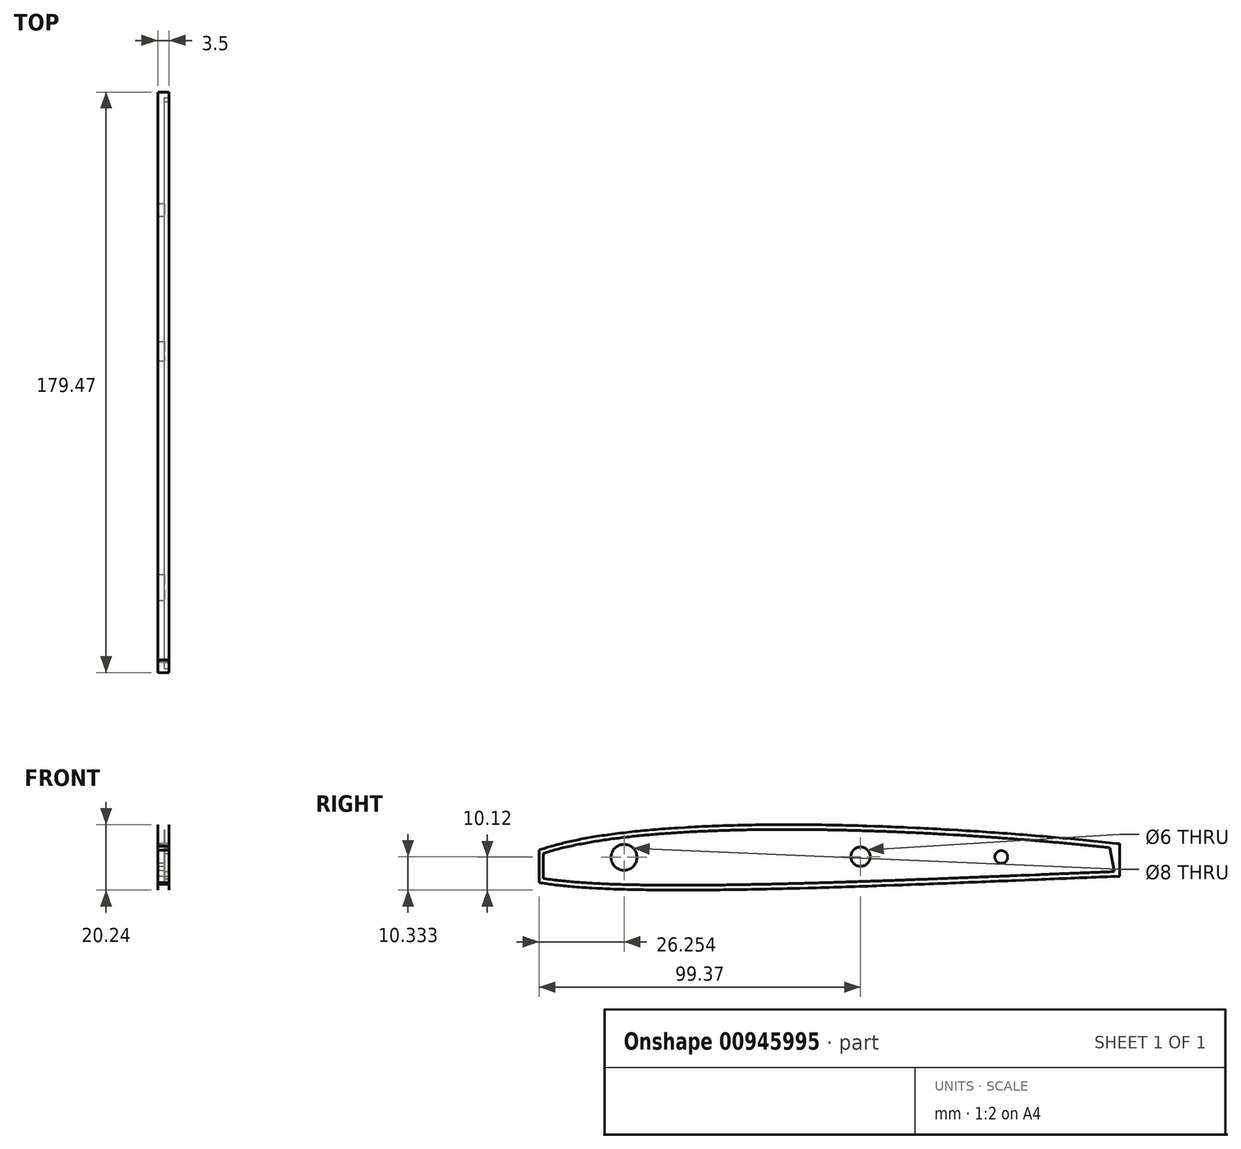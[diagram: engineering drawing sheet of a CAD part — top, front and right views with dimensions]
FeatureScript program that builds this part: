
annotation { "Feature Type Name" : "Feature", "Feature Type Description" : "" }
export const myFeature = defineFeature(function(context is Context, id is Id, definition is map)
    precondition{}
    {
        {
            var Q0;
            Q0=qCreatedBy(makeId("Right.planeOp"),FACE);
            var sketch = newSketch(context, id + "F0", { "sketchPlane" : qUnion([Q0])});
            skLineSegment(sketch, "E0", {"start": v(127, -3.95) * mm, "end": v(126.92, -3.95) * mm});
            skLineSegment(sketch, "E1", {"start": v(126.92, -3.95) * mm, "end": v(126.83, -3.94) * mm});
            skLineSegment(sketch, "E2", {"start": v(126.83, -3.94) * mm, "end": v(126.75, -3.93) * mm});
            skLineSegment(sketch, "E3", {"start": v(126.75, -3.93) * mm, "end": v(126.67, -3.93) * mm});
            skLineSegment(sketch, "E4", {"start": v(126.67, -3.93) * mm, "end": v(126.59, -3.92) * mm});
            skLineSegment(sketch, "E5", {"start": v(126.59, -3.92) * mm, "end": v(126.5, -3.91) * mm});
            skLineSegment(sketch, "E6", {"start": v(126.5, -3.91) * mm, "end": v(126.42, -3.9) * mm});
            skLineSegment(sketch, "E7", {"start": v(126.42, -3.9) * mm, "end": v(126.34, -3.9) * mm});
            skLineSegment(sketch, "E8", {"start": v(126.34, -3.9) * mm, "end": v(126.26, -3.9) * mm});
            skLineSegment(sketch, "E9", {"start": v(126.26, -3.9) * mm, "end": v(125.93, -3.86) * mm});
            skLineSegment(sketch, "E10", {"start": v(125.93, -3.86) * mm, "end": v(125.69, -3.84) * mm});
            skLineSegment(sketch, "E11", {"start": v(125.69, -3.84) * mm, "end": v(125.44, -3.82) * mm});
            skLineSegment(sketch, "E12", {"start": v(125.44, -3.82) * mm, "end": v(125.2, -3.8) * mm});
            skLineSegment(sketch, "E13", {"start": v(125.2, -3.8) * mm, "end": v(124.96, -3.77) * mm});
            skLineSegment(sketch, "E14", {"start": v(124.96, -3.77) * mm, "end": v(124.71, -3.75) * mm});
            skLineSegment(sketch, "E15", {"start": v(124.71, -3.75) * mm, "end": v(124.47, -3.72) * mm});
            skLineSegment(sketch, "E16", {"start": v(124.47, -3.72) * mm, "end": v(124.23, -3.7) * mm});
            skLineSegment(sketch, "E17", {"start": v(124.23, -3.7) * mm, "end": v(123.98, -3.67) * mm});
            skLineSegment(sketch, "E18", {"start": v(123.98, -3.67) * mm, "end": v(123.35, -3.6) * mm});
            skLineSegment(sketch, "E19", {"start": v(123.35, -3.6) * mm, "end": v(122.95, -3.56) * mm});
            skLineSegment(sketch, "E20", {"start": v(122.95, -3.56) * mm, "end": v(122.56, -3.52) * mm});
            skLineSegment(sketch, "E21", {"start": v(122.56, -3.52) * mm, "end": v(122.17, -3.48) * mm});
            skLineSegment(sketch, "E22", {"start": v(122.17, -3.48) * mm, "end": v(121.77, -3.43) * mm});
            skLineSegment(sketch, "E23", {"start": v(121.77, -3.43) * mm, "end": v(121.38, -3.39) * mm});
            skLineSegment(sketch, "E24", {"start": v(121.38, -3.39) * mm, "end": v(120.98, -3.34) * mm});
            skLineSegment(sketch, "E25", {"start": v(120.98, -3.34) * mm, "end": v(120.59, -3.3) * mm});
            skLineSegment(sketch, "E26", {"start": v(120.59, -3.3) * mm, "end": v(120.2, -3.25) * mm});
            skLineSegment(sketch, "E27", {"start": v(120.2, -3.25) * mm, "end": v(119.8, -3.2) * mm});
            skLineSegment(sketch, "E28", {"start": v(119.8, -3.2) * mm, "end": v(119.27, -3.14) * mm});
            skLineSegment(sketch, "E29", {"start": v(119.27, -3.14) * mm, "end": v(118.73, -3.07) * mm});
            skLineSegment(sketch, "E30", {"start": v(118.73, -3.07) * mm, "end": v(118.2, -3) * mm});
            skLineSegment(sketch, "E31", {"start": v(118.2, -3) * mm, "end": v(117.67, -2.94) * mm});
            skLineSegment(sketch, "E32", {"start": v(117.67, -2.94) * mm, "end": v(117.13, -2.87) * mm});
            skLineSegment(sketch, "E33", {"start": v(117.13, -2.87) * mm, "end": v(116.6, -2.8) * mm});
            skLineSegment(sketch, "E34", {"start": v(116.6, -2.8) * mm, "end": v(116.07, -2.74) * mm});
            skLineSegment(sketch, "E35", {"start": v(116.07, -2.74) * mm, "end": v(115.53, -2.67) * mm});
            skLineSegment(sketch, "E36", {"start": v(115.53, -2.67) * mm, "end": v(115, -2.6) * mm});
            skLineSegment(sketch, "E37", {"start": v(115, -2.6) * mm, "end": v(114.47, -2.54) * mm});
            skLineSegment(sketch, "E38", {"start": v(114.47, -2.54) * mm, "end": v(113.8, -2.45) * mm});
            skLineSegment(sketch, "E39", {"start": v(113.8, -2.45) * mm, "end": v(113.14, -2.37) * mm});
            skLineSegment(sketch, "E40", {"start": v(113.14, -2.37) * mm, "end": v(112.48, -2.28) * mm});
            skLineSegment(sketch, "E41", {"start": v(112.48, -2.28) * mm, "end": v(111.82, -2.2) * mm});
            skLineSegment(sketch, "E42", {"start": v(111.82, -2.2) * mm, "end": v(111.16, -2.1) * mm});
            skLineSegment(sketch, "E43", {"start": v(111.16, -2.1) * mm, "end": v(110.5, -2.02) * mm});
            skLineSegment(sketch, "E44", {"start": v(110.5, -2.02) * mm, "end": v(109.84, -1.93) * mm});
            skLineSegment(sketch, "E45", {"start": v(109.84, -1.93) * mm, "end": v(109.17, -1.84) * mm});
            skLineSegment(sketch, "E46", {"start": v(109.17, -1.84) * mm, "end": v(108.51, -1.75) * mm});
            skLineSegment(sketch, "E47", {"start": v(108.51, -1.75) * mm, "end": v(107.07, -1.56) * mm});
            skLineSegment(sketch, "E48", {"start": v(107.07, -1.56) * mm, "end": v(106.3, -1.46) * mm});
            skLineSegment(sketch, "E49", {"start": v(106.3, -1.46) * mm, "end": v(105.52, -1.35) * mm});
            skLineSegment(sketch, "E50", {"start": v(105.52, -1.35) * mm, "end": v(104.74, -1.25) * mm});
            skLineSegment(sketch, "E51", {"start": v(104.74, -1.25) * mm, "end": v(103.96, -1.14) * mm});
            skLineSegment(sketch, "E52", {"start": v(103.96, -1.14) * mm, "end": v(103.19, -1.04) * mm});
            skLineSegment(sketch, "E53", {"start": v(103.19, -1.04) * mm, "end": v(102.4, -0.93) * mm});
            skLineSegment(sketch, "E54", {"start": v(102.4, -0.93) * mm, "end": v(101.63, -0.82) * mm});
            skLineSegment(sketch, "E55", {"start": v(101.63, -0.82) * mm, "end": v(100.85, -0.72) * mm});
            skLineSegment(sketch, "E56", {"start": v(100.85, -0.72) * mm, "end": v(100.08, -0.61) * mm});
            skLineSegment(sketch, "E57", {"start": v(100.08, -0.61) * mm, "end": v(99.2, -0.5) * mm});
            skLineSegment(sketch, "E58", {"start": v(99.2, -0.5) * mm, "end": v(98.32, -0.38) * mm});
            skLineSegment(sketch, "E59", {"start": v(98.32, -0.38) * mm, "end": v(97.43, -0.26) * mm});
            skLineSegment(sketch, "E60", {"start": v(97.43, -0.26) * mm, "end": v(96.55, -0.14) * mm});
            skLineSegment(sketch, "E61", {"start": v(96.55, -0.14) * mm, "end": v(95.67, -0.02) * mm});
            skLineSegment(sketch, "E62", {"start": v(95.67, -0.02) * mm, "end": v(94.8, 0.1) * mm});
            skLineSegment(sketch, "E63", {"start": v(94.8, 0.1) * mm, "end": v(93.91, 0.22) * mm});
            skLineSegment(sketch, "E64", {"start": v(93.91, 0.22) * mm, "end": v(93.03, 0.34) * mm});
            skLineSegment(sketch, "E65", {"start": v(93.03, 0.34) * mm, "end": v(92.15, 0.45) * mm});
            skLineSegment(sketch, "E66", {"start": v(92.15, 0.45) * mm, "end": v(90.3, 0.7) * mm});
            skLineSegment(sketch, "E67", {"start": v(90.3, 0.7) * mm, "end": v(89.33, 0.83) * mm});
            skLineSegment(sketch, "E68", {"start": v(89.33, 0.83) * mm, "end": v(88.36, 0.96) * mm});
            skLineSegment(sketch, "E69", {"start": v(88.36, 0.96) * mm, "end": v(87.39, 1.09) * mm});
            skLineSegment(sketch, "E70", {"start": v(87.39, 1.09) * mm, "end": v(86.42, 1.22) * mm});
            skLineSegment(sketch, "E71", {"start": v(86.42, 1.22) * mm, "end": v(85.44, 1.34) * mm});
            skLineSegment(sketch, "E72", {"start": v(85.44, 1.34) * mm, "end": v(84.47, 1.47) * mm});
            skLineSegment(sketch, "E73", {"start": v(84.47, 1.47) * mm, "end": v(83.5, 1.6) * mm});
            skLineSegment(sketch, "E74", {"start": v(83.5, 1.6) * mm, "end": v(82.53, 1.72) * mm});
            skLineSegment(sketch, "E75", {"start": v(82.53, 1.72) * mm, "end": v(81.56, 1.85) * mm});
            skLineSegment(sketch, "E76", {"start": v(81.56, 1.85) * mm, "end": v(80.51, 1.98) * mm});
            skLineSegment(sketch, "E77", {"start": v(80.51, 1.98) * mm, "end": v(79.46, 2.12) * mm});
            skLineSegment(sketch, "E78", {"start": v(79.46, 2.12) * mm, "end": v(78.41, 2.25) * mm});
            skLineSegment(sketch, "E79", {"start": v(78.41, 2.25) * mm, "end": v(77.36, 2.38) * mm});
            skLineSegment(sketch, "E80", {"start": v(77.36, 2.38) * mm, "end": v(76.31, 2.51) * mm});
            skLineSegment(sketch, "E81", {"start": v(76.31, 2.51) * mm, "end": v(75.26, 2.64) * mm});
            skLineSegment(sketch, "E82", {"start": v(75.26, 2.64) * mm, "end": v(74.21, 2.77) * mm});
            skLineSegment(sketch, "E83", {"start": v(74.21, 2.77) * mm, "end": v(73.17, 2.9) * mm});
            skLineSegment(sketch, "E84", {"start": v(73.17, 2.9) * mm, "end": v(72.12, 3.03) * mm});
            skLineSegment(sketch, "E85", {"start": v(72.12, 3.03) * mm, "end": v(69.95, 3.29) * mm});
            skLineSegment(sketch, "E86", {"start": v(69.95, 3.29) * mm, "end": v(68.83, 3.42) * mm});
            skLineSegment(sketch, "E87", {"start": v(68.83, 3.42) * mm, "end": v(67.72, 3.55) * mm});
            skLineSegment(sketch, "E88", {"start": v(67.72, 3.55) * mm, "end": v(66.6, 3.68) * mm});
            skLineSegment(sketch, "E89", {"start": v(66.6, 3.68) * mm, "end": v(65.48, 3.8) * mm});
            skLineSegment(sketch, "E90", {"start": v(65.48, 3.8) * mm, "end": v(64.37, 3.93) * mm});
            skLineSegment(sketch, "E91", {"start": v(64.37, 3.93) * mm, "end": v(63.25, 4.06) * mm});
            skLineSegment(sketch, "E92", {"start": v(63.25, 4.06) * mm, "end": v(62.14, 4.18) * mm});
            skLineSegment(sketch, "E93", {"start": v(62.14, 4.18) * mm, "end": v(61.02, 4.3) * mm});
            skLineSegment(sketch, "E94", {"start": v(61.02, 4.3) * mm, "end": v(58.73, 4.55) * mm});
            skLineSegment(sketch, "E95", {"start": v(58.73, 4.55) * mm, "end": v(57.56, 4.68) * mm});
            skLineSegment(sketch, "E96", {"start": v(57.56, 4.68) * mm, "end": v(56.38, 4.8) * mm});
            skLineSegment(sketch, "E97", {"start": v(56.38, 4.8) * mm, "end": v(55.21, 4.92) * mm});
            skLineSegment(sketch, "E98", {"start": v(55.21, 4.92) * mm, "end": v(54.04, 5.04) * mm});
            skLineSegment(sketch, "E99", {"start": v(54.04, 5.04) * mm, "end": v(52.86, 5.16) * mm});
            skLineSegment(sketch, "E100", {"start": v(52.86, 5.16) * mm, "end": v(51.7, 5.27) * mm});
            skLineSegment(sketch, "E101", {"start": v(51.7, 5.27) * mm, "end": v(50.52, 5.39) * mm});
            skLineSegment(sketch, "E102", {"start": v(50.52, 5.39) * mm, "end": v(49.34, 5.5) * mm});
            skLineSegment(sketch, "E103", {"start": v(49.34, 5.5) * mm, "end": v(48.17, 5.61) * mm});
            skLineSegment(sketch, "E104", {"start": v(48.17, 5.61) * mm, "end": v(46.95, 5.73) * mm});
            skLineSegment(sketch, "E105", {"start": v(46.95, 5.73) * mm, "end": v(45.73, 5.84) * mm});
            skLineSegment(sketch, "E106", {"start": v(45.73, 5.84) * mm, "end": v(44.51, 5.95) * mm});
            skLineSegment(sketch, "E107", {"start": v(44.51, 5.95) * mm, "end": v(43.3, 6.06) * mm});
            skLineSegment(sketch, "E108", {"start": v(43.3, 6.06) * mm, "end": v(42.07, 6.17) * mm});
            skLineSegment(sketch, "E109", {"start": v(42.07, 6.17) * mm, "end": v(40.85, 6.28) * mm});
            skLineSegment(sketch, "E110", {"start": v(40.85, 6.28) * mm, "end": v(39.63, 6.39) * mm});
            skLineSegment(sketch, "E111", {"start": v(39.63, 6.39) * mm, "end": v(38.41, 6.5) * mm});
            skLineSegment(sketch, "E112", {"start": v(38.41, 6.5) * mm, "end": v(37.2, 6.6) * mm});
            skLineSegment(sketch, "E113", {"start": v(37.2, 6.6) * mm, "end": v(35.97, 6.7) * mm});
            skLineSegment(sketch, "E114", {"start": v(35.97, 6.7) * mm, "end": v(34.72, 6.8) * mm});
            skLineSegment(sketch, "E115", {"start": v(34.72, 6.8) * mm, "end": v(33.46, 6.9) * mm});
            skLineSegment(sketch, "E116", {"start": v(33.46, 6.9) * mm, "end": v(32.2, 7) * mm});
            skLineSegment(sketch, "E117", {"start": v(32.2, 7) * mm, "end": v(30.95, 7.1) * mm});
            skLineSegment(sketch, "E118", {"start": v(30.95, 7.1) * mm, "end": v(29.7, 7.2) * mm});
            skLineSegment(sketch, "E119", {"start": v(29.7, 7.2) * mm, "end": v(28.44, 7.29) * mm});
            skLineSegment(sketch, "E120", {"start": v(28.44, 7.29) * mm, "end": v(27.19, 7.38) * mm});
            skLineSegment(sketch, "E121", {"start": v(27.19, 7.38) * mm, "end": v(25.93, 7.47) * mm});
            skLineSegment(sketch, "E122", {"start": v(25.93, 7.47) * mm, "end": v(24.68, 7.56) * mm});
            skLineSegment(sketch, "E123", {"start": v(24.68, 7.56) * mm, "end": v(23.42, 7.65) * mm});
            skLineSegment(sketch, "E124", {"start": v(23.42, 7.65) * mm, "end": v(22.15, 7.74) * mm});
            skLineSegment(sketch, "E125", {"start": v(22.15, 7.74) * mm, "end": v(20.87, 7.83) * mm});
            skLineSegment(sketch, "E126", {"start": v(20.87, 7.83) * mm, "end": v(19.6, 7.91) * mm});
            skLineSegment(sketch, "E127", {"start": v(19.6, 7.91) * mm, "end": v(18.31, 8) * mm});
            skLineSegment(sketch, "E128", {"start": v(18.31, 8) * mm, "end": v(17.04, 8.08) * mm});
            skLineSegment(sketch, "E129", {"start": v(17.04, 8.08) * mm, "end": v(15.76, 8.16) * mm});
            skLineSegment(sketch, "E130", {"start": v(15.76, 8.16) * mm, "end": v(14.48, 8.24) * mm});
            skLineSegment(sketch, "E131", {"start": v(14.48, 8.24) * mm, "end": v(13.2, 8.32) * mm});
            skLineSegment(sketch, "E132", {"start": v(13.2, 8.32) * mm, "end": v(11.93, 8.4) * mm});
            skLineSegment(sketch, "E133", {"start": v(11.93, 8.4) * mm, "end": v(9.37, 8.55) * mm});
            skLineSegment(sketch, "E134", {"start": v(9.37, 8.55) * mm, "end": v(8.08, 8.63) * mm});
            skLineSegment(sketch, "E135", {"start": v(8.08, 8.63) * mm, "end": v(6.8, 8.7) * mm});
            skLineSegment(sketch, "E136", {"start": v(6.8, 8.7) * mm, "end": v(5.51, 8.77) * mm});
            skLineSegment(sketch, "E137", {"start": v(5.51, 8.77) * mm, "end": v(4.23, 8.84) * mm});
            skLineSegment(sketch, "E138", {"start": v(4.23, 8.84) * mm, "end": v(2.94, 8.9) * mm});
            skLineSegment(sketch, "E139", {"start": v(2.94, 8.9) * mm, "end": v(1.66, 8.97) * mm});
            skLineSegment(sketch, "E140", {"start": v(1.66, 8.97) * mm, "end": v(0.38, 9.04) * mm});
            skLineSegment(sketch, "E141", {"start": v(0.38, 9.04) * mm, "end": v(-0.9, 9.1) * mm});
            skLineSegment(sketch, "E142", {"start": v(-0.9, 9.1) * mm, "end": v(-3.47, 9.22) * mm});
            skLineSegment(sketch, "E143", {"start": v(-3.47, 9.22) * mm, "end": v(-4.75, 9.28) * mm});
            skLineSegment(sketch, "E144", {"start": v(-4.75, 9.28) * mm, "end": v(-6.02, 9.33) * mm});
            skLineSegment(sketch, "E145", {"start": v(-6.02, 9.33) * mm, "end": v(-7.3, 9.39) * mm});
            skLineSegment(sketch, "E146", {"start": v(-7.3, 9.39) * mm, "end": v(-8.58, 9.44) * mm});
            skLineSegment(sketch, "E147", {"start": v(-8.58, 9.44) * mm, "end": v(-9.86, 9.5) * mm});
            skLineSegment(sketch, "E148", {"start": v(-9.86, 9.5) * mm, "end": v(-11.14, 9.54) * mm});
            skLineSegment(sketch, "E149", {"start": v(-11.14, 9.54) * mm, "end": v(-12.41, 9.59) * mm});
            skLineSegment(sketch, "E150", {"start": v(-12.41, 9.59) * mm, "end": v(-13.7, 9.63) * mm});
            skLineSegment(sketch, "E151", {"start": v(-13.7, 9.63) * mm, "end": v(-16.23, 9.71) * mm});
            skLineSegment(sketch, "E152", {"start": v(-16.23, 9.71) * mm, "end": v(-17.49, 9.75) * mm});
            skLineSegment(sketch, "E153", {"start": v(-17.49, 9.75) * mm, "end": v(-18.74, 9.79) * mm});
            skLineSegment(sketch, "E154", {"start": v(-18.74, 9.79) * mm, "end": v(-20, 9.82) * mm});
            skLineSegment(sketch, "E155", {"start": v(-20, 9.82) * mm, "end": v(-21.26, 9.86) * mm});
            skLineSegment(sketch, "E156", {"start": v(-21.26, 9.86) * mm, "end": v(-22.52, 9.89) * mm});
            skLineSegment(sketch, "E157", {"start": v(-22.52, 9.89) * mm, "end": v(-23.78, 9.92) * mm});
            skLineSegment(sketch, "E158", {"start": v(-23.78, 9.92) * mm, "end": v(-25.04, 9.94) * mm});
            skLineSegment(sketch, "E159", {"start": v(-25.04, 9.94) * mm, "end": v(-26.3, 9.97) * mm});
            skLineSegment(sketch, "E160", {"start": v(-26.3, 9.97) * mm, "end": v(-28.78, 10.01) * mm});
            skLineSegment(sketch, "E161", {"start": v(-28.78, 10.01) * mm, "end": v(-30.01, 10.03) * mm});
            skLineSegment(sketch, "E162", {"start": v(-30.01, 10.03) * mm, "end": v(-31.24, 10.05) * mm});
            skLineSegment(sketch, "E163", {"start": v(-31.24, 10.05) * mm, "end": v(-32.47, 10.07) * mm});
            skLineSegment(sketch, "E164", {"start": v(-32.47, 10.07) * mm, "end": v(-33.7, 10.08) * mm});
            skLineSegment(sketch, "E165", {"start": v(-33.7, 10.08) * mm, "end": v(-34.92, 10.1) * mm});
            skLineSegment(sketch, "E166", {"start": v(-34.92, 10.1) * mm, "end": v(-36.15, 10.1) * mm});
            skLineSegment(sketch, "E167", {"start": v(-36.15, 10.1) * mm, "end": v(-37.38, 10.1) * mm});
            skLineSegment(sketch, "E168", {"start": v(-37.38, 10.1) * mm, "end": v(-38.6, 10.11) * mm});
            skLineSegment(sketch, "E169", {"start": v(-38.6, 10.11) * mm, "end": v(-39.83, 10.12) * mm});
            skLineSegment(sketch, "E170", {"start": v(-39.83, 10.12) * mm, "end": v(-41.01, 10.12) * mm});
            skLineSegment(sketch, "E171", {"start": v(-41.01, 10.12) * mm, "end": v(-42.2, 10.12) * mm});
            skLineSegment(sketch, "E172", {"start": v(-42.2, 10.12) * mm, "end": v(-43.38, 10.11) * mm});
            skLineSegment(sketch, "E173", {"start": v(-43.38, 10.11) * mm, "end": v(-44.56, 10.1) * mm});
            skLineSegment(sketch, "E174", {"start": v(-44.56, 10.1) * mm, "end": v(-45.74, 10.1) * mm});
            skLineSegment(sketch, "E175", {"start": v(-45.74, 10.1) * mm, "end": v(-46.93, 10.09) * mm});
            skLineSegment(sketch, "E176", {"start": v(-46.93, 10.09) * mm, "end": v(-48.1, 10.08) * mm});
            skLineSegment(sketch, "E177", {"start": v(-48.1, 10.08) * mm, "end": v(-49.3, 10.06) * mm});
            skLineSegment(sketch, "E178", {"start": v(-49.3, 10.06) * mm, "end": v(-50.47, 10.05) * mm});
            skLineSegment(sketch, "E179", {"start": v(-50.47, 10.05) * mm, "end": v(-51.66, 10.03) * mm});
            skLineSegment(sketch, "E180", {"start": v(-51.66, 10.03) * mm, "end": v(-52.78, 10) * mm});
            skLineSegment(sketch, "E181", {"start": v(-52.78, 10) * mm, "end": v(-53.91, 9.98) * mm});
            skLineSegment(sketch, "E182", {"start": v(-53.91, 9.98) * mm, "end": v(-55.04, 9.96) * mm});
            skLineSegment(sketch, "E183", {"start": v(-55.04, 9.96) * mm, "end": v(-56.17, 9.93) * mm});
            skLineSegment(sketch, "E184", {"start": v(-56.17, 9.93) * mm, "end": v(-57.3, 9.9) * mm});
            skLineSegment(sketch, "E185", {"start": v(-57.3, 9.9) * mm, "end": v(-58.42, 9.87) * mm});
            skLineSegment(sketch, "E186", {"start": v(-58.42, 9.87) * mm, "end": v(-59.55, 9.83) * mm});
            skLineSegment(sketch, "E187", {"start": v(-59.55, 9.83) * mm, "end": v(-60.68, 9.8) * mm});
            skLineSegment(sketch, "E188", {"start": v(-60.68, 9.8) * mm, "end": v(-61.8, 9.76) * mm});
            skLineSegment(sketch, "E189", {"start": v(-61.8, 9.76) * mm, "end": v(-62.93, 9.72) * mm});
            skLineSegment(sketch, "E190", {"start": v(-62.93, 9.72) * mm, "end": v(-64, 9.68) * mm});
            skLineSegment(sketch, "E191", {"start": v(-64, 9.68) * mm, "end": v(-65.05, 9.63) * mm});
            skLineSegment(sketch, "E192", {"start": v(-65.05, 9.63) * mm, "end": v(-66.11, 9.59) * mm});
            skLineSegment(sketch, "E193", {"start": v(-66.11, 9.59) * mm, "end": v(-67.18, 9.54) * mm});
            skLineSegment(sketch, "E194", {"start": v(-67.18, 9.54) * mm, "end": v(-68.24, 9.49) * mm});
            skLineSegment(sketch, "E195", {"start": v(-68.24, 9.49) * mm, "end": v(-69.3, 9.43) * mm});
            skLineSegment(sketch, "E196", {"start": v(-69.3, 9.43) * mm, "end": v(-70.36, 9.38) * mm});
            skLineSegment(sketch, "E197", {"start": v(-70.36, 9.38) * mm, "end": v(-71.42, 9.32) * mm});
            skLineSegment(sketch, "E198", {"start": v(-71.42, 9.32) * mm, "end": v(-72.48, 9.26) * mm});
            skLineSegment(sketch, "E199", {"start": v(-72.48, 9.26) * mm, "end": v(-74.53, 9.13) * mm});
            skLineSegment(sketch, "E200", {"start": v(-74.53, 9.13) * mm, "end": v(-75.51, 9.07) * mm});
            skLineSegment(sketch, "E201", {"start": v(-75.51, 9.07) * mm, "end": v(-76.5, 9) * mm});
            skLineSegment(sketch, "E202", {"start": v(-76.5, 9) * mm, "end": v(-77.48, 8.93) * mm});
            skLineSegment(sketch, "E203", {"start": v(-77.48, 8.93) * mm, "end": v(-78.46, 8.86) * mm});
            skLineSegment(sketch, "E204", {"start": v(-78.46, 8.86) * mm, "end": v(-79.45, 8.79) * mm});
            skLineSegment(sketch, "E205", {"start": v(-79.45, 8.79) * mm, "end": v(-80.43, 8.71) * mm});
            skLineSegment(sketch, "E206", {"start": v(-80.43, 8.71) * mm, "end": v(-81.42, 8.63) * mm});
            skLineSegment(sketch, "E207", {"start": v(-81.42, 8.63) * mm, "end": v(-82.4, 8.55) * mm});
            skLineSegment(sketch, "E208", {"start": v(-82.4, 8.55) * mm, "end": v(-84.28, 8.38) * mm});
            skLineSegment(sketch, "E209", {"start": v(-84.28, 8.38) * mm, "end": v(-85.18, 8.3) * mm});
            skLineSegment(sketch, "E210", {"start": v(-85.18, 8.3) * mm, "end": v(-86.08, 8.2) * mm});
            skLineSegment(sketch, "E211", {"start": v(-86.08, 8.2) * mm, "end": v(-86.98, 8.11) * mm});
            skLineSegment(sketch, "E212", {"start": v(-86.98, 8.11) * mm, "end": v(-87.88, 8.02) * mm});
            skLineSegment(sketch, "E213", {"start": v(-87.88, 8.02) * mm, "end": v(-88.77, 7.92) * mm});
            skLineSegment(sketch, "E214", {"start": v(-88.77, 7.92) * mm, "end": v(-89.67, 7.82) * mm});
            skLineSegment(sketch, "E215", {"start": v(-89.67, 7.82) * mm, "end": v(-90.57, 7.72) * mm});
            skLineSegment(sketch, "E216", {"start": v(-90.57, 7.72) * mm, "end": v(-91.47, 7.61) * mm});
            skLineSegment(sketch, "E217", {"start": v(-91.47, 7.61) * mm, "end": v(-92.37, 7.5) * mm});
            skLineSegment(sketch, "E218", {"start": v(-92.37, 7.5) * mm, "end": v(-93.17, 7.4) * mm});
            skLineSegment(sketch, "E219", {"start": v(-93.17, 7.4) * mm, "end": v(-93.98, 7.3) * mm});
            skLineSegment(sketch, "E220", {"start": v(-93.98, 7.3) * mm, "end": v(-94.78, 7.2) * mm});
            skLineSegment(sketch, "E221", {"start": v(-94.78, 7.2) * mm, "end": v(-95.59, 7.08) * mm});
            skLineSegment(sketch, "E222", {"start": v(-95.59, 7.08) * mm, "end": v(-96.4, 6.97) * mm});
            skLineSegment(sketch, "E223", {"start": v(-96.4, 6.97) * mm, "end": v(-97.2, 6.85) * mm});
            skLineSegment(sketch, "E224", {"start": v(-97.2, 6.85) * mm, "end": v(-98, 6.73) * mm});
            skLineSegment(sketch, "E225", {"start": v(-98, 6.73) * mm, "end": v(-98.81, 6.6) * mm});
            skLineSegment(sketch, "E226", {"start": v(-98.81, 6.6) * mm, "end": v(-99.62, 6.48) * mm});
            skLineSegment(sketch, "E227", {"start": v(-99.62, 6.48) * mm, "end": v(-100.42, 6.35) * mm});
            skLineSegment(sketch, "E228", {"start": v(-100.42, 6.35) * mm, "end": v(-101.13, 6.23) * mm});
            skLineSegment(sketch, "E229", {"start": v(-101.13, 6.23) * mm, "end": v(-101.83, 6.1) * mm});
            skLineSegment(sketch, "E230", {"start": v(-101.83, 6.1) * mm, "end": v(-102.54, 5.98) * mm});
            skLineSegment(sketch, "E231", {"start": v(-102.54, 5.98) * mm, "end": v(-103.25, 5.85) * mm});
            skLineSegment(sketch, "E232", {"start": v(-103.25, 5.85) * mm, "end": v(-103.95, 5.72) * mm});
            skLineSegment(sketch, "E233", {"start": v(-103.95, 5.72) * mm, "end": v(-104.66, 5.59) * mm});
            skLineSegment(sketch, "E234", {"start": v(-104.66, 5.59) * mm, "end": v(-105.37, 5.45) * mm});
            skLineSegment(sketch, "E235", {"start": v(-105.37, 5.45) * mm, "end": v(-106.07, 5.3) * mm});
            skLineSegment(sketch, "E236", {"start": v(-106.07, 5.3) * mm, "end": v(-106.78, 5.16) * mm});
            skLineSegment(sketch, "E237", {"start": v(-106.78, 5.16) * mm, "end": v(-108.09, 4.87) * mm});
            skLineSegment(sketch, "E238", {"start": v(-108.09, 4.87) * mm, "end": v(-108.69, 4.73) * mm});
            skLineSegment(sketch, "E239", {"start": v(-108.69, 4.73) * mm, "end": v(-109.3, 4.6) * mm});
            skLineSegment(sketch, "E240", {"start": v(-109.3, 4.6) * mm, "end": v(-109.9, 4.45) * mm});
            skLineSegment(sketch, "E241", {"start": v(-109.9, 4.45) * mm, "end": v(-110.5, 4.3) * mm});
            skLineSegment(sketch, "E242", {"start": v(-110.5, 4.3) * mm, "end": v(-111.1, 4.15) * mm});
            skLineSegment(sketch, "E243", {"start": v(-111.1, 4.15) * mm, "end": v(-111.7, 4) * mm});
            skLineSegment(sketch, "E244", {"start": v(-111.7, 4) * mm, "end": v(-112.3, 3.84) * mm});
            skLineSegment(sketch, "E245", {"start": v(-112.3, 3.84) * mm, "end": v(-112.9, 3.67) * mm});
            skLineSegment(sketch, "E246", {"start": v(-112.9, 3.67) * mm, "end": v(-113.5, 3.5) * mm});
            skLineSegment(sketch, "E247", {"start": v(-113.5, 3.5) * mm, "end": v(-114, 3.36) * mm});
            skLineSegment(sketch, "E248", {"start": v(-114, 3.36) * mm, "end": v(-114.5, 3.21) * mm});
            skLineSegment(sketch, "E249", {"start": v(-114.5, 3.21) * mm, "end": v(-115, 3.06) * mm});
            skLineSegment(sketch, "E250", {"start": v(-115, 3.06) * mm, "end": v(-115.49, 2.9) * mm});
            skLineSegment(sketch, "E251", {"start": v(-115.49, 2.9) * mm, "end": v(-115.98, 2.74) * mm});
            skLineSegment(sketch, "E252", {"start": v(-115.98, 2.74) * mm, "end": v(-116.48, 2.58) * mm});
            skLineSegment(sketch, "E253", {"start": v(-116.48, 2.58) * mm, "end": v(-116.97, 2.41) * mm});
            skLineSegment(sketch, "E254", {"start": v(-116.97, 2.41) * mm, "end": v(-117.47, 2.24) * mm});
            skLineSegment(sketch, "E255", {"start": v(-117.47, 2.24) * mm, "end": v(-117.96, 2.06) * mm});
            skLineSegment(sketch, "E256", {"start": v(-117.96, 2.06) * mm, "end": v(-118.46, 1.88) * mm});
            skLineSegment(sketch, "E257", {"start": v(-118.46, 1.88) * mm, "end": v(-118.9, 1.71) * mm});
            skLineSegment(sketch, "E258", {"start": v(-118.9, 1.71) * mm, "end": v(-119.32, 1.54) * mm});
            skLineSegment(sketch, "E259", {"start": v(-119.32, 1.54) * mm, "end": v(-119.74, 1.37) * mm});
            skLineSegment(sketch, "E260", {"start": v(-119.74, 1.37) * mm, "end": v(-120.14, 1.2) * mm});
            skLineSegment(sketch, "E261", {"start": v(-120.14, 1.2) * mm, "end": v(-120.53, 1.03) * mm});
            skLineSegment(sketch, "E262", {"start": v(-120.53, 1.03) * mm, "end": v(-120.9, 0.86) * mm});
            skLineSegment(sketch, "E263", {"start": v(-120.9, 0.86) * mm, "end": v(-121.27, 0.7) * mm});
            skLineSegment(sketch, "E264", {"start": v(-121.27, 0.7) * mm, "end": v(-121.63, 0.53) * mm});
            skLineSegment(sketch, "E265", {"start": v(-121.63, 0.53) * mm, "end": v(-121.97, 0.36) * mm});
            skLineSegment(sketch, "E266", {"start": v(-121.97, 0.36) * mm, "end": v(-122.3, 0.19) * mm});
            skLineSegment(sketch, "E267", {"start": v(-122.3, 0.19) * mm, "end": v(-122.62, 0.02) * mm});
            skLineSegment(sketch, "E268", {"start": v(-122.62, 0.02) * mm, "end": v(-122.93, -0.15) * mm});
            skLineSegment(sketch, "E269", {"start": v(-122.93, -0.15) * mm, "end": v(-123.23, -0.32) * mm});
            skLineSegment(sketch, "E270", {"start": v(-123.23, -0.32) * mm, "end": v(-123.52, -0.49) * mm});
            skLineSegment(sketch, "E271", {"start": v(-123.52, -0.49) * mm, "end": v(-123.8, -0.66) * mm});
            skLineSegment(sketch, "E272", {"start": v(-123.8, -0.66) * mm, "end": v(-124.06, -0.83) * mm});
            skLineSegment(sketch, "E273", {"start": v(-124.06, -0.83) * mm, "end": v(-124.32, -1) * mm});
            skLineSegment(sketch, "E274", {"start": v(-124.32, -1) * mm, "end": v(-124.57, -1.16) * mm});
            skLineSegment(sketch, "E275", {"start": v(-124.57, -1.16) * mm, "end": v(-124.81, -1.33) * mm});
            skLineSegment(sketch, "E276", {"start": v(-124.81, -1.33) * mm, "end": v(-125.04, -1.5) * mm});
            skLineSegment(sketch, "E277", {"start": v(-125.04, -1.5) * mm, "end": v(-125.24, -1.66) * mm});
            skLineSegment(sketch, "E278", {"start": v(-125.24, -1.66) * mm, "end": v(-125.43, -1.81) * mm});
            skLineSegment(sketch, "E279", {"start": v(-125.43, -1.81) * mm, "end": v(-125.6, -1.97) * mm});
            skLineSegment(sketch, "E280", {"start": v(-125.6, -1.97) * mm, "end": v(-125.78, -2.13) * mm});
            skLineSegment(sketch, "E281", {"start": v(-125.78, -2.13) * mm, "end": v(-125.95, -2.28) * mm});
            skLineSegment(sketch, "E282", {"start": v(-125.95, -2.28) * mm, "end": v(-126.1, -2.44) * mm});
            skLineSegment(sketch, "E283", {"start": v(-126.1, -2.44) * mm, "end": v(-126.26, -2.6) * mm});
            skLineSegment(sketch, "E284", {"start": v(-126.26, -2.6) * mm, "end": v(-126.4, -2.75) * mm});
            skLineSegment(sketch, "E285", {"start": v(-126.4, -2.75) * mm, "end": v(-126.52, -2.91) * mm});
            skLineSegment(sketch, "E286", {"start": v(-126.52, -2.91) * mm, "end": v(-126.64, -3.07) * mm});
            skLineSegment(sketch, "E287", {"start": v(-126.64, -3.07) * mm, "end": v(-126.7, -3.16) * mm});
            skLineSegment(sketch, "E288", {"start": v(-126.7, -3.16) * mm, "end": v(-126.76, -3.24) * mm});
            skLineSegment(sketch, "E289", {"start": v(-126.76, -3.24) * mm, "end": v(-126.81, -3.33) * mm});
            skLineSegment(sketch, "E290", {"start": v(-126.81, -3.33) * mm, "end": v(-126.86, -3.42) * mm});
            skLineSegment(sketch, "E291", {"start": v(-126.86, -3.42) * mm, "end": v(-126.9, -3.51) * mm});
            skLineSegment(sketch, "E292", {"start": v(-126.9, -3.51) * mm, "end": v(-126.93, -3.6) * mm});
            skLineSegment(sketch, "E293", {"start": v(-126.93, -3.6) * mm, "end": v(-126.96, -3.69) * mm});
            skLineSegment(sketch, "E294", {"start": v(-126.96, -3.69) * mm, "end": v(-126.98, -3.78) * mm});
            skLineSegment(sketch, "E295", {"start": v(-126.98, -3.78) * mm, "end": v(-127, -3.87) * mm});
            skLineSegment(sketch, "E296", {"start": v(-127, -3.87) * mm, "end": v(-127, -3.95) * mm});
            skLineSegment(sketch, "E297", {"start": v(-127, -3.95) * mm, "end": v(-127, -3.99) * mm});
            skLineSegment(sketch, "E298", {"start": v(-127, -3.99) * mm, "end": v(-127, -4.02) * mm});
            skLineSegment(sketch, "E299", {"start": v(-127, -4.02) * mm, "end": v(-127, -4.06) * mm});
            skLineSegment(sketch, "E300", {"start": v(-127, -4.06) * mm, "end": v(-127, -4.1) * mm});
            skLineSegment(sketch, "E301", {"start": v(-127, -4.1) * mm, "end": v(-126.99, -4.13) * mm});
            skLineSegment(sketch, "E302", {"start": v(-126.99, -4.13) * mm, "end": v(-126.98, -4.16) * mm});
            skLineSegment(sketch, "E303", {"start": v(-126.98, -4.16) * mm, "end": v(-126.97, -4.2) * mm});
            skLineSegment(sketch, "E304", {"start": v(-126.97, -4.2) * mm, "end": v(-126.96, -4.23) * mm});
            skLineSegment(sketch, "E305", {"start": v(-126.96, -4.23) * mm, "end": v(-126.95, -4.27) * mm});
            skLineSegment(sketch, "E306", {"start": v(-126.95, -4.27) * mm, "end": v(-126.94, -4.3) * mm});
            skLineSegment(sketch, "E307", {"start": v(-126.94, -4.3) * mm, "end": v(-126.89, -4.4) * mm});
            skLineSegment(sketch, "E308", {"start": v(-126.89, -4.4) * mm, "end": v(-126.82, -4.51) * mm});
            skLineSegment(sketch, "E309", {"start": v(-126.82, -4.51) * mm, "end": v(-126.74, -4.62) * mm});
            skLineSegment(sketch, "E310", {"start": v(-126.74, -4.62) * mm, "end": v(-126.65, -4.72) * mm});
            skLineSegment(sketch, "E311", {"start": v(-126.65, -4.72) * mm, "end": v(-126.54, -4.83) * mm});
            skLineSegment(sketch, "E312", {"start": v(-126.54, -4.83) * mm, "end": v(-126.41, -4.93) * mm});
            skLineSegment(sketch, "E313", {"start": v(-126.41, -4.93) * mm, "end": v(-126.27, -5.04) * mm});
            skLineSegment(sketch, "E314", {"start": v(-126.27, -5.04) * mm, "end": v(-126.12, -5.14) * mm});
            skLineSegment(sketch, "E315", {"start": v(-126.12, -5.14) * mm, "end": v(-125.95, -5.25) * mm});
            skLineSegment(sketch, "E316", {"start": v(-125.95, -5.25) * mm, "end": v(-125.77, -5.35) * mm});
            skLineSegment(sketch, "E317", {"start": v(-125.77, -5.35) * mm, "end": v(-125.58, -5.46) * mm});
            skLineSegment(sketch, "E318", {"start": v(-125.58, -5.46) * mm, "end": v(-125.37, -5.57) * mm});
            skLineSegment(sketch, "E319", {"start": v(-125.37, -5.57) * mm, "end": v(-125.15, -5.67) * mm});
            skLineSegment(sketch, "E320", {"start": v(-125.15, -5.67) * mm, "end": v(-124.92, -5.78) * mm});
            skLineSegment(sketch, "E321", {"start": v(-124.92, -5.78) * mm, "end": v(-124.67, -5.89) * mm});
            skLineSegment(sketch, "E322", {"start": v(-124.67, -5.89) * mm, "end": v(-124.4, -6) * mm});
            skLineSegment(sketch, "E323", {"start": v(-124.4, -6) * mm, "end": v(-124.13, -6.1) * mm});
            skLineSegment(sketch, "E324", {"start": v(-124.13, -6.1) * mm, "end": v(-123.84, -6.2) * mm});
            skLineSegment(sketch, "E325", {"start": v(-123.84, -6.2) * mm, "end": v(-123.53, -6.32) * mm});
            skLineSegment(sketch, "E326", {"start": v(-123.53, -6.32) * mm, "end": v(-123.21, -6.42) * mm});
            skLineSegment(sketch, "E327", {"start": v(-123.21, -6.42) * mm, "end": v(-122.9, -6.52) * mm});
            skLineSegment(sketch, "E328", {"start": v(-122.9, -6.52) * mm, "end": v(-122.57, -6.62) * mm});
            skLineSegment(sketch, "E329", {"start": v(-122.57, -6.62) * mm, "end": v(-122.22, -6.72) * mm});
            skLineSegment(sketch, "E330", {"start": v(-122.22, -6.72) * mm, "end": v(-121.86, -6.82) * mm});
            skLineSegment(sketch, "E331", {"start": v(-121.86, -6.82) * mm, "end": v(-121.49, -6.92) * mm});
            skLineSegment(sketch, "E332", {"start": v(-121.49, -6.92) * mm, "end": v(-121.1, -7.02) * mm});
            skLineSegment(sketch, "E333", {"start": v(-121.1, -7.02) * mm, "end": v(-120.7, -7.12) * mm});
            skLineSegment(sketch, "E334", {"start": v(-120.7, -7.12) * mm, "end": v(-120.27, -7.22) * mm});
            skLineSegment(sketch, "E335", {"start": v(-120.27, -7.22) * mm, "end": v(-119.82, -7.31) * mm});
            skLineSegment(sketch, "E336", {"start": v(-119.82, -7.31) * mm, "end": v(-119.36, -7.41) * mm});
            skLineSegment(sketch, "E337", {"start": v(-119.36, -7.41) * mm, "end": v(-118.85, -7.51) * mm});
            skLineSegment(sketch, "E338", {"start": v(-118.85, -7.51) * mm, "end": v(-118.34, -7.61) * mm});
            skLineSegment(sketch, "E339", {"start": v(-118.34, -7.61) * mm, "end": v(-117.83, -7.7) * mm});
            skLineSegment(sketch, "E340", {"start": v(-117.83, -7.7) * mm, "end": v(-117.33, -7.8) * mm});
            skLineSegment(sketch, "E341", {"start": v(-117.33, -7.8) * mm, "end": v(-116.82, -7.88) * mm});
            skLineSegment(sketch, "E342", {"start": v(-116.82, -7.88) * mm, "end": v(-116.3, -7.97) * mm});
            skLineSegment(sketch, "E343", {"start": v(-116.3, -7.97) * mm, "end": v(-115.8, -8.05) * mm});
            skLineSegment(sketch, "E344", {"start": v(-115.8, -8.05) * mm, "end": v(-115.29, -8.13) * mm});
            skLineSegment(sketch, "E345", {"start": v(-115.29, -8.13) * mm, "end": v(-114.78, -8.2) * mm});
            skLineSegment(sketch, "E346", {"start": v(-114.78, -8.2) * mm, "end": v(-114.27, -8.28) * mm});
            skLineSegment(sketch, "E347", {"start": v(-114.27, -8.28) * mm, "end": v(-113.64, -8.36) * mm});
            skLineSegment(sketch, "E348", {"start": v(-113.64, -8.36) * mm, "end": v(-113, -8.45) * mm});
            skLineSegment(sketch, "E349", {"start": v(-113, -8.45) * mm, "end": v(-112.38, -8.52) * mm});
            skLineSegment(sketch, "E350", {"start": v(-112.38, -8.52) * mm, "end": v(-111.75, -8.6) * mm});
            skLineSegment(sketch, "E351", {"start": v(-111.75, -8.6) * mm, "end": v(-111.12, -8.67) * mm});
            skLineSegment(sketch, "E352", {"start": v(-111.12, -8.67) * mm, "end": v(-110.49, -8.74) * mm});
            skLineSegment(sketch, "E353", {"start": v(-110.49, -8.74) * mm, "end": v(-109.86, -8.8) * mm});
            skLineSegment(sketch, "E354", {"start": v(-109.86, -8.8) * mm, "end": v(-109.23, -8.87) * mm});
            skLineSegment(sketch, "E355", {"start": v(-109.23, -8.87) * mm, "end": v(-108.6, -8.93) * mm});
            skLineSegment(sketch, "E356", {"start": v(-108.6, -8.93) * mm, "end": v(-107.97, -8.99) * mm});
            skLineSegment(sketch, "E357", {"start": v(-107.97, -8.99) * mm, "end": v(-107.22, -9.05) * mm});
            skLineSegment(sketch, "E358", {"start": v(-107.22, -9.05) * mm, "end": v(-106.48, -9.11) * mm});
            skLineSegment(sketch, "E359", {"start": v(-106.48, -9.11) * mm, "end": v(-105.73, -9.17) * mm});
            skLineSegment(sketch, "E360", {"start": v(-105.73, -9.17) * mm, "end": v(-104.98, -9.23) * mm});
            skLineSegment(sketch, "E361", {"start": v(-104.98, -9.23) * mm, "end": v(-104.24, -9.28) * mm});
            skLineSegment(sketch, "E362", {"start": v(-104.24, -9.28) * mm, "end": v(-103.5, -9.34) * mm});
            skLineSegment(sketch, "E363", {"start": v(-103.5, -9.34) * mm, "end": v(-102.74, -9.39) * mm});
            skLineSegment(sketch, "E364", {"start": v(-102.74, -9.39) * mm, "end": v(-102, -9.43) * mm});
            skLineSegment(sketch, "E365", {"start": v(-102, -9.43) * mm, "end": v(-101.25, -9.48) * mm});
            skLineSegment(sketch, "E366", {"start": v(-101.25, -9.48) * mm, "end": v(-99.65, -9.57) * mm});
            skLineSegment(sketch, "E367", {"start": v(-99.65, -9.57) * mm, "end": v(-98.8, -9.61) * mm});
            skLineSegment(sketch, "E368", {"start": v(-98.8, -9.61) * mm, "end": v(-97.93, -9.65) * mm});
            skLineSegment(sketch, "E369", {"start": v(-97.93, -9.65) * mm, "end": v(-97.08, -9.7) * mm});
            skLineSegment(sketch, "E370", {"start": v(-97.08, -9.7) * mm, "end": v(-96.22, -9.73) * mm});
            skLineSegment(sketch, "E371", {"start": v(-96.22, -9.73) * mm, "end": v(-95.36, -9.76) * mm});
            skLineSegment(sketch, "E372", {"start": v(-95.36, -9.76) * mm, "end": v(-94.5, -9.8) * mm});
            skLineSegment(sketch, "E373", {"start": v(-94.5, -9.8) * mm, "end": v(-93.65, -9.82) * mm});
            skLineSegment(sketch, "E374", {"start": v(-93.65, -9.82) * mm, "end": v(-92.8, -9.85) * mm});
            skLineSegment(sketch, "E375", {"start": v(-92.8, -9.85) * mm, "end": v(-91.93, -9.88) * mm});
            skLineSegment(sketch, "E376", {"start": v(-91.93, -9.88) * mm, "end": v(-90.97, -9.9) * mm});
            skLineSegment(sketch, "E377", {"start": v(-90.97, -9.9) * mm, "end": v(-90.01, -9.93) * mm});
            skLineSegment(sketch, "E378", {"start": v(-90.01, -9.93) * mm, "end": v(-89.05, -9.95) * mm});
            skLineSegment(sketch, "E379", {"start": v(-89.05, -9.95) * mm, "end": v(-88.09, -9.98) * mm});
            skLineSegment(sketch, "E380", {"start": v(-88.09, -9.98) * mm, "end": v(-87.13, -10) * mm});
            skLineSegment(sketch, "E381", {"start": v(-87.13, -10) * mm, "end": v(-86.17, -10.01) * mm});
            skLineSegment(sketch, "E382", {"start": v(-86.17, -10.01) * mm, "end": v(-85.2, -10.03) * mm});
            skLineSegment(sketch, "E383", {"start": v(-85.2, -10.03) * mm, "end": v(-84.25, -10.05) * mm});
            skLineSegment(sketch, "E384", {"start": v(-84.25, -10.05) * mm, "end": v(-83.28, -10.06) * mm});
            skLineSegment(sketch, "E385", {"start": v(-83.28, -10.06) * mm, "end": v(-81.27, -10.08) * mm});
            skLineSegment(sketch, "E386", {"start": v(-81.27, -10.08) * mm, "end": v(-80.21, -10.1) * mm});
            skLineSegment(sketch, "E387", {"start": v(-80.21, -10.1) * mm, "end": v(-79.16, -10.1) * mm});
            skLineSegment(sketch, "E388", {"start": v(-79.16, -10.1) * mm, "end": v(-78.1, -10.1) * mm});
            skLineSegment(sketch, "E389", {"start": v(-78.1, -10.1) * mm, "end": v(-77.05, -10.11) * mm});
            skLineSegment(sketch, "E390", {"start": v(-77.05, -10.11) * mm, "end": v(-76, -10.12) * mm});
            skLineSegment(sketch, "E391", {"start": v(-76, -10.12) * mm, "end": v(-74.94, -10.12) * mm});
            skLineSegment(sketch, "E392", {"start": v(-74.94, -10.12) * mm, "end": v(-73.89, -10.12) * mm});
            skLineSegment(sketch, "E393", {"start": v(-73.89, -10.12) * mm, "end": v(-72.83, -10.12) * mm});
            skLineSegment(sketch, "E394", {"start": v(-72.83, -10.12) * mm, "end": v(-71.78, -10.12) * mm});
            skLineSegment(sketch, "E395", {"start": v(-71.78, -10.12) * mm, "end": v(-70.64, -10.11) * mm});
            skLineSegment(sketch, "E396", {"start": v(-70.64, -10.11) * mm, "end": v(-69.5, -10.1) * mm});
            skLineSegment(sketch, "E397", {"start": v(-69.5, -10.1) * mm, "end": v(-68.36, -10.1) * mm});
            skLineSegment(sketch, "E398", {"start": v(-68.36, -10.1) * mm, "end": v(-67.22, -10.1) * mm});
            skLineSegment(sketch, "E399", {"start": v(-67.22, -10.1) * mm, "end": v(-66.08, -10.09) * mm});
            skLineSegment(sketch, "E400", {"start": v(-66.08, -10.09) * mm, "end": v(-64.94, -10.08) * mm});
            skLineSegment(sketch, "E401", {"start": v(-64.94, -10.08) * mm, "end": v(-63.8, -10.07) * mm});
            skLineSegment(sketch, "E402", {"start": v(-63.8, -10.07) * mm, "end": v(-62.67, -10.05) * mm});
            skLineSegment(sketch, "E403", {"start": v(-62.67, -10.05) * mm, "end": v(-61.53, -10.04) * mm});
            skLineSegment(sketch, "E404", {"start": v(-61.53, -10.04) * mm, "end": v(-60.4, -10.03) * mm});
            skLineSegment(sketch, "E405", {"start": v(-60.4, -10.03) * mm, "end": v(-59.18, -10.01) * mm});
            skLineSegment(sketch, "E406", {"start": v(-59.18, -10.01) * mm, "end": v(-57.97, -10) * mm});
            skLineSegment(sketch, "E407", {"start": v(-57.97, -10) * mm, "end": v(-56.76, -9.97) * mm});
            skLineSegment(sketch, "E408", {"start": v(-56.76, -9.97) * mm, "end": v(-55.55, -9.96) * mm});
            skLineSegment(sketch, "E409", {"start": v(-55.55, -9.96) * mm, "end": v(-54.34, -9.93) * mm});
            skLineSegment(sketch, "E410", {"start": v(-54.34, -9.93) * mm, "end": v(-53.14, -9.91) * mm});
            skLineSegment(sketch, "E411", {"start": v(-53.14, -9.91) * mm, "end": v(-51.93, -9.9) * mm});
            skLineSegment(sketch, "E412", {"start": v(-51.93, -9.9) * mm, "end": v(-50.72, -9.87) * mm});
            skLineSegment(sketch, "E413", {"start": v(-50.72, -9.87) * mm, "end": v(-49.5, -9.84) * mm});
            skLineSegment(sketch, "E414", {"start": v(-49.5, -9.84) * mm, "end": v(-47.03, -9.8) * mm});
            skLineSegment(sketch, "E415", {"start": v(-47.03, -9.8) * mm, "end": v(-45.76, -9.76) * mm});
            skLineSegment(sketch, "E416", {"start": v(-45.76, -9.76) * mm, "end": v(-44.5, -9.74) * mm});
            skLineSegment(sketch, "E417", {"start": v(-44.5, -9.74) * mm, "end": v(-43.23, -9.7) * mm});
            skLineSegment(sketch, "E418", {"start": v(-43.23, -9.7) * mm, "end": v(-41.96, -9.68) * mm});
            skLineSegment(sketch, "E419", {"start": v(-41.96, -9.68) * mm, "end": v(-40.7, -9.64) * mm});
            skLineSegment(sketch, "E420", {"start": v(-40.7, -9.64) * mm, "end": v(-39.43, -9.61) * mm});
            skLineSegment(sketch, "E421", {"start": v(-39.43, -9.61) * mm, "end": v(-38.16, -9.58) * mm});
            skLineSegment(sketch, "E422", {"start": v(-38.16, -9.58) * mm, "end": v(-36.9, -9.55) * mm});
            skLineSegment(sketch, "E423", {"start": v(-36.9, -9.55) * mm, "end": v(-34.31, -9.48) * mm});
            skLineSegment(sketch, "E424", {"start": v(-34.31, -9.48) * mm, "end": v(-33, -9.44) * mm});
            skLineSegment(sketch, "E425", {"start": v(-33, -9.44) * mm, "end": v(-31.7, -9.4) * mm});
            skLineSegment(sketch, "E426", {"start": v(-31.7, -9.4) * mm, "end": v(-30.38, -9.37) * mm});
            skLineSegment(sketch, "E427", {"start": v(-30.38, -9.37) * mm, "end": v(-29.07, -9.33) * mm});
            skLineSegment(sketch, "E428", {"start": v(-29.07, -9.33) * mm, "end": v(-27.76, -9.29) * mm});
            skLineSegment(sketch, "E429", {"start": v(-27.76, -9.29) * mm, "end": v(-26.45, -9.25) * mm});
            skLineSegment(sketch, "E430", {"start": v(-26.45, -9.25) * mm, "end": v(-25.13, -9.2) * mm});
            skLineSegment(sketch, "E431", {"start": v(-25.13, -9.2) * mm, "end": v(-23.82, -9.17) * mm});
            skLineSegment(sketch, "E432", {"start": v(-23.82, -9.17) * mm, "end": v(-22.51, -9.13) * mm});
            skLineSegment(sketch, "E433", {"start": v(-22.51, -9.13) * mm, "end": v(-21.17, -9.08) * mm});
            skLineSegment(sketch, "E434", {"start": v(-21.17, -9.08) * mm, "end": v(-19.83, -9.04) * mm});
            skLineSegment(sketch, "E435", {"start": v(-19.83, -9.04) * mm, "end": v(-18.49, -9) * mm});
            skLineSegment(sketch, "E436", {"start": v(-18.49, -9) * mm, "end": v(-17.15, -8.95) * mm});
            skLineSegment(sketch, "E437", {"start": v(-17.15, -8.95) * mm, "end": v(-15.8, -8.9) * mm});
            skLineSegment(sketch, "E438", {"start": v(-15.8, -8.9) * mm, "end": v(-14.47, -8.86) * mm});
            skLineSegment(sketch, "E439", {"start": v(-14.47, -8.86) * mm, "end": v(-13.13, -8.81) * mm});
            skLineSegment(sketch, "E440", {"start": v(-13.13, -8.81) * mm, "end": v(-11.79, -8.77) * mm});
            skLineSegment(sketch, "E441", {"start": v(-11.79, -8.77) * mm, "end": v(-10.44, -8.72) * mm});
            skLineSegment(sketch, "E442", {"start": v(-10.44, -8.72) * mm, "end": v(-7.75, -8.62) * mm});
            skLineSegment(sketch, "E443", {"start": v(-7.75, -8.62) * mm, "end": v(-6.4, -8.57) * mm});
            skLineSegment(sketch, "E444", {"start": v(-6.4, -8.57) * mm, "end": v(-5.04, -8.52) * mm});
            skLineSegment(sketch, "E445", {"start": v(-5.04, -8.52) * mm, "end": v(-3.68, -8.47) * mm});
            skLineSegment(sketch, "E446", {"start": v(-3.68, -8.47) * mm, "end": v(-2.33, -8.42) * mm});
            skLineSegment(sketch, "E447", {"start": v(-2.33, -8.42) * mm, "end": v(-0.97, -8.37) * mm});
            skLineSegment(sketch, "E448", {"start": v(-0.97, -8.37) * mm, "end": v(0.38, -8.32) * mm});
            skLineSegment(sketch, "E449", {"start": v(0.38, -8.32) * mm, "end": v(1.74, -8.27) * mm});
            skLineSegment(sketch, "E450", {"start": v(1.74, -8.27) * mm, "end": v(3.1, -8.22) * mm});
            skLineSegment(sketch, "E451", {"start": v(3.1, -8.22) * mm, "end": v(4.45, -8.17) * mm});
            skLineSegment(sketch, "E452", {"start": v(4.45, -8.17) * mm, "end": v(5.8, -8.12) * mm});
            skLineSegment(sketch, "E453", {"start": v(5.8, -8.12) * mm, "end": v(7.16, -8.06) * mm});
            skLineSegment(sketch, "E454", {"start": v(7.16, -8.06) * mm, "end": v(8.5, -8.01) * mm});
            skLineSegment(sketch, "E455", {"start": v(8.5, -8.01) * mm, "end": v(9.86, -7.96) * mm});
            skLineSegment(sketch, "E456", {"start": v(9.86, -7.96) * mm, "end": v(11.22, -7.9) * mm});
            skLineSegment(sketch, "E457", {"start": v(11.22, -7.9) * mm, "end": v(12.57, -7.85) * mm});
            skLineSegment(sketch, "E458", {"start": v(12.57, -7.85) * mm, "end": v(13.93, -7.8) * mm});
            skLineSegment(sketch, "E459", {"start": v(13.93, -7.8) * mm, "end": v(15.28, -7.75) * mm});
            skLineSegment(sketch, "E460", {"start": v(15.28, -7.75) * mm, "end": v(16.63, -7.7) * mm});
            skLineSegment(sketch, "E461", {"start": v(16.63, -7.7) * mm, "end": v(17.99, -7.64) * mm});
            skLineSegment(sketch, "E462", {"start": v(17.99, -7.64) * mm, "end": v(19.33, -7.58) * mm});
            skLineSegment(sketch, "E463", {"start": v(19.33, -7.58) * mm, "end": v(20.66, -7.53) * mm});
            skLineSegment(sketch, "E464", {"start": v(20.66, -7.53) * mm, "end": v(22, -7.47) * mm});
            skLineSegment(sketch, "E465", {"start": v(22, -7.47) * mm, "end": v(23.34, -7.42) * mm});
            skLineSegment(sketch, "E466", {"start": v(23.34, -7.42) * mm, "end": v(24.68, -7.37) * mm});
            skLineSegment(sketch, "E467", {"start": v(24.68, -7.37) * mm, "end": v(26.01, -7.31) * mm});
            skLineSegment(sketch, "E468", {"start": v(26.01, -7.31) * mm, "end": v(27.35, -7.26) * mm});
            skLineSegment(sketch, "E469", {"start": v(27.35, -7.26) * mm, "end": v(28.69, -7.2) * mm});
            skLineSegment(sketch, "E470", {"start": v(28.69, -7.2) * mm, "end": v(30.03, -7.15) * mm});
            skLineSegment(sketch, "E471", {"start": v(30.03, -7.15) * mm, "end": v(32.67, -7.04) * mm});
            skLineSegment(sketch, "E472", {"start": v(32.67, -7.04) * mm, "end": v(33.98, -6.98) * mm});
            skLineSegment(sketch, "E473", {"start": v(33.98, -6.98) * mm, "end": v(35.28, -6.93) * mm});
            skLineSegment(sketch, "E474", {"start": v(35.28, -6.93) * mm, "end": v(36.59, -6.88) * mm});
            skLineSegment(sketch, "E475", {"start": v(36.59, -6.88) * mm, "end": v(37.9, -6.82) * mm});
            skLineSegment(sketch, "E476", {"start": v(37.9, -6.82) * mm, "end": v(39.2, -6.77) * mm});
            skLineSegment(sketch, "E477", {"start": v(39.2, -6.77) * mm, "end": v(40.5, -6.72) * mm});
            skLineSegment(sketch, "E478", {"start": v(40.5, -6.72) * mm, "end": v(41.81, -6.66) * mm});
            skLineSegment(sketch, "E479", {"start": v(41.81, -6.66) * mm, "end": v(43.12, -6.6) * mm});
            skLineSegment(sketch, "E480", {"start": v(43.12, -6.6) * mm, "end": v(45.68, -6.5) * mm});
            skLineSegment(sketch, "E481", {"start": v(45.68, -6.5) * mm, "end": v(46.94, -6.45) * mm});
            skLineSegment(sketch, "E482", {"start": v(46.94, -6.45) * mm, "end": v(48.2, -6.4) * mm});
            skLineSegment(sketch, "E483", {"start": v(48.2, -6.4) * mm, "end": v(49.46, -6.35) * mm});
            skLineSegment(sketch, "E484", {"start": v(49.46, -6.35) * mm, "end": v(50.71, -6.3) * mm});
            skLineSegment(sketch, "E485", {"start": v(50.71, -6.3) * mm, "end": v(51.97, -6.25) * mm});
            skLineSegment(sketch, "E486", {"start": v(51.97, -6.25) * mm, "end": v(53.23, -6.2) * mm});
            skLineSegment(sketch, "E487", {"start": v(53.23, -6.2) * mm, "end": v(54.49, -6.14) * mm});
            skLineSegment(sketch, "E488", {"start": v(54.49, -6.14) * mm, "end": v(55.75, -6.1) * mm});
            skLineSegment(sketch, "E489", {"start": v(55.75, -6.1) * mm, "end": v(57, -6.04) * mm});
            skLineSegment(sketch, "E490", {"start": v(57, -6.04) * mm, "end": v(58.2, -6) * mm});
            skLineSegment(sketch, "E491", {"start": v(58.2, -6) * mm, "end": v(59.4, -5.95) * mm});
            skLineSegment(sketch, "E492", {"start": v(59.4, -5.95) * mm, "end": v(60.6, -5.9) * mm});
            skLineSegment(sketch, "E493", {"start": v(60.6, -5.9) * mm, "end": v(61.79, -5.85) * mm});
            skLineSegment(sketch, "E494", {"start": v(61.79, -5.85) * mm, "end": v(62.98, -5.8) * mm});
            skLineSegment(sketch, "E495", {"start": v(62.98, -5.8) * mm, "end": v(64.18, -5.75) * mm});
            skLineSegment(sketch, "E496", {"start": v(64.18, -5.75) * mm, "end": v(65.38, -5.7) * mm});
            skLineSegment(sketch, "E497", {"start": v(65.38, -5.7) * mm, "end": v(66.57, -5.66) * mm});
            skLineSegment(sketch, "E498", {"start": v(66.57, -5.66) * mm, "end": v(67.77, -5.61) * mm});
            skLineSegment(sketch, "E499", {"start": v(67.77, -5.61) * mm, "end": v(68.96, -5.57) * mm});
            skLineSegment(sketch, "E500", {"start": v(68.96, -5.57) * mm, "end": v(70.08, -5.52) * mm});
            skLineSegment(sketch, "E501", {"start": v(70.08, -5.52) * mm, "end": v(71.2, -5.48) * mm});
            skLineSegment(sketch, "E502", {"start": v(71.2, -5.48) * mm, "end": v(72.32, -5.44) * mm});
            skLineSegment(sketch, "E503", {"start": v(72.32, -5.44) * mm, "end": v(73.44, -5.4) * mm});
            skLineSegment(sketch, "E504", {"start": v(73.44, -5.4) * mm, "end": v(74.56, -5.35) * mm});
            skLineSegment(sketch, "E505", {"start": v(74.56, -5.35) * mm, "end": v(75.68, -5.31) * mm});
            skLineSegment(sketch, "E506", {"start": v(75.68, -5.31) * mm, "end": v(76.8, -5.27) * mm});
            skLineSegment(sketch, "E507", {"start": v(76.8, -5.27) * mm, "end": v(77.91, -5.23) * mm});
            skLineSegment(sketch, "E508", {"start": v(77.91, -5.23) * mm, "end": v(79.03, -5.19) * mm});
            skLineSegment(sketch, "E509", {"start": v(79.03, -5.19) * mm, "end": v(81.18, -5.1) * mm});
            skLineSegment(sketch, "E510", {"start": v(81.18, -5.1) * mm, "end": v(82.2, -5.07) * mm});
            skLineSegment(sketch, "E511", {"start": v(82.2, -5.07) * mm, "end": v(83.23, -5.03) * mm});
            skLineSegment(sketch, "E512", {"start": v(83.23, -5.03) * mm, "end": v(84.26, -5) * mm});
            skLineSegment(sketch, "E513", {"start": v(84.26, -5) * mm, "end": v(85.29, -4.96) * mm});
            skLineSegment(sketch, "E514", {"start": v(85.29, -4.96) * mm, "end": v(86.31, -4.93) * mm});
            skLineSegment(sketch, "E515", {"start": v(86.31, -4.93) * mm, "end": v(87.34, -4.9) * mm});
            skLineSegment(sketch, "E516", {"start": v(87.34, -4.9) * mm, "end": v(88.37, -4.86) * mm});
            skLineSegment(sketch, "E517", {"start": v(88.37, -4.86) * mm, "end": v(89.4, -4.82) * mm});
            skLineSegment(sketch, "E518", {"start": v(89.4, -4.82) * mm, "end": v(90.42, -4.79) * mm});
            skLineSegment(sketch, "E519", {"start": v(90.42, -4.79) * mm, "end": v(91.34, -4.76) * mm});
            skLineSegment(sketch, "E520", {"start": v(91.34, -4.76) * mm, "end": v(92.27, -4.73) * mm});
            skLineSegment(sketch, "E521", {"start": v(92.27, -4.73) * mm, "end": v(93.19, -4.7) * mm});
            skLineSegment(sketch, "E522", {"start": v(93.19, -4.7) * mm, "end": v(94.11, -4.67) * mm});
            skLineSegment(sketch, "E523", {"start": v(94.11, -4.67) * mm, "end": v(95.03, -4.64) * mm});
            skLineSegment(sketch, "E524", {"start": v(95.03, -4.64) * mm, "end": v(95.96, -4.61) * mm});
            skLineSegment(sketch, "E525", {"start": v(95.96, -4.61) * mm, "end": v(96.88, -4.59) * mm});
            skLineSegment(sketch, "E526", {"start": v(96.88, -4.59) * mm, "end": v(97.8, -4.56) * mm});
            skLineSegment(sketch, "E527", {"start": v(97.8, -4.56) * mm, "end": v(98.72, -4.53) * mm});
            skLineSegment(sketch, "E528", {"start": v(98.72, -4.53) * mm, "end": v(99.64, -4.5) * mm});
            skLineSegment(sketch, "E529", {"start": v(99.64, -4.5) * mm, "end": v(100.45, -4.48) * mm});
            skLineSegment(sketch, "E530", {"start": v(100.45, -4.48) * mm, "end": v(101.25, -4.46) * mm});
            skLineSegment(sketch, "E531", {"start": v(101.25, -4.46) * mm, "end": v(102.06, -4.44) * mm});
            skLineSegment(sketch, "E532", {"start": v(102.06, -4.44) * mm, "end": v(102.86, -4.42) * mm});
            skLineSegment(sketch, "E533", {"start": v(102.86, -4.42) * mm, "end": v(103.67, -4.4) * mm});
            skLineSegment(sketch, "E534", {"start": v(103.67, -4.4) * mm, "end": v(104.47, -4.37) * mm});
            skLineSegment(sketch, "E535", {"start": v(104.47, -4.37) * mm, "end": v(105.28, -4.35) * mm});
            skLineSegment(sketch, "E536", {"start": v(105.28, -4.35) * mm, "end": v(106.08, -4.33) * mm});
            skLineSegment(sketch, "E537", {"start": v(106.08, -4.33) * mm, "end": v(106.89, -4.31) * mm});
            skLineSegment(sketch, "E538", {"start": v(106.89, -4.31) * mm, "end": v(107.7, -4.3) * mm});
            skLineSegment(sketch, "E539", {"start": v(107.7, -4.3) * mm, "end": v(108.37, -4.28) * mm});
            skLineSegment(sketch, "E540", {"start": v(108.37, -4.28) * mm, "end": v(109.05, -4.26) * mm});
            skLineSegment(sketch, "E541", {"start": v(109.05, -4.26) * mm, "end": v(109.72, -4.25) * mm});
            skLineSegment(sketch, "E542", {"start": v(109.72, -4.25) * mm, "end": v(110.4, -4.23) * mm});
            skLineSegment(sketch, "E543", {"start": v(110.4, -4.23) * mm, "end": v(111.08, -4.22) * mm});
            skLineSegment(sketch, "E544", {"start": v(111.08, -4.22) * mm, "end": v(111.75, -4.2) * mm});
            skLineSegment(sketch, "E545", {"start": v(111.75, -4.2) * mm, "end": v(112.43, -4.19) * mm});
            skLineSegment(sketch, "E546", {"start": v(112.43, -4.19) * mm, "end": v(113.1, -4.17) * mm});
            skLineSegment(sketch, "E547", {"start": v(113.1, -4.17) * mm, "end": v(113.78, -4.16) * mm});
            skLineSegment(sketch, "E548", {"start": v(113.78, -4.16) * mm, "end": v(115, -4.14) * mm});
            skLineSegment(sketch, "E549", {"start": v(115, -4.14) * mm, "end": v(115.53, -4.13) * mm});
            skLineSegment(sketch, "E550", {"start": v(115.53, -4.13) * mm, "end": v(116.07, -4.12) * mm});
            skLineSegment(sketch, "E551", {"start": v(116.07, -4.12) * mm, "end": v(116.6, -4.1) * mm});
            skLineSegment(sketch, "E552", {"start": v(116.6, -4.1) * mm, "end": v(117.15, -4.1) * mm});
            skLineSegment(sketch, "E553", {"start": v(117.15, -4.1) * mm, "end": v(117.69, -4.09) * mm});
            skLineSegment(sketch, "E554", {"start": v(117.69, -4.09) * mm, "end": v(118.22, -4.08) * mm});
            skLineSegment(sketch, "E555", {"start": v(118.22, -4.08) * mm, "end": v(118.76, -4.07) * mm});
            skLineSegment(sketch, "E556", {"start": v(118.76, -4.07) * mm, "end": v(119.3, -4.06) * mm});
            skLineSegment(sketch, "E557", {"start": v(119.3, -4.06) * mm, "end": v(119.84, -4.05) * mm});
            skLineSegment(sketch, "E558", {"start": v(119.84, -4.05) * mm, "end": v(124, -3.99) * mm});
            skLineSegment(sketch, "E559", {"start": v(124, -3.99) * mm, "end": v(124.24, -3.99) * mm});
            skLineSegment(sketch, "E560", {"start": v(124.24, -3.99) * mm, "end": v(124.48, -3.98) * mm});
            skLineSegment(sketch, "E561", {"start": v(124.48, -3.98) * mm, "end": v(124.73, -3.98) * mm});
            skLineSegment(sketch, "E562", {"start": v(124.73, -3.98) * mm, "end": v(124.97, -3.98) * mm});
            skLineSegment(sketch, "E563", {"start": v(124.97, -3.98) * mm, "end": v(125.2, -3.97) * mm});
            skLineSegment(sketch, "E564", {"start": v(125.2, -3.97) * mm, "end": v(125.45, -3.97) * mm});
            skLineSegment(sketch, "E565", {"start": v(125.45, -3.97) * mm, "end": v(125.7, -3.97) * mm});
            skLineSegment(sketch, "E566", {"start": v(125.7, -3.97) * mm, "end": v(125.93, -3.96) * mm});
            skLineSegment(sketch, "E567", {"start": v(125.93, -3.96) * mm, "end": v(126.17, -3.96) * mm});
            skLineSegment(sketch, "E568", {"start": v(126.17, -3.96) * mm, "end": v(126.26, -3.96) * mm});
            skLineSegment(sketch, "E569", {"start": v(126.26, -3.96) * mm, "end": v(126.34, -3.96) * mm});
            skLineSegment(sketch, "E570", {"start": v(126.34, -3.96) * mm, "end": v(126.42, -3.96) * mm});
            skLineSegment(sketch, "E571", {"start": v(126.42, -3.96) * mm, "end": v(126.5, -3.96) * mm});
            skLineSegment(sketch, "E572", {"start": v(126.5, -3.96) * mm, "end": v(126.59, -3.96) * mm});
            skLineSegment(sketch, "E573", {"start": v(126.59, -3.96) * mm, "end": v(126.67, -3.96) * mm});
            skLineSegment(sketch, "E574", {"start": v(126.67, -3.96) * mm, "end": v(126.75, -3.96) * mm});
            skLineSegment(sketch, "E575", {"start": v(126.75, -3.96) * mm, "end": v(126.83, -3.96) * mm});
            skLineSegment(sketch, "E576", {"start": v(126.83, -3.96) * mm, "end": v(126.92, -3.95) * mm});
            skLineSegment(sketch, "E577", {"start": v(126.92, -3.95) * mm, "end": v(127, -3.95) * mm});
            skLineSegment(sketch, "E578", {"start": v(61.39, 2.74) * mm, "end": v(60.75, 2.81) * mm});
            skLineSegment(sketch, "E579", {"start": v(60.75, 2.81) * mm, "end": v(60.12, 2.88) * mm});
            skLineSegment(sketch, "E580", {"start": v(60.12, 2.88) * mm, "end": v(59.48, 2.95) * mm});
            skLineSegment(sketch, "E581", {"start": v(59.48, 2.95) * mm, "end": v(58.85, 3.02) * mm});
            skLineSegment(sketch, "E582", {"start": v(58.85, 3.02) * mm, "end": v(58.21, 3.08) * mm});
            skLineSegment(sketch, "E583", {"start": v(58.21, 3.08) * mm, "end": v(57.58, 3.15) * mm});
            skLineSegment(sketch, "E584", {"start": v(57.58, 3.15) * mm, "end": v(56.94, 3.22) * mm});
            skLineSegment(sketch, "E585", {"start": v(56.94, 3.22) * mm, "end": v(56.3, 3.28) * mm});
            skLineSegment(sketch, "E586", {"start": v(56.3, 3.28) * mm, "end": v(55.67, 3.35) * mm});
            skLineSegment(sketch, "E587", {"start": v(55.67, 3.35) * mm, "end": v(55.04, 3.42) * mm});
            skLineSegment(sketch, "E588", {"start": v(55.04, 3.42) * mm, "end": v(54.4, 3.48) * mm});
            skLineSegment(sketch, "E589", {"start": v(54.4, 3.48) * mm, "end": v(53.77, 3.55) * mm});
            skLineSegment(sketch, "E590", {"start": v(53.77, 3.55) * mm, "end": v(53.13, 3.6) * mm});
            skLineSegment(sketch, "E591", {"start": v(53.13, 3.6) * mm, "end": v(52.5, 3.67) * mm});
            skLineSegment(sketch, "E592", {"start": v(52.5, 3.67) * mm, "end": v(51.86, 3.74) * mm});
            skLineSegment(sketch, "E593", {"start": v(51.86, 3.74) * mm, "end": v(51.23, 3.8) * mm});
            skLineSegment(sketch, "E594", {"start": v(51.23, 3.8) * mm, "end": v(50.6, 3.86) * mm});
            skLineSegment(sketch, "E595", {"start": v(50.6, 3.86) * mm, "end": v(49.96, 3.92) * mm});
            skLineSegment(sketch, "E596", {"start": v(49.96, 3.92) * mm, "end": v(49.32, 3.98) * mm});
            skLineSegment(sketch, "E597", {"start": v(49.32, 3.98) * mm, "end": v(48.69, 4.05) * mm});
            skLineSegment(sketch, "E598", {"start": v(48.69, 4.05) * mm, "end": v(48.05, 4.1) * mm});
            skLineSegment(sketch, "E599", {"start": v(48.05, 4.1) * mm, "end": v(47.42, 4.17) * mm});
            skLineSegment(sketch, "E600", {"start": v(47.42, 4.17) * mm, "end": v(46.78, 4.23) * mm});
            skLineSegment(sketch, "E601", {"start": v(46.78, 4.23) * mm, "end": v(46.14, 4.28) * mm});
            skLineSegment(sketch, "E602", {"start": v(46.14, 4.28) * mm, "end": v(45.5, 4.34) * mm});
            skLineSegment(sketch, "E603", {"start": v(45.5, 4.34) * mm, "end": v(44.87, 4.4) * mm});
            skLineSegment(sketch, "E604", {"start": v(44.87, 4.4) * mm, "end": v(44.24, 4.46) * mm});
            skLineSegment(sketch, "E605", {"start": v(44.24, 4.46) * mm, "end": v(43.6, 4.52) * mm});
            skLineSegment(sketch, "E606", {"start": v(43.6, 4.52) * mm, "end": v(42.97, 4.57) * mm});
            skLineSegment(sketch, "E607", {"start": v(42.97, 4.57) * mm, "end": v(42.33, 4.63) * mm});
            skLineSegment(sketch, "E608", {"start": v(42.33, 4.63) * mm, "end": v(41.7, 4.69) * mm});
            skLineSegment(sketch, "E609", {"start": v(41.7, 4.69) * mm, "end": v(41.06, 4.74) * mm});
            skLineSegment(sketch, "E610", {"start": v(41.06, 4.74) * mm, "end": v(40.43, 4.8) * mm});
            skLineSegment(sketch, "E611", {"start": v(40.43, 4.8) * mm, "end": v(39.8, 4.85) * mm});
            skLineSegment(sketch, "E612", {"start": v(39.8, 4.85) * mm, "end": v(39.16, 4.9) * mm});
            skLineSegment(sketch, "E613", {"start": v(39.16, 4.9) * mm, "end": v(38.52, 4.96) * mm});
            skLineSegment(sketch, "E614", {"start": v(38.52, 4.96) * mm, "end": v(37.89, 5.02) * mm});
            skLineSegment(sketch, "E615", {"start": v(37.89, 5.02) * mm, "end": v(37.25, 5.07) * mm});
            skLineSegment(sketch, "E616", {"start": v(37.25, 5.07) * mm, "end": v(36.62, 5.12) * mm});
            skLineSegment(sketch, "E617", {"start": v(36.62, 5.12) * mm, "end": v(35.98, 5.18) * mm});
            skLineSegment(sketch, "E618", {"start": v(35.98, 5.18) * mm, "end": v(35.35, 5.23) * mm});
            skLineSegment(sketch, "E619", {"start": v(35.35, 5.23) * mm, "end": v(34.71, 5.28) * mm});
            skLineSegment(sketch, "E620", {"start": v(34.71, 5.28) * mm, "end": v(34.08, 5.33) * mm});
            skLineSegment(sketch, "E621", {"start": v(34.08, 5.33) * mm, "end": v(33.44, 5.38) * mm});
            skLineSegment(sketch, "E622", {"start": v(33.44, 5.38) * mm, "end": v(32.8, 5.43) * mm});
            skLineSegment(sketch, "E623", {"start": v(32.8, 5.43) * mm, "end": v(32.17, 5.48) * mm});
            skLineSegment(sketch, "E624", {"start": v(32.17, 5.48) * mm, "end": v(31.54, 5.53) * mm});
            skLineSegment(sketch, "E625", {"start": v(31.54, 5.53) * mm, "end": v(30.9, 5.58) * mm});
            skLineSegment(sketch, "E626", {"start": v(30.9, 5.58) * mm, "end": v(30.27, 5.63) * mm});
            skLineSegment(sketch, "E627", {"start": v(30.27, 5.63) * mm, "end": v(29.63, 5.68) * mm});
            skLineSegment(sketch, "E628", {"start": v(29.63, 5.68) * mm, "end": v(29, 5.73) * mm});
            skLineSegment(sketch, "E629", {"start": v(29, 5.73) * mm, "end": v(28.36, 5.78) * mm});
            skLineSegment(sketch, "E630", {"start": v(28.36, 5.78) * mm, "end": v(27.73, 5.82) * mm});
            skLineSegment(sketch, "E631", {"start": v(27.73, 5.82) * mm, "end": v(27.1, 5.87) * mm});
            skLineSegment(sketch, "E632", {"start": v(27.1, 5.87) * mm, "end": v(26.46, 5.92) * mm});
            skLineSegment(sketch, "E633", {"start": v(26.46, 5.92) * mm, "end": v(25.82, 5.96) * mm});
            skLineSegment(sketch, "E634", {"start": v(25.82, 5.96) * mm, "end": v(25.19, 6.01) * mm});
            skLineSegment(sketch, "E635", {"start": v(25.19, 6.01) * mm, "end": v(24.55, 6.06) * mm});
            skLineSegment(sketch, "E636", {"start": v(24.55, 6.06) * mm, "end": v(23.92, 6.1) * mm});
            skLineSegment(sketch, "E637", {"start": v(23.92, 6.1) * mm, "end": v(23.28, 6.15) * mm});
            skLineSegment(sketch, "E638", {"start": v(23.28, 6.15) * mm, "end": v(22.65, 6.2) * mm});
            skLineSegment(sketch, "E639", {"start": v(22.65, 6.2) * mm, "end": v(22, 6.24) * mm});
            skLineSegment(sketch, "E640", {"start": v(22, 6.24) * mm, "end": v(21.37, 6.28) * mm});
            skLineSegment(sketch, "E641", {"start": v(21.37, 6.28) * mm, "end": v(20.74, 6.32) * mm});
            skLineSegment(sketch, "E642", {"start": v(20.74, 6.32) * mm, "end": v(20.1, 6.37) * mm});
            skLineSegment(sketch, "E643", {"start": v(20.1, 6.37) * mm, "end": v(19.47, 6.4) * mm});
            skLineSegment(sketch, "E644", {"start": v(19.47, 6.4) * mm, "end": v(18.83, 6.45) * mm});
            skLineSegment(sketch, "E645", {"start": v(18.83, 6.45) * mm, "end": v(18.2, 6.5) * mm});
            skLineSegment(sketch, "E646", {"start": v(18.2, 6.5) * mm, "end": v(17.56, 6.53) * mm});
            skLineSegment(sketch, "E647", {"start": v(17.56, 6.53) * mm, "end": v(16.93, 6.58) * mm});
            skLineSegment(sketch, "E648", {"start": v(16.93, 6.58) * mm, "end": v(16.3, 6.62) * mm});
            skLineSegment(sketch, "E649", {"start": v(16.3, 6.62) * mm, "end": v(15.66, 6.66) * mm});
            skLineSegment(sketch, "E650", {"start": v(15.66, 6.66) * mm, "end": v(15.02, 6.7) * mm});
            skLineSegment(sketch, "E651", {"start": v(15.02, 6.7) * mm, "end": v(14.39, 6.74) * mm});
            skLineSegment(sketch, "E652", {"start": v(14.39, 6.74) * mm, "end": v(13.75, 6.78) * mm});
            skLineSegment(sketch, "E653", {"start": v(13.75, 6.78) * mm, "end": v(13.12, 6.82) * mm});
            skLineSegment(sketch, "E654", {"start": v(13.12, 6.82) * mm, "end": v(12.48, 6.85) * mm});
            skLineSegment(sketch, "E655", {"start": v(12.48, 6.85) * mm, "end": v(11.85, 6.9) * mm});
            skLineSegment(sketch, "E656", {"start": v(11.85, 6.9) * mm, "end": v(11.21, 6.93) * mm});
            skLineSegment(sketch, "E657", {"start": v(11.21, 6.93) * mm, "end": v(10.58, 6.97) * mm});
            skLineSegment(sketch, "E658", {"start": v(10.58, 6.97) * mm, "end": v(9.94, 7) * mm});
            skLineSegment(sketch, "E659", {"start": v(9.94, 7) * mm, "end": v(9.3, 7.04) * mm});
            skLineSegment(sketch, "E660", {"start": v(9.3, 7.04) * mm, "end": v(8.67, 7.08) * mm});
            skLineSegment(sketch, "E661", {"start": v(8.67, 7.08) * mm, "end": v(8.04, 7.12) * mm});
            skLineSegment(sketch, "E662", {"start": v(8.04, 7.12) * mm, "end": v(7.4, 7.15) * mm});
            skLineSegment(sketch, "E663", {"start": v(7.4, 7.15) * mm, "end": v(6.77, 7.19) * mm});
            skLineSegment(sketch, "E664", {"start": v(6.77, 7.19) * mm, "end": v(6.13, 7.22) * mm});
            skLineSegment(sketch, "E665", {"start": v(6.13, 7.22) * mm, "end": v(5.5, 7.26) * mm});
            skLineSegment(sketch, "E666", {"start": v(5.5, 7.26) * mm, "end": v(4.86, 7.3) * mm});
            skLineSegment(sketch, "E667", {"start": v(4.86, 7.3) * mm, "end": v(4.23, 7.33) * mm});
            skLineSegment(sketch, "E668", {"start": v(4.23, 7.33) * mm, "end": v(3.6, 7.36) * mm});
            skLineSegment(sketch, "E669", {"start": v(3.6, 7.36) * mm, "end": v(2.96, 7.4) * mm});
            skLineSegment(sketch, "E670", {"start": v(2.96, 7.4) * mm, "end": v(2.32, 7.43) * mm});
            skLineSegment(sketch, "E671", {"start": v(2.32, 7.43) * mm, "end": v(1.69, 7.46) * mm});
            skLineSegment(sketch, "E672", {"start": v(1.69, 7.46) * mm, "end": v(1.05, 7.5) * mm});
            skLineSegment(sketch, "E673", {"start": v(1.05, 7.5) * mm, "end": v(0.42, 7.53) * mm});
            skLineSegment(sketch, "E674", {"start": v(0.42, 7.53) * mm, "end": v(-0.22, 7.56) * mm});
            skLineSegment(sketch, "E675", {"start": v(-0.22, 7.56) * mm, "end": v(-0.85, 7.59) * mm});
            skLineSegment(sketch, "E676", {"start": v(-0.85, 7.59) * mm, "end": v(-1.49, 7.62) * mm});
            skLineSegment(sketch, "E677", {"start": v(-1.49, 7.62) * mm, "end": v(-2.12, 7.65) * mm});
            skLineSegment(sketch, "E678", {"start": v(-2.12, 7.65) * mm, "end": v(-2.76, 7.68) * mm});
            skLineSegment(sketch, "E679", {"start": v(-2.76, 7.68) * mm, "end": v(-3.4, 7.7) * mm});
            skLineSegment(sketch, "E680", {"start": v(-3.4, 7.7) * mm, "end": v(-4.03, 7.74) * mm});
            skLineSegment(sketch, "E681", {"start": v(-4.03, 7.74) * mm, "end": v(-4.67, 7.77) * mm});
            skLineSegment(sketch, "E682", {"start": v(-4.67, 7.77) * mm, "end": v(-5.3, 7.8) * mm});
            skLineSegment(sketch, "E683", {"start": v(-5.3, 7.8) * mm, "end": v(-5.94, 7.82) * mm});
            skLineSegment(sketch, "E684", {"start": v(-5.94, 7.82) * mm, "end": v(-6.57, 7.85) * mm});
            skLineSegment(sketch, "E685", {"start": v(-6.57, 7.85) * mm, "end": v(-7.2, 7.88) * mm});
            skLineSegment(sketch, "E686", {"start": v(-7.2, 7.88) * mm, "end": v(-7.84, 7.9) * mm});
            skLineSegment(sketch, "E687", {"start": v(-7.84, 7.9) * mm, "end": v(-8.48, 7.93) * mm});
            skLineSegment(sketch, "E688", {"start": v(-8.48, 7.93) * mm, "end": v(-9.11, 7.95) * mm});
            skLineSegment(sketch, "E689", {"start": v(-9.11, 7.95) * mm, "end": v(-9.75, 7.98) * mm});
            skLineSegment(sketch, "E690", {"start": v(-9.75, 7.98) * mm, "end": v(-10.38, 8) * mm});
            skLineSegment(sketch, "E691", {"start": v(-10.38, 8) * mm, "end": v(-11.02, 8.03) * mm});
            skLineSegment(sketch, "E692", {"start": v(-11.02, 8.03) * mm, "end": v(-11.65, 8.05) * mm});
            skLineSegment(sketch, "E693", {"start": v(-11.65, 8.05) * mm, "end": v(-12.29, 8.07) * mm});
            skLineSegment(sketch, "E694", {"start": v(-12.29, 8.07) * mm, "end": v(-12.92, 8.1) * mm});
            skLineSegment(sketch, "E695", {"start": v(-12.92, 8.1) * mm, "end": v(-13.56, 8.12) * mm});
            skLineSegment(sketch, "E696", {"start": v(-13.56, 8.12) * mm, "end": v(-14.2, 8.14) * mm});
            skLineSegment(sketch, "E697", {"start": v(-14.2, 8.14) * mm, "end": v(-14.83, 8.16) * mm});
            skLineSegment(sketch, "E698", {"start": v(-14.83, 8.16) * mm, "end": v(-15.46, 8.18) * mm});
            skLineSegment(sketch, "E699", {"start": v(-15.46, 8.18) * mm, "end": v(-16.1, 8.2) * mm});
            skLineSegment(sketch, "E700", {"start": v(-16.1, 8.2) * mm, "end": v(-16.73, 8.22) * mm});
            skLineSegment(sketch, "E701", {"start": v(-16.73, 8.22) * mm, "end": v(-17.37, 8.24) * mm});
            skLineSegment(sketch, "E702", {"start": v(-17.37, 8.24) * mm, "end": v(-18, 8.26) * mm});
            skLineSegment(sketch, "E703", {"start": v(-18, 8.26) * mm, "end": v(-18.64, 8.28) * mm});
            skLineSegment(sketch, "E704", {"start": v(-18.64, 8.28) * mm, "end": v(-19.27, 8.3) * mm});
            skLineSegment(sketch, "E705", {"start": v(-19.27, 8.3) * mm, "end": v(-19.9, 8.31) * mm});
            skLineSegment(sketch, "E706", {"start": v(-19.9, 8.31) * mm, "end": v(-20.54, 8.33) * mm});
            skLineSegment(sketch, "E707", {"start": v(-20.54, 8.33) * mm, "end": v(-21.18, 8.35) * mm});
            skLineSegment(sketch, "E708", {"start": v(-21.18, 8.35) * mm, "end": v(-21.81, 8.36) * mm});
            skLineSegment(sketch, "E709", {"start": v(-21.81, 8.36) * mm, "end": v(-22.45, 8.38) * mm});
            skLineSegment(sketch, "E710", {"start": v(-22.45, 8.38) * mm, "end": v(-23.08, 8.4) * mm});
            skLineSegment(sketch, "E711", {"start": v(-23.08, 8.4) * mm, "end": v(-23.72, 8.41) * mm});
            skLineSegment(sketch, "E712", {"start": v(-23.72, 8.41) * mm, "end": v(-24.36, 8.42) * mm});
            skLineSegment(sketch, "E713", {"start": v(-24.36, 8.42) * mm, "end": v(-25, 8.44) * mm});
            skLineSegment(sketch, "E714", {"start": v(-25, 8.44) * mm, "end": v(-25.63, 8.45) * mm});
            skLineSegment(sketch, "E715", {"start": v(-25.63, 8.45) * mm, "end": v(-26.26, 8.46) * mm});
            skLineSegment(sketch, "E716", {"start": v(-26.26, 8.46) * mm, "end": v(-26.9, 8.48) * mm});
            skLineSegment(sketch, "E717", {"start": v(-26.9, 8.48) * mm, "end": v(-27.53, 8.49) * mm});
            skLineSegment(sketch, "E718", {"start": v(-27.53, 8.49) * mm, "end": v(-28.17, 8.5) * mm});
            skLineSegment(sketch, "E719", {"start": v(-28.17, 8.5) * mm, "end": v(-28.8, 8.51) * mm});
            skLineSegment(sketch, "E720", {"start": v(-28.8, 8.51) * mm, "end": v(-29.44, 8.52) * mm});
            skLineSegment(sketch, "E721", {"start": v(-29.44, 8.52) * mm, "end": v(-30.07, 8.53) * mm});
            skLineSegment(sketch, "E722", {"start": v(-30.07, 8.53) * mm, "end": v(-30.7, 8.54) * mm});
            skLineSegment(sketch, "E723", {"start": v(-30.7, 8.54) * mm, "end": v(-31.34, 8.55) * mm});
            skLineSegment(sketch, "E724", {"start": v(-31.34, 8.55) * mm, "end": v(-31.98, 8.56) * mm});
            skLineSegment(sketch, "E725", {"start": v(-31.98, 8.56) * mm, "end": v(-32.61, 8.57) * mm});
            skLineSegment(sketch, "E726", {"start": v(-32.61, 8.57) * mm, "end": v(-33.25, 8.57) * mm});
            skLineSegment(sketch, "E727", {"start": v(-33.25, 8.57) * mm, "end": v(-33.88, 8.58) * mm});
            skLineSegment(sketch, "E728", {"start": v(-33.88, 8.58) * mm, "end": v(-34.52, 8.59) * mm});
            skLineSegment(sketch, "E729", {"start": v(-34.52, 8.59) * mm, "end": v(-35.15, 8.6) * mm});
            skLineSegment(sketch, "E730", {"start": v(-35.15, 8.6) * mm, "end": v(-35.79, 8.6) * mm});
            skLineSegment(sketch, "E731", {"start": v(-35.79, 8.6) * mm, "end": v(-36.42, 8.6) * mm});
            skLineSegment(sketch, "E732", {"start": v(-36.42, 8.6) * mm, "end": v(-37.06, 8.6) * mm});
            skLineSegment(sketch, "E733", {"start": v(-37.06, 8.6) * mm, "end": v(-37.7, 8.6) * mm});
            skLineSegment(sketch, "E734", {"start": v(-37.7, 8.6) * mm, "end": v(-38.33, 8.61) * mm});
            skLineSegment(sketch, "E735", {"start": v(-38.33, 8.61) * mm, "end": v(-38.96, 8.62) * mm});
            skLineSegment(sketch, "E736", {"start": v(-38.96, 8.62) * mm, "end": v(-39.6, 8.62) * mm});
            skLineSegment(sketch, "E737", {"start": v(-39.6, 8.62) * mm, "end": v(-40.23, 8.62) * mm});
            skLineSegment(sketch, "E738", {"start": v(-40.23, 8.62) * mm, "end": v(-40.87, 8.62) * mm});
            skLineSegment(sketch, "E739", {"start": v(-40.87, 8.62) * mm, "end": v(-41.5, 8.62) * mm});
            skLineSegment(sketch, "E740", {"start": v(-41.5, 8.62) * mm, "end": v(-42.14, 8.62) * mm});
            skLineSegment(sketch, "E741", {"start": v(-42.14, 8.62) * mm, "end": v(-42.77, 8.62) * mm});
            skLineSegment(sketch, "E742", {"start": v(-42.77, 8.62) * mm, "end": v(-43.4, 8.61) * mm});
            skLineSegment(sketch, "E743", {"start": v(-43.4, 8.61) * mm, "end": v(-44.04, 8.61) * mm});
            skLineSegment(sketch, "E744", {"start": v(-44.04, 8.61) * mm, "end": v(-44.68, 8.6) * mm});
            skLineSegment(sketch, "E745", {"start": v(-44.68, 8.6) * mm, "end": v(-45.31, 8.6) * mm});
            skLineSegment(sketch, "E746", {"start": v(-45.31, 8.6) * mm, "end": v(-45.95, 8.6) * mm});
            skLineSegment(sketch, "E747", {"start": v(-45.95, 8.6) * mm, "end": v(-46.58, 8.6) * mm});
            skLineSegment(sketch, "E748", {"start": v(-46.58, 8.6) * mm, "end": v(-47.22, 8.59) * mm});
            skLineSegment(sketch, "E749", {"start": v(-47.22, 8.59) * mm, "end": v(-47.85, 8.58) * mm});
            skLineSegment(sketch, "E750", {"start": v(-47.85, 8.58) * mm, "end": v(-48.49, 8.58) * mm});
            skLineSegment(sketch, "E751", {"start": v(-48.49, 8.58) * mm, "end": v(-49.12, 8.57) * mm});
            skLineSegment(sketch, "E752", {"start": v(-49.12, 8.57) * mm, "end": v(-49.76, 8.56) * mm});
            skLineSegment(sketch, "E753", {"start": v(-49.76, 8.56) * mm, "end": v(-50.4, 8.55) * mm});
            skLineSegment(sketch, "E754", {"start": v(-50.4, 8.55) * mm, "end": v(-51.03, 8.54) * mm});
            skLineSegment(sketch, "E755", {"start": v(-51.03, 8.54) * mm, "end": v(-51.66, 8.53) * mm});
            skLineSegment(sketch, "E756", {"start": v(-51.66, 8.53) * mm, "end": v(-52.3, 8.52) * mm});
            skLineSegment(sketch, "E757", {"start": v(-52.3, 8.52) * mm, "end": v(-52.93, 8.5) * mm});
            skLineSegment(sketch, "E758", {"start": v(-52.93, 8.5) * mm, "end": v(-53.57, 8.5) * mm});
            skLineSegment(sketch, "E759", {"start": v(-53.57, 8.5) * mm, "end": v(-54.2, 8.48) * mm});
            skLineSegment(sketch, "E760", {"start": v(-54.2, 8.48) * mm, "end": v(-54.84, 8.47) * mm});
            skLineSegment(sketch, "E761", {"start": v(-54.84, 8.47) * mm, "end": v(-55.47, 8.45) * mm});
            skLineSegment(sketch, "E762", {"start": v(-55.47, 8.45) * mm, "end": v(-56.1, 8.44) * mm});
            skLineSegment(sketch, "E763", {"start": v(-56.1, 8.44) * mm, "end": v(-56.74, 8.42) * mm});
            skLineSegment(sketch, "E764", {"start": v(-56.74, 8.42) * mm, "end": v(-57.37, 8.4) * mm});
            skLineSegment(sketch, "E765", {"start": v(-57.37, 8.4) * mm, "end": v(-58, 8.39) * mm});
            skLineSegment(sketch, "E766", {"start": v(-58, 8.39) * mm, "end": v(-58.64, 8.37) * mm});
            skLineSegment(sketch, "E767", {"start": v(-58.64, 8.37) * mm, "end": v(-59.28, 8.35) * mm});
            skLineSegment(sketch, "E768", {"start": v(-59.28, 8.35) * mm, "end": v(-59.91, 8.33) * mm});
            skLineSegment(sketch, "E769", {"start": v(-59.91, 8.33) * mm, "end": v(-60.55, 8.3) * mm});
            skLineSegment(sketch, "E770", {"start": v(-60.55, 8.3) * mm, "end": v(-61.18, 8.29) * mm});
            skLineSegment(sketch, "E771", {"start": v(-61.18, 8.29) * mm, "end": v(-61.82, 8.27) * mm});
            skLineSegment(sketch, "E772", {"start": v(-61.82, 8.27) * mm, "end": v(-62.45, 8.24) * mm});
            skLineSegment(sketch, "E773", {"start": v(-62.45, 8.24) * mm, "end": v(-63.09, 8.22) * mm});
            skLineSegment(sketch, "E774", {"start": v(-63.09, 8.22) * mm, "end": v(-63.72, 8.2) * mm});
            skLineSegment(sketch, "E775", {"start": v(-63.72, 8.2) * mm, "end": v(-64.36, 8.17) * mm});
            skLineSegment(sketch, "E776", {"start": v(-64.36, 8.17) * mm, "end": v(-65, 8.14) * mm});
            skLineSegment(sketch, "E777", {"start": v(-65, 8.14) * mm, "end": v(-65.63, 8.12) * mm});
            skLineSegment(sketch, "E778", {"start": v(-65.63, 8.12) * mm, "end": v(-66.26, 8.09) * mm});
            skLineSegment(sketch, "E779", {"start": v(-66.26, 8.09) * mm, "end": v(-66.9, 8.06) * mm});
            skLineSegment(sketch, "E780", {"start": v(-66.9, 8.06) * mm, "end": v(-67.53, 8.03) * mm});
            skLineSegment(sketch, "E781", {"start": v(-67.53, 8.03) * mm, "end": v(-68.16, 8) * mm});
            skLineSegment(sketch, "E782", {"start": v(-68.16, 8) * mm, "end": v(-68.8, 7.97) * mm});
            skLineSegment(sketch, "E783", {"start": v(-68.8, 7.97) * mm, "end": v(-69.43, 7.94) * mm});
            skLineSegment(sketch, "E784", {"start": v(-69.43, 7.94) * mm, "end": v(-70.07, 7.9) * mm});
            skLineSegment(sketch, "E785", {"start": v(-70.07, 7.9) * mm, "end": v(-70.7, 7.87) * mm});
            skLineSegment(sketch, "E786", {"start": v(-70.7, 7.87) * mm, "end": v(-71.34, 7.84) * mm});
            skLineSegment(sketch, "E787", {"start": v(-71.34, 7.84) * mm, "end": v(-71.97, 7.8) * mm});
            skLineSegment(sketch, "E788", {"start": v(-71.97, 7.8) * mm, "end": v(-72.6, 7.76) * mm});
            skLineSegment(sketch, "E789", {"start": v(-72.6, 7.76) * mm, "end": v(-73.24, 7.73) * mm});
            skLineSegment(sketch, "E790", {"start": v(-73.24, 7.73) * mm, "end": v(-73.88, 7.69) * mm});
            skLineSegment(sketch, "E791", {"start": v(-73.88, 7.69) * mm, "end": v(-74.51, 7.65) * mm});
            skLineSegment(sketch, "E792", {"start": v(-74.51, 7.65) * mm, "end": v(-75.15, 7.6) * mm});
            skLineSegment(sketch, "E793", {"start": v(-75.15, 7.6) * mm, "end": v(-75.78, 7.57) * mm});
            skLineSegment(sketch, "E794", {"start": v(-75.78, 7.57) * mm, "end": v(-76.42, 7.52) * mm});
            skLineSegment(sketch, "E795", {"start": v(-76.42, 7.52) * mm, "end": v(-77.05, 7.48) * mm});
            skLineSegment(sketch, "E796", {"start": v(-77.05, 7.48) * mm, "end": v(-77.68, 7.44) * mm});
            skLineSegment(sketch, "E797", {"start": v(-77.68, 7.44) * mm, "end": v(-78.32, 7.39) * mm});
            skLineSegment(sketch, "E798", {"start": v(-78.32, 7.39) * mm, "end": v(-78.95, 7.34) * mm});
            skLineSegment(sketch, "E799", {"start": v(-78.95, 7.34) * mm, "end": v(-79.59, 7.3) * mm});
            skLineSegment(sketch, "E800", {"start": v(-79.59, 7.3) * mm, "end": v(-80.22, 7.24) * mm});
            skLineSegment(sketch, "E801", {"start": v(-80.22, 7.24) * mm, "end": v(-80.86, 7.2) * mm});
            skLineSegment(sketch, "E802", {"start": v(-80.86, 7.2) * mm, "end": v(-81.5, 7.14) * mm});
            skLineSegment(sketch, "E803", {"start": v(-81.5, 7.14) * mm, "end": v(-82.13, 7.09) * mm});
            skLineSegment(sketch, "E804", {"start": v(-82.13, 7.09) * mm, "end": v(-82.76, 7.03) * mm});
            skLineSegment(sketch, "E805", {"start": v(-82.76, 7.03) * mm, "end": v(-83.4, 6.98) * mm});
            skLineSegment(sketch, "E806", {"start": v(-83.4, 6.98) * mm, "end": v(-84.03, 6.92) * mm});
            skLineSegment(sketch, "E807", {"start": v(-84.03, 6.92) * mm, "end": v(-84.67, 6.86) * mm});
            skLineSegment(sketch, "E808", {"start": v(-84.67, 6.86) * mm, "end": v(-85.3, 6.8) * mm});
            skLineSegment(sketch, "E809", {"start": v(-85.3, 6.8) * mm, "end": v(-85.93, 6.74) * mm});
            skLineSegment(sketch, "E810", {"start": v(-85.93, 6.74) * mm, "end": v(-86.57, 6.68) * mm});
            skLineSegment(sketch, "E811", {"start": v(-86.57, 6.68) * mm, "end": v(-87.2, 6.61) * mm});
            skLineSegment(sketch, "E812", {"start": v(-87.2, 6.61) * mm, "end": v(-87.84, 6.55) * mm});
            skLineSegment(sketch, "E813", {"start": v(-87.84, 6.55) * mm, "end": v(-88.47, 6.48) * mm});
            skLineSegment(sketch, "E814", {"start": v(-88.47, 6.48) * mm, "end": v(-89.1, 6.4) * mm});
            skLineSegment(sketch, "E815", {"start": v(-89.1, 6.4) * mm, "end": v(-89.74, 6.34) * mm});
            skLineSegment(sketch, "E816", {"start": v(-89.74, 6.34) * mm, "end": v(-90.38, 6.27) * mm});
            skLineSegment(sketch, "E817", {"start": v(-90.38, 6.27) * mm, "end": v(-91.01, 6.2) * mm});
            skLineSegment(sketch, "E818", {"start": v(-91.01, 6.2) * mm, "end": v(-91.64, 6.12) * mm});
            skLineSegment(sketch, "E819", {"start": v(-91.64, 6.12) * mm, "end": v(-92.28, 6.04) * mm});
            skLineSegment(sketch, "E820", {"start": v(-92.28, 6.04) * mm, "end": v(-92.91, 5.96) * mm});
            skLineSegment(sketch, "E821", {"start": v(-92.91, 5.96) * mm, "end": v(-93.55, 5.88) * mm});
            skLineSegment(sketch, "E822", {"start": v(-93.55, 5.88) * mm, "end": v(-94.18, 5.8) * mm});
            skLineSegment(sketch, "E823", {"start": v(-94.18, 5.8) * mm, "end": v(-94.82, 5.71) * mm});
            skLineSegment(sketch, "E824", {"start": v(-94.82, 5.71) * mm, "end": v(-95.45, 5.63) * mm});
            skLineSegment(sketch, "E825", {"start": v(-95.45, 5.63) * mm, "end": v(-96.09, 5.54) * mm});
            skLineSegment(sketch, "E826", {"start": v(-96.09, 5.54) * mm, "end": v(-96.72, 5.45) * mm});
            skLineSegment(sketch, "E827", {"start": v(-96.72, 5.45) * mm, "end": v(-97.35, 5.36) * mm});
            skLineSegment(sketch, "E828", {"start": v(-97.35, 5.36) * mm, "end": v(-97.99, 5.26) * mm});
            skLineSegment(sketch, "E829", {"start": v(-97.99, 5.26) * mm, "end": v(-98.62, 5.17) * mm});
            skLineSegment(sketch, "E830", {"start": v(-98.62, 5.17) * mm, "end": v(-99.26, 5.07) * mm});
            skLineSegment(sketch, "E831", {"start": v(-99.26, 5.07) * mm, "end": v(-99.9, 4.97) * mm});
            skLineSegment(sketch, "E832", {"start": v(-99.9, 4.97) * mm, "end": v(-100.52, 4.86) * mm});
            skLineSegment(sketch, "E833", {"start": v(-100.52, 4.86) * mm, "end": v(-101.16, 4.76) * mm});
            skLineSegment(sketch, "E834", {"start": v(-101.16, 4.76) * mm, "end": v(-101.8, 4.65) * mm});
            skLineSegment(sketch, "E835", {"start": v(-101.8, 4.65) * mm, "end": v(-102.43, 4.54) * mm});
            skLineSegment(sketch, "E836", {"start": v(-102.43, 4.54) * mm, "end": v(-103.06, 4.42) * mm});
            skLineSegment(sketch, "E837", {"start": v(-103.06, 4.42) * mm, "end": v(-103.7, 4.3) * mm});
            skLineSegment(sketch, "E838", {"start": v(-103.7, 4.3) * mm, "end": v(-104.33, 4.19) * mm});
            skLineSegment(sketch, "E839", {"start": v(-104.33, 4.19) * mm, "end": v(-104.96, 4.06) * mm});
            skLineSegment(sketch, "E840", {"start": v(-104.96, 4.06) * mm, "end": v(-105.6, 3.94) * mm});
            skLineSegment(sketch, "E841", {"start": v(-105.6, 3.94) * mm, "end": v(-106.23, 3.8) * mm});
            skLineSegment(sketch, "E842", {"start": v(-106.23, 3.8) * mm, "end": v(-106.87, 3.68) * mm});
            skLineSegment(sketch, "E843", {"start": v(-106.87, 3.68) * mm, "end": v(-107.5, 3.54) * mm});
            skLineSegment(sketch, "E844", {"start": v(-107.5, 3.54) * mm, "end": v(-108.13, 3.4) * mm});
            skLineSegment(sketch, "E845", {"start": v(-108.13, 3.4) * mm, "end": v(-108.77, 3.26) * mm});
            skLineSegment(sketch, "E846", {"start": v(-108.77, 3.26) * mm, "end": v(-109.4, 3.11) * mm});
            skLineSegment(sketch, "E847", {"start": v(-109.4, 3.11) * mm, "end": v(-110.03, 2.96) * mm});
            skLineSegment(sketch, "E848", {"start": v(-110.03, 2.96) * mm, "end": v(-110.67, 2.8) * mm});
            skLineSegment(sketch, "E849", {"start": v(-110.67, 2.8) * mm, "end": v(-111.3, 2.65) * mm});
            skLineSegment(sketch, "E850", {"start": v(-111.3, 2.65) * mm, "end": v(-111.93, 2.48) * mm});
            skLineSegment(sketch, "E851", {"start": v(-111.93, 2.48) * mm, "end": v(-112.57, 2.31) * mm});
            skLineSegment(sketch, "E852", {"start": v(-112.57, 2.31) * mm, "end": v(-113.2, 2.14) * mm});
            skLineSegment(sketch, "E853", {"start": v(-113.2, 2.14) * mm, "end": v(-113.83, 1.96) * mm});
            skLineSegment(sketch, "E854", {"start": v(-113.83, 1.96) * mm, "end": v(-114.47, 1.77) * mm});
            skLineSegment(sketch, "E855", {"start": v(-114.47, 1.77) * mm, "end": v(-115.1, 1.58) * mm});
            skLineSegment(sketch, "E856", {"start": v(-115.1, 1.58) * mm, "end": v(-115.73, 1.38) * mm});
            skLineSegment(sketch, "E857", {"start": v(-115.73, 1.38) * mm, "end": v(-116.37, 1.17) * mm});
            skLineSegment(sketch, "E858", {"start": v(-116.37, 1.17) * mm, "end": v(-117, 0.96) * mm});
            skLineSegment(sketch, "E859", {"start": v(61.37, -4.36) * mm, "end": v(60.74, -4.38) * mm});
            skLineSegment(sketch, "E860", {"start": v(60.74, -4.38) * mm, "end": v(60.1, -4.4) * mm});
            skLineSegment(sketch, "E861", {"start": v(60.1, -4.4) * mm, "end": v(59.47, -4.43) * mm});
            skLineSegment(sketch, "E862", {"start": v(59.47, -4.43) * mm, "end": v(58.83, -4.46) * mm});
            skLineSegment(sketch, "E863", {"start": v(58.83, -4.46) * mm, "end": v(58.2, -4.48) * mm});
            skLineSegment(sketch, "E864", {"start": v(58.2, -4.48) * mm, "end": v(57.56, -4.51) * mm});
            skLineSegment(sketch, "E865", {"start": v(57.56, -4.51) * mm, "end": v(56.93, -4.54) * mm});
            skLineSegment(sketch, "E866", {"start": v(56.93, -4.54) * mm, "end": v(56.3, -4.56) * mm});
            skLineSegment(sketch, "E867", {"start": v(56.3, -4.56) * mm, "end": v(55.66, -4.59) * mm});
            skLineSegment(sketch, "E868", {"start": v(55.66, -4.59) * mm, "end": v(55.02, -4.61) * mm});
            skLineSegment(sketch, "E869", {"start": v(55.02, -4.61) * mm, "end": v(54.39, -4.64) * mm});
            skLineSegment(sketch, "E870", {"start": v(54.39, -4.64) * mm, "end": v(53.75, -4.66) * mm});
            skLineSegment(sketch, "E871", {"start": v(53.75, -4.66) * mm, "end": v(53.12, -4.7) * mm});
            skLineSegment(sketch, "E872", {"start": v(53.12, -4.7) * mm, "end": v(52.48, -4.72) * mm});
            skLineSegment(sketch, "E873", {"start": v(52.48, -4.72) * mm, "end": v(51.85, -4.74) * mm});
            skLineSegment(sketch, "E874", {"start": v(51.85, -4.74) * mm, "end": v(51.21, -4.77) * mm});
            skLineSegment(sketch, "E875", {"start": v(51.21, -4.77) * mm, "end": v(50.58, -4.8) * mm});
            skLineSegment(sketch, "E876", {"start": v(50.58, -4.8) * mm, "end": v(49.94, -4.82) * mm});
            skLineSegment(sketch, "E877", {"start": v(49.94, -4.82) * mm, "end": v(49.3, -4.85) * mm});
            skLineSegment(sketch, "E878", {"start": v(49.3, -4.85) * mm, "end": v(48.67, -4.87) * mm});
            skLineSegment(sketch, "E879", {"start": v(48.67, -4.87) * mm, "end": v(48.04, -4.9) * mm});
            skLineSegment(sketch, "E880", {"start": v(48.04, -4.9) * mm, "end": v(47.4, -4.92) * mm});
            skLineSegment(sketch, "E881", {"start": v(47.4, -4.92) * mm, "end": v(46.77, -4.95) * mm});
            skLineSegment(sketch, "E882", {"start": v(46.77, -4.95) * mm, "end": v(46.13, -4.98) * mm});
            skLineSegment(sketch, "E883", {"start": v(46.13, -4.98) * mm, "end": v(45.5, -5) * mm});
            skLineSegment(sketch, "E884", {"start": v(45.5, -5) * mm, "end": v(44.86, -5.03) * mm});
            skLineSegment(sketch, "E885", {"start": v(44.86, -5.03) * mm, "end": v(44.23, -5.05) * mm});
            skLineSegment(sketch, "E886", {"start": v(44.23, -5.05) * mm, "end": v(43.6, -5.08) * mm});
            skLineSegment(sketch, "E887", {"start": v(43.6, -5.08) * mm, "end": v(42.96, -5.1) * mm});
            skLineSegment(sketch, "E888", {"start": v(42.96, -5.1) * mm, "end": v(42.32, -5.13) * mm});
            skLineSegment(sketch, "E889", {"start": v(42.32, -5.13) * mm, "end": v(41.69, -5.16) * mm});
            skLineSegment(sketch, "E890", {"start": v(41.69, -5.16) * mm, "end": v(41.05, -5.18) * mm});
            skLineSegment(sketch, "E891", {"start": v(41.05, -5.18) * mm, "end": v(40.42, -5.2) * mm});
            skLineSegment(sketch, "E892", {"start": v(40.42, -5.2) * mm, "end": v(39.78, -5.24) * mm});
            skLineSegment(sketch, "E893", {"start": v(39.78, -5.24) * mm, "end": v(39.15, -5.26) * mm});
            skLineSegment(sketch, "E894", {"start": v(39.15, -5.26) * mm, "end": v(38.51, -5.29) * mm});
            skLineSegment(sketch, "E895", {"start": v(38.51, -5.29) * mm, "end": v(37.88, -5.31) * mm});
            skLineSegment(sketch, "E896", {"start": v(37.88, -5.31) * mm, "end": v(37.24, -5.34) * mm});
            skLineSegment(sketch, "E897", {"start": v(37.24, -5.34) * mm, "end": v(36.6, -5.37) * mm});
            skLineSegment(sketch, "E898", {"start": v(36.6, -5.37) * mm, "end": v(35.97, -5.4) * mm});
            skLineSegment(sketch, "E899", {"start": v(35.97, -5.4) * mm, "end": v(35.34, -5.42) * mm});
            skLineSegment(sketch, "E900", {"start": v(35.34, -5.42) * mm, "end": v(34.7, -5.44) * mm});
            skLineSegment(sketch, "E901", {"start": v(34.7, -5.44) * mm, "end": v(34.07, -5.47) * mm});
            skLineSegment(sketch, "E902", {"start": v(34.07, -5.47) * mm, "end": v(33.43, -5.5) * mm});
            skLineSegment(sketch, "E903", {"start": v(33.43, -5.5) * mm, "end": v(32.8, -5.52) * mm});
            skLineSegment(sketch, "E904", {"start": v(32.8, -5.52) * mm, "end": v(32.16, -5.55) * mm});
            skLineSegment(sketch, "E905", {"start": v(32.16, -5.55) * mm, "end": v(31.53, -5.57) * mm});
            skLineSegment(sketch, "E906", {"start": v(31.53, -5.57) * mm, "end": v(30.9, -5.6) * mm});
            skLineSegment(sketch, "E907", {"start": v(30.9, -5.6) * mm, "end": v(30.26, -5.63) * mm});
            skLineSegment(sketch, "E908", {"start": v(30.26, -5.63) * mm, "end": v(29.62, -5.65) * mm});
            skLineSegment(sketch, "E909", {"start": v(29.62, -5.65) * mm, "end": v(28.99, -5.68) * mm});
            skLineSegment(sketch, "E910", {"start": v(28.99, -5.68) * mm, "end": v(28.35, -5.7) * mm});
            skLineSegment(sketch, "E911", {"start": v(28.35, -5.7) * mm, "end": v(27.72, -5.73) * mm});
            skLineSegment(sketch, "E912", {"start": v(27.72, -5.73) * mm, "end": v(27.08, -5.76) * mm});
            skLineSegment(sketch, "E913", {"start": v(27.08, -5.76) * mm, "end": v(26.45, -5.78) * mm});
            skLineSegment(sketch, "E914", {"start": v(26.45, -5.78) * mm, "end": v(25.81, -5.8) * mm});
            skLineSegment(sketch, "E915", {"start": v(25.81, -5.8) * mm, "end": v(25.18, -5.84) * mm});
            skLineSegment(sketch, "E916", {"start": v(25.18, -5.84) * mm, "end": v(24.54, -5.86) * mm});
            skLineSegment(sketch, "E917", {"start": v(24.54, -5.86) * mm, "end": v(23.9, -5.89) * mm});
            skLineSegment(sketch, "E918", {"start": v(23.9, -5.89) * mm, "end": v(23.27, -5.91) * mm});
            skLineSegment(sketch, "E919", {"start": v(23.27, -5.91) * mm, "end": v(22.64, -5.94) * mm});
            skLineSegment(sketch, "E920", {"start": v(22.64, -5.94) * mm, "end": v(22, -5.97) * mm});
            skLineSegment(sketch, "E921", {"start": v(22, -5.97) * mm, "end": v(21.37, -6) * mm});
            skLineSegment(sketch, "E922", {"start": v(21.37, -6) * mm, "end": v(20.73, -6.02) * mm});
            skLineSegment(sketch, "E923", {"start": v(20.73, -6.02) * mm, "end": v(20.1, -6.04) * mm});
            skLineSegment(sketch, "E924", {"start": v(20.1, -6.04) * mm, "end": v(19.46, -6.07) * mm});
            skLineSegment(sketch, "E925", {"start": v(19.46, -6.07) * mm, "end": v(18.83, -6.1) * mm});
            skLineSegment(sketch, "E926", {"start": v(18.83, -6.1) * mm, "end": v(18.2, -6.12) * mm});
            skLineSegment(sketch, "E927", {"start": v(18.2, -6.12) * mm, "end": v(17.56, -6.15) * mm});
            skLineSegment(sketch, "E928", {"start": v(17.56, -6.15) * mm, "end": v(16.92, -6.17) * mm});
            skLineSegment(sketch, "E929", {"start": v(16.92, -6.17) * mm, "end": v(16.29, -6.2) * mm});
            skLineSegment(sketch, "E930", {"start": v(16.29, -6.2) * mm, "end": v(15.65, -6.22) * mm});
            skLineSegment(sketch, "E931", {"start": v(15.65, -6.22) * mm, "end": v(15.02, -6.25) * mm});
            skLineSegment(sketch, "E932", {"start": v(15.02, -6.25) * mm, "end": v(14.38, -6.27) * mm});
            skLineSegment(sketch, "E933", {"start": v(14.38, -6.27) * mm, "end": v(13.75, -6.3) * mm});
            skLineSegment(sketch, "E934", {"start": v(13.75, -6.3) * mm, "end": v(13.11, -6.32) * mm});
            skLineSegment(sketch, "E935", {"start": v(13.11, -6.32) * mm, "end": v(12.48, -6.35) * mm});
            skLineSegment(sketch, "E936", {"start": v(12.48, -6.35) * mm, "end": v(11.84, -6.37) * mm});
            skLineSegment(sketch, "E937", {"start": v(11.84, -6.37) * mm, "end": v(11.2, -6.4) * mm});
            skLineSegment(sketch, "E938", {"start": v(11.2, -6.4) * mm, "end": v(10.57, -6.42) * mm});
            skLineSegment(sketch, "E939", {"start": v(10.57, -6.42) * mm, "end": v(9.94, -6.45) * mm});
            skLineSegment(sketch, "E940", {"start": v(9.94, -6.45) * mm, "end": v(9.3, -6.47) * mm});
            skLineSegment(sketch, "E941", {"start": v(9.3, -6.47) * mm, "end": v(8.67, -6.5) * mm});
            skLineSegment(sketch, "E942", {"start": v(8.67, -6.5) * mm, "end": v(8.03, -6.52) * mm});
            skLineSegment(sketch, "E943", {"start": v(8.03, -6.52) * mm, "end": v(7.4, -6.55) * mm});
            skLineSegment(sketch, "E944", {"start": v(7.4, -6.55) * mm, "end": v(6.76, -6.57) * mm});
            skLineSegment(sketch, "E945", {"start": v(6.76, -6.57) * mm, "end": v(6.13, -6.6) * mm});
            skLineSegment(sketch, "E946", {"start": v(6.13, -6.6) * mm, "end": v(5.5, -6.62) * mm});
            skLineSegment(sketch, "E947", {"start": v(5.5, -6.62) * mm, "end": v(4.86, -6.64) * mm});
            skLineSegment(sketch, "E948", {"start": v(4.86, -6.64) * mm, "end": v(4.22, -6.67) * mm});
            skLineSegment(sketch, "E949", {"start": v(4.22, -6.67) * mm, "end": v(3.59, -6.7) * mm});
            skLineSegment(sketch, "E950", {"start": v(3.59, -6.7) * mm, "end": v(2.95, -6.72) * mm});
            skLineSegment(sketch, "E951", {"start": v(2.95, -6.72) * mm, "end": v(2.32, -6.74) * mm});
            skLineSegment(sketch, "E952", {"start": v(2.32, -6.74) * mm, "end": v(1.68, -6.76) * mm});
            skLineSegment(sketch, "E953", {"start": v(1.68, -6.76) * mm, "end": v(1.05, -6.79) * mm});
            skLineSegment(sketch, "E954", {"start": v(1.05, -6.79) * mm, "end": v(0.41, -6.81) * mm});
            skLineSegment(sketch, "E955", {"start": v(0.41, -6.81) * mm, "end": v(-0.22, -6.84) * mm});
            skLineSegment(sketch, "E956", {"start": v(-0.22, -6.84) * mm, "end": v(-0.86, -6.86) * mm});
            skLineSegment(sketch, "E957", {"start": v(-0.86, -6.86) * mm, "end": v(-1.5, -6.88) * mm});
            skLineSegment(sketch, "E958", {"start": v(-1.5, -6.88) * mm, "end": v(-2.13, -6.9) * mm});
            skLineSegment(sketch, "E959", {"start": v(-2.13, -6.9) * mm, "end": v(-2.76, -6.93) * mm});
            skLineSegment(sketch, "E960", {"start": v(-2.76, -6.93) * mm, "end": v(-3.4, -6.95) * mm});
            skLineSegment(sketch, "E961", {"start": v(-3.4, -6.95) * mm, "end": v(-4.03, -6.98) * mm});
            skLineSegment(sketch, "E962", {"start": v(-4.03, -6.98) * mm, "end": v(-4.67, -7) * mm});
            skLineSegment(sketch, "E963", {"start": v(-4.67, -7) * mm, "end": v(-5.3, -7.03) * mm});
            skLineSegment(sketch, "E964", {"start": v(-5.3, -7.03) * mm, "end": v(-5.94, -7.05) * mm});
            skLineSegment(sketch, "E965", {"start": v(-5.94, -7.05) * mm, "end": v(-6.57, -7.07) * mm});
            skLineSegment(sketch, "E966", {"start": v(-6.57, -7.07) * mm, "end": v(-7.2, -7.1) * mm});
            skLineSegment(sketch, "E967", {"start": v(-7.2, -7.1) * mm, "end": v(-7.84, -7.12) * mm});
            skLineSegment(sketch, "E968", {"start": v(-7.84, -7.12) * mm, "end": v(-8.48, -7.14) * mm});
            skLineSegment(sketch, "E969", {"start": v(-8.48, -7.14) * mm, "end": v(-9.11, -7.16) * mm});
            skLineSegment(sketch, "E970", {"start": v(-9.11, -7.16) * mm, "end": v(-9.75, -7.19) * mm});
            skLineSegment(sketch, "E971", {"start": v(-9.75, -7.19) * mm, "end": v(-10.38, -7.2) * mm});
            skLineSegment(sketch, "E972", {"start": v(-10.38, -7.2) * mm, "end": v(-11.02, -7.23) * mm});
            skLineSegment(sketch, "E973", {"start": v(-11.02, -7.23) * mm, "end": v(-11.65, -7.25) * mm});
            skLineSegment(sketch, "E974", {"start": v(-11.65, -7.25) * mm, "end": v(-12.29, -7.28) * mm});
            skLineSegment(sketch, "E975", {"start": v(-12.29, -7.28) * mm, "end": v(-12.92, -7.3) * mm});
            skLineSegment(sketch, "E976", {"start": v(-12.92, -7.3) * mm, "end": v(-13.56, -7.32) * mm});
            skLineSegment(sketch, "E977", {"start": v(-13.56, -7.32) * mm, "end": v(-14.2, -7.34) * mm});
            skLineSegment(sketch, "E978", {"start": v(-14.2, -7.34) * mm, "end": v(-14.83, -7.36) * mm});
            skLineSegment(sketch, "E979", {"start": v(-14.83, -7.36) * mm, "end": v(-15.46, -7.38) * mm});
            skLineSegment(sketch, "E980", {"start": v(-15.46, -7.38) * mm, "end": v(-16.1, -7.4) * mm});
            skLineSegment(sketch, "E981", {"start": v(-16.1, -7.4) * mm, "end": v(-16.73, -7.43) * mm});
            skLineSegment(sketch, "E982", {"start": v(-16.73, -7.43) * mm, "end": v(-17.37, -7.45) * mm});
            skLineSegment(sketch, "E983", {"start": v(-17.37, -7.45) * mm, "end": v(-18, -7.47) * mm});
            skLineSegment(sketch, "E984", {"start": v(-18, -7.47) * mm, "end": v(-18.64, -7.5) * mm});
            skLineSegment(sketch, "E985", {"start": v(-18.64, -7.5) * mm, "end": v(-19.27, -7.51) * mm});
            skLineSegment(sketch, "E986", {"start": v(-19.27, -7.51) * mm, "end": v(-19.9, -7.53) * mm});
            skLineSegment(sketch, "E987", {"start": v(-19.9, -7.53) * mm, "end": v(-20.54, -7.55) * mm});
            skLineSegment(sketch, "E988", {"start": v(-20.54, -7.55) * mm, "end": v(-21.18, -7.58) * mm});
            skLineSegment(sketch, "E989", {"start": v(-21.18, -7.58) * mm, "end": v(-21.81, -7.6) * mm});
            skLineSegment(sketch, "E990", {"start": v(-21.81, -7.6) * mm, "end": v(-22.45, -7.62) * mm});
            skLineSegment(sketch, "E991", {"start": v(-22.45, -7.62) * mm, "end": v(-23.08, -7.64) * mm});
            skLineSegment(sketch, "E992", {"start": v(-23.08, -7.64) * mm, "end": v(-23.72, -7.66) * mm});
            skLineSegment(sketch, "E993", {"start": v(-23.72, -7.66) * mm, "end": v(-24.35, -7.68) * mm});
            skLineSegment(sketch, "E994", {"start": v(-24.35, -7.68) * mm, "end": v(-24.99, -7.7) * mm});
            skLineSegment(sketch, "E995", {"start": v(-24.99, -7.7) * mm, "end": v(-25.62, -7.72) * mm});
            skLineSegment(sketch, "E996", {"start": v(-25.62, -7.72) * mm, "end": v(-26.26, -7.74) * mm});
            skLineSegment(sketch, "E997", {"start": v(-26.26, -7.74) * mm, "end": v(-26.9, -7.76) * mm});
            skLineSegment(sketch, "E998", {"start": v(-26.9, -7.76) * mm, "end": v(-27.53, -7.77) * mm});
            skLineSegment(sketch, "E999", {"start": v(-27.53, -7.77) * mm, "end": v(-28.16, -7.8) * mm});
            skLineSegment(sketch, "E1000", {"start": v(-28.16, -7.8) * mm, "end": v(-28.8, -7.81) * mm});
            skLineSegment(sketch, "E1001", {"start": v(-28.8, -7.81) * mm, "end": v(-29.43, -7.83) * mm});
            skLineSegment(sketch, "E1002", {"start": v(-29.43, -7.83) * mm, "end": v(-30.07, -7.85) * mm});
            skLineSegment(sketch, "E1003", {"start": v(-30.07, -7.85) * mm, "end": v(-30.7, -7.87) * mm});
            skLineSegment(sketch, "E1004", {"start": v(-30.7, -7.87) * mm, "end": v(-31.34, -7.89) * mm});
            skLineSegment(sketch, "E1005", {"start": v(-31.34, -7.89) * mm, "end": v(-31.97, -7.9) * mm});
            skLineSegment(sketch, "E1006", {"start": v(-31.97, -7.9) * mm, "end": v(-32.6, -7.92) * mm});
            skLineSegment(sketch, "E1007", {"start": v(-32.6, -7.92) * mm, "end": v(-33.24, -7.94) * mm});
            skLineSegment(sketch, "E1008", {"start": v(-33.24, -7.94) * mm, "end": v(-33.88, -7.96) * mm});
            skLineSegment(sketch, "E1009", {"start": v(-33.88, -7.96) * mm, "end": v(-34.51, -7.98) * mm});
            skLineSegment(sketch, "E1010", {"start": v(-34.51, -7.98) * mm, "end": v(-35.15, -8) * mm});
            skLineSegment(sketch, "E1011", {"start": v(-35.15, -8) * mm, "end": v(-35.78, -8.01) * mm});
            skLineSegment(sketch, "E1012", {"start": v(-35.78, -8.01) * mm, "end": v(-36.42, -8.03) * mm});
            skLineSegment(sketch, "E1013", {"start": v(-36.42, -8.03) * mm, "end": v(-37.05, -8.05) * mm});
            skLineSegment(sketch, "E1014", {"start": v(-37.05, -8.05) * mm, "end": v(-37.69, -8.06) * mm});
            skLineSegment(sketch, "E1015", {"start": v(-37.69, -8.06) * mm, "end": v(-38.32, -8.08) * mm});
            skLineSegment(sketch, "E1016", {"start": v(-38.32, -8.08) * mm, "end": v(-38.96, -8.1) * mm});
            skLineSegment(sketch, "E1017", {"start": v(-38.96, -8.1) * mm, "end": v(-39.6, -8.11) * mm});
            skLineSegment(sketch, "E1018", {"start": v(-39.6, -8.11) * mm, "end": v(-40.23, -8.13) * mm});
            skLineSegment(sketch, "E1019", {"start": v(-40.23, -8.13) * mm, "end": v(-40.86, -8.14) * mm});
            skLineSegment(sketch, "E1020", {"start": v(-40.86, -8.14) * mm, "end": v(-41.5, -8.16) * mm});
            skLineSegment(sketch, "E1021", {"start": v(-41.5, -8.16) * mm, "end": v(-42.13, -8.17) * mm});
            skLineSegment(sketch, "E1022", {"start": v(-42.13, -8.17) * mm, "end": v(-42.77, -8.19) * mm});
            skLineSegment(sketch, "E1023", {"start": v(-42.77, -8.19) * mm, "end": v(-43.4, -8.2) * mm});
            skLineSegment(sketch, "E1024", {"start": v(-43.4, -8.2) * mm, "end": v(-44.04, -8.22) * mm});
            skLineSegment(sketch, "E1025", {"start": v(-44.04, -8.22) * mm, "end": v(-44.68, -8.23) * mm});
            skLineSegment(sketch, "E1026", {"start": v(-44.68, -8.23) * mm, "end": v(-45.31, -8.25) * mm});
            skLineSegment(sketch, "E1027", {"start": v(-45.31, -8.25) * mm, "end": v(-45.95, -8.26) * mm});
            skLineSegment(sketch, "E1028", {"start": v(-45.95, -8.26) * mm, "end": v(-46.58, -8.28) * mm});
            skLineSegment(sketch, "E1029", {"start": v(-46.58, -8.28) * mm, "end": v(-47.22, -8.3) * mm});
            skLineSegment(sketch, "E1030", {"start": v(-47.22, -8.3) * mm, "end": v(-47.85, -8.3) * mm});
            skLineSegment(sketch, "E1031", {"start": v(-47.85, -8.3) * mm, "end": v(-48.49, -8.32) * mm});
            skLineSegment(sketch, "E1032", {"start": v(-48.49, -8.32) * mm, "end": v(-49.12, -8.33) * mm});
            skLineSegment(sketch, "E1033", {"start": v(-49.12, -8.33) * mm, "end": v(-49.76, -8.34) * mm});
            skLineSegment(sketch, "E1034", {"start": v(-49.76, -8.34) * mm, "end": v(-50.4, -8.36) * mm});
            skLineSegment(sketch, "E1035", {"start": v(-50.4, -8.36) * mm, "end": v(-51.03, -8.37) * mm});
            skLineSegment(sketch, "E1036", {"start": v(-51.03, -8.37) * mm, "end": v(-51.66, -8.38) * mm});
            skLineSegment(sketch, "E1037", {"start": v(-51.66, -8.38) * mm, "end": v(-52.3, -8.4) * mm});
            skLineSegment(sketch, "E1038", {"start": v(-52.3, -8.4) * mm, "end": v(-52.93, -8.4) * mm});
            skLineSegment(sketch, "E1039", {"start": v(-52.93, -8.4) * mm, "end": v(-53.57, -8.42) * mm});
            skLineSegment(sketch, "E1040", {"start": v(-53.57, -8.42) * mm, "end": v(-54.2, -8.43) * mm});
            skLineSegment(sketch, "E1041", {"start": v(-54.2, -8.43) * mm, "end": v(-54.84, -8.44) * mm});
            skLineSegment(sketch, "E1042", {"start": v(-54.84, -8.44) * mm, "end": v(-55.47, -8.45) * mm});
            skLineSegment(sketch, "E1043", {"start": v(-55.47, -8.45) * mm, "end": v(-56.1, -8.46) * mm});
            skLineSegment(sketch, "E1044", {"start": v(-56.1, -8.46) * mm, "end": v(-56.74, -8.47) * mm});
            skLineSegment(sketch, "E1045", {"start": v(-56.74, -8.47) * mm, "end": v(-57.38, -8.48) * mm});
            skLineSegment(sketch, "E1046", {"start": v(-57.38, -8.48) * mm, "end": v(-58.01, -8.5) * mm});
            skLineSegment(sketch, "E1047", {"start": v(-58.01, -8.5) * mm, "end": v(-58.65, -8.5) * mm});
            skLineSegment(sketch, "E1048", {"start": v(-58.65, -8.5) * mm, "end": v(-59.28, -8.5) * mm});
            skLineSegment(sketch, "E1049", {"start": v(-59.28, -8.5) * mm, "end": v(-59.92, -8.52) * mm});
            skLineSegment(sketch, "E1050", {"start": v(-59.92, -8.52) * mm, "end": v(-60.55, -8.53) * mm});
            skLineSegment(sketch, "E1051", {"start": v(-60.55, -8.53) * mm, "end": v(-61.19, -8.53) * mm});
            skLineSegment(sketch, "E1052", {"start": v(-61.19, -8.53) * mm, "end": v(-61.82, -8.54) * mm});
            skLineSegment(sketch, "E1053", {"start": v(-61.82, -8.54) * mm, "end": v(-62.46, -8.55) * mm});
            skLineSegment(sketch, "E1054", {"start": v(-62.46, -8.55) * mm, "end": v(-63.1, -8.56) * mm});
            skLineSegment(sketch, "E1055", {"start": v(-63.1, -8.56) * mm, "end": v(-63.73, -8.56) * mm});
            skLineSegment(sketch, "E1056", {"start": v(-63.73, -8.56) * mm, "end": v(-64.36, -8.57) * mm});
            skLineSegment(sketch, "E1057", {"start": v(-64.36, -8.57) * mm, "end": v(-65, -8.57) * mm});
            skLineSegment(sketch, "E1058", {"start": v(-65, -8.57) * mm, "end": v(-65.63, -8.58) * mm});
            skLineSegment(sketch, "E1059", {"start": v(-65.63, -8.58) * mm, "end": v(-66.27, -8.59) * mm});
            skLineSegment(sketch, "E1060", {"start": v(-66.27, -8.59) * mm, "end": v(-66.9, -8.6) * mm});
            skLineSegment(sketch, "E1061", {"start": v(-66.9, -8.6) * mm, "end": v(-67.54, -8.6) * mm});
            skLineSegment(sketch, "E1062", {"start": v(-67.54, -8.6) * mm, "end": v(-68.17, -8.6) * mm});
            skLineSegment(sketch, "E1063", {"start": v(-68.17, -8.6) * mm, "end": v(-68.8, -8.6) * mm});
            skLineSegment(sketch, "E1064", {"start": v(-68.8, -8.6) * mm, "end": v(-69.44, -8.6) * mm});
            skLineSegment(sketch, "E1065", {"start": v(-69.44, -8.6) * mm, "end": v(-70.08, -8.6) * mm});
            skLineSegment(sketch, "E1066", {"start": v(-70.08, -8.6) * mm, "end": v(-70.71, -8.61) * mm});
            skLineSegment(sketch, "E1067", {"start": v(-70.71, -8.61) * mm, "end": v(-71.35, -8.61) * mm});
            skLineSegment(sketch, "E1068", {"start": v(-71.35, -8.61) * mm, "end": v(-71.98, -8.62) * mm});
            skLineSegment(sketch, "E1069", {"start": v(-71.98, -8.62) * mm, "end": v(-72.62, -8.62) * mm});
            skLineSegment(sketch, "E1070", {"start": v(-72.62, -8.62) * mm, "end": v(-73.25, -8.62) * mm});
            skLineSegment(sketch, "E1071", {"start": v(-73.25, -8.62) * mm, "end": v(-73.89, -8.62) * mm});
            skLineSegment(sketch, "E1072", {"start": v(-73.89, -8.62) * mm, "end": v(-74.52, -8.62) * mm});
            skLineSegment(sketch, "E1073", {"start": v(-74.52, -8.62) * mm, "end": v(-75.16, -8.62) * mm});
            skLineSegment(sketch, "E1074", {"start": v(-75.16, -8.62) * mm, "end": v(-75.8, -8.62) * mm});
            skLineSegment(sketch, "E1075", {"start": v(-75.8, -8.62) * mm, "end": v(-76.43, -8.62) * mm});
            skLineSegment(sketch, "E1076", {"start": v(-76.43, -8.62) * mm, "end": v(-77.06, -8.61) * mm});
            skLineSegment(sketch, "E1077", {"start": v(-77.06, -8.61) * mm, "end": v(-77.7, -8.61) * mm});
            skLineSegment(sketch, "E1078", {"start": v(-77.7, -8.61) * mm, "end": v(-78.33, -8.6) * mm});
            skLineSegment(sketch, "E1079", {"start": v(-78.33, -8.6) * mm, "end": v(-78.97, -8.6) * mm});
            skLineSegment(sketch, "E1080", {"start": v(-78.97, -8.6) * mm, "end": v(-79.6, -8.6) * mm});
            skLineSegment(sketch, "E1081", {"start": v(-79.6, -8.6) * mm, "end": v(-80.24, -8.6) * mm});
            skLineSegment(sketch, "E1082", {"start": v(-80.24, -8.6) * mm, "end": v(-80.87, -8.59) * mm});
            skLineSegment(sketch, "E1083", {"start": v(-80.87, -8.59) * mm, "end": v(-81.5, -8.58) * mm});
            skLineSegment(sketch, "E1084", {"start": v(-81.5, -8.58) * mm, "end": v(-82.14, -8.58) * mm});
            skLineSegment(sketch, "E1085", {"start": v(-82.14, -8.58) * mm, "end": v(-82.78, -8.57) * mm});
            skLineSegment(sketch, "E1086", {"start": v(-82.78, -8.57) * mm, "end": v(-83.41, -8.56) * mm});
            skLineSegment(sketch, "E1087", {"start": v(-83.41, -8.56) * mm, "end": v(-84.05, -8.55) * mm});
            skLineSegment(sketch, "E1088", {"start": v(-84.05, -8.55) * mm, "end": v(-84.68, -8.54) * mm});
            skLineSegment(sketch, "E1089", {"start": v(-84.68, -8.54) * mm, "end": v(-85.32, -8.53) * mm});
            skLineSegment(sketch, "E1090", {"start": v(-85.32, -8.53) * mm, "end": v(-85.95, -8.52) * mm});
            skLineSegment(sketch, "E1091", {"start": v(-85.95, -8.52) * mm, "end": v(-86.59, -8.51) * mm});
            skLineSegment(sketch, "E1092", {"start": v(-86.59, -8.51) * mm, "end": v(-87.22, -8.5) * mm});
            skLineSegment(sketch, "E1093", {"start": v(-87.22, -8.5) * mm, "end": v(-87.86, -8.49) * mm});
            skLineSegment(sketch, "E1094", {"start": v(-87.86, -8.49) * mm, "end": v(-88.5, -8.47) * mm});
            skLineSegment(sketch, "E1095", {"start": v(-88.5, -8.47) * mm, "end": v(-89.13, -8.46) * mm});
            skLineSegment(sketch, "E1096", {"start": v(-89.13, -8.46) * mm, "end": v(-89.76, -8.44) * mm});
            skLineSegment(sketch, "E1097", {"start": v(-89.76, -8.44) * mm, "end": v(-90.4, -8.43) * mm});
            skLineSegment(sketch, "E1098", {"start": v(-90.4, -8.43) * mm, "end": v(-91.03, -8.4) * mm});
            skLineSegment(sketch, "E1099", {"start": v(-91.03, -8.4) * mm, "end": v(-91.66, -8.4) * mm});
            skLineSegment(sketch, "E1100", {"start": v(-91.66, -8.4) * mm, "end": v(-92.3, -8.37) * mm});
            skLineSegment(sketch, "E1101", {"start": v(-92.3, -8.37) * mm, "end": v(-92.93, -8.35) * mm});
            skLineSegment(sketch, "E1102", {"start": v(-92.93, -8.35) * mm, "end": v(-93.57, -8.33) * mm});
            skLineSegment(sketch, "E1103", {"start": v(-93.57, -8.33) * mm, "end": v(-94.2, -8.31) * mm});
            skLineSegment(sketch, "E1104", {"start": v(-94.2, -8.31) * mm, "end": v(-94.84, -8.29) * mm});
            skLineSegment(sketch, "E1105", {"start": v(-94.84, -8.29) * mm, "end": v(-95.47, -8.26) * mm});
            skLineSegment(sketch, "E1106", {"start": v(-95.47, -8.26) * mm, "end": v(-96.1, -8.24) * mm});
            skLineSegment(sketch, "E1107", {"start": v(-96.1, -8.24) * mm, "end": v(-96.74, -8.21) * mm});
            skLineSegment(sketch, "E1108", {"start": v(-96.74, -8.21) * mm, "end": v(-97.38, -8.19) * mm});
            skLineSegment(sketch, "E1109", {"start": v(-97.38, -8.19) * mm, "end": v(-98.01, -8.16) * mm});
            skLineSegment(sketch, "E1110", {"start": v(-98.01, -8.16) * mm, "end": v(-98.64, -8.13) * mm});
            skLineSegment(sketch, "E1111", {"start": v(-98.64, -8.13) * mm, "end": v(-99.28, -8.1) * mm});
            skLineSegment(sketch, "E1112", {"start": v(-99.28, -8.1) * mm, "end": v(-99.91, -8.06) * mm});
            skLineSegment(sketch, "E1113", {"start": v(-99.91, -8.06) * mm, "end": v(-100.55, -8.03) * mm});
            skLineSegment(sketch, "E1114", {"start": v(-100.55, -8.03) * mm, "end": v(-101.18, -8) * mm});
            skLineSegment(sketch, "E1115", {"start": v(-101.18, -8) * mm, "end": v(-101.82, -7.96) * mm});
            skLineSegment(sketch, "E1116", {"start": v(-101.82, -7.96) * mm, "end": v(-102.45, -7.92) * mm});
            skLineSegment(sketch, "E1117", {"start": v(-102.45, -7.92) * mm, "end": v(-103.09, -7.88) * mm});
            skLineSegment(sketch, "E1118", {"start": v(-103.09, -7.88) * mm, "end": v(-103.72, -7.84) * mm});
            skLineSegment(sketch, "E1119", {"start": v(-103.72, -7.84) * mm, "end": v(-104.36, -7.8) * mm});
            skLineSegment(sketch, "E1120", {"start": v(-104.36, -7.8) * mm, "end": v(-104.99, -7.75) * mm});
            skLineSegment(sketch, "E1121", {"start": v(-104.99, -7.75) * mm, "end": v(-105.62, -7.7) * mm});
            skLineSegment(sketch, "E1122", {"start": v(-105.62, -7.7) * mm, "end": v(-106.26, -7.65) * mm});
            skLineSegment(sketch, "E1123", {"start": v(-106.26, -7.65) * mm, "end": v(-106.9, -7.6) * mm});
            skLineSegment(sketch, "E1124", {"start": v(-106.9, -7.6) * mm, "end": v(-107.53, -7.54) * mm});
            skLineSegment(sketch, "E1125", {"start": v(-107.53, -7.54) * mm, "end": v(-108.16, -7.49) * mm});
            skLineSegment(sketch, "E1126", {"start": v(-108.16, -7.49) * mm, "end": v(-108.8, -7.43) * mm});
            skLineSegment(sketch, "E1127", {"start": v(-108.8, -7.43) * mm, "end": v(-109.43, -7.37) * mm});
            skLineSegment(sketch, "E1128", {"start": v(-109.43, -7.37) * mm, "end": v(-110.06, -7.3) * mm});
            skLineSegment(sketch, "E1129", {"start": v(-110.06, -7.3) * mm, "end": v(-110.7, -7.24) * mm});
            skLineSegment(sketch, "E1130", {"start": v(-110.7, -7.24) * mm, "end": v(-111.33, -7.17) * mm});
            skLineSegment(sketch, "E1131", {"start": v(-111.33, -7.17) * mm, "end": v(-111.97, -7.1) * mm});
            skLineSegment(sketch, "E1132", {"start": v(-111.97, -7.1) * mm, "end": v(-112.6, -7.02) * mm});
            skLineSegment(sketch, "E1133", {"start": v(-112.6, -7.02) * mm, "end": v(-113.23, -6.94) * mm});
            skLineSegment(sketch, "E1134", {"start": v(-113.23, -6.94) * mm, "end": v(-113.87, -6.86) * mm});
            skLineSegment(sketch, "E1135", {"start": v(-113.87, -6.86) * mm, "end": v(-114.5, -6.78) * mm});
            skLineSegment(sketch, "E1136", {"start": v(-114.5, -6.78) * mm, "end": v(-115.13, -6.68) * mm});
            skLineSegment(sketch, "E1137", {"start": v(-115.13, -6.68) * mm, "end": v(-115.77, -6.58) * mm});
            skLineSegment(sketch, "E1138", {"start": v(-115.77, -6.58) * mm, "end": v(-116.4, -6.48) * mm});
            skLineSegment(sketch, "E1139", {"start": v(-116.4, -6.48) * mm, "end": v(-117.03, -6.38) * mm});
            skCircle(sketch, "E1140", {"center": v(-38.1, 0.27) * mm, "radius": 6 * mm});
            skLineSegment(sketch, "E1141", {"start": v(-44.1, 0.27) * mm, "end": v(-32.1, 0.27) * mm});
            skLineSegment(sketch, "E1142", {"start": v(-38.1, -2.73) * mm, "end": v(-38.1, 3.27) * mm});
            skCircle(sketch, "E1143", {"center": v(25.4, 0.1) * mm, "radius": 2 * mm});
            skLineSegment(sketch, "E1144", {"start": v(23.4, 0.1) * mm, "end": v(27.4, 0.1) * mm});
            skLineSegment(sketch, "E1145", {"start": v(25.4, -0.9) * mm, "end": v(25.4, 1.1) * mm});
            skSolve(sketch);
        }
        {
            var Q0;
            Q0 = qSketchRegion(id + "F0", true);
            extrude(context, id + "F1", {"entities" : qUnion([Q0]), "endBound" : BoundingType.SYMMETRIC, "depth" : 2 * mm, "offsetDistance" : 25 * mm});
        }
        {
            var Q0;
            Q0=qCreatedBy(makeId("Right.planeOp"),FACE);
            var sketch = newSketch(context, id + "F2", { "sketchPlane" : qUnion([Q0])});
            skLineSegment(sketch, "E1146", {"start": v(62.14, 4.18) * mm, "end": v(61.02, 4.3) * mm});
            skLineSegment(sketch, "E1147", {"start": v(61.02, 4.3) * mm, "end": v(58.73, 4.55) * mm});
            skLineSegment(sketch, "E1148", {"start": v(58.73, 4.55) * mm, "end": v(57.56, 4.68) * mm});
            skLineSegment(sketch, "E1149", {"start": v(57.56, 4.68) * mm, "end": v(56.38, 4.8) * mm});
            skLineSegment(sketch, "E1150", {"start": v(56.38, 4.8) * mm, "end": v(55.21, 4.92) * mm});
            skLineSegment(sketch, "E1151", {"start": v(55.21, 4.92) * mm, "end": v(54.04, 5.04) * mm});
            skLineSegment(sketch, "E1152", {"start": v(54.04, 5.04) * mm, "end": v(52.86, 5.16) * mm});
            skLineSegment(sketch, "E1153", {"start": v(52.86, 5.16) * mm, "end": v(51.7, 5.27) * mm});
            skLineSegment(sketch, "E1154", {"start": v(51.7, 5.27) * mm, "end": v(50.52, 5.39) * mm});
            skLineSegment(sketch, "E1155", {"start": v(50.52, 5.39) * mm, "end": v(49.34, 5.5) * mm});
            skLineSegment(sketch, "E1156", {"start": v(49.34, 5.5) * mm, "end": v(48.17, 5.61) * mm});
            skLineSegment(sketch, "E1157", {"start": v(48.17, 5.61) * mm, "end": v(46.95, 5.73) * mm});
            skLineSegment(sketch, "E1158", {"start": v(46.95, 5.73) * mm, "end": v(45.73, 5.84) * mm});
            skLineSegment(sketch, "E1159", {"start": v(45.73, 5.84) * mm, "end": v(44.51, 5.95) * mm});
            skLineSegment(sketch, "E1160", {"start": v(44.51, 5.95) * mm, "end": v(43.3, 6.06) * mm});
            skLineSegment(sketch, "E1161", {"start": v(43.3, 6.06) * mm, "end": v(42.07, 6.17) * mm});
            skLineSegment(sketch, "E1162", {"start": v(42.07, 6.17) * mm, "end": v(40.85, 6.28) * mm});
            skLineSegment(sketch, "E1163", {"start": v(40.85, 6.28) * mm, "end": v(39.63, 6.39) * mm});
            skLineSegment(sketch, "E1164", {"start": v(39.63, 6.39) * mm, "end": v(38.41, 6.5) * mm});
            skLineSegment(sketch, "E1165", {"start": v(38.41, 6.5) * mm, "end": v(37.2, 6.6) * mm});
            skLineSegment(sketch, "E1166", {"start": v(37.2, 6.6) * mm, "end": v(35.97, 6.7) * mm});
            skLineSegment(sketch, "E1167", {"start": v(35.97, 6.7) * mm, "end": v(34.72, 6.8) * mm});
            skLineSegment(sketch, "E1168", {"start": v(34.72, 6.8) * mm, "end": v(33.46, 6.9) * mm});
            skLineSegment(sketch, "E1169", {"start": v(33.46, 6.9) * mm, "end": v(32.2, 7) * mm});
            skLineSegment(sketch, "E1170", {"start": v(32.2, 7) * mm, "end": v(30.95, 7.1) * mm});
            skLineSegment(sketch, "E1171", {"start": v(30.95, 7.1) * mm, "end": v(29.7, 7.2) * mm});
            skLineSegment(sketch, "E1172", {"start": v(29.7, 7.2) * mm, "end": v(28.44, 7.29) * mm});
            skLineSegment(sketch, "E1173", {"start": v(28.44, 7.29) * mm, "end": v(27.19, 7.38) * mm});
            skLineSegment(sketch, "E1174", {"start": v(27.19, 7.38) * mm, "end": v(25.93, 7.47) * mm});
            skLineSegment(sketch, "E1175", {"start": v(25.93, 7.47) * mm, "end": v(24.68, 7.56) * mm});
            skLineSegment(sketch, "E1176", {"start": v(24.68, 7.56) * mm, "end": v(23.42, 7.65) * mm});
            skLineSegment(sketch, "E1177", {"start": v(23.42, 7.65) * mm, "end": v(22.15, 7.74) * mm});
            skLineSegment(sketch, "E1178", {"start": v(22.15, 7.74) * mm, "end": v(20.87, 7.83) * mm});
            skLineSegment(sketch, "E1179", {"start": v(20.87, 7.83) * mm, "end": v(19.6, 7.91) * mm});
            skLineSegment(sketch, "E1180", {"start": v(19.6, 7.91) * mm, "end": v(18.31, 8) * mm});
            skLineSegment(sketch, "E1181", {"start": v(18.31, 8) * mm, "end": v(17.04, 8.08) * mm});
            skLineSegment(sketch, "E1182", {"start": v(17.04, 8.08) * mm, "end": v(15.76, 8.16) * mm});
            skLineSegment(sketch, "E1183", {"start": v(15.76, 8.16) * mm, "end": v(14.48, 8.24) * mm});
            skLineSegment(sketch, "E1184", {"start": v(14.48, 8.24) * mm, "end": v(13.2, 8.32) * mm});
            skLineSegment(sketch, "E1185", {"start": v(13.2, 8.32) * mm, "end": v(11.93, 8.4) * mm});
            skLineSegment(sketch, "E1186", {"start": v(11.93, 8.4) * mm, "end": v(9.37, 8.55) * mm});
            skLineSegment(sketch, "E1187", {"start": v(9.37, 8.55) * mm, "end": v(8.08, 8.63) * mm});
            skLineSegment(sketch, "E1188", {"start": v(8.08, 8.63) * mm, "end": v(6.8, 8.7) * mm});
            skLineSegment(sketch, "E1189", {"start": v(6.8, 8.7) * mm, "end": v(5.51, 8.77) * mm});
            skLineSegment(sketch, "E1190", {"start": v(5.51, 8.77) * mm, "end": v(4.23, 8.84) * mm});
            skLineSegment(sketch, "E1191", {"start": v(4.23, 8.84) * mm, "end": v(2.94, 8.9) * mm});
            skLineSegment(sketch, "E1192", {"start": v(2.94, 8.9) * mm, "end": v(1.66, 8.97) * mm});
            skLineSegment(sketch, "E1193", {"start": v(1.66, 8.97) * mm, "end": v(0.38, 9.04) * mm});
            skLineSegment(sketch, "E1194", {"start": v(0.38, 9.04) * mm, "end": v(-0.9, 9.1) * mm});
            skLineSegment(sketch, "E1195", {"start": v(-0.9, 9.1) * mm, "end": v(-3.47, 9.22) * mm});
            skLineSegment(sketch, "E1196", {"start": v(-3.47, 9.22) * mm, "end": v(-4.75, 9.28) * mm});
            skLineSegment(sketch, "E1197", {"start": v(-4.75, 9.28) * mm, "end": v(-6.02, 9.33) * mm});
            skLineSegment(sketch, "E1198", {"start": v(-6.02, 9.33) * mm, "end": v(-7.3, 9.39) * mm});
            skLineSegment(sketch, "E1199", {"start": v(-7.3, 9.39) * mm, "end": v(-8.58, 9.44) * mm});
            skLineSegment(sketch, "E1200", {"start": v(-8.58, 9.44) * mm, "end": v(-9.86, 9.5) * mm});
            skLineSegment(sketch, "E1201", {"start": v(-9.86, 9.5) * mm, "end": v(-11.14, 9.54) * mm});
            skLineSegment(sketch, "E1202", {"start": v(-11.14, 9.54) * mm, "end": v(-12.41, 9.59) * mm});
            skLineSegment(sketch, "E1203", {"start": v(-12.41, 9.59) * mm, "end": v(-13.7, 9.63) * mm});
            skLineSegment(sketch, "E1204", {"start": v(-13.7, 9.63) * mm, "end": v(-16.23, 9.71) * mm});
            skLineSegment(sketch, "E1205", {"start": v(-16.23, 9.71) * mm, "end": v(-17.49, 9.75) * mm});
            skLineSegment(sketch, "E1206", {"start": v(-17.49, 9.75) * mm, "end": v(-18.74, 9.79) * mm});
            skLineSegment(sketch, "E1207", {"start": v(-18.74, 9.79) * mm, "end": v(-20, 9.82) * mm});
            skLineSegment(sketch, "E1208", {"start": v(-20, 9.82) * mm, "end": v(-21.26, 9.86) * mm});
            skLineSegment(sketch, "E1209", {"start": v(-21.26, 9.86) * mm, "end": v(-22.52, 9.89) * mm});
            skLineSegment(sketch, "E1210", {"start": v(-22.52, 9.89) * mm, "end": v(-23.78, 9.92) * mm});
            skLineSegment(sketch, "E1211", {"start": v(-23.78, 9.92) * mm, "end": v(-25.04, 9.94) * mm});
            skLineSegment(sketch, "E1212", {"start": v(-25.04, 9.94) * mm, "end": v(-26.3, 9.97) * mm});
            skLineSegment(sketch, "E1213", {"start": v(-26.3, 9.97) * mm, "end": v(-28.78, 10.01) * mm});
            skLineSegment(sketch, "E1214", {"start": v(-28.78, 10.01) * mm, "end": v(-30.01, 10.03) * mm});
            skLineSegment(sketch, "E1215", {"start": v(-30.01, 10.03) * mm, "end": v(-31.24, 10.05) * mm});
            skLineSegment(sketch, "E1216", {"start": v(-31.24, 10.05) * mm, "end": v(-32.47, 10.07) * mm});
            skLineSegment(sketch, "E1217", {"start": v(-32.47, 10.07) * mm, "end": v(-33.7, 10.08) * mm});
            skLineSegment(sketch, "E1218", {"start": v(-33.7, 10.08) * mm, "end": v(-34.92, 10.1) * mm});
            skLineSegment(sketch, "E1219", {"start": v(-34.92, 10.1) * mm, "end": v(-36.15, 10.1) * mm});
            skLineSegment(sketch, "E1220", {"start": v(-36.15, 10.1) * mm, "end": v(-37.38, 10.1) * mm});
            skLineSegment(sketch, "E1221", {"start": v(-37.38, 10.1) * mm, "end": v(-38.6, 10.11) * mm});
            skLineSegment(sketch, "E1222", {"start": v(-38.6, 10.11) * mm, "end": v(-39.83, 10.12) * mm});
            skLineSegment(sketch, "E1223", {"start": v(-39.83, 10.12) * mm, "end": v(-41.01, 10.12) * mm});
            skLineSegment(sketch, "E1224", {"start": v(-41.01, 10.12) * mm, "end": v(-42.2, 10.12) * mm});
            skLineSegment(sketch, "E1225", {"start": v(-42.2, 10.12) * mm, "end": v(-43.38, 10.11) * mm});
            skLineSegment(sketch, "E1226", {"start": v(-43.38, 10.11) * mm, "end": v(-44.56, 10.1) * mm});
            skLineSegment(sketch, "E1227", {"start": v(-44.56, 10.1) * mm, "end": v(-45.74, 10.1) * mm});
            skLineSegment(sketch, "E1228", {"start": v(-45.74, 10.1) * mm, "end": v(-46.93, 10.09) * mm});
            skLineSegment(sketch, "E1229", {"start": v(-46.93, 10.09) * mm, "end": v(-48.1, 10.08) * mm});
            skLineSegment(sketch, "E1230", {"start": v(-48.1, 10.08) * mm, "end": v(-49.3, 10.06) * mm});
            skLineSegment(sketch, "E1231", {"start": v(-49.3, 10.06) * mm, "end": v(-50.47, 10.05) * mm});
            skLineSegment(sketch, "E1232", {"start": v(-50.47, 10.05) * mm, "end": v(-51.66, 10.03) * mm});
            skLineSegment(sketch, "E1233", {"start": v(-51.66, 10.03) * mm, "end": v(-52.78, 10) * mm});
            skLineSegment(sketch, "E1234", {"start": v(-52.78, 10) * mm, "end": v(-53.91, 9.98) * mm});
            skLineSegment(sketch, "E1235", {"start": v(-53.91, 9.98) * mm, "end": v(-55.04, 9.96) * mm});
            skLineSegment(sketch, "E1236", {"start": v(-55.04, 9.96) * mm, "end": v(-56.17, 9.93) * mm});
            skLineSegment(sketch, "E1237", {"start": v(-56.17, 9.93) * mm, "end": v(-57.3, 9.9) * mm});
            skLineSegment(sketch, "E1238", {"start": v(-57.3, 9.9) * mm, "end": v(-58.42, 9.87) * mm});
            skLineSegment(sketch, "E1239", {"start": v(-58.42, 9.87) * mm, "end": v(-59.55, 9.83) * mm});
            skLineSegment(sketch, "E1240", {"start": v(-59.55, 9.83) * mm, "end": v(-60.68, 9.8) * mm});
            skLineSegment(sketch, "E1241", {"start": v(-60.68, 9.8) * mm, "end": v(-61.8, 9.76) * mm});
            skLineSegment(sketch, "E1242", {"start": v(-61.8, 9.76) * mm, "end": v(-62.93, 9.72) * mm});
            skLineSegment(sketch, "E1243", {"start": v(-62.93, 9.72) * mm, "end": v(-64, 9.68) * mm});
            skLineSegment(sketch, "E1244", {"start": v(-64, 9.68) * mm, "end": v(-65.05, 9.63) * mm});
            skLineSegment(sketch, "E1245", {"start": v(-65.05, 9.63) * mm, "end": v(-66.11, 9.59) * mm});
            skLineSegment(sketch, "E1246", {"start": v(-66.11, 9.59) * mm, "end": v(-67.18, 9.54) * mm});
            skLineSegment(sketch, "E1247", {"start": v(-67.18, 9.54) * mm, "end": v(-68.24, 9.49) * mm});
            skLineSegment(sketch, "E1248", {"start": v(-68.24, 9.49) * mm, "end": v(-69.3, 9.43) * mm});
            skLineSegment(sketch, "E1249", {"start": v(-69.3, 9.43) * mm, "end": v(-70.36, 9.38) * mm});
            skLineSegment(sketch, "E1250", {"start": v(-70.36, 9.38) * mm, "end": v(-71.42, 9.32) * mm});
            skLineSegment(sketch, "E1251", {"start": v(-71.42, 9.32) * mm, "end": v(-72.48, 9.26) * mm});
            skLineSegment(sketch, "E1252", {"start": v(-72.48, 9.26) * mm, "end": v(-74.53, 9.13) * mm});
            skLineSegment(sketch, "E1253", {"start": v(-74.53, 9.13) * mm, "end": v(-75.51, 9.07) * mm});
            skLineSegment(sketch, "E1254", {"start": v(-75.51, 9.07) * mm, "end": v(-76.5, 9) * mm});
            skLineSegment(sketch, "E1255", {"start": v(-76.5, 9) * mm, "end": v(-77.48, 8.93) * mm});
            skLineSegment(sketch, "E1256", {"start": v(-77.48, 8.93) * mm, "end": v(-78.46, 8.86) * mm});
            skLineSegment(sketch, "E1257", {"start": v(-78.46, 8.86) * mm, "end": v(-79.45, 8.79) * mm});
            skLineSegment(sketch, "E1258", {"start": v(-79.45, 8.79) * mm, "end": v(-80.43, 8.71) * mm});
            skLineSegment(sketch, "E1259", {"start": v(-80.43, 8.71) * mm, "end": v(-81.42, 8.63) * mm});
            skLineSegment(sketch, "E1260", {"start": v(-81.42, 8.63) * mm, "end": v(-82.4, 8.55) * mm});
            skLineSegment(sketch, "E1261", {"start": v(-82.4, 8.55) * mm, "end": v(-84.28, 8.38) * mm});
            skLineSegment(sketch, "E1262", {"start": v(-84.28, 8.38) * mm, "end": v(-85.18, 8.3) * mm});
            skLineSegment(sketch, "E1263", {"start": v(-85.18, 8.3) * mm, "end": v(-86.08, 8.2) * mm});
            skLineSegment(sketch, "E1264", {"start": v(-86.08, 8.2) * mm, "end": v(-86.98, 8.11) * mm});
            skLineSegment(sketch, "E1265", {"start": v(-86.98, 8.11) * mm, "end": v(-87.88, 8.02) * mm});
            skLineSegment(sketch, "E1266", {"start": v(-87.88, 8.02) * mm, "end": v(-88.77, 7.92) * mm});
            skLineSegment(sketch, "E1267", {"start": v(-88.77, 7.92) * mm, "end": v(-89.67, 7.82) * mm});
            skLineSegment(sketch, "E1268", {"start": v(-89.67, 7.82) * mm, "end": v(-90.57, 7.72) * mm});
            skLineSegment(sketch, "E1269", {"start": v(-90.57, 7.72) * mm, "end": v(-91.47, 7.61) * mm});
            skLineSegment(sketch, "E1270", {"start": v(-91.47, 7.61) * mm, "end": v(-92.37, 7.5) * mm});
            skLineSegment(sketch, "E1271", {"start": v(-92.37, 7.5) * mm, "end": v(-93.17, 7.4) * mm});
            skLineSegment(sketch, "E1272", {"start": v(-93.17, 7.4) * mm, "end": v(-93.98, 7.3) * mm});
            skLineSegment(sketch, "E1273", {"start": v(-93.98, 7.3) * mm, "end": v(-94.78, 7.2) * mm});
            skLineSegment(sketch, "E1274", {"start": v(-94.78, 7.2) * mm, "end": v(-95.59, 7.08) * mm});
            skLineSegment(sketch, "E1275", {"start": v(-95.59, 7.08) * mm, "end": v(-96.4, 6.97) * mm});
            skLineSegment(sketch, "E1276", {"start": v(-96.4, 6.97) * mm, "end": v(-97.2, 6.85) * mm});
            skLineSegment(sketch, "E1277", {"start": v(-97.2, 6.85) * mm, "end": v(-98, 6.73) * mm});
            skLineSegment(sketch, "E1278", {"start": v(-98, 6.73) * mm, "end": v(-98.81, 6.6) * mm});
            skLineSegment(sketch, "E1279", {"start": v(-98.81, 6.6) * mm, "end": v(-99.62, 6.48) * mm});
            skLineSegment(sketch, "E1280", {"start": v(-99.62, 6.48) * mm, "end": v(-100.42, 6.35) * mm});
            skLineSegment(sketch, "E1281", {"start": v(-100.42, 6.35) * mm, "end": v(-101.13, 6.23) * mm});
            skLineSegment(sketch, "E1282", {"start": v(-101.13, 6.23) * mm, "end": v(-101.83, 6.1) * mm});
            skLineSegment(sketch, "E1283", {"start": v(-101.83, 6.1) * mm, "end": v(-102.54, 5.98) * mm});
            skLineSegment(sketch, "E1284", {"start": v(-102.54, 5.98) * mm, "end": v(-103.25, 5.85) * mm});
            skLineSegment(sketch, "E1285", {"start": v(-103.25, 5.85) * mm, "end": v(-103.95, 5.72) * mm});
            skLineSegment(sketch, "E1286", {"start": v(-103.95, 5.72) * mm, "end": v(-104.66, 5.59) * mm});
            skLineSegment(sketch, "E1287", {"start": v(-104.66, 5.59) * mm, "end": v(-105.37, 5.45) * mm});
            skLineSegment(sketch, "E1288", {"start": v(-105.37, 5.45) * mm, "end": v(-106.07, 5.3) * mm});
            skLineSegment(sketch, "E1289", {"start": v(-106.07, 5.3) * mm, "end": v(-106.78, 5.16) * mm});
            skLineSegment(sketch, "E1290", {"start": v(-106.78, 5.16) * mm, "end": v(-108.09, 4.87) * mm});
            skLineSegment(sketch, "E1291", {"start": v(-108.09, 4.87) * mm, "end": v(-108.69, 4.73) * mm});
            skLineSegment(sketch, "E1292", {"start": v(-108.69, 4.73) * mm, "end": v(-109.3, 4.6) * mm});
            skLineSegment(sketch, "E1293", {"start": v(-109.3, 4.6) * mm, "end": v(-109.9, 4.45) * mm});
            skLineSegment(sketch, "E1294", {"start": v(-109.9, 4.45) * mm, "end": v(-110.5, 4.3) * mm});
            skLineSegment(sketch, "E1295", {"start": v(-110.5, 4.3) * mm, "end": v(-111.1, 4.15) * mm});
            skLineSegment(sketch, "E1296", {"start": v(-111.1, 4.15) * mm, "end": v(-111.7, 4) * mm});
            skLineSegment(sketch, "E1297", {"start": v(-111.7, 4) * mm, "end": v(-112.3, 3.84) * mm});
            skLineSegment(sketch, "E1298", {"start": v(-112.3, 3.84) * mm, "end": v(-112.9, 3.67) * mm});
            skLineSegment(sketch, "E1299", {"start": v(-112.9, 3.67) * mm, "end": v(-113.5, 3.5) * mm});
            skLineSegment(sketch, "E1300", {"start": v(-113.5, 3.5) * mm, "end": v(-114, 3.36) * mm});
            skLineSegment(sketch, "E1301", {"start": v(-114, 3.36) * mm, "end": v(-114.5, 3.21) * mm});
            skLineSegment(sketch, "E1302", {"start": v(-114.5, 3.21) * mm, "end": v(-115, 3.06) * mm});
            skLineSegment(sketch, "E1303", {"start": v(-115, 3.06) * mm, "end": v(-115.49, 2.9) * mm});
            skLineSegment(sketch, "E1304", {"start": v(-115.49, 2.9) * mm, "end": v(-115.98, 2.74) * mm});
            skLineSegment(sketch, "E1305", {"start": v(-115.98, 2.74) * mm, "end": v(-116.48, 2.58) * mm});
            skLineSegment(sketch, "E1306", {"start": v(-116.48, 2.58) * mm, "end": v(-116.97, 2.41) * mm});
            skLineSegment(sketch, "E1307", {"start": v(-117.33, -7.8) * mm, "end": v(-117, -7.85) * mm});
            skLineSegment(sketch, "E1308", {"start": v(-116.82, -7.88) * mm, "end": v(-116.3, -7.97) * mm});
            skLineSegment(sketch, "E1309", {"start": v(-116.3, -7.97) * mm, "end": v(-115.8, -8.05) * mm});
            skLineSegment(sketch, "E1310", {"start": v(-115.8, -8.05) * mm, "end": v(-115.29, -8.13) * mm});
            skLineSegment(sketch, "E1311", {"start": v(-115.29, -8.13) * mm, "end": v(-114.78, -8.2) * mm});
            skLineSegment(sketch, "E1312", {"start": v(-114.78, -8.2) * mm, "end": v(-114.27, -8.28) * mm});
            skLineSegment(sketch, "E1313", {"start": v(-114.27, -8.28) * mm, "end": v(-113.64, -8.36) * mm});
            skLineSegment(sketch, "E1314", {"start": v(-113.64, -8.36) * mm, "end": v(-113, -8.45) * mm});
            skLineSegment(sketch, "E1315", {"start": v(-113, -8.45) * mm, "end": v(-112.38, -8.52) * mm});
            skLineSegment(sketch, "E1316", {"start": v(-112.38, -8.52) * mm, "end": v(-111.75, -8.6) * mm});
            skLineSegment(sketch, "E1317", {"start": v(-111.75, -8.6) * mm, "end": v(-111.12, -8.67) * mm});
            skLineSegment(sketch, "E1318", {"start": v(-111.12, -8.67) * mm, "end": v(-110.49, -8.74) * mm});
            skLineSegment(sketch, "E1319", {"start": v(-110.49, -8.74) * mm, "end": v(-109.86, -8.8) * mm});
            skLineSegment(sketch, "E1320", {"start": v(-109.86, -8.8) * mm, "end": v(-109.23, -8.87) * mm});
            skLineSegment(sketch, "E1321", {"start": v(-109.23, -8.87) * mm, "end": v(-108.6, -8.93) * mm});
            skLineSegment(sketch, "E1322", {"start": v(-108.6, -8.93) * mm, "end": v(-107.97, -8.99) * mm});
            skLineSegment(sketch, "E1323", {"start": v(-107.97, -8.99) * mm, "end": v(-107.22, -9.05) * mm});
            skLineSegment(sketch, "E1324", {"start": v(-107.22, -9.05) * mm, "end": v(-106.48, -9.11) * mm});
            skLineSegment(sketch, "E1325", {"start": v(-106.48, -9.11) * mm, "end": v(-105.73, -9.17) * mm});
            skLineSegment(sketch, "E1326", {"start": v(-105.73, -9.17) * mm, "end": v(-104.98, -9.23) * mm});
            skLineSegment(sketch, "E1327", {"start": v(-104.98, -9.23) * mm, "end": v(-104.24, -9.28) * mm});
            skLineSegment(sketch, "E1328", {"start": v(-104.24, -9.28) * mm, "end": v(-103.5, -9.34) * mm});
            skLineSegment(sketch, "E1329", {"start": v(-103.5, -9.34) * mm, "end": v(-102.74, -9.39) * mm});
            skLineSegment(sketch, "E1330", {"start": v(-102.74, -9.39) * mm, "end": v(-102, -9.43) * mm});
            skLineSegment(sketch, "E1331", {"start": v(-102, -9.43) * mm, "end": v(-101.25, -9.48) * mm});
            skLineSegment(sketch, "E1332", {"start": v(-101.25, -9.48) * mm, "end": v(-99.65, -9.57) * mm});
            skLineSegment(sketch, "E1333", {"start": v(-99.65, -9.57) * mm, "end": v(-98.8, -9.61) * mm});
            skLineSegment(sketch, "E1334", {"start": v(-98.8, -9.61) * mm, "end": v(-97.93, -9.65) * mm});
            skLineSegment(sketch, "E1335", {"start": v(-97.93, -9.65) * mm, "end": v(-97.08, -9.7) * mm});
            skLineSegment(sketch, "E1336", {"start": v(-97.08, -9.7) * mm, "end": v(-96.22, -9.73) * mm});
            skLineSegment(sketch, "E1337", {"start": v(-96.22, -9.73) * mm, "end": v(-95.36, -9.76) * mm});
            skLineSegment(sketch, "E1338", {"start": v(-95.36, -9.76) * mm, "end": v(-94.5, -9.8) * mm});
            skLineSegment(sketch, "E1339", {"start": v(-94.5, -9.8) * mm, "end": v(-93.65, -9.82) * mm});
            skLineSegment(sketch, "E1340", {"start": v(-93.65, -9.82) * mm, "end": v(-92.8, -9.85) * mm});
            skLineSegment(sketch, "E1341", {"start": v(-92.8, -9.85) * mm, "end": v(-91.93, -9.88) * mm});
            skLineSegment(sketch, "E1342", {"start": v(-91.93, -9.88) * mm, "end": v(-90.97, -9.9) * mm});
            skLineSegment(sketch, "E1343", {"start": v(-90.97, -9.9) * mm, "end": v(-90.01, -9.93) * mm});
            skLineSegment(sketch, "E1344", {"start": v(-90.01, -9.93) * mm, "end": v(-89.05, -9.95) * mm});
            skLineSegment(sketch, "E1345", {"start": v(-89.05, -9.95) * mm, "end": v(-88.09, -9.98) * mm});
            skLineSegment(sketch, "E1346", {"start": v(-88.09, -9.98) * mm, "end": v(-87.13, -10) * mm});
            skLineSegment(sketch, "E1347", {"start": v(-87.13, -10) * mm, "end": v(-86.17, -10.01) * mm});
            skLineSegment(sketch, "E1348", {"start": v(-86.17, -10.01) * mm, "end": v(-85.2, -10.03) * mm});
            skLineSegment(sketch, "E1349", {"start": v(-85.2, -10.03) * mm, "end": v(-84.25, -10.05) * mm});
            skLineSegment(sketch, "E1350", {"start": v(-84.25, -10.05) * mm, "end": v(-83.28, -10.06) * mm});
            skLineSegment(sketch, "E1351", {"start": v(-83.28, -10.06) * mm, "end": v(-81.27, -10.08) * mm});
            skLineSegment(sketch, "E1352", {"start": v(-81.27, -10.08) * mm, "end": v(-80.21, -10.1) * mm});
            skLineSegment(sketch, "E1353", {"start": v(-80.21, -10.1) * mm, "end": v(-79.16, -10.1) * mm});
            skLineSegment(sketch, "E1354", {"start": v(-79.16, -10.1) * mm, "end": v(-78.1, -10.1) * mm});
            skLineSegment(sketch, "E1355", {"start": v(-78.1, -10.1) * mm, "end": v(-77.05, -10.11) * mm});
            skLineSegment(sketch, "E1356", {"start": v(-77.05, -10.11) * mm, "end": v(-76, -10.12) * mm});
            skLineSegment(sketch, "E1357", {"start": v(-76, -10.12) * mm, "end": v(-74.94, -10.12) * mm});
            skLineSegment(sketch, "E1358", {"start": v(-74.94, -10.12) * mm, "end": v(-73.89, -10.12) * mm});
            skLineSegment(sketch, "E1359", {"start": v(-73.89, -10.12) * mm, "end": v(-72.83, -10.12) * mm});
            skLineSegment(sketch, "E1360", {"start": v(-72.83, -10.12) * mm, "end": v(-71.78, -10.12) * mm});
            skLineSegment(sketch, "E1361", {"start": v(-71.78, -10.12) * mm, "end": v(-70.64, -10.11) * mm});
            skLineSegment(sketch, "E1362", {"start": v(-70.64, -10.11) * mm, "end": v(-69.5, -10.1) * mm});
            skLineSegment(sketch, "E1363", {"start": v(-69.5, -10.1) * mm, "end": v(-68.36, -10.1) * mm});
            skLineSegment(sketch, "E1364", {"start": v(-68.36, -10.1) * mm, "end": v(-67.22, -10.1) * mm});
            skLineSegment(sketch, "E1365", {"start": v(-67.22, -10.1) * mm, "end": v(-66.08, -10.09) * mm});
            skLineSegment(sketch, "E1366", {"start": v(-66.08, -10.09) * mm, "end": v(-64.94, -10.08) * mm});
            skLineSegment(sketch, "E1367", {"start": v(-64.94, -10.08) * mm, "end": v(-63.8, -10.07) * mm});
            skLineSegment(sketch, "E1368", {"start": v(-63.8, -10.07) * mm, "end": v(-62.67, -10.05) * mm});
            skLineSegment(sketch, "E1369", {"start": v(-62.67, -10.05) * mm, "end": v(-61.53, -10.04) * mm});
            skLineSegment(sketch, "E1370", {"start": v(-61.53, -10.04) * mm, "end": v(-60.4, -10.03) * mm});
            skLineSegment(sketch, "E1371", {"start": v(-60.4, -10.03) * mm, "end": v(-59.18, -10.01) * mm});
            skLineSegment(sketch, "E1372", {"start": v(-59.18, -10.01) * mm, "end": v(-57.97, -10) * mm});
            skLineSegment(sketch, "E1373", {"start": v(-57.97, -10) * mm, "end": v(-56.76, -9.97) * mm});
            skLineSegment(sketch, "E1374", {"start": v(-56.76, -9.97) * mm, "end": v(-55.55, -9.96) * mm});
            skLineSegment(sketch, "E1375", {"start": v(-55.55, -9.96) * mm, "end": v(-54.34, -9.93) * mm});
            skLineSegment(sketch, "E1376", {"start": v(-54.34, -9.93) * mm, "end": v(-53.14, -9.91) * mm});
            skLineSegment(sketch, "E1377", {"start": v(-53.14, -9.91) * mm, "end": v(-51.93, -9.9) * mm});
            skLineSegment(sketch, "E1378", {"start": v(-51.93, -9.9) * mm, "end": v(-50.72, -9.87) * mm});
            skLineSegment(sketch, "E1379", {"start": v(-50.72, -9.87) * mm, "end": v(-49.5, -9.84) * mm});
            skLineSegment(sketch, "E1380", {"start": v(-49.5, -9.84) * mm, "end": v(-47.03, -9.8) * mm});
            skLineSegment(sketch, "E1381", {"start": v(-47.03, -9.8) * mm, "end": v(-45.76, -9.76) * mm});
            skLineSegment(sketch, "E1382", {"start": v(-45.76, -9.76) * mm, "end": v(-44.5, -9.74) * mm});
            skLineSegment(sketch, "E1383", {"start": v(-44.5, -9.74) * mm, "end": v(-43.23, -9.7) * mm});
            skLineSegment(sketch, "E1384", {"start": v(-43.23, -9.7) * mm, "end": v(-41.96, -9.68) * mm});
            skLineSegment(sketch, "E1385", {"start": v(-41.96, -9.68) * mm, "end": v(-40.7, -9.64) * mm});
            skLineSegment(sketch, "E1386", {"start": v(-40.7, -9.64) * mm, "end": v(-39.43, -9.61) * mm});
            skLineSegment(sketch, "E1387", {"start": v(-39.43, -9.61) * mm, "end": v(-38.16, -9.58) * mm});
            skLineSegment(sketch, "E1388", {"start": v(-38.16, -9.58) * mm, "end": v(-36.9, -9.55) * mm});
            skLineSegment(sketch, "E1389", {"start": v(-36.9, -9.55) * mm, "end": v(-34.31, -9.48) * mm});
            skLineSegment(sketch, "E1390", {"start": v(-34.31, -9.48) * mm, "end": v(-33, -9.44) * mm});
            skLineSegment(sketch, "E1391", {"start": v(-33, -9.44) * mm, "end": v(-31.7, -9.4) * mm});
            skLineSegment(sketch, "E1392", {"start": v(-31.7, -9.4) * mm, "end": v(-30.38, -9.37) * mm});
            skLineSegment(sketch, "E1393", {"start": v(-30.38, -9.37) * mm, "end": v(-29.07, -9.33) * mm});
            skLineSegment(sketch, "E1394", {"start": v(-29.07, -9.33) * mm, "end": v(-27.76, -9.29) * mm});
            skLineSegment(sketch, "E1395", {"start": v(-27.76, -9.29) * mm, "end": v(-26.45, -9.25) * mm});
            skLineSegment(sketch, "E1396", {"start": v(-26.45, -9.25) * mm, "end": v(-25.13, -9.2) * mm});
            skLineSegment(sketch, "E1397", {"start": v(-25.13, -9.2) * mm, "end": v(-23.82, -9.17) * mm});
            skLineSegment(sketch, "E1398", {"start": v(-23.82, -9.17) * mm, "end": v(-22.51, -9.13) * mm});
            skLineSegment(sketch, "E1399", {"start": v(-22.51, -9.13) * mm, "end": v(-21.17, -9.08) * mm});
            skLineSegment(sketch, "E1400", {"start": v(-21.17, -9.08) * mm, "end": v(-19.83, -9.04) * mm});
            skLineSegment(sketch, "E1401", {"start": v(-19.83, -9.04) * mm, "end": v(-18.49, -9) * mm});
            skLineSegment(sketch, "E1402", {"start": v(-18.49, -9) * mm, "end": v(-17.15, -8.95) * mm});
            skLineSegment(sketch, "E1403", {"start": v(-17.15, -8.95) * mm, "end": v(-15.8, -8.9) * mm});
            skLineSegment(sketch, "E1404", {"start": v(-15.8, -8.9) * mm, "end": v(-14.47, -8.86) * mm});
            skLineSegment(sketch, "E1405", {"start": v(-14.47, -8.86) * mm, "end": v(-13.13, -8.81) * mm});
            skLineSegment(sketch, "E1406", {"start": v(-13.13, -8.81) * mm, "end": v(-11.79, -8.77) * mm});
            skLineSegment(sketch, "E1407", {"start": v(-11.79, -8.77) * mm, "end": v(-10.44, -8.72) * mm});
            skLineSegment(sketch, "E1408", {"start": v(-10.44, -8.72) * mm, "end": v(-7.75, -8.62) * mm});
            skLineSegment(sketch, "E1409", {"start": v(-7.75, -8.62) * mm, "end": v(-6.4, -8.57) * mm});
            skLineSegment(sketch, "E1410", {"start": v(-6.4, -8.57) * mm, "end": v(-5.04, -8.52) * mm});
            skLineSegment(sketch, "E1411", {"start": v(-5.04, -8.52) * mm, "end": v(-3.68, -8.47) * mm});
            skLineSegment(sketch, "E1412", {"start": v(-3.68, -8.47) * mm, "end": v(-2.33, -8.42) * mm});
            skLineSegment(sketch, "E1413", {"start": v(-2.33, -8.42) * mm, "end": v(-0.97, -8.37) * mm});
            skLineSegment(sketch, "E1414", {"start": v(-0.97, -8.37) * mm, "end": v(0.38, -8.32) * mm});
            skLineSegment(sketch, "E1415", {"start": v(0.38, -8.32) * mm, "end": v(1.74, -8.27) * mm});
            skLineSegment(sketch, "E1416", {"start": v(1.74, -8.27) * mm, "end": v(3.1, -8.22) * mm});
            skLineSegment(sketch, "E1417", {"start": v(3.1, -8.22) * mm, "end": v(4.45, -8.17) * mm});
            skLineSegment(sketch, "E1418", {"start": v(4.45, -8.17) * mm, "end": v(5.8, -8.12) * mm});
            skLineSegment(sketch, "E1419", {"start": v(5.8, -8.12) * mm, "end": v(7.16, -8.06) * mm});
            skLineSegment(sketch, "E1420", {"start": v(7.16, -8.06) * mm, "end": v(8.5, -8.01) * mm});
            skLineSegment(sketch, "E1421", {"start": v(8.5, -8.01) * mm, "end": v(9.86, -7.96) * mm});
            skLineSegment(sketch, "E1422", {"start": v(9.86, -7.96) * mm, "end": v(11.22, -7.9) * mm});
            skLineSegment(sketch, "E1423", {"start": v(11.22, -7.9) * mm, "end": v(12.57, -7.85) * mm});
            skLineSegment(sketch, "E1424", {"start": v(12.57, -7.85) * mm, "end": v(13.93, -7.8) * mm});
            skLineSegment(sketch, "E1425", {"start": v(13.93, -7.8) * mm, "end": v(15.28, -7.75) * mm});
            skLineSegment(sketch, "E1426", {"start": v(15.28, -7.75) * mm, "end": v(16.63, -7.7) * mm});
            skLineSegment(sketch, "E1427", {"start": v(16.63, -7.7) * mm, "end": v(17.99, -7.64) * mm});
            skLineSegment(sketch, "E1428", {"start": v(17.99, -7.64) * mm, "end": v(19.33, -7.58) * mm});
            skLineSegment(sketch, "E1429", {"start": v(19.33, -7.58) * mm, "end": v(20.66, -7.53) * mm});
            skLineSegment(sketch, "E1430", {"start": v(20.66, -7.53) * mm, "end": v(22, -7.47) * mm});
            skLineSegment(sketch, "E1431", {"start": v(22, -7.47) * mm, "end": v(23.34, -7.42) * mm});
            skLineSegment(sketch, "E1432", {"start": v(23.34, -7.42) * mm, "end": v(24.68, -7.37) * mm});
            skLineSegment(sketch, "E1433", {"start": v(24.68, -7.37) * mm, "end": v(26.01, -7.31) * mm});
            skLineSegment(sketch, "E1434", {"start": v(26.01, -7.31) * mm, "end": v(27.35, -7.26) * mm});
            skLineSegment(sketch, "E1435", {"start": v(27.35, -7.26) * mm, "end": v(28.69, -7.2) * mm});
            skLineSegment(sketch, "E1436", {"start": v(28.69, -7.2) * mm, "end": v(30.03, -7.15) * mm});
            skLineSegment(sketch, "E1437", {"start": v(30.03, -7.15) * mm, "end": v(32.67, -7.04) * mm});
            skLineSegment(sketch, "E1438", {"start": v(32.67, -7.04) * mm, "end": v(33.98, -6.98) * mm});
            skLineSegment(sketch, "E1439", {"start": v(33.98, -6.98) * mm, "end": v(35.28, -6.93) * mm});
            skLineSegment(sketch, "E1440", {"start": v(35.28, -6.93) * mm, "end": v(36.59, -6.88) * mm});
            skLineSegment(sketch, "E1441", {"start": v(36.59, -6.88) * mm, "end": v(37.9, -6.82) * mm});
            skLineSegment(sketch, "E1442", {"start": v(37.9, -6.82) * mm, "end": v(39.2, -6.77) * mm});
            skLineSegment(sketch, "E1443", {"start": v(39.2, -6.77) * mm, "end": v(40.5, -6.72) * mm});
            skLineSegment(sketch, "E1444", {"start": v(40.5, -6.72) * mm, "end": v(41.81, -6.66) * mm});
            skLineSegment(sketch, "E1445", {"start": v(41.81, -6.66) * mm, "end": v(43.12, -6.6) * mm});
            skLineSegment(sketch, "E1446", {"start": v(43.12, -6.6) * mm, "end": v(45.68, -6.5) * mm});
            skLineSegment(sketch, "E1447", {"start": v(45.68, -6.5) * mm, "end": v(46.94, -6.45) * mm});
            skLineSegment(sketch, "E1448", {"start": v(46.94, -6.45) * mm, "end": v(48.2, -6.4) * mm});
            skLineSegment(sketch, "E1449", {"start": v(48.2, -6.4) * mm, "end": v(49.46, -6.35) * mm});
            skLineSegment(sketch, "E1450", {"start": v(49.46, -6.35) * mm, "end": v(50.71, -6.3) * mm});
            skLineSegment(sketch, "E1451", {"start": v(50.71, -6.3) * mm, "end": v(51.97, -6.25) * mm});
            skLineSegment(sketch, "E1452", {"start": v(51.97, -6.25) * mm, "end": v(53.23, -6.2) * mm});
            skLineSegment(sketch, "E1453", {"start": v(53.23, -6.2) * mm, "end": v(54.49, -6.14) * mm});
            skLineSegment(sketch, "E1454", {"start": v(54.49, -6.14) * mm, "end": v(55.75, -6.1) * mm});
            skLineSegment(sketch, "E1455", {"start": v(55.75, -6.1) * mm, "end": v(57, -6.04) * mm});
            skLineSegment(sketch, "E1456", {"start": v(57, -6.04) * mm, "end": v(58.2, -6) * mm});
            skLineSegment(sketch, "E1457", {"start": v(58.2, -6) * mm, "end": v(59.4, -5.95) * mm});
            skLineSegment(sketch, "E1458", {"start": v(59.4, -5.95) * mm, "end": v(60.6, -5.9) * mm});
            skLineSegment(sketch, "E1459", {"start": v(60.6, -5.9) * mm, "end": v(61.79, -5.85) * mm});
            skLineSegment(sketch, "E1460", {"start": v(62.14, 4.18) * mm, "end": v(61.39, 2.74) * mm});
            skLineSegment(sketch, "E1461", {"start": v(61.39, 2.74) * mm, "end": v(60.75, 2.81) * mm});
            skLineSegment(sketch, "E1462", {"start": v(60.75, 2.81) * mm, "end": v(60.12, 2.88) * mm});
            skLineSegment(sketch, "E1463", {"start": v(60.12, 2.88) * mm, "end": v(59.48, 2.95) * mm});
            skLineSegment(sketch, "E1464", {"start": v(59.48, 2.95) * mm, "end": v(58.85, 3.02) * mm});
            skLineSegment(sketch, "E1465", {"start": v(58.85, 3.02) * mm, "end": v(58.21, 3.08) * mm});
            skLineSegment(sketch, "E1466", {"start": v(58.21, 3.08) * mm, "end": v(57.58, 3.15) * mm});
            skLineSegment(sketch, "E1467", {"start": v(57.58, 3.15) * mm, "end": v(56.94, 3.22) * mm});
            skLineSegment(sketch, "E1468", {"start": v(56.94, 3.22) * mm, "end": v(56.3, 3.28) * mm});
            skLineSegment(sketch, "E1469", {"start": v(56.3, 3.28) * mm, "end": v(55.67, 3.35) * mm});
            skLineSegment(sketch, "E1470", {"start": v(55.67, 3.35) * mm, "end": v(55.04, 3.42) * mm});
            skLineSegment(sketch, "E1471", {"start": v(55.04, 3.42) * mm, "end": v(54.4, 3.48) * mm});
            skLineSegment(sketch, "E1472", {"start": v(54.4, 3.48) * mm, "end": v(53.77, 3.55) * mm});
            skLineSegment(sketch, "E1473", {"start": v(53.77, 3.55) * mm, "end": v(53.13, 3.6) * mm});
            skLineSegment(sketch, "E1474", {"start": v(53.13, 3.6) * mm, "end": v(52.5, 3.67) * mm});
            skLineSegment(sketch, "E1475", {"start": v(52.5, 3.67) * mm, "end": v(51.86, 3.74) * mm});
            skLineSegment(sketch, "E1476", {"start": v(51.86, 3.74) * mm, "end": v(51.23, 3.8) * mm});
            skLineSegment(sketch, "E1477", {"start": v(51.23, 3.8) * mm, "end": v(50.6, 3.86) * mm});
            skLineSegment(sketch, "E1478", {"start": v(50.6, 3.86) * mm, "end": v(49.96, 3.92) * mm});
            skLineSegment(sketch, "E1479", {"start": v(49.96, 3.92) * mm, "end": v(49.32, 3.98) * mm});
            skLineSegment(sketch, "E1480", {"start": v(49.32, 3.98) * mm, "end": v(48.69, 4.05) * mm});
            skLineSegment(sketch, "E1481", {"start": v(48.69, 4.05) * mm, "end": v(48.05, 4.1) * mm});
            skLineSegment(sketch, "E1482", {"start": v(48.05, 4.1) * mm, "end": v(47.42, 4.17) * mm});
            skLineSegment(sketch, "E1483", {"start": v(47.42, 4.17) * mm, "end": v(46.78, 4.23) * mm});
            skLineSegment(sketch, "E1484", {"start": v(46.78, 4.23) * mm, "end": v(46.14, 4.28) * mm});
            skLineSegment(sketch, "E1485", {"start": v(46.14, 4.28) * mm, "end": v(45.5, 4.34) * mm});
            skLineSegment(sketch, "E1486", {"start": v(45.5, 4.34) * mm, "end": v(44.87, 4.4) * mm});
            skLineSegment(sketch, "E1487", {"start": v(44.87, 4.4) * mm, "end": v(44.24, 4.46) * mm});
            skLineSegment(sketch, "E1488", {"start": v(44.24, 4.46) * mm, "end": v(43.6, 4.52) * mm});
            skLineSegment(sketch, "E1489", {"start": v(43.6, 4.52) * mm, "end": v(42.97, 4.57) * mm});
            skLineSegment(sketch, "E1490", {"start": v(42.97, 4.57) * mm, "end": v(42.33, 4.63) * mm});
            skLineSegment(sketch, "E1491", {"start": v(42.33, 4.63) * mm, "end": v(41.7, 4.69) * mm});
            skLineSegment(sketch, "E1492", {"start": v(41.7, 4.69) * mm, "end": v(41.06, 4.74) * mm});
            skLineSegment(sketch, "E1493", {"start": v(41.06, 4.74) * mm, "end": v(40.43, 4.8) * mm});
            skLineSegment(sketch, "E1494", {"start": v(40.43, 4.8) * mm, "end": v(39.8, 4.85) * mm});
            skLineSegment(sketch, "E1495", {"start": v(39.8, 4.85) * mm, "end": v(39.16, 4.9) * mm});
            skLineSegment(sketch, "E1496", {"start": v(39.16, 4.9) * mm, "end": v(38.52, 4.96) * mm});
            skLineSegment(sketch, "E1497", {"start": v(38.52, 4.96) * mm, "end": v(37.89, 5.02) * mm});
            skLineSegment(sketch, "E1498", {"start": v(37.89, 5.02) * mm, "end": v(37.25, 5.07) * mm});
            skLineSegment(sketch, "E1499", {"start": v(37.25, 5.07) * mm, "end": v(36.62, 5.12) * mm});
            skLineSegment(sketch, "E1500", {"start": v(36.62, 5.12) * mm, "end": v(35.98, 5.18) * mm});
            skLineSegment(sketch, "E1501", {"start": v(35.98, 5.18) * mm, "end": v(35.35, 5.23) * mm});
            skLineSegment(sketch, "E1502", {"start": v(35.35, 5.23) * mm, "end": v(34.71, 5.28) * mm});
            skLineSegment(sketch, "E1503", {"start": v(34.71, 5.28) * mm, "end": v(34.08, 5.33) * mm});
            skLineSegment(sketch, "E1504", {"start": v(34.08, 5.33) * mm, "end": v(33.44, 5.38) * mm});
            skLineSegment(sketch, "E1505", {"start": v(33.44, 5.38) * mm, "end": v(32.8, 5.43) * mm});
            skLineSegment(sketch, "E1506", {"start": v(32.8, 5.43) * mm, "end": v(32.17, 5.48) * mm});
            skLineSegment(sketch, "E1507", {"start": v(32.17, 5.48) * mm, "end": v(31.54, 5.53) * mm});
            skLineSegment(sketch, "E1508", {"start": v(31.54, 5.53) * mm, "end": v(30.9, 5.58) * mm});
            skLineSegment(sketch, "E1509", {"start": v(30.9, 5.58) * mm, "end": v(30.27, 5.63) * mm});
            skLineSegment(sketch, "E1510", {"start": v(30.27, 5.63) * mm, "end": v(29.63, 5.68) * mm});
            skLineSegment(sketch, "E1511", {"start": v(29.63, 5.68) * mm, "end": v(29, 5.73) * mm});
            skLineSegment(sketch, "E1512", {"start": v(29, 5.73) * mm, "end": v(28.36, 5.78) * mm});
            skLineSegment(sketch, "E1513", {"start": v(28.36, 5.78) * mm, "end": v(27.73, 5.82) * mm});
            skLineSegment(sketch, "E1514", {"start": v(27.73, 5.82) * mm, "end": v(27.1, 5.87) * mm});
            skLineSegment(sketch, "E1515", {"start": v(27.1, 5.87) * mm, "end": v(26.46, 5.92) * mm});
            skLineSegment(sketch, "E1516", {"start": v(26.46, 5.92) * mm, "end": v(25.82, 5.96) * mm});
            skLineSegment(sketch, "E1517", {"start": v(25.82, 5.96) * mm, "end": v(25.19, 6.01) * mm});
            skLineSegment(sketch, "E1518", {"start": v(25.19, 6.01) * mm, "end": v(24.55, 6.06) * mm});
            skLineSegment(sketch, "E1519", {"start": v(24.55, 6.06) * mm, "end": v(23.92, 6.1) * mm});
            skLineSegment(sketch, "E1520", {"start": v(23.92, 6.1) * mm, "end": v(23.28, 6.15) * mm});
            skLineSegment(sketch, "E1521", {"start": v(23.28, 6.15) * mm, "end": v(22.65, 6.2) * mm});
            skLineSegment(sketch, "E1522", {"start": v(22.65, 6.2) * mm, "end": v(22, 6.24) * mm});
            skLineSegment(sketch, "E1523", {"start": v(22, 6.24) * mm, "end": v(21.37, 6.28) * mm});
            skLineSegment(sketch, "E1524", {"start": v(21.37, 6.28) * mm, "end": v(20.74, 6.32) * mm});
            skLineSegment(sketch, "E1525", {"start": v(20.74, 6.32) * mm, "end": v(20.1, 6.37) * mm});
            skLineSegment(sketch, "E1526", {"start": v(20.1, 6.37) * mm, "end": v(19.47, 6.4) * mm});
            skLineSegment(sketch, "E1527", {"start": v(19.47, 6.4) * mm, "end": v(18.83, 6.45) * mm});
            skLineSegment(sketch, "E1528", {"start": v(18.83, 6.45) * mm, "end": v(18.2, 6.5) * mm});
            skLineSegment(sketch, "E1529", {"start": v(18.2, 6.5) * mm, "end": v(17.56, 6.53) * mm});
            skLineSegment(sketch, "E1530", {"start": v(17.56, 6.53) * mm, "end": v(16.93, 6.58) * mm});
            skLineSegment(sketch, "E1531", {"start": v(16.93, 6.58) * mm, "end": v(16.3, 6.62) * mm});
            skLineSegment(sketch, "E1532", {"start": v(16.3, 6.62) * mm, "end": v(15.66, 6.66) * mm});
            skLineSegment(sketch, "E1533", {"start": v(15.66, 6.66) * mm, "end": v(15.02, 6.7) * mm});
            skLineSegment(sketch, "E1534", {"start": v(15.02, 6.7) * mm, "end": v(14.39, 6.74) * mm});
            skLineSegment(sketch, "E1535", {"start": v(14.39, 6.74) * mm, "end": v(13.75, 6.78) * mm});
            skLineSegment(sketch, "E1536", {"start": v(13.75, 6.78) * mm, "end": v(13.12, 6.82) * mm});
            skLineSegment(sketch, "E1537", {"start": v(13.12, 6.82) * mm, "end": v(12.48, 6.85) * mm});
            skLineSegment(sketch, "E1538", {"start": v(12.48, 6.85) * mm, "end": v(11.85, 6.9) * mm});
            skLineSegment(sketch, "E1539", {"start": v(11.85, 6.9) * mm, "end": v(11.21, 6.93) * mm});
            skLineSegment(sketch, "E1540", {"start": v(11.21, 6.93) * mm, "end": v(10.58, 6.97) * mm});
            skLineSegment(sketch, "E1541", {"start": v(10.58, 6.97) * mm, "end": v(9.94, 7) * mm});
            skLineSegment(sketch, "E1542", {"start": v(9.94, 7) * mm, "end": v(9.3, 7.04) * mm});
            skLineSegment(sketch, "E1543", {"start": v(9.3, 7.04) * mm, "end": v(8.67, 7.08) * mm});
            skLineSegment(sketch, "E1544", {"start": v(8.67, 7.08) * mm, "end": v(8.04, 7.12) * mm});
            skLineSegment(sketch, "E1545", {"start": v(8.04, 7.12) * mm, "end": v(7.4, 7.15) * mm});
            skLineSegment(sketch, "E1546", {"start": v(7.4, 7.15) * mm, "end": v(6.77, 7.19) * mm});
            skLineSegment(sketch, "E1547", {"start": v(6.77, 7.19) * mm, "end": v(6.13, 7.22) * mm});
            skLineSegment(sketch, "E1548", {"start": v(6.13, 7.22) * mm, "end": v(5.5, 7.26) * mm});
            skLineSegment(sketch, "E1549", {"start": v(5.5, 7.26) * mm, "end": v(4.86, 7.3) * mm});
            skLineSegment(sketch, "E1550", {"start": v(4.86, 7.3) * mm, "end": v(4.23, 7.33) * mm});
            skLineSegment(sketch, "E1551", {"start": v(4.23, 7.33) * mm, "end": v(3.6, 7.36) * mm});
            skLineSegment(sketch, "E1552", {"start": v(3.6, 7.36) * mm, "end": v(2.96, 7.4) * mm});
            skLineSegment(sketch, "E1553", {"start": v(2.96, 7.4) * mm, "end": v(2.32, 7.43) * mm});
            skLineSegment(sketch, "E1554", {"start": v(2.32, 7.43) * mm, "end": v(1.69, 7.46) * mm});
            skLineSegment(sketch, "E1555", {"start": v(1.69, 7.46) * mm, "end": v(1.05, 7.5) * mm});
            skLineSegment(sketch, "E1556", {"start": v(1.05, 7.5) * mm, "end": v(0.42, 7.53) * mm});
            skLineSegment(sketch, "E1557", {"start": v(0.42, 7.53) * mm, "end": v(-0.22, 7.56) * mm});
            skLineSegment(sketch, "E1558", {"start": v(-0.22, 7.56) * mm, "end": v(-0.85, 7.59) * mm});
            skLineSegment(sketch, "E1559", {"start": v(-0.85, 7.59) * mm, "end": v(-1.49, 7.62) * mm});
            skLineSegment(sketch, "E1560", {"start": v(-1.49, 7.62) * mm, "end": v(-2.12, 7.65) * mm});
            skLineSegment(sketch, "E1561", {"start": v(-2.12, 7.65) * mm, "end": v(-2.76, 7.68) * mm});
            skLineSegment(sketch, "E1562", {"start": v(-2.76, 7.68) * mm, "end": v(-3.4, 7.7) * mm});
            skLineSegment(sketch, "E1563", {"start": v(-3.4, 7.7) * mm, "end": v(-4.03, 7.74) * mm});
            skLineSegment(sketch, "E1564", {"start": v(-4.03, 7.74) * mm, "end": v(-4.67, 7.77) * mm});
            skLineSegment(sketch, "E1565", {"start": v(-4.67, 7.77) * mm, "end": v(-5.3, 7.8) * mm});
            skLineSegment(sketch, "E1566", {"start": v(-5.3, 7.8) * mm, "end": v(-5.94, 7.82) * mm});
            skLineSegment(sketch, "E1567", {"start": v(-5.94, 7.82) * mm, "end": v(-6.57, 7.85) * mm});
            skLineSegment(sketch, "E1568", {"start": v(-6.57, 7.85) * mm, "end": v(-7.2, 7.88) * mm});
            skLineSegment(sketch, "E1569", {"start": v(-7.2, 7.88) * mm, "end": v(-7.84, 7.9) * mm});
            skLineSegment(sketch, "E1570", {"start": v(-7.84, 7.9) * mm, "end": v(-8.48, 7.93) * mm});
            skLineSegment(sketch, "E1571", {"start": v(-8.48, 7.93) * mm, "end": v(-9.11, 7.95) * mm});
            skLineSegment(sketch, "E1572", {"start": v(-9.11, 7.95) * mm, "end": v(-9.75, 7.98) * mm});
            skLineSegment(sketch, "E1573", {"start": v(-9.75, 7.98) * mm, "end": v(-10.38, 8) * mm});
            skLineSegment(sketch, "E1574", {"start": v(-10.38, 8) * mm, "end": v(-11.02, 8.03) * mm});
            skLineSegment(sketch, "E1575", {"start": v(-11.02, 8.03) * mm, "end": v(-11.65, 8.05) * mm});
            skLineSegment(sketch, "E1576", {"start": v(-11.65, 8.05) * mm, "end": v(-12.29, 8.07) * mm});
            skLineSegment(sketch, "E1577", {"start": v(-12.29, 8.07) * mm, "end": v(-12.92, 8.1) * mm});
            skLineSegment(sketch, "E1578", {"start": v(-12.92, 8.1) * mm, "end": v(-13.56, 8.12) * mm});
            skLineSegment(sketch, "E1579", {"start": v(-13.56, 8.12) * mm, "end": v(-14.2, 8.14) * mm});
            skLineSegment(sketch, "E1580", {"start": v(-14.2, 8.14) * mm, "end": v(-14.83, 8.16) * mm});
            skLineSegment(sketch, "E1581", {"start": v(-14.83, 8.16) * mm, "end": v(-15.46, 8.18) * mm});
            skLineSegment(sketch, "E1582", {"start": v(-15.46, 8.18) * mm, "end": v(-16.1, 8.2) * mm});
            skLineSegment(sketch, "E1583", {"start": v(-16.1, 8.2) * mm, "end": v(-16.73, 8.22) * mm});
            skLineSegment(sketch, "E1584", {"start": v(-16.73, 8.22) * mm, "end": v(-17.37, 8.24) * mm});
            skLineSegment(sketch, "E1585", {"start": v(-17.37, 8.24) * mm, "end": v(-18, 8.26) * mm});
            skLineSegment(sketch, "E1586", {"start": v(-18, 8.26) * mm, "end": v(-18.64, 8.28) * mm});
            skLineSegment(sketch, "E1587", {"start": v(-18.64, 8.28) * mm, "end": v(-19.27, 8.3) * mm});
            skLineSegment(sketch, "E1588", {"start": v(-19.27, 8.3) * mm, "end": v(-19.9, 8.31) * mm});
            skLineSegment(sketch, "E1589", {"start": v(-19.9, 8.31) * mm, "end": v(-20.54, 8.33) * mm});
            skLineSegment(sketch, "E1590", {"start": v(-20.54, 8.33) * mm, "end": v(-21.18, 8.35) * mm});
            skLineSegment(sketch, "E1591", {"start": v(-21.18, 8.35) * mm, "end": v(-21.81, 8.36) * mm});
            skLineSegment(sketch, "E1592", {"start": v(-21.81, 8.36) * mm, "end": v(-22.45, 8.38) * mm});
            skLineSegment(sketch, "E1593", {"start": v(-22.45, 8.38) * mm, "end": v(-23.08, 8.4) * mm});
            skLineSegment(sketch, "E1594", {"start": v(-23.08, 8.4) * mm, "end": v(-23.72, 8.41) * mm});
            skLineSegment(sketch, "E1595", {"start": v(-23.72, 8.41) * mm, "end": v(-24.36, 8.42) * mm});
            skLineSegment(sketch, "E1596", {"start": v(-24.36, 8.42) * mm, "end": v(-25, 8.44) * mm});
            skLineSegment(sketch, "E1597", {"start": v(-25, 8.44) * mm, "end": v(-25.63, 8.45) * mm});
            skLineSegment(sketch, "E1598", {"start": v(-25.63, 8.45) * mm, "end": v(-26.26, 8.46) * mm});
            skLineSegment(sketch, "E1599", {"start": v(-26.26, 8.46) * mm, "end": v(-26.9, 8.48) * mm});
            skLineSegment(sketch, "E1600", {"start": v(-26.9, 8.48) * mm, "end": v(-27.53, 8.49) * mm});
            skLineSegment(sketch, "E1601", {"start": v(-27.53, 8.49) * mm, "end": v(-28.17, 8.5) * mm});
            skLineSegment(sketch, "E1602", {"start": v(-28.17, 8.5) * mm, "end": v(-28.8, 8.51) * mm});
            skLineSegment(sketch, "E1603", {"start": v(-28.8, 8.51) * mm, "end": v(-29.44, 8.52) * mm});
            skLineSegment(sketch, "E1604", {"start": v(-29.44, 8.52) * mm, "end": v(-30.07, 8.53) * mm});
            skLineSegment(sketch, "E1605", {"start": v(-30.07, 8.53) * mm, "end": v(-30.7, 8.54) * mm});
            skLineSegment(sketch, "E1606", {"start": v(-30.7, 8.54) * mm, "end": v(-31.34, 8.55) * mm});
            skLineSegment(sketch, "E1607", {"start": v(-31.34, 8.55) * mm, "end": v(-31.98, 8.56) * mm});
            skLineSegment(sketch, "E1608", {"start": v(-31.98, 8.56) * mm, "end": v(-32.61, 8.57) * mm});
            skLineSegment(sketch, "E1609", {"start": v(-32.61, 8.57) * mm, "end": v(-33.25, 8.57) * mm});
            skLineSegment(sketch, "E1610", {"start": v(-33.25, 8.57) * mm, "end": v(-33.88, 8.58) * mm});
            skLineSegment(sketch, "E1611", {"start": v(-33.88, 8.58) * mm, "end": v(-34.52, 8.59) * mm});
            skLineSegment(sketch, "E1612", {"start": v(-34.52, 8.59) * mm, "end": v(-35.15, 8.6) * mm});
            skLineSegment(sketch, "E1613", {"start": v(-35.15, 8.6) * mm, "end": v(-35.79, 8.6) * mm});
            skLineSegment(sketch, "E1614", {"start": v(-35.79, 8.6) * mm, "end": v(-36.42, 8.6) * mm});
            skLineSegment(sketch, "E1615", {"start": v(-36.42, 8.6) * mm, "end": v(-37.06, 8.6) * mm});
            skLineSegment(sketch, "E1616", {"start": v(-37.06, 8.6) * mm, "end": v(-37.7, 8.6) * mm});
            skLineSegment(sketch, "E1617", {"start": v(-37.7, 8.6) * mm, "end": v(-38.33, 8.61) * mm});
            skLineSegment(sketch, "E1618", {"start": v(-38.33, 8.61) * mm, "end": v(-38.96, 8.62) * mm});
            skLineSegment(sketch, "E1619", {"start": v(-38.96, 8.62) * mm, "end": v(-39.6, 8.62) * mm});
            skLineSegment(sketch, "E1620", {"start": v(-39.6, 8.62) * mm, "end": v(-40.23, 8.62) * mm});
            skLineSegment(sketch, "E1621", {"start": v(-40.23, 8.62) * mm, "end": v(-40.87, 8.62) * mm});
            skLineSegment(sketch, "E1622", {"start": v(-40.87, 8.62) * mm, "end": v(-41.5, 8.62) * mm});
            skLineSegment(sketch, "E1623", {"start": v(-41.5, 8.62) * mm, "end": v(-42.14, 8.62) * mm});
            skLineSegment(sketch, "E1624", {"start": v(-42.14, 8.62) * mm, "end": v(-42.77, 8.62) * mm});
            skLineSegment(sketch, "E1625", {"start": v(-42.77, 8.62) * mm, "end": v(-43.4, 8.61) * mm});
            skLineSegment(sketch, "E1626", {"start": v(-43.4, 8.61) * mm, "end": v(-44.04, 8.61) * mm});
            skLineSegment(sketch, "E1627", {"start": v(-44.04, 8.61) * mm, "end": v(-44.68, 8.6) * mm});
            skLineSegment(sketch, "E1628", {"start": v(-44.68, 8.6) * mm, "end": v(-45.31, 8.6) * mm});
            skLineSegment(sketch, "E1629", {"start": v(-45.31, 8.6) * mm, "end": v(-45.95, 8.6) * mm});
            skLineSegment(sketch, "E1630", {"start": v(-45.95, 8.6) * mm, "end": v(-46.58, 8.6) * mm});
            skLineSegment(sketch, "E1631", {"start": v(-46.58, 8.6) * mm, "end": v(-47.22, 8.59) * mm});
            skLineSegment(sketch, "E1632", {"start": v(-47.22, 8.59) * mm, "end": v(-47.85, 8.58) * mm});
            skLineSegment(sketch, "E1633", {"start": v(-47.85, 8.58) * mm, "end": v(-48.49, 8.58) * mm});
            skLineSegment(sketch, "E1634", {"start": v(-48.49, 8.58) * mm, "end": v(-49.12, 8.57) * mm});
            skLineSegment(sketch, "E1635", {"start": v(-49.12, 8.57) * mm, "end": v(-49.76, 8.56) * mm});
            skLineSegment(sketch, "E1636", {"start": v(-49.76, 8.56) * mm, "end": v(-50.4, 8.55) * mm});
            skLineSegment(sketch, "E1637", {"start": v(-50.4, 8.55) * mm, "end": v(-51.03, 8.54) * mm});
            skLineSegment(sketch, "E1638", {"start": v(-51.03, 8.54) * mm, "end": v(-51.66, 8.53) * mm});
            skLineSegment(sketch, "E1639", {"start": v(-51.66, 8.53) * mm, "end": v(-52.3, 8.52) * mm});
            skLineSegment(sketch, "E1640", {"start": v(-52.3, 8.52) * mm, "end": v(-52.93, 8.5) * mm});
            skLineSegment(sketch, "E1641", {"start": v(-52.93, 8.5) * mm, "end": v(-53.57, 8.5) * mm});
            skLineSegment(sketch, "E1642", {"start": v(-53.57, 8.5) * mm, "end": v(-54.2, 8.48) * mm});
            skLineSegment(sketch, "E1643", {"start": v(-54.2, 8.48) * mm, "end": v(-54.84, 8.47) * mm});
            skLineSegment(sketch, "E1644", {"start": v(-54.84, 8.47) * mm, "end": v(-55.47, 8.45) * mm});
            skLineSegment(sketch, "E1645", {"start": v(-55.47, 8.45) * mm, "end": v(-56.1, 8.44) * mm});
            skLineSegment(sketch, "E1646", {"start": v(-56.1, 8.44) * mm, "end": v(-56.74, 8.42) * mm});
            skLineSegment(sketch, "E1647", {"start": v(-56.74, 8.42) * mm, "end": v(-57.37, 8.4) * mm});
            skLineSegment(sketch, "E1648", {"start": v(-57.37, 8.4) * mm, "end": v(-58, 8.39) * mm});
            skLineSegment(sketch, "E1649", {"start": v(-58, 8.39) * mm, "end": v(-58.64, 8.37) * mm});
            skLineSegment(sketch, "E1650", {"start": v(-58.64, 8.37) * mm, "end": v(-59.28, 8.35) * mm});
            skLineSegment(sketch, "E1651", {"start": v(-59.28, 8.35) * mm, "end": v(-59.91, 8.33) * mm});
            skLineSegment(sketch, "E1652", {"start": v(-59.91, 8.33) * mm, "end": v(-60.55, 8.3) * mm});
            skLineSegment(sketch, "E1653", {"start": v(-60.55, 8.3) * mm, "end": v(-61.18, 8.29) * mm});
            skLineSegment(sketch, "E1654", {"start": v(-61.18, 8.29) * mm, "end": v(-61.82, 8.27) * mm});
            skLineSegment(sketch, "E1655", {"start": v(-61.82, 8.27) * mm, "end": v(-62.45, 8.24) * mm});
            skLineSegment(sketch, "E1656", {"start": v(-62.45, 8.24) * mm, "end": v(-63.09, 8.22) * mm});
            skLineSegment(sketch, "E1657", {"start": v(-63.09, 8.22) * mm, "end": v(-63.72, 8.2) * mm});
            skLineSegment(sketch, "E1658", {"start": v(-63.72, 8.2) * mm, "end": v(-64.36, 8.17) * mm});
            skLineSegment(sketch, "E1659", {"start": v(-64.36, 8.17) * mm, "end": v(-65, 8.14) * mm});
            skLineSegment(sketch, "E1660", {"start": v(-65, 8.14) * mm, "end": v(-65.63, 8.12) * mm});
            skLineSegment(sketch, "E1661", {"start": v(-65.63, 8.12) * mm, "end": v(-66.26, 8.09) * mm});
            skLineSegment(sketch, "E1662", {"start": v(-66.26, 8.09) * mm, "end": v(-66.9, 8.06) * mm});
            skLineSegment(sketch, "E1663", {"start": v(-66.9, 8.06) * mm, "end": v(-67.53, 8.03) * mm});
            skLineSegment(sketch, "E1664", {"start": v(-67.53, 8.03) * mm, "end": v(-68.16, 8) * mm});
            skLineSegment(sketch, "E1665", {"start": v(-68.16, 8) * mm, "end": v(-68.8, 7.97) * mm});
            skLineSegment(sketch, "E1666", {"start": v(-68.8, 7.97) * mm, "end": v(-69.43, 7.94) * mm});
            skLineSegment(sketch, "E1667", {"start": v(-69.43, 7.94) * mm, "end": v(-70.07, 7.9) * mm});
            skLineSegment(sketch, "E1668", {"start": v(-70.07, 7.9) * mm, "end": v(-70.7, 7.87) * mm});
            skLineSegment(sketch, "E1669", {"start": v(-70.7, 7.87) * mm, "end": v(-71.34, 7.84) * mm});
            skLineSegment(sketch, "E1670", {"start": v(-71.34, 7.84) * mm, "end": v(-71.97, 7.8) * mm});
            skLineSegment(sketch, "E1671", {"start": v(-71.97, 7.8) * mm, "end": v(-72.6, 7.76) * mm});
            skLineSegment(sketch, "E1672", {"start": v(-72.6, 7.76) * mm, "end": v(-73.24, 7.73) * mm});
            skLineSegment(sketch, "E1673", {"start": v(-73.24, 7.73) * mm, "end": v(-73.88, 7.69) * mm});
            skLineSegment(sketch, "E1674", {"start": v(-73.88, 7.69) * mm, "end": v(-74.51, 7.65) * mm});
            skLineSegment(sketch, "E1675", {"start": v(-74.51, 7.65) * mm, "end": v(-75.15, 7.6) * mm});
            skLineSegment(sketch, "E1676", {"start": v(-75.15, 7.6) * mm, "end": v(-75.78, 7.57) * mm});
            skLineSegment(sketch, "E1677", {"start": v(-75.78, 7.57) * mm, "end": v(-76.42, 7.52) * mm});
            skLineSegment(sketch, "E1678", {"start": v(-76.42, 7.52) * mm, "end": v(-77.05, 7.48) * mm});
            skLineSegment(sketch, "E1679", {"start": v(-77.05, 7.48) * mm, "end": v(-77.68, 7.44) * mm});
            skLineSegment(sketch, "E1680", {"start": v(-77.68, 7.44) * mm, "end": v(-78.32, 7.39) * mm});
            skLineSegment(sketch, "E1681", {"start": v(-78.32, 7.39) * mm, "end": v(-78.95, 7.34) * mm});
            skLineSegment(sketch, "E1682", {"start": v(-78.95, 7.34) * mm, "end": v(-79.59, 7.3) * mm});
            skLineSegment(sketch, "E1683", {"start": v(-79.59, 7.3) * mm, "end": v(-80.22, 7.24) * mm});
            skLineSegment(sketch, "E1684", {"start": v(-80.22, 7.24) * mm, "end": v(-80.86, 7.2) * mm});
            skLineSegment(sketch, "E1685", {"start": v(-80.86, 7.2) * mm, "end": v(-81.5, 7.14) * mm});
            skLineSegment(sketch, "E1686", {"start": v(-81.5, 7.14) * mm, "end": v(-82.13, 7.09) * mm});
            skLineSegment(sketch, "E1687", {"start": v(-82.13, 7.09) * mm, "end": v(-82.76, 7.03) * mm});
            skLineSegment(sketch, "E1688", {"start": v(-82.76, 7.03) * mm, "end": v(-83.4, 6.98) * mm});
            skLineSegment(sketch, "E1689", {"start": v(-83.4, 6.98) * mm, "end": v(-84.03, 6.92) * mm});
            skLineSegment(sketch, "E1690", {"start": v(-84.03, 6.92) * mm, "end": v(-84.67, 6.86) * mm});
            skLineSegment(sketch, "E1691", {"start": v(-84.67, 6.86) * mm, "end": v(-85.3, 6.8) * mm});
            skLineSegment(sketch, "E1692", {"start": v(-85.3, 6.8) * mm, "end": v(-85.93, 6.74) * mm});
            skLineSegment(sketch, "E1693", {"start": v(-85.93, 6.74) * mm, "end": v(-86.57, 6.68) * mm});
            skLineSegment(sketch, "E1694", {"start": v(-86.57, 6.68) * mm, "end": v(-87.2, 6.61) * mm});
            skLineSegment(sketch, "E1695", {"start": v(-87.2, 6.61) * mm, "end": v(-87.84, 6.55) * mm});
            skLineSegment(sketch, "E1696", {"start": v(-87.84, 6.55) * mm, "end": v(-88.47, 6.48) * mm});
            skLineSegment(sketch, "E1697", {"start": v(-88.47, 6.48) * mm, "end": v(-89.1, 6.4) * mm});
            skLineSegment(sketch, "E1698", {"start": v(-89.1, 6.4) * mm, "end": v(-89.74, 6.34) * mm});
            skLineSegment(sketch, "E1699", {"start": v(-89.74, 6.34) * mm, "end": v(-90.38, 6.27) * mm});
            skLineSegment(sketch, "E1700", {"start": v(-90.38, 6.27) * mm, "end": v(-91.01, 6.2) * mm});
            skLineSegment(sketch, "E1701", {"start": v(-91.01, 6.2) * mm, "end": v(-91.64, 6.12) * mm});
            skLineSegment(sketch, "E1702", {"start": v(-91.64, 6.12) * mm, "end": v(-92.28, 6.04) * mm});
            skLineSegment(sketch, "E1703", {"start": v(-92.28, 6.04) * mm, "end": v(-92.91, 5.96) * mm});
            skLineSegment(sketch, "E1704", {"start": v(-92.91, 5.96) * mm, "end": v(-93.55, 5.88) * mm});
            skLineSegment(sketch, "E1705", {"start": v(-93.55, 5.88) * mm, "end": v(-94.18, 5.8) * mm});
            skLineSegment(sketch, "E1706", {"start": v(-94.18, 5.8) * mm, "end": v(-94.82, 5.71) * mm});
            skLineSegment(sketch, "E1707", {"start": v(-94.82, 5.71) * mm, "end": v(-95.45, 5.63) * mm});
            skLineSegment(sketch, "E1708", {"start": v(-95.45, 5.63) * mm, "end": v(-96.09, 5.54) * mm});
            skLineSegment(sketch, "E1709", {"start": v(-96.09, 5.54) * mm, "end": v(-96.72, 5.45) * mm});
            skLineSegment(sketch, "E1710", {"start": v(-96.72, 5.45) * mm, "end": v(-97.35, 5.36) * mm});
            skLineSegment(sketch, "E1711", {"start": v(-97.35, 5.36) * mm, "end": v(-97.99, 5.26) * mm});
            skLineSegment(sketch, "E1712", {"start": v(-97.99, 5.26) * mm, "end": v(-98.62, 5.17) * mm});
            skLineSegment(sketch, "E1713", {"start": v(-98.62, 5.17) * mm, "end": v(-99.26, 5.07) * mm});
            skLineSegment(sketch, "E1714", {"start": v(-99.26, 5.07) * mm, "end": v(-99.9, 4.97) * mm});
            skLineSegment(sketch, "E1715", {"start": v(-99.9, 4.97) * mm, "end": v(-100.52, 4.86) * mm});
            skLineSegment(sketch, "E1716", {"start": v(-100.52, 4.86) * mm, "end": v(-101.16, 4.76) * mm});
            skLineSegment(sketch, "E1717", {"start": v(-101.16, 4.76) * mm, "end": v(-101.8, 4.65) * mm});
            skLineSegment(sketch, "E1718", {"start": v(-101.8, 4.65) * mm, "end": v(-102.43, 4.54) * mm});
            skLineSegment(sketch, "E1719", {"start": v(-102.43, 4.54) * mm, "end": v(-103.06, 4.42) * mm});
            skLineSegment(sketch, "E1720", {"start": v(-103.06, 4.42) * mm, "end": v(-103.7, 4.3) * mm});
            skLineSegment(sketch, "E1721", {"start": v(-103.7, 4.3) * mm, "end": v(-104.33, 4.19) * mm});
            skLineSegment(sketch, "E1722", {"start": v(-104.33, 4.19) * mm, "end": v(-104.96, 4.06) * mm});
            skLineSegment(sketch, "E1723", {"start": v(-104.96, 4.06) * mm, "end": v(-105.6, 3.94) * mm});
            skLineSegment(sketch, "E1724", {"start": v(-105.6, 3.94) * mm, "end": v(-106.23, 3.8) * mm});
            skLineSegment(sketch, "E1725", {"start": v(-106.23, 3.8) * mm, "end": v(-106.87, 3.68) * mm});
            skLineSegment(sketch, "E1726", {"start": v(-106.87, 3.68) * mm, "end": v(-107.5, 3.54) * mm});
            skLineSegment(sketch, "E1727", {"start": v(-107.5, 3.54) * mm, "end": v(-108.13, 3.4) * mm});
            skLineSegment(sketch, "E1728", {"start": v(-108.13, 3.4) * mm, "end": v(-108.77, 3.26) * mm});
            skLineSegment(sketch, "E1729", {"start": v(-108.77, 3.26) * mm, "end": v(-109.4, 3.11) * mm});
            skLineSegment(sketch, "E1730", {"start": v(-109.4, 3.11) * mm, "end": v(-110.03, 2.96) * mm});
            skLineSegment(sketch, "E1731", {"start": v(-110.03, 2.96) * mm, "end": v(-110.67, 2.8) * mm});
            skLineSegment(sketch, "E1732", {"start": v(-110.67, 2.8) * mm, "end": v(-111.3, 2.65) * mm});
            skLineSegment(sketch, "E1733", {"start": v(-111.3, 2.65) * mm, "end": v(-111.93, 2.48) * mm});
            skLineSegment(sketch, "E1734", {"start": v(-111.93, 2.48) * mm, "end": v(-112.57, 2.31) * mm});
            skLineSegment(sketch, "E1735", {"start": v(-112.57, 2.31) * mm, "end": v(-113.2, 2.14) * mm});
            skLineSegment(sketch, "E1736", {"start": v(-113.2, 2.14) * mm, "end": v(-113.83, 1.96) * mm});
            skLineSegment(sketch, "E1737", {"start": v(-113.83, 1.96) * mm, "end": v(-114.47, 1.77) * mm});
            skLineSegment(sketch, "E1738", {"start": v(-114.47, 1.77) * mm, "end": v(-115.1, 1.58) * mm});
            skLineSegment(sketch, "E1739", {"start": v(-115.1, 1.58) * mm, "end": v(-115.73, 1.38) * mm});
            skLineSegment(sketch, "E1740", {"start": v(-115.73, 1.38) * mm, "end": v(-116.37, 1.17) * mm});
            skLineSegment(sketch, "E1741", {"start": v(-116.37, 1.17) * mm, "end": v(-117, 0.96) * mm});
            skLineSegment(sketch, "E1742", {"start": v(61.37, -4.36) * mm, "end": v(60.74, -4.38) * mm});
            skLineSegment(sketch, "E1743", {"start": v(60.74, -4.38) * mm, "end": v(60.1, -4.4) * mm});
            skLineSegment(sketch, "E1744", {"start": v(60.1, -4.4) * mm, "end": v(59.47, -4.43) * mm});
            skLineSegment(sketch, "E1745", {"start": v(59.47, -4.43) * mm, "end": v(58.83, -4.46) * mm});
            skLineSegment(sketch, "E1746", {"start": v(58.83, -4.46) * mm, "end": v(58.2, -4.48) * mm});
            skLineSegment(sketch, "E1747", {"start": v(58.2, -4.48) * mm, "end": v(57.56, -4.51) * mm});
            skLineSegment(sketch, "E1748", {"start": v(57.56, -4.51) * mm, "end": v(56.93, -4.54) * mm});
            skLineSegment(sketch, "E1749", {"start": v(56.93, -4.54) * mm, "end": v(56.3, -4.56) * mm});
            skLineSegment(sketch, "E1750", {"start": v(56.3, -4.56) * mm, "end": v(55.66, -4.59) * mm});
            skLineSegment(sketch, "E1751", {"start": v(55.66, -4.59) * mm, "end": v(55.02, -4.61) * mm});
            skLineSegment(sketch, "E1752", {"start": v(55.02, -4.61) * mm, "end": v(54.39, -4.64) * mm});
            skLineSegment(sketch, "E1753", {"start": v(54.39, -4.64) * mm, "end": v(53.75, -4.66) * mm});
            skLineSegment(sketch, "E1754", {"start": v(53.75, -4.66) * mm, "end": v(53.12, -4.7) * mm});
            skLineSegment(sketch, "E1755", {"start": v(53.12, -4.7) * mm, "end": v(52.48, -4.72) * mm});
            skLineSegment(sketch, "E1756", {"start": v(52.48, -4.72) * mm, "end": v(51.85, -4.74) * mm});
            skLineSegment(sketch, "E1757", {"start": v(51.85, -4.74) * mm, "end": v(51.21, -4.77) * mm});
            skLineSegment(sketch, "E1758", {"start": v(51.21, -4.77) * mm, "end": v(50.58, -4.8) * mm});
            skLineSegment(sketch, "E1759", {"start": v(50.58, -4.8) * mm, "end": v(49.94, -4.82) * mm});
            skLineSegment(sketch, "E1760", {"start": v(49.94, -4.82) * mm, "end": v(49.3, -4.85) * mm});
            skLineSegment(sketch, "E1761", {"start": v(49.3, -4.85) * mm, "end": v(48.67, -4.87) * mm});
            skLineSegment(sketch, "E1762", {"start": v(48.67, -4.87) * mm, "end": v(48.04, -4.9) * mm});
            skLineSegment(sketch, "E1763", {"start": v(48.04, -4.9) * mm, "end": v(47.4, -4.92) * mm});
            skLineSegment(sketch, "E1764", {"start": v(47.4, -4.92) * mm, "end": v(46.77, -4.95) * mm});
            skLineSegment(sketch, "E1765", {"start": v(46.77, -4.95) * mm, "end": v(46.13, -4.98) * mm});
            skLineSegment(sketch, "E1766", {"start": v(46.13, -4.98) * mm, "end": v(45.5, -5) * mm});
            skLineSegment(sketch, "E1767", {"start": v(45.5, -5) * mm, "end": v(44.86, -5.03) * mm});
            skLineSegment(sketch, "E1768", {"start": v(44.86, -5.03) * mm, "end": v(44.23, -5.05) * mm});
            skLineSegment(sketch, "E1769", {"start": v(44.23, -5.05) * mm, "end": v(43.6, -5.08) * mm});
            skLineSegment(sketch, "E1770", {"start": v(43.6, -5.08) * mm, "end": v(42.96, -5.1) * mm});
            skLineSegment(sketch, "E1771", {"start": v(42.96, -5.1) * mm, "end": v(42.32, -5.13) * mm});
            skLineSegment(sketch, "E1772", {"start": v(42.32, -5.13) * mm, "end": v(41.69, -5.16) * mm});
            skLineSegment(sketch, "E1773", {"start": v(41.69, -5.16) * mm, "end": v(41.05, -5.18) * mm});
            skLineSegment(sketch, "E1774", {"start": v(41.05, -5.18) * mm, "end": v(40.42, -5.2) * mm});
            skLineSegment(sketch, "E1775", {"start": v(40.42, -5.2) * mm, "end": v(39.78, -5.24) * mm});
            skLineSegment(sketch, "E1776", {"start": v(39.78, -5.24) * mm, "end": v(39.15, -5.26) * mm});
            skLineSegment(sketch, "E1777", {"start": v(39.15, -5.26) * mm, "end": v(38.51, -5.29) * mm});
            skLineSegment(sketch, "E1778", {"start": v(38.51, -5.29) * mm, "end": v(37.88, -5.31) * mm});
            skLineSegment(sketch, "E1779", {"start": v(37.88, -5.31) * mm, "end": v(37.24, -5.34) * mm});
            skLineSegment(sketch, "E1780", {"start": v(37.24, -5.34) * mm, "end": v(36.6, -5.37) * mm});
            skLineSegment(sketch, "E1781", {"start": v(36.6, -5.37) * mm, "end": v(35.97, -5.4) * mm});
            skLineSegment(sketch, "E1782", {"start": v(35.97, -5.4) * mm, "end": v(35.34, -5.42) * mm});
            skLineSegment(sketch, "E1783", {"start": v(35.34, -5.42) * mm, "end": v(34.7, -5.44) * mm});
            skLineSegment(sketch, "E1784", {"start": v(34.7, -5.44) * mm, "end": v(34.07, -5.47) * mm});
            skLineSegment(sketch, "E1785", {"start": v(34.07, -5.47) * mm, "end": v(33.43, -5.5) * mm});
            skLineSegment(sketch, "E1786", {"start": v(33.43, -5.5) * mm, "end": v(32.8, -5.52) * mm});
            skLineSegment(sketch, "E1787", {"start": v(32.8, -5.52) * mm, "end": v(32.16, -5.55) * mm});
            skLineSegment(sketch, "E1788", {"start": v(32.16, -5.55) * mm, "end": v(31.53, -5.57) * mm});
            skLineSegment(sketch, "E1789", {"start": v(31.53, -5.57) * mm, "end": v(30.9, -5.6) * mm});
            skLineSegment(sketch, "E1790", {"start": v(30.9, -5.6) * mm, "end": v(30.26, -5.63) * mm});
            skLineSegment(sketch, "E1791", {"start": v(30.26, -5.63) * mm, "end": v(29.62, -5.65) * mm});
            skLineSegment(sketch, "E1792", {"start": v(29.62, -5.65) * mm, "end": v(28.99, -5.68) * mm});
            skLineSegment(sketch, "E1793", {"start": v(28.99, -5.68) * mm, "end": v(28.35, -5.7) * mm});
            skLineSegment(sketch, "E1794", {"start": v(28.35, -5.7) * mm, "end": v(27.72, -5.73) * mm});
            skLineSegment(sketch, "E1795", {"start": v(27.72, -5.73) * mm, "end": v(27.08, -5.76) * mm});
            skLineSegment(sketch, "E1796", {"start": v(27.08, -5.76) * mm, "end": v(26.45, -5.78) * mm});
            skLineSegment(sketch, "E1797", {"start": v(26.45, -5.78) * mm, "end": v(25.81, -5.8) * mm});
            skLineSegment(sketch, "E1798", {"start": v(25.81, -5.8) * mm, "end": v(25.18, -5.84) * mm});
            skLineSegment(sketch, "E1799", {"start": v(25.18, -5.84) * mm, "end": v(24.54, -5.86) * mm});
            skLineSegment(sketch, "E1800", {"start": v(24.54, -5.86) * mm, "end": v(23.9, -5.89) * mm});
            skLineSegment(sketch, "E1801", {"start": v(23.9, -5.89) * mm, "end": v(23.27, -5.91) * mm});
            skLineSegment(sketch, "E1802", {"start": v(23.27, -5.91) * mm, "end": v(22.64, -5.94) * mm});
            skLineSegment(sketch, "E1803", {"start": v(22.64, -5.94) * mm, "end": v(22, -5.97) * mm});
            skLineSegment(sketch, "E1804", {"start": v(22, -5.97) * mm, "end": v(21.37, -6) * mm});
            skLineSegment(sketch, "E1805", {"start": v(21.37, -6) * mm, "end": v(20.73, -6.02) * mm});
            skLineSegment(sketch, "E1806", {"start": v(20.73, -6.02) * mm, "end": v(20.1, -6.04) * mm});
            skLineSegment(sketch, "E1807", {"start": v(20.1, -6.04) * mm, "end": v(19.46, -6.07) * mm});
            skLineSegment(sketch, "E1808", {"start": v(19.46, -6.07) * mm, "end": v(18.83, -6.1) * mm});
            skLineSegment(sketch, "E1809", {"start": v(18.83, -6.1) * mm, "end": v(18.2, -6.12) * mm});
            skLineSegment(sketch, "E1810", {"start": v(18.2, -6.12) * mm, "end": v(17.56, -6.15) * mm});
            skLineSegment(sketch, "E1811", {"start": v(17.56, -6.15) * mm, "end": v(16.92, -6.17) * mm});
            skLineSegment(sketch, "E1812", {"start": v(16.92, -6.17) * mm, "end": v(16.29, -6.2) * mm});
            skLineSegment(sketch, "E1813", {"start": v(16.29, -6.2) * mm, "end": v(15.65, -6.22) * mm});
            skLineSegment(sketch, "E1814", {"start": v(15.65, -6.22) * mm, "end": v(15.02, -6.25) * mm});
            skLineSegment(sketch, "E1815", {"start": v(15.02, -6.25) * mm, "end": v(14.38, -6.27) * mm});
            skLineSegment(sketch, "E1816", {"start": v(14.38, -6.27) * mm, "end": v(13.75, -6.3) * mm});
            skLineSegment(sketch, "E1817", {"start": v(13.75, -6.3) * mm, "end": v(13.11, -6.32) * mm});
            skLineSegment(sketch, "E1818", {"start": v(13.11, -6.32) * mm, "end": v(12.48, -6.35) * mm});
            skLineSegment(sketch, "E1819", {"start": v(12.48, -6.35) * mm, "end": v(11.84, -6.37) * mm});
            skLineSegment(sketch, "E1820", {"start": v(11.84, -6.37) * mm, "end": v(11.2, -6.4) * mm});
            skLineSegment(sketch, "E1821", {"start": v(11.2, -6.4) * mm, "end": v(10.57, -6.42) * mm});
            skLineSegment(sketch, "E1822", {"start": v(10.57, -6.42) * mm, "end": v(9.94, -6.45) * mm});
            skLineSegment(sketch, "E1823", {"start": v(9.94, -6.45) * mm, "end": v(9.3, -6.47) * mm});
            skLineSegment(sketch, "E1824", {"start": v(9.3, -6.47) * mm, "end": v(8.67, -6.5) * mm});
            skLineSegment(sketch, "E1825", {"start": v(8.67, -6.5) * mm, "end": v(8.03, -6.52) * mm});
            skLineSegment(sketch, "E1826", {"start": v(8.03, -6.52) * mm, "end": v(7.4, -6.55) * mm});
            skLineSegment(sketch, "E1827", {"start": v(7.4, -6.55) * mm, "end": v(6.76, -6.57) * mm});
            skLineSegment(sketch, "E1828", {"start": v(6.76, -6.57) * mm, "end": v(6.13, -6.6) * mm});
            skLineSegment(sketch, "E1829", {"start": v(6.13, -6.6) * mm, "end": v(5.5, -6.62) * mm});
            skLineSegment(sketch, "E1830", {"start": v(5.5, -6.62) * mm, "end": v(4.86, -6.64) * mm});
            skLineSegment(sketch, "E1831", {"start": v(4.86, -6.64) * mm, "end": v(4.22, -6.67) * mm});
            skLineSegment(sketch, "E1832", {"start": v(4.22, -6.67) * mm, "end": v(3.59, -6.7) * mm});
            skLineSegment(sketch, "E1833", {"start": v(3.59, -6.7) * mm, "end": v(2.95, -6.72) * mm});
            skLineSegment(sketch, "E1834", {"start": v(2.95, -6.72) * mm, "end": v(2.32, -6.74) * mm});
            skLineSegment(sketch, "E1835", {"start": v(2.32, -6.74) * mm, "end": v(1.68, -6.76) * mm});
            skLineSegment(sketch, "E1836", {"start": v(1.68, -6.76) * mm, "end": v(1.05, -6.79) * mm});
            skLineSegment(sketch, "E1837", {"start": v(1.05, -6.79) * mm, "end": v(0.41, -6.81) * mm});
            skLineSegment(sketch, "E1838", {"start": v(0.41, -6.81) * mm, "end": v(-0.22, -6.84) * mm});
            skLineSegment(sketch, "E1839", {"start": v(-0.22, -6.84) * mm, "end": v(-0.86, -6.86) * mm});
            skLineSegment(sketch, "E1840", {"start": v(-0.86, -6.86) * mm, "end": v(-1.5, -6.88) * mm});
            skLineSegment(sketch, "E1841", {"start": v(-1.5, -6.88) * mm, "end": v(-2.13, -6.9) * mm});
            skLineSegment(sketch, "E1842", {"start": v(-2.13, -6.9) * mm, "end": v(-2.76, -6.93) * mm});
            skLineSegment(sketch, "E1843", {"start": v(-2.76, -6.93) * mm, "end": v(-3.4, -6.95) * mm});
            skLineSegment(sketch, "E1844", {"start": v(-3.4, -6.95) * mm, "end": v(-4.03, -6.98) * mm});
            skLineSegment(sketch, "E1845", {"start": v(-4.03, -6.98) * mm, "end": v(-4.67, -7) * mm});
            skLineSegment(sketch, "E1846", {"start": v(-4.67, -7) * mm, "end": v(-5.3, -7.03) * mm});
            skLineSegment(sketch, "E1847", {"start": v(-5.3, -7.03) * mm, "end": v(-5.94, -7.05) * mm});
            skLineSegment(sketch, "E1848", {"start": v(-5.94, -7.05) * mm, "end": v(-6.57, -7.07) * mm});
            skLineSegment(sketch, "E1849", {"start": v(-6.57, -7.07) * mm, "end": v(-7.2, -7.1) * mm});
            skLineSegment(sketch, "E1850", {"start": v(-7.2, -7.1) * mm, "end": v(-7.84, -7.12) * mm});
            skLineSegment(sketch, "E1851", {"start": v(-7.84, -7.12) * mm, "end": v(-8.48, -7.14) * mm});
            skLineSegment(sketch, "E1852", {"start": v(-8.48, -7.14) * mm, "end": v(-9.11, -7.16) * mm});
            skLineSegment(sketch, "E1853", {"start": v(-9.11, -7.16) * mm, "end": v(-9.75, -7.19) * mm});
            skLineSegment(sketch, "E1854", {"start": v(-9.75, -7.19) * mm, "end": v(-10.38, -7.2) * mm});
            skLineSegment(sketch, "E1855", {"start": v(-10.38, -7.2) * mm, "end": v(-11.02, -7.23) * mm});
            skLineSegment(sketch, "E1856", {"start": v(-11.02, -7.23) * mm, "end": v(-11.65, -7.25) * mm});
            skLineSegment(sketch, "E1857", {"start": v(-11.65, -7.25) * mm, "end": v(-12.29, -7.28) * mm});
            skLineSegment(sketch, "E1858", {"start": v(-12.29, -7.28) * mm, "end": v(-12.92, -7.3) * mm});
            skLineSegment(sketch, "E1859", {"start": v(-12.92, -7.3) * mm, "end": v(-13.56, -7.32) * mm});
            skLineSegment(sketch, "E1860", {"start": v(-13.56, -7.32) * mm, "end": v(-14.2, -7.34) * mm});
            skLineSegment(sketch, "E1861", {"start": v(-14.2, -7.34) * mm, "end": v(-14.83, -7.36) * mm});
            skLineSegment(sketch, "E1862", {"start": v(-14.83, -7.36) * mm, "end": v(-15.46, -7.38) * mm});
            skLineSegment(sketch, "E1863", {"start": v(-15.46, -7.38) * mm, "end": v(-16.1, -7.4) * mm});
            skLineSegment(sketch, "E1864", {"start": v(-16.1, -7.4) * mm, "end": v(-16.73, -7.43) * mm});
            skLineSegment(sketch, "E1865", {"start": v(-16.73, -7.43) * mm, "end": v(-17.37, -7.45) * mm});
            skLineSegment(sketch, "E1866", {"start": v(-17.37, -7.45) * mm, "end": v(-18, -7.47) * mm});
            skLineSegment(sketch, "E1867", {"start": v(-18, -7.47) * mm, "end": v(-18.64, -7.5) * mm});
            skLineSegment(sketch, "E1868", {"start": v(-18.64, -7.5) * mm, "end": v(-19.27, -7.51) * mm});
            skLineSegment(sketch, "E1869", {"start": v(-19.27, -7.51) * mm, "end": v(-19.9, -7.53) * mm});
            skLineSegment(sketch, "E1870", {"start": v(-19.9, -7.53) * mm, "end": v(-20.54, -7.55) * mm});
            skLineSegment(sketch, "E1871", {"start": v(-20.54, -7.55) * mm, "end": v(-21.18, -7.58) * mm});
            skLineSegment(sketch, "E1872", {"start": v(-21.18, -7.58) * mm, "end": v(-21.81, -7.6) * mm});
            skLineSegment(sketch, "E1873", {"start": v(-21.81, -7.6) * mm, "end": v(-22.45, -7.62) * mm});
            skLineSegment(sketch, "E1874", {"start": v(-22.45, -7.62) * mm, "end": v(-23.08, -7.64) * mm});
            skLineSegment(sketch, "E1875", {"start": v(-23.08, -7.64) * mm, "end": v(-23.72, -7.66) * mm});
            skLineSegment(sketch, "E1876", {"start": v(-23.72, -7.66) * mm, "end": v(-24.35, -7.68) * mm});
            skLineSegment(sketch, "E1877", {"start": v(-24.35, -7.68) * mm, "end": v(-24.99, -7.7) * mm});
            skLineSegment(sketch, "E1878", {"start": v(-24.99, -7.7) * mm, "end": v(-25.62, -7.72) * mm});
            skLineSegment(sketch, "E1879", {"start": v(-25.62, -7.72) * mm, "end": v(-26.26, -7.74) * mm});
            skLineSegment(sketch, "E1880", {"start": v(-26.26, -7.74) * mm, "end": v(-26.9, -7.76) * mm});
            skLineSegment(sketch, "E1881", {"start": v(-26.9, -7.76) * mm, "end": v(-27.53, -7.77) * mm});
            skLineSegment(sketch, "E1882", {"start": v(-27.53, -7.77) * mm, "end": v(-28.16, -7.8) * mm});
            skLineSegment(sketch, "E1883", {"start": v(-28.16, -7.8) * mm, "end": v(-28.8, -7.81) * mm});
            skLineSegment(sketch, "E1884", {"start": v(-28.8, -7.81) * mm, "end": v(-29.43, -7.83) * mm});
            skLineSegment(sketch, "E1885", {"start": v(-29.43, -7.83) * mm, "end": v(-30.07, -7.85) * mm});
            skLineSegment(sketch, "E1886", {"start": v(-30.07, -7.85) * mm, "end": v(-30.7, -7.87) * mm});
            skLineSegment(sketch, "E1887", {"start": v(-30.7, -7.87) * mm, "end": v(-31.34, -7.89) * mm});
            skLineSegment(sketch, "E1888", {"start": v(-31.34, -7.89) * mm, "end": v(-31.97, -7.9) * mm});
            skLineSegment(sketch, "E1889", {"start": v(-31.97, -7.9) * mm, "end": v(-32.6, -7.92) * mm});
            skLineSegment(sketch, "E1890", {"start": v(-32.6, -7.92) * mm, "end": v(-33.24, -7.94) * mm});
            skLineSegment(sketch, "E1891", {"start": v(-33.24, -7.94) * mm, "end": v(-33.88, -7.96) * mm});
            skLineSegment(sketch, "E1892", {"start": v(-33.88, -7.96) * mm, "end": v(-34.51, -7.98) * mm});
            skLineSegment(sketch, "E1893", {"start": v(-34.51, -7.98) * mm, "end": v(-35.15, -8) * mm});
            skLineSegment(sketch, "E1894", {"start": v(-35.15, -8) * mm, "end": v(-35.78, -8.01) * mm});
            skLineSegment(sketch, "E1895", {"start": v(-35.78, -8.01) * mm, "end": v(-36.42, -8.03) * mm});
            skLineSegment(sketch, "E1896", {"start": v(-36.42, -8.03) * mm, "end": v(-37.05, -8.05) * mm});
            skLineSegment(sketch, "E1897", {"start": v(-37.05, -8.05) * mm, "end": v(-37.69, -8.06) * mm});
            skLineSegment(sketch, "E1898", {"start": v(-37.69, -8.06) * mm, "end": v(-38.32, -8.08) * mm});
            skLineSegment(sketch, "E1899", {"start": v(-38.32, -8.08) * mm, "end": v(-38.96, -8.1) * mm});
            skLineSegment(sketch, "E1900", {"start": v(-38.96, -8.1) * mm, "end": v(-39.6, -8.11) * mm});
            skLineSegment(sketch, "E1901", {"start": v(-39.6, -8.11) * mm, "end": v(-40.23, -8.13) * mm});
            skLineSegment(sketch, "E1902", {"start": v(-40.23, -8.13) * mm, "end": v(-40.86, -8.14) * mm});
            skLineSegment(sketch, "E1903", {"start": v(-40.86, -8.14) * mm, "end": v(-41.5, -8.16) * mm});
            skLineSegment(sketch, "E1904", {"start": v(-41.5, -8.16) * mm, "end": v(-42.13, -8.17) * mm});
            skLineSegment(sketch, "E1905", {"start": v(-42.13, -8.17) * mm, "end": v(-42.77, -8.19) * mm});
            skLineSegment(sketch, "E1906", {"start": v(-42.77, -8.19) * mm, "end": v(-43.4, -8.2) * mm});
            skLineSegment(sketch, "E1907", {"start": v(-43.4, -8.2) * mm, "end": v(-44.04, -8.22) * mm});
            skLineSegment(sketch, "E1908", {"start": v(-44.04, -8.22) * mm, "end": v(-44.68, -8.23) * mm});
            skLineSegment(sketch, "E1909", {"start": v(-44.68, -8.23) * mm, "end": v(-45.31, -8.25) * mm});
            skLineSegment(sketch, "E1910", {"start": v(-45.31, -8.25) * mm, "end": v(-45.95, -8.26) * mm});
            skLineSegment(sketch, "E1911", {"start": v(-45.95, -8.26) * mm, "end": v(-46.58, -8.28) * mm});
            skLineSegment(sketch, "E1912", {"start": v(-46.58, -8.28) * mm, "end": v(-47.22, -8.3) * mm});
            skLineSegment(sketch, "E1913", {"start": v(-47.22, -8.3) * mm, "end": v(-47.85, -8.3) * mm});
            skLineSegment(sketch, "E1914", {"start": v(-47.85, -8.3) * mm, "end": v(-48.49, -8.32) * mm});
            skLineSegment(sketch, "E1915", {"start": v(-48.49, -8.32) * mm, "end": v(-49.12, -8.33) * mm});
            skLineSegment(sketch, "E1916", {"start": v(-49.12, -8.33) * mm, "end": v(-49.76, -8.34) * mm});
            skLineSegment(sketch, "E1917", {"start": v(-49.76, -8.34) * mm, "end": v(-50.4, -8.36) * mm});
            skLineSegment(sketch, "E1918", {"start": v(-50.4, -8.36) * mm, "end": v(-51.03, -8.37) * mm});
            skLineSegment(sketch, "E1919", {"start": v(-51.03, -8.37) * mm, "end": v(-51.66, -8.38) * mm});
            skLineSegment(sketch, "E1920", {"start": v(-51.66, -8.38) * mm, "end": v(-52.3, -8.4) * mm});
            skLineSegment(sketch, "E1921", {"start": v(-52.3, -8.4) * mm, "end": v(-52.93, -8.4) * mm});
            skLineSegment(sketch, "E1922", {"start": v(-52.93, -8.4) * mm, "end": v(-53.57, -8.42) * mm});
            skLineSegment(sketch, "E1923", {"start": v(-53.57, -8.42) * mm, "end": v(-54.2, -8.43) * mm});
            skLineSegment(sketch, "E1924", {"start": v(-54.2, -8.43) * mm, "end": v(-54.84, -8.44) * mm});
            skLineSegment(sketch, "E1925", {"start": v(-54.84, -8.44) * mm, "end": v(-55.47, -8.45) * mm});
            skLineSegment(sketch, "E1926", {"start": v(-55.47, -8.45) * mm, "end": v(-56.1, -8.46) * mm});
            skLineSegment(sketch, "E1927", {"start": v(-56.1, -8.46) * mm, "end": v(-56.74, -8.47) * mm});
            skLineSegment(sketch, "E1928", {"start": v(-56.74, -8.47) * mm, "end": v(-57.38, -8.48) * mm});
            skLineSegment(sketch, "E1929", {"start": v(-57.38, -8.48) * mm, "end": v(-58.01, -8.5) * mm});
            skLineSegment(sketch, "E1930", {"start": v(-58.01, -8.5) * mm, "end": v(-58.65, -8.5) * mm});
            skLineSegment(sketch, "E1931", {"start": v(-58.65, -8.5) * mm, "end": v(-59.28, -8.5) * mm});
            skLineSegment(sketch, "E1932", {"start": v(-59.28, -8.5) * mm, "end": v(-59.92, -8.52) * mm});
            skLineSegment(sketch, "E1933", {"start": v(-59.92, -8.52) * mm, "end": v(-60.55, -8.53) * mm});
            skLineSegment(sketch, "E1934", {"start": v(-60.55, -8.53) * mm, "end": v(-61.19, -8.53) * mm});
            skLineSegment(sketch, "E1935", {"start": v(-61.19, -8.53) * mm, "end": v(-61.82, -8.54) * mm});
            skLineSegment(sketch, "E1936", {"start": v(-61.82, -8.54) * mm, "end": v(-62.46, -8.55) * mm});
            skLineSegment(sketch, "E1937", {"start": v(-62.46, -8.55) * mm, "end": v(-63.1, -8.56) * mm});
            skLineSegment(sketch, "E1938", {"start": v(-63.1, -8.56) * mm, "end": v(-63.73, -8.56) * mm});
            skLineSegment(sketch, "E1939", {"start": v(-63.73, -8.56) * mm, "end": v(-64.36, -8.57) * mm});
            skLineSegment(sketch, "E1940", {"start": v(-64.36, -8.57) * mm, "end": v(-65, -8.57) * mm});
            skLineSegment(sketch, "E1941", {"start": v(-65, -8.57) * mm, "end": v(-65.63, -8.58) * mm});
            skLineSegment(sketch, "E1942", {"start": v(-65.63, -8.58) * mm, "end": v(-66.27, -8.59) * mm});
            skLineSegment(sketch, "E1943", {"start": v(-66.27, -8.59) * mm, "end": v(-66.9, -8.6) * mm});
            skLineSegment(sketch, "E1944", {"start": v(-66.9, -8.6) * mm, "end": v(-67.54, -8.6) * mm});
            skLineSegment(sketch, "E1945", {"start": v(-67.54, -8.6) * mm, "end": v(-68.17, -8.6) * mm});
            skLineSegment(sketch, "E1946", {"start": v(-68.17, -8.6) * mm, "end": v(-68.8, -8.6) * mm});
            skLineSegment(sketch, "E1947", {"start": v(-68.8, -8.6) * mm, "end": v(-69.44, -8.6) * mm});
            skLineSegment(sketch, "E1948", {"start": v(-69.44, -8.6) * mm, "end": v(-70.08, -8.6) * mm});
            skLineSegment(sketch, "E1949", {"start": v(-70.08, -8.6) * mm, "end": v(-70.71, -8.61) * mm});
            skLineSegment(sketch, "E1950", {"start": v(-70.71, -8.61) * mm, "end": v(-71.35, -8.61) * mm});
            skLineSegment(sketch, "E1951", {"start": v(-71.35, -8.61) * mm, "end": v(-71.98, -8.62) * mm});
            skLineSegment(sketch, "E1952", {"start": v(-71.98, -8.62) * mm, "end": v(-72.62, -8.62) * mm});
            skLineSegment(sketch, "E1953", {"start": v(-72.62, -8.62) * mm, "end": v(-73.25, -8.62) * mm});
            skLineSegment(sketch, "E1954", {"start": v(-73.25, -8.62) * mm, "end": v(-73.89, -8.62) * mm});
            skLineSegment(sketch, "E1955", {"start": v(-73.89, -8.62) * mm, "end": v(-74.52, -8.62) * mm});
            skLineSegment(sketch, "E1956", {"start": v(-74.52, -8.62) * mm, "end": v(-75.16, -8.62) * mm});
            skLineSegment(sketch, "E1957", {"start": v(-75.16, -8.62) * mm, "end": v(-75.8, -8.62) * mm});
            skLineSegment(sketch, "E1958", {"start": v(-75.8, -8.62) * mm, "end": v(-76.43, -8.62) * mm});
            skLineSegment(sketch, "E1959", {"start": v(-76.43, -8.62) * mm, "end": v(-77.06, -8.61) * mm});
            skLineSegment(sketch, "E1960", {"start": v(-77.06, -8.61) * mm, "end": v(-77.7, -8.61) * mm});
            skLineSegment(sketch, "E1961", {"start": v(-77.7, -8.61) * mm, "end": v(-78.33, -8.6) * mm});
            skLineSegment(sketch, "E1962", {"start": v(-78.33, -8.6) * mm, "end": v(-78.97, -8.6) * mm});
            skLineSegment(sketch, "E1963", {"start": v(-78.97, -8.6) * mm, "end": v(-79.6, -8.6) * mm});
            skLineSegment(sketch, "E1964", {"start": v(-79.6, -8.6) * mm, "end": v(-80.24, -8.6) * mm});
            skLineSegment(sketch, "E1965", {"start": v(-80.24, -8.6) * mm, "end": v(-80.87, -8.59) * mm});
            skLineSegment(sketch, "E1966", {"start": v(-80.87, -8.59) * mm, "end": v(-81.5, -8.58) * mm});
            skLineSegment(sketch, "E1967", {"start": v(-81.5, -8.58) * mm, "end": v(-82.14, -8.58) * mm});
            skLineSegment(sketch, "E1968", {"start": v(-82.14, -8.58) * mm, "end": v(-82.78, -8.57) * mm});
            skLineSegment(sketch, "E1969", {"start": v(-82.78, -8.57) * mm, "end": v(-83.41, -8.56) * mm});
            skLineSegment(sketch, "E1970", {"start": v(-83.41, -8.56) * mm, "end": v(-84.05, -8.55) * mm});
            skLineSegment(sketch, "E1971", {"start": v(-84.05, -8.55) * mm, "end": v(-84.68, -8.54) * mm});
            skLineSegment(sketch, "E1972", {"start": v(-84.68, -8.54) * mm, "end": v(-85.32, -8.53) * mm});
            skLineSegment(sketch, "E1973", {"start": v(-85.32, -8.53) * mm, "end": v(-85.95, -8.52) * mm});
            skLineSegment(sketch, "E1974", {"start": v(-85.95, -8.52) * mm, "end": v(-86.59, -8.51) * mm});
            skLineSegment(sketch, "E1975", {"start": v(-86.59, -8.51) * mm, "end": v(-87.22, -8.5) * mm});
            skLineSegment(sketch, "E1976", {"start": v(-87.22, -8.5) * mm, "end": v(-87.86, -8.49) * mm});
            skLineSegment(sketch, "E1977", {"start": v(-87.86, -8.49) * mm, "end": v(-88.5, -8.47) * mm});
            skLineSegment(sketch, "E1978", {"start": v(-88.5, -8.47) * mm, "end": v(-89.13, -8.46) * mm});
            skLineSegment(sketch, "E1979", {"start": v(-89.13, -8.46) * mm, "end": v(-89.76, -8.44) * mm});
            skLineSegment(sketch, "E1980", {"start": v(-89.76, -8.44) * mm, "end": v(-90.4, -8.43) * mm});
            skLineSegment(sketch, "E1981", {"start": v(-90.4, -8.43) * mm, "end": v(-91.03, -8.4) * mm});
            skLineSegment(sketch, "E1982", {"start": v(-91.03, -8.4) * mm, "end": v(-91.66, -8.4) * mm});
            skLineSegment(sketch, "E1983", {"start": v(-91.66, -8.4) * mm, "end": v(-92.3, -8.37) * mm});
            skLineSegment(sketch, "E1984", {"start": v(-92.3, -8.37) * mm, "end": v(-92.93, -8.35) * mm});
            skLineSegment(sketch, "E1985", {"start": v(-92.93, -8.35) * mm, "end": v(-93.57, -8.33) * mm});
            skLineSegment(sketch, "E1986", {"start": v(-93.57, -8.33) * mm, "end": v(-94.2, -8.31) * mm});
            skLineSegment(sketch, "E1987", {"start": v(-94.2, -8.31) * mm, "end": v(-94.84, -8.29) * mm});
            skLineSegment(sketch, "E1988", {"start": v(-94.84, -8.29) * mm, "end": v(-95.47, -8.26) * mm});
            skLineSegment(sketch, "E1989", {"start": v(-95.47, -8.26) * mm, "end": v(-96.1, -8.24) * mm});
            skLineSegment(sketch, "E1990", {"start": v(-96.1, -8.24) * mm, "end": v(-96.74, -8.21) * mm});
            skLineSegment(sketch, "E1991", {"start": v(-96.74, -8.21) * mm, "end": v(-97.38, -8.19) * mm});
            skLineSegment(sketch, "E1992", {"start": v(-97.38, -8.19) * mm, "end": v(-98.01, -8.16) * mm});
            skLineSegment(sketch, "E1993", {"start": v(-98.01, -8.16) * mm, "end": v(-98.64, -8.13) * mm});
            skLineSegment(sketch, "E1994", {"start": v(-98.64, -8.13) * mm, "end": v(-99.28, -8.1) * mm});
            skLineSegment(sketch, "E1995", {"start": v(-99.28, -8.1) * mm, "end": v(-99.91, -8.06) * mm});
            skLineSegment(sketch, "E1996", {"start": v(-99.91, -8.06) * mm, "end": v(-100.55, -8.03) * mm});
            skLineSegment(sketch, "E1997", {"start": v(-100.55, -8.03) * mm, "end": v(-101.18, -8) * mm});
            skLineSegment(sketch, "E1998", {"start": v(-101.18, -8) * mm, "end": v(-101.82, -7.96) * mm});
            skLineSegment(sketch, "E1999", {"start": v(-101.82, -7.96) * mm, "end": v(-102.45, -7.92) * mm});
            skLineSegment(sketch, "E2000", {"start": v(-102.45, -7.92) * mm, "end": v(-103.09, -7.88) * mm});
            skLineSegment(sketch, "E2001", {"start": v(-103.09, -7.88) * mm, "end": v(-103.72, -7.84) * mm});
            skLineSegment(sketch, "E2002", {"start": v(-103.72, -7.84) * mm, "end": v(-104.36, -7.8) * mm});
            skLineSegment(sketch, "E2003", {"start": v(-104.36, -7.8) * mm, "end": v(-104.99, -7.75) * mm});
            skLineSegment(sketch, "E2004", {"start": v(-104.99, -7.75) * mm, "end": v(-105.62, -7.7) * mm});
            skLineSegment(sketch, "E2005", {"start": v(-105.62, -7.7) * mm, "end": v(-106.26, -7.65) * mm});
            skLineSegment(sketch, "E2006", {"start": v(-106.26, -7.65) * mm, "end": v(-106.9, -7.6) * mm});
            skLineSegment(sketch, "E2007", {"start": v(-106.9, -7.6) * mm, "end": v(-107.53, -7.54) * mm});
            skLineSegment(sketch, "E2008", {"start": v(-107.53, -7.54) * mm, "end": v(-108.16, -7.49) * mm});
            skLineSegment(sketch, "E2009", {"start": v(-108.16, -7.49) * mm, "end": v(-108.8, -7.43) * mm});
            skLineSegment(sketch, "E2010", {"start": v(-108.8, -7.43) * mm, "end": v(-109.43, -7.37) * mm});
            skLineSegment(sketch, "E2011", {"start": v(-109.43, -7.37) * mm, "end": v(-110.06, -7.3) * mm});
            skLineSegment(sketch, "E2012", {"start": v(-110.06, -7.3) * mm, "end": v(-110.7, -7.24) * mm});
            skLineSegment(sketch, "E2013", {"start": v(-110.7, -7.24) * mm, "end": v(-111.33, -7.17) * mm});
            skLineSegment(sketch, "E2014", {"start": v(-111.33, -7.17) * mm, "end": v(-111.97, -7.1) * mm});
            skLineSegment(sketch, "E2015", {"start": v(-111.97, -7.1) * mm, "end": v(-112.6, -7.02) * mm});
            skLineSegment(sketch, "E2016", {"start": v(-112.6, -7.02) * mm, "end": v(-113.23, -6.94) * mm});
            skLineSegment(sketch, "E2017", {"start": v(-113.23, -6.94) * mm, "end": v(-113.87, -6.86) * mm});
            skLineSegment(sketch, "E2018", {"start": v(-113.87, -6.86) * mm, "end": v(-114.5, -6.78) * mm});
            skLineSegment(sketch, "E2019", {"start": v(-114.5, -6.78) * mm, "end": v(-115.13, -6.68) * mm});
            skLineSegment(sketch, "E2020", {"start": v(-115.13, -6.68) * mm, "end": v(-115.77, -6.58) * mm});
            skLineSegment(sketch, "E2021", {"start": v(-115.77, -6.58) * mm, "end": v(-116.4, -6.48) * mm});
            skLineSegment(sketch, "E2022", {"start": v(-116.4, -6.48) * mm, "end": v(-117.03, -6.38) * mm});
            skLineSegment(sketch, "E2023", {"start": v(-116.97, 2.41) * mm, "end": v(-117, 0.96) * mm});
            skLineSegment(sketch, "E2024", {"start": v(-117.03, -6.38) * mm, "end": v(-117.33, -7.8) * mm});
            skLineSegment(sketch, "E2025", {"start": v(61.37, -4.36) * mm, "end": v(61.79, -5.85) * mm});
            skLineSegment(sketch, "E2026", {"start": v(-117, -7.85) * mm, "end": v(-116.82, -7.88) * mm});
            skSolve(sketch);
        }
        {
            var Q0;
            Q0 = qSketchRegion(id + "F2", true);
            extrude(context, id + "F3", {"entities" : qUnion([Q0]), "operationType" : NewBodyOperationType.ADD, "depth" : 2.5 * mm, "offsetDistance" : 25 * mm});
        }
        {
            var Q0;
            Q0=makeQuery(id+"F1.opExtrude","CAP_FACE",FACE,{"disambiguationData":[OSD([sQuery(id+"F0.wireOp",EDGE,"E0"),sQuery(id+"F0.wireOp",EDGE,"E1"),sQuery(id+"F0.wireOp",EDGE,"E2"),sQuery(id+"F0.wireOp",EDGE,"E3"),sQuery(id+"F0.wireOp",EDGE,"E4"),sQuery(id+"F0.wireOp",EDGE,"E5"),sQuery(id+"F0.wireOp",EDGE,"E6"),sQuery(id+"F0.wireOp",EDGE,"E7"),sQuery(id+"F0.wireOp",EDGE,"E8"),sQuery(id+"F0.wireOp",EDGE,"E9"),sQuery(id+"F0.wireOp",EDGE,"E10"),sQuery(id+"F0.wireOp",EDGE,"E11"),sQuery(id+"F0.wireOp",EDGE,"E12"),sQuery(id+"F0.wireOp",EDGE,"E13"),sQuery(id+"F0.wireOp",EDGE,"E14"),sQuery(id+"F0.wireOp",EDGE,"E15"),sQuery(id+"F0.wireOp",EDGE,"E16"),sQuery(id+"F0.wireOp",EDGE,"E17"),sQuery(id+"F0.wireOp",EDGE,"E18"),sQuery(id+"F0.wireOp",EDGE,"E19"),sQuery(id+"F0.wireOp",EDGE,"E20"),sQuery(id+"F0.wireOp",EDGE,"E21"),sQuery(id+"F0.wireOp",EDGE,"E22"),sQuery(id+"F0.wireOp",EDGE,"E23"),sQuery(id+"F0.wireOp",EDGE,"E24"),sQuery(id+"F0.wireOp",EDGE,"E25"),sQuery(id+"F0.wireOp",EDGE,"E26"),sQuery(id+"F0.wireOp",EDGE,"E27"),sQuery(id+"F0.wireOp",EDGE,"E28"),sQuery(id+"F0.wireOp",EDGE,"E29"),sQuery(id+"F0.wireOp",EDGE,"E30"),sQuery(id+"F0.wireOp",EDGE,"E31"),sQuery(id+"F0.wireOp",EDGE,"E32"),sQuery(id+"F0.wireOp",EDGE,"E33"),sQuery(id+"F0.wireOp",EDGE,"E34"),sQuery(id+"F0.wireOp",EDGE,"E35"),sQuery(id+"F0.wireOp",EDGE,"E36"),sQuery(id+"F0.wireOp",EDGE,"E37"),sQuery(id+"F0.wireOp",EDGE,"E38"),sQuery(id+"F0.wireOp",EDGE,"E39"),sQuery(id+"F0.wireOp",EDGE,"E40"),sQuery(id+"F0.wireOp",EDGE,"E41"),sQuery(id+"F0.wireOp",EDGE,"E42"),sQuery(id+"F0.wireOp",EDGE,"E43"),sQuery(id+"F0.wireOp",EDGE,"E44"),sQuery(id+"F0.wireOp",EDGE,"E45"),sQuery(id+"F0.wireOp",EDGE,"E46"),sQuery(id+"F0.wireOp",EDGE,"E47"),sQuery(id+"F0.wireOp",EDGE,"E48"),sQuery(id+"F0.wireOp",EDGE,"E49"),sQuery(id+"F0.wireOp",EDGE,"E50"),sQuery(id+"F0.wireOp",EDGE,"E51"),sQuery(id+"F0.wireOp",EDGE,"E52"),sQuery(id+"F0.wireOp",EDGE,"E53"),sQuery(id+"F0.wireOp",EDGE,"E54"),sQuery(id+"F0.wireOp",EDGE,"E55"),sQuery(id+"F0.wireOp",EDGE,"E56"),sQuery(id+"F0.wireOp",EDGE,"E57"),sQuery(id+"F0.wireOp",EDGE,"E58"),sQuery(id+"F0.wireOp",EDGE,"E59"),sQuery(id+"F0.wireOp",EDGE,"E60"),sQuery(id+"F0.wireOp",EDGE,"E61"),sQuery(id+"F0.wireOp",EDGE,"E62"),sQuery(id+"F0.wireOp",EDGE,"E63"),sQuery(id+"F0.wireOp",EDGE,"E64"),sQuery(id+"F0.wireOp",EDGE,"E65"),sQuery(id+"F0.wireOp",EDGE,"E66"),sQuery(id+"F0.wireOp",EDGE,"E67"),sQuery(id+"F0.wireOp",EDGE,"E68"),sQuery(id+"F0.wireOp",EDGE,"E69"),sQuery(id+"F0.wireOp",EDGE,"E70"),sQuery(id+"F0.wireOp",EDGE,"E71"),sQuery(id+"F0.wireOp",EDGE,"E72"),sQuery(id+"F0.wireOp",EDGE,"E73"),sQuery(id+"F0.wireOp",EDGE,"E74"),sQuery(id+"F0.wireOp",EDGE,"E75"),sQuery(id+"F0.wireOp",EDGE,"E76"),sQuery(id+"F0.wireOp",EDGE,"E77"),sQuery(id+"F0.wireOp",EDGE,"E78"),sQuery(id+"F0.wireOp",EDGE,"E79"),sQuery(id+"F0.wireOp",EDGE,"E80"),sQuery(id+"F0.wireOp",EDGE,"E81"),sQuery(id+"F0.wireOp",EDGE,"E82"),sQuery(id+"F0.wireOp",EDGE,"E83"),sQuery(id+"F0.wireOp",EDGE,"E84"),sQuery(id+"F0.wireOp",EDGE,"E85"),sQuery(id+"F0.wireOp",EDGE,"E86"),sQuery(id+"F0.wireOp",EDGE,"E87"),sQuery(id+"F0.wireOp",EDGE,"E88"),sQuery(id+"F0.wireOp",EDGE,"E89"),sQuery(id+"F0.wireOp",EDGE,"E90"),sQuery(id+"F0.wireOp",EDGE,"E91"),sQuery(id+"F0.wireOp",EDGE,"E92"),sQuery(id+"F0.wireOp",EDGE,"E93"),sQuery(id+"F0.wireOp",EDGE,"E94"),sQuery(id+"F0.wireOp",EDGE,"E95"),sQuery(id+"F0.wireOp",EDGE,"E96"),sQuery(id+"F0.wireOp",EDGE,"E97"),sQuery(id+"F0.wireOp",EDGE,"E98"),sQuery(id+"F0.wireOp",EDGE,"E99"),sQuery(id+"F0.wireOp",EDGE,"E100"),sQuery(id+"F0.wireOp",EDGE,"E101"),sQuery(id+"F0.wireOp",EDGE,"E102"),sQuery(id+"F0.wireOp",EDGE,"E103"),sQuery(id+"F0.wireOp",EDGE,"E104"),sQuery(id+"F0.wireOp",EDGE,"E105"),sQuery(id+"F0.wireOp",EDGE,"E106"),sQuery(id+"F0.wireOp",EDGE,"E107"),sQuery(id+"F0.wireOp",EDGE,"E108"),sQuery(id+"F0.wireOp",EDGE,"E109"),sQuery(id+"F0.wireOp",EDGE,"E110"),sQuery(id+"F0.wireOp",EDGE,"E111"),sQuery(id+"F0.wireOp",EDGE,"E112"),sQuery(id+"F0.wireOp",EDGE,"E113"),sQuery(id+"F0.wireOp",EDGE,"E114"),sQuery(id+"F0.wireOp",EDGE,"E115"),sQuery(id+"F0.wireOp",EDGE,"E116"),sQuery(id+"F0.wireOp",EDGE,"E117"),sQuery(id+"F0.wireOp",EDGE,"E118"),sQuery(id+"F0.wireOp",EDGE,"E119"),sQuery(id+"F0.wireOp",EDGE,"E120"),sQuery(id+"F0.wireOp",EDGE,"E121"),sQuery(id+"F0.wireOp",EDGE,"E122"),sQuery(id+"F0.wireOp",EDGE,"E123"),sQuery(id+"F0.wireOp",EDGE,"E124"),sQuery(id+"F0.wireOp",EDGE,"E125"),sQuery(id+"F0.wireOp",EDGE,"E126"),sQuery(id+"F0.wireOp",EDGE,"E127"),sQuery(id+"F0.wireOp",EDGE,"E128"),sQuery(id+"F0.wireOp",EDGE,"E129"),sQuery(id+"F0.wireOp",EDGE,"E130"),sQuery(id+"F0.wireOp",EDGE,"E131"),sQuery(id+"F0.wireOp",EDGE,"E132"),sQuery(id+"F0.wireOp",EDGE,"E133"),sQuery(id+"F0.wireOp",EDGE,"E134"),sQuery(id+"F0.wireOp",EDGE,"E135"),sQuery(id+"F0.wireOp",EDGE,"E136"),sQuery(id+"F0.wireOp",EDGE,"E137"),sQuery(id+"F0.wireOp",EDGE,"E138"),sQuery(id+"F0.wireOp",EDGE,"E139"),sQuery(id+"F0.wireOp",EDGE,"E140"),sQuery(id+"F0.wireOp",EDGE,"E141"),sQuery(id+"F0.wireOp",EDGE,"E142"),sQuery(id+"F0.wireOp",EDGE,"E143"),sQuery(id+"F0.wireOp",EDGE,"E144"),sQuery(id+"F0.wireOp",EDGE,"E145"),sQuery(id+"F0.wireOp",EDGE,"E146"),sQuery(id+"F0.wireOp",EDGE,"E147"),sQuery(id+"F0.wireOp",EDGE,"E148"),sQuery(id+"F0.wireOp",EDGE,"E149"),sQuery(id+"F0.wireOp",EDGE,"E150"),sQuery(id+"F0.wireOp",EDGE,"E151"),sQuery(id+"F0.wireOp",EDGE,"E152"),sQuery(id+"F0.wireOp",EDGE,"E153"),sQuery(id+"F0.wireOp",EDGE,"E154"),sQuery(id+"F0.wireOp",EDGE,"E155"),sQuery(id+"F0.wireOp",EDGE,"E156"),sQuery(id+"F0.wireOp",EDGE,"E157"),sQuery(id+"F0.wireOp",EDGE,"E158"),sQuery(id+"F0.wireOp",EDGE,"E159"),sQuery(id+"F0.wireOp",EDGE,"E160"),sQuery(id+"F0.wireOp",EDGE,"E161"),sQuery(id+"F0.wireOp",EDGE,"E162"),sQuery(id+"F0.wireOp",EDGE,"E163"),sQuery(id+"F0.wireOp",EDGE,"E164"),sQuery(id+"F0.wireOp",EDGE,"E165"),sQuery(id+"F0.wireOp",EDGE,"E166"),sQuery(id+"F0.wireOp",EDGE,"E167"),sQuery(id+"F0.wireOp",EDGE,"E168"),sQuery(id+"F0.wireOp",EDGE,"E169"),sQuery(id+"F0.wireOp",EDGE,"E170"),sQuery(id+"F0.wireOp",EDGE,"E171"),sQuery(id+"F0.wireOp",EDGE,"E172"),sQuery(id+"F0.wireOp",EDGE,"E173"),sQuery(id+"F0.wireOp",EDGE,"E174"),sQuery(id+"F0.wireOp",EDGE,"E175"),sQuery(id+"F0.wireOp",EDGE,"E176"),sQuery(id+"F0.wireOp",EDGE,"E177"),sQuery(id+"F0.wireOp",EDGE,"E178"),sQuery(id+"F0.wireOp",EDGE,"E179"),sQuery(id+"F0.wireOp",EDGE,"E180"),sQuery(id+"F0.wireOp",EDGE,"E181"),sQuery(id+"F0.wireOp",EDGE,"E182"),sQuery(id+"F0.wireOp",EDGE,"E183"),sQuery(id+"F0.wireOp",EDGE,"E184"),sQuery(id+"F0.wireOp",EDGE,"E185"),sQuery(id+"F0.wireOp",EDGE,"E186"),sQuery(id+"F0.wireOp",EDGE,"E187"),sQuery(id+"F0.wireOp",EDGE,"E188"),sQuery(id+"F0.wireOp",EDGE,"E189"),sQuery(id+"F0.wireOp",EDGE,"E190"),sQuery(id+"F0.wireOp",EDGE,"E191"),sQuery(id+"F0.wireOp",EDGE,"E192"),sQuery(id+"F0.wireOp",EDGE,"E193"),sQuery(id+"F0.wireOp",EDGE,"E194"),sQuery(id+"F0.wireOp",EDGE,"E195"),sQuery(id+"F0.wireOp",EDGE,"E196"),sQuery(id+"F0.wireOp",EDGE,"E197"),sQuery(id+"F0.wireOp",EDGE,"E198"),sQuery(id+"F0.wireOp",EDGE,"E199"),sQuery(id+"F0.wireOp",EDGE,"E200"),sQuery(id+"F0.wireOp",EDGE,"E201"),sQuery(id+"F0.wireOp",EDGE,"E202"),sQuery(id+"F0.wireOp",EDGE,"E203"),sQuery(id+"F0.wireOp",EDGE,"E204"),sQuery(id+"F0.wireOp",EDGE,"E205"),sQuery(id+"F0.wireOp",EDGE,"E206"),sQuery(id+"F0.wireOp",EDGE,"E207"),sQuery(id+"F0.wireOp",EDGE,"E208"),sQuery(id+"F0.wireOp",EDGE,"E209"),sQuery(id+"F0.wireOp",EDGE,"E210"),sQuery(id+"F0.wireOp",EDGE,"E211"),sQuery(id+"F0.wireOp",EDGE,"E212"),sQuery(id+"F0.wireOp",EDGE,"E213"),sQuery(id+"F0.wireOp",EDGE,"E214"),sQuery(id+"F0.wireOp",EDGE,"E215"),sQuery(id+"F0.wireOp",EDGE,"E216"),sQuery(id+"F0.wireOp",EDGE,"E217"),sQuery(id+"F0.wireOp",EDGE,"E218"),sQuery(id+"F0.wireOp",EDGE,"E219"),sQuery(id+"F0.wireOp",EDGE,"E220"),sQuery(id+"F0.wireOp",EDGE,"E221"),sQuery(id+"F0.wireOp",EDGE,"E222"),sQuery(id+"F0.wireOp",EDGE,"E223"),sQuery(id+"F0.wireOp",EDGE,"E224"),sQuery(id+"F0.wireOp",EDGE,"E225"),sQuery(id+"F0.wireOp",EDGE,"E226"),sQuery(id+"F0.wireOp",EDGE,"E227"),sQuery(id+"F0.wireOp",EDGE,"E228"),sQuery(id+"F0.wireOp",EDGE,"E229"),sQuery(id+"F0.wireOp",EDGE,"E230"),sQuery(id+"F0.wireOp",EDGE,"E231"),sQuery(id+"F0.wireOp",EDGE,"E232"),sQuery(id+"F0.wireOp",EDGE,"E233"),sQuery(id+"F0.wireOp",EDGE,"E234"),sQuery(id+"F0.wireOp",EDGE,"E235"),sQuery(id+"F0.wireOp",EDGE,"E236"),sQuery(id+"F0.wireOp",EDGE,"E237"),sQuery(id+"F0.wireOp",EDGE,"E238"),sQuery(id+"F0.wireOp",EDGE,"E239"),sQuery(id+"F0.wireOp",EDGE,"E240"),sQuery(id+"F0.wireOp",EDGE,"E241"),sQuery(id+"F0.wireOp",EDGE,"E242"),sQuery(id+"F0.wireOp",EDGE,"E243"),sQuery(id+"F0.wireOp",EDGE,"E244"),sQuery(id+"F0.wireOp",EDGE,"E245"),sQuery(id+"F0.wireOp",EDGE,"E246"),sQuery(id+"F0.wireOp",EDGE,"E247"),sQuery(id+"F0.wireOp",EDGE,"E248"),sQuery(id+"F0.wireOp",EDGE,"E249"),sQuery(id+"F0.wireOp",EDGE,"E250"),sQuery(id+"F0.wireOp",EDGE,"E251"),sQuery(id+"F0.wireOp",EDGE,"E252"),sQuery(id+"F0.wireOp",EDGE,"E253"),sQuery(id+"F0.wireOp",EDGE,"E254"),sQuery(id+"F0.wireOp",EDGE,"E255"),sQuery(id+"F0.wireOp",EDGE,"E256"),sQuery(id+"F0.wireOp",EDGE,"E257"),sQuery(id+"F0.wireOp",EDGE,"E258"),sQuery(id+"F0.wireOp",EDGE,"E259"),sQuery(id+"F0.wireOp",EDGE,"E260"),sQuery(id+"F0.wireOp",EDGE,"E261"),sQuery(id+"F0.wireOp",EDGE,"E262"),sQuery(id+"F0.wireOp",EDGE,"E263"),sQuery(id+"F0.wireOp",EDGE,"E264"),sQuery(id+"F0.wireOp",EDGE,"E265"),sQuery(id+"F0.wireOp",EDGE,"E266"),sQuery(id+"F0.wireOp",EDGE,"E267"),sQuery(id+"F0.wireOp",EDGE,"E268"),sQuery(id+"F0.wireOp",EDGE,"E269"),sQuery(id+"F0.wireOp",EDGE,"E270"),sQuery(id+"F0.wireOp",EDGE,"E271"),sQuery(id+"F0.wireOp",EDGE,"E272"),sQuery(id+"F0.wireOp",EDGE,"E273"),sQuery(id+"F0.wireOp",EDGE,"E274"),sQuery(id+"F0.wireOp",EDGE,"E275"),sQuery(id+"F0.wireOp",EDGE,"E276"),sQuery(id+"F0.wireOp",EDGE,"E277"),sQuery(id+"F0.wireOp",EDGE,"E278"),sQuery(id+"F0.wireOp",EDGE,"E279"),sQuery(id+"F0.wireOp",EDGE,"E280"),sQuery(id+"F0.wireOp",EDGE,"E281"),sQuery(id+"F0.wireOp",EDGE,"E282"),sQuery(id+"F0.wireOp",EDGE,"E283"),sQuery(id+"F0.wireOp",EDGE,"E284"),sQuery(id+"F0.wireOp",EDGE,"E285"),sQuery(id+"F0.wireOp",EDGE,"E286"),sQuery(id+"F0.wireOp",EDGE,"E287"),sQuery(id+"F0.wireOp",EDGE,"E288"),sQuery(id+"F0.wireOp",EDGE,"E289"),sQuery(id+"F0.wireOp",EDGE,"E290"),sQuery(id+"F0.wireOp",EDGE,"E291"),sQuery(id+"F0.wireOp",EDGE,"E292"),sQuery(id+"F0.wireOp",EDGE,"E293"),sQuery(id+"F0.wireOp",EDGE,"E294"),sQuery(id+"F0.wireOp",EDGE,"E295"),sQuery(id+"F0.wireOp",EDGE,"E296"),sQuery(id+"F0.wireOp",EDGE,"E297"),sQuery(id+"F0.wireOp",EDGE,"E298"),sQuery(id+"F0.wireOp",EDGE,"E299"),sQuery(id+"F0.wireOp",EDGE,"E300"),sQuery(id+"F0.wireOp",EDGE,"E301"),sQuery(id+"F0.wireOp",EDGE,"E302"),sQuery(id+"F0.wireOp",EDGE,"E303"),sQuery(id+"F0.wireOp",EDGE,"E304"),sQuery(id+"F0.wireOp",EDGE,"E305"),sQuery(id+"F0.wireOp",EDGE,"E306"),sQuery(id+"F0.wireOp",EDGE,"E307"),sQuery(id+"F0.wireOp",EDGE,"E308"),sQuery(id+"F0.wireOp",EDGE,"E309"),sQuery(id+"F0.wireOp",EDGE,"E310"),sQuery(id+"F0.wireOp",EDGE,"E311"),sQuery(id+"F0.wireOp",EDGE,"E312"),sQuery(id+"F0.wireOp",EDGE,"E313"),sQuery(id+"F0.wireOp",EDGE,"E314"),sQuery(id+"F0.wireOp",EDGE,"E315"),sQuery(id+"F0.wireOp",EDGE,"E316"),sQuery(id+"F0.wireOp",EDGE,"E317"),sQuery(id+"F0.wireOp",EDGE,"E318"),sQuery(id+"F0.wireOp",EDGE,"E319"),sQuery(id+"F0.wireOp",EDGE,"E320"),sQuery(id+"F0.wireOp",EDGE,"E321"),sQuery(id+"F0.wireOp",EDGE,"E322"),sQuery(id+"F0.wireOp",EDGE,"E323"),sQuery(id+"F0.wireOp",EDGE,"E324"),sQuery(id+"F0.wireOp",EDGE,"E325"),sQuery(id+"F0.wireOp",EDGE,"E326"),sQuery(id+"F0.wireOp",EDGE,"E327"),sQuery(id+"F0.wireOp",EDGE,"E328"),sQuery(id+"F0.wireOp",EDGE,"E329"),sQuery(id+"F0.wireOp",EDGE,"E330"),sQuery(id+"F0.wireOp",EDGE,"E331"),sQuery(id+"F0.wireOp",EDGE,"E332"),sQuery(id+"F0.wireOp",EDGE,"E333"),sQuery(id+"F0.wireOp",EDGE,"E334"),sQuery(id+"F0.wireOp",EDGE,"E335"),sQuery(id+"F0.wireOp",EDGE,"E336"),sQuery(id+"F0.wireOp",EDGE,"E337"),sQuery(id+"F0.wireOp",EDGE,"E338"),sQuery(id+"F0.wireOp",EDGE,"E339"),sQuery(id+"F0.wireOp",EDGE,"E340"),sQuery(id+"F0.wireOp",EDGE,"E341"),sQuery(id+"F0.wireOp",EDGE,"E342"),sQuery(id+"F0.wireOp",EDGE,"E343"),sQuery(id+"F0.wireOp",EDGE,"E344"),sQuery(id+"F0.wireOp",EDGE,"E345"),sQuery(id+"F0.wireOp",EDGE,"E346"),sQuery(id+"F0.wireOp",EDGE,"E347"),sQuery(id+"F0.wireOp",EDGE,"E348"),sQuery(id+"F0.wireOp",EDGE,"E349"),sQuery(id+"F0.wireOp",EDGE,"E350"),sQuery(id+"F0.wireOp",EDGE,"E351"),sQuery(id+"F0.wireOp",EDGE,"E352"),sQuery(id+"F0.wireOp",EDGE,"E353"),sQuery(id+"F0.wireOp",EDGE,"E354"),sQuery(id+"F0.wireOp",EDGE,"E355"),sQuery(id+"F0.wireOp",EDGE,"E356"),sQuery(id+"F0.wireOp",EDGE,"E357"),sQuery(id+"F0.wireOp",EDGE,"E358"),sQuery(id+"F0.wireOp",EDGE,"E359"),sQuery(id+"F0.wireOp",EDGE,"E360"),sQuery(id+"F0.wireOp",EDGE,"E361"),sQuery(id+"F0.wireOp",EDGE,"E362"),sQuery(id+"F0.wireOp",EDGE,"E363"),sQuery(id+"F0.wireOp",EDGE,"E364"),sQuery(id+"F0.wireOp",EDGE,"E365"),sQuery(id+"F0.wireOp",EDGE,"E366"),sQuery(id+"F0.wireOp",EDGE,"E367"),sQuery(id+"F0.wireOp",EDGE,"E368"),sQuery(id+"F0.wireOp",EDGE,"E369"),sQuery(id+"F0.wireOp",EDGE,"E370"),sQuery(id+"F0.wireOp",EDGE,"E371"),sQuery(id+"F0.wireOp",EDGE,"E372"),sQuery(id+"F0.wireOp",EDGE,"E373"),sQuery(id+"F0.wireOp",EDGE,"E374"),sQuery(id+"F0.wireOp",EDGE,"E375"),sQuery(id+"F0.wireOp",EDGE,"E376"),sQuery(id+"F0.wireOp",EDGE,"E377"),sQuery(id+"F0.wireOp",EDGE,"E378"),sQuery(id+"F0.wireOp",EDGE,"E379"),sQuery(id+"F0.wireOp",EDGE,"E380"),sQuery(id+"F0.wireOp",EDGE,"E381"),sQuery(id+"F0.wireOp",EDGE,"E382"),sQuery(id+"F0.wireOp",EDGE,"E383"),sQuery(id+"F0.wireOp",EDGE,"E384"),sQuery(id+"F0.wireOp",EDGE,"E385"),sQuery(id+"F0.wireOp",EDGE,"E386"),sQuery(id+"F0.wireOp",EDGE,"E387"),sQuery(id+"F0.wireOp",EDGE,"E388"),sQuery(id+"F0.wireOp",EDGE,"E389"),sQuery(id+"F0.wireOp",EDGE,"E390"),sQuery(id+"F0.wireOp",EDGE,"E391"),sQuery(id+"F0.wireOp",EDGE,"E392"),sQuery(id+"F0.wireOp",EDGE,"E393"),sQuery(id+"F0.wireOp",EDGE,"E394"),sQuery(id+"F0.wireOp",EDGE,"E395"),sQuery(id+"F0.wireOp",EDGE,"E396"),sQuery(id+"F0.wireOp",EDGE,"E397"),sQuery(id+"F0.wireOp",EDGE,"E398"),sQuery(id+"F0.wireOp",EDGE,"E399"),sQuery(id+"F0.wireOp",EDGE,"E400"),sQuery(id+"F0.wireOp",EDGE,"E401"),sQuery(id+"F0.wireOp",EDGE,"E402"),sQuery(id+"F0.wireOp",EDGE,"E403"),sQuery(id+"F0.wireOp",EDGE,"E404"),sQuery(id+"F0.wireOp",EDGE,"E405"),sQuery(id+"F0.wireOp",EDGE,"E406"),sQuery(id+"F0.wireOp",EDGE,"E407"),sQuery(id+"F0.wireOp",EDGE,"E408"),sQuery(id+"F0.wireOp",EDGE,"E409"),sQuery(id+"F0.wireOp",EDGE,"E410"),sQuery(id+"F0.wireOp",EDGE,"E411"),sQuery(id+"F0.wireOp",EDGE,"E412"),sQuery(id+"F0.wireOp",EDGE,"E413"),sQuery(id+"F0.wireOp",EDGE,"E414"),sQuery(id+"F0.wireOp",EDGE,"E415"),sQuery(id+"F0.wireOp",EDGE,"E416"),sQuery(id+"F0.wireOp",EDGE,"E417"),sQuery(id+"F0.wireOp",EDGE,"E418"),sQuery(id+"F0.wireOp",EDGE,"E419"),sQuery(id+"F0.wireOp",EDGE,"E420"),sQuery(id+"F0.wireOp",EDGE,"E421"),sQuery(id+"F0.wireOp",EDGE,"E422"),sQuery(id+"F0.wireOp",EDGE,"E423"),sQuery(id+"F0.wireOp",EDGE,"E424"),sQuery(id+"F0.wireOp",EDGE,"E425"),sQuery(id+"F0.wireOp",EDGE,"E426"),sQuery(id+"F0.wireOp",EDGE,"E427"),sQuery(id+"F0.wireOp",EDGE,"E428"),sQuery(id+"F0.wireOp",EDGE,"E429"),sQuery(id+"F0.wireOp",EDGE,"E430"),sQuery(id+"F0.wireOp",EDGE,"E431"),sQuery(id+"F0.wireOp",EDGE,"E432"),sQuery(id+"F0.wireOp",EDGE,"E433"),sQuery(id+"F0.wireOp",EDGE,"E434"),sQuery(id+"F0.wireOp",EDGE,"E435"),sQuery(id+"F0.wireOp",EDGE,"E436"),sQuery(id+"F0.wireOp",EDGE,"E437"),sQuery(id+"F0.wireOp",EDGE,"E438"),sQuery(id+"F0.wireOp",EDGE,"E439"),sQuery(id+"F0.wireOp",EDGE,"E440"),sQuery(id+"F0.wireOp",EDGE,"E441"),sQuery(id+"F0.wireOp",EDGE,"E442"),sQuery(id+"F0.wireOp",EDGE,"E443"),sQuery(id+"F0.wireOp",EDGE,"E444"),sQuery(id+"F0.wireOp",EDGE,"E445"),sQuery(id+"F0.wireOp",EDGE,"E446"),sQuery(id+"F0.wireOp",EDGE,"E447"),sQuery(id+"F0.wireOp",EDGE,"E448"),sQuery(id+"F0.wireOp",EDGE,"E449"),sQuery(id+"F0.wireOp",EDGE,"E450"),sQuery(id+"F0.wireOp",EDGE,"E451"),sQuery(id+"F0.wireOp",EDGE,"E452"),sQuery(id+"F0.wireOp",EDGE,"E453"),sQuery(id+"F0.wireOp",EDGE,"E454"),sQuery(id+"F0.wireOp",EDGE,"E455"),sQuery(id+"F0.wireOp",EDGE,"E456"),sQuery(id+"F0.wireOp",EDGE,"E457"),sQuery(id+"F0.wireOp",EDGE,"E458"),sQuery(id+"F0.wireOp",EDGE,"E459"),sQuery(id+"F0.wireOp",EDGE,"E460"),sQuery(id+"F0.wireOp",EDGE,"E461"),sQuery(id+"F0.wireOp",EDGE,"E462"),sQuery(id+"F0.wireOp",EDGE,"E463"),sQuery(id+"F0.wireOp",EDGE,"E464"),sQuery(id+"F0.wireOp",EDGE,"E465"),sQuery(id+"F0.wireOp",EDGE,"E466"),sQuery(id+"F0.wireOp",EDGE,"E467"),sQuery(id+"F0.wireOp",EDGE,"E468"),sQuery(id+"F0.wireOp",EDGE,"E469"),sQuery(id+"F0.wireOp",EDGE,"E470"),sQuery(id+"F0.wireOp",EDGE,"E471"),sQuery(id+"F0.wireOp",EDGE,"E472"),sQuery(id+"F0.wireOp",EDGE,"E473"),sQuery(id+"F0.wireOp",EDGE,"E474"),sQuery(id+"F0.wireOp",EDGE,"E475"),sQuery(id+"F0.wireOp",EDGE,"E476"),sQuery(id+"F0.wireOp",EDGE,"E477"),sQuery(id+"F0.wireOp",EDGE,"E478"),sQuery(id+"F0.wireOp",EDGE,"E479"),sQuery(id+"F0.wireOp",EDGE,"E480"),sQuery(id+"F0.wireOp",EDGE,"E481"),sQuery(id+"F0.wireOp",EDGE,"E482"),sQuery(id+"F0.wireOp",EDGE,"E483"),sQuery(id+"F0.wireOp",EDGE,"E484"),sQuery(id+"F0.wireOp",EDGE,"E485"),sQuery(id+"F0.wireOp",EDGE,"E486"),sQuery(id+"F0.wireOp",EDGE,"E487"),sQuery(id+"F0.wireOp",EDGE,"E488"),sQuery(id+"F0.wireOp",EDGE,"E489"),sQuery(id+"F0.wireOp",EDGE,"E490"),sQuery(id+"F0.wireOp",EDGE,"E491"),sQuery(id+"F0.wireOp",EDGE,"E492"),sQuery(id+"F0.wireOp",EDGE,"E493"),sQuery(id+"F0.wireOp",EDGE,"E494"),sQuery(id+"F0.wireOp",EDGE,"E495"),sQuery(id+"F0.wireOp",EDGE,"E496"),sQuery(id+"F0.wireOp",EDGE,"E497"),sQuery(id+"F0.wireOp",EDGE,"E498"),sQuery(id+"F0.wireOp",EDGE,"E499"),sQuery(id+"F0.wireOp",EDGE,"E500"),sQuery(id+"F0.wireOp",EDGE,"E501"),sQuery(id+"F0.wireOp",EDGE,"E502"),sQuery(id+"F0.wireOp",EDGE,"E503"),sQuery(id+"F0.wireOp",EDGE,"E504"),sQuery(id+"F0.wireOp",EDGE,"E505"),sQuery(id+"F0.wireOp",EDGE,"E506"),sQuery(id+"F0.wireOp",EDGE,"E507"),sQuery(id+"F0.wireOp",EDGE,"E508"),sQuery(id+"F0.wireOp",EDGE,"E509"),sQuery(id+"F0.wireOp",EDGE,"E510"),sQuery(id+"F0.wireOp",EDGE,"E511"),sQuery(id+"F0.wireOp",EDGE,"E512"),sQuery(id+"F0.wireOp",EDGE,"E513"),sQuery(id+"F0.wireOp",EDGE,"E514"),sQuery(id+"F0.wireOp",EDGE,"E515"),sQuery(id+"F0.wireOp",EDGE,"E516"),sQuery(id+"F0.wireOp",EDGE,"E517"),sQuery(id+"F0.wireOp",EDGE,"E518"),sQuery(id+"F0.wireOp",EDGE,"E519"),sQuery(id+"F0.wireOp",EDGE,"E520"),sQuery(id+"F0.wireOp",EDGE,"E521"),sQuery(id+"F0.wireOp",EDGE,"E522"),sQuery(id+"F0.wireOp",EDGE,"E523"),sQuery(id+"F0.wireOp",EDGE,"E524"),sQuery(id+"F0.wireOp",EDGE,"E525"),sQuery(id+"F0.wireOp",EDGE,"E526"),sQuery(id+"F0.wireOp",EDGE,"E527"),sQuery(id+"F0.wireOp",EDGE,"E528"),sQuery(id+"F0.wireOp",EDGE,"E529"),sQuery(id+"F0.wireOp",EDGE,"E530"),sQuery(id+"F0.wireOp",EDGE,"E531"),sQuery(id+"F0.wireOp",EDGE,"E532"),sQuery(id+"F0.wireOp",EDGE,"E533"),sQuery(id+"F0.wireOp",EDGE,"E534"),sQuery(id+"F0.wireOp",EDGE,"E535"),sQuery(id+"F0.wireOp",EDGE,"E536"),sQuery(id+"F0.wireOp",EDGE,"E537"),sQuery(id+"F0.wireOp",EDGE,"E538"),sQuery(id+"F0.wireOp",EDGE,"E539"),sQuery(id+"F0.wireOp",EDGE,"E540"),sQuery(id+"F0.wireOp",EDGE,"E541"),sQuery(id+"F0.wireOp",EDGE,"E542"),sQuery(id+"F0.wireOp",EDGE,"E543"),sQuery(id+"F0.wireOp",EDGE,"E544"),sQuery(id+"F0.wireOp",EDGE,"E545"),sQuery(id+"F0.wireOp",EDGE,"E546"),sQuery(id+"F0.wireOp",EDGE,"E547"),sQuery(id+"F0.wireOp",EDGE,"E548"),sQuery(id+"F0.wireOp",EDGE,"E549"),sQuery(id+"F0.wireOp",EDGE,"E550"),sQuery(id+"F0.wireOp",EDGE,"E551"),sQuery(id+"F0.wireOp",EDGE,"E552"),sQuery(id+"F0.wireOp",EDGE,"E553"),sQuery(id+"F0.wireOp",EDGE,"E554"),sQuery(id+"F0.wireOp",EDGE,"E555"),sQuery(id+"F0.wireOp",EDGE,"E556"),sQuery(id+"F0.wireOp",EDGE,"E557"),sQuery(id+"F0.wireOp",EDGE,"E558"),sQuery(id+"F0.wireOp",EDGE,"E559"),sQuery(id+"F0.wireOp",EDGE,"E560"),sQuery(id+"F0.wireOp",EDGE,"E561"),sQuery(id+"F0.wireOp",EDGE,"E562"),sQuery(id+"F0.wireOp",EDGE,"E563"),sQuery(id+"F0.wireOp",EDGE,"E564"),sQuery(id+"F0.wireOp",EDGE,"E565"),sQuery(id+"F0.wireOp",EDGE,"E566"),sQuery(id+"F0.wireOp",EDGE,"E567"),sQuery(id+"F0.wireOp",EDGE,"E568"),sQuery(id+"F0.wireOp",EDGE,"E569"),sQuery(id+"F0.wireOp",EDGE,"E570"),sQuery(id+"F0.wireOp",EDGE,"E571"),sQuery(id+"F0.wireOp",EDGE,"E572"),sQuery(id+"F0.wireOp",EDGE,"E573"),sQuery(id+"F0.wireOp",EDGE,"E574"),sQuery(id+"F0.wireOp",EDGE,"E575"),sQuery(id+"F0.wireOp",EDGE,"E576"),sQuery(id+"F0.wireOp",EDGE,"E577"),sQuery(id+"F0.wireOp",EDGE,"E1140"),sQuery(id+"F0.wireOp",EDGE,"E1143")])],"isStart":false});
            var sketch = newSketch(context, id + "F4", { "sketchPlane" : qUnion([Q0])});
            skLineSegment(sketch, "E2027", {"start": v(-38.1, 0.27) * mm, "end": v(25.4, 0.1) * mm, "construction": true});
            skCircle(sketch, "E2028", {"center": v(-18.1, 0.21) * mm, "radius": 3 * mm});
            skLineSegment(sketch, "E2029.bottom", {"start": v(62, 23.22) * mm, "end": v(147, 23.22) * mm});
            skLineSegment(sketch, "E2029.top", {"start": v(62, -26.78) * mm, "end": v(147, -26.78) * mm});
            skLineSegment(sketch, "E2029.left", {"start": v(62, 23.22) * mm, "end": v(62, -26.78) * mm});
            skLineSegment(sketch, "E2029.right", {"start": v(147, 23.22) * mm, "end": v(147, -26.78) * mm});
            skSolve(sketch);
        }
        {
            var Q0;
            Q0 = qSketchRegion(id + "F4", true);
            extrude(context, id + "F5", {"entities" : qUnion([Q0]), "operationType" : NewBodyOperationType.REMOVE, "endBound" : BoundingType.SYMMETRIC, "oppositeDirection" : true, "depth" : 25 * mm, "offsetDistance" : 25 * mm});
        }
        {
            var Q0;
            Q0=makeQuery(id+"F1.opExtrude","CAP_FACE",FACE,{"disambiguationData":[OSD([sQuery(id+"F0.wireOp",EDGE,"E0"),sQuery(id+"F0.wireOp",EDGE,"E1"),sQuery(id+"F0.wireOp",EDGE,"E2"),sQuery(id+"F0.wireOp",EDGE,"E3"),sQuery(id+"F0.wireOp",EDGE,"E4"),sQuery(id+"F0.wireOp",EDGE,"E5"),sQuery(id+"F0.wireOp",EDGE,"E6"),sQuery(id+"F0.wireOp",EDGE,"E7"),sQuery(id+"F0.wireOp",EDGE,"E8"),sQuery(id+"F0.wireOp",EDGE,"E9"),sQuery(id+"F0.wireOp",EDGE,"E10"),sQuery(id+"F0.wireOp",EDGE,"E11"),sQuery(id+"F0.wireOp",EDGE,"E12"),sQuery(id+"F0.wireOp",EDGE,"E13"),sQuery(id+"F0.wireOp",EDGE,"E14"),sQuery(id+"F0.wireOp",EDGE,"E15"),sQuery(id+"F0.wireOp",EDGE,"E16"),sQuery(id+"F0.wireOp",EDGE,"E17"),sQuery(id+"F0.wireOp",EDGE,"E18"),sQuery(id+"F0.wireOp",EDGE,"E19"),sQuery(id+"F0.wireOp",EDGE,"E20"),sQuery(id+"F0.wireOp",EDGE,"E21"),sQuery(id+"F0.wireOp",EDGE,"E22"),sQuery(id+"F0.wireOp",EDGE,"E23"),sQuery(id+"F0.wireOp",EDGE,"E24"),sQuery(id+"F0.wireOp",EDGE,"E25"),sQuery(id+"F0.wireOp",EDGE,"E26"),sQuery(id+"F0.wireOp",EDGE,"E27"),sQuery(id+"F0.wireOp",EDGE,"E28"),sQuery(id+"F0.wireOp",EDGE,"E29"),sQuery(id+"F0.wireOp",EDGE,"E30"),sQuery(id+"F0.wireOp",EDGE,"E31"),sQuery(id+"F0.wireOp",EDGE,"E32"),sQuery(id+"F0.wireOp",EDGE,"E33"),sQuery(id+"F0.wireOp",EDGE,"E34"),sQuery(id+"F0.wireOp",EDGE,"E35"),sQuery(id+"F0.wireOp",EDGE,"E36"),sQuery(id+"F0.wireOp",EDGE,"E37"),sQuery(id+"F0.wireOp",EDGE,"E38"),sQuery(id+"F0.wireOp",EDGE,"E39"),sQuery(id+"F0.wireOp",EDGE,"E40"),sQuery(id+"F0.wireOp",EDGE,"E41"),sQuery(id+"F0.wireOp",EDGE,"E42"),sQuery(id+"F0.wireOp",EDGE,"E43"),sQuery(id+"F0.wireOp",EDGE,"E44"),sQuery(id+"F0.wireOp",EDGE,"E45"),sQuery(id+"F0.wireOp",EDGE,"E46"),sQuery(id+"F0.wireOp",EDGE,"E47"),sQuery(id+"F0.wireOp",EDGE,"E48"),sQuery(id+"F0.wireOp",EDGE,"E49"),sQuery(id+"F0.wireOp",EDGE,"E50"),sQuery(id+"F0.wireOp",EDGE,"E51"),sQuery(id+"F0.wireOp",EDGE,"E52"),sQuery(id+"F0.wireOp",EDGE,"E53"),sQuery(id+"F0.wireOp",EDGE,"E54"),sQuery(id+"F0.wireOp",EDGE,"E55"),sQuery(id+"F0.wireOp",EDGE,"E56"),sQuery(id+"F0.wireOp",EDGE,"E57"),sQuery(id+"F0.wireOp",EDGE,"E58"),sQuery(id+"F0.wireOp",EDGE,"E59"),sQuery(id+"F0.wireOp",EDGE,"E60"),sQuery(id+"F0.wireOp",EDGE,"E61"),sQuery(id+"F0.wireOp",EDGE,"E62"),sQuery(id+"F0.wireOp",EDGE,"E63"),sQuery(id+"F0.wireOp",EDGE,"E64"),sQuery(id+"F0.wireOp",EDGE,"E65"),sQuery(id+"F0.wireOp",EDGE,"E66"),sQuery(id+"F0.wireOp",EDGE,"E67"),sQuery(id+"F0.wireOp",EDGE,"E68"),sQuery(id+"F0.wireOp",EDGE,"E69"),sQuery(id+"F0.wireOp",EDGE,"E70"),sQuery(id+"F0.wireOp",EDGE,"E71"),sQuery(id+"F0.wireOp",EDGE,"E72"),sQuery(id+"F0.wireOp",EDGE,"E73"),sQuery(id+"F0.wireOp",EDGE,"E74"),sQuery(id+"F0.wireOp",EDGE,"E75"),sQuery(id+"F0.wireOp",EDGE,"E76"),sQuery(id+"F0.wireOp",EDGE,"E77"),sQuery(id+"F0.wireOp",EDGE,"E78"),sQuery(id+"F0.wireOp",EDGE,"E79"),sQuery(id+"F0.wireOp",EDGE,"E80"),sQuery(id+"F0.wireOp",EDGE,"E81"),sQuery(id+"F0.wireOp",EDGE,"E82"),sQuery(id+"F0.wireOp",EDGE,"E83"),sQuery(id+"F0.wireOp",EDGE,"E84"),sQuery(id+"F0.wireOp",EDGE,"E85"),sQuery(id+"F0.wireOp",EDGE,"E86"),sQuery(id+"F0.wireOp",EDGE,"E87"),sQuery(id+"F0.wireOp",EDGE,"E88"),sQuery(id+"F0.wireOp",EDGE,"E89"),sQuery(id+"F0.wireOp",EDGE,"E90"),sQuery(id+"F0.wireOp",EDGE,"E91"),sQuery(id+"F0.wireOp",EDGE,"E92"),sQuery(id+"F0.wireOp",EDGE,"E93"),sQuery(id+"F0.wireOp",EDGE,"E94"),sQuery(id+"F0.wireOp",EDGE,"E95"),sQuery(id+"F0.wireOp",EDGE,"E96"),sQuery(id+"F0.wireOp",EDGE,"E97"),sQuery(id+"F0.wireOp",EDGE,"E98"),sQuery(id+"F0.wireOp",EDGE,"E99"),sQuery(id+"F0.wireOp",EDGE,"E100"),sQuery(id+"F0.wireOp",EDGE,"E101"),sQuery(id+"F0.wireOp",EDGE,"E102"),sQuery(id+"F0.wireOp",EDGE,"E103"),sQuery(id+"F0.wireOp",EDGE,"E104"),sQuery(id+"F0.wireOp",EDGE,"E105"),sQuery(id+"F0.wireOp",EDGE,"E106"),sQuery(id+"F0.wireOp",EDGE,"E107"),sQuery(id+"F0.wireOp",EDGE,"E108"),sQuery(id+"F0.wireOp",EDGE,"E109"),sQuery(id+"F0.wireOp",EDGE,"E110"),sQuery(id+"F0.wireOp",EDGE,"E111"),sQuery(id+"F0.wireOp",EDGE,"E112"),sQuery(id+"F0.wireOp",EDGE,"E113"),sQuery(id+"F0.wireOp",EDGE,"E114"),sQuery(id+"F0.wireOp",EDGE,"E115"),sQuery(id+"F0.wireOp",EDGE,"E116"),sQuery(id+"F0.wireOp",EDGE,"E117"),sQuery(id+"F0.wireOp",EDGE,"E118"),sQuery(id+"F0.wireOp",EDGE,"E119"),sQuery(id+"F0.wireOp",EDGE,"E120"),sQuery(id+"F0.wireOp",EDGE,"E121"),sQuery(id+"F0.wireOp",EDGE,"E122"),sQuery(id+"F0.wireOp",EDGE,"E123"),sQuery(id+"F0.wireOp",EDGE,"E124"),sQuery(id+"F0.wireOp",EDGE,"E125"),sQuery(id+"F0.wireOp",EDGE,"E126"),sQuery(id+"F0.wireOp",EDGE,"E127"),sQuery(id+"F0.wireOp",EDGE,"E128"),sQuery(id+"F0.wireOp",EDGE,"E129"),sQuery(id+"F0.wireOp",EDGE,"E130"),sQuery(id+"F0.wireOp",EDGE,"E131"),sQuery(id+"F0.wireOp",EDGE,"E132"),sQuery(id+"F0.wireOp",EDGE,"E133"),sQuery(id+"F0.wireOp",EDGE,"E134"),sQuery(id+"F0.wireOp",EDGE,"E135"),sQuery(id+"F0.wireOp",EDGE,"E136"),sQuery(id+"F0.wireOp",EDGE,"E137"),sQuery(id+"F0.wireOp",EDGE,"E138"),sQuery(id+"F0.wireOp",EDGE,"E139"),sQuery(id+"F0.wireOp",EDGE,"E140"),sQuery(id+"F0.wireOp",EDGE,"E141"),sQuery(id+"F0.wireOp",EDGE,"E142"),sQuery(id+"F0.wireOp",EDGE,"E143"),sQuery(id+"F0.wireOp",EDGE,"E144"),sQuery(id+"F0.wireOp",EDGE,"E145"),sQuery(id+"F0.wireOp",EDGE,"E146"),sQuery(id+"F0.wireOp",EDGE,"E147"),sQuery(id+"F0.wireOp",EDGE,"E148"),sQuery(id+"F0.wireOp",EDGE,"E149"),sQuery(id+"F0.wireOp",EDGE,"E150"),sQuery(id+"F0.wireOp",EDGE,"E151"),sQuery(id+"F0.wireOp",EDGE,"E152"),sQuery(id+"F0.wireOp",EDGE,"E153"),sQuery(id+"F0.wireOp",EDGE,"E154"),sQuery(id+"F0.wireOp",EDGE,"E155"),sQuery(id+"F0.wireOp",EDGE,"E156"),sQuery(id+"F0.wireOp",EDGE,"E157"),sQuery(id+"F0.wireOp",EDGE,"E158"),sQuery(id+"F0.wireOp",EDGE,"E159"),sQuery(id+"F0.wireOp",EDGE,"E160"),sQuery(id+"F0.wireOp",EDGE,"E161"),sQuery(id+"F0.wireOp",EDGE,"E162"),sQuery(id+"F0.wireOp",EDGE,"E163"),sQuery(id+"F0.wireOp",EDGE,"E164"),sQuery(id+"F0.wireOp",EDGE,"E165"),sQuery(id+"F0.wireOp",EDGE,"E166"),sQuery(id+"F0.wireOp",EDGE,"E167"),sQuery(id+"F0.wireOp",EDGE,"E168"),sQuery(id+"F0.wireOp",EDGE,"E169"),sQuery(id+"F0.wireOp",EDGE,"E170"),sQuery(id+"F0.wireOp",EDGE,"E171"),sQuery(id+"F0.wireOp",EDGE,"E172"),sQuery(id+"F0.wireOp",EDGE,"E173"),sQuery(id+"F0.wireOp",EDGE,"E174"),sQuery(id+"F0.wireOp",EDGE,"E175"),sQuery(id+"F0.wireOp",EDGE,"E176"),sQuery(id+"F0.wireOp",EDGE,"E177"),sQuery(id+"F0.wireOp",EDGE,"E178"),sQuery(id+"F0.wireOp",EDGE,"E179"),sQuery(id+"F0.wireOp",EDGE,"E180"),sQuery(id+"F0.wireOp",EDGE,"E181"),sQuery(id+"F0.wireOp",EDGE,"E182"),sQuery(id+"F0.wireOp",EDGE,"E183"),sQuery(id+"F0.wireOp",EDGE,"E184"),sQuery(id+"F0.wireOp",EDGE,"E185"),sQuery(id+"F0.wireOp",EDGE,"E186"),sQuery(id+"F0.wireOp",EDGE,"E187"),sQuery(id+"F0.wireOp",EDGE,"E188"),sQuery(id+"F0.wireOp",EDGE,"E189"),sQuery(id+"F0.wireOp",EDGE,"E190"),sQuery(id+"F0.wireOp",EDGE,"E191"),sQuery(id+"F0.wireOp",EDGE,"E192"),sQuery(id+"F0.wireOp",EDGE,"E193"),sQuery(id+"F0.wireOp",EDGE,"E194"),sQuery(id+"F0.wireOp",EDGE,"E195"),sQuery(id+"F0.wireOp",EDGE,"E196"),sQuery(id+"F0.wireOp",EDGE,"E197"),sQuery(id+"F0.wireOp",EDGE,"E198"),sQuery(id+"F0.wireOp",EDGE,"E199"),sQuery(id+"F0.wireOp",EDGE,"E200"),sQuery(id+"F0.wireOp",EDGE,"E201"),sQuery(id+"F0.wireOp",EDGE,"E202"),sQuery(id+"F0.wireOp",EDGE,"E203"),sQuery(id+"F0.wireOp",EDGE,"E204"),sQuery(id+"F0.wireOp",EDGE,"E205"),sQuery(id+"F0.wireOp",EDGE,"E206"),sQuery(id+"F0.wireOp",EDGE,"E207"),sQuery(id+"F0.wireOp",EDGE,"E208"),sQuery(id+"F0.wireOp",EDGE,"E209"),sQuery(id+"F0.wireOp",EDGE,"E210"),sQuery(id+"F0.wireOp",EDGE,"E211"),sQuery(id+"F0.wireOp",EDGE,"E212"),sQuery(id+"F0.wireOp",EDGE,"E213"),sQuery(id+"F0.wireOp",EDGE,"E214"),sQuery(id+"F0.wireOp",EDGE,"E215"),sQuery(id+"F0.wireOp",EDGE,"E216"),sQuery(id+"F0.wireOp",EDGE,"E217"),sQuery(id+"F0.wireOp",EDGE,"E218"),sQuery(id+"F0.wireOp",EDGE,"E219"),sQuery(id+"F0.wireOp",EDGE,"E220"),sQuery(id+"F0.wireOp",EDGE,"E221"),sQuery(id+"F0.wireOp",EDGE,"E222"),sQuery(id+"F0.wireOp",EDGE,"E223"),sQuery(id+"F0.wireOp",EDGE,"E224"),sQuery(id+"F0.wireOp",EDGE,"E225"),sQuery(id+"F0.wireOp",EDGE,"E226"),sQuery(id+"F0.wireOp",EDGE,"E227"),sQuery(id+"F0.wireOp",EDGE,"E228"),sQuery(id+"F0.wireOp",EDGE,"E229"),sQuery(id+"F0.wireOp",EDGE,"E230"),sQuery(id+"F0.wireOp",EDGE,"E231"),sQuery(id+"F0.wireOp",EDGE,"E232"),sQuery(id+"F0.wireOp",EDGE,"E233"),sQuery(id+"F0.wireOp",EDGE,"E234"),sQuery(id+"F0.wireOp",EDGE,"E235"),sQuery(id+"F0.wireOp",EDGE,"E236"),sQuery(id+"F0.wireOp",EDGE,"E237"),sQuery(id+"F0.wireOp",EDGE,"E238"),sQuery(id+"F0.wireOp",EDGE,"E239"),sQuery(id+"F0.wireOp",EDGE,"E240"),sQuery(id+"F0.wireOp",EDGE,"E241"),sQuery(id+"F0.wireOp",EDGE,"E242"),sQuery(id+"F0.wireOp",EDGE,"E243"),sQuery(id+"F0.wireOp",EDGE,"E244"),sQuery(id+"F0.wireOp",EDGE,"E245"),sQuery(id+"F0.wireOp",EDGE,"E246"),sQuery(id+"F0.wireOp",EDGE,"E247"),sQuery(id+"F0.wireOp",EDGE,"E248"),sQuery(id+"F0.wireOp",EDGE,"E249"),sQuery(id+"F0.wireOp",EDGE,"E250"),sQuery(id+"F0.wireOp",EDGE,"E251"),sQuery(id+"F0.wireOp",EDGE,"E252"),sQuery(id+"F0.wireOp",EDGE,"E253"),sQuery(id+"F0.wireOp",EDGE,"E254"),sQuery(id+"F0.wireOp",EDGE,"E255"),sQuery(id+"F0.wireOp",EDGE,"E256"),sQuery(id+"F0.wireOp",EDGE,"E257"),sQuery(id+"F0.wireOp",EDGE,"E258"),sQuery(id+"F0.wireOp",EDGE,"E259"),sQuery(id+"F0.wireOp",EDGE,"E260"),sQuery(id+"F0.wireOp",EDGE,"E261"),sQuery(id+"F0.wireOp",EDGE,"E262"),sQuery(id+"F0.wireOp",EDGE,"E263"),sQuery(id+"F0.wireOp",EDGE,"E264"),sQuery(id+"F0.wireOp",EDGE,"E265"),sQuery(id+"F0.wireOp",EDGE,"E266"),sQuery(id+"F0.wireOp",EDGE,"E267"),sQuery(id+"F0.wireOp",EDGE,"E268"),sQuery(id+"F0.wireOp",EDGE,"E269"),sQuery(id+"F0.wireOp",EDGE,"E270"),sQuery(id+"F0.wireOp",EDGE,"E271"),sQuery(id+"F0.wireOp",EDGE,"E272"),sQuery(id+"F0.wireOp",EDGE,"E273"),sQuery(id+"F0.wireOp",EDGE,"E274"),sQuery(id+"F0.wireOp",EDGE,"E275"),sQuery(id+"F0.wireOp",EDGE,"E276"),sQuery(id+"F0.wireOp",EDGE,"E277"),sQuery(id+"F0.wireOp",EDGE,"E278"),sQuery(id+"F0.wireOp",EDGE,"E279"),sQuery(id+"F0.wireOp",EDGE,"E280"),sQuery(id+"F0.wireOp",EDGE,"E281"),sQuery(id+"F0.wireOp",EDGE,"E282"),sQuery(id+"F0.wireOp",EDGE,"E283"),sQuery(id+"F0.wireOp",EDGE,"E284"),sQuery(id+"F0.wireOp",EDGE,"E285"),sQuery(id+"F0.wireOp",EDGE,"E286"),sQuery(id+"F0.wireOp",EDGE,"E287"),sQuery(id+"F0.wireOp",EDGE,"E288"),sQuery(id+"F0.wireOp",EDGE,"E289"),sQuery(id+"F0.wireOp",EDGE,"E290"),sQuery(id+"F0.wireOp",EDGE,"E291"),sQuery(id+"F0.wireOp",EDGE,"E292"),sQuery(id+"F0.wireOp",EDGE,"E293"),sQuery(id+"F0.wireOp",EDGE,"E294"),sQuery(id+"F0.wireOp",EDGE,"E295"),sQuery(id+"F0.wireOp",EDGE,"E296"),sQuery(id+"F0.wireOp",EDGE,"E297"),sQuery(id+"F0.wireOp",EDGE,"E298"),sQuery(id+"F0.wireOp",EDGE,"E299"),sQuery(id+"F0.wireOp",EDGE,"E300"),sQuery(id+"F0.wireOp",EDGE,"E301"),sQuery(id+"F0.wireOp",EDGE,"E302"),sQuery(id+"F0.wireOp",EDGE,"E303"),sQuery(id+"F0.wireOp",EDGE,"E304"),sQuery(id+"F0.wireOp",EDGE,"E305"),sQuery(id+"F0.wireOp",EDGE,"E306"),sQuery(id+"F0.wireOp",EDGE,"E307"),sQuery(id+"F0.wireOp",EDGE,"E308"),sQuery(id+"F0.wireOp",EDGE,"E309"),sQuery(id+"F0.wireOp",EDGE,"E310"),sQuery(id+"F0.wireOp",EDGE,"E311"),sQuery(id+"F0.wireOp",EDGE,"E312"),sQuery(id+"F0.wireOp",EDGE,"E313"),sQuery(id+"F0.wireOp",EDGE,"E314"),sQuery(id+"F0.wireOp",EDGE,"E315"),sQuery(id+"F0.wireOp",EDGE,"E316"),sQuery(id+"F0.wireOp",EDGE,"E317"),sQuery(id+"F0.wireOp",EDGE,"E318"),sQuery(id+"F0.wireOp",EDGE,"E319"),sQuery(id+"F0.wireOp",EDGE,"E320"),sQuery(id+"F0.wireOp",EDGE,"E321"),sQuery(id+"F0.wireOp",EDGE,"E322"),sQuery(id+"F0.wireOp",EDGE,"E323"),sQuery(id+"F0.wireOp",EDGE,"E324"),sQuery(id+"F0.wireOp",EDGE,"E325"),sQuery(id+"F0.wireOp",EDGE,"E326"),sQuery(id+"F0.wireOp",EDGE,"E327"),sQuery(id+"F0.wireOp",EDGE,"E328"),sQuery(id+"F0.wireOp",EDGE,"E329"),sQuery(id+"F0.wireOp",EDGE,"E330"),sQuery(id+"F0.wireOp",EDGE,"E331"),sQuery(id+"F0.wireOp",EDGE,"E332"),sQuery(id+"F0.wireOp",EDGE,"E333"),sQuery(id+"F0.wireOp",EDGE,"E334"),sQuery(id+"F0.wireOp",EDGE,"E335"),sQuery(id+"F0.wireOp",EDGE,"E336"),sQuery(id+"F0.wireOp",EDGE,"E337"),sQuery(id+"F0.wireOp",EDGE,"E338"),sQuery(id+"F0.wireOp",EDGE,"E339"),sQuery(id+"F0.wireOp",EDGE,"E340"),sQuery(id+"F0.wireOp",EDGE,"E341"),sQuery(id+"F0.wireOp",EDGE,"E342"),sQuery(id+"F0.wireOp",EDGE,"E343"),sQuery(id+"F0.wireOp",EDGE,"E344"),sQuery(id+"F0.wireOp",EDGE,"E345"),sQuery(id+"F0.wireOp",EDGE,"E346"),sQuery(id+"F0.wireOp",EDGE,"E347"),sQuery(id+"F0.wireOp",EDGE,"E348"),sQuery(id+"F0.wireOp",EDGE,"E349"),sQuery(id+"F0.wireOp",EDGE,"E350"),sQuery(id+"F0.wireOp",EDGE,"E351"),sQuery(id+"F0.wireOp",EDGE,"E352"),sQuery(id+"F0.wireOp",EDGE,"E353"),sQuery(id+"F0.wireOp",EDGE,"E354"),sQuery(id+"F0.wireOp",EDGE,"E355"),sQuery(id+"F0.wireOp",EDGE,"E356"),sQuery(id+"F0.wireOp",EDGE,"E357"),sQuery(id+"F0.wireOp",EDGE,"E358"),sQuery(id+"F0.wireOp",EDGE,"E359"),sQuery(id+"F0.wireOp",EDGE,"E360"),sQuery(id+"F0.wireOp",EDGE,"E361"),sQuery(id+"F0.wireOp",EDGE,"E362"),sQuery(id+"F0.wireOp",EDGE,"E363"),sQuery(id+"F0.wireOp",EDGE,"E364"),sQuery(id+"F0.wireOp",EDGE,"E365"),sQuery(id+"F0.wireOp",EDGE,"E366"),sQuery(id+"F0.wireOp",EDGE,"E367"),sQuery(id+"F0.wireOp",EDGE,"E368"),sQuery(id+"F0.wireOp",EDGE,"E369"),sQuery(id+"F0.wireOp",EDGE,"E370"),sQuery(id+"F0.wireOp",EDGE,"E371"),sQuery(id+"F0.wireOp",EDGE,"E372"),sQuery(id+"F0.wireOp",EDGE,"E373"),sQuery(id+"F0.wireOp",EDGE,"E374"),sQuery(id+"F0.wireOp",EDGE,"E375"),sQuery(id+"F0.wireOp",EDGE,"E376"),sQuery(id+"F0.wireOp",EDGE,"E377"),sQuery(id+"F0.wireOp",EDGE,"E378"),sQuery(id+"F0.wireOp",EDGE,"E379"),sQuery(id+"F0.wireOp",EDGE,"E380"),sQuery(id+"F0.wireOp",EDGE,"E381"),sQuery(id+"F0.wireOp",EDGE,"E382"),sQuery(id+"F0.wireOp",EDGE,"E383"),sQuery(id+"F0.wireOp",EDGE,"E384"),sQuery(id+"F0.wireOp",EDGE,"E385"),sQuery(id+"F0.wireOp",EDGE,"E386"),sQuery(id+"F0.wireOp",EDGE,"E387"),sQuery(id+"F0.wireOp",EDGE,"E388"),sQuery(id+"F0.wireOp",EDGE,"E389"),sQuery(id+"F0.wireOp",EDGE,"E390"),sQuery(id+"F0.wireOp",EDGE,"E391"),sQuery(id+"F0.wireOp",EDGE,"E392"),sQuery(id+"F0.wireOp",EDGE,"E393"),sQuery(id+"F0.wireOp",EDGE,"E394"),sQuery(id+"F0.wireOp",EDGE,"E395"),sQuery(id+"F0.wireOp",EDGE,"E396"),sQuery(id+"F0.wireOp",EDGE,"E397"),sQuery(id+"F0.wireOp",EDGE,"E398"),sQuery(id+"F0.wireOp",EDGE,"E399"),sQuery(id+"F0.wireOp",EDGE,"E400"),sQuery(id+"F0.wireOp",EDGE,"E401"),sQuery(id+"F0.wireOp",EDGE,"E402"),sQuery(id+"F0.wireOp",EDGE,"E403"),sQuery(id+"F0.wireOp",EDGE,"E404"),sQuery(id+"F0.wireOp",EDGE,"E405"),sQuery(id+"F0.wireOp",EDGE,"E406"),sQuery(id+"F0.wireOp",EDGE,"E407"),sQuery(id+"F0.wireOp",EDGE,"E408"),sQuery(id+"F0.wireOp",EDGE,"E409"),sQuery(id+"F0.wireOp",EDGE,"E410"),sQuery(id+"F0.wireOp",EDGE,"E411"),sQuery(id+"F0.wireOp",EDGE,"E412"),sQuery(id+"F0.wireOp",EDGE,"E413"),sQuery(id+"F0.wireOp",EDGE,"E414"),sQuery(id+"F0.wireOp",EDGE,"E415"),sQuery(id+"F0.wireOp",EDGE,"E416"),sQuery(id+"F0.wireOp",EDGE,"E417"),sQuery(id+"F0.wireOp",EDGE,"E418"),sQuery(id+"F0.wireOp",EDGE,"E419"),sQuery(id+"F0.wireOp",EDGE,"E420"),sQuery(id+"F0.wireOp",EDGE,"E421"),sQuery(id+"F0.wireOp",EDGE,"E422"),sQuery(id+"F0.wireOp",EDGE,"E423"),sQuery(id+"F0.wireOp",EDGE,"E424"),sQuery(id+"F0.wireOp",EDGE,"E425"),sQuery(id+"F0.wireOp",EDGE,"E426"),sQuery(id+"F0.wireOp",EDGE,"E427"),sQuery(id+"F0.wireOp",EDGE,"E428"),sQuery(id+"F0.wireOp",EDGE,"E429"),sQuery(id+"F0.wireOp",EDGE,"E430"),sQuery(id+"F0.wireOp",EDGE,"E431"),sQuery(id+"F0.wireOp",EDGE,"E432"),sQuery(id+"F0.wireOp",EDGE,"E433"),sQuery(id+"F0.wireOp",EDGE,"E434"),sQuery(id+"F0.wireOp",EDGE,"E435"),sQuery(id+"F0.wireOp",EDGE,"E436"),sQuery(id+"F0.wireOp",EDGE,"E437"),sQuery(id+"F0.wireOp",EDGE,"E438"),sQuery(id+"F0.wireOp",EDGE,"E439"),sQuery(id+"F0.wireOp",EDGE,"E440"),sQuery(id+"F0.wireOp",EDGE,"E441"),sQuery(id+"F0.wireOp",EDGE,"E442"),sQuery(id+"F0.wireOp",EDGE,"E443"),sQuery(id+"F0.wireOp",EDGE,"E444"),sQuery(id+"F0.wireOp",EDGE,"E445"),sQuery(id+"F0.wireOp",EDGE,"E446"),sQuery(id+"F0.wireOp",EDGE,"E447"),sQuery(id+"F0.wireOp",EDGE,"E448"),sQuery(id+"F0.wireOp",EDGE,"E449"),sQuery(id+"F0.wireOp",EDGE,"E450"),sQuery(id+"F0.wireOp",EDGE,"E451"),sQuery(id+"F0.wireOp",EDGE,"E452"),sQuery(id+"F0.wireOp",EDGE,"E453"),sQuery(id+"F0.wireOp",EDGE,"E454"),sQuery(id+"F0.wireOp",EDGE,"E455"),sQuery(id+"F0.wireOp",EDGE,"E456"),sQuery(id+"F0.wireOp",EDGE,"E457"),sQuery(id+"F0.wireOp",EDGE,"E458"),sQuery(id+"F0.wireOp",EDGE,"E459"),sQuery(id+"F0.wireOp",EDGE,"E460"),sQuery(id+"F0.wireOp",EDGE,"E461"),sQuery(id+"F0.wireOp",EDGE,"E462"),sQuery(id+"F0.wireOp",EDGE,"E463"),sQuery(id+"F0.wireOp",EDGE,"E464"),sQuery(id+"F0.wireOp",EDGE,"E465"),sQuery(id+"F0.wireOp",EDGE,"E466"),sQuery(id+"F0.wireOp",EDGE,"E467"),sQuery(id+"F0.wireOp",EDGE,"E468"),sQuery(id+"F0.wireOp",EDGE,"E469"),sQuery(id+"F0.wireOp",EDGE,"E470"),sQuery(id+"F0.wireOp",EDGE,"E471"),sQuery(id+"F0.wireOp",EDGE,"E472"),sQuery(id+"F0.wireOp",EDGE,"E473"),sQuery(id+"F0.wireOp",EDGE,"E474"),sQuery(id+"F0.wireOp",EDGE,"E475"),sQuery(id+"F0.wireOp",EDGE,"E476"),sQuery(id+"F0.wireOp",EDGE,"E477"),sQuery(id+"F0.wireOp",EDGE,"E478"),sQuery(id+"F0.wireOp",EDGE,"E479"),sQuery(id+"F0.wireOp",EDGE,"E480"),sQuery(id+"F0.wireOp",EDGE,"E481"),sQuery(id+"F0.wireOp",EDGE,"E482"),sQuery(id+"F0.wireOp",EDGE,"E483"),sQuery(id+"F0.wireOp",EDGE,"E484"),sQuery(id+"F0.wireOp",EDGE,"E485"),sQuery(id+"F0.wireOp",EDGE,"E486"),sQuery(id+"F0.wireOp",EDGE,"E487"),sQuery(id+"F0.wireOp",EDGE,"E488"),sQuery(id+"F0.wireOp",EDGE,"E489"),sQuery(id+"F0.wireOp",EDGE,"E490"),sQuery(id+"F0.wireOp",EDGE,"E491"),sQuery(id+"F0.wireOp",EDGE,"E492"),sQuery(id+"F0.wireOp",EDGE,"E493"),sQuery(id+"F0.wireOp",EDGE,"E494"),sQuery(id+"F0.wireOp",EDGE,"E495"),sQuery(id+"F0.wireOp",EDGE,"E496"),sQuery(id+"F0.wireOp",EDGE,"E497"),sQuery(id+"F0.wireOp",EDGE,"E498"),sQuery(id+"F0.wireOp",EDGE,"E499"),sQuery(id+"F0.wireOp",EDGE,"E500"),sQuery(id+"F0.wireOp",EDGE,"E501"),sQuery(id+"F0.wireOp",EDGE,"E502"),sQuery(id+"F0.wireOp",EDGE,"E503"),sQuery(id+"F0.wireOp",EDGE,"E504"),sQuery(id+"F0.wireOp",EDGE,"E505"),sQuery(id+"F0.wireOp",EDGE,"E506"),sQuery(id+"F0.wireOp",EDGE,"E507"),sQuery(id+"F0.wireOp",EDGE,"E508"),sQuery(id+"F0.wireOp",EDGE,"E509"),sQuery(id+"F0.wireOp",EDGE,"E510"),sQuery(id+"F0.wireOp",EDGE,"E511"),sQuery(id+"F0.wireOp",EDGE,"E512"),sQuery(id+"F0.wireOp",EDGE,"E513"),sQuery(id+"F0.wireOp",EDGE,"E514"),sQuery(id+"F0.wireOp",EDGE,"E515"),sQuery(id+"F0.wireOp",EDGE,"E516"),sQuery(id+"F0.wireOp",EDGE,"E517"),sQuery(id+"F0.wireOp",EDGE,"E518"),sQuery(id+"F0.wireOp",EDGE,"E519"),sQuery(id+"F0.wireOp",EDGE,"E520"),sQuery(id+"F0.wireOp",EDGE,"E521"),sQuery(id+"F0.wireOp",EDGE,"E522"),sQuery(id+"F0.wireOp",EDGE,"E523"),sQuery(id+"F0.wireOp",EDGE,"E524"),sQuery(id+"F0.wireOp",EDGE,"E525"),sQuery(id+"F0.wireOp",EDGE,"E526"),sQuery(id+"F0.wireOp",EDGE,"E527"),sQuery(id+"F0.wireOp",EDGE,"E528"),sQuery(id+"F0.wireOp",EDGE,"E529"),sQuery(id+"F0.wireOp",EDGE,"E530"),sQuery(id+"F0.wireOp",EDGE,"E531"),sQuery(id+"F0.wireOp",EDGE,"E532"),sQuery(id+"F0.wireOp",EDGE,"E533"),sQuery(id+"F0.wireOp",EDGE,"E534"),sQuery(id+"F0.wireOp",EDGE,"E535"),sQuery(id+"F0.wireOp",EDGE,"E536"),sQuery(id+"F0.wireOp",EDGE,"E537"),sQuery(id+"F0.wireOp",EDGE,"E538"),sQuery(id+"F0.wireOp",EDGE,"E539"),sQuery(id+"F0.wireOp",EDGE,"E540"),sQuery(id+"F0.wireOp",EDGE,"E541"),sQuery(id+"F0.wireOp",EDGE,"E542"),sQuery(id+"F0.wireOp",EDGE,"E543"),sQuery(id+"F0.wireOp",EDGE,"E544"),sQuery(id+"F0.wireOp",EDGE,"E545"),sQuery(id+"F0.wireOp",EDGE,"E546"),sQuery(id+"F0.wireOp",EDGE,"E547"),sQuery(id+"F0.wireOp",EDGE,"E548"),sQuery(id+"F0.wireOp",EDGE,"E549"),sQuery(id+"F0.wireOp",EDGE,"E550"),sQuery(id+"F0.wireOp",EDGE,"E551"),sQuery(id+"F0.wireOp",EDGE,"E552"),sQuery(id+"F0.wireOp",EDGE,"E553"),sQuery(id+"F0.wireOp",EDGE,"E554"),sQuery(id+"F0.wireOp",EDGE,"E555"),sQuery(id+"F0.wireOp",EDGE,"E556"),sQuery(id+"F0.wireOp",EDGE,"E557"),sQuery(id+"F0.wireOp",EDGE,"E558"),sQuery(id+"F0.wireOp",EDGE,"E559"),sQuery(id+"F0.wireOp",EDGE,"E560"),sQuery(id+"F0.wireOp",EDGE,"E561"),sQuery(id+"F0.wireOp",EDGE,"E562"),sQuery(id+"F0.wireOp",EDGE,"E563"),sQuery(id+"F0.wireOp",EDGE,"E564"),sQuery(id+"F0.wireOp",EDGE,"E565"),sQuery(id+"F0.wireOp",EDGE,"E566"),sQuery(id+"F0.wireOp",EDGE,"E567"),sQuery(id+"F0.wireOp",EDGE,"E568"),sQuery(id+"F0.wireOp",EDGE,"E569"),sQuery(id+"F0.wireOp",EDGE,"E570"),sQuery(id+"F0.wireOp",EDGE,"E571"),sQuery(id+"F0.wireOp",EDGE,"E572"),sQuery(id+"F0.wireOp",EDGE,"E573"),sQuery(id+"F0.wireOp",EDGE,"E574"),sQuery(id+"F0.wireOp",EDGE,"E575"),sQuery(id+"F0.wireOp",EDGE,"E576"),sQuery(id+"F0.wireOp",EDGE,"E577"),sQuery(id+"F0.wireOp",EDGE,"E1140"),sQuery(id+"F0.wireOp",EDGE,"E1143")])],"isStart":false});
            var sketch = newSketch(context, id + "F6", { "sketchPlane" : qUnion([Q0])});
            skLineSegment(sketch, "E2030.bottom", {"start": v(-137.89, 9.87) * mm, "end": v(-117.47, 9.87) * mm});
            skLineSegment(sketch, "E2030.top", {"start": v(-137.89, -15.95) * mm, "end": v(-117.47, -15.95) * mm});
            skLineSegment(sketch, "E2030.left", {"start": v(-137.89, 9.87) * mm, "end": v(-137.89, -15.95) * mm});
            skLineSegment(sketch, "E2030.right", {"start": v(-117.47, 9.87) * mm, "end": v(-117.47, -15.95) * mm});
            skSolve(sketch);
        }
        {
            var Q0;
            Q0 = qSketchRegion(id + "F6", true);
            extrude(context, id + "F7", {"entities" : qUnion([Q0]), "operationType" : NewBodyOperationType.REMOVE, "endBound" : BoundingType.SYMMETRIC, "oppositeDirection" : true, "depth" : 25 * mm, "offsetDistance" : 25 * mm});
        }
        {
            var Q0;
            Q0=makeQuery(id+"F1.opExtrude","CAP_FACE",FACE,{"disambiguationData":[OSD([sQuery(id+"F0.wireOp",EDGE,"E0"),sQuery(id+"F0.wireOp",EDGE,"E1"),sQuery(id+"F0.wireOp",EDGE,"E2"),sQuery(id+"F0.wireOp",EDGE,"E3"),sQuery(id+"F0.wireOp",EDGE,"E4"),sQuery(id+"F0.wireOp",EDGE,"E5"),sQuery(id+"F0.wireOp",EDGE,"E6"),sQuery(id+"F0.wireOp",EDGE,"E7"),sQuery(id+"F0.wireOp",EDGE,"E8"),sQuery(id+"F0.wireOp",EDGE,"E9"),sQuery(id+"F0.wireOp",EDGE,"E10"),sQuery(id+"F0.wireOp",EDGE,"E11"),sQuery(id+"F0.wireOp",EDGE,"E12"),sQuery(id+"F0.wireOp",EDGE,"E13"),sQuery(id+"F0.wireOp",EDGE,"E14"),sQuery(id+"F0.wireOp",EDGE,"E15"),sQuery(id+"F0.wireOp",EDGE,"E16"),sQuery(id+"F0.wireOp",EDGE,"E17"),sQuery(id+"F0.wireOp",EDGE,"E18"),sQuery(id+"F0.wireOp",EDGE,"E19"),sQuery(id+"F0.wireOp",EDGE,"E20"),sQuery(id+"F0.wireOp",EDGE,"E21"),sQuery(id+"F0.wireOp",EDGE,"E22"),sQuery(id+"F0.wireOp",EDGE,"E23"),sQuery(id+"F0.wireOp",EDGE,"E24"),sQuery(id+"F0.wireOp",EDGE,"E25"),sQuery(id+"F0.wireOp",EDGE,"E26"),sQuery(id+"F0.wireOp",EDGE,"E27"),sQuery(id+"F0.wireOp",EDGE,"E28"),sQuery(id+"F0.wireOp",EDGE,"E29"),sQuery(id+"F0.wireOp",EDGE,"E30"),sQuery(id+"F0.wireOp",EDGE,"E31"),sQuery(id+"F0.wireOp",EDGE,"E32"),sQuery(id+"F0.wireOp",EDGE,"E33"),sQuery(id+"F0.wireOp",EDGE,"E34"),sQuery(id+"F0.wireOp",EDGE,"E35"),sQuery(id+"F0.wireOp",EDGE,"E36"),sQuery(id+"F0.wireOp",EDGE,"E37"),sQuery(id+"F0.wireOp",EDGE,"E38"),sQuery(id+"F0.wireOp",EDGE,"E39"),sQuery(id+"F0.wireOp",EDGE,"E40"),sQuery(id+"F0.wireOp",EDGE,"E41"),sQuery(id+"F0.wireOp",EDGE,"E42"),sQuery(id+"F0.wireOp",EDGE,"E43"),sQuery(id+"F0.wireOp",EDGE,"E44"),sQuery(id+"F0.wireOp",EDGE,"E45"),sQuery(id+"F0.wireOp",EDGE,"E46"),sQuery(id+"F0.wireOp",EDGE,"E47"),sQuery(id+"F0.wireOp",EDGE,"E48"),sQuery(id+"F0.wireOp",EDGE,"E49"),sQuery(id+"F0.wireOp",EDGE,"E50"),sQuery(id+"F0.wireOp",EDGE,"E51"),sQuery(id+"F0.wireOp",EDGE,"E52"),sQuery(id+"F0.wireOp",EDGE,"E53"),sQuery(id+"F0.wireOp",EDGE,"E54"),sQuery(id+"F0.wireOp",EDGE,"E55"),sQuery(id+"F0.wireOp",EDGE,"E56"),sQuery(id+"F0.wireOp",EDGE,"E57"),sQuery(id+"F0.wireOp",EDGE,"E58"),sQuery(id+"F0.wireOp",EDGE,"E59"),sQuery(id+"F0.wireOp",EDGE,"E60"),sQuery(id+"F0.wireOp",EDGE,"E61"),sQuery(id+"F0.wireOp",EDGE,"E62"),sQuery(id+"F0.wireOp",EDGE,"E63"),sQuery(id+"F0.wireOp",EDGE,"E64"),sQuery(id+"F0.wireOp",EDGE,"E65"),sQuery(id+"F0.wireOp",EDGE,"E66"),sQuery(id+"F0.wireOp",EDGE,"E67"),sQuery(id+"F0.wireOp",EDGE,"E68"),sQuery(id+"F0.wireOp",EDGE,"E69"),sQuery(id+"F0.wireOp",EDGE,"E70"),sQuery(id+"F0.wireOp",EDGE,"E71"),sQuery(id+"F0.wireOp",EDGE,"E72"),sQuery(id+"F0.wireOp",EDGE,"E73"),sQuery(id+"F0.wireOp",EDGE,"E74"),sQuery(id+"F0.wireOp",EDGE,"E75"),sQuery(id+"F0.wireOp",EDGE,"E76"),sQuery(id+"F0.wireOp",EDGE,"E77"),sQuery(id+"F0.wireOp",EDGE,"E78"),sQuery(id+"F0.wireOp",EDGE,"E79"),sQuery(id+"F0.wireOp",EDGE,"E80"),sQuery(id+"F0.wireOp",EDGE,"E81"),sQuery(id+"F0.wireOp",EDGE,"E82"),sQuery(id+"F0.wireOp",EDGE,"E83"),sQuery(id+"F0.wireOp",EDGE,"E84"),sQuery(id+"F0.wireOp",EDGE,"E85"),sQuery(id+"F0.wireOp",EDGE,"E86"),sQuery(id+"F0.wireOp",EDGE,"E87"),sQuery(id+"F0.wireOp",EDGE,"E88"),sQuery(id+"F0.wireOp",EDGE,"E89"),sQuery(id+"F0.wireOp",EDGE,"E90"),sQuery(id+"F0.wireOp",EDGE,"E91"),sQuery(id+"F0.wireOp",EDGE,"E92"),sQuery(id+"F0.wireOp",EDGE,"E93"),sQuery(id+"F0.wireOp",EDGE,"E94"),sQuery(id+"F0.wireOp",EDGE,"E95"),sQuery(id+"F0.wireOp",EDGE,"E96"),sQuery(id+"F0.wireOp",EDGE,"E97"),sQuery(id+"F0.wireOp",EDGE,"E98"),sQuery(id+"F0.wireOp",EDGE,"E99"),sQuery(id+"F0.wireOp",EDGE,"E100"),sQuery(id+"F0.wireOp",EDGE,"E101"),sQuery(id+"F0.wireOp",EDGE,"E102"),sQuery(id+"F0.wireOp",EDGE,"E103"),sQuery(id+"F0.wireOp",EDGE,"E104"),sQuery(id+"F0.wireOp",EDGE,"E105"),sQuery(id+"F0.wireOp",EDGE,"E106"),sQuery(id+"F0.wireOp",EDGE,"E107"),sQuery(id+"F0.wireOp",EDGE,"E108"),sQuery(id+"F0.wireOp",EDGE,"E109"),sQuery(id+"F0.wireOp",EDGE,"E110"),sQuery(id+"F0.wireOp",EDGE,"E111"),sQuery(id+"F0.wireOp",EDGE,"E112"),sQuery(id+"F0.wireOp",EDGE,"E113"),sQuery(id+"F0.wireOp",EDGE,"E114"),sQuery(id+"F0.wireOp",EDGE,"E115"),sQuery(id+"F0.wireOp",EDGE,"E116"),sQuery(id+"F0.wireOp",EDGE,"E117"),sQuery(id+"F0.wireOp",EDGE,"E118"),sQuery(id+"F0.wireOp",EDGE,"E119"),sQuery(id+"F0.wireOp",EDGE,"E120"),sQuery(id+"F0.wireOp",EDGE,"E121"),sQuery(id+"F0.wireOp",EDGE,"E122"),sQuery(id+"F0.wireOp",EDGE,"E123"),sQuery(id+"F0.wireOp",EDGE,"E124"),sQuery(id+"F0.wireOp",EDGE,"E125"),sQuery(id+"F0.wireOp",EDGE,"E126"),sQuery(id+"F0.wireOp",EDGE,"E127"),sQuery(id+"F0.wireOp",EDGE,"E128"),sQuery(id+"F0.wireOp",EDGE,"E129"),sQuery(id+"F0.wireOp",EDGE,"E130"),sQuery(id+"F0.wireOp",EDGE,"E131"),sQuery(id+"F0.wireOp",EDGE,"E132"),sQuery(id+"F0.wireOp",EDGE,"E133"),sQuery(id+"F0.wireOp",EDGE,"E134"),sQuery(id+"F0.wireOp",EDGE,"E135"),sQuery(id+"F0.wireOp",EDGE,"E136"),sQuery(id+"F0.wireOp",EDGE,"E137"),sQuery(id+"F0.wireOp",EDGE,"E138"),sQuery(id+"F0.wireOp",EDGE,"E139"),sQuery(id+"F0.wireOp",EDGE,"E140"),sQuery(id+"F0.wireOp",EDGE,"E141"),sQuery(id+"F0.wireOp",EDGE,"E142"),sQuery(id+"F0.wireOp",EDGE,"E143"),sQuery(id+"F0.wireOp",EDGE,"E144"),sQuery(id+"F0.wireOp",EDGE,"E145"),sQuery(id+"F0.wireOp",EDGE,"E146"),sQuery(id+"F0.wireOp",EDGE,"E147"),sQuery(id+"F0.wireOp",EDGE,"E148"),sQuery(id+"F0.wireOp",EDGE,"E149"),sQuery(id+"F0.wireOp",EDGE,"E150"),sQuery(id+"F0.wireOp",EDGE,"E151"),sQuery(id+"F0.wireOp",EDGE,"E152"),sQuery(id+"F0.wireOp",EDGE,"E153"),sQuery(id+"F0.wireOp",EDGE,"E154"),sQuery(id+"F0.wireOp",EDGE,"E155"),sQuery(id+"F0.wireOp",EDGE,"E156"),sQuery(id+"F0.wireOp",EDGE,"E157"),sQuery(id+"F0.wireOp",EDGE,"E158"),sQuery(id+"F0.wireOp",EDGE,"E159"),sQuery(id+"F0.wireOp",EDGE,"E160"),sQuery(id+"F0.wireOp",EDGE,"E161"),sQuery(id+"F0.wireOp",EDGE,"E162"),sQuery(id+"F0.wireOp",EDGE,"E163"),sQuery(id+"F0.wireOp",EDGE,"E164"),sQuery(id+"F0.wireOp",EDGE,"E165"),sQuery(id+"F0.wireOp",EDGE,"E166"),sQuery(id+"F0.wireOp",EDGE,"E167"),sQuery(id+"F0.wireOp",EDGE,"E168"),sQuery(id+"F0.wireOp",EDGE,"E169"),sQuery(id+"F0.wireOp",EDGE,"E170"),sQuery(id+"F0.wireOp",EDGE,"E171"),sQuery(id+"F0.wireOp",EDGE,"E172"),sQuery(id+"F0.wireOp",EDGE,"E173"),sQuery(id+"F0.wireOp",EDGE,"E174"),sQuery(id+"F0.wireOp",EDGE,"E175"),sQuery(id+"F0.wireOp",EDGE,"E176"),sQuery(id+"F0.wireOp",EDGE,"E177"),sQuery(id+"F0.wireOp",EDGE,"E178"),sQuery(id+"F0.wireOp",EDGE,"E179"),sQuery(id+"F0.wireOp",EDGE,"E180"),sQuery(id+"F0.wireOp",EDGE,"E181"),sQuery(id+"F0.wireOp",EDGE,"E182"),sQuery(id+"F0.wireOp",EDGE,"E183"),sQuery(id+"F0.wireOp",EDGE,"E184"),sQuery(id+"F0.wireOp",EDGE,"E185"),sQuery(id+"F0.wireOp",EDGE,"E186"),sQuery(id+"F0.wireOp",EDGE,"E187"),sQuery(id+"F0.wireOp",EDGE,"E188"),sQuery(id+"F0.wireOp",EDGE,"E189"),sQuery(id+"F0.wireOp",EDGE,"E190"),sQuery(id+"F0.wireOp",EDGE,"E191"),sQuery(id+"F0.wireOp",EDGE,"E192"),sQuery(id+"F0.wireOp",EDGE,"E193"),sQuery(id+"F0.wireOp",EDGE,"E194"),sQuery(id+"F0.wireOp",EDGE,"E195"),sQuery(id+"F0.wireOp",EDGE,"E196"),sQuery(id+"F0.wireOp",EDGE,"E197"),sQuery(id+"F0.wireOp",EDGE,"E198"),sQuery(id+"F0.wireOp",EDGE,"E199"),sQuery(id+"F0.wireOp",EDGE,"E200"),sQuery(id+"F0.wireOp",EDGE,"E201"),sQuery(id+"F0.wireOp",EDGE,"E202"),sQuery(id+"F0.wireOp",EDGE,"E203"),sQuery(id+"F0.wireOp",EDGE,"E204"),sQuery(id+"F0.wireOp",EDGE,"E205"),sQuery(id+"F0.wireOp",EDGE,"E206"),sQuery(id+"F0.wireOp",EDGE,"E207"),sQuery(id+"F0.wireOp",EDGE,"E208"),sQuery(id+"F0.wireOp",EDGE,"E209"),sQuery(id+"F0.wireOp",EDGE,"E210"),sQuery(id+"F0.wireOp",EDGE,"E211"),sQuery(id+"F0.wireOp",EDGE,"E212"),sQuery(id+"F0.wireOp",EDGE,"E213"),sQuery(id+"F0.wireOp",EDGE,"E214"),sQuery(id+"F0.wireOp",EDGE,"E215"),sQuery(id+"F0.wireOp",EDGE,"E216"),sQuery(id+"F0.wireOp",EDGE,"E217"),sQuery(id+"F0.wireOp",EDGE,"E218"),sQuery(id+"F0.wireOp",EDGE,"E219"),sQuery(id+"F0.wireOp",EDGE,"E220"),sQuery(id+"F0.wireOp",EDGE,"E221"),sQuery(id+"F0.wireOp",EDGE,"E222"),sQuery(id+"F0.wireOp",EDGE,"E223"),sQuery(id+"F0.wireOp",EDGE,"E224"),sQuery(id+"F0.wireOp",EDGE,"E225"),sQuery(id+"F0.wireOp",EDGE,"E226"),sQuery(id+"F0.wireOp",EDGE,"E227"),sQuery(id+"F0.wireOp",EDGE,"E228"),sQuery(id+"F0.wireOp",EDGE,"E229"),sQuery(id+"F0.wireOp",EDGE,"E230"),sQuery(id+"F0.wireOp",EDGE,"E231"),sQuery(id+"F0.wireOp",EDGE,"E232"),sQuery(id+"F0.wireOp",EDGE,"E233"),sQuery(id+"F0.wireOp",EDGE,"E234"),sQuery(id+"F0.wireOp",EDGE,"E235"),sQuery(id+"F0.wireOp",EDGE,"E236"),sQuery(id+"F0.wireOp",EDGE,"E237"),sQuery(id+"F0.wireOp",EDGE,"E238"),sQuery(id+"F0.wireOp",EDGE,"E239"),sQuery(id+"F0.wireOp",EDGE,"E240"),sQuery(id+"F0.wireOp",EDGE,"E241"),sQuery(id+"F0.wireOp",EDGE,"E242"),sQuery(id+"F0.wireOp",EDGE,"E243"),sQuery(id+"F0.wireOp",EDGE,"E244"),sQuery(id+"F0.wireOp",EDGE,"E245"),sQuery(id+"F0.wireOp",EDGE,"E246"),sQuery(id+"F0.wireOp",EDGE,"E247"),sQuery(id+"F0.wireOp",EDGE,"E248"),sQuery(id+"F0.wireOp",EDGE,"E249"),sQuery(id+"F0.wireOp",EDGE,"E250"),sQuery(id+"F0.wireOp",EDGE,"E251"),sQuery(id+"F0.wireOp",EDGE,"E252"),sQuery(id+"F0.wireOp",EDGE,"E253"),sQuery(id+"F0.wireOp",EDGE,"E254"),sQuery(id+"F0.wireOp",EDGE,"E255"),sQuery(id+"F0.wireOp",EDGE,"E256"),sQuery(id+"F0.wireOp",EDGE,"E257"),sQuery(id+"F0.wireOp",EDGE,"E258"),sQuery(id+"F0.wireOp",EDGE,"E259"),sQuery(id+"F0.wireOp",EDGE,"E260"),sQuery(id+"F0.wireOp",EDGE,"E261"),sQuery(id+"F0.wireOp",EDGE,"E262"),sQuery(id+"F0.wireOp",EDGE,"E263"),sQuery(id+"F0.wireOp",EDGE,"E264"),sQuery(id+"F0.wireOp",EDGE,"E265"),sQuery(id+"F0.wireOp",EDGE,"E266"),sQuery(id+"F0.wireOp",EDGE,"E267"),sQuery(id+"F0.wireOp",EDGE,"E268"),sQuery(id+"F0.wireOp",EDGE,"E269"),sQuery(id+"F0.wireOp",EDGE,"E270"),sQuery(id+"F0.wireOp",EDGE,"E271"),sQuery(id+"F0.wireOp",EDGE,"E272"),sQuery(id+"F0.wireOp",EDGE,"E273"),sQuery(id+"F0.wireOp",EDGE,"E274"),sQuery(id+"F0.wireOp",EDGE,"E275"),sQuery(id+"F0.wireOp",EDGE,"E276"),sQuery(id+"F0.wireOp",EDGE,"E277"),sQuery(id+"F0.wireOp",EDGE,"E278"),sQuery(id+"F0.wireOp",EDGE,"E279"),sQuery(id+"F0.wireOp",EDGE,"E280"),sQuery(id+"F0.wireOp",EDGE,"E281"),sQuery(id+"F0.wireOp",EDGE,"E282"),sQuery(id+"F0.wireOp",EDGE,"E283"),sQuery(id+"F0.wireOp",EDGE,"E284"),sQuery(id+"F0.wireOp",EDGE,"E285"),sQuery(id+"F0.wireOp",EDGE,"E286"),sQuery(id+"F0.wireOp",EDGE,"E287"),sQuery(id+"F0.wireOp",EDGE,"E288"),sQuery(id+"F0.wireOp",EDGE,"E289"),sQuery(id+"F0.wireOp",EDGE,"E290"),sQuery(id+"F0.wireOp",EDGE,"E291"),sQuery(id+"F0.wireOp",EDGE,"E292"),sQuery(id+"F0.wireOp",EDGE,"E293"),sQuery(id+"F0.wireOp",EDGE,"E294"),sQuery(id+"F0.wireOp",EDGE,"E295"),sQuery(id+"F0.wireOp",EDGE,"E296"),sQuery(id+"F0.wireOp",EDGE,"E297"),sQuery(id+"F0.wireOp",EDGE,"E298"),sQuery(id+"F0.wireOp",EDGE,"E299"),sQuery(id+"F0.wireOp",EDGE,"E300"),sQuery(id+"F0.wireOp",EDGE,"E301"),sQuery(id+"F0.wireOp",EDGE,"E302"),sQuery(id+"F0.wireOp",EDGE,"E303"),sQuery(id+"F0.wireOp",EDGE,"E304"),sQuery(id+"F0.wireOp",EDGE,"E305"),sQuery(id+"F0.wireOp",EDGE,"E306"),sQuery(id+"F0.wireOp",EDGE,"E307"),sQuery(id+"F0.wireOp",EDGE,"E308"),sQuery(id+"F0.wireOp",EDGE,"E309"),sQuery(id+"F0.wireOp",EDGE,"E310"),sQuery(id+"F0.wireOp",EDGE,"E311"),sQuery(id+"F0.wireOp",EDGE,"E312"),sQuery(id+"F0.wireOp",EDGE,"E313"),sQuery(id+"F0.wireOp",EDGE,"E314"),sQuery(id+"F0.wireOp",EDGE,"E315"),sQuery(id+"F0.wireOp",EDGE,"E316"),sQuery(id+"F0.wireOp",EDGE,"E317"),sQuery(id+"F0.wireOp",EDGE,"E318"),sQuery(id+"F0.wireOp",EDGE,"E319"),sQuery(id+"F0.wireOp",EDGE,"E320"),sQuery(id+"F0.wireOp",EDGE,"E321"),sQuery(id+"F0.wireOp",EDGE,"E322"),sQuery(id+"F0.wireOp",EDGE,"E323"),sQuery(id+"F0.wireOp",EDGE,"E324"),sQuery(id+"F0.wireOp",EDGE,"E325"),sQuery(id+"F0.wireOp",EDGE,"E326"),sQuery(id+"F0.wireOp",EDGE,"E327"),sQuery(id+"F0.wireOp",EDGE,"E328"),sQuery(id+"F0.wireOp",EDGE,"E329"),sQuery(id+"F0.wireOp",EDGE,"E330"),sQuery(id+"F0.wireOp",EDGE,"E331"),sQuery(id+"F0.wireOp",EDGE,"E332"),sQuery(id+"F0.wireOp",EDGE,"E333"),sQuery(id+"F0.wireOp",EDGE,"E334"),sQuery(id+"F0.wireOp",EDGE,"E335"),sQuery(id+"F0.wireOp",EDGE,"E336"),sQuery(id+"F0.wireOp",EDGE,"E337"),sQuery(id+"F0.wireOp",EDGE,"E338"),sQuery(id+"F0.wireOp",EDGE,"E339"),sQuery(id+"F0.wireOp",EDGE,"E340"),sQuery(id+"F0.wireOp",EDGE,"E341"),sQuery(id+"F0.wireOp",EDGE,"E342"),sQuery(id+"F0.wireOp",EDGE,"E343"),sQuery(id+"F0.wireOp",EDGE,"E344"),sQuery(id+"F0.wireOp",EDGE,"E345"),sQuery(id+"F0.wireOp",EDGE,"E346"),sQuery(id+"F0.wireOp",EDGE,"E347"),sQuery(id+"F0.wireOp",EDGE,"E348"),sQuery(id+"F0.wireOp",EDGE,"E349"),sQuery(id+"F0.wireOp",EDGE,"E350"),sQuery(id+"F0.wireOp",EDGE,"E351"),sQuery(id+"F0.wireOp",EDGE,"E352"),sQuery(id+"F0.wireOp",EDGE,"E353"),sQuery(id+"F0.wireOp",EDGE,"E354"),sQuery(id+"F0.wireOp",EDGE,"E355"),sQuery(id+"F0.wireOp",EDGE,"E356"),sQuery(id+"F0.wireOp",EDGE,"E357"),sQuery(id+"F0.wireOp",EDGE,"E358"),sQuery(id+"F0.wireOp",EDGE,"E359"),sQuery(id+"F0.wireOp",EDGE,"E360"),sQuery(id+"F0.wireOp",EDGE,"E361"),sQuery(id+"F0.wireOp",EDGE,"E362"),sQuery(id+"F0.wireOp",EDGE,"E363"),sQuery(id+"F0.wireOp",EDGE,"E364"),sQuery(id+"F0.wireOp",EDGE,"E365"),sQuery(id+"F0.wireOp",EDGE,"E366"),sQuery(id+"F0.wireOp",EDGE,"E367"),sQuery(id+"F0.wireOp",EDGE,"E368"),sQuery(id+"F0.wireOp",EDGE,"E369"),sQuery(id+"F0.wireOp",EDGE,"E370"),sQuery(id+"F0.wireOp",EDGE,"E371"),sQuery(id+"F0.wireOp",EDGE,"E372"),sQuery(id+"F0.wireOp",EDGE,"E373"),sQuery(id+"F0.wireOp",EDGE,"E374"),sQuery(id+"F0.wireOp",EDGE,"E375"),sQuery(id+"F0.wireOp",EDGE,"E376"),sQuery(id+"F0.wireOp",EDGE,"E377"),sQuery(id+"F0.wireOp",EDGE,"E378"),sQuery(id+"F0.wireOp",EDGE,"E379"),sQuery(id+"F0.wireOp",EDGE,"E380"),sQuery(id+"F0.wireOp",EDGE,"E381"),sQuery(id+"F0.wireOp",EDGE,"E382"),sQuery(id+"F0.wireOp",EDGE,"E383"),sQuery(id+"F0.wireOp",EDGE,"E384"),sQuery(id+"F0.wireOp",EDGE,"E385"),sQuery(id+"F0.wireOp",EDGE,"E386"),sQuery(id+"F0.wireOp",EDGE,"E387"),sQuery(id+"F0.wireOp",EDGE,"E388"),sQuery(id+"F0.wireOp",EDGE,"E389"),sQuery(id+"F0.wireOp",EDGE,"E390"),sQuery(id+"F0.wireOp",EDGE,"E391"),sQuery(id+"F0.wireOp",EDGE,"E392"),sQuery(id+"F0.wireOp",EDGE,"E393"),sQuery(id+"F0.wireOp",EDGE,"E394"),sQuery(id+"F0.wireOp",EDGE,"E395"),sQuery(id+"F0.wireOp",EDGE,"E396"),sQuery(id+"F0.wireOp",EDGE,"E397"),sQuery(id+"F0.wireOp",EDGE,"E398"),sQuery(id+"F0.wireOp",EDGE,"E399"),sQuery(id+"F0.wireOp",EDGE,"E400"),sQuery(id+"F0.wireOp",EDGE,"E401"),sQuery(id+"F0.wireOp",EDGE,"E402"),sQuery(id+"F0.wireOp",EDGE,"E403"),sQuery(id+"F0.wireOp",EDGE,"E404"),sQuery(id+"F0.wireOp",EDGE,"E405"),sQuery(id+"F0.wireOp",EDGE,"E406"),sQuery(id+"F0.wireOp",EDGE,"E407"),sQuery(id+"F0.wireOp",EDGE,"E408"),sQuery(id+"F0.wireOp",EDGE,"E409"),sQuery(id+"F0.wireOp",EDGE,"E410"),sQuery(id+"F0.wireOp",EDGE,"E411"),sQuery(id+"F0.wireOp",EDGE,"E412"),sQuery(id+"F0.wireOp",EDGE,"E413"),sQuery(id+"F0.wireOp",EDGE,"E414"),sQuery(id+"F0.wireOp",EDGE,"E415"),sQuery(id+"F0.wireOp",EDGE,"E416"),sQuery(id+"F0.wireOp",EDGE,"E417"),sQuery(id+"F0.wireOp",EDGE,"E418"),sQuery(id+"F0.wireOp",EDGE,"E419"),sQuery(id+"F0.wireOp",EDGE,"E420"),sQuery(id+"F0.wireOp",EDGE,"E421"),sQuery(id+"F0.wireOp",EDGE,"E422"),sQuery(id+"F0.wireOp",EDGE,"E423"),sQuery(id+"F0.wireOp",EDGE,"E424"),sQuery(id+"F0.wireOp",EDGE,"E425"),sQuery(id+"F0.wireOp",EDGE,"E426"),sQuery(id+"F0.wireOp",EDGE,"E427"),sQuery(id+"F0.wireOp",EDGE,"E428"),sQuery(id+"F0.wireOp",EDGE,"E429"),sQuery(id+"F0.wireOp",EDGE,"E430"),sQuery(id+"F0.wireOp",EDGE,"E431"),sQuery(id+"F0.wireOp",EDGE,"E432"),sQuery(id+"F0.wireOp",EDGE,"E433"),sQuery(id+"F0.wireOp",EDGE,"E434"),sQuery(id+"F0.wireOp",EDGE,"E435"),sQuery(id+"F0.wireOp",EDGE,"E436"),sQuery(id+"F0.wireOp",EDGE,"E437"),sQuery(id+"F0.wireOp",EDGE,"E438"),sQuery(id+"F0.wireOp",EDGE,"E439"),sQuery(id+"F0.wireOp",EDGE,"E440"),sQuery(id+"F0.wireOp",EDGE,"E441"),sQuery(id+"F0.wireOp",EDGE,"E442"),sQuery(id+"F0.wireOp",EDGE,"E443"),sQuery(id+"F0.wireOp",EDGE,"E444"),sQuery(id+"F0.wireOp",EDGE,"E445"),sQuery(id+"F0.wireOp",EDGE,"E446"),sQuery(id+"F0.wireOp",EDGE,"E447"),sQuery(id+"F0.wireOp",EDGE,"E448"),sQuery(id+"F0.wireOp",EDGE,"E449"),sQuery(id+"F0.wireOp",EDGE,"E450"),sQuery(id+"F0.wireOp",EDGE,"E451"),sQuery(id+"F0.wireOp",EDGE,"E452"),sQuery(id+"F0.wireOp",EDGE,"E453"),sQuery(id+"F0.wireOp",EDGE,"E454"),sQuery(id+"F0.wireOp",EDGE,"E455"),sQuery(id+"F0.wireOp",EDGE,"E456"),sQuery(id+"F0.wireOp",EDGE,"E457"),sQuery(id+"F0.wireOp",EDGE,"E458"),sQuery(id+"F0.wireOp",EDGE,"E459"),sQuery(id+"F0.wireOp",EDGE,"E460"),sQuery(id+"F0.wireOp",EDGE,"E461"),sQuery(id+"F0.wireOp",EDGE,"E462"),sQuery(id+"F0.wireOp",EDGE,"E463"),sQuery(id+"F0.wireOp",EDGE,"E464"),sQuery(id+"F0.wireOp",EDGE,"E465"),sQuery(id+"F0.wireOp",EDGE,"E466"),sQuery(id+"F0.wireOp",EDGE,"E467"),sQuery(id+"F0.wireOp",EDGE,"E468"),sQuery(id+"F0.wireOp",EDGE,"E469"),sQuery(id+"F0.wireOp",EDGE,"E470"),sQuery(id+"F0.wireOp",EDGE,"E471"),sQuery(id+"F0.wireOp",EDGE,"E472"),sQuery(id+"F0.wireOp",EDGE,"E473"),sQuery(id+"F0.wireOp",EDGE,"E474"),sQuery(id+"F0.wireOp",EDGE,"E475"),sQuery(id+"F0.wireOp",EDGE,"E476"),sQuery(id+"F0.wireOp",EDGE,"E477"),sQuery(id+"F0.wireOp",EDGE,"E478"),sQuery(id+"F0.wireOp",EDGE,"E479"),sQuery(id+"F0.wireOp",EDGE,"E480"),sQuery(id+"F0.wireOp",EDGE,"E481"),sQuery(id+"F0.wireOp",EDGE,"E482"),sQuery(id+"F0.wireOp",EDGE,"E483"),sQuery(id+"F0.wireOp",EDGE,"E484"),sQuery(id+"F0.wireOp",EDGE,"E485"),sQuery(id+"F0.wireOp",EDGE,"E486"),sQuery(id+"F0.wireOp",EDGE,"E487"),sQuery(id+"F0.wireOp",EDGE,"E488"),sQuery(id+"F0.wireOp",EDGE,"E489"),sQuery(id+"F0.wireOp",EDGE,"E490"),sQuery(id+"F0.wireOp",EDGE,"E491"),sQuery(id+"F0.wireOp",EDGE,"E492"),sQuery(id+"F0.wireOp",EDGE,"E493"),sQuery(id+"F0.wireOp",EDGE,"E494"),sQuery(id+"F0.wireOp",EDGE,"E495"),sQuery(id+"F0.wireOp",EDGE,"E496"),sQuery(id+"F0.wireOp",EDGE,"E497"),sQuery(id+"F0.wireOp",EDGE,"E498"),sQuery(id+"F0.wireOp",EDGE,"E499"),sQuery(id+"F0.wireOp",EDGE,"E500"),sQuery(id+"F0.wireOp",EDGE,"E501"),sQuery(id+"F0.wireOp",EDGE,"E502"),sQuery(id+"F0.wireOp",EDGE,"E503"),sQuery(id+"F0.wireOp",EDGE,"E504"),sQuery(id+"F0.wireOp",EDGE,"E505"),sQuery(id+"F0.wireOp",EDGE,"E506"),sQuery(id+"F0.wireOp",EDGE,"E507"),sQuery(id+"F0.wireOp",EDGE,"E508"),sQuery(id+"F0.wireOp",EDGE,"E509"),sQuery(id+"F0.wireOp",EDGE,"E510"),sQuery(id+"F0.wireOp",EDGE,"E511"),sQuery(id+"F0.wireOp",EDGE,"E512"),sQuery(id+"F0.wireOp",EDGE,"E513"),sQuery(id+"F0.wireOp",EDGE,"E514"),sQuery(id+"F0.wireOp",EDGE,"E515"),sQuery(id+"F0.wireOp",EDGE,"E516"),sQuery(id+"F0.wireOp",EDGE,"E517"),sQuery(id+"F0.wireOp",EDGE,"E518"),sQuery(id+"F0.wireOp",EDGE,"E519"),sQuery(id+"F0.wireOp",EDGE,"E520"),sQuery(id+"F0.wireOp",EDGE,"E521"),sQuery(id+"F0.wireOp",EDGE,"E522"),sQuery(id+"F0.wireOp",EDGE,"E523"),sQuery(id+"F0.wireOp",EDGE,"E524"),sQuery(id+"F0.wireOp",EDGE,"E525"),sQuery(id+"F0.wireOp",EDGE,"E526"),sQuery(id+"F0.wireOp",EDGE,"E527"),sQuery(id+"F0.wireOp",EDGE,"E528"),sQuery(id+"F0.wireOp",EDGE,"E529"),sQuery(id+"F0.wireOp",EDGE,"E530"),sQuery(id+"F0.wireOp",EDGE,"E531"),sQuery(id+"F0.wireOp",EDGE,"E532"),sQuery(id+"F0.wireOp",EDGE,"E533"),sQuery(id+"F0.wireOp",EDGE,"E534"),sQuery(id+"F0.wireOp",EDGE,"E535"),sQuery(id+"F0.wireOp",EDGE,"E536"),sQuery(id+"F0.wireOp",EDGE,"E537"),sQuery(id+"F0.wireOp",EDGE,"E538"),sQuery(id+"F0.wireOp",EDGE,"E539"),sQuery(id+"F0.wireOp",EDGE,"E540"),sQuery(id+"F0.wireOp",EDGE,"E541"),sQuery(id+"F0.wireOp",EDGE,"E542"),sQuery(id+"F0.wireOp",EDGE,"E543"),sQuery(id+"F0.wireOp",EDGE,"E544"),sQuery(id+"F0.wireOp",EDGE,"E545"),sQuery(id+"F0.wireOp",EDGE,"E546"),sQuery(id+"F0.wireOp",EDGE,"E547"),sQuery(id+"F0.wireOp",EDGE,"E548"),sQuery(id+"F0.wireOp",EDGE,"E549"),sQuery(id+"F0.wireOp",EDGE,"E550"),sQuery(id+"F0.wireOp",EDGE,"E551"),sQuery(id+"F0.wireOp",EDGE,"E552"),sQuery(id+"F0.wireOp",EDGE,"E553"),sQuery(id+"F0.wireOp",EDGE,"E554"),sQuery(id+"F0.wireOp",EDGE,"E555"),sQuery(id+"F0.wireOp",EDGE,"E556"),sQuery(id+"F0.wireOp",EDGE,"E557"),sQuery(id+"F0.wireOp",EDGE,"E558"),sQuery(id+"F0.wireOp",EDGE,"E559"),sQuery(id+"F0.wireOp",EDGE,"E560"),sQuery(id+"F0.wireOp",EDGE,"E561"),sQuery(id+"F0.wireOp",EDGE,"E562"),sQuery(id+"F0.wireOp",EDGE,"E563"),sQuery(id+"F0.wireOp",EDGE,"E564"),sQuery(id+"F0.wireOp",EDGE,"E565"),sQuery(id+"F0.wireOp",EDGE,"E566"),sQuery(id+"F0.wireOp",EDGE,"E567"),sQuery(id+"F0.wireOp",EDGE,"E568"),sQuery(id+"F0.wireOp",EDGE,"E569"),sQuery(id+"F0.wireOp",EDGE,"E570"),sQuery(id+"F0.wireOp",EDGE,"E571"),sQuery(id+"F0.wireOp",EDGE,"E572"),sQuery(id+"F0.wireOp",EDGE,"E573"),sQuery(id+"F0.wireOp",EDGE,"E574"),sQuery(id+"F0.wireOp",EDGE,"E575"),sQuery(id+"F0.wireOp",EDGE,"E576"),sQuery(id+"F0.wireOp",EDGE,"E577"),sQuery(id+"F0.wireOp",EDGE,"E1140"),sQuery(id+"F0.wireOp",EDGE,"E1143")])],"isStart":false});
            var sketch = newSketch(context, id + "F8", { "sketchPlane" : qUnion([Q0])});
            skLineSegment(sketch, "E2031.0", {"start": v(62, 4.2) * mm, "end": v(62, -5.84) * mm});
            skLineSegment(sketch, "E2032.0", {"start": v(62, 4.2) * mm, "end": v(61.02, 4.3) * mm});
            skLineSegment(sketch, "E2033.0", {"start": v(61.02, 4.3) * mm, "end": v(58.73, 4.55) * mm});
            skLineSegment(sketch, "E2034.0", {"start": v(61.79, -5.85) * mm, "end": v(62, -5.84) * mm});
            skLineSegment(sketch, "E2035.0", {"start": v(60.6, -5.9) * mm, "end": v(61.79, -5.85) * mm});
            skLineSegment(sketch, "E2036", {"start": v(58.73, 4.55) * mm, "end": v(60.6, -5.9) * mm});
            skSolve(sketch);
        }
        {
            var Q0;
            Q0 = qSketchRegion(id + "F8", true);
            var Q1;
            Q1=makeQuery(id+"F3.opExtrude","CAP_FACE",FACE,{"disambiguationData":[OSD([sQuery(id+"F2.wireOp",EDGE,"E1146"),sQuery(id+"F2.wireOp",EDGE,"E1147"),sQuery(id+"F2.wireOp",EDGE,"E1148"),sQuery(id+"F2.wireOp",EDGE,"E1149"),sQuery(id+"F2.wireOp",EDGE,"E1150"),sQuery(id+"F2.wireOp",EDGE,"E1151"),sQuery(id+"F2.wireOp",EDGE,"E1152"),sQuery(id+"F2.wireOp",EDGE,"E1153"),sQuery(id+"F2.wireOp",EDGE,"E1154"),sQuery(id+"F2.wireOp",EDGE,"E1155"),sQuery(id+"F2.wireOp",EDGE,"E1156"),sQuery(id+"F2.wireOp",EDGE,"E1157"),sQuery(id+"F2.wireOp",EDGE,"E1158"),sQuery(id+"F2.wireOp",EDGE,"E1159"),sQuery(id+"F2.wireOp",EDGE,"E1160"),sQuery(id+"F2.wireOp",EDGE,"E1161"),sQuery(id+"F2.wireOp",EDGE,"E1162"),sQuery(id+"F2.wireOp",EDGE,"E1163"),sQuery(id+"F2.wireOp",EDGE,"E1164"),sQuery(id+"F2.wireOp",EDGE,"E1165"),sQuery(id+"F2.wireOp",EDGE,"E1166"),sQuery(id+"F2.wireOp",EDGE,"E1167"),sQuery(id+"F2.wireOp",EDGE,"E1168"),sQuery(id+"F2.wireOp",EDGE,"E1169"),sQuery(id+"F2.wireOp",EDGE,"E1170"),sQuery(id+"F2.wireOp",EDGE,"E1171"),sQuery(id+"F2.wireOp",EDGE,"E1172"),sQuery(id+"F2.wireOp",EDGE,"E1173"),sQuery(id+"F2.wireOp",EDGE,"E1174"),sQuery(id+"F2.wireOp",EDGE,"E1175"),sQuery(id+"F2.wireOp",EDGE,"E1176"),sQuery(id+"F2.wireOp",EDGE,"E1177"),sQuery(id+"F2.wireOp",EDGE,"E1178"),sQuery(id+"F2.wireOp",EDGE,"E1179"),sQuery(id+"F2.wireOp",EDGE,"E1180"),sQuery(id+"F2.wireOp",EDGE,"E1181"),sQuery(id+"F2.wireOp",EDGE,"E1182"),sQuery(id+"F2.wireOp",EDGE,"E1183"),sQuery(id+"F2.wireOp",EDGE,"E1184"),sQuery(id+"F2.wireOp",EDGE,"E1185"),sQuery(id+"F2.wireOp",EDGE,"E1186"),sQuery(id+"F2.wireOp",EDGE,"E1187"),sQuery(id+"F2.wireOp",EDGE,"E1188"),sQuery(id+"F2.wireOp",EDGE,"E1189"),sQuery(id+"F2.wireOp",EDGE,"E1190"),sQuery(id+"F2.wireOp",EDGE,"E1191"),sQuery(id+"F2.wireOp",EDGE,"E1192"),sQuery(id+"F2.wireOp",EDGE,"E1193"),sQuery(id+"F2.wireOp",EDGE,"E1194"),sQuery(id+"F2.wireOp",EDGE,"E1195"),sQuery(id+"F2.wireOp",EDGE,"E1196"),sQuery(id+"F2.wireOp",EDGE,"E1197"),sQuery(id+"F2.wireOp",EDGE,"E1198"),sQuery(id+"F2.wireOp",EDGE,"E1199"),sQuery(id+"F2.wireOp",EDGE,"E1200"),sQuery(id+"F2.wireOp",EDGE,"E1201"),sQuery(id+"F2.wireOp",EDGE,"E1202"),sQuery(id+"F2.wireOp",EDGE,"E1203"),sQuery(id+"F2.wireOp",EDGE,"E1204"),sQuery(id+"F2.wireOp",EDGE,"E1205"),sQuery(id+"F2.wireOp",EDGE,"E1206"),sQuery(id+"F2.wireOp",EDGE,"E1207"),sQuery(id+"F2.wireOp",EDGE,"E1208"),sQuery(id+"F2.wireOp",EDGE,"E1209"),sQuery(id+"F2.wireOp",EDGE,"E1210"),sQuery(id+"F2.wireOp",EDGE,"E1211"),sQuery(id+"F2.wireOp",EDGE,"E1212"),sQuery(id+"F2.wireOp",EDGE,"E1213"),sQuery(id+"F2.wireOp",EDGE,"E1214"),sQuery(id+"F2.wireOp",EDGE,"E1215"),sQuery(id+"F2.wireOp",EDGE,"E1216"),sQuery(id+"F2.wireOp",EDGE,"E1217"),sQuery(id+"F2.wireOp",EDGE,"E1218"),sQuery(id+"F2.wireOp",EDGE,"E1219"),sQuery(id+"F2.wireOp",EDGE,"E1220"),sQuery(id+"F2.wireOp",EDGE,"E1221"),sQuery(id+"F2.wireOp",EDGE,"E1222"),sQuery(id+"F2.wireOp",EDGE,"E1223"),sQuery(id+"F2.wireOp",EDGE,"E1224"),sQuery(id+"F2.wireOp",EDGE,"E1225"),sQuery(id+"F2.wireOp",EDGE,"E1226"),sQuery(id+"F2.wireOp",EDGE,"E1227"),sQuery(id+"F2.wireOp",EDGE,"E1228"),sQuery(id+"F2.wireOp",EDGE,"E1229"),sQuery(id+"F2.wireOp",EDGE,"E1230"),sQuery(id+"F2.wireOp",EDGE,"E1231"),sQuery(id+"F2.wireOp",EDGE,"E1232"),sQuery(id+"F2.wireOp",EDGE,"E1233"),sQuery(id+"F2.wireOp",EDGE,"E1234"),sQuery(id+"F2.wireOp",EDGE,"E1235"),sQuery(id+"F2.wireOp",EDGE,"E1236"),sQuery(id+"F2.wireOp",EDGE,"E1237"),sQuery(id+"F2.wireOp",EDGE,"E1238"),sQuery(id+"F2.wireOp",EDGE,"E1239"),sQuery(id+"F2.wireOp",EDGE,"E1240"),sQuery(id+"F2.wireOp",EDGE,"E1241"),sQuery(id+"F2.wireOp",EDGE,"E1242"),sQuery(id+"F2.wireOp",EDGE,"E1243"),sQuery(id+"F2.wireOp",EDGE,"E1244"),sQuery(id+"F2.wireOp",EDGE,"E1245"),sQuery(id+"F2.wireOp",EDGE,"E1246"),sQuery(id+"F2.wireOp",EDGE,"E1247"),sQuery(id+"F2.wireOp",EDGE,"E1248"),sQuery(id+"F2.wireOp",EDGE,"E1249"),sQuery(id+"F2.wireOp",EDGE,"E1250"),sQuery(id+"F2.wireOp",EDGE,"E1251"),sQuery(id+"F2.wireOp",EDGE,"E1252"),sQuery(id+"F2.wireOp",EDGE,"E1253"),sQuery(id+"F2.wireOp",EDGE,"E1254"),sQuery(id+"F2.wireOp",EDGE,"E1255"),sQuery(id+"F2.wireOp",EDGE,"E1256"),sQuery(id+"F2.wireOp",EDGE,"E1257"),sQuery(id+"F2.wireOp",EDGE,"E1258"),sQuery(id+"F2.wireOp",EDGE,"E1259"),sQuery(id+"F2.wireOp",EDGE,"E1260"),sQuery(id+"F2.wireOp",EDGE,"E1261"),sQuery(id+"F2.wireOp",EDGE,"E1262"),sQuery(id+"F2.wireOp",EDGE,"E1263"),sQuery(id+"F2.wireOp",EDGE,"E1264"),sQuery(id+"F2.wireOp",EDGE,"E1265"),sQuery(id+"F2.wireOp",EDGE,"E1266"),sQuery(id+"F2.wireOp",EDGE,"E1267"),sQuery(id+"F2.wireOp",EDGE,"E1268"),sQuery(id+"F2.wireOp",EDGE,"E1269"),sQuery(id+"F2.wireOp",EDGE,"E1270"),sQuery(id+"F2.wireOp",EDGE,"E1271"),sQuery(id+"F2.wireOp",EDGE,"E1272"),sQuery(id+"F2.wireOp",EDGE,"E1273"),sQuery(id+"F2.wireOp",EDGE,"E1274"),sQuery(id+"F2.wireOp",EDGE,"E1275"),sQuery(id+"F2.wireOp",EDGE,"E1276"),sQuery(id+"F2.wireOp",EDGE,"E1277"),sQuery(id+"F2.wireOp",EDGE,"E1278"),sQuery(id+"F2.wireOp",EDGE,"E1279"),sQuery(id+"F2.wireOp",EDGE,"E1280"),sQuery(id+"F2.wireOp",EDGE,"E1281"),sQuery(id+"F2.wireOp",EDGE,"E1282"),sQuery(id+"F2.wireOp",EDGE,"E1283"),sQuery(id+"F2.wireOp",EDGE,"E1284"),sQuery(id+"F2.wireOp",EDGE,"E1285"),sQuery(id+"F2.wireOp",EDGE,"E1286"),sQuery(id+"F2.wireOp",EDGE,"E1287"),sQuery(id+"F2.wireOp",EDGE,"E1288"),sQuery(id+"F2.wireOp",EDGE,"E1289"),sQuery(id+"F2.wireOp",EDGE,"E1290"),sQuery(id+"F2.wireOp",EDGE,"E1291"),sQuery(id+"F2.wireOp",EDGE,"E1292"),sQuery(id+"F2.wireOp",EDGE,"E1293"),sQuery(id+"F2.wireOp",EDGE,"E1294"),sQuery(id+"F2.wireOp",EDGE,"E1295"),sQuery(id+"F2.wireOp",EDGE,"E1296"),sQuery(id+"F2.wireOp",EDGE,"E1297"),sQuery(id+"F2.wireOp",EDGE,"E1298"),sQuery(id+"F2.wireOp",EDGE,"E1299"),sQuery(id+"F2.wireOp",EDGE,"E1300"),sQuery(id+"F2.wireOp",EDGE,"E1301"),sQuery(id+"F2.wireOp",EDGE,"E1302"),sQuery(id+"F2.wireOp",EDGE,"E1303"),sQuery(id+"F2.wireOp",EDGE,"E1304"),sQuery(id+"F2.wireOp",EDGE,"E1305"),sQuery(id+"F2.wireOp",EDGE,"E1306"),sQuery(id+"F2.wireOp",EDGE,"E1460"),sQuery(id+"F2.wireOp",EDGE,"E1461"),sQuery(id+"F2.wireOp",EDGE,"E1462"),sQuery(id+"F2.wireOp",EDGE,"E1463"),sQuery(id+"F2.wireOp",EDGE,"E1464"),sQuery(id+"F2.wireOp",EDGE,"E1465"),sQuery(id+"F2.wireOp",EDGE,"E1466"),sQuery(id+"F2.wireOp",EDGE,"E1467"),sQuery(id+"F2.wireOp",EDGE,"E1468"),sQuery(id+"F2.wireOp",EDGE,"E1469"),sQuery(id+"F2.wireOp",EDGE,"E1470"),sQuery(id+"F2.wireOp",EDGE,"E1471"),sQuery(id+"F2.wireOp",EDGE,"E1472"),sQuery(id+"F2.wireOp",EDGE,"E1473"),sQuery(id+"F2.wireOp",EDGE,"E1474"),sQuery(id+"F2.wireOp",EDGE,"E1475"),sQuery(id+"F2.wireOp",EDGE,"E1476"),sQuery(id+"F2.wireOp",EDGE,"E1477"),sQuery(id+"F2.wireOp",EDGE,"E1478"),sQuery(id+"F2.wireOp",EDGE,"E1479"),sQuery(id+"F2.wireOp",EDGE,"E1480"),sQuery(id+"F2.wireOp",EDGE,"E1481"),sQuery(id+"F2.wireOp",EDGE,"E1482"),sQuery(id+"F2.wireOp",EDGE,"E1483"),sQuery(id+"F2.wireOp",EDGE,"E1484"),sQuery(id+"F2.wireOp",EDGE,"E1485"),sQuery(id+"F2.wireOp",EDGE,"E1486"),sQuery(id+"F2.wireOp",EDGE,"E1487"),sQuery(id+"F2.wireOp",EDGE,"E1488"),sQuery(id+"F2.wireOp",EDGE,"E1489"),sQuery(id+"F2.wireOp",EDGE,"E1490"),sQuery(id+"F2.wireOp",EDGE,"E1491"),sQuery(id+"F2.wireOp",EDGE,"E1492"),sQuery(id+"F2.wireOp",EDGE,"E1493"),sQuery(id+"F2.wireOp",EDGE,"E1494"),sQuery(id+"F2.wireOp",EDGE,"E1495"),sQuery(id+"F2.wireOp",EDGE,"E1496"),sQuery(id+"F2.wireOp",EDGE,"E1497"),sQuery(id+"F2.wireOp",EDGE,"E1498"),sQuery(id+"F2.wireOp",EDGE,"E1499"),sQuery(id+"F2.wireOp",EDGE,"E1500"),sQuery(id+"F2.wireOp",EDGE,"E1501"),sQuery(id+"F2.wireOp",EDGE,"E1502"),sQuery(id+"F2.wireOp",EDGE,"E1503"),sQuery(id+"F2.wireOp",EDGE,"E1504"),sQuery(id+"F2.wireOp",EDGE,"E1505"),sQuery(id+"F2.wireOp",EDGE,"E1506"),sQuery(id+"F2.wireOp",EDGE,"E1507"),sQuery(id+"F2.wireOp",EDGE,"E1508"),sQuery(id+"F2.wireOp",EDGE,"E1509"),sQuery(id+"F2.wireOp",EDGE,"E1510"),sQuery(id+"F2.wireOp",EDGE,"E1511"),sQuery(id+"F2.wireOp",EDGE,"E1512"),sQuery(id+"F2.wireOp",EDGE,"E1513"),sQuery(id+"F2.wireOp",EDGE,"E1514"),sQuery(id+"F2.wireOp",EDGE,"E1515"),sQuery(id+"F2.wireOp",EDGE,"E1516"),sQuery(id+"F2.wireOp",EDGE,"E1517"),sQuery(id+"F2.wireOp",EDGE,"E1518"),sQuery(id+"F2.wireOp",EDGE,"E1519"),sQuery(id+"F2.wireOp",EDGE,"E1520"),sQuery(id+"F2.wireOp",EDGE,"E1521"),sQuery(id+"F2.wireOp",EDGE,"E1522"),sQuery(id+"F2.wireOp",EDGE,"E1523"),sQuery(id+"F2.wireOp",EDGE,"E1524"),sQuery(id+"F2.wireOp",EDGE,"E1525"),sQuery(id+"F2.wireOp",EDGE,"E1526"),sQuery(id+"F2.wireOp",EDGE,"E1527"),sQuery(id+"F2.wireOp",EDGE,"E1528"),sQuery(id+"F2.wireOp",EDGE,"E1529"),sQuery(id+"F2.wireOp",EDGE,"E1530"),sQuery(id+"F2.wireOp",EDGE,"E1531"),sQuery(id+"F2.wireOp",EDGE,"E1532"),sQuery(id+"F2.wireOp",EDGE,"E1533"),sQuery(id+"F2.wireOp",EDGE,"E1534"),sQuery(id+"F2.wireOp",EDGE,"E1535"),sQuery(id+"F2.wireOp",EDGE,"E1536"),sQuery(id+"F2.wireOp",EDGE,"E1537"),sQuery(id+"F2.wireOp",EDGE,"E1538"),sQuery(id+"F2.wireOp",EDGE,"E1539"),sQuery(id+"F2.wireOp",EDGE,"E1540"),sQuery(id+"F2.wireOp",EDGE,"E1541"),sQuery(id+"F2.wireOp",EDGE,"E1542"),sQuery(id+"F2.wireOp",EDGE,"E1543"),sQuery(id+"F2.wireOp",EDGE,"E1544"),sQuery(id+"F2.wireOp",EDGE,"E1545"),sQuery(id+"F2.wireOp",EDGE,"E1546"),sQuery(id+"F2.wireOp",EDGE,"E1547"),sQuery(id+"F2.wireOp",EDGE,"E1548"),sQuery(id+"F2.wireOp",EDGE,"E1549"),sQuery(id+"F2.wireOp",EDGE,"E1550"),sQuery(id+"F2.wireOp",EDGE,"E1551"),sQuery(id+"F2.wireOp",EDGE,"E1552"),sQuery(id+"F2.wireOp",EDGE,"E1553"),sQuery(id+"F2.wireOp",EDGE,"E1554"),sQuery(id+"F2.wireOp",EDGE,"E1555"),sQuery(id+"F2.wireOp",EDGE,"E1556"),sQuery(id+"F2.wireOp",EDGE,"E1557"),sQuery(id+"F2.wireOp",EDGE,"E1558"),sQuery(id+"F2.wireOp",EDGE,"E1559"),sQuery(id+"F2.wireOp",EDGE,"E1560"),sQuery(id+"F2.wireOp",EDGE,"E1561"),sQuery(id+"F2.wireOp",EDGE,"E1562"),sQuery(id+"F2.wireOp",EDGE,"E1563"),sQuery(id+"F2.wireOp",EDGE,"E1564"),sQuery(id+"F2.wireOp",EDGE,"E1565"),sQuery(id+"F2.wireOp",EDGE,"E1566"),sQuery(id+"F2.wireOp",EDGE,"E1567"),sQuery(id+"F2.wireOp",EDGE,"E1568"),sQuery(id+"F2.wireOp",EDGE,"E1569"),sQuery(id+"F2.wireOp",EDGE,"E1570"),sQuery(id+"F2.wireOp",EDGE,"E1571"),sQuery(id+"F2.wireOp",EDGE,"E1572"),sQuery(id+"F2.wireOp",EDGE,"E1573"),sQuery(id+"F2.wireOp",EDGE,"E1574"),sQuery(id+"F2.wireOp",EDGE,"E1575"),sQuery(id+"F2.wireOp",EDGE,"E1576"),sQuery(id+"F2.wireOp",EDGE,"E1577"),sQuery(id+"F2.wireOp",EDGE,"E1578"),sQuery(id+"F2.wireOp",EDGE,"E1579"),sQuery(id+"F2.wireOp",EDGE,"E1580"),sQuery(id+"F2.wireOp",EDGE,"E1581"),sQuery(id+"F2.wireOp",EDGE,"E1582"),sQuery(id+"F2.wireOp",EDGE,"E1583"),sQuery(id+"F2.wireOp",EDGE,"E1584"),sQuery(id+"F2.wireOp",EDGE,"E1585"),sQuery(id+"F2.wireOp",EDGE,"E1586"),sQuery(id+"F2.wireOp",EDGE,"E1587"),sQuery(id+"F2.wireOp",EDGE,"E1588"),sQuery(id+"F2.wireOp",EDGE,"E1589"),sQuery(id+"F2.wireOp",EDGE,"E1590"),sQuery(id+"F2.wireOp",EDGE,"E1591"),sQuery(id+"F2.wireOp",EDGE,"E1592"),sQuery(id+"F2.wireOp",EDGE,"E1593"),sQuery(id+"F2.wireOp",EDGE,"E1594"),sQuery(id+"F2.wireOp",EDGE,"E1595"),sQuery(id+"F2.wireOp",EDGE,"E1596"),sQuery(id+"F2.wireOp",EDGE,"E1597"),sQuery(id+"F2.wireOp",EDGE,"E1598"),sQuery(id+"F2.wireOp",EDGE,"E1599"),sQuery(id+"F2.wireOp",EDGE,"E1600"),sQuery(id+"F2.wireOp",EDGE,"E1601"),sQuery(id+"F2.wireOp",EDGE,"E1602"),sQuery(id+"F2.wireOp",EDGE,"E1603"),sQuery(id+"F2.wireOp",EDGE,"E1604"),sQuery(id+"F2.wireOp",EDGE,"E1605"),sQuery(id+"F2.wireOp",EDGE,"E1606"),sQuery(id+"F2.wireOp",EDGE,"E1607"),sQuery(id+"F2.wireOp",EDGE,"E1608"),sQuery(id+"F2.wireOp",EDGE,"E1609"),sQuery(id+"F2.wireOp",EDGE,"E1610"),sQuery(id+"F2.wireOp",EDGE,"E1611"),sQuery(id+"F2.wireOp",EDGE,"E1612"),sQuery(id+"F2.wireOp",EDGE,"E1613"),sQuery(id+"F2.wireOp",EDGE,"E1614"),sQuery(id+"F2.wireOp",EDGE,"E1615"),sQuery(id+"F2.wireOp",EDGE,"E1616"),sQuery(id+"F2.wireOp",EDGE,"E1617"),sQuery(id+"F2.wireOp",EDGE,"E1618"),sQuery(id+"F2.wireOp",EDGE,"E1619"),sQuery(id+"F2.wireOp",EDGE,"E1620"),sQuery(id+"F2.wireOp",EDGE,"E1621"),sQuery(id+"F2.wireOp",EDGE,"E1622"),sQuery(id+"F2.wireOp",EDGE,"E1623"),sQuery(id+"F2.wireOp",EDGE,"E1624"),sQuery(id+"F2.wireOp",EDGE,"E1625"),sQuery(id+"F2.wireOp",EDGE,"E1626"),sQuery(id+"F2.wireOp",EDGE,"E1627"),sQuery(id+"F2.wireOp",EDGE,"E1628"),sQuery(id+"F2.wireOp",EDGE,"E1629"),sQuery(id+"F2.wireOp",EDGE,"E1630"),sQuery(id+"F2.wireOp",EDGE,"E1631"),sQuery(id+"F2.wireOp",EDGE,"E1632"),sQuery(id+"F2.wireOp",EDGE,"E1633"),sQuery(id+"F2.wireOp",EDGE,"E1634"),sQuery(id+"F2.wireOp",EDGE,"E1635"),sQuery(id+"F2.wireOp",EDGE,"E1636"),sQuery(id+"F2.wireOp",EDGE,"E1637"),sQuery(id+"F2.wireOp",EDGE,"E1638"),sQuery(id+"F2.wireOp",EDGE,"E1639"),sQuery(id+"F2.wireOp",EDGE,"E1640"),sQuery(id+"F2.wireOp",EDGE,"E1641"),sQuery(id+"F2.wireOp",EDGE,"E1642"),sQuery(id+"F2.wireOp",EDGE,"E1643"),sQuery(id+"F2.wireOp",EDGE,"E1644"),sQuery(id+"F2.wireOp",EDGE,"E1645"),sQuery(id+"F2.wireOp",EDGE,"E1646"),sQuery(id+"F2.wireOp",EDGE,"E1647"),sQuery(id+"F2.wireOp",EDGE,"E1648"),sQuery(id+"F2.wireOp",EDGE,"E1649"),sQuery(id+"F2.wireOp",EDGE,"E1650"),sQuery(id+"F2.wireOp",EDGE,"E1651"),sQuery(id+"F2.wireOp",EDGE,"E1652"),sQuery(id+"F2.wireOp",EDGE,"E1653"),sQuery(id+"F2.wireOp",EDGE,"E1654"),sQuery(id+"F2.wireOp",EDGE,"E1655"),sQuery(id+"F2.wireOp",EDGE,"E1656"),sQuery(id+"F2.wireOp",EDGE,"E1657"),sQuery(id+"F2.wireOp",EDGE,"E1658"),sQuery(id+"F2.wireOp",EDGE,"E1659"),sQuery(id+"F2.wireOp",EDGE,"E1660"),sQuery(id+"F2.wireOp",EDGE,"E1661"),sQuery(id+"F2.wireOp",EDGE,"E1662"),sQuery(id+"F2.wireOp",EDGE,"E1663"),sQuery(id+"F2.wireOp",EDGE,"E1664"),sQuery(id+"F2.wireOp",EDGE,"E1665"),sQuery(id+"F2.wireOp",EDGE,"E1666"),sQuery(id+"F2.wireOp",EDGE,"E1667"),sQuery(id+"F2.wireOp",EDGE,"E1668"),sQuery(id+"F2.wireOp",EDGE,"E1669"),sQuery(id+"F2.wireOp",EDGE,"E1670"),sQuery(id+"F2.wireOp",EDGE,"E1671"),sQuery(id+"F2.wireOp",EDGE,"E1672"),sQuery(id+"F2.wireOp",EDGE,"E1673"),sQuery(id+"F2.wireOp",EDGE,"E1674"),sQuery(id+"F2.wireOp",EDGE,"E1675"),sQuery(id+"F2.wireOp",EDGE,"E1676"),sQuery(id+"F2.wireOp",EDGE,"E1677"),sQuery(id+"F2.wireOp",EDGE,"E1678"),sQuery(id+"F2.wireOp",EDGE,"E1679"),sQuery(id+"F2.wireOp",EDGE,"E1680"),sQuery(id+"F2.wireOp",EDGE,"E1681"),sQuery(id+"F2.wireOp",EDGE,"E1682"),sQuery(id+"F2.wireOp",EDGE,"E1683"),sQuery(id+"F2.wireOp",EDGE,"E1684"),sQuery(id+"F2.wireOp",EDGE,"E1685"),sQuery(id+"F2.wireOp",EDGE,"E1686"),sQuery(id+"F2.wireOp",EDGE,"E1687"),sQuery(id+"F2.wireOp",EDGE,"E1688"),sQuery(id+"F2.wireOp",EDGE,"E1689"),sQuery(id+"F2.wireOp",EDGE,"E1690"),sQuery(id+"F2.wireOp",EDGE,"E1691"),sQuery(id+"F2.wireOp",EDGE,"E1692"),sQuery(id+"F2.wireOp",EDGE,"E1693"),sQuery(id+"F2.wireOp",EDGE,"E1694"),sQuery(id+"F2.wireOp",EDGE,"E1695"),sQuery(id+"F2.wireOp",EDGE,"E1696"),sQuery(id+"F2.wireOp",EDGE,"E1697"),sQuery(id+"F2.wireOp",EDGE,"E1698"),sQuery(id+"F2.wireOp",EDGE,"E1699"),sQuery(id+"F2.wireOp",EDGE,"E1700"),sQuery(id+"F2.wireOp",EDGE,"E1701"),sQuery(id+"F2.wireOp",EDGE,"E1702"),sQuery(id+"F2.wireOp",EDGE,"E1703"),sQuery(id+"F2.wireOp",EDGE,"E1704"),sQuery(id+"F2.wireOp",EDGE,"E1705"),sQuery(id+"F2.wireOp",EDGE,"E1706"),sQuery(id+"F2.wireOp",EDGE,"E1707"),sQuery(id+"F2.wireOp",EDGE,"E1708"),sQuery(id+"F2.wireOp",EDGE,"E1709"),sQuery(id+"F2.wireOp",EDGE,"E1710"),sQuery(id+"F2.wireOp",EDGE,"E1711"),sQuery(id+"F2.wireOp",EDGE,"E1712"),sQuery(id+"F2.wireOp",EDGE,"E1713"),sQuery(id+"F2.wireOp",EDGE,"E1714"),sQuery(id+"F2.wireOp",EDGE,"E1715"),sQuery(id+"F2.wireOp",EDGE,"E1716"),sQuery(id+"F2.wireOp",EDGE,"E1717"),sQuery(id+"F2.wireOp",EDGE,"E1718"),sQuery(id+"F2.wireOp",EDGE,"E1719"),sQuery(id+"F2.wireOp",EDGE,"E1720"),sQuery(id+"F2.wireOp",EDGE,"E1721"),sQuery(id+"F2.wireOp",EDGE,"E1722"),sQuery(id+"F2.wireOp",EDGE,"E1723"),sQuery(id+"F2.wireOp",EDGE,"E1724"),sQuery(id+"F2.wireOp",EDGE,"E1725"),sQuery(id+"F2.wireOp",EDGE,"E1726"),sQuery(id+"F2.wireOp",EDGE,"E1727"),sQuery(id+"F2.wireOp",EDGE,"E1728"),sQuery(id+"F2.wireOp",EDGE,"E1729"),sQuery(id+"F2.wireOp",EDGE,"E1730"),sQuery(id+"F2.wireOp",EDGE,"E1731"),sQuery(id+"F2.wireOp",EDGE,"E1732"),sQuery(id+"F2.wireOp",EDGE,"E1733"),sQuery(id+"F2.wireOp",EDGE,"E1734"),sQuery(id+"F2.wireOp",EDGE,"E1735"),sQuery(id+"F2.wireOp",EDGE,"E1736"),sQuery(id+"F2.wireOp",EDGE,"E1737"),sQuery(id+"F2.wireOp",EDGE,"E1738"),sQuery(id+"F2.wireOp",EDGE,"E1739"),sQuery(id+"F2.wireOp",EDGE,"E1740"),sQuery(id+"F2.wireOp",EDGE,"E1741"),sQuery(id+"F2.wireOp",EDGE,"E2023")])],"isStart":false});
            extrude(context, id + "F9", {"entities" : qUnion([Q0]), "operationType" : NewBodyOperationType.ADD, "endBound" : BoundingType.UP_TO_SURFACE, "depth" : 25 * mm, "endBoundEntityFace" : qUnion([Q1]), "offsetDistance" : 25 * mm});
        }
        {
            var Q0;
            Q0=makeQuery(id+"F3.opExtrude","SWEPT_FACE",FACE,{"disambiguationData":[OSD([sQuery(id+"F2.wireOp",EDGE,"E2023")])]});
            var Q1;
            Q1=makeQuery(id+"F1.opExtrude","CAP_EDGE",EDGE,{"disambiguationData":[OSD([sQuery(id+"F0.wireOp",EDGE,"E254")])],"isStart":false});
            sweep(context, id + "F10", {"operationType" : NewBodyOperationType.ADD, "profiles" : qUnion([Q0]), "path" : qUnion([Q1])});
        }
        {
            var Q0;
            {var subQ0=sQuery(id+"F0.wireOp",EDGE,"E341");var subQ1=sQuery(id+"F0.wireOp",EDGE,"E340");var subQ4=sQuery(id+"F0.wireOp",EDGE,"E1143");var subQ5=sQuery(id+"F0.wireOp",EDGE,"E1140");var subQ6=sQuery(id+"F0.wireOp",EDGE,"E577");var subQ7=sQuery(id+"F0.wireOp",EDGE,"E576");var subQ8=sQuery(id+"F0.wireOp",EDGE,"E575");var subQ9=sQuery(id+"F0.wireOp",EDGE,"E574");var subQ10=sQuery(id+"F0.wireOp",EDGE,"E573");var subQ11=sQuery(id+"F0.wireOp",EDGE,"E572");var subQ12=sQuery(id+"F0.wireOp",EDGE,"E571");var subQ13=sQuery(id+"F0.wireOp",EDGE,"E570");var subQ14=sQuery(id+"F0.wireOp",EDGE,"E569");var subQ15=sQuery(id+"F0.wireOp",EDGE,"E568");var subQ16=sQuery(id+"F0.wireOp",EDGE,"E567");var subQ17=sQuery(id+"F0.wireOp",EDGE,"E566");var subQ18=sQuery(id+"F0.wireOp",EDGE,"E565");var subQ19=sQuery(id+"F0.wireOp",EDGE,"E564");var subQ20=sQuery(id+"F0.wireOp",EDGE,"E563");var subQ21=sQuery(id+"F0.wireOp",EDGE,"E562");var subQ22=sQuery(id+"F0.wireOp",EDGE,"E561");var subQ23=sQuery(id+"F0.wireOp",EDGE,"E560");var subQ24=sQuery(id+"F0.wireOp",EDGE,"E559");var subQ25=sQuery(id+"F0.wireOp",EDGE,"E558");var subQ26=sQuery(id+"F0.wireOp",EDGE,"E557");var subQ27=sQuery(id+"F0.wireOp",EDGE,"E556");var subQ28=sQuery(id+"F0.wireOp",EDGE,"E555");var subQ29=sQuery(id+"F0.wireOp",EDGE,"E554");var subQ30=sQuery(id+"F0.wireOp",EDGE,"E553");var subQ31=sQuery(id+"F0.wireOp",EDGE,"E552");var subQ32=sQuery(id+"F0.wireOp",EDGE,"E551");var subQ33=sQuery(id+"F0.wireOp",EDGE,"E550");var subQ34=sQuery(id+"F0.wireOp",EDGE,"E549");var subQ35=sQuery(id+"F0.wireOp",EDGE,"E548");var subQ36=sQuery(id+"F0.wireOp",EDGE,"E547");var subQ37=sQuery(id+"F0.wireOp",EDGE,"E546");var subQ38=sQuery(id+"F0.wireOp",EDGE,"E545");var subQ39=sQuery(id+"F0.wireOp",EDGE,"E544");var subQ40=sQuery(id+"F0.wireOp",EDGE,"E543");var subQ41=sQuery(id+"F0.wireOp",EDGE,"E542");var subQ42=sQuery(id+"F0.wireOp",EDGE,"E541");var subQ43=sQuery(id+"F0.wireOp",EDGE,"E540");var subQ44=sQuery(id+"F0.wireOp",EDGE,"E539");var subQ45=sQuery(id+"F0.wireOp",EDGE,"E538");var subQ46=sQuery(id+"F0.wireOp",EDGE,"E537");var subQ47=sQuery(id+"F0.wireOp",EDGE,"E536");var subQ48=sQuery(id+"F0.wireOp",EDGE,"E535");var subQ49=sQuery(id+"F0.wireOp",EDGE,"E534");var subQ50=sQuery(id+"F0.wireOp",EDGE,"E533");var subQ51=sQuery(id+"F0.wireOp",EDGE,"E532");var subQ52=sQuery(id+"F0.wireOp",EDGE,"E531");var subQ53=sQuery(id+"F0.wireOp",EDGE,"E530");var subQ54=sQuery(id+"F0.wireOp",EDGE,"E529");var subQ55=sQuery(id+"F0.wireOp",EDGE,"E528");var subQ56=sQuery(id+"F0.wireOp",EDGE,"E527");var subQ57=sQuery(id+"F0.wireOp",EDGE,"E526");var subQ58=sQuery(id+"F0.wireOp",EDGE,"E525");var subQ59=sQuery(id+"F0.wireOp",EDGE,"E524");var subQ60=sQuery(id+"F0.wireOp",EDGE,"E523");var subQ61=sQuery(id+"F0.wireOp",EDGE,"E522");var subQ62=sQuery(id+"F0.wireOp",EDGE,"E521");var subQ63=sQuery(id+"F0.wireOp",EDGE,"E520");var subQ64=sQuery(id+"F0.wireOp",EDGE,"E519");var subQ65=sQuery(id+"F0.wireOp",EDGE,"E518");var subQ66=sQuery(id+"F0.wireOp",EDGE,"E517");var subQ67=sQuery(id+"F0.wireOp",EDGE,"E516");var subQ68=sQuery(id+"F0.wireOp",EDGE,"E515");var subQ69=sQuery(id+"F0.wireOp",EDGE,"E514");var subQ70=sQuery(id+"F0.wireOp",EDGE,"E513");var subQ71=sQuery(id+"F0.wireOp",EDGE,"E512");var subQ72=sQuery(id+"F0.wireOp",EDGE,"E511");var subQ73=sQuery(id+"F0.wireOp",EDGE,"E510");var subQ74=sQuery(id+"F0.wireOp",EDGE,"E509");var subQ75=sQuery(id+"F0.wireOp",EDGE,"E508");var subQ76=sQuery(id+"F0.wireOp",EDGE,"E507");var subQ77=sQuery(id+"F0.wireOp",EDGE,"E506");var subQ78=sQuery(id+"F0.wireOp",EDGE,"E505");var subQ79=sQuery(id+"F0.wireOp",EDGE,"E504");var subQ80=sQuery(id+"F0.wireOp",EDGE,"E503");var subQ81=sQuery(id+"F0.wireOp",EDGE,"E502");var subQ82=sQuery(id+"F0.wireOp",EDGE,"E501");var subQ83=sQuery(id+"F0.wireOp",EDGE,"E500");var subQ84=sQuery(id+"F0.wireOp",EDGE,"E499");var subQ85=sQuery(id+"F0.wireOp",EDGE,"E498");var subQ86=sQuery(id+"F0.wireOp",EDGE,"E497");var subQ87=sQuery(id+"F0.wireOp",EDGE,"E496");var subQ88=sQuery(id+"F0.wireOp",EDGE,"E495");var subQ89=sQuery(id+"F0.wireOp",EDGE,"E494");var subQ90=sQuery(id+"F0.wireOp",EDGE,"E493");var subQ91=sQuery(id+"F0.wireOp",EDGE,"E492");var subQ92=sQuery(id+"F0.wireOp",EDGE,"E491");var subQ93=sQuery(id+"F0.wireOp",EDGE,"E490");var subQ94=sQuery(id+"F0.wireOp",EDGE,"E489");var subQ95=sQuery(id+"F0.wireOp",EDGE,"E488");var subQ96=sQuery(id+"F0.wireOp",EDGE,"E487");var subQ97=sQuery(id+"F0.wireOp",EDGE,"E486");var subQ98=sQuery(id+"F0.wireOp",EDGE,"E485");var subQ99=sQuery(id+"F0.wireOp",EDGE,"E484");var subQ100=sQuery(id+"F0.wireOp",EDGE,"E483");var subQ101=sQuery(id+"F0.wireOp",EDGE,"E482");var subQ102=sQuery(id+"F0.wireOp",EDGE,"E481");var subQ103=sQuery(id+"F0.wireOp",EDGE,"E480");var subQ104=sQuery(id+"F0.wireOp",EDGE,"E479");var subQ105=sQuery(id+"F0.wireOp",EDGE,"E478");var subQ106=sQuery(id+"F0.wireOp",EDGE,"E477");var subQ107=sQuery(id+"F0.wireOp",EDGE,"E476");var subQ108=sQuery(id+"F0.wireOp",EDGE,"E475");var subQ109=sQuery(id+"F0.wireOp",EDGE,"E474");var subQ110=sQuery(id+"F0.wireOp",EDGE,"E473");var subQ111=sQuery(id+"F0.wireOp",EDGE,"E472");var subQ112=sQuery(id+"F0.wireOp",EDGE,"E471");var subQ113=sQuery(id+"F0.wireOp",EDGE,"E470");var subQ114=sQuery(id+"F0.wireOp",EDGE,"E469");var subQ115=sQuery(id+"F0.wireOp",EDGE,"E468");var subQ116=sQuery(id+"F0.wireOp",EDGE,"E467");var subQ117=sQuery(id+"F0.wireOp",EDGE,"E466");var subQ118=sQuery(id+"F0.wireOp",EDGE,"E465");var subQ119=sQuery(id+"F0.wireOp",EDGE,"E464");var subQ120=sQuery(id+"F0.wireOp",EDGE,"E463");var subQ121=sQuery(id+"F0.wireOp",EDGE,"E462");var subQ122=sQuery(id+"F0.wireOp",EDGE,"E461");var subQ123=sQuery(id+"F0.wireOp",EDGE,"E460");var subQ124=sQuery(id+"F0.wireOp",EDGE,"E459");var subQ125=sQuery(id+"F0.wireOp",EDGE,"E458");var subQ126=sQuery(id+"F0.wireOp",EDGE,"E457");var subQ127=sQuery(id+"F0.wireOp",EDGE,"E456");var subQ128=sQuery(id+"F0.wireOp",EDGE,"E455");var subQ129=sQuery(id+"F0.wireOp",EDGE,"E454");var subQ130=sQuery(id+"F0.wireOp",EDGE,"E453");var subQ131=sQuery(id+"F0.wireOp",EDGE,"E452");var subQ132=sQuery(id+"F0.wireOp",EDGE,"E451");var subQ133=sQuery(id+"F0.wireOp",EDGE,"E450");var subQ134=sQuery(id+"F0.wireOp",EDGE,"E449");var subQ135=sQuery(id+"F0.wireOp",EDGE,"E448");var subQ136=sQuery(id+"F0.wireOp",EDGE,"E447");var subQ137=sQuery(id+"F0.wireOp",EDGE,"E446");var subQ138=sQuery(id+"F0.wireOp",EDGE,"E445");var subQ139=sQuery(id+"F0.wireOp",EDGE,"E444");var subQ140=sQuery(id+"F0.wireOp",EDGE,"E443");var subQ141=sQuery(id+"F0.wireOp",EDGE,"E442");var subQ142=sQuery(id+"F0.wireOp",EDGE,"E441");var subQ143=sQuery(id+"F0.wireOp",EDGE,"E440");var subQ144=sQuery(id+"F0.wireOp",EDGE,"E439");var subQ145=sQuery(id+"F0.wireOp",EDGE,"E438");var subQ146=sQuery(id+"F0.wireOp",EDGE,"E437");var subQ147=sQuery(id+"F0.wireOp",EDGE,"E436");var subQ148=sQuery(id+"F0.wireOp",EDGE,"E435");var subQ149=sQuery(id+"F0.wireOp",EDGE,"E434");var subQ150=sQuery(id+"F0.wireOp",EDGE,"E433");var subQ151=sQuery(id+"F0.wireOp",EDGE,"E432");var subQ152=sQuery(id+"F0.wireOp",EDGE,"E431");var subQ153=sQuery(id+"F0.wireOp",EDGE,"E430");var subQ154=sQuery(id+"F0.wireOp",EDGE,"E429");var subQ155=sQuery(id+"F0.wireOp",EDGE,"E428");var subQ156=sQuery(id+"F0.wireOp",EDGE,"E427");var subQ157=sQuery(id+"F0.wireOp",EDGE,"E426");var subQ158=sQuery(id+"F0.wireOp",EDGE,"E425");var subQ159=sQuery(id+"F0.wireOp",EDGE,"E424");var subQ160=sQuery(id+"F0.wireOp",EDGE,"E423");var subQ161=sQuery(id+"F0.wireOp",EDGE,"E422");var subQ162=sQuery(id+"F0.wireOp",EDGE,"E421");var subQ163=sQuery(id+"F0.wireOp",EDGE,"E420");var subQ164=sQuery(id+"F0.wireOp",EDGE,"E419");var subQ165=sQuery(id+"F0.wireOp",EDGE,"E418");var subQ166=sQuery(id+"F0.wireOp",EDGE,"E417");var subQ167=sQuery(id+"F0.wireOp",EDGE,"E416");var subQ168=sQuery(id+"F0.wireOp",EDGE,"E415");var subQ169=sQuery(id+"F0.wireOp",EDGE,"E414");var subQ170=sQuery(id+"F0.wireOp",EDGE,"E413");var subQ171=sQuery(id+"F0.wireOp",EDGE,"E412");var subQ172=sQuery(id+"F0.wireOp",EDGE,"E411");var subQ173=sQuery(id+"F0.wireOp",EDGE,"E410");var subQ174=sQuery(id+"F0.wireOp",EDGE,"E409");var subQ175=sQuery(id+"F0.wireOp",EDGE,"E408");var subQ176=sQuery(id+"F0.wireOp",EDGE,"E407");var subQ177=sQuery(id+"F0.wireOp",EDGE,"E406");var subQ178=sQuery(id+"F0.wireOp",EDGE,"E405");var subQ179=sQuery(id+"F0.wireOp",EDGE,"E404");var subQ180=sQuery(id+"F0.wireOp",EDGE,"E403");var subQ181=sQuery(id+"F0.wireOp",EDGE,"E402");var subQ182=sQuery(id+"F0.wireOp",EDGE,"E401");var subQ183=sQuery(id+"F0.wireOp",EDGE,"E400");var subQ184=sQuery(id+"F0.wireOp",EDGE,"E399");var subQ185=sQuery(id+"F0.wireOp",EDGE,"E398");var subQ186=sQuery(id+"F0.wireOp",EDGE,"E397");var subQ187=sQuery(id+"F0.wireOp",EDGE,"E396");var subQ188=sQuery(id+"F0.wireOp",EDGE,"E395");var subQ189=sQuery(id+"F0.wireOp",EDGE,"E394");var subQ190=sQuery(id+"F0.wireOp",EDGE,"E393");var subQ191=sQuery(id+"F0.wireOp",EDGE,"E392");var subQ192=sQuery(id+"F0.wireOp",EDGE,"E391");var subQ193=sQuery(id+"F0.wireOp",EDGE,"E390");var subQ194=sQuery(id+"F0.wireOp",EDGE,"E389");var subQ195=sQuery(id+"F0.wireOp",EDGE,"E388");var subQ196=sQuery(id+"F0.wireOp",EDGE,"E387");var subQ197=sQuery(id+"F0.wireOp",EDGE,"E386");var subQ198=sQuery(id+"F0.wireOp",EDGE,"E385");var subQ199=sQuery(id+"F0.wireOp",EDGE,"E384");var subQ200=sQuery(id+"F0.wireOp",EDGE,"E383");var subQ201=sQuery(id+"F0.wireOp",EDGE,"E382");var subQ202=sQuery(id+"F0.wireOp",EDGE,"E381");var subQ203=sQuery(id+"F0.wireOp",EDGE,"E380");var subQ204=sQuery(id+"F0.wireOp",EDGE,"E379");var subQ205=sQuery(id+"F0.wireOp",EDGE,"E378");var subQ206=sQuery(id+"F0.wireOp",EDGE,"E377");var subQ207=sQuery(id+"F0.wireOp",EDGE,"E376");var subQ208=sQuery(id+"F0.wireOp",EDGE,"E375");var subQ209=sQuery(id+"F0.wireOp",EDGE,"E374");var subQ210=sQuery(id+"F0.wireOp",EDGE,"E373");var subQ211=sQuery(id+"F0.wireOp",EDGE,"E372");var subQ212=sQuery(id+"F0.wireOp",EDGE,"E371");var subQ213=sQuery(id+"F0.wireOp",EDGE,"E370");var subQ214=sQuery(id+"F0.wireOp",EDGE,"E369");var subQ215=sQuery(id+"F0.wireOp",EDGE,"E368");var subQ216=sQuery(id+"F0.wireOp",EDGE,"E367");var subQ217=sQuery(id+"F0.wireOp",EDGE,"E366");var subQ218=sQuery(id+"F0.wireOp",EDGE,"E365");var subQ219=sQuery(id+"F0.wireOp",EDGE,"E364");var subQ220=sQuery(id+"F0.wireOp",EDGE,"E363");var subQ221=sQuery(id+"F0.wireOp",EDGE,"E362");var subQ222=sQuery(id+"F0.wireOp",EDGE,"E361");var subQ223=sQuery(id+"F0.wireOp",EDGE,"E360");var subQ224=sQuery(id+"F0.wireOp",EDGE,"E359");var subQ225=sQuery(id+"F0.wireOp",EDGE,"E358");var subQ226=sQuery(id+"F0.wireOp",EDGE,"E357");var subQ227=sQuery(id+"F0.wireOp",EDGE,"E356");var subQ228=sQuery(id+"F0.wireOp",EDGE,"E355");var subQ229=sQuery(id+"F0.wireOp",EDGE,"E354");var subQ230=sQuery(id+"F0.wireOp",EDGE,"E353");var subQ231=sQuery(id+"F0.wireOp",EDGE,"E352");var subQ232=sQuery(id+"F0.wireOp",EDGE,"E351");var subQ233=sQuery(id+"F0.wireOp",EDGE,"E350");var subQ234=sQuery(id+"F0.wireOp",EDGE,"E349");var subQ235=sQuery(id+"F0.wireOp",EDGE,"E348");var subQ236=sQuery(id+"F0.wireOp",EDGE,"E347");var subQ237=sQuery(id+"F0.wireOp",EDGE,"E346");var subQ238=sQuery(id+"F0.wireOp",EDGE,"E345");var subQ239=sQuery(id+"F0.wireOp",EDGE,"E344");var subQ240=sQuery(id+"F0.wireOp",EDGE,"E343");var subQ241=sQuery(id+"F0.wireOp",EDGE,"E342");var subQ242=sQuery(id+"F0.wireOp",EDGE,"E339");var subQ243=sQuery(id+"F0.wireOp",EDGE,"E338");var subQ244=sQuery(id+"F0.wireOp",EDGE,"E337");var subQ245=sQuery(id+"F0.wireOp",EDGE,"E336");var subQ246=sQuery(id+"F0.wireOp",EDGE,"E335");var subQ247=sQuery(id+"F0.wireOp",EDGE,"E334");var subQ248=sQuery(id+"F0.wireOp",EDGE,"E333");var subQ249=sQuery(id+"F0.wireOp",EDGE,"E332");var subQ250=sQuery(id+"F0.wireOp",EDGE,"E331");var subQ251=sQuery(id+"F0.wireOp",EDGE,"E330");var subQ252=sQuery(id+"F0.wireOp",EDGE,"E329");var subQ253=sQuery(id+"F0.wireOp",EDGE,"E328");var subQ254=sQuery(id+"F0.wireOp",EDGE,"E327");var subQ255=sQuery(id+"F0.wireOp",EDGE,"E326");var subQ256=sQuery(id+"F0.wireOp",EDGE,"E325");var subQ257=sQuery(id+"F0.wireOp",EDGE,"E324");var subQ258=sQuery(id+"F0.wireOp",EDGE,"E323");var subQ259=sQuery(id+"F0.wireOp",EDGE,"E322");var subQ260=sQuery(id+"F0.wireOp",EDGE,"E321");var subQ261=sQuery(id+"F0.wireOp",EDGE,"E320");var subQ262=sQuery(id+"F0.wireOp",EDGE,"E319");var subQ263=sQuery(id+"F0.wireOp",EDGE,"E318");var subQ264=sQuery(id+"F0.wireOp",EDGE,"E317");var subQ265=sQuery(id+"F0.wireOp",EDGE,"E316");var subQ266=sQuery(id+"F0.wireOp",EDGE,"E315");var subQ267=sQuery(id+"F0.wireOp",EDGE,"E314");var subQ268=sQuery(id+"F0.wireOp",EDGE,"E313");var subQ269=sQuery(id+"F0.wireOp",EDGE,"E312");var subQ270=sQuery(id+"F0.wireOp",EDGE,"E311");var subQ271=sQuery(id+"F0.wireOp",EDGE,"E310");var subQ272=sQuery(id+"F0.wireOp",EDGE,"E309");var subQ273=sQuery(id+"F0.wireOp",EDGE,"E308");var subQ274=sQuery(id+"F0.wireOp",EDGE,"E307");var subQ275=sQuery(id+"F0.wireOp",EDGE,"E306");var subQ276=sQuery(id+"F0.wireOp",EDGE,"E305");var subQ277=sQuery(id+"F0.wireOp",EDGE,"E304");var subQ278=sQuery(id+"F0.wireOp",EDGE,"E303");var subQ279=sQuery(id+"F0.wireOp",EDGE,"E302");var subQ280=sQuery(id+"F0.wireOp",EDGE,"E301");var subQ281=sQuery(id+"F0.wireOp",EDGE,"E300");var subQ282=sQuery(id+"F0.wireOp",EDGE,"E299");var subQ283=sQuery(id+"F0.wireOp",EDGE,"E298");var subQ284=sQuery(id+"F0.wireOp",EDGE,"E297");var subQ285=sQuery(id+"F0.wireOp",EDGE,"E296");var subQ286=sQuery(id+"F0.wireOp",EDGE,"E295");var subQ287=sQuery(id+"F0.wireOp",EDGE,"E294");var subQ288=sQuery(id+"F0.wireOp",EDGE,"E293");var subQ289=sQuery(id+"F0.wireOp",EDGE,"E292");var subQ290=sQuery(id+"F0.wireOp",EDGE,"E291");var subQ291=sQuery(id+"F0.wireOp",EDGE,"E290");var subQ292=sQuery(id+"F0.wireOp",EDGE,"E289");var subQ293=sQuery(id+"F0.wireOp",EDGE,"E288");var subQ294=sQuery(id+"F0.wireOp",EDGE,"E287");var subQ295=sQuery(id+"F0.wireOp",EDGE,"E286");var subQ296=sQuery(id+"F0.wireOp",EDGE,"E285");var subQ297=sQuery(id+"F0.wireOp",EDGE,"E284");var subQ298=sQuery(id+"F0.wireOp",EDGE,"E283");var subQ299=sQuery(id+"F0.wireOp",EDGE,"E282");var subQ300=sQuery(id+"F0.wireOp",EDGE,"E281");var subQ301=sQuery(id+"F0.wireOp",EDGE,"E280");var subQ302=sQuery(id+"F0.wireOp",EDGE,"E279");var subQ303=sQuery(id+"F0.wireOp",EDGE,"E278");var subQ304=sQuery(id+"F0.wireOp",EDGE,"E277");var subQ305=sQuery(id+"F0.wireOp",EDGE,"E276");var subQ306=sQuery(id+"F0.wireOp",EDGE,"E275");var subQ307=sQuery(id+"F0.wireOp",EDGE,"E274");var subQ308=sQuery(id+"F0.wireOp",EDGE,"E273");var subQ309=sQuery(id+"F0.wireOp",EDGE,"E272");var subQ310=sQuery(id+"F0.wireOp",EDGE,"E271");var subQ311=sQuery(id+"F0.wireOp",EDGE,"E270");var subQ312=sQuery(id+"F0.wireOp",EDGE,"E269");var subQ313=sQuery(id+"F0.wireOp",EDGE,"E268");var subQ314=sQuery(id+"F0.wireOp",EDGE,"E267");var subQ315=sQuery(id+"F0.wireOp",EDGE,"E266");var subQ316=sQuery(id+"F0.wireOp",EDGE,"E265");var subQ317=sQuery(id+"F0.wireOp",EDGE,"E264");var subQ318=sQuery(id+"F0.wireOp",EDGE,"E263");var subQ319=sQuery(id+"F0.wireOp",EDGE,"E262");var subQ320=sQuery(id+"F0.wireOp",EDGE,"E261");var subQ321=sQuery(id+"F0.wireOp",EDGE,"E260");var subQ322=sQuery(id+"F0.wireOp",EDGE,"E259");var subQ323=sQuery(id+"F0.wireOp",EDGE,"E258");var subQ324=sQuery(id+"F0.wireOp",EDGE,"E257");var subQ325=sQuery(id+"F0.wireOp",EDGE,"E256");var subQ326=sQuery(id+"F0.wireOp",EDGE,"E255");var subQ327=sQuery(id+"F0.wireOp",EDGE,"E254");var subQ328=sQuery(id+"F0.wireOp",EDGE,"E253");var subQ329=sQuery(id+"F0.wireOp",EDGE,"E252");var subQ330=sQuery(id+"F0.wireOp",EDGE,"E251");var subQ331=sQuery(id+"F0.wireOp",EDGE,"E250");var subQ332=sQuery(id+"F0.wireOp",EDGE,"E249");var subQ333=sQuery(id+"F0.wireOp",EDGE,"E248");var subQ334=sQuery(id+"F0.wireOp",EDGE,"E247");var subQ335=sQuery(id+"F0.wireOp",EDGE,"E246");var subQ336=sQuery(id+"F0.wireOp",EDGE,"E245");var subQ337=sQuery(id+"F0.wireOp",EDGE,"E244");var subQ338=sQuery(id+"F0.wireOp",EDGE,"E243");var subQ339=sQuery(id+"F0.wireOp",EDGE,"E242");var subQ340=sQuery(id+"F0.wireOp",EDGE,"E241");var subQ341=sQuery(id+"F0.wireOp",EDGE,"E240");var subQ342=sQuery(id+"F0.wireOp",EDGE,"E239");var subQ343=sQuery(id+"F0.wireOp",EDGE,"E238");var subQ344=sQuery(id+"F0.wireOp",EDGE,"E237");var subQ345=sQuery(id+"F0.wireOp",EDGE,"E236");var subQ346=sQuery(id+"F0.wireOp",EDGE,"E235");var subQ347=sQuery(id+"F0.wireOp",EDGE,"E234");var subQ348=sQuery(id+"F0.wireOp",EDGE,"E233");var subQ349=sQuery(id+"F0.wireOp",EDGE,"E232");var subQ350=sQuery(id+"F0.wireOp",EDGE,"E231");var subQ351=sQuery(id+"F0.wireOp",EDGE,"E230");var subQ352=sQuery(id+"F0.wireOp",EDGE,"E229");var subQ353=sQuery(id+"F0.wireOp",EDGE,"E228");var subQ354=sQuery(id+"F0.wireOp",EDGE,"E227");var subQ355=sQuery(id+"F0.wireOp",EDGE,"E226");var subQ356=sQuery(id+"F0.wireOp",EDGE,"E225");var subQ357=sQuery(id+"F0.wireOp",EDGE,"E224");var subQ358=sQuery(id+"F0.wireOp",EDGE,"E223");var subQ359=sQuery(id+"F0.wireOp",EDGE,"E222");var subQ360=sQuery(id+"F0.wireOp",EDGE,"E221");var subQ361=sQuery(id+"F0.wireOp",EDGE,"E220");var subQ362=sQuery(id+"F0.wireOp",EDGE,"E219");var subQ363=sQuery(id+"F0.wireOp",EDGE,"E218");var subQ364=sQuery(id+"F0.wireOp",EDGE,"E217");var subQ365=sQuery(id+"F0.wireOp",EDGE,"E216");var subQ366=sQuery(id+"F0.wireOp",EDGE,"E215");var subQ367=sQuery(id+"F0.wireOp",EDGE,"E214");var subQ368=sQuery(id+"F0.wireOp",EDGE,"E213");var subQ369=sQuery(id+"F0.wireOp",EDGE,"E212");var subQ370=sQuery(id+"F0.wireOp",EDGE,"E211");var subQ371=sQuery(id+"F0.wireOp",EDGE,"E210");var subQ372=sQuery(id+"F0.wireOp",EDGE,"E209");var subQ373=sQuery(id+"F0.wireOp",EDGE,"E208");var subQ374=sQuery(id+"F0.wireOp",EDGE,"E207");var subQ375=sQuery(id+"F0.wireOp",EDGE,"E206");var subQ376=sQuery(id+"F0.wireOp",EDGE,"E205");var subQ377=sQuery(id+"F0.wireOp",EDGE,"E204");var subQ378=sQuery(id+"F0.wireOp",EDGE,"E203");var subQ379=sQuery(id+"F0.wireOp",EDGE,"E202");var subQ380=sQuery(id+"F0.wireOp",EDGE,"E201");var subQ381=sQuery(id+"F0.wireOp",EDGE,"E200");var subQ382=sQuery(id+"F0.wireOp",EDGE,"E199");var subQ383=sQuery(id+"F0.wireOp",EDGE,"E198");var subQ384=sQuery(id+"F0.wireOp",EDGE,"E197");var subQ385=sQuery(id+"F0.wireOp",EDGE,"E196");var subQ386=sQuery(id+"F0.wireOp",EDGE,"E195");var subQ387=sQuery(id+"F0.wireOp",EDGE,"E194");var subQ388=sQuery(id+"F0.wireOp",EDGE,"E193");var subQ389=sQuery(id+"F0.wireOp",EDGE,"E192");var subQ390=sQuery(id+"F0.wireOp",EDGE,"E191");var subQ391=sQuery(id+"F0.wireOp",EDGE,"E190");var subQ392=sQuery(id+"F0.wireOp",EDGE,"E189");var subQ393=sQuery(id+"F0.wireOp",EDGE,"E188");var subQ394=sQuery(id+"F0.wireOp",EDGE,"E187");var subQ395=sQuery(id+"F0.wireOp",EDGE,"E186");var subQ396=sQuery(id+"F0.wireOp",EDGE,"E185");var subQ397=sQuery(id+"F0.wireOp",EDGE,"E184");var subQ398=sQuery(id+"F0.wireOp",EDGE,"E183");var subQ399=sQuery(id+"F0.wireOp",EDGE,"E182");var subQ400=sQuery(id+"F0.wireOp",EDGE,"E181");var subQ401=sQuery(id+"F0.wireOp",EDGE,"E180");var subQ402=sQuery(id+"F0.wireOp",EDGE,"E179");var subQ403=sQuery(id+"F0.wireOp",EDGE,"E178");var subQ404=sQuery(id+"F0.wireOp",EDGE,"E177");var subQ405=sQuery(id+"F0.wireOp",EDGE,"E176");var subQ406=sQuery(id+"F0.wireOp",EDGE,"E175");var subQ407=sQuery(id+"F0.wireOp",EDGE,"E174");var subQ408=sQuery(id+"F0.wireOp",EDGE,"E173");var subQ409=sQuery(id+"F0.wireOp",EDGE,"E172");var subQ410=sQuery(id+"F0.wireOp",EDGE,"E171");var subQ411=sQuery(id+"F0.wireOp",EDGE,"E170");var subQ412=sQuery(id+"F0.wireOp",EDGE,"E169");var subQ413=sQuery(id+"F0.wireOp",EDGE,"E168");var subQ414=sQuery(id+"F0.wireOp",EDGE,"E167");var subQ415=sQuery(id+"F0.wireOp",EDGE,"E166");var subQ416=sQuery(id+"F0.wireOp",EDGE,"E165");var subQ417=sQuery(id+"F0.wireOp",EDGE,"E164");var subQ418=sQuery(id+"F0.wireOp",EDGE,"E163");var subQ419=sQuery(id+"F0.wireOp",EDGE,"E162");var subQ420=sQuery(id+"F0.wireOp",EDGE,"E161");var subQ421=sQuery(id+"F0.wireOp",EDGE,"E160");var subQ422=sQuery(id+"F0.wireOp",EDGE,"E159");var subQ423=sQuery(id+"F0.wireOp",EDGE,"E158");var subQ424=sQuery(id+"F0.wireOp",EDGE,"E157");var subQ425=sQuery(id+"F0.wireOp",EDGE,"E156");var subQ426=sQuery(id+"F0.wireOp",EDGE,"E155");var subQ427=sQuery(id+"F0.wireOp",EDGE,"E154");var subQ428=sQuery(id+"F0.wireOp",EDGE,"E153");var subQ429=sQuery(id+"F0.wireOp",EDGE,"E152");var subQ430=sQuery(id+"F0.wireOp",EDGE,"E151");var subQ431=sQuery(id+"F0.wireOp",EDGE,"E150");var subQ432=sQuery(id+"F0.wireOp",EDGE,"E149");var subQ433=sQuery(id+"F0.wireOp",EDGE,"E148");var subQ434=sQuery(id+"F0.wireOp",EDGE,"E147");var subQ435=sQuery(id+"F0.wireOp",EDGE,"E146");var subQ436=sQuery(id+"F0.wireOp",EDGE,"E145");var subQ437=sQuery(id+"F0.wireOp",EDGE,"E144");var subQ438=sQuery(id+"F0.wireOp",EDGE,"E143");var subQ439=sQuery(id+"F0.wireOp",EDGE,"E142");var subQ440=sQuery(id+"F0.wireOp",EDGE,"E141");var subQ441=sQuery(id+"F0.wireOp",EDGE,"E140");var subQ442=sQuery(id+"F0.wireOp",EDGE,"E139");var subQ443=sQuery(id+"F0.wireOp",EDGE,"E138");var subQ444=sQuery(id+"F0.wireOp",EDGE,"E137");var subQ445=sQuery(id+"F0.wireOp",EDGE,"E136");var subQ446=sQuery(id+"F0.wireOp",EDGE,"E135");var subQ447=sQuery(id+"F0.wireOp",EDGE,"E134");var subQ448=sQuery(id+"F0.wireOp",EDGE,"E133");var subQ449=sQuery(id+"F0.wireOp",EDGE,"E132");var subQ450=sQuery(id+"F0.wireOp",EDGE,"E131");var subQ451=sQuery(id+"F0.wireOp",EDGE,"E130");var subQ452=sQuery(id+"F0.wireOp",EDGE,"E129");var subQ453=sQuery(id+"F0.wireOp",EDGE,"E128");var subQ454=sQuery(id+"F0.wireOp",EDGE,"E127");var subQ455=sQuery(id+"F0.wireOp",EDGE,"E126");var subQ456=sQuery(id+"F0.wireOp",EDGE,"E125");var subQ457=sQuery(id+"F0.wireOp",EDGE,"E124");var subQ458=sQuery(id+"F0.wireOp",EDGE,"E123");var subQ459=sQuery(id+"F0.wireOp",EDGE,"E122");var subQ460=sQuery(id+"F0.wireOp",EDGE,"E121");var subQ461=sQuery(id+"F0.wireOp",EDGE,"E120");var subQ462=sQuery(id+"F0.wireOp",EDGE,"E119");var subQ463=sQuery(id+"F0.wireOp",EDGE,"E118");var subQ464=sQuery(id+"F0.wireOp",EDGE,"E117");var subQ465=sQuery(id+"F0.wireOp",EDGE,"E116");var subQ466=sQuery(id+"F0.wireOp",EDGE,"E115");var subQ467=sQuery(id+"F0.wireOp",EDGE,"E114");var subQ468=sQuery(id+"F0.wireOp",EDGE,"E113");var subQ469=sQuery(id+"F0.wireOp",EDGE,"E112");var subQ470=sQuery(id+"F0.wireOp",EDGE,"E111");var subQ471=sQuery(id+"F0.wireOp",EDGE,"E110");var subQ472=sQuery(id+"F0.wireOp",EDGE,"E109");var subQ473=sQuery(id+"F0.wireOp",EDGE,"E108");var subQ474=sQuery(id+"F0.wireOp",EDGE,"E107");var subQ475=sQuery(id+"F0.wireOp",EDGE,"E106");var subQ476=sQuery(id+"F0.wireOp",EDGE,"E105");var subQ477=sQuery(id+"F0.wireOp",EDGE,"E104");var subQ478=sQuery(id+"F0.wireOp",EDGE,"E103");var subQ479=sQuery(id+"F0.wireOp",EDGE,"E102");var subQ480=sQuery(id+"F0.wireOp",EDGE,"E101");var subQ481=sQuery(id+"F0.wireOp",EDGE,"E100");var subQ482=sQuery(id+"F0.wireOp",EDGE,"E99");var subQ483=sQuery(id+"F0.wireOp",EDGE,"E98");var subQ484=sQuery(id+"F0.wireOp",EDGE,"E97");var subQ485=sQuery(id+"F0.wireOp",EDGE,"E96");var subQ486=sQuery(id+"F0.wireOp",EDGE,"E95");var subQ487=sQuery(id+"F0.wireOp",EDGE,"E94");var subQ488=sQuery(id+"F0.wireOp",EDGE,"E93");var subQ489=sQuery(id+"F0.wireOp",EDGE,"E92");var subQ490=sQuery(id+"F0.wireOp",EDGE,"E91");var subQ491=sQuery(id+"F0.wireOp",EDGE,"E90");var subQ492=sQuery(id+"F0.wireOp",EDGE,"E89");var subQ493=sQuery(id+"F0.wireOp",EDGE,"E88");var subQ494=sQuery(id+"F0.wireOp",EDGE,"E87");var subQ495=sQuery(id+"F0.wireOp",EDGE,"E86");var subQ496=sQuery(id+"F0.wireOp",EDGE,"E85");var subQ497=sQuery(id+"F0.wireOp",EDGE,"E84");var subQ498=sQuery(id+"F0.wireOp",EDGE,"E83");var subQ499=sQuery(id+"F0.wireOp",EDGE,"E82");var subQ500=sQuery(id+"F0.wireOp",EDGE,"E81");var subQ501=sQuery(id+"F0.wireOp",EDGE,"E80");var subQ502=sQuery(id+"F0.wireOp",EDGE,"E79");var subQ503=sQuery(id+"F0.wireOp",EDGE,"E78");var subQ504=sQuery(id+"F0.wireOp",EDGE,"E77");var subQ505=sQuery(id+"F0.wireOp",EDGE,"E76");var subQ506=sQuery(id+"F0.wireOp",EDGE,"E75");var subQ507=sQuery(id+"F0.wireOp",EDGE,"E74");var subQ508=sQuery(id+"F0.wireOp",EDGE,"E73");var subQ509=sQuery(id+"F0.wireOp",EDGE,"E72");var subQ510=sQuery(id+"F0.wireOp",EDGE,"E71");var subQ511=sQuery(id+"F0.wireOp",EDGE,"E70");var subQ512=sQuery(id+"F0.wireOp",EDGE,"E69");var subQ513=sQuery(id+"F0.wireOp",EDGE,"E68");var subQ514=sQuery(id+"F0.wireOp",EDGE,"E67");var subQ515=sQuery(id+"F0.wireOp",EDGE,"E66");var subQ516=sQuery(id+"F0.wireOp",EDGE,"E65");var subQ517=sQuery(id+"F0.wireOp",EDGE,"E64");var subQ518=sQuery(id+"F0.wireOp",EDGE,"E63");var subQ519=sQuery(id+"F0.wireOp",EDGE,"E62");var subQ520=sQuery(id+"F0.wireOp",EDGE,"E61");var subQ521=sQuery(id+"F0.wireOp",EDGE,"E60");var subQ522=sQuery(id+"F0.wireOp",EDGE,"E59");var subQ523=sQuery(id+"F0.wireOp",EDGE,"E58");var subQ524=sQuery(id+"F0.wireOp",EDGE,"E57");var subQ525=sQuery(id+"F0.wireOp",EDGE,"E56");var subQ526=sQuery(id+"F0.wireOp",EDGE,"E55");var subQ527=sQuery(id+"F0.wireOp",EDGE,"E54");var subQ528=sQuery(id+"F0.wireOp",EDGE,"E53");var subQ529=sQuery(id+"F0.wireOp",EDGE,"E52");var subQ530=sQuery(id+"F0.wireOp",EDGE,"E51");var subQ531=sQuery(id+"F0.wireOp",EDGE,"E50");var subQ532=sQuery(id+"F0.wireOp",EDGE,"E49");var subQ533=sQuery(id+"F0.wireOp",EDGE,"E48");var subQ534=sQuery(id+"F0.wireOp",EDGE,"E47");var subQ535=sQuery(id+"F0.wireOp",EDGE,"E46");var subQ536=sQuery(id+"F0.wireOp",EDGE,"E45");var subQ537=sQuery(id+"F0.wireOp",EDGE,"E44");var subQ538=sQuery(id+"F0.wireOp",EDGE,"E43");var subQ539=sQuery(id+"F0.wireOp",EDGE,"E42");var subQ540=sQuery(id+"F0.wireOp",EDGE,"E41");var subQ541=sQuery(id+"F0.wireOp",EDGE,"E40");var subQ542=sQuery(id+"F0.wireOp",EDGE,"E39");var subQ543=sQuery(id+"F0.wireOp",EDGE,"E38");var subQ544=sQuery(id+"F0.wireOp",EDGE,"E37");var subQ545=sQuery(id+"F0.wireOp",EDGE,"E36");var subQ546=sQuery(id+"F0.wireOp",EDGE,"E35");var subQ547=sQuery(id+"F0.wireOp",EDGE,"E34");var subQ548=sQuery(id+"F0.wireOp",EDGE,"E33");var subQ549=sQuery(id+"F0.wireOp",EDGE,"E32");var subQ550=sQuery(id+"F0.wireOp",EDGE,"E31");var subQ551=sQuery(id+"F0.wireOp",EDGE,"E30");var subQ552=sQuery(id+"F0.wireOp",EDGE,"E29");var subQ553=sQuery(id+"F0.wireOp",EDGE,"E28");var subQ554=sQuery(id+"F0.wireOp",EDGE,"E27");var subQ555=sQuery(id+"F0.wireOp",EDGE,"E26");var subQ556=sQuery(id+"F0.wireOp",EDGE,"E25");var subQ557=sQuery(id+"F0.wireOp",EDGE,"E24");var subQ558=sQuery(id+"F0.wireOp",EDGE,"E23");var subQ559=sQuery(id+"F0.wireOp",EDGE,"E22");var subQ560=sQuery(id+"F0.wireOp",EDGE,"E21");var subQ561=sQuery(id+"F0.wireOp",EDGE,"E20");var subQ562=sQuery(id+"F0.wireOp",EDGE,"E19");var subQ563=sQuery(id+"F0.wireOp",EDGE,"E18");var subQ564=sQuery(id+"F0.wireOp",EDGE,"E17");var subQ565=sQuery(id+"F0.wireOp",EDGE,"E16");var subQ566=sQuery(id+"F0.wireOp",EDGE,"E15");var subQ567=sQuery(id+"F0.wireOp",EDGE,"E14");var subQ568=sQuery(id+"F0.wireOp",EDGE,"E13");var subQ569=sQuery(id+"F0.wireOp",EDGE,"E12");var subQ570=sQuery(id+"F0.wireOp",EDGE,"E11");var subQ571=sQuery(id+"F0.wireOp",EDGE,"E10");var subQ572=sQuery(id+"F0.wireOp",EDGE,"E9");var subQ573=sQuery(id+"F0.wireOp",EDGE,"E8");var subQ574=sQuery(id+"F0.wireOp",EDGE,"E7");var subQ575=sQuery(id+"F0.wireOp",EDGE,"E6");var subQ576=sQuery(id+"F0.wireOp",EDGE,"E5");var subQ577=sQuery(id+"F0.wireOp",EDGE,"E4");var subQ578=sQuery(id+"F0.wireOp",EDGE,"E3");var subQ579=sQuery(id+"F0.wireOp",EDGE,"E2");var subQ580=sQuery(id+"F0.wireOp",EDGE,"E1");var subQ581=sQuery(id+"F0.wireOp",EDGE,"E0");Q0=makeQuery(id+"F10.boolean.opBoolean","SPLIT",FACE,{"disambiguationData":[TD([makeQuery(id+"F1.opExtrude","SWEPT_FACE",FACE,{"disambiguationData":[OSD([subQ1])]})])],"derivedFrom":makeQuery(id+"F1.opExtrude","CAP_FACE",FACE,{"disambiguationData":[OSD([subQ581,subQ580,subQ579,subQ578,subQ577,subQ576,subQ575,subQ574,subQ573,subQ572,subQ571,subQ570,subQ569,subQ568,subQ567,subQ566,subQ565,subQ564,subQ563,subQ562,subQ561,subQ560,subQ559,subQ558,subQ557,subQ556,subQ555,subQ554,subQ553,subQ552,subQ551,subQ550,subQ549,subQ548,subQ547,subQ546,subQ545,subQ544,subQ543,subQ542,subQ541,subQ540,subQ539,subQ538,subQ537,subQ536,subQ535,subQ534,subQ533,subQ532,subQ531,subQ530,subQ529,subQ528,subQ527,subQ526,subQ525,subQ524,subQ523,subQ522,subQ521,subQ520,subQ519,subQ518,subQ517,subQ516,subQ515,subQ514,subQ513,subQ512,subQ511,subQ510,subQ509,subQ508,subQ507,subQ506,subQ505,subQ504,subQ503,subQ502,subQ501,subQ500,subQ499,subQ498,subQ497,subQ496,subQ495,subQ494,subQ493,subQ492,subQ491,subQ490,subQ489,subQ488,subQ487,subQ486,subQ485,subQ484,subQ483,subQ482,subQ481,subQ480,subQ479,subQ478,subQ477,subQ476,subQ475,subQ474,subQ473,subQ472,subQ471,subQ470,subQ469,subQ468,subQ467,subQ466,subQ465,subQ464,subQ463,subQ462,subQ461,subQ460,subQ459,subQ458,subQ457,subQ456,subQ455,subQ454,subQ453,subQ452,subQ451,subQ450,subQ449,subQ448,subQ447,subQ446,subQ445,subQ444,subQ443,subQ442,subQ441,subQ440,subQ439,subQ438,subQ437,subQ436,subQ435,subQ434,subQ433,subQ432,subQ431,subQ430,subQ429,subQ428,subQ427,subQ426,subQ425,subQ424,subQ423,subQ422,subQ421,subQ420,subQ419,subQ418,subQ417,subQ416,subQ415,subQ414,subQ413,subQ412,subQ411,subQ410,subQ409,subQ408,subQ407,subQ406,subQ405,subQ404,subQ403,subQ402,subQ401,subQ400,subQ399,subQ398,subQ397,subQ396,subQ395,subQ394,subQ393,subQ392,subQ391,subQ390,subQ389,subQ388,subQ387,subQ386,subQ385,subQ384,subQ383,subQ382,subQ381,subQ380,subQ379,subQ378,subQ377,subQ376,subQ375,subQ374,subQ373,subQ372,subQ371,subQ370,subQ369,subQ368,subQ367,subQ366,subQ365,subQ364,subQ363,subQ362,subQ361,subQ360,subQ359,subQ358,subQ357,subQ356,subQ355,subQ354,subQ353,subQ352,subQ351,subQ350,subQ349,subQ348,subQ347,subQ346,subQ345,subQ344,subQ343,subQ342,subQ341,subQ340,subQ339,subQ338,subQ337,subQ336,subQ335,subQ334,subQ333,subQ332,subQ331,subQ330,subQ329,subQ328,subQ327,subQ326,subQ325,subQ324,subQ323,subQ322,subQ321,subQ320,subQ319,subQ318,subQ317,subQ316,subQ315,subQ314,subQ313,subQ312,subQ311,subQ310,subQ309,subQ308,subQ307,subQ306,subQ305,subQ304,subQ303,subQ302,subQ301,subQ300,subQ299,subQ298,subQ297,subQ296,subQ295,subQ294,subQ293,subQ292,subQ291,subQ290,subQ289,subQ288,subQ287,subQ286,subQ285,subQ284,subQ283,subQ282,subQ281,subQ280,subQ279,subQ278,subQ277,subQ276,subQ275,subQ274,subQ273,subQ272,subQ271,subQ270,subQ269,subQ268,subQ267,subQ266,subQ265,subQ264,subQ263,subQ262,subQ261,subQ260,subQ259,subQ258,subQ257,subQ256,subQ255,subQ254,subQ253,subQ252,subQ251,subQ250,subQ249,subQ248,subQ247,subQ246,subQ245,subQ244,subQ243,subQ242,subQ1,subQ0,subQ241,subQ240,subQ239,subQ238,subQ237,subQ236,subQ235,subQ234,subQ233,subQ232,subQ231,subQ230,subQ229,subQ228,subQ227,subQ226,subQ225,subQ224,subQ223,subQ222,subQ221,subQ220,subQ219,subQ218,subQ217,subQ216,subQ215,subQ214,subQ213,subQ212,subQ211,subQ210,subQ209,subQ208,subQ207,subQ206,subQ205,subQ204,subQ203,subQ202,subQ201,subQ200,subQ199,subQ198,subQ197,subQ196,subQ195,subQ194,subQ193,subQ192,subQ191,subQ190,subQ189,subQ188,subQ187,subQ186,subQ185,subQ184,subQ183,subQ182,subQ181,subQ180,subQ179,subQ178,subQ177,subQ176,subQ175,subQ174,subQ173,subQ172,subQ171,subQ170,subQ169,subQ168,subQ167,subQ166,subQ165,subQ164,subQ163,subQ162,subQ161,subQ160,subQ159,subQ158,subQ157,subQ156,subQ155,subQ154,subQ153,subQ152,subQ151,subQ150,subQ149,subQ148,subQ147,subQ146,subQ145,subQ144,subQ143,subQ142,subQ141,subQ140,subQ139,subQ138,subQ137,subQ136,subQ135,subQ134,subQ133,subQ132,subQ131,subQ130,subQ129,subQ128,subQ127,subQ126,subQ125,subQ124,subQ123,subQ122,subQ121,subQ120,subQ119,subQ118,subQ117,subQ116,subQ115,subQ114,subQ113,subQ112,subQ111,subQ110,subQ109,subQ108,subQ107,subQ106,subQ105,subQ104,subQ103,subQ102,subQ101,subQ100,subQ99,subQ98,subQ97,subQ96,subQ95,subQ94,subQ93,subQ92,subQ91,subQ90,subQ89,subQ88,subQ87,subQ86,subQ85,subQ84,subQ83,subQ82,subQ81,subQ80,subQ79,subQ78,subQ77,subQ76,subQ75,subQ74,subQ73,subQ72,subQ71,subQ70,subQ69,subQ68,subQ67,subQ66,subQ65,subQ64,subQ63,subQ62,subQ61,subQ60,subQ59,subQ58,subQ57,subQ56,subQ55,subQ54,subQ53,subQ52,subQ51,subQ50,subQ49,subQ48,subQ47,subQ46,subQ45,subQ44,subQ43,subQ42,subQ41,subQ40,subQ39,subQ38,subQ37,subQ36,subQ35,subQ34,subQ33,subQ32,subQ31,subQ30,subQ29,subQ28,subQ27,subQ26,subQ25,subQ24,subQ23,subQ22,subQ21,subQ20,subQ19,subQ18,subQ17,subQ16,subQ15,subQ14,subQ13,subQ12,subQ11,subQ10,subQ9,subQ8,subQ7,subQ6,subQ5,subQ4])],"isStart":false})});}
            var sketch = newSketch(context, id + "F11", { "sketchPlane" : qUnion([Q0])});
            skLineSegment(sketch, "E2037.0", {"start": v(-118.3, -7.62) * mm, "end": v(-117.47, -7.77) * mm});
            skLineSegment(sketch, "E2038", {"start": v(-118.21, -7.06) * mm, "end": v(-118.36, -7.89) * mm, "construction": true});
            skPoint(sketch, "E2039.orphan", {"position": v(-117.33, -7.8) * mm});
            skSolve(sketch);
        }
        {
            var Q0;
            Q0=makeQuery(id+"F3.opExtrude","SWEPT_FACE",FACE,{"disambiguationData":[OSD([sQuery(id+"F2.wireOp",EDGE,"E2024")])]});
            var Q1;
            Q1=sQuery(id+"F11.wireOp",EDGE,"E2037.0");
            sweep(context, id + "F12", {"operationType" : NewBodyOperationType.ADD, "profiles" : qUnion([Q0]), "path" : qUnion([Q1])});
        }
        {
            var Q0;
            {var subQ0=sQuery(id+"F0.wireOp",EDGE,"E341");var subQ1=sQuery(id+"F0.wireOp",EDGE,"E340");var subQ4=sQuery(id+"F0.wireOp",EDGE,"E1143");var subQ5=sQuery(id+"F0.wireOp",EDGE,"E1140");var subQ6=sQuery(id+"F0.wireOp",EDGE,"E577");var subQ7=sQuery(id+"F0.wireOp",EDGE,"E576");var subQ8=sQuery(id+"F0.wireOp",EDGE,"E575");var subQ9=sQuery(id+"F0.wireOp",EDGE,"E574");var subQ10=sQuery(id+"F0.wireOp",EDGE,"E573");var subQ11=sQuery(id+"F0.wireOp",EDGE,"E572");var subQ12=sQuery(id+"F0.wireOp",EDGE,"E571");var subQ13=sQuery(id+"F0.wireOp",EDGE,"E570");var subQ14=sQuery(id+"F0.wireOp",EDGE,"E569");var subQ15=sQuery(id+"F0.wireOp",EDGE,"E568");var subQ16=sQuery(id+"F0.wireOp",EDGE,"E567");var subQ17=sQuery(id+"F0.wireOp",EDGE,"E566");var subQ18=sQuery(id+"F0.wireOp",EDGE,"E565");var subQ19=sQuery(id+"F0.wireOp",EDGE,"E564");var subQ20=sQuery(id+"F0.wireOp",EDGE,"E563");var subQ21=sQuery(id+"F0.wireOp",EDGE,"E562");var subQ22=sQuery(id+"F0.wireOp",EDGE,"E561");var subQ23=sQuery(id+"F0.wireOp",EDGE,"E560");var subQ24=sQuery(id+"F0.wireOp",EDGE,"E559");var subQ25=sQuery(id+"F0.wireOp",EDGE,"E558");var subQ26=sQuery(id+"F0.wireOp",EDGE,"E557");var subQ27=sQuery(id+"F0.wireOp",EDGE,"E556");var subQ28=sQuery(id+"F0.wireOp",EDGE,"E555");var subQ29=sQuery(id+"F0.wireOp",EDGE,"E554");var subQ30=sQuery(id+"F0.wireOp",EDGE,"E553");var subQ31=sQuery(id+"F0.wireOp",EDGE,"E552");var subQ32=sQuery(id+"F0.wireOp",EDGE,"E551");var subQ33=sQuery(id+"F0.wireOp",EDGE,"E550");var subQ34=sQuery(id+"F0.wireOp",EDGE,"E549");var subQ35=sQuery(id+"F0.wireOp",EDGE,"E548");var subQ36=sQuery(id+"F0.wireOp",EDGE,"E547");var subQ37=sQuery(id+"F0.wireOp",EDGE,"E546");var subQ38=sQuery(id+"F0.wireOp",EDGE,"E545");var subQ39=sQuery(id+"F0.wireOp",EDGE,"E544");var subQ40=sQuery(id+"F0.wireOp",EDGE,"E543");var subQ41=sQuery(id+"F0.wireOp",EDGE,"E542");var subQ42=sQuery(id+"F0.wireOp",EDGE,"E541");var subQ43=sQuery(id+"F0.wireOp",EDGE,"E540");var subQ44=sQuery(id+"F0.wireOp",EDGE,"E539");var subQ45=sQuery(id+"F0.wireOp",EDGE,"E538");var subQ46=sQuery(id+"F0.wireOp",EDGE,"E537");var subQ47=sQuery(id+"F0.wireOp",EDGE,"E536");var subQ48=sQuery(id+"F0.wireOp",EDGE,"E535");var subQ49=sQuery(id+"F0.wireOp",EDGE,"E534");var subQ50=sQuery(id+"F0.wireOp",EDGE,"E533");var subQ51=sQuery(id+"F0.wireOp",EDGE,"E532");var subQ52=sQuery(id+"F0.wireOp",EDGE,"E531");var subQ53=sQuery(id+"F0.wireOp",EDGE,"E530");var subQ54=sQuery(id+"F0.wireOp",EDGE,"E529");var subQ55=sQuery(id+"F0.wireOp",EDGE,"E528");var subQ56=sQuery(id+"F0.wireOp",EDGE,"E527");var subQ57=sQuery(id+"F0.wireOp",EDGE,"E526");var subQ58=sQuery(id+"F0.wireOp",EDGE,"E525");var subQ59=sQuery(id+"F0.wireOp",EDGE,"E524");var subQ60=sQuery(id+"F0.wireOp",EDGE,"E523");var subQ61=sQuery(id+"F0.wireOp",EDGE,"E522");var subQ62=sQuery(id+"F0.wireOp",EDGE,"E521");var subQ63=sQuery(id+"F0.wireOp",EDGE,"E520");var subQ64=sQuery(id+"F0.wireOp",EDGE,"E519");var subQ65=sQuery(id+"F0.wireOp",EDGE,"E518");var subQ66=sQuery(id+"F0.wireOp",EDGE,"E517");var subQ67=sQuery(id+"F0.wireOp",EDGE,"E516");var subQ68=sQuery(id+"F0.wireOp",EDGE,"E515");var subQ69=sQuery(id+"F0.wireOp",EDGE,"E514");var subQ70=sQuery(id+"F0.wireOp",EDGE,"E513");var subQ71=sQuery(id+"F0.wireOp",EDGE,"E512");var subQ72=sQuery(id+"F0.wireOp",EDGE,"E511");var subQ73=sQuery(id+"F0.wireOp",EDGE,"E510");var subQ74=sQuery(id+"F0.wireOp",EDGE,"E509");var subQ75=sQuery(id+"F0.wireOp",EDGE,"E508");var subQ76=sQuery(id+"F0.wireOp",EDGE,"E507");var subQ77=sQuery(id+"F0.wireOp",EDGE,"E506");var subQ78=sQuery(id+"F0.wireOp",EDGE,"E505");var subQ79=sQuery(id+"F0.wireOp",EDGE,"E504");var subQ80=sQuery(id+"F0.wireOp",EDGE,"E503");var subQ81=sQuery(id+"F0.wireOp",EDGE,"E502");var subQ82=sQuery(id+"F0.wireOp",EDGE,"E501");var subQ83=sQuery(id+"F0.wireOp",EDGE,"E500");var subQ84=sQuery(id+"F0.wireOp",EDGE,"E499");var subQ85=sQuery(id+"F0.wireOp",EDGE,"E498");var subQ86=sQuery(id+"F0.wireOp",EDGE,"E497");var subQ87=sQuery(id+"F0.wireOp",EDGE,"E496");var subQ88=sQuery(id+"F0.wireOp",EDGE,"E495");var subQ89=sQuery(id+"F0.wireOp",EDGE,"E494");var subQ90=sQuery(id+"F0.wireOp",EDGE,"E493");var subQ91=sQuery(id+"F0.wireOp",EDGE,"E492");var subQ92=sQuery(id+"F0.wireOp",EDGE,"E491");var subQ93=sQuery(id+"F0.wireOp",EDGE,"E490");var subQ94=sQuery(id+"F0.wireOp",EDGE,"E489");var subQ95=sQuery(id+"F0.wireOp",EDGE,"E488");var subQ96=sQuery(id+"F0.wireOp",EDGE,"E487");var subQ97=sQuery(id+"F0.wireOp",EDGE,"E486");var subQ98=sQuery(id+"F0.wireOp",EDGE,"E485");var subQ99=sQuery(id+"F0.wireOp",EDGE,"E484");var subQ100=sQuery(id+"F0.wireOp",EDGE,"E483");var subQ101=sQuery(id+"F0.wireOp",EDGE,"E482");var subQ102=sQuery(id+"F0.wireOp",EDGE,"E481");var subQ103=sQuery(id+"F0.wireOp",EDGE,"E480");var subQ104=sQuery(id+"F0.wireOp",EDGE,"E479");var subQ105=sQuery(id+"F0.wireOp",EDGE,"E478");var subQ106=sQuery(id+"F0.wireOp",EDGE,"E477");var subQ107=sQuery(id+"F0.wireOp",EDGE,"E476");var subQ108=sQuery(id+"F0.wireOp",EDGE,"E475");var subQ109=sQuery(id+"F0.wireOp",EDGE,"E474");var subQ110=sQuery(id+"F0.wireOp",EDGE,"E473");var subQ111=sQuery(id+"F0.wireOp",EDGE,"E472");var subQ112=sQuery(id+"F0.wireOp",EDGE,"E471");var subQ113=sQuery(id+"F0.wireOp",EDGE,"E470");var subQ114=sQuery(id+"F0.wireOp",EDGE,"E469");var subQ115=sQuery(id+"F0.wireOp",EDGE,"E468");var subQ116=sQuery(id+"F0.wireOp",EDGE,"E467");var subQ117=sQuery(id+"F0.wireOp",EDGE,"E466");var subQ118=sQuery(id+"F0.wireOp",EDGE,"E465");var subQ119=sQuery(id+"F0.wireOp",EDGE,"E464");var subQ120=sQuery(id+"F0.wireOp",EDGE,"E463");var subQ121=sQuery(id+"F0.wireOp",EDGE,"E462");var subQ122=sQuery(id+"F0.wireOp",EDGE,"E461");var subQ123=sQuery(id+"F0.wireOp",EDGE,"E460");var subQ124=sQuery(id+"F0.wireOp",EDGE,"E459");var subQ125=sQuery(id+"F0.wireOp",EDGE,"E458");var subQ126=sQuery(id+"F0.wireOp",EDGE,"E457");var subQ127=sQuery(id+"F0.wireOp",EDGE,"E456");var subQ128=sQuery(id+"F0.wireOp",EDGE,"E455");var subQ129=sQuery(id+"F0.wireOp",EDGE,"E454");var subQ130=sQuery(id+"F0.wireOp",EDGE,"E453");var subQ131=sQuery(id+"F0.wireOp",EDGE,"E452");var subQ132=sQuery(id+"F0.wireOp",EDGE,"E451");var subQ133=sQuery(id+"F0.wireOp",EDGE,"E450");var subQ134=sQuery(id+"F0.wireOp",EDGE,"E449");var subQ135=sQuery(id+"F0.wireOp",EDGE,"E448");var subQ136=sQuery(id+"F0.wireOp",EDGE,"E447");var subQ137=sQuery(id+"F0.wireOp",EDGE,"E446");var subQ138=sQuery(id+"F0.wireOp",EDGE,"E445");var subQ139=sQuery(id+"F0.wireOp",EDGE,"E444");var subQ140=sQuery(id+"F0.wireOp",EDGE,"E443");var subQ141=sQuery(id+"F0.wireOp",EDGE,"E442");var subQ142=sQuery(id+"F0.wireOp",EDGE,"E441");var subQ143=sQuery(id+"F0.wireOp",EDGE,"E440");var subQ144=sQuery(id+"F0.wireOp",EDGE,"E439");var subQ145=sQuery(id+"F0.wireOp",EDGE,"E438");var subQ146=sQuery(id+"F0.wireOp",EDGE,"E437");var subQ147=sQuery(id+"F0.wireOp",EDGE,"E436");var subQ148=sQuery(id+"F0.wireOp",EDGE,"E435");var subQ149=sQuery(id+"F0.wireOp",EDGE,"E434");var subQ150=sQuery(id+"F0.wireOp",EDGE,"E433");var subQ151=sQuery(id+"F0.wireOp",EDGE,"E432");var subQ152=sQuery(id+"F0.wireOp",EDGE,"E431");var subQ153=sQuery(id+"F0.wireOp",EDGE,"E430");var subQ154=sQuery(id+"F0.wireOp",EDGE,"E429");var subQ155=sQuery(id+"F0.wireOp",EDGE,"E428");var subQ156=sQuery(id+"F0.wireOp",EDGE,"E427");var subQ157=sQuery(id+"F0.wireOp",EDGE,"E426");var subQ158=sQuery(id+"F0.wireOp",EDGE,"E425");var subQ159=sQuery(id+"F0.wireOp",EDGE,"E424");var subQ160=sQuery(id+"F0.wireOp",EDGE,"E423");var subQ161=sQuery(id+"F0.wireOp",EDGE,"E422");var subQ162=sQuery(id+"F0.wireOp",EDGE,"E421");var subQ163=sQuery(id+"F0.wireOp",EDGE,"E420");var subQ164=sQuery(id+"F0.wireOp",EDGE,"E419");var subQ165=sQuery(id+"F0.wireOp",EDGE,"E418");var subQ166=sQuery(id+"F0.wireOp",EDGE,"E417");var subQ167=sQuery(id+"F0.wireOp",EDGE,"E416");var subQ168=sQuery(id+"F0.wireOp",EDGE,"E415");var subQ169=sQuery(id+"F0.wireOp",EDGE,"E414");var subQ170=sQuery(id+"F0.wireOp",EDGE,"E413");var subQ171=sQuery(id+"F0.wireOp",EDGE,"E412");var subQ172=sQuery(id+"F0.wireOp",EDGE,"E411");var subQ173=sQuery(id+"F0.wireOp",EDGE,"E410");var subQ174=sQuery(id+"F0.wireOp",EDGE,"E409");var subQ175=sQuery(id+"F0.wireOp",EDGE,"E408");var subQ176=sQuery(id+"F0.wireOp",EDGE,"E407");var subQ177=sQuery(id+"F0.wireOp",EDGE,"E406");var subQ178=sQuery(id+"F0.wireOp",EDGE,"E405");var subQ179=sQuery(id+"F0.wireOp",EDGE,"E404");var subQ180=sQuery(id+"F0.wireOp",EDGE,"E403");var subQ181=sQuery(id+"F0.wireOp",EDGE,"E402");var subQ182=sQuery(id+"F0.wireOp",EDGE,"E401");var subQ183=sQuery(id+"F0.wireOp",EDGE,"E400");var subQ184=sQuery(id+"F0.wireOp",EDGE,"E399");var subQ185=sQuery(id+"F0.wireOp",EDGE,"E398");var subQ186=sQuery(id+"F0.wireOp",EDGE,"E397");var subQ187=sQuery(id+"F0.wireOp",EDGE,"E396");var subQ188=sQuery(id+"F0.wireOp",EDGE,"E395");var subQ189=sQuery(id+"F0.wireOp",EDGE,"E394");var subQ190=sQuery(id+"F0.wireOp",EDGE,"E393");var subQ191=sQuery(id+"F0.wireOp",EDGE,"E392");var subQ192=sQuery(id+"F0.wireOp",EDGE,"E391");var subQ193=sQuery(id+"F0.wireOp",EDGE,"E390");var subQ194=sQuery(id+"F0.wireOp",EDGE,"E389");var subQ195=sQuery(id+"F0.wireOp",EDGE,"E388");var subQ196=sQuery(id+"F0.wireOp",EDGE,"E387");var subQ197=sQuery(id+"F0.wireOp",EDGE,"E386");var subQ198=sQuery(id+"F0.wireOp",EDGE,"E385");var subQ199=sQuery(id+"F0.wireOp",EDGE,"E384");var subQ200=sQuery(id+"F0.wireOp",EDGE,"E383");var subQ201=sQuery(id+"F0.wireOp",EDGE,"E382");var subQ202=sQuery(id+"F0.wireOp",EDGE,"E381");var subQ203=sQuery(id+"F0.wireOp",EDGE,"E380");var subQ204=sQuery(id+"F0.wireOp",EDGE,"E379");var subQ205=sQuery(id+"F0.wireOp",EDGE,"E378");var subQ206=sQuery(id+"F0.wireOp",EDGE,"E377");var subQ207=sQuery(id+"F0.wireOp",EDGE,"E376");var subQ208=sQuery(id+"F0.wireOp",EDGE,"E375");var subQ209=sQuery(id+"F0.wireOp",EDGE,"E374");var subQ210=sQuery(id+"F0.wireOp",EDGE,"E373");var subQ211=sQuery(id+"F0.wireOp",EDGE,"E372");var subQ212=sQuery(id+"F0.wireOp",EDGE,"E371");var subQ213=sQuery(id+"F0.wireOp",EDGE,"E370");var subQ214=sQuery(id+"F0.wireOp",EDGE,"E369");var subQ215=sQuery(id+"F0.wireOp",EDGE,"E368");var subQ216=sQuery(id+"F0.wireOp",EDGE,"E367");var subQ217=sQuery(id+"F0.wireOp",EDGE,"E366");var subQ218=sQuery(id+"F0.wireOp",EDGE,"E365");var subQ219=sQuery(id+"F0.wireOp",EDGE,"E364");var subQ220=sQuery(id+"F0.wireOp",EDGE,"E363");var subQ221=sQuery(id+"F0.wireOp",EDGE,"E362");var subQ222=sQuery(id+"F0.wireOp",EDGE,"E361");var subQ223=sQuery(id+"F0.wireOp",EDGE,"E360");var subQ224=sQuery(id+"F0.wireOp",EDGE,"E359");var subQ225=sQuery(id+"F0.wireOp",EDGE,"E358");var subQ226=sQuery(id+"F0.wireOp",EDGE,"E357");var subQ227=sQuery(id+"F0.wireOp",EDGE,"E356");var subQ228=sQuery(id+"F0.wireOp",EDGE,"E355");var subQ229=sQuery(id+"F0.wireOp",EDGE,"E354");var subQ230=sQuery(id+"F0.wireOp",EDGE,"E353");var subQ231=sQuery(id+"F0.wireOp",EDGE,"E352");var subQ232=sQuery(id+"F0.wireOp",EDGE,"E351");var subQ233=sQuery(id+"F0.wireOp",EDGE,"E350");var subQ234=sQuery(id+"F0.wireOp",EDGE,"E349");var subQ235=sQuery(id+"F0.wireOp",EDGE,"E348");var subQ236=sQuery(id+"F0.wireOp",EDGE,"E347");var subQ237=sQuery(id+"F0.wireOp",EDGE,"E346");var subQ238=sQuery(id+"F0.wireOp",EDGE,"E345");var subQ239=sQuery(id+"F0.wireOp",EDGE,"E344");var subQ240=sQuery(id+"F0.wireOp",EDGE,"E343");var subQ241=sQuery(id+"F0.wireOp",EDGE,"E342");var subQ242=sQuery(id+"F0.wireOp",EDGE,"E339");var subQ243=sQuery(id+"F0.wireOp",EDGE,"E338");var subQ244=sQuery(id+"F0.wireOp",EDGE,"E337");var subQ245=sQuery(id+"F0.wireOp",EDGE,"E336");var subQ246=sQuery(id+"F0.wireOp",EDGE,"E335");var subQ247=sQuery(id+"F0.wireOp",EDGE,"E334");var subQ248=sQuery(id+"F0.wireOp",EDGE,"E333");var subQ249=sQuery(id+"F0.wireOp",EDGE,"E332");var subQ250=sQuery(id+"F0.wireOp",EDGE,"E331");var subQ251=sQuery(id+"F0.wireOp",EDGE,"E330");var subQ252=sQuery(id+"F0.wireOp",EDGE,"E329");var subQ253=sQuery(id+"F0.wireOp",EDGE,"E328");var subQ254=sQuery(id+"F0.wireOp",EDGE,"E327");var subQ255=sQuery(id+"F0.wireOp",EDGE,"E326");var subQ256=sQuery(id+"F0.wireOp",EDGE,"E325");var subQ257=sQuery(id+"F0.wireOp",EDGE,"E324");var subQ258=sQuery(id+"F0.wireOp",EDGE,"E323");var subQ259=sQuery(id+"F0.wireOp",EDGE,"E322");var subQ260=sQuery(id+"F0.wireOp",EDGE,"E321");var subQ261=sQuery(id+"F0.wireOp",EDGE,"E320");var subQ262=sQuery(id+"F0.wireOp",EDGE,"E319");var subQ263=sQuery(id+"F0.wireOp",EDGE,"E318");var subQ264=sQuery(id+"F0.wireOp",EDGE,"E317");var subQ265=sQuery(id+"F0.wireOp",EDGE,"E316");var subQ266=sQuery(id+"F0.wireOp",EDGE,"E315");var subQ267=sQuery(id+"F0.wireOp",EDGE,"E314");var subQ268=sQuery(id+"F0.wireOp",EDGE,"E313");var subQ269=sQuery(id+"F0.wireOp",EDGE,"E312");var subQ270=sQuery(id+"F0.wireOp",EDGE,"E311");var subQ271=sQuery(id+"F0.wireOp",EDGE,"E310");var subQ272=sQuery(id+"F0.wireOp",EDGE,"E309");var subQ273=sQuery(id+"F0.wireOp",EDGE,"E308");var subQ274=sQuery(id+"F0.wireOp",EDGE,"E307");var subQ275=sQuery(id+"F0.wireOp",EDGE,"E306");var subQ276=sQuery(id+"F0.wireOp",EDGE,"E305");var subQ277=sQuery(id+"F0.wireOp",EDGE,"E304");var subQ278=sQuery(id+"F0.wireOp",EDGE,"E303");var subQ279=sQuery(id+"F0.wireOp",EDGE,"E302");var subQ280=sQuery(id+"F0.wireOp",EDGE,"E301");var subQ281=sQuery(id+"F0.wireOp",EDGE,"E300");var subQ282=sQuery(id+"F0.wireOp",EDGE,"E299");var subQ283=sQuery(id+"F0.wireOp",EDGE,"E298");var subQ284=sQuery(id+"F0.wireOp",EDGE,"E297");var subQ285=sQuery(id+"F0.wireOp",EDGE,"E296");var subQ286=sQuery(id+"F0.wireOp",EDGE,"E295");var subQ287=sQuery(id+"F0.wireOp",EDGE,"E294");var subQ288=sQuery(id+"F0.wireOp",EDGE,"E293");var subQ289=sQuery(id+"F0.wireOp",EDGE,"E292");var subQ290=sQuery(id+"F0.wireOp",EDGE,"E291");var subQ291=sQuery(id+"F0.wireOp",EDGE,"E290");var subQ292=sQuery(id+"F0.wireOp",EDGE,"E289");var subQ293=sQuery(id+"F0.wireOp",EDGE,"E288");var subQ294=sQuery(id+"F0.wireOp",EDGE,"E287");var subQ295=sQuery(id+"F0.wireOp",EDGE,"E286");var subQ296=sQuery(id+"F0.wireOp",EDGE,"E285");var subQ297=sQuery(id+"F0.wireOp",EDGE,"E284");var subQ298=sQuery(id+"F0.wireOp",EDGE,"E283");var subQ299=sQuery(id+"F0.wireOp",EDGE,"E282");var subQ300=sQuery(id+"F0.wireOp",EDGE,"E281");var subQ301=sQuery(id+"F0.wireOp",EDGE,"E280");var subQ302=sQuery(id+"F0.wireOp",EDGE,"E279");var subQ303=sQuery(id+"F0.wireOp",EDGE,"E278");var subQ304=sQuery(id+"F0.wireOp",EDGE,"E277");var subQ305=sQuery(id+"F0.wireOp",EDGE,"E276");var subQ306=sQuery(id+"F0.wireOp",EDGE,"E275");var subQ307=sQuery(id+"F0.wireOp",EDGE,"E274");var subQ308=sQuery(id+"F0.wireOp",EDGE,"E273");var subQ309=sQuery(id+"F0.wireOp",EDGE,"E272");var subQ310=sQuery(id+"F0.wireOp",EDGE,"E271");var subQ311=sQuery(id+"F0.wireOp",EDGE,"E270");var subQ312=sQuery(id+"F0.wireOp",EDGE,"E269");var subQ313=sQuery(id+"F0.wireOp",EDGE,"E268");var subQ314=sQuery(id+"F0.wireOp",EDGE,"E267");var subQ315=sQuery(id+"F0.wireOp",EDGE,"E266");var subQ316=sQuery(id+"F0.wireOp",EDGE,"E265");var subQ317=sQuery(id+"F0.wireOp",EDGE,"E264");var subQ318=sQuery(id+"F0.wireOp",EDGE,"E263");var subQ319=sQuery(id+"F0.wireOp",EDGE,"E262");var subQ320=sQuery(id+"F0.wireOp",EDGE,"E261");var subQ321=sQuery(id+"F0.wireOp",EDGE,"E260");var subQ322=sQuery(id+"F0.wireOp",EDGE,"E259");var subQ323=sQuery(id+"F0.wireOp",EDGE,"E258");var subQ324=sQuery(id+"F0.wireOp",EDGE,"E257");var subQ325=sQuery(id+"F0.wireOp",EDGE,"E256");var subQ326=sQuery(id+"F0.wireOp",EDGE,"E255");var subQ327=sQuery(id+"F0.wireOp",EDGE,"E254");var subQ328=sQuery(id+"F0.wireOp",EDGE,"E253");var subQ329=sQuery(id+"F0.wireOp",EDGE,"E252");var subQ330=sQuery(id+"F0.wireOp",EDGE,"E251");var subQ331=sQuery(id+"F0.wireOp",EDGE,"E250");var subQ332=sQuery(id+"F0.wireOp",EDGE,"E249");var subQ333=sQuery(id+"F0.wireOp",EDGE,"E248");var subQ334=sQuery(id+"F0.wireOp",EDGE,"E247");var subQ335=sQuery(id+"F0.wireOp",EDGE,"E246");var subQ336=sQuery(id+"F0.wireOp",EDGE,"E245");var subQ337=sQuery(id+"F0.wireOp",EDGE,"E244");var subQ338=sQuery(id+"F0.wireOp",EDGE,"E243");var subQ339=sQuery(id+"F0.wireOp",EDGE,"E242");var subQ340=sQuery(id+"F0.wireOp",EDGE,"E241");var subQ341=sQuery(id+"F0.wireOp",EDGE,"E240");var subQ342=sQuery(id+"F0.wireOp",EDGE,"E239");var subQ343=sQuery(id+"F0.wireOp",EDGE,"E238");var subQ344=sQuery(id+"F0.wireOp",EDGE,"E237");var subQ345=sQuery(id+"F0.wireOp",EDGE,"E236");var subQ346=sQuery(id+"F0.wireOp",EDGE,"E235");var subQ347=sQuery(id+"F0.wireOp",EDGE,"E234");var subQ348=sQuery(id+"F0.wireOp",EDGE,"E233");var subQ349=sQuery(id+"F0.wireOp",EDGE,"E232");var subQ350=sQuery(id+"F0.wireOp",EDGE,"E231");var subQ351=sQuery(id+"F0.wireOp",EDGE,"E230");var subQ352=sQuery(id+"F0.wireOp",EDGE,"E229");var subQ353=sQuery(id+"F0.wireOp",EDGE,"E228");var subQ354=sQuery(id+"F0.wireOp",EDGE,"E227");var subQ355=sQuery(id+"F0.wireOp",EDGE,"E226");var subQ356=sQuery(id+"F0.wireOp",EDGE,"E225");var subQ357=sQuery(id+"F0.wireOp",EDGE,"E224");var subQ358=sQuery(id+"F0.wireOp",EDGE,"E223");var subQ359=sQuery(id+"F0.wireOp",EDGE,"E222");var subQ360=sQuery(id+"F0.wireOp",EDGE,"E221");var subQ361=sQuery(id+"F0.wireOp",EDGE,"E220");var subQ362=sQuery(id+"F0.wireOp",EDGE,"E219");var subQ363=sQuery(id+"F0.wireOp",EDGE,"E218");var subQ364=sQuery(id+"F0.wireOp",EDGE,"E217");var subQ365=sQuery(id+"F0.wireOp",EDGE,"E216");var subQ366=sQuery(id+"F0.wireOp",EDGE,"E215");var subQ367=sQuery(id+"F0.wireOp",EDGE,"E214");var subQ368=sQuery(id+"F0.wireOp",EDGE,"E213");var subQ369=sQuery(id+"F0.wireOp",EDGE,"E212");var subQ370=sQuery(id+"F0.wireOp",EDGE,"E211");var subQ371=sQuery(id+"F0.wireOp",EDGE,"E210");var subQ372=sQuery(id+"F0.wireOp",EDGE,"E209");var subQ373=sQuery(id+"F0.wireOp",EDGE,"E208");var subQ374=sQuery(id+"F0.wireOp",EDGE,"E207");var subQ375=sQuery(id+"F0.wireOp",EDGE,"E206");var subQ376=sQuery(id+"F0.wireOp",EDGE,"E205");var subQ377=sQuery(id+"F0.wireOp",EDGE,"E204");var subQ378=sQuery(id+"F0.wireOp",EDGE,"E203");var subQ379=sQuery(id+"F0.wireOp",EDGE,"E202");var subQ380=sQuery(id+"F0.wireOp",EDGE,"E201");var subQ381=sQuery(id+"F0.wireOp",EDGE,"E200");var subQ382=sQuery(id+"F0.wireOp",EDGE,"E199");var subQ383=sQuery(id+"F0.wireOp",EDGE,"E198");var subQ384=sQuery(id+"F0.wireOp",EDGE,"E197");var subQ385=sQuery(id+"F0.wireOp",EDGE,"E196");var subQ386=sQuery(id+"F0.wireOp",EDGE,"E195");var subQ387=sQuery(id+"F0.wireOp",EDGE,"E194");var subQ388=sQuery(id+"F0.wireOp",EDGE,"E193");var subQ389=sQuery(id+"F0.wireOp",EDGE,"E192");var subQ390=sQuery(id+"F0.wireOp",EDGE,"E191");var subQ391=sQuery(id+"F0.wireOp",EDGE,"E190");var subQ392=sQuery(id+"F0.wireOp",EDGE,"E189");var subQ393=sQuery(id+"F0.wireOp",EDGE,"E188");var subQ394=sQuery(id+"F0.wireOp",EDGE,"E187");var subQ395=sQuery(id+"F0.wireOp",EDGE,"E186");var subQ396=sQuery(id+"F0.wireOp",EDGE,"E185");var subQ397=sQuery(id+"F0.wireOp",EDGE,"E184");var subQ398=sQuery(id+"F0.wireOp",EDGE,"E183");var subQ399=sQuery(id+"F0.wireOp",EDGE,"E182");var subQ400=sQuery(id+"F0.wireOp",EDGE,"E181");var subQ401=sQuery(id+"F0.wireOp",EDGE,"E180");var subQ402=sQuery(id+"F0.wireOp",EDGE,"E179");var subQ403=sQuery(id+"F0.wireOp",EDGE,"E178");var subQ404=sQuery(id+"F0.wireOp",EDGE,"E177");var subQ405=sQuery(id+"F0.wireOp",EDGE,"E176");var subQ406=sQuery(id+"F0.wireOp",EDGE,"E175");var subQ407=sQuery(id+"F0.wireOp",EDGE,"E174");var subQ408=sQuery(id+"F0.wireOp",EDGE,"E173");var subQ409=sQuery(id+"F0.wireOp",EDGE,"E172");var subQ410=sQuery(id+"F0.wireOp",EDGE,"E171");var subQ411=sQuery(id+"F0.wireOp",EDGE,"E170");var subQ412=sQuery(id+"F0.wireOp",EDGE,"E169");var subQ413=sQuery(id+"F0.wireOp",EDGE,"E168");var subQ414=sQuery(id+"F0.wireOp",EDGE,"E167");var subQ415=sQuery(id+"F0.wireOp",EDGE,"E166");var subQ416=sQuery(id+"F0.wireOp",EDGE,"E165");var subQ417=sQuery(id+"F0.wireOp",EDGE,"E164");var subQ418=sQuery(id+"F0.wireOp",EDGE,"E163");var subQ419=sQuery(id+"F0.wireOp",EDGE,"E162");var subQ420=sQuery(id+"F0.wireOp",EDGE,"E161");var subQ421=sQuery(id+"F0.wireOp",EDGE,"E160");var subQ422=sQuery(id+"F0.wireOp",EDGE,"E159");var subQ423=sQuery(id+"F0.wireOp",EDGE,"E158");var subQ424=sQuery(id+"F0.wireOp",EDGE,"E157");var subQ425=sQuery(id+"F0.wireOp",EDGE,"E156");var subQ426=sQuery(id+"F0.wireOp",EDGE,"E155");var subQ427=sQuery(id+"F0.wireOp",EDGE,"E154");var subQ428=sQuery(id+"F0.wireOp",EDGE,"E153");var subQ429=sQuery(id+"F0.wireOp",EDGE,"E152");var subQ430=sQuery(id+"F0.wireOp",EDGE,"E151");var subQ431=sQuery(id+"F0.wireOp",EDGE,"E150");var subQ432=sQuery(id+"F0.wireOp",EDGE,"E149");var subQ433=sQuery(id+"F0.wireOp",EDGE,"E148");var subQ434=sQuery(id+"F0.wireOp",EDGE,"E147");var subQ435=sQuery(id+"F0.wireOp",EDGE,"E146");var subQ436=sQuery(id+"F0.wireOp",EDGE,"E145");var subQ437=sQuery(id+"F0.wireOp",EDGE,"E144");var subQ438=sQuery(id+"F0.wireOp",EDGE,"E143");var subQ439=sQuery(id+"F0.wireOp",EDGE,"E142");var subQ440=sQuery(id+"F0.wireOp",EDGE,"E141");var subQ441=sQuery(id+"F0.wireOp",EDGE,"E140");var subQ442=sQuery(id+"F0.wireOp",EDGE,"E139");var subQ443=sQuery(id+"F0.wireOp",EDGE,"E138");var subQ444=sQuery(id+"F0.wireOp",EDGE,"E137");var subQ445=sQuery(id+"F0.wireOp",EDGE,"E136");var subQ446=sQuery(id+"F0.wireOp",EDGE,"E135");var subQ447=sQuery(id+"F0.wireOp",EDGE,"E134");var subQ448=sQuery(id+"F0.wireOp",EDGE,"E133");var subQ449=sQuery(id+"F0.wireOp",EDGE,"E132");var subQ450=sQuery(id+"F0.wireOp",EDGE,"E131");var subQ451=sQuery(id+"F0.wireOp",EDGE,"E130");var subQ452=sQuery(id+"F0.wireOp",EDGE,"E129");var subQ453=sQuery(id+"F0.wireOp",EDGE,"E128");var subQ454=sQuery(id+"F0.wireOp",EDGE,"E127");var subQ455=sQuery(id+"F0.wireOp",EDGE,"E126");var subQ456=sQuery(id+"F0.wireOp",EDGE,"E125");var subQ457=sQuery(id+"F0.wireOp",EDGE,"E124");var subQ458=sQuery(id+"F0.wireOp",EDGE,"E123");var subQ459=sQuery(id+"F0.wireOp",EDGE,"E122");var subQ460=sQuery(id+"F0.wireOp",EDGE,"E121");var subQ461=sQuery(id+"F0.wireOp",EDGE,"E120");var subQ462=sQuery(id+"F0.wireOp",EDGE,"E119");var subQ463=sQuery(id+"F0.wireOp",EDGE,"E118");var subQ464=sQuery(id+"F0.wireOp",EDGE,"E117");var subQ465=sQuery(id+"F0.wireOp",EDGE,"E116");var subQ466=sQuery(id+"F0.wireOp",EDGE,"E115");var subQ467=sQuery(id+"F0.wireOp",EDGE,"E114");var subQ468=sQuery(id+"F0.wireOp",EDGE,"E113");var subQ469=sQuery(id+"F0.wireOp",EDGE,"E112");var subQ470=sQuery(id+"F0.wireOp",EDGE,"E111");var subQ471=sQuery(id+"F0.wireOp",EDGE,"E110");var subQ472=sQuery(id+"F0.wireOp",EDGE,"E109");var subQ473=sQuery(id+"F0.wireOp",EDGE,"E108");var subQ474=sQuery(id+"F0.wireOp",EDGE,"E107");var subQ475=sQuery(id+"F0.wireOp",EDGE,"E106");var subQ476=sQuery(id+"F0.wireOp",EDGE,"E105");var subQ477=sQuery(id+"F0.wireOp",EDGE,"E104");var subQ478=sQuery(id+"F0.wireOp",EDGE,"E103");var subQ479=sQuery(id+"F0.wireOp",EDGE,"E102");var subQ480=sQuery(id+"F0.wireOp",EDGE,"E101");var subQ481=sQuery(id+"F0.wireOp",EDGE,"E100");var subQ482=sQuery(id+"F0.wireOp",EDGE,"E99");var subQ483=sQuery(id+"F0.wireOp",EDGE,"E98");var subQ484=sQuery(id+"F0.wireOp",EDGE,"E97");var subQ485=sQuery(id+"F0.wireOp",EDGE,"E96");var subQ486=sQuery(id+"F0.wireOp",EDGE,"E95");var subQ487=sQuery(id+"F0.wireOp",EDGE,"E94");var subQ488=sQuery(id+"F0.wireOp",EDGE,"E93");var subQ489=sQuery(id+"F0.wireOp",EDGE,"E92");var subQ490=sQuery(id+"F0.wireOp",EDGE,"E91");var subQ491=sQuery(id+"F0.wireOp",EDGE,"E90");var subQ492=sQuery(id+"F0.wireOp",EDGE,"E89");var subQ493=sQuery(id+"F0.wireOp",EDGE,"E88");var subQ494=sQuery(id+"F0.wireOp",EDGE,"E87");var subQ495=sQuery(id+"F0.wireOp",EDGE,"E86");var subQ496=sQuery(id+"F0.wireOp",EDGE,"E85");var subQ497=sQuery(id+"F0.wireOp",EDGE,"E84");var subQ498=sQuery(id+"F0.wireOp",EDGE,"E83");var subQ499=sQuery(id+"F0.wireOp",EDGE,"E82");var subQ500=sQuery(id+"F0.wireOp",EDGE,"E81");var subQ501=sQuery(id+"F0.wireOp",EDGE,"E80");var subQ502=sQuery(id+"F0.wireOp",EDGE,"E79");var subQ503=sQuery(id+"F0.wireOp",EDGE,"E78");var subQ504=sQuery(id+"F0.wireOp",EDGE,"E77");var subQ505=sQuery(id+"F0.wireOp",EDGE,"E76");var subQ506=sQuery(id+"F0.wireOp",EDGE,"E75");var subQ507=sQuery(id+"F0.wireOp",EDGE,"E74");var subQ508=sQuery(id+"F0.wireOp",EDGE,"E73");var subQ509=sQuery(id+"F0.wireOp",EDGE,"E72");var subQ510=sQuery(id+"F0.wireOp",EDGE,"E71");var subQ511=sQuery(id+"F0.wireOp",EDGE,"E70");var subQ512=sQuery(id+"F0.wireOp",EDGE,"E69");var subQ513=sQuery(id+"F0.wireOp",EDGE,"E68");var subQ514=sQuery(id+"F0.wireOp",EDGE,"E67");var subQ515=sQuery(id+"F0.wireOp",EDGE,"E66");var subQ516=sQuery(id+"F0.wireOp",EDGE,"E65");var subQ517=sQuery(id+"F0.wireOp",EDGE,"E64");var subQ518=sQuery(id+"F0.wireOp",EDGE,"E63");var subQ519=sQuery(id+"F0.wireOp",EDGE,"E62");var subQ520=sQuery(id+"F0.wireOp",EDGE,"E61");var subQ521=sQuery(id+"F0.wireOp",EDGE,"E60");var subQ522=sQuery(id+"F0.wireOp",EDGE,"E59");var subQ523=sQuery(id+"F0.wireOp",EDGE,"E58");var subQ524=sQuery(id+"F0.wireOp",EDGE,"E57");var subQ525=sQuery(id+"F0.wireOp",EDGE,"E56");var subQ526=sQuery(id+"F0.wireOp",EDGE,"E55");var subQ527=sQuery(id+"F0.wireOp",EDGE,"E54");var subQ528=sQuery(id+"F0.wireOp",EDGE,"E53");var subQ529=sQuery(id+"F0.wireOp",EDGE,"E52");var subQ530=sQuery(id+"F0.wireOp",EDGE,"E51");var subQ531=sQuery(id+"F0.wireOp",EDGE,"E50");var subQ532=sQuery(id+"F0.wireOp",EDGE,"E49");var subQ533=sQuery(id+"F0.wireOp",EDGE,"E48");var subQ534=sQuery(id+"F0.wireOp",EDGE,"E47");var subQ535=sQuery(id+"F0.wireOp",EDGE,"E46");var subQ536=sQuery(id+"F0.wireOp",EDGE,"E45");var subQ537=sQuery(id+"F0.wireOp",EDGE,"E44");var subQ538=sQuery(id+"F0.wireOp",EDGE,"E43");var subQ539=sQuery(id+"F0.wireOp",EDGE,"E42");var subQ540=sQuery(id+"F0.wireOp",EDGE,"E41");var subQ541=sQuery(id+"F0.wireOp",EDGE,"E40");var subQ542=sQuery(id+"F0.wireOp",EDGE,"E39");var subQ543=sQuery(id+"F0.wireOp",EDGE,"E38");var subQ544=sQuery(id+"F0.wireOp",EDGE,"E37");var subQ545=sQuery(id+"F0.wireOp",EDGE,"E36");var subQ546=sQuery(id+"F0.wireOp",EDGE,"E35");var subQ547=sQuery(id+"F0.wireOp",EDGE,"E34");var subQ548=sQuery(id+"F0.wireOp",EDGE,"E33");var subQ549=sQuery(id+"F0.wireOp",EDGE,"E32");var subQ550=sQuery(id+"F0.wireOp",EDGE,"E31");var subQ551=sQuery(id+"F0.wireOp",EDGE,"E30");var subQ552=sQuery(id+"F0.wireOp",EDGE,"E29");var subQ553=sQuery(id+"F0.wireOp",EDGE,"E28");var subQ554=sQuery(id+"F0.wireOp",EDGE,"E27");var subQ555=sQuery(id+"F0.wireOp",EDGE,"E26");var subQ556=sQuery(id+"F0.wireOp",EDGE,"E25");var subQ557=sQuery(id+"F0.wireOp",EDGE,"E24");var subQ558=sQuery(id+"F0.wireOp",EDGE,"E23");var subQ559=sQuery(id+"F0.wireOp",EDGE,"E22");var subQ560=sQuery(id+"F0.wireOp",EDGE,"E21");var subQ561=sQuery(id+"F0.wireOp",EDGE,"E20");var subQ562=sQuery(id+"F0.wireOp",EDGE,"E19");var subQ563=sQuery(id+"F0.wireOp",EDGE,"E18");var subQ564=sQuery(id+"F0.wireOp",EDGE,"E17");var subQ565=sQuery(id+"F0.wireOp",EDGE,"E16");var subQ566=sQuery(id+"F0.wireOp",EDGE,"E15");var subQ567=sQuery(id+"F0.wireOp",EDGE,"E14");var subQ568=sQuery(id+"F0.wireOp",EDGE,"E13");var subQ569=sQuery(id+"F0.wireOp",EDGE,"E12");var subQ570=sQuery(id+"F0.wireOp",EDGE,"E11");var subQ571=sQuery(id+"F0.wireOp",EDGE,"E10");var subQ572=sQuery(id+"F0.wireOp",EDGE,"E9");var subQ573=sQuery(id+"F0.wireOp",EDGE,"E8");var subQ574=sQuery(id+"F0.wireOp",EDGE,"E7");var subQ575=sQuery(id+"F0.wireOp",EDGE,"E6");var subQ576=sQuery(id+"F0.wireOp",EDGE,"E5");var subQ577=sQuery(id+"F0.wireOp",EDGE,"E4");var subQ578=sQuery(id+"F0.wireOp",EDGE,"E3");var subQ579=sQuery(id+"F0.wireOp",EDGE,"E2");var subQ580=sQuery(id+"F0.wireOp",EDGE,"E1");var subQ581=sQuery(id+"F0.wireOp",EDGE,"E0");Q0=makeQuery(id+"F10.boolean.opBoolean","SPLIT",FACE,{"disambiguationData":[TD([makeQuery(id+"F1.opExtrude","SWEPT_FACE",FACE,{"disambiguationData":[OSD([subQ1])]})])],"derivedFrom":makeQuery(id+"F1.opExtrude","CAP_FACE",FACE,{"disambiguationData":[OSD([subQ581,subQ580,subQ579,subQ578,subQ577,subQ576,subQ575,subQ574,subQ573,subQ572,subQ571,subQ570,subQ569,subQ568,subQ567,subQ566,subQ565,subQ564,subQ563,subQ562,subQ561,subQ560,subQ559,subQ558,subQ557,subQ556,subQ555,subQ554,subQ553,subQ552,subQ551,subQ550,subQ549,subQ548,subQ547,subQ546,subQ545,subQ544,subQ543,subQ542,subQ541,subQ540,subQ539,subQ538,subQ537,subQ536,subQ535,subQ534,subQ533,subQ532,subQ531,subQ530,subQ529,subQ528,subQ527,subQ526,subQ525,subQ524,subQ523,subQ522,subQ521,subQ520,subQ519,subQ518,subQ517,subQ516,subQ515,subQ514,subQ513,subQ512,subQ511,subQ510,subQ509,subQ508,subQ507,subQ506,subQ505,subQ504,subQ503,subQ502,subQ501,subQ500,subQ499,subQ498,subQ497,subQ496,subQ495,subQ494,subQ493,subQ492,subQ491,subQ490,subQ489,subQ488,subQ487,subQ486,subQ485,subQ484,subQ483,subQ482,subQ481,subQ480,subQ479,subQ478,subQ477,subQ476,subQ475,subQ474,subQ473,subQ472,subQ471,subQ470,subQ469,subQ468,subQ467,subQ466,subQ465,subQ464,subQ463,subQ462,subQ461,subQ460,subQ459,subQ458,subQ457,subQ456,subQ455,subQ454,subQ453,subQ452,subQ451,subQ450,subQ449,subQ448,subQ447,subQ446,subQ445,subQ444,subQ443,subQ442,subQ441,subQ440,subQ439,subQ438,subQ437,subQ436,subQ435,subQ434,subQ433,subQ432,subQ431,subQ430,subQ429,subQ428,subQ427,subQ426,subQ425,subQ424,subQ423,subQ422,subQ421,subQ420,subQ419,subQ418,subQ417,subQ416,subQ415,subQ414,subQ413,subQ412,subQ411,subQ410,subQ409,subQ408,subQ407,subQ406,subQ405,subQ404,subQ403,subQ402,subQ401,subQ400,subQ399,subQ398,subQ397,subQ396,subQ395,subQ394,subQ393,subQ392,subQ391,subQ390,subQ389,subQ388,subQ387,subQ386,subQ385,subQ384,subQ383,subQ382,subQ381,subQ380,subQ379,subQ378,subQ377,subQ376,subQ375,subQ374,subQ373,subQ372,subQ371,subQ370,subQ369,subQ368,subQ367,subQ366,subQ365,subQ364,subQ363,subQ362,subQ361,subQ360,subQ359,subQ358,subQ357,subQ356,subQ355,subQ354,subQ353,subQ352,subQ351,subQ350,subQ349,subQ348,subQ347,subQ346,subQ345,subQ344,subQ343,subQ342,subQ341,subQ340,subQ339,subQ338,subQ337,subQ336,subQ335,subQ334,subQ333,subQ332,subQ331,subQ330,subQ329,subQ328,subQ327,subQ326,subQ325,subQ324,subQ323,subQ322,subQ321,subQ320,subQ319,subQ318,subQ317,subQ316,subQ315,subQ314,subQ313,subQ312,subQ311,subQ310,subQ309,subQ308,subQ307,subQ306,subQ305,subQ304,subQ303,subQ302,subQ301,subQ300,subQ299,subQ298,subQ297,subQ296,subQ295,subQ294,subQ293,subQ292,subQ291,subQ290,subQ289,subQ288,subQ287,subQ286,subQ285,subQ284,subQ283,subQ282,subQ281,subQ280,subQ279,subQ278,subQ277,subQ276,subQ275,subQ274,subQ273,subQ272,subQ271,subQ270,subQ269,subQ268,subQ267,subQ266,subQ265,subQ264,subQ263,subQ262,subQ261,subQ260,subQ259,subQ258,subQ257,subQ256,subQ255,subQ254,subQ253,subQ252,subQ251,subQ250,subQ249,subQ248,subQ247,subQ246,subQ245,subQ244,subQ243,subQ242,subQ1,subQ0,subQ241,subQ240,subQ239,subQ238,subQ237,subQ236,subQ235,subQ234,subQ233,subQ232,subQ231,subQ230,subQ229,subQ228,subQ227,subQ226,subQ225,subQ224,subQ223,subQ222,subQ221,subQ220,subQ219,subQ218,subQ217,subQ216,subQ215,subQ214,subQ213,subQ212,subQ211,subQ210,subQ209,subQ208,subQ207,subQ206,subQ205,subQ204,subQ203,subQ202,subQ201,subQ200,subQ199,subQ198,subQ197,subQ196,subQ195,subQ194,subQ193,subQ192,subQ191,subQ190,subQ189,subQ188,subQ187,subQ186,subQ185,subQ184,subQ183,subQ182,subQ181,subQ180,subQ179,subQ178,subQ177,subQ176,subQ175,subQ174,subQ173,subQ172,subQ171,subQ170,subQ169,subQ168,subQ167,subQ166,subQ165,subQ164,subQ163,subQ162,subQ161,subQ160,subQ159,subQ158,subQ157,subQ156,subQ155,subQ154,subQ153,subQ152,subQ151,subQ150,subQ149,subQ148,subQ147,subQ146,subQ145,subQ144,subQ143,subQ142,subQ141,subQ140,subQ139,subQ138,subQ137,subQ136,subQ135,subQ134,subQ133,subQ132,subQ131,subQ130,subQ129,subQ128,subQ127,subQ126,subQ125,subQ124,subQ123,subQ122,subQ121,subQ120,subQ119,subQ118,subQ117,subQ116,subQ115,subQ114,subQ113,subQ112,subQ111,subQ110,subQ109,subQ108,subQ107,subQ106,subQ105,subQ104,subQ103,subQ102,subQ101,subQ100,subQ99,subQ98,subQ97,subQ96,subQ95,subQ94,subQ93,subQ92,subQ91,subQ90,subQ89,subQ88,subQ87,subQ86,subQ85,subQ84,subQ83,subQ82,subQ81,subQ80,subQ79,subQ78,subQ77,subQ76,subQ75,subQ74,subQ73,subQ72,subQ71,subQ70,subQ69,subQ68,subQ67,subQ66,subQ65,subQ64,subQ63,subQ62,subQ61,subQ60,subQ59,subQ58,subQ57,subQ56,subQ55,subQ54,subQ53,subQ52,subQ51,subQ50,subQ49,subQ48,subQ47,subQ46,subQ45,subQ44,subQ43,subQ42,subQ41,subQ40,subQ39,subQ38,subQ37,subQ36,subQ35,subQ34,subQ33,subQ32,subQ31,subQ30,subQ29,subQ28,subQ27,subQ26,subQ25,subQ24,subQ23,subQ22,subQ21,subQ20,subQ19,subQ18,subQ17,subQ16,subQ15,subQ14,subQ13,subQ12,subQ11,subQ10,subQ9,subQ8,subQ7,subQ6,subQ5,subQ4])],"isStart":false})});}
            var sketch = newSketch(context, id + "F13", { "sketchPlane" : qUnion([Q0])});
            skLineSegment(sketch, "E2040.0", {"start": v(-117.47, 2.24) * mm, "end": v(-117.47, -7.77) * mm});
            skLineSegment(sketch, "E2041", {"start": v(-117.47, 2.24) * mm, "end": v(-118.47, 2.24) * mm});
            skLineSegment(sketch, "E2042", {"start": v(-118.47, 2.24) * mm, "end": v(-118.47, -7.77) * mm});
            skLineSegment(sketch, "E2043", {"start": v(-118.47, -7.77) * mm, "end": v(-117.47, -7.77) * mm});
            skSolve(sketch);
        }
        {
            var Q0;
            Q0 = qSketchRegion(id + "F13", true);
            var Q1;
            {var subQ0=sQuery(id+"F2.wireOp",EDGE,"E2024");var subQ1=sQuery(id+"F2.wireOp",EDGE,"E2023");Q1=makeQuery(id+"F12.boolean.opBoolean","MERGE",FACE,{"derivedFrom":[makeQuery(id+"F10.boolean.opBoolean","MERGE",FACE,{"derivedFrom":[makeQuery(id+"F9.boolean.opBoolean","MERGE",FACE,{"derivedFrom":[makeQuery(id+"F3.opExtrude","CAP_FACE",FACE,{"disambiguationData":[OSD([sQuery(id+"F2.wireOp",EDGE,"E1307"),sQuery(id+"F2.wireOp",EDGE,"E1308"),sQuery(id+"F2.wireOp",EDGE,"E1309"),sQuery(id+"F2.wireOp",EDGE,"E1310"),sQuery(id+"F2.wireOp",EDGE,"E1311"),sQuery(id+"F2.wireOp",EDGE,"E1312"),sQuery(id+"F2.wireOp",EDGE,"E1313"),sQuery(id+"F2.wireOp",EDGE,"E1314"),sQuery(id+"F2.wireOp",EDGE,"E1315"),sQuery(id+"F2.wireOp",EDGE,"E1316"),sQuery(id+"F2.wireOp",EDGE,"E1317"),sQuery(id+"F2.wireOp",EDGE,"E1318"),sQuery(id+"F2.wireOp",EDGE,"E1319"),sQuery(id+"F2.wireOp",EDGE,"E1320"),sQuery(id+"F2.wireOp",EDGE,"E1321"),sQuery(id+"F2.wireOp",EDGE,"E1322"),sQuery(id+"F2.wireOp",EDGE,"E1323"),sQuery(id+"F2.wireOp",EDGE,"E1324"),sQuery(id+"F2.wireOp",EDGE,"E1325"),sQuery(id+"F2.wireOp",EDGE,"E1326"),sQuery(id+"F2.wireOp",EDGE,"E1327"),sQuery(id+"F2.wireOp",EDGE,"E1328"),sQuery(id+"F2.wireOp",EDGE,"E1329"),sQuery(id+"F2.wireOp",EDGE,"E1330"),sQuery(id+"F2.wireOp",EDGE,"E1331"),sQuery(id+"F2.wireOp",EDGE,"E1332"),sQuery(id+"F2.wireOp",EDGE,"E1333"),sQuery(id+"F2.wireOp",EDGE,"E1334"),sQuery(id+"F2.wireOp",EDGE,"E1335"),sQuery(id+"F2.wireOp",EDGE,"E1336"),sQuery(id+"F2.wireOp",EDGE,"E1337"),sQuery(id+"F2.wireOp",EDGE,"E1338"),sQuery(id+"F2.wireOp",EDGE,"E1339"),sQuery(id+"F2.wireOp",EDGE,"E1340"),sQuery(id+"F2.wireOp",EDGE,"E1341"),sQuery(id+"F2.wireOp",EDGE,"E1342"),sQuery(id+"F2.wireOp",EDGE,"E1343"),sQuery(id+"F2.wireOp",EDGE,"E1344"),sQuery(id+"F2.wireOp",EDGE,"E1345"),sQuery(id+"F2.wireOp",EDGE,"E1346"),sQuery(id+"F2.wireOp",EDGE,"E1347"),sQuery(id+"F2.wireOp",EDGE,"E1348"),sQuery(id+"F2.wireOp",EDGE,"E1349"),sQuery(id+"F2.wireOp",EDGE,"E1350"),sQuery(id+"F2.wireOp",EDGE,"E1351"),sQuery(id+"F2.wireOp",EDGE,"E1352"),sQuery(id+"F2.wireOp",EDGE,"E1353"),sQuery(id+"F2.wireOp",EDGE,"E1354"),sQuery(id+"F2.wireOp",EDGE,"E1355"),sQuery(id+"F2.wireOp",EDGE,"E1356"),sQuery(id+"F2.wireOp",EDGE,"E1357"),sQuery(id+"F2.wireOp",EDGE,"E1358"),sQuery(id+"F2.wireOp",EDGE,"E1359"),sQuery(id+"F2.wireOp",EDGE,"E1360"),sQuery(id+"F2.wireOp",EDGE,"E1361"),sQuery(id+"F2.wireOp",EDGE,"E1362"),sQuery(id+"F2.wireOp",EDGE,"E1363"),sQuery(id+"F2.wireOp",EDGE,"E1364"),sQuery(id+"F2.wireOp",EDGE,"E1365"),sQuery(id+"F2.wireOp",EDGE,"E1366"),sQuery(id+"F2.wireOp",EDGE,"E1367"),sQuery(id+"F2.wireOp",EDGE,"E1368"),sQuery(id+"F2.wireOp",EDGE,"E1369"),sQuery(id+"F2.wireOp",EDGE,"E1370"),sQuery(id+"F2.wireOp",EDGE,"E1371"),sQuery(id+"F2.wireOp",EDGE,"E1372"),sQuery(id+"F2.wireOp",EDGE,"E1373"),sQuery(id+"F2.wireOp",EDGE,"E1374"),sQuery(id+"F2.wireOp",EDGE,"E1375"),sQuery(id+"F2.wireOp",EDGE,"E1376"),sQuery(id+"F2.wireOp",EDGE,"E1377"),sQuery(id+"F2.wireOp",EDGE,"E1378"),sQuery(id+"F2.wireOp",EDGE,"E1379"),sQuery(id+"F2.wireOp",EDGE,"E1380"),sQuery(id+"F2.wireOp",EDGE,"E1381"),sQuery(id+"F2.wireOp",EDGE,"E1382"),sQuery(id+"F2.wireOp",EDGE,"E1383"),sQuery(id+"F2.wireOp",EDGE,"E1384"),sQuery(id+"F2.wireOp",EDGE,"E1385"),sQuery(id+"F2.wireOp",EDGE,"E1386"),sQuery(id+"F2.wireOp",EDGE,"E1387"),sQuery(id+"F2.wireOp",EDGE,"E1388"),sQuery(id+"F2.wireOp",EDGE,"E1389"),sQuery(id+"F2.wireOp",EDGE,"E1390"),sQuery(id+"F2.wireOp",EDGE,"E1391"),sQuery(id+"F2.wireOp",EDGE,"E1392"),sQuery(id+"F2.wireOp",EDGE,"E1393"),sQuery(id+"F2.wireOp",EDGE,"E1394"),sQuery(id+"F2.wireOp",EDGE,"E1395"),sQuery(id+"F2.wireOp",EDGE,"E1396"),sQuery(id+"F2.wireOp",EDGE,"E1397"),sQuery(id+"F2.wireOp",EDGE,"E1398"),sQuery(id+"F2.wireOp",EDGE,"E1399"),sQuery(id+"F2.wireOp",EDGE,"E1400"),sQuery(id+"F2.wireOp",EDGE,"E1401"),sQuery(id+"F2.wireOp",EDGE,"E1402"),sQuery(id+"F2.wireOp",EDGE,"E1403"),sQuery(id+"F2.wireOp",EDGE,"E1404"),sQuery(id+"F2.wireOp",EDGE,"E1405"),sQuery(id+"F2.wireOp",EDGE,"E1406"),sQuery(id+"F2.wireOp",EDGE,"E1407"),sQuery(id+"F2.wireOp",EDGE,"E1408"),sQuery(id+"F2.wireOp",EDGE,"E1409"),sQuery(id+"F2.wireOp",EDGE,"E1410"),sQuery(id+"F2.wireOp",EDGE,"E1411"),sQuery(id+"F2.wireOp",EDGE,"E1412"),sQuery(id+"F2.wireOp",EDGE,"E1413"),sQuery(id+"F2.wireOp",EDGE,"E1414"),sQuery(id+"F2.wireOp",EDGE,"E1415"),sQuery(id+"F2.wireOp",EDGE,"E1416"),sQuery(id+"F2.wireOp",EDGE,"E1417"),sQuery(id+"F2.wireOp",EDGE,"E1418"),sQuery(id+"F2.wireOp",EDGE,"E1419"),sQuery(id+"F2.wireOp",EDGE,"E1420"),sQuery(id+"F2.wireOp",EDGE,"E1421"),sQuery(id+"F2.wireOp",EDGE,"E1422"),sQuery(id+"F2.wireOp",EDGE,"E1423"),sQuery(id+"F2.wireOp",EDGE,"E1424"),sQuery(id+"F2.wireOp",EDGE,"E1425"),sQuery(id+"F2.wireOp",EDGE,"E1426"),sQuery(id+"F2.wireOp",EDGE,"E1427"),sQuery(id+"F2.wireOp",EDGE,"E1428"),sQuery(id+"F2.wireOp",EDGE,"E1429"),sQuery(id+"F2.wireOp",EDGE,"E1430"),sQuery(id+"F2.wireOp",EDGE,"E1431"),sQuery(id+"F2.wireOp",EDGE,"E1432"),sQuery(id+"F2.wireOp",EDGE,"E1433"),sQuery(id+"F2.wireOp",EDGE,"E1434"),sQuery(id+"F2.wireOp",EDGE,"E1435"),sQuery(id+"F2.wireOp",EDGE,"E1436"),sQuery(id+"F2.wireOp",EDGE,"E1437"),sQuery(id+"F2.wireOp",EDGE,"E1438"),sQuery(id+"F2.wireOp",EDGE,"E1439"),sQuery(id+"F2.wireOp",EDGE,"E1440"),sQuery(id+"F2.wireOp",EDGE,"E1441"),sQuery(id+"F2.wireOp",EDGE,"E1442"),sQuery(id+"F2.wireOp",EDGE,"E1443"),sQuery(id+"F2.wireOp",EDGE,"E1444"),sQuery(id+"F2.wireOp",EDGE,"E1445"),sQuery(id+"F2.wireOp",EDGE,"E1446"),sQuery(id+"F2.wireOp",EDGE,"E1447"),sQuery(id+"F2.wireOp",EDGE,"E1448"),sQuery(id+"F2.wireOp",EDGE,"E1449"),sQuery(id+"F2.wireOp",EDGE,"E1450"),sQuery(id+"F2.wireOp",EDGE,"E1451"),sQuery(id+"F2.wireOp",EDGE,"E1452"),sQuery(id+"F2.wireOp",EDGE,"E1453"),sQuery(id+"F2.wireOp",EDGE,"E1454"),sQuery(id+"F2.wireOp",EDGE,"E1455"),sQuery(id+"F2.wireOp",EDGE,"E1456"),sQuery(id+"F2.wireOp",EDGE,"E1457"),sQuery(id+"F2.wireOp",EDGE,"E1458"),sQuery(id+"F2.wireOp",EDGE,"E1459"),sQuery(id+"F2.wireOp",EDGE,"E1742"),sQuery(id+"F2.wireOp",EDGE,"E1743"),sQuery(id+"F2.wireOp",EDGE,"E1744"),sQuery(id+"F2.wireOp",EDGE,"E1745"),sQuery(id+"F2.wireOp",EDGE,"E1746"),sQuery(id+"F2.wireOp",EDGE,"E1747"),sQuery(id+"F2.wireOp",EDGE,"E1748"),sQuery(id+"F2.wireOp",EDGE,"E1749"),sQuery(id+"F2.wireOp",EDGE,"E1750"),sQuery(id+"F2.wireOp",EDGE,"E1751"),sQuery(id+"F2.wireOp",EDGE,"E1752"),sQuery(id+"F2.wireOp",EDGE,"E1753"),sQuery(id+"F2.wireOp",EDGE,"E1754"),sQuery(id+"F2.wireOp",EDGE,"E1755"),sQuery(id+"F2.wireOp",EDGE,"E1756"),sQuery(id+"F2.wireOp",EDGE,"E1757"),sQuery(id+"F2.wireOp",EDGE,"E1758"),sQuery(id+"F2.wireOp",EDGE,"E1759"),sQuery(id+"F2.wireOp",EDGE,"E1760"),sQuery(id+"F2.wireOp",EDGE,"E1761"),sQuery(id+"F2.wireOp",EDGE,"E1762"),sQuery(id+"F2.wireOp",EDGE,"E1763"),sQuery(id+"F2.wireOp",EDGE,"E1764"),sQuery(id+"F2.wireOp",EDGE,"E1765"),sQuery(id+"F2.wireOp",EDGE,"E1766"),sQuery(id+"F2.wireOp",EDGE,"E1767"),sQuery(id+"F2.wireOp",EDGE,"E1768"),sQuery(id+"F2.wireOp",EDGE,"E1769"),sQuery(id+"F2.wireOp",EDGE,"E1770"),sQuery(id+"F2.wireOp",EDGE,"E1771"),sQuery(id+"F2.wireOp",EDGE,"E1772"),sQuery(id+"F2.wireOp",EDGE,"E1773"),sQuery(id+"F2.wireOp",EDGE,"E1774"),sQuery(id+"F2.wireOp",EDGE,"E1775"),sQuery(id+"F2.wireOp",EDGE,"E1776"),sQuery(id+"F2.wireOp",EDGE,"E1777"),sQuery(id+"F2.wireOp",EDGE,"E1778"),sQuery(id+"F2.wireOp",EDGE,"E1779"),sQuery(id+"F2.wireOp",EDGE,"E1780"),sQuery(id+"F2.wireOp",EDGE,"E1781"),sQuery(id+"F2.wireOp",EDGE,"E1782"),sQuery(id+"F2.wireOp",EDGE,"E1783"),sQuery(id+"F2.wireOp",EDGE,"E1784"),sQuery(id+"F2.wireOp",EDGE,"E1785"),sQuery(id+"F2.wireOp",EDGE,"E1786"),sQuery(id+"F2.wireOp",EDGE,"E1787"),sQuery(id+"F2.wireOp",EDGE,"E1788"),sQuery(id+"F2.wireOp",EDGE,"E1789"),sQuery(id+"F2.wireOp",EDGE,"E1790"),sQuery(id+"F2.wireOp",EDGE,"E1791"),sQuery(id+"F2.wireOp",EDGE,"E1792"),sQuery(id+"F2.wireOp",EDGE,"E1793"),sQuery(id+"F2.wireOp",EDGE,"E1794"),sQuery(id+"F2.wireOp",EDGE,"E1795"),sQuery(id+"F2.wireOp",EDGE,"E1796"),sQuery(id+"F2.wireOp",EDGE,"E1797"),sQuery(id+"F2.wireOp",EDGE,"E1798"),sQuery(id+"F2.wireOp",EDGE,"E1799"),sQuery(id+"F2.wireOp",EDGE,"E1800"),sQuery(id+"F2.wireOp",EDGE,"E1801"),sQuery(id+"F2.wireOp",EDGE,"E1802"),sQuery(id+"F2.wireOp",EDGE,"E1803"),sQuery(id+"F2.wireOp",EDGE,"E1804"),sQuery(id+"F2.wireOp",EDGE,"E1805"),sQuery(id+"F2.wireOp",EDGE,"E1806"),sQuery(id+"F2.wireOp",EDGE,"E1807"),sQuery(id+"F2.wireOp",EDGE,"E1808"),sQuery(id+"F2.wireOp",EDGE,"E1809"),sQuery(id+"F2.wireOp",EDGE,"E1810"),sQuery(id+"F2.wireOp",EDGE,"E1811"),sQuery(id+"F2.wireOp",EDGE,"E1812"),sQuery(id+"F2.wireOp",EDGE,"E1813"),sQuery(id+"F2.wireOp",EDGE,"E1814"),sQuery(id+"F2.wireOp",EDGE,"E1815"),sQuery(id+"F2.wireOp",EDGE,"E1816"),sQuery(id+"F2.wireOp",EDGE,"E1817"),sQuery(id+"F2.wireOp",EDGE,"E1818"),sQuery(id+"F2.wireOp",EDGE,"E1819"),sQuery(id+"F2.wireOp",EDGE,"E1820"),sQuery(id+"F2.wireOp",EDGE,"E1821"),sQuery(id+"F2.wireOp",EDGE,"E1822"),sQuery(id+"F2.wireOp",EDGE,"E1823"),sQuery(id+"F2.wireOp",EDGE,"E1824"),sQuery(id+"F2.wireOp",EDGE,"E1825"),sQuery(id+"F2.wireOp",EDGE,"E1826"),sQuery(id+"F2.wireOp",EDGE,"E1827"),sQuery(id+"F2.wireOp",EDGE,"E1828"),sQuery(id+"F2.wireOp",EDGE,"E1829"),sQuery(id+"F2.wireOp",EDGE,"E1830"),sQuery(id+"F2.wireOp",EDGE,"E1831"),sQuery(id+"F2.wireOp",EDGE,"E1832"),sQuery(id+"F2.wireOp",EDGE,"E1833"),sQuery(id+"F2.wireOp",EDGE,"E1834"),sQuery(id+"F2.wireOp",EDGE,"E1835"),sQuery(id+"F2.wireOp",EDGE,"E1836"),sQuery(id+"F2.wireOp",EDGE,"E1837"),sQuery(id+"F2.wireOp",EDGE,"E1838"),sQuery(id+"F2.wireOp",EDGE,"E1839"),sQuery(id+"F2.wireOp",EDGE,"E1840"),sQuery(id+"F2.wireOp",EDGE,"E1841"),sQuery(id+"F2.wireOp",EDGE,"E1842"),sQuery(id+"F2.wireOp",EDGE,"E1843"),sQuery(id+"F2.wireOp",EDGE,"E1844"),sQuery(id+"F2.wireOp",EDGE,"E1845"),sQuery(id+"F2.wireOp",EDGE,"E1846"),sQuery(id+"F2.wireOp",EDGE,"E1847"),sQuery(id+"F2.wireOp",EDGE,"E1848"),sQuery(id+"F2.wireOp",EDGE,"E1849"),sQuery(id+"F2.wireOp",EDGE,"E1850"),sQuery(id+"F2.wireOp",EDGE,"E1851"),sQuery(id+"F2.wireOp",EDGE,"E1852"),sQuery(id+"F2.wireOp",EDGE,"E1853"),sQuery(id+"F2.wireOp",EDGE,"E1854"),sQuery(id+"F2.wireOp",EDGE,"E1855"),sQuery(id+"F2.wireOp",EDGE,"E1856"),sQuery(id+"F2.wireOp",EDGE,"E1857"),sQuery(id+"F2.wireOp",EDGE,"E1858"),sQuery(id+"F2.wireOp",EDGE,"E1859"),sQuery(id+"F2.wireOp",EDGE,"E1860"),sQuery(id+"F2.wireOp",EDGE,"E1861"),sQuery(id+"F2.wireOp",EDGE,"E1862"),sQuery(id+"F2.wireOp",EDGE,"E1863"),sQuery(id+"F2.wireOp",EDGE,"E1864"),sQuery(id+"F2.wireOp",EDGE,"E1865"),sQuery(id+"F2.wireOp",EDGE,"E1866"),sQuery(id+"F2.wireOp",EDGE,"E1867"),sQuery(id+"F2.wireOp",EDGE,"E1868"),sQuery(id+"F2.wireOp",EDGE,"E1869"),sQuery(id+"F2.wireOp",EDGE,"E1870"),sQuery(id+"F2.wireOp",EDGE,"E1871"),sQuery(id+"F2.wireOp",EDGE,"E1872"),sQuery(id+"F2.wireOp",EDGE,"E1873"),sQuery(id+"F2.wireOp",EDGE,"E1874"),sQuery(id+"F2.wireOp",EDGE,"E1875"),sQuery(id+"F2.wireOp",EDGE,"E1876"),sQuery(id+"F2.wireOp",EDGE,"E1877"),sQuery(id+"F2.wireOp",EDGE,"E1878"),sQuery(id+"F2.wireOp",EDGE,"E1879"),sQuery(id+"F2.wireOp",EDGE,"E1880"),sQuery(id+"F2.wireOp",EDGE,"E1881"),sQuery(id+"F2.wireOp",EDGE,"E1882"),sQuery(id+"F2.wireOp",EDGE,"E1883"),sQuery(id+"F2.wireOp",EDGE,"E1884"),sQuery(id+"F2.wireOp",EDGE,"E1885"),sQuery(id+"F2.wireOp",EDGE,"E1886"),sQuery(id+"F2.wireOp",EDGE,"E1887"),sQuery(id+"F2.wireOp",EDGE,"E1888"),sQuery(id+"F2.wireOp",EDGE,"E1889"),sQuery(id+"F2.wireOp",EDGE,"E1890"),sQuery(id+"F2.wireOp",EDGE,"E1891"),sQuery(id+"F2.wireOp",EDGE,"E1892"),sQuery(id+"F2.wireOp",EDGE,"E1893"),sQuery(id+"F2.wireOp",EDGE,"E1894"),sQuery(id+"F2.wireOp",EDGE,"E1895"),sQuery(id+"F2.wireOp",EDGE,"E1896"),sQuery(id+"F2.wireOp",EDGE,"E1897"),sQuery(id+"F2.wireOp",EDGE,"E1898"),sQuery(id+"F2.wireOp",EDGE,"E1899"),sQuery(id+"F2.wireOp",EDGE,"E1900"),sQuery(id+"F2.wireOp",EDGE,"E1901"),sQuery(id+"F2.wireOp",EDGE,"E1902"),sQuery(id+"F2.wireOp",EDGE,"E1903"),sQuery(id+"F2.wireOp",EDGE,"E1904"),sQuery(id+"F2.wireOp",EDGE,"E1905"),sQuery(id+"F2.wireOp",EDGE,"E1906"),sQuery(id+"F2.wireOp",EDGE,"E1907"),sQuery(id+"F2.wireOp",EDGE,"E1908"),sQuery(id+"F2.wireOp",EDGE,"E1909"),sQuery(id+"F2.wireOp",EDGE,"E1910"),sQuery(id+"F2.wireOp",EDGE,"E1911"),sQuery(id+"F2.wireOp",EDGE,"E1912"),sQuery(id+"F2.wireOp",EDGE,"E1913"),sQuery(id+"F2.wireOp",EDGE,"E1914"),sQuery(id+"F2.wireOp",EDGE,"E1915"),sQuery(id+"F2.wireOp",EDGE,"E1916"),sQuery(id+"F2.wireOp",EDGE,"E1917"),sQuery(id+"F2.wireOp",EDGE,"E1918"),sQuery(id+"F2.wireOp",EDGE,"E1919"),sQuery(id+"F2.wireOp",EDGE,"E1920"),sQuery(id+"F2.wireOp",EDGE,"E1921"),sQuery(id+"F2.wireOp",EDGE,"E1922"),sQuery(id+"F2.wireOp",EDGE,"E1923"),sQuery(id+"F2.wireOp",EDGE,"E1924"),sQuery(id+"F2.wireOp",EDGE,"E1925"),sQuery(id+"F2.wireOp",EDGE,"E1926"),sQuery(id+"F2.wireOp",EDGE,"E1927"),sQuery(id+"F2.wireOp",EDGE,"E1928"),sQuery(id+"F2.wireOp",EDGE,"E1929"),sQuery(id+"F2.wireOp",EDGE,"E1930"),sQuery(id+"F2.wireOp",EDGE,"E1931"),sQuery(id+"F2.wireOp",EDGE,"E1932"),sQuery(id+"F2.wireOp",EDGE,"E1933"),sQuery(id+"F2.wireOp",EDGE,"E1934"),sQuery(id+"F2.wireOp",EDGE,"E1935"),sQuery(id+"F2.wireOp",EDGE,"E1936"),sQuery(id+"F2.wireOp",EDGE,"E1937"),sQuery(id+"F2.wireOp",EDGE,"E1938"),sQuery(id+"F2.wireOp",EDGE,"E1939"),sQuery(id+"F2.wireOp",EDGE,"E1940"),sQuery(id+"F2.wireOp",EDGE,"E1941"),sQuery(id+"F2.wireOp",EDGE,"E1942"),sQuery(id+"F2.wireOp",EDGE,"E1943"),sQuery(id+"F2.wireOp",EDGE,"E1944"),sQuery(id+"F2.wireOp",EDGE,"E1945"),sQuery(id+"F2.wireOp",EDGE,"E1946"),sQuery(id+"F2.wireOp",EDGE,"E1947"),sQuery(id+"F2.wireOp",EDGE,"E1948"),sQuery(id+"F2.wireOp",EDGE,"E1949"),sQuery(id+"F2.wireOp",EDGE,"E1950"),sQuery(id+"F2.wireOp",EDGE,"E1951"),sQuery(id+"F2.wireOp",EDGE,"E1952"),sQuery(id+"F2.wireOp",EDGE,"E1953"),sQuery(id+"F2.wireOp",EDGE,"E1954"),sQuery(id+"F2.wireOp",EDGE,"E1955"),sQuery(id+"F2.wireOp",EDGE,"E1956"),sQuery(id+"F2.wireOp",EDGE,"E1957"),sQuery(id+"F2.wireOp",EDGE,"E1958"),sQuery(id+"F2.wireOp",EDGE,"E1959"),sQuery(id+"F2.wireOp",EDGE,"E1960"),sQuery(id+"F2.wireOp",EDGE,"E1961"),sQuery(id+"F2.wireOp",EDGE,"E1962"),sQuery(id+"F2.wireOp",EDGE,"E1963"),sQuery(id+"F2.wireOp",EDGE,"E1964"),sQuery(id+"F2.wireOp",EDGE,"E1965"),sQuery(id+"F2.wireOp",EDGE,"E1966"),sQuery(id+"F2.wireOp",EDGE,"E1967"),sQuery(id+"F2.wireOp",EDGE,"E1968"),sQuery(id+"F2.wireOp",EDGE,"E1969"),sQuery(id+"F2.wireOp",EDGE,"E1970"),sQuery(id+"F2.wireOp",EDGE,"E1971"),sQuery(id+"F2.wireOp",EDGE,"E1972"),sQuery(id+"F2.wireOp",EDGE,"E1973"),sQuery(id+"F2.wireOp",EDGE,"E1974"),sQuery(id+"F2.wireOp",EDGE,"E1975"),sQuery(id+"F2.wireOp",EDGE,"E1976"),sQuery(id+"F2.wireOp",EDGE,"E1977"),sQuery(id+"F2.wireOp",EDGE,"E1978"),sQuery(id+"F2.wireOp",EDGE,"E1979"),sQuery(id+"F2.wireOp",EDGE,"E1980"),sQuery(id+"F2.wireOp",EDGE,"E1981"),sQuery(id+"F2.wireOp",EDGE,"E1982"),sQuery(id+"F2.wireOp",EDGE,"E1983"),sQuery(id+"F2.wireOp",EDGE,"E1984"),sQuery(id+"F2.wireOp",EDGE,"E1985"),sQuery(id+"F2.wireOp",EDGE,"E1986"),sQuery(id+"F2.wireOp",EDGE,"E1987"),sQuery(id+"F2.wireOp",EDGE,"E1988"),sQuery(id+"F2.wireOp",EDGE,"E1989"),sQuery(id+"F2.wireOp",EDGE,"E1990"),sQuery(id+"F2.wireOp",EDGE,"E1991"),sQuery(id+"F2.wireOp",EDGE,"E1992"),sQuery(id+"F2.wireOp",EDGE,"E1993"),sQuery(id+"F2.wireOp",EDGE,"E1994"),sQuery(id+"F2.wireOp",EDGE,"E1995"),sQuery(id+"F2.wireOp",EDGE,"E1996"),sQuery(id+"F2.wireOp",EDGE,"E1997"),sQuery(id+"F2.wireOp",EDGE,"E1998"),sQuery(id+"F2.wireOp",EDGE,"E1999"),sQuery(id+"F2.wireOp",EDGE,"E2000"),sQuery(id+"F2.wireOp",EDGE,"E2001"),sQuery(id+"F2.wireOp",EDGE,"E2002"),sQuery(id+"F2.wireOp",EDGE,"E2003"),sQuery(id+"F2.wireOp",EDGE,"E2004"),sQuery(id+"F2.wireOp",EDGE,"E2005"),sQuery(id+"F2.wireOp",EDGE,"E2006"),sQuery(id+"F2.wireOp",EDGE,"E2007"),sQuery(id+"F2.wireOp",EDGE,"E2008"),sQuery(id+"F2.wireOp",EDGE,"E2009"),sQuery(id+"F2.wireOp",EDGE,"E2010"),sQuery(id+"F2.wireOp",EDGE,"E2011"),sQuery(id+"F2.wireOp",EDGE,"E2012"),sQuery(id+"F2.wireOp",EDGE,"E2013"),sQuery(id+"F2.wireOp",EDGE,"E2014"),sQuery(id+"F2.wireOp",EDGE,"E2015"),sQuery(id+"F2.wireOp",EDGE,"E2016"),sQuery(id+"F2.wireOp",EDGE,"E2017"),sQuery(id+"F2.wireOp",EDGE,"E2018"),sQuery(id+"F2.wireOp",EDGE,"E2019"),sQuery(id+"F2.wireOp",EDGE,"E2020"),sQuery(id+"F2.wireOp",EDGE,"E2021"),sQuery(id+"F2.wireOp",EDGE,"E2022"),subQ0,sQuery(id+"F2.wireOp",EDGE,"E2025"),sQuery(id+"F2.wireOp",EDGE,"E2026")])],"isStart":false}),makeQuery(id+"F3.opExtrude","CAP_FACE",FACE,{"disambiguationData":[OSD([sQuery(id+"F2.wireOp",EDGE,"E1146"),sQuery(id+"F2.wireOp",EDGE,"E1147"),sQuery(id+"F2.wireOp",EDGE,"E1148"),sQuery(id+"F2.wireOp",EDGE,"E1149"),sQuery(id+"F2.wireOp",EDGE,"E1150"),sQuery(id+"F2.wireOp",EDGE,"E1151"),sQuery(id+"F2.wireOp",EDGE,"E1152"),sQuery(id+"F2.wireOp",EDGE,"E1153"),sQuery(id+"F2.wireOp",EDGE,"E1154"),sQuery(id+"F2.wireOp",EDGE,"E1155"),sQuery(id+"F2.wireOp",EDGE,"E1156"),sQuery(id+"F2.wireOp",EDGE,"E1157"),sQuery(id+"F2.wireOp",EDGE,"E1158"),sQuery(id+"F2.wireOp",EDGE,"E1159"),sQuery(id+"F2.wireOp",EDGE,"E1160"),sQuery(id+"F2.wireOp",EDGE,"E1161"),sQuery(id+"F2.wireOp",EDGE,"E1162"),sQuery(id+"F2.wireOp",EDGE,"E1163"),sQuery(id+"F2.wireOp",EDGE,"E1164"),sQuery(id+"F2.wireOp",EDGE,"E1165"),sQuery(id+"F2.wireOp",EDGE,"E1166"),sQuery(id+"F2.wireOp",EDGE,"E1167"),sQuery(id+"F2.wireOp",EDGE,"E1168"),sQuery(id+"F2.wireOp",EDGE,"E1169"),sQuery(id+"F2.wireOp",EDGE,"E1170"),sQuery(id+"F2.wireOp",EDGE,"E1171"),sQuery(id+"F2.wireOp",EDGE,"E1172"),sQuery(id+"F2.wireOp",EDGE,"E1173"),sQuery(id+"F2.wireOp",EDGE,"E1174"),sQuery(id+"F2.wireOp",EDGE,"E1175"),sQuery(id+"F2.wireOp",EDGE,"E1176"),sQuery(id+"F2.wireOp",EDGE,"E1177"),sQuery(id+"F2.wireOp",EDGE,"E1178"),sQuery(id+"F2.wireOp",EDGE,"E1179"),sQuery(id+"F2.wireOp",EDGE,"E1180"),sQuery(id+"F2.wireOp",EDGE,"E1181"),sQuery(id+"F2.wireOp",EDGE,"E1182"),sQuery(id+"F2.wireOp",EDGE,"E1183"),sQuery(id+"F2.wireOp",EDGE,"E1184"),sQuery(id+"F2.wireOp",EDGE,"E1185"),sQuery(id+"F2.wireOp",EDGE,"E1186"),sQuery(id+"F2.wireOp",EDGE,"E1187"),sQuery(id+"F2.wireOp",EDGE,"E1188"),sQuery(id+"F2.wireOp",EDGE,"E1189"),sQuery(id+"F2.wireOp",EDGE,"E1190"),sQuery(id+"F2.wireOp",EDGE,"E1191"),sQuery(id+"F2.wireOp",EDGE,"E1192"),sQuery(id+"F2.wireOp",EDGE,"E1193"),sQuery(id+"F2.wireOp",EDGE,"E1194"),sQuery(id+"F2.wireOp",EDGE,"E1195"),sQuery(id+"F2.wireOp",EDGE,"E1196"),sQuery(id+"F2.wireOp",EDGE,"E1197"),sQuery(id+"F2.wireOp",EDGE,"E1198"),sQuery(id+"F2.wireOp",EDGE,"E1199"),sQuery(id+"F2.wireOp",EDGE,"E1200"),sQuery(id+"F2.wireOp",EDGE,"E1201"),sQuery(id+"F2.wireOp",EDGE,"E1202"),sQuery(id+"F2.wireOp",EDGE,"E1203"),sQuery(id+"F2.wireOp",EDGE,"E1204"),sQuery(id+"F2.wireOp",EDGE,"E1205"),sQuery(id+"F2.wireOp",EDGE,"E1206"),sQuery(id+"F2.wireOp",EDGE,"E1207"),sQuery(id+"F2.wireOp",EDGE,"E1208"),sQuery(id+"F2.wireOp",EDGE,"E1209"),sQuery(id+"F2.wireOp",EDGE,"E1210"),sQuery(id+"F2.wireOp",EDGE,"E1211"),sQuery(id+"F2.wireOp",EDGE,"E1212"),sQuery(id+"F2.wireOp",EDGE,"E1213"),sQuery(id+"F2.wireOp",EDGE,"E1214"),sQuery(id+"F2.wireOp",EDGE,"E1215"),sQuery(id+"F2.wireOp",EDGE,"E1216"),sQuery(id+"F2.wireOp",EDGE,"E1217"),sQuery(id+"F2.wireOp",EDGE,"E1218"),sQuery(id+"F2.wireOp",EDGE,"E1219"),sQuery(id+"F2.wireOp",EDGE,"E1220"),sQuery(id+"F2.wireOp",EDGE,"E1221"),sQuery(id+"F2.wireOp",EDGE,"E1222"),sQuery(id+"F2.wireOp",EDGE,"E1223"),sQuery(id+"F2.wireOp",EDGE,"E1224"),sQuery(id+"F2.wireOp",EDGE,"E1225"),sQuery(id+"F2.wireOp",EDGE,"E1226"),sQuery(id+"F2.wireOp",EDGE,"E1227"),sQuery(id+"F2.wireOp",EDGE,"E1228"),sQuery(id+"F2.wireOp",EDGE,"E1229"),sQuery(id+"F2.wireOp",EDGE,"E1230"),sQuery(id+"F2.wireOp",EDGE,"E1231"),sQuery(id+"F2.wireOp",EDGE,"E1232"),sQuery(id+"F2.wireOp",EDGE,"E1233"),sQuery(id+"F2.wireOp",EDGE,"E1234"),sQuery(id+"F2.wireOp",EDGE,"E1235"),sQuery(id+"F2.wireOp",EDGE,"E1236"),sQuery(id+"F2.wireOp",EDGE,"E1237"),sQuery(id+"F2.wireOp",EDGE,"E1238"),sQuery(id+"F2.wireOp",EDGE,"E1239"),sQuery(id+"F2.wireOp",EDGE,"E1240"),sQuery(id+"F2.wireOp",EDGE,"E1241"),sQuery(id+"F2.wireOp",EDGE,"E1242"),sQuery(id+"F2.wireOp",EDGE,"E1243"),sQuery(id+"F2.wireOp",EDGE,"E1244"),sQuery(id+"F2.wireOp",EDGE,"E1245"),sQuery(id+"F2.wireOp",EDGE,"E1246"),sQuery(id+"F2.wireOp",EDGE,"E1247"),sQuery(id+"F2.wireOp",EDGE,"E1248"),sQuery(id+"F2.wireOp",EDGE,"E1249"),sQuery(id+"F2.wireOp",EDGE,"E1250"),sQuery(id+"F2.wireOp",EDGE,"E1251"),sQuery(id+"F2.wireOp",EDGE,"E1252"),sQuery(id+"F2.wireOp",EDGE,"E1253"),sQuery(id+"F2.wireOp",EDGE,"E1254"),sQuery(id+"F2.wireOp",EDGE,"E1255"),sQuery(id+"F2.wireOp",EDGE,"E1256"),sQuery(id+"F2.wireOp",EDGE,"E1257"),sQuery(id+"F2.wireOp",EDGE,"E1258"),sQuery(id+"F2.wireOp",EDGE,"E1259"),sQuery(id+"F2.wireOp",EDGE,"E1260"),sQuery(id+"F2.wireOp",EDGE,"E1261"),sQuery(id+"F2.wireOp",EDGE,"E1262"),sQuery(id+"F2.wireOp",EDGE,"E1263"),sQuery(id+"F2.wireOp",EDGE,"E1264"),sQuery(id+"F2.wireOp",EDGE,"E1265"),sQuery(id+"F2.wireOp",EDGE,"E1266"),sQuery(id+"F2.wireOp",EDGE,"E1267"),sQuery(id+"F2.wireOp",EDGE,"E1268"),sQuery(id+"F2.wireOp",EDGE,"E1269"),sQuery(id+"F2.wireOp",EDGE,"E1270"),sQuery(id+"F2.wireOp",EDGE,"E1271"),sQuery(id+"F2.wireOp",EDGE,"E1272"),sQuery(id+"F2.wireOp",EDGE,"E1273"),sQuery(id+"F2.wireOp",EDGE,"E1274"),sQuery(id+"F2.wireOp",EDGE,"E1275"),sQuery(id+"F2.wireOp",EDGE,"E1276"),sQuery(id+"F2.wireOp",EDGE,"E1277"),sQuery(id+"F2.wireOp",EDGE,"E1278"),sQuery(id+"F2.wireOp",EDGE,"E1279"),sQuery(id+"F2.wireOp",EDGE,"E1280"),sQuery(id+"F2.wireOp",EDGE,"E1281"),sQuery(id+"F2.wireOp",EDGE,"E1282"),sQuery(id+"F2.wireOp",EDGE,"E1283"),sQuery(id+"F2.wireOp",EDGE,"E1284"),sQuery(id+"F2.wireOp",EDGE,"E1285"),sQuery(id+"F2.wireOp",EDGE,"E1286"),sQuery(id+"F2.wireOp",EDGE,"E1287"),sQuery(id+"F2.wireOp",EDGE,"E1288"),sQuery(id+"F2.wireOp",EDGE,"E1289"),sQuery(id+"F2.wireOp",EDGE,"E1290"),sQuery(id+"F2.wireOp",EDGE,"E1291"),sQuery(id+"F2.wireOp",EDGE,"E1292"),sQuery(id+"F2.wireOp",EDGE,"E1293"),sQuery(id+"F2.wireOp",EDGE,"E1294"),sQuery(id+"F2.wireOp",EDGE,"E1295"),sQuery(id+"F2.wireOp",EDGE,"E1296"),sQuery(id+"F2.wireOp",EDGE,"E1297"),sQuery(id+"F2.wireOp",EDGE,"E1298"),sQuery(id+"F2.wireOp",EDGE,"E1299"),sQuery(id+"F2.wireOp",EDGE,"E1300"),sQuery(id+"F2.wireOp",EDGE,"E1301"),sQuery(id+"F2.wireOp",EDGE,"E1302"),sQuery(id+"F2.wireOp",EDGE,"E1303"),sQuery(id+"F2.wireOp",EDGE,"E1304"),sQuery(id+"F2.wireOp",EDGE,"E1305"),sQuery(id+"F2.wireOp",EDGE,"E1306"),sQuery(id+"F2.wireOp",EDGE,"E1460"),sQuery(id+"F2.wireOp",EDGE,"E1461"),sQuery(id+"F2.wireOp",EDGE,"E1462"),sQuery(id+"F2.wireOp",EDGE,"E1463"),sQuery(id+"F2.wireOp",EDGE,"E1464"),sQuery(id+"F2.wireOp",EDGE,"E1465"),sQuery(id+"F2.wireOp",EDGE,"E1466"),sQuery(id+"F2.wireOp",EDGE,"E1467"),sQuery(id+"F2.wireOp",EDGE,"E1468"),sQuery(id+"F2.wireOp",EDGE,"E1469"),sQuery(id+"F2.wireOp",EDGE,"E1470"),sQuery(id+"F2.wireOp",EDGE,"E1471"),sQuery(id+"F2.wireOp",EDGE,"E1472"),sQuery(id+"F2.wireOp",EDGE,"E1473"),sQuery(id+"F2.wireOp",EDGE,"E1474"),sQuery(id+"F2.wireOp",EDGE,"E1475"),sQuery(id+"F2.wireOp",EDGE,"E1476"),sQuery(id+"F2.wireOp",EDGE,"E1477"),sQuery(id+"F2.wireOp",EDGE,"E1478"),sQuery(id+"F2.wireOp",EDGE,"E1479"),sQuery(id+"F2.wireOp",EDGE,"E1480"),sQuery(id+"F2.wireOp",EDGE,"E1481"),sQuery(id+"F2.wireOp",EDGE,"E1482"),sQuery(id+"F2.wireOp",EDGE,"E1483"),sQuery(id+"F2.wireOp",EDGE,"E1484"),sQuery(id+"F2.wireOp",EDGE,"E1485"),sQuery(id+"F2.wireOp",EDGE,"E1486"),sQuery(id+"F2.wireOp",EDGE,"E1487"),sQuery(id+"F2.wireOp",EDGE,"E1488"),sQuery(id+"F2.wireOp",EDGE,"E1489"),sQuery(id+"F2.wireOp",EDGE,"E1490"),sQuery(id+"F2.wireOp",EDGE,"E1491"),sQuery(id+"F2.wireOp",EDGE,"E1492"),sQuery(id+"F2.wireOp",EDGE,"E1493"),sQuery(id+"F2.wireOp",EDGE,"E1494"),sQuery(id+"F2.wireOp",EDGE,"E1495"),sQuery(id+"F2.wireOp",EDGE,"E1496"),sQuery(id+"F2.wireOp",EDGE,"E1497"),sQuery(id+"F2.wireOp",EDGE,"E1498"),sQuery(id+"F2.wireOp",EDGE,"E1499"),sQuery(id+"F2.wireOp",EDGE,"E1500"),sQuery(id+"F2.wireOp",EDGE,"E1501"),sQuery(id+"F2.wireOp",EDGE,"E1502"),sQuery(id+"F2.wireOp",EDGE,"E1503"),sQuery(id+"F2.wireOp",EDGE,"E1504"),sQuery(id+"F2.wireOp",EDGE,"E1505"),sQuery(id+"F2.wireOp",EDGE,"E1506"),sQuery(id+"F2.wireOp",EDGE,"E1507"),sQuery(id+"F2.wireOp",EDGE,"E1508"),sQuery(id+"F2.wireOp",EDGE,"E1509"),sQuery(id+"F2.wireOp",EDGE,"E1510"),sQuery(id+"F2.wireOp",EDGE,"E1511"),sQuery(id+"F2.wireOp",EDGE,"E1512"),sQuery(id+"F2.wireOp",EDGE,"E1513"),sQuery(id+"F2.wireOp",EDGE,"E1514"),sQuery(id+"F2.wireOp",EDGE,"E1515"),sQuery(id+"F2.wireOp",EDGE,"E1516"),sQuery(id+"F2.wireOp",EDGE,"E1517"),sQuery(id+"F2.wireOp",EDGE,"E1518"),sQuery(id+"F2.wireOp",EDGE,"E1519"),sQuery(id+"F2.wireOp",EDGE,"E1520"),sQuery(id+"F2.wireOp",EDGE,"E1521"),sQuery(id+"F2.wireOp",EDGE,"E1522"),sQuery(id+"F2.wireOp",EDGE,"E1523"),sQuery(id+"F2.wireOp",EDGE,"E1524"),sQuery(id+"F2.wireOp",EDGE,"E1525"),sQuery(id+"F2.wireOp",EDGE,"E1526"),sQuery(id+"F2.wireOp",EDGE,"E1527"),sQuery(id+"F2.wireOp",EDGE,"E1528"),sQuery(id+"F2.wireOp",EDGE,"E1529"),sQuery(id+"F2.wireOp",EDGE,"E1530"),sQuery(id+"F2.wireOp",EDGE,"E1531"),sQuery(id+"F2.wireOp",EDGE,"E1532"),sQuery(id+"F2.wireOp",EDGE,"E1533"),sQuery(id+"F2.wireOp",EDGE,"E1534"),sQuery(id+"F2.wireOp",EDGE,"E1535"),sQuery(id+"F2.wireOp",EDGE,"E1536"),sQuery(id+"F2.wireOp",EDGE,"E1537"),sQuery(id+"F2.wireOp",EDGE,"E1538"),sQuery(id+"F2.wireOp",EDGE,"E1539"),sQuery(id+"F2.wireOp",EDGE,"E1540"),sQuery(id+"F2.wireOp",EDGE,"E1541"),sQuery(id+"F2.wireOp",EDGE,"E1542"),sQuery(id+"F2.wireOp",EDGE,"E1543"),sQuery(id+"F2.wireOp",EDGE,"E1544"),sQuery(id+"F2.wireOp",EDGE,"E1545"),sQuery(id+"F2.wireOp",EDGE,"E1546"),sQuery(id+"F2.wireOp",EDGE,"E1547"),sQuery(id+"F2.wireOp",EDGE,"E1548"),sQuery(id+"F2.wireOp",EDGE,"E1549"),sQuery(id+"F2.wireOp",EDGE,"E1550"),sQuery(id+"F2.wireOp",EDGE,"E1551"),sQuery(id+"F2.wireOp",EDGE,"E1552"),sQuery(id+"F2.wireOp",EDGE,"E1553"),sQuery(id+"F2.wireOp",EDGE,"E1554"),sQuery(id+"F2.wireOp",EDGE,"E1555"),sQuery(id+"F2.wireOp",EDGE,"E1556"),sQuery(id+"F2.wireOp",EDGE,"E1557"),sQuery(id+"F2.wireOp",EDGE,"E1558"),sQuery(id+"F2.wireOp",EDGE,"E1559"),sQuery(id+"F2.wireOp",EDGE,"E1560"),sQuery(id+"F2.wireOp",EDGE,"E1561"),sQuery(id+"F2.wireOp",EDGE,"E1562"),sQuery(id+"F2.wireOp",EDGE,"E1563"),sQuery(id+"F2.wireOp",EDGE,"E1564"),sQuery(id+"F2.wireOp",EDGE,"E1565"),sQuery(id+"F2.wireOp",EDGE,"E1566"),sQuery(id+"F2.wireOp",EDGE,"E1567"),sQuery(id+"F2.wireOp",EDGE,"E1568"),sQuery(id+"F2.wireOp",EDGE,"E1569"),sQuery(id+"F2.wireOp",EDGE,"E1570"),sQuery(id+"F2.wireOp",EDGE,"E1571"),sQuery(id+"F2.wireOp",EDGE,"E1572"),sQuery(id+"F2.wireOp",EDGE,"E1573"),sQuery(id+"F2.wireOp",EDGE,"E1574"),sQuery(id+"F2.wireOp",EDGE,"E1575"),sQuery(id+"F2.wireOp",EDGE,"E1576"),sQuery(id+"F2.wireOp",EDGE,"E1577"),sQuery(id+"F2.wireOp",EDGE,"E1578"),sQuery(id+"F2.wireOp",EDGE,"E1579"),sQuery(id+"F2.wireOp",EDGE,"E1580"),sQuery(id+"F2.wireOp",EDGE,"E1581"),sQuery(id+"F2.wireOp",EDGE,"E1582"),sQuery(id+"F2.wireOp",EDGE,"E1583"),sQuery(id+"F2.wireOp",EDGE,"E1584"),sQuery(id+"F2.wireOp",EDGE,"E1585"),sQuery(id+"F2.wireOp",EDGE,"E1586"),sQuery(id+"F2.wireOp",EDGE,"E1587"),sQuery(id+"F2.wireOp",EDGE,"E1588"),sQuery(id+"F2.wireOp",EDGE,"E1589"),sQuery(id+"F2.wireOp",EDGE,"E1590"),sQuery(id+"F2.wireOp",EDGE,"E1591"),sQuery(id+"F2.wireOp",EDGE,"E1592"),sQuery(id+"F2.wireOp",EDGE,"E1593"),sQuery(id+"F2.wireOp",EDGE,"E1594"),sQuery(id+"F2.wireOp",EDGE,"E1595"),sQuery(id+"F2.wireOp",EDGE,"E1596"),sQuery(id+"F2.wireOp",EDGE,"E1597"),sQuery(id+"F2.wireOp",EDGE,"E1598"),sQuery(id+"F2.wireOp",EDGE,"E1599"),sQuery(id+"F2.wireOp",EDGE,"E1600"),sQuery(id+"F2.wireOp",EDGE,"E1601"),sQuery(id+"F2.wireOp",EDGE,"E1602"),sQuery(id+"F2.wireOp",EDGE,"E1603"),sQuery(id+"F2.wireOp",EDGE,"E1604"),sQuery(id+"F2.wireOp",EDGE,"E1605"),sQuery(id+"F2.wireOp",EDGE,"E1606"),sQuery(id+"F2.wireOp",EDGE,"E1607"),sQuery(id+"F2.wireOp",EDGE,"E1608"),sQuery(id+"F2.wireOp",EDGE,"E1609"),sQuery(id+"F2.wireOp",EDGE,"E1610"),sQuery(id+"F2.wireOp",EDGE,"E1611"),sQuery(id+"F2.wireOp",EDGE,"E1612"),sQuery(id+"F2.wireOp",EDGE,"E1613"),sQuery(id+"F2.wireOp",EDGE,"E1614"),sQuery(id+"F2.wireOp",EDGE,"E1615"),sQuery(id+"F2.wireOp",EDGE,"E1616"),sQuery(id+"F2.wireOp",EDGE,"E1617"),sQuery(id+"F2.wireOp",EDGE,"E1618"),sQuery(id+"F2.wireOp",EDGE,"E1619"),sQuery(id+"F2.wireOp",EDGE,"E1620"),sQuery(id+"F2.wireOp",EDGE,"E1621"),sQuery(id+"F2.wireOp",EDGE,"E1622"),sQuery(id+"F2.wireOp",EDGE,"E1623"),sQuery(id+"F2.wireOp",EDGE,"E1624"),sQuery(id+"F2.wireOp",EDGE,"E1625"),sQuery(id+"F2.wireOp",EDGE,"E1626"),sQuery(id+"F2.wireOp",EDGE,"E1627"),sQuery(id+"F2.wireOp",EDGE,"E1628"),sQuery(id+"F2.wireOp",EDGE,"E1629"),sQuery(id+"F2.wireOp",EDGE,"E1630"),sQuery(id+"F2.wireOp",EDGE,"E1631"),sQuery(id+"F2.wireOp",EDGE,"E1632"),sQuery(id+"F2.wireOp",EDGE,"E1633"),sQuery(id+"F2.wireOp",EDGE,"E1634"),sQuery(id+"F2.wireOp",EDGE,"E1635"),sQuery(id+"F2.wireOp",EDGE,"E1636"),sQuery(id+"F2.wireOp",EDGE,"E1637"),sQuery(id+"F2.wireOp",EDGE,"E1638"),sQuery(id+"F2.wireOp",EDGE,"E1639"),sQuery(id+"F2.wireOp",EDGE,"E1640"),sQuery(id+"F2.wireOp",EDGE,"E1641"),sQuery(id+"F2.wireOp",EDGE,"E1642"),sQuery(id+"F2.wireOp",EDGE,"E1643"),sQuery(id+"F2.wireOp",EDGE,"E1644"),sQuery(id+"F2.wireOp",EDGE,"E1645"),sQuery(id+"F2.wireOp",EDGE,"E1646"),sQuery(id+"F2.wireOp",EDGE,"E1647"),sQuery(id+"F2.wireOp",EDGE,"E1648"),sQuery(id+"F2.wireOp",EDGE,"E1649"),sQuery(id+"F2.wireOp",EDGE,"E1650"),sQuery(id+"F2.wireOp",EDGE,"E1651"),sQuery(id+"F2.wireOp",EDGE,"E1652"),sQuery(id+"F2.wireOp",EDGE,"E1653"),sQuery(id+"F2.wireOp",EDGE,"E1654"),sQuery(id+"F2.wireOp",EDGE,"E1655"),sQuery(id+"F2.wireOp",EDGE,"E1656"),sQuery(id+"F2.wireOp",EDGE,"E1657"),sQuery(id+"F2.wireOp",EDGE,"E1658"),sQuery(id+"F2.wireOp",EDGE,"E1659"),sQuery(id+"F2.wireOp",EDGE,"E1660"),sQuery(id+"F2.wireOp",EDGE,"E1661"),sQuery(id+"F2.wireOp",EDGE,"E1662"),sQuery(id+"F2.wireOp",EDGE,"E1663"),sQuery(id+"F2.wireOp",EDGE,"E1664"),sQuery(id+"F2.wireOp",EDGE,"E1665"),sQuery(id+"F2.wireOp",EDGE,"E1666"),sQuery(id+"F2.wireOp",EDGE,"E1667"),sQuery(id+"F2.wireOp",EDGE,"E1668"),sQuery(id+"F2.wireOp",EDGE,"E1669"),sQuery(id+"F2.wireOp",EDGE,"E1670"),sQuery(id+"F2.wireOp",EDGE,"E1671"),sQuery(id+"F2.wireOp",EDGE,"E1672"),sQuery(id+"F2.wireOp",EDGE,"E1673"),sQuery(id+"F2.wireOp",EDGE,"E1674"),sQuery(id+"F2.wireOp",EDGE,"E1675"),sQuery(id+"F2.wireOp",EDGE,"E1676"),sQuery(id+"F2.wireOp",EDGE,"E1677"),sQuery(id+"F2.wireOp",EDGE,"E1678"),sQuery(id+"F2.wireOp",EDGE,"E1679"),sQuery(id+"F2.wireOp",EDGE,"E1680"),sQuery(id+"F2.wireOp",EDGE,"E1681"),sQuery(id+"F2.wireOp",EDGE,"E1682"),sQuery(id+"F2.wireOp",EDGE,"E1683"),sQuery(id+"F2.wireOp",EDGE,"E1684"),sQuery(id+"F2.wireOp",EDGE,"E1685"),sQuery(id+"F2.wireOp",EDGE,"E1686"),sQuery(id+"F2.wireOp",EDGE,"E1687"),sQuery(id+"F2.wireOp",EDGE,"E1688"),sQuery(id+"F2.wireOp",EDGE,"E1689"),sQuery(id+"F2.wireOp",EDGE,"E1690"),sQuery(id+"F2.wireOp",EDGE,"E1691"),sQuery(id+"F2.wireOp",EDGE,"E1692"),sQuery(id+"F2.wireOp",EDGE,"E1693"),sQuery(id+"F2.wireOp",EDGE,"E1694"),sQuery(id+"F2.wireOp",EDGE,"E1695"),sQuery(id+"F2.wireOp",EDGE,"E1696"),sQuery(id+"F2.wireOp",EDGE,"E1697"),sQuery(id+"F2.wireOp",EDGE,"E1698"),sQuery(id+"F2.wireOp",EDGE,"E1699"),sQuery(id+"F2.wireOp",EDGE,"E1700"),sQuery(id+"F2.wireOp",EDGE,"E1701"),sQuery(id+"F2.wireOp",EDGE,"E1702"),sQuery(id+"F2.wireOp",EDGE,"E1703"),sQuery(id+"F2.wireOp",EDGE,"E1704"),sQuery(id+"F2.wireOp",EDGE,"E1705"),sQuery(id+"F2.wireOp",EDGE,"E1706"),sQuery(id+"F2.wireOp",EDGE,"E1707"),sQuery(id+"F2.wireOp",EDGE,"E1708"),sQuery(id+"F2.wireOp",EDGE,"E1709"),sQuery(id+"F2.wireOp",EDGE,"E1710"),sQuery(id+"F2.wireOp",EDGE,"E1711"),sQuery(id+"F2.wireOp",EDGE,"E1712"),sQuery(id+"F2.wireOp",EDGE,"E1713"),sQuery(id+"F2.wireOp",EDGE,"E1714"),sQuery(id+"F2.wireOp",EDGE,"E1715"),sQuery(id+"F2.wireOp",EDGE,"E1716"),sQuery(id+"F2.wireOp",EDGE,"E1717"),sQuery(id+"F2.wireOp",EDGE,"E1718"),sQuery(id+"F2.wireOp",EDGE,"E1719"),sQuery(id+"F2.wireOp",EDGE,"E1720"),sQuery(id+"F2.wireOp",EDGE,"E1721"),sQuery(id+"F2.wireOp",EDGE,"E1722"),sQuery(id+"F2.wireOp",EDGE,"E1723"),sQuery(id+"F2.wireOp",EDGE,"E1724"),sQuery(id+"F2.wireOp",EDGE,"E1725"),sQuery(id+"F2.wireOp",EDGE,"E1726"),sQuery(id+"F2.wireOp",EDGE,"E1727"),sQuery(id+"F2.wireOp",EDGE,"E1728"),sQuery(id+"F2.wireOp",EDGE,"E1729"),sQuery(id+"F2.wireOp",EDGE,"E1730"),sQuery(id+"F2.wireOp",EDGE,"E1731"),sQuery(id+"F2.wireOp",EDGE,"E1732"),sQuery(id+"F2.wireOp",EDGE,"E1733"),sQuery(id+"F2.wireOp",EDGE,"E1734"),sQuery(id+"F2.wireOp",EDGE,"E1735"),sQuery(id+"F2.wireOp",EDGE,"E1736"),sQuery(id+"F2.wireOp",EDGE,"E1737"),sQuery(id+"F2.wireOp",EDGE,"E1738"),sQuery(id+"F2.wireOp",EDGE,"E1739"),sQuery(id+"F2.wireOp",EDGE,"E1740"),sQuery(id+"F2.wireOp",EDGE,"E1741"),subQ1])],"isStart":false}),makeQuery(id+"F9.opExtrude","CAP_FACE",FACE,{"disambiguationData":[OSD([sQuery(id+"F8.wireOp",EDGE,"E2031.0"),sQuery(id+"F8.wireOp",EDGE,"E2032.0"),sQuery(id+"F8.wireOp",EDGE,"E2033.0"),sQuery(id+"F8.wireOp",EDGE,"E2034.0"),sQuery(id+"F8.wireOp",EDGE,"E2035.0"),sQuery(id+"F8.wireOp",EDGE,"E2036")])],"isStart":false})]}),makeQuery(id+"F10.opSweep","SWEPT_FACE",FACE,{"disambiguationData":[OSD([sQuery(id+"F0.wireOp",EDGE,"E254"),subQ1])]})]}),makeQuery(id+"F12.opSweep","SWEPT_FACE",FACE,{"disambiguationData":[OSD([subQ0,sQuery(id+"F11.wireOp",EDGE,"E2037.0")])]})]});}
            extrude(context, id + "F14", {"entities" : qUnion([Q0]), "operationType" : NewBodyOperationType.REMOVE, "endBound" : BoundingType.UP_TO_SURFACE, "depth" : 25 * mm, "endBoundEntityFace" : qUnion([Q1]), "offsetDistance" : 25 * mm});
        }
        {
            var Q0;
            {var subQ0=sQuery(id+"F0.wireOp",EDGE,"E341");var subQ1=sQuery(id+"F0.wireOp",EDGE,"E340");var subQ4=sQuery(id+"F0.wireOp",EDGE,"E1143");var subQ5=sQuery(id+"F0.wireOp",EDGE,"E1140");var subQ6=sQuery(id+"F0.wireOp",EDGE,"E577");var subQ7=sQuery(id+"F0.wireOp",EDGE,"E576");var subQ8=sQuery(id+"F0.wireOp",EDGE,"E575");var subQ9=sQuery(id+"F0.wireOp",EDGE,"E574");var subQ10=sQuery(id+"F0.wireOp",EDGE,"E573");var subQ11=sQuery(id+"F0.wireOp",EDGE,"E572");var subQ12=sQuery(id+"F0.wireOp",EDGE,"E571");var subQ13=sQuery(id+"F0.wireOp",EDGE,"E570");var subQ14=sQuery(id+"F0.wireOp",EDGE,"E569");var subQ15=sQuery(id+"F0.wireOp",EDGE,"E568");var subQ16=sQuery(id+"F0.wireOp",EDGE,"E567");var subQ17=sQuery(id+"F0.wireOp",EDGE,"E566");var subQ18=sQuery(id+"F0.wireOp",EDGE,"E565");var subQ19=sQuery(id+"F0.wireOp",EDGE,"E564");var subQ20=sQuery(id+"F0.wireOp",EDGE,"E563");var subQ21=sQuery(id+"F0.wireOp",EDGE,"E562");var subQ22=sQuery(id+"F0.wireOp",EDGE,"E561");var subQ23=sQuery(id+"F0.wireOp",EDGE,"E560");var subQ24=sQuery(id+"F0.wireOp",EDGE,"E559");var subQ25=sQuery(id+"F0.wireOp",EDGE,"E558");var subQ26=sQuery(id+"F0.wireOp",EDGE,"E557");var subQ27=sQuery(id+"F0.wireOp",EDGE,"E556");var subQ28=sQuery(id+"F0.wireOp",EDGE,"E555");var subQ29=sQuery(id+"F0.wireOp",EDGE,"E554");var subQ30=sQuery(id+"F0.wireOp",EDGE,"E553");var subQ31=sQuery(id+"F0.wireOp",EDGE,"E552");var subQ32=sQuery(id+"F0.wireOp",EDGE,"E551");var subQ33=sQuery(id+"F0.wireOp",EDGE,"E550");var subQ34=sQuery(id+"F0.wireOp",EDGE,"E549");var subQ35=sQuery(id+"F0.wireOp",EDGE,"E548");var subQ36=sQuery(id+"F0.wireOp",EDGE,"E547");var subQ37=sQuery(id+"F0.wireOp",EDGE,"E546");var subQ38=sQuery(id+"F0.wireOp",EDGE,"E545");var subQ39=sQuery(id+"F0.wireOp",EDGE,"E544");var subQ40=sQuery(id+"F0.wireOp",EDGE,"E543");var subQ41=sQuery(id+"F0.wireOp",EDGE,"E542");var subQ42=sQuery(id+"F0.wireOp",EDGE,"E541");var subQ43=sQuery(id+"F0.wireOp",EDGE,"E540");var subQ44=sQuery(id+"F0.wireOp",EDGE,"E539");var subQ45=sQuery(id+"F0.wireOp",EDGE,"E538");var subQ46=sQuery(id+"F0.wireOp",EDGE,"E537");var subQ47=sQuery(id+"F0.wireOp",EDGE,"E536");var subQ48=sQuery(id+"F0.wireOp",EDGE,"E535");var subQ49=sQuery(id+"F0.wireOp",EDGE,"E534");var subQ50=sQuery(id+"F0.wireOp",EDGE,"E533");var subQ51=sQuery(id+"F0.wireOp",EDGE,"E532");var subQ52=sQuery(id+"F0.wireOp",EDGE,"E531");var subQ53=sQuery(id+"F0.wireOp",EDGE,"E530");var subQ54=sQuery(id+"F0.wireOp",EDGE,"E529");var subQ55=sQuery(id+"F0.wireOp",EDGE,"E528");var subQ56=sQuery(id+"F0.wireOp",EDGE,"E527");var subQ57=sQuery(id+"F0.wireOp",EDGE,"E526");var subQ58=sQuery(id+"F0.wireOp",EDGE,"E525");var subQ59=sQuery(id+"F0.wireOp",EDGE,"E524");var subQ60=sQuery(id+"F0.wireOp",EDGE,"E523");var subQ61=sQuery(id+"F0.wireOp",EDGE,"E522");var subQ62=sQuery(id+"F0.wireOp",EDGE,"E521");var subQ63=sQuery(id+"F0.wireOp",EDGE,"E520");var subQ64=sQuery(id+"F0.wireOp",EDGE,"E519");var subQ65=sQuery(id+"F0.wireOp",EDGE,"E518");var subQ66=sQuery(id+"F0.wireOp",EDGE,"E517");var subQ67=sQuery(id+"F0.wireOp",EDGE,"E516");var subQ68=sQuery(id+"F0.wireOp",EDGE,"E515");var subQ69=sQuery(id+"F0.wireOp",EDGE,"E514");var subQ70=sQuery(id+"F0.wireOp",EDGE,"E513");var subQ71=sQuery(id+"F0.wireOp",EDGE,"E512");var subQ72=sQuery(id+"F0.wireOp",EDGE,"E511");var subQ73=sQuery(id+"F0.wireOp",EDGE,"E510");var subQ74=sQuery(id+"F0.wireOp",EDGE,"E509");var subQ75=sQuery(id+"F0.wireOp",EDGE,"E508");var subQ76=sQuery(id+"F0.wireOp",EDGE,"E507");var subQ77=sQuery(id+"F0.wireOp",EDGE,"E506");var subQ78=sQuery(id+"F0.wireOp",EDGE,"E505");var subQ79=sQuery(id+"F0.wireOp",EDGE,"E504");var subQ80=sQuery(id+"F0.wireOp",EDGE,"E503");var subQ81=sQuery(id+"F0.wireOp",EDGE,"E502");var subQ82=sQuery(id+"F0.wireOp",EDGE,"E501");var subQ83=sQuery(id+"F0.wireOp",EDGE,"E500");var subQ84=sQuery(id+"F0.wireOp",EDGE,"E499");var subQ85=sQuery(id+"F0.wireOp",EDGE,"E498");var subQ86=sQuery(id+"F0.wireOp",EDGE,"E497");var subQ87=sQuery(id+"F0.wireOp",EDGE,"E496");var subQ88=sQuery(id+"F0.wireOp",EDGE,"E495");var subQ89=sQuery(id+"F0.wireOp",EDGE,"E494");var subQ90=sQuery(id+"F0.wireOp",EDGE,"E493");var subQ91=sQuery(id+"F0.wireOp",EDGE,"E492");var subQ92=sQuery(id+"F0.wireOp",EDGE,"E491");var subQ93=sQuery(id+"F0.wireOp",EDGE,"E490");var subQ94=sQuery(id+"F0.wireOp",EDGE,"E489");var subQ95=sQuery(id+"F0.wireOp",EDGE,"E488");var subQ96=sQuery(id+"F0.wireOp",EDGE,"E487");var subQ97=sQuery(id+"F0.wireOp",EDGE,"E486");var subQ98=sQuery(id+"F0.wireOp",EDGE,"E485");var subQ99=sQuery(id+"F0.wireOp",EDGE,"E484");var subQ100=sQuery(id+"F0.wireOp",EDGE,"E483");var subQ101=sQuery(id+"F0.wireOp",EDGE,"E482");var subQ102=sQuery(id+"F0.wireOp",EDGE,"E481");var subQ103=sQuery(id+"F0.wireOp",EDGE,"E480");var subQ104=sQuery(id+"F0.wireOp",EDGE,"E479");var subQ105=sQuery(id+"F0.wireOp",EDGE,"E478");var subQ106=sQuery(id+"F0.wireOp",EDGE,"E477");var subQ107=sQuery(id+"F0.wireOp",EDGE,"E476");var subQ108=sQuery(id+"F0.wireOp",EDGE,"E475");var subQ109=sQuery(id+"F0.wireOp",EDGE,"E474");var subQ110=sQuery(id+"F0.wireOp",EDGE,"E473");var subQ111=sQuery(id+"F0.wireOp",EDGE,"E472");var subQ112=sQuery(id+"F0.wireOp",EDGE,"E471");var subQ113=sQuery(id+"F0.wireOp",EDGE,"E470");var subQ114=sQuery(id+"F0.wireOp",EDGE,"E469");var subQ115=sQuery(id+"F0.wireOp",EDGE,"E468");var subQ116=sQuery(id+"F0.wireOp",EDGE,"E467");var subQ117=sQuery(id+"F0.wireOp",EDGE,"E466");var subQ118=sQuery(id+"F0.wireOp",EDGE,"E465");var subQ119=sQuery(id+"F0.wireOp",EDGE,"E464");var subQ120=sQuery(id+"F0.wireOp",EDGE,"E463");var subQ121=sQuery(id+"F0.wireOp",EDGE,"E462");var subQ122=sQuery(id+"F0.wireOp",EDGE,"E461");var subQ123=sQuery(id+"F0.wireOp",EDGE,"E460");var subQ124=sQuery(id+"F0.wireOp",EDGE,"E459");var subQ125=sQuery(id+"F0.wireOp",EDGE,"E458");var subQ126=sQuery(id+"F0.wireOp",EDGE,"E457");var subQ127=sQuery(id+"F0.wireOp",EDGE,"E456");var subQ128=sQuery(id+"F0.wireOp",EDGE,"E455");var subQ129=sQuery(id+"F0.wireOp",EDGE,"E454");var subQ130=sQuery(id+"F0.wireOp",EDGE,"E453");var subQ131=sQuery(id+"F0.wireOp",EDGE,"E452");var subQ132=sQuery(id+"F0.wireOp",EDGE,"E451");var subQ133=sQuery(id+"F0.wireOp",EDGE,"E450");var subQ134=sQuery(id+"F0.wireOp",EDGE,"E449");var subQ135=sQuery(id+"F0.wireOp",EDGE,"E448");var subQ136=sQuery(id+"F0.wireOp",EDGE,"E447");var subQ137=sQuery(id+"F0.wireOp",EDGE,"E446");var subQ138=sQuery(id+"F0.wireOp",EDGE,"E445");var subQ139=sQuery(id+"F0.wireOp",EDGE,"E444");var subQ140=sQuery(id+"F0.wireOp",EDGE,"E443");var subQ141=sQuery(id+"F0.wireOp",EDGE,"E442");var subQ142=sQuery(id+"F0.wireOp",EDGE,"E441");var subQ143=sQuery(id+"F0.wireOp",EDGE,"E440");var subQ144=sQuery(id+"F0.wireOp",EDGE,"E439");var subQ145=sQuery(id+"F0.wireOp",EDGE,"E438");var subQ146=sQuery(id+"F0.wireOp",EDGE,"E437");var subQ147=sQuery(id+"F0.wireOp",EDGE,"E436");var subQ148=sQuery(id+"F0.wireOp",EDGE,"E435");var subQ149=sQuery(id+"F0.wireOp",EDGE,"E434");var subQ150=sQuery(id+"F0.wireOp",EDGE,"E433");var subQ151=sQuery(id+"F0.wireOp",EDGE,"E432");var subQ152=sQuery(id+"F0.wireOp",EDGE,"E431");var subQ153=sQuery(id+"F0.wireOp",EDGE,"E430");var subQ154=sQuery(id+"F0.wireOp",EDGE,"E429");var subQ155=sQuery(id+"F0.wireOp",EDGE,"E428");var subQ156=sQuery(id+"F0.wireOp",EDGE,"E427");var subQ157=sQuery(id+"F0.wireOp",EDGE,"E426");var subQ158=sQuery(id+"F0.wireOp",EDGE,"E425");var subQ159=sQuery(id+"F0.wireOp",EDGE,"E424");var subQ160=sQuery(id+"F0.wireOp",EDGE,"E423");var subQ161=sQuery(id+"F0.wireOp",EDGE,"E422");var subQ162=sQuery(id+"F0.wireOp",EDGE,"E421");var subQ163=sQuery(id+"F0.wireOp",EDGE,"E420");var subQ164=sQuery(id+"F0.wireOp",EDGE,"E419");var subQ165=sQuery(id+"F0.wireOp",EDGE,"E418");var subQ166=sQuery(id+"F0.wireOp",EDGE,"E417");var subQ167=sQuery(id+"F0.wireOp",EDGE,"E416");var subQ168=sQuery(id+"F0.wireOp",EDGE,"E415");var subQ169=sQuery(id+"F0.wireOp",EDGE,"E414");var subQ170=sQuery(id+"F0.wireOp",EDGE,"E413");var subQ171=sQuery(id+"F0.wireOp",EDGE,"E412");var subQ172=sQuery(id+"F0.wireOp",EDGE,"E411");var subQ173=sQuery(id+"F0.wireOp",EDGE,"E410");var subQ174=sQuery(id+"F0.wireOp",EDGE,"E409");var subQ175=sQuery(id+"F0.wireOp",EDGE,"E408");var subQ176=sQuery(id+"F0.wireOp",EDGE,"E407");var subQ177=sQuery(id+"F0.wireOp",EDGE,"E406");var subQ178=sQuery(id+"F0.wireOp",EDGE,"E405");var subQ179=sQuery(id+"F0.wireOp",EDGE,"E404");var subQ180=sQuery(id+"F0.wireOp",EDGE,"E403");var subQ181=sQuery(id+"F0.wireOp",EDGE,"E402");var subQ182=sQuery(id+"F0.wireOp",EDGE,"E401");var subQ183=sQuery(id+"F0.wireOp",EDGE,"E400");var subQ184=sQuery(id+"F0.wireOp",EDGE,"E399");var subQ185=sQuery(id+"F0.wireOp",EDGE,"E398");var subQ186=sQuery(id+"F0.wireOp",EDGE,"E397");var subQ187=sQuery(id+"F0.wireOp",EDGE,"E396");var subQ188=sQuery(id+"F0.wireOp",EDGE,"E395");var subQ189=sQuery(id+"F0.wireOp",EDGE,"E394");var subQ190=sQuery(id+"F0.wireOp",EDGE,"E393");var subQ191=sQuery(id+"F0.wireOp",EDGE,"E392");var subQ192=sQuery(id+"F0.wireOp",EDGE,"E391");var subQ193=sQuery(id+"F0.wireOp",EDGE,"E390");var subQ194=sQuery(id+"F0.wireOp",EDGE,"E389");var subQ195=sQuery(id+"F0.wireOp",EDGE,"E388");var subQ196=sQuery(id+"F0.wireOp",EDGE,"E387");var subQ197=sQuery(id+"F0.wireOp",EDGE,"E386");var subQ198=sQuery(id+"F0.wireOp",EDGE,"E385");var subQ199=sQuery(id+"F0.wireOp",EDGE,"E384");var subQ200=sQuery(id+"F0.wireOp",EDGE,"E383");var subQ201=sQuery(id+"F0.wireOp",EDGE,"E382");var subQ202=sQuery(id+"F0.wireOp",EDGE,"E381");var subQ203=sQuery(id+"F0.wireOp",EDGE,"E380");var subQ204=sQuery(id+"F0.wireOp",EDGE,"E379");var subQ205=sQuery(id+"F0.wireOp",EDGE,"E378");var subQ206=sQuery(id+"F0.wireOp",EDGE,"E377");var subQ207=sQuery(id+"F0.wireOp",EDGE,"E376");var subQ208=sQuery(id+"F0.wireOp",EDGE,"E375");var subQ209=sQuery(id+"F0.wireOp",EDGE,"E374");var subQ210=sQuery(id+"F0.wireOp",EDGE,"E373");var subQ211=sQuery(id+"F0.wireOp",EDGE,"E372");var subQ212=sQuery(id+"F0.wireOp",EDGE,"E371");var subQ213=sQuery(id+"F0.wireOp",EDGE,"E370");var subQ214=sQuery(id+"F0.wireOp",EDGE,"E369");var subQ215=sQuery(id+"F0.wireOp",EDGE,"E368");var subQ216=sQuery(id+"F0.wireOp",EDGE,"E367");var subQ217=sQuery(id+"F0.wireOp",EDGE,"E366");var subQ218=sQuery(id+"F0.wireOp",EDGE,"E365");var subQ219=sQuery(id+"F0.wireOp",EDGE,"E364");var subQ220=sQuery(id+"F0.wireOp",EDGE,"E363");var subQ221=sQuery(id+"F0.wireOp",EDGE,"E362");var subQ222=sQuery(id+"F0.wireOp",EDGE,"E361");var subQ223=sQuery(id+"F0.wireOp",EDGE,"E360");var subQ224=sQuery(id+"F0.wireOp",EDGE,"E359");var subQ225=sQuery(id+"F0.wireOp",EDGE,"E358");var subQ226=sQuery(id+"F0.wireOp",EDGE,"E357");var subQ227=sQuery(id+"F0.wireOp",EDGE,"E356");var subQ228=sQuery(id+"F0.wireOp",EDGE,"E355");var subQ229=sQuery(id+"F0.wireOp",EDGE,"E354");var subQ230=sQuery(id+"F0.wireOp",EDGE,"E353");var subQ231=sQuery(id+"F0.wireOp",EDGE,"E352");var subQ232=sQuery(id+"F0.wireOp",EDGE,"E351");var subQ233=sQuery(id+"F0.wireOp",EDGE,"E350");var subQ234=sQuery(id+"F0.wireOp",EDGE,"E349");var subQ235=sQuery(id+"F0.wireOp",EDGE,"E348");var subQ236=sQuery(id+"F0.wireOp",EDGE,"E347");var subQ237=sQuery(id+"F0.wireOp",EDGE,"E346");var subQ238=sQuery(id+"F0.wireOp",EDGE,"E345");var subQ239=sQuery(id+"F0.wireOp",EDGE,"E344");var subQ240=sQuery(id+"F0.wireOp",EDGE,"E343");var subQ241=sQuery(id+"F0.wireOp",EDGE,"E342");var subQ242=sQuery(id+"F0.wireOp",EDGE,"E339");var subQ243=sQuery(id+"F0.wireOp",EDGE,"E338");var subQ244=sQuery(id+"F0.wireOp",EDGE,"E337");var subQ245=sQuery(id+"F0.wireOp",EDGE,"E336");var subQ246=sQuery(id+"F0.wireOp",EDGE,"E335");var subQ247=sQuery(id+"F0.wireOp",EDGE,"E334");var subQ248=sQuery(id+"F0.wireOp",EDGE,"E333");var subQ249=sQuery(id+"F0.wireOp",EDGE,"E332");var subQ250=sQuery(id+"F0.wireOp",EDGE,"E331");var subQ251=sQuery(id+"F0.wireOp",EDGE,"E330");var subQ252=sQuery(id+"F0.wireOp",EDGE,"E329");var subQ253=sQuery(id+"F0.wireOp",EDGE,"E328");var subQ254=sQuery(id+"F0.wireOp",EDGE,"E327");var subQ255=sQuery(id+"F0.wireOp",EDGE,"E326");var subQ256=sQuery(id+"F0.wireOp",EDGE,"E325");var subQ257=sQuery(id+"F0.wireOp",EDGE,"E324");var subQ258=sQuery(id+"F0.wireOp",EDGE,"E323");var subQ259=sQuery(id+"F0.wireOp",EDGE,"E322");var subQ260=sQuery(id+"F0.wireOp",EDGE,"E321");var subQ261=sQuery(id+"F0.wireOp",EDGE,"E320");var subQ262=sQuery(id+"F0.wireOp",EDGE,"E319");var subQ263=sQuery(id+"F0.wireOp",EDGE,"E318");var subQ264=sQuery(id+"F0.wireOp",EDGE,"E317");var subQ265=sQuery(id+"F0.wireOp",EDGE,"E316");var subQ266=sQuery(id+"F0.wireOp",EDGE,"E315");var subQ267=sQuery(id+"F0.wireOp",EDGE,"E314");var subQ268=sQuery(id+"F0.wireOp",EDGE,"E313");var subQ269=sQuery(id+"F0.wireOp",EDGE,"E312");var subQ270=sQuery(id+"F0.wireOp",EDGE,"E311");var subQ271=sQuery(id+"F0.wireOp",EDGE,"E310");var subQ272=sQuery(id+"F0.wireOp",EDGE,"E309");var subQ273=sQuery(id+"F0.wireOp",EDGE,"E308");var subQ274=sQuery(id+"F0.wireOp",EDGE,"E307");var subQ275=sQuery(id+"F0.wireOp",EDGE,"E306");var subQ276=sQuery(id+"F0.wireOp",EDGE,"E305");var subQ277=sQuery(id+"F0.wireOp",EDGE,"E304");var subQ278=sQuery(id+"F0.wireOp",EDGE,"E303");var subQ279=sQuery(id+"F0.wireOp",EDGE,"E302");var subQ280=sQuery(id+"F0.wireOp",EDGE,"E301");var subQ281=sQuery(id+"F0.wireOp",EDGE,"E300");var subQ282=sQuery(id+"F0.wireOp",EDGE,"E299");var subQ283=sQuery(id+"F0.wireOp",EDGE,"E298");var subQ284=sQuery(id+"F0.wireOp",EDGE,"E297");var subQ285=sQuery(id+"F0.wireOp",EDGE,"E296");var subQ286=sQuery(id+"F0.wireOp",EDGE,"E295");var subQ287=sQuery(id+"F0.wireOp",EDGE,"E294");var subQ288=sQuery(id+"F0.wireOp",EDGE,"E293");var subQ289=sQuery(id+"F0.wireOp",EDGE,"E292");var subQ290=sQuery(id+"F0.wireOp",EDGE,"E291");var subQ291=sQuery(id+"F0.wireOp",EDGE,"E290");var subQ292=sQuery(id+"F0.wireOp",EDGE,"E289");var subQ293=sQuery(id+"F0.wireOp",EDGE,"E288");var subQ294=sQuery(id+"F0.wireOp",EDGE,"E287");var subQ295=sQuery(id+"F0.wireOp",EDGE,"E286");var subQ296=sQuery(id+"F0.wireOp",EDGE,"E285");var subQ297=sQuery(id+"F0.wireOp",EDGE,"E284");var subQ298=sQuery(id+"F0.wireOp",EDGE,"E283");var subQ299=sQuery(id+"F0.wireOp",EDGE,"E282");var subQ300=sQuery(id+"F0.wireOp",EDGE,"E281");var subQ301=sQuery(id+"F0.wireOp",EDGE,"E280");var subQ302=sQuery(id+"F0.wireOp",EDGE,"E279");var subQ303=sQuery(id+"F0.wireOp",EDGE,"E278");var subQ304=sQuery(id+"F0.wireOp",EDGE,"E277");var subQ305=sQuery(id+"F0.wireOp",EDGE,"E276");var subQ306=sQuery(id+"F0.wireOp",EDGE,"E275");var subQ307=sQuery(id+"F0.wireOp",EDGE,"E274");var subQ308=sQuery(id+"F0.wireOp",EDGE,"E273");var subQ309=sQuery(id+"F0.wireOp",EDGE,"E272");var subQ310=sQuery(id+"F0.wireOp",EDGE,"E271");var subQ311=sQuery(id+"F0.wireOp",EDGE,"E270");var subQ312=sQuery(id+"F0.wireOp",EDGE,"E269");var subQ313=sQuery(id+"F0.wireOp",EDGE,"E268");var subQ314=sQuery(id+"F0.wireOp",EDGE,"E267");var subQ315=sQuery(id+"F0.wireOp",EDGE,"E266");var subQ316=sQuery(id+"F0.wireOp",EDGE,"E265");var subQ317=sQuery(id+"F0.wireOp",EDGE,"E264");var subQ318=sQuery(id+"F0.wireOp",EDGE,"E263");var subQ319=sQuery(id+"F0.wireOp",EDGE,"E262");var subQ320=sQuery(id+"F0.wireOp",EDGE,"E261");var subQ321=sQuery(id+"F0.wireOp",EDGE,"E260");var subQ322=sQuery(id+"F0.wireOp",EDGE,"E259");var subQ323=sQuery(id+"F0.wireOp",EDGE,"E258");var subQ324=sQuery(id+"F0.wireOp",EDGE,"E257");var subQ325=sQuery(id+"F0.wireOp",EDGE,"E256");var subQ326=sQuery(id+"F0.wireOp",EDGE,"E255");var subQ327=sQuery(id+"F0.wireOp",EDGE,"E254");var subQ328=sQuery(id+"F0.wireOp",EDGE,"E253");var subQ329=sQuery(id+"F0.wireOp",EDGE,"E252");var subQ330=sQuery(id+"F0.wireOp",EDGE,"E251");var subQ331=sQuery(id+"F0.wireOp",EDGE,"E250");var subQ332=sQuery(id+"F0.wireOp",EDGE,"E249");var subQ333=sQuery(id+"F0.wireOp",EDGE,"E248");var subQ334=sQuery(id+"F0.wireOp",EDGE,"E247");var subQ335=sQuery(id+"F0.wireOp",EDGE,"E246");var subQ336=sQuery(id+"F0.wireOp",EDGE,"E245");var subQ337=sQuery(id+"F0.wireOp",EDGE,"E244");var subQ338=sQuery(id+"F0.wireOp",EDGE,"E243");var subQ339=sQuery(id+"F0.wireOp",EDGE,"E242");var subQ340=sQuery(id+"F0.wireOp",EDGE,"E241");var subQ341=sQuery(id+"F0.wireOp",EDGE,"E240");var subQ342=sQuery(id+"F0.wireOp",EDGE,"E239");var subQ343=sQuery(id+"F0.wireOp",EDGE,"E238");var subQ344=sQuery(id+"F0.wireOp",EDGE,"E237");var subQ345=sQuery(id+"F0.wireOp",EDGE,"E236");var subQ346=sQuery(id+"F0.wireOp",EDGE,"E235");var subQ347=sQuery(id+"F0.wireOp",EDGE,"E234");var subQ348=sQuery(id+"F0.wireOp",EDGE,"E233");var subQ349=sQuery(id+"F0.wireOp",EDGE,"E232");var subQ350=sQuery(id+"F0.wireOp",EDGE,"E231");var subQ351=sQuery(id+"F0.wireOp",EDGE,"E230");var subQ352=sQuery(id+"F0.wireOp",EDGE,"E229");var subQ353=sQuery(id+"F0.wireOp",EDGE,"E228");var subQ354=sQuery(id+"F0.wireOp",EDGE,"E227");var subQ355=sQuery(id+"F0.wireOp",EDGE,"E226");var subQ356=sQuery(id+"F0.wireOp",EDGE,"E225");var subQ357=sQuery(id+"F0.wireOp",EDGE,"E224");var subQ358=sQuery(id+"F0.wireOp",EDGE,"E223");var subQ359=sQuery(id+"F0.wireOp",EDGE,"E222");var subQ360=sQuery(id+"F0.wireOp",EDGE,"E221");var subQ361=sQuery(id+"F0.wireOp",EDGE,"E220");var subQ362=sQuery(id+"F0.wireOp",EDGE,"E219");var subQ363=sQuery(id+"F0.wireOp",EDGE,"E218");var subQ364=sQuery(id+"F0.wireOp",EDGE,"E217");var subQ365=sQuery(id+"F0.wireOp",EDGE,"E216");var subQ366=sQuery(id+"F0.wireOp",EDGE,"E215");var subQ367=sQuery(id+"F0.wireOp",EDGE,"E214");var subQ368=sQuery(id+"F0.wireOp",EDGE,"E213");var subQ369=sQuery(id+"F0.wireOp",EDGE,"E212");var subQ370=sQuery(id+"F0.wireOp",EDGE,"E211");var subQ371=sQuery(id+"F0.wireOp",EDGE,"E210");var subQ372=sQuery(id+"F0.wireOp",EDGE,"E209");var subQ373=sQuery(id+"F0.wireOp",EDGE,"E208");var subQ374=sQuery(id+"F0.wireOp",EDGE,"E207");var subQ375=sQuery(id+"F0.wireOp",EDGE,"E206");var subQ376=sQuery(id+"F0.wireOp",EDGE,"E205");var subQ377=sQuery(id+"F0.wireOp",EDGE,"E204");var subQ378=sQuery(id+"F0.wireOp",EDGE,"E203");var subQ379=sQuery(id+"F0.wireOp",EDGE,"E202");var subQ380=sQuery(id+"F0.wireOp",EDGE,"E201");var subQ381=sQuery(id+"F0.wireOp",EDGE,"E200");var subQ382=sQuery(id+"F0.wireOp",EDGE,"E199");var subQ383=sQuery(id+"F0.wireOp",EDGE,"E198");var subQ384=sQuery(id+"F0.wireOp",EDGE,"E197");var subQ385=sQuery(id+"F0.wireOp",EDGE,"E196");var subQ386=sQuery(id+"F0.wireOp",EDGE,"E195");var subQ387=sQuery(id+"F0.wireOp",EDGE,"E194");var subQ388=sQuery(id+"F0.wireOp",EDGE,"E193");var subQ389=sQuery(id+"F0.wireOp",EDGE,"E192");var subQ390=sQuery(id+"F0.wireOp",EDGE,"E191");var subQ391=sQuery(id+"F0.wireOp",EDGE,"E190");var subQ392=sQuery(id+"F0.wireOp",EDGE,"E189");var subQ393=sQuery(id+"F0.wireOp",EDGE,"E188");var subQ394=sQuery(id+"F0.wireOp",EDGE,"E187");var subQ395=sQuery(id+"F0.wireOp",EDGE,"E186");var subQ396=sQuery(id+"F0.wireOp",EDGE,"E185");var subQ397=sQuery(id+"F0.wireOp",EDGE,"E184");var subQ398=sQuery(id+"F0.wireOp",EDGE,"E183");var subQ399=sQuery(id+"F0.wireOp",EDGE,"E182");var subQ400=sQuery(id+"F0.wireOp",EDGE,"E181");var subQ401=sQuery(id+"F0.wireOp",EDGE,"E180");var subQ402=sQuery(id+"F0.wireOp",EDGE,"E179");var subQ403=sQuery(id+"F0.wireOp",EDGE,"E178");var subQ404=sQuery(id+"F0.wireOp",EDGE,"E177");var subQ405=sQuery(id+"F0.wireOp",EDGE,"E176");var subQ406=sQuery(id+"F0.wireOp",EDGE,"E175");var subQ407=sQuery(id+"F0.wireOp",EDGE,"E174");var subQ408=sQuery(id+"F0.wireOp",EDGE,"E173");var subQ409=sQuery(id+"F0.wireOp",EDGE,"E172");var subQ410=sQuery(id+"F0.wireOp",EDGE,"E171");var subQ411=sQuery(id+"F0.wireOp",EDGE,"E170");var subQ412=sQuery(id+"F0.wireOp",EDGE,"E169");var subQ413=sQuery(id+"F0.wireOp",EDGE,"E168");var subQ414=sQuery(id+"F0.wireOp",EDGE,"E167");var subQ415=sQuery(id+"F0.wireOp",EDGE,"E166");var subQ416=sQuery(id+"F0.wireOp",EDGE,"E165");var subQ417=sQuery(id+"F0.wireOp",EDGE,"E164");var subQ418=sQuery(id+"F0.wireOp",EDGE,"E163");var subQ419=sQuery(id+"F0.wireOp",EDGE,"E162");var subQ420=sQuery(id+"F0.wireOp",EDGE,"E161");var subQ421=sQuery(id+"F0.wireOp",EDGE,"E160");var subQ422=sQuery(id+"F0.wireOp",EDGE,"E159");var subQ423=sQuery(id+"F0.wireOp",EDGE,"E158");var subQ424=sQuery(id+"F0.wireOp",EDGE,"E157");var subQ425=sQuery(id+"F0.wireOp",EDGE,"E156");var subQ426=sQuery(id+"F0.wireOp",EDGE,"E155");var subQ427=sQuery(id+"F0.wireOp",EDGE,"E154");var subQ428=sQuery(id+"F0.wireOp",EDGE,"E153");var subQ429=sQuery(id+"F0.wireOp",EDGE,"E152");var subQ430=sQuery(id+"F0.wireOp",EDGE,"E151");var subQ431=sQuery(id+"F0.wireOp",EDGE,"E150");var subQ432=sQuery(id+"F0.wireOp",EDGE,"E149");var subQ433=sQuery(id+"F0.wireOp",EDGE,"E148");var subQ434=sQuery(id+"F0.wireOp",EDGE,"E147");var subQ435=sQuery(id+"F0.wireOp",EDGE,"E146");var subQ436=sQuery(id+"F0.wireOp",EDGE,"E145");var subQ437=sQuery(id+"F0.wireOp",EDGE,"E144");var subQ438=sQuery(id+"F0.wireOp",EDGE,"E143");var subQ439=sQuery(id+"F0.wireOp",EDGE,"E142");var subQ440=sQuery(id+"F0.wireOp",EDGE,"E141");var subQ441=sQuery(id+"F0.wireOp",EDGE,"E140");var subQ442=sQuery(id+"F0.wireOp",EDGE,"E139");var subQ443=sQuery(id+"F0.wireOp",EDGE,"E138");var subQ444=sQuery(id+"F0.wireOp",EDGE,"E137");var subQ445=sQuery(id+"F0.wireOp",EDGE,"E136");var subQ446=sQuery(id+"F0.wireOp",EDGE,"E135");var subQ447=sQuery(id+"F0.wireOp",EDGE,"E134");var subQ448=sQuery(id+"F0.wireOp",EDGE,"E133");var subQ449=sQuery(id+"F0.wireOp",EDGE,"E132");var subQ450=sQuery(id+"F0.wireOp",EDGE,"E131");var subQ451=sQuery(id+"F0.wireOp",EDGE,"E130");var subQ452=sQuery(id+"F0.wireOp",EDGE,"E129");var subQ453=sQuery(id+"F0.wireOp",EDGE,"E128");var subQ454=sQuery(id+"F0.wireOp",EDGE,"E127");var subQ455=sQuery(id+"F0.wireOp",EDGE,"E126");var subQ456=sQuery(id+"F0.wireOp",EDGE,"E125");var subQ457=sQuery(id+"F0.wireOp",EDGE,"E124");var subQ458=sQuery(id+"F0.wireOp",EDGE,"E123");var subQ459=sQuery(id+"F0.wireOp",EDGE,"E122");var subQ460=sQuery(id+"F0.wireOp",EDGE,"E121");var subQ461=sQuery(id+"F0.wireOp",EDGE,"E120");var subQ462=sQuery(id+"F0.wireOp",EDGE,"E119");var subQ463=sQuery(id+"F0.wireOp",EDGE,"E118");var subQ464=sQuery(id+"F0.wireOp",EDGE,"E117");var subQ465=sQuery(id+"F0.wireOp",EDGE,"E116");var subQ466=sQuery(id+"F0.wireOp",EDGE,"E115");var subQ467=sQuery(id+"F0.wireOp",EDGE,"E114");var subQ468=sQuery(id+"F0.wireOp",EDGE,"E113");var subQ469=sQuery(id+"F0.wireOp",EDGE,"E112");var subQ470=sQuery(id+"F0.wireOp",EDGE,"E111");var subQ471=sQuery(id+"F0.wireOp",EDGE,"E110");var subQ472=sQuery(id+"F0.wireOp",EDGE,"E109");var subQ473=sQuery(id+"F0.wireOp",EDGE,"E108");var subQ474=sQuery(id+"F0.wireOp",EDGE,"E107");var subQ475=sQuery(id+"F0.wireOp",EDGE,"E106");var subQ476=sQuery(id+"F0.wireOp",EDGE,"E105");var subQ477=sQuery(id+"F0.wireOp",EDGE,"E104");var subQ478=sQuery(id+"F0.wireOp",EDGE,"E103");var subQ479=sQuery(id+"F0.wireOp",EDGE,"E102");var subQ480=sQuery(id+"F0.wireOp",EDGE,"E101");var subQ481=sQuery(id+"F0.wireOp",EDGE,"E100");var subQ482=sQuery(id+"F0.wireOp",EDGE,"E99");var subQ483=sQuery(id+"F0.wireOp",EDGE,"E98");var subQ484=sQuery(id+"F0.wireOp",EDGE,"E97");var subQ485=sQuery(id+"F0.wireOp",EDGE,"E96");var subQ486=sQuery(id+"F0.wireOp",EDGE,"E95");var subQ487=sQuery(id+"F0.wireOp",EDGE,"E94");var subQ488=sQuery(id+"F0.wireOp",EDGE,"E93");var subQ489=sQuery(id+"F0.wireOp",EDGE,"E92");var subQ490=sQuery(id+"F0.wireOp",EDGE,"E91");var subQ491=sQuery(id+"F0.wireOp",EDGE,"E90");var subQ492=sQuery(id+"F0.wireOp",EDGE,"E89");var subQ493=sQuery(id+"F0.wireOp",EDGE,"E88");var subQ494=sQuery(id+"F0.wireOp",EDGE,"E87");var subQ495=sQuery(id+"F0.wireOp",EDGE,"E86");var subQ496=sQuery(id+"F0.wireOp",EDGE,"E85");var subQ497=sQuery(id+"F0.wireOp",EDGE,"E84");var subQ498=sQuery(id+"F0.wireOp",EDGE,"E83");var subQ499=sQuery(id+"F0.wireOp",EDGE,"E82");var subQ500=sQuery(id+"F0.wireOp",EDGE,"E81");var subQ501=sQuery(id+"F0.wireOp",EDGE,"E80");var subQ502=sQuery(id+"F0.wireOp",EDGE,"E79");var subQ503=sQuery(id+"F0.wireOp",EDGE,"E78");var subQ504=sQuery(id+"F0.wireOp",EDGE,"E77");var subQ505=sQuery(id+"F0.wireOp",EDGE,"E76");var subQ506=sQuery(id+"F0.wireOp",EDGE,"E75");var subQ507=sQuery(id+"F0.wireOp",EDGE,"E74");var subQ508=sQuery(id+"F0.wireOp",EDGE,"E73");var subQ509=sQuery(id+"F0.wireOp",EDGE,"E72");var subQ510=sQuery(id+"F0.wireOp",EDGE,"E71");var subQ511=sQuery(id+"F0.wireOp",EDGE,"E70");var subQ512=sQuery(id+"F0.wireOp",EDGE,"E69");var subQ513=sQuery(id+"F0.wireOp",EDGE,"E68");var subQ514=sQuery(id+"F0.wireOp",EDGE,"E67");var subQ515=sQuery(id+"F0.wireOp",EDGE,"E66");var subQ516=sQuery(id+"F0.wireOp",EDGE,"E65");var subQ517=sQuery(id+"F0.wireOp",EDGE,"E64");var subQ518=sQuery(id+"F0.wireOp",EDGE,"E63");var subQ519=sQuery(id+"F0.wireOp",EDGE,"E62");var subQ520=sQuery(id+"F0.wireOp",EDGE,"E61");var subQ521=sQuery(id+"F0.wireOp",EDGE,"E60");var subQ522=sQuery(id+"F0.wireOp",EDGE,"E59");var subQ523=sQuery(id+"F0.wireOp",EDGE,"E58");var subQ524=sQuery(id+"F0.wireOp",EDGE,"E57");var subQ525=sQuery(id+"F0.wireOp",EDGE,"E56");var subQ526=sQuery(id+"F0.wireOp",EDGE,"E55");var subQ527=sQuery(id+"F0.wireOp",EDGE,"E54");var subQ528=sQuery(id+"F0.wireOp",EDGE,"E53");var subQ529=sQuery(id+"F0.wireOp",EDGE,"E52");var subQ530=sQuery(id+"F0.wireOp",EDGE,"E51");var subQ531=sQuery(id+"F0.wireOp",EDGE,"E50");var subQ532=sQuery(id+"F0.wireOp",EDGE,"E49");var subQ533=sQuery(id+"F0.wireOp",EDGE,"E48");var subQ534=sQuery(id+"F0.wireOp",EDGE,"E47");var subQ535=sQuery(id+"F0.wireOp",EDGE,"E46");var subQ536=sQuery(id+"F0.wireOp",EDGE,"E45");var subQ537=sQuery(id+"F0.wireOp",EDGE,"E44");var subQ538=sQuery(id+"F0.wireOp",EDGE,"E43");var subQ539=sQuery(id+"F0.wireOp",EDGE,"E42");var subQ540=sQuery(id+"F0.wireOp",EDGE,"E41");var subQ541=sQuery(id+"F0.wireOp",EDGE,"E40");var subQ542=sQuery(id+"F0.wireOp",EDGE,"E39");var subQ543=sQuery(id+"F0.wireOp",EDGE,"E38");var subQ544=sQuery(id+"F0.wireOp",EDGE,"E37");var subQ545=sQuery(id+"F0.wireOp",EDGE,"E36");var subQ546=sQuery(id+"F0.wireOp",EDGE,"E35");var subQ547=sQuery(id+"F0.wireOp",EDGE,"E34");var subQ548=sQuery(id+"F0.wireOp",EDGE,"E33");var subQ549=sQuery(id+"F0.wireOp",EDGE,"E32");var subQ550=sQuery(id+"F0.wireOp",EDGE,"E31");var subQ551=sQuery(id+"F0.wireOp",EDGE,"E30");var subQ552=sQuery(id+"F0.wireOp",EDGE,"E29");var subQ553=sQuery(id+"F0.wireOp",EDGE,"E28");var subQ554=sQuery(id+"F0.wireOp",EDGE,"E27");var subQ555=sQuery(id+"F0.wireOp",EDGE,"E26");var subQ556=sQuery(id+"F0.wireOp",EDGE,"E25");var subQ557=sQuery(id+"F0.wireOp",EDGE,"E24");var subQ558=sQuery(id+"F0.wireOp",EDGE,"E23");var subQ559=sQuery(id+"F0.wireOp",EDGE,"E22");var subQ560=sQuery(id+"F0.wireOp",EDGE,"E21");var subQ561=sQuery(id+"F0.wireOp",EDGE,"E20");var subQ562=sQuery(id+"F0.wireOp",EDGE,"E19");var subQ563=sQuery(id+"F0.wireOp",EDGE,"E18");var subQ564=sQuery(id+"F0.wireOp",EDGE,"E17");var subQ565=sQuery(id+"F0.wireOp",EDGE,"E16");var subQ566=sQuery(id+"F0.wireOp",EDGE,"E15");var subQ567=sQuery(id+"F0.wireOp",EDGE,"E14");var subQ568=sQuery(id+"F0.wireOp",EDGE,"E13");var subQ569=sQuery(id+"F0.wireOp",EDGE,"E12");var subQ570=sQuery(id+"F0.wireOp",EDGE,"E11");var subQ571=sQuery(id+"F0.wireOp",EDGE,"E10");var subQ572=sQuery(id+"F0.wireOp",EDGE,"E9");var subQ573=sQuery(id+"F0.wireOp",EDGE,"E8");var subQ574=sQuery(id+"F0.wireOp",EDGE,"E7");var subQ575=sQuery(id+"F0.wireOp",EDGE,"E6");var subQ576=sQuery(id+"F0.wireOp",EDGE,"E5");var subQ577=sQuery(id+"F0.wireOp",EDGE,"E4");var subQ578=sQuery(id+"F0.wireOp",EDGE,"E3");var subQ579=sQuery(id+"F0.wireOp",EDGE,"E2");var subQ580=sQuery(id+"F0.wireOp",EDGE,"E1");var subQ581=sQuery(id+"F0.wireOp",EDGE,"E0");Q0=makeQuery(id+"F10.boolean.opBoolean","SPLIT",FACE,{"disambiguationData":[TD([makeQuery(id+"F1.opExtrude","SWEPT_FACE",FACE,{"disambiguationData":[OSD([subQ1])]})])],"derivedFrom":makeQuery(id+"F1.opExtrude","CAP_FACE",FACE,{"disambiguationData":[OSD([subQ581,subQ580,subQ579,subQ578,subQ577,subQ576,subQ575,subQ574,subQ573,subQ572,subQ571,subQ570,subQ569,subQ568,subQ567,subQ566,subQ565,subQ564,subQ563,subQ562,subQ561,subQ560,subQ559,subQ558,subQ557,subQ556,subQ555,subQ554,subQ553,subQ552,subQ551,subQ550,subQ549,subQ548,subQ547,subQ546,subQ545,subQ544,subQ543,subQ542,subQ541,subQ540,subQ539,subQ538,subQ537,subQ536,subQ535,subQ534,subQ533,subQ532,subQ531,subQ530,subQ529,subQ528,subQ527,subQ526,subQ525,subQ524,subQ523,subQ522,subQ521,subQ520,subQ519,subQ518,subQ517,subQ516,subQ515,subQ514,subQ513,subQ512,subQ511,subQ510,subQ509,subQ508,subQ507,subQ506,subQ505,subQ504,subQ503,subQ502,subQ501,subQ500,subQ499,subQ498,subQ497,subQ496,subQ495,subQ494,subQ493,subQ492,subQ491,subQ490,subQ489,subQ488,subQ487,subQ486,subQ485,subQ484,subQ483,subQ482,subQ481,subQ480,subQ479,subQ478,subQ477,subQ476,subQ475,subQ474,subQ473,subQ472,subQ471,subQ470,subQ469,subQ468,subQ467,subQ466,subQ465,subQ464,subQ463,subQ462,subQ461,subQ460,subQ459,subQ458,subQ457,subQ456,subQ455,subQ454,subQ453,subQ452,subQ451,subQ450,subQ449,subQ448,subQ447,subQ446,subQ445,subQ444,subQ443,subQ442,subQ441,subQ440,subQ439,subQ438,subQ437,subQ436,subQ435,subQ434,subQ433,subQ432,subQ431,subQ430,subQ429,subQ428,subQ427,subQ426,subQ425,subQ424,subQ423,subQ422,subQ421,subQ420,subQ419,subQ418,subQ417,subQ416,subQ415,subQ414,subQ413,subQ412,subQ411,subQ410,subQ409,subQ408,subQ407,subQ406,subQ405,subQ404,subQ403,subQ402,subQ401,subQ400,subQ399,subQ398,subQ397,subQ396,subQ395,subQ394,subQ393,subQ392,subQ391,subQ390,subQ389,subQ388,subQ387,subQ386,subQ385,subQ384,subQ383,subQ382,subQ381,subQ380,subQ379,subQ378,subQ377,subQ376,subQ375,subQ374,subQ373,subQ372,subQ371,subQ370,subQ369,subQ368,subQ367,subQ366,subQ365,subQ364,subQ363,subQ362,subQ361,subQ360,subQ359,subQ358,subQ357,subQ356,subQ355,subQ354,subQ353,subQ352,subQ351,subQ350,subQ349,subQ348,subQ347,subQ346,subQ345,subQ344,subQ343,subQ342,subQ341,subQ340,subQ339,subQ338,subQ337,subQ336,subQ335,subQ334,subQ333,subQ332,subQ331,subQ330,subQ329,subQ328,subQ327,subQ326,subQ325,subQ324,subQ323,subQ322,subQ321,subQ320,subQ319,subQ318,subQ317,subQ316,subQ315,subQ314,subQ313,subQ312,subQ311,subQ310,subQ309,subQ308,subQ307,subQ306,subQ305,subQ304,subQ303,subQ302,subQ301,subQ300,subQ299,subQ298,subQ297,subQ296,subQ295,subQ294,subQ293,subQ292,subQ291,subQ290,subQ289,subQ288,subQ287,subQ286,subQ285,subQ284,subQ283,subQ282,subQ281,subQ280,subQ279,subQ278,subQ277,subQ276,subQ275,subQ274,subQ273,subQ272,subQ271,subQ270,subQ269,subQ268,subQ267,subQ266,subQ265,subQ264,subQ263,subQ262,subQ261,subQ260,subQ259,subQ258,subQ257,subQ256,subQ255,subQ254,subQ253,subQ252,subQ251,subQ250,subQ249,subQ248,subQ247,subQ246,subQ245,subQ244,subQ243,subQ242,subQ1,subQ0,subQ241,subQ240,subQ239,subQ238,subQ237,subQ236,subQ235,subQ234,subQ233,subQ232,subQ231,subQ230,subQ229,subQ228,subQ227,subQ226,subQ225,subQ224,subQ223,subQ222,subQ221,subQ220,subQ219,subQ218,subQ217,subQ216,subQ215,subQ214,subQ213,subQ212,subQ211,subQ210,subQ209,subQ208,subQ207,subQ206,subQ205,subQ204,subQ203,subQ202,subQ201,subQ200,subQ199,subQ198,subQ197,subQ196,subQ195,subQ194,subQ193,subQ192,subQ191,subQ190,subQ189,subQ188,subQ187,subQ186,subQ185,subQ184,subQ183,subQ182,subQ181,subQ180,subQ179,subQ178,subQ177,subQ176,subQ175,subQ174,subQ173,subQ172,subQ171,subQ170,subQ169,subQ168,subQ167,subQ166,subQ165,subQ164,subQ163,subQ162,subQ161,subQ160,subQ159,subQ158,subQ157,subQ156,subQ155,subQ154,subQ153,subQ152,subQ151,subQ150,subQ149,subQ148,subQ147,subQ146,subQ145,subQ144,subQ143,subQ142,subQ141,subQ140,subQ139,subQ138,subQ137,subQ136,subQ135,subQ134,subQ133,subQ132,subQ131,subQ130,subQ129,subQ128,subQ127,subQ126,subQ125,subQ124,subQ123,subQ122,subQ121,subQ120,subQ119,subQ118,subQ117,subQ116,subQ115,subQ114,subQ113,subQ112,subQ111,subQ110,subQ109,subQ108,subQ107,subQ106,subQ105,subQ104,subQ103,subQ102,subQ101,subQ100,subQ99,subQ98,subQ97,subQ96,subQ95,subQ94,subQ93,subQ92,subQ91,subQ90,subQ89,subQ88,subQ87,subQ86,subQ85,subQ84,subQ83,subQ82,subQ81,subQ80,subQ79,subQ78,subQ77,subQ76,subQ75,subQ74,subQ73,subQ72,subQ71,subQ70,subQ69,subQ68,subQ67,subQ66,subQ65,subQ64,subQ63,subQ62,subQ61,subQ60,subQ59,subQ58,subQ57,subQ56,subQ55,subQ54,subQ53,subQ52,subQ51,subQ50,subQ49,subQ48,subQ47,subQ46,subQ45,subQ44,subQ43,subQ42,subQ41,subQ40,subQ39,subQ38,subQ37,subQ36,subQ35,subQ34,subQ33,subQ32,subQ31,subQ30,subQ29,subQ28,subQ27,subQ26,subQ25,subQ24,subQ23,subQ22,subQ21,subQ20,subQ19,subQ18,subQ17,subQ16,subQ15,subQ14,subQ13,subQ12,subQ11,subQ10,subQ9,subQ8,subQ7,subQ6,subQ5,subQ4])],"isStart":false})});}
            var sketch = newSketch(context, id + "F15", { "sketchPlane" : qUnion([Q0])});
            skLineSegment(sketch, "E2044.0", {"start": v(-117.47, 2.24) * mm, "end": v(-117.47, -7.77) * mm});
            skLineSegment(sketch, "E2045", {"start": v(-117.47, 2.24) * mm, "end": v(-116.22, 2.24) * mm});
            skLineSegment(sketch, "E2046", {"start": v(-116.22, 2.24) * mm, "end": v(-116.22, -7.77) * mm});
            skLineSegment(sketch, "E2047", {"start": v(-116.22, -7.77) * mm, "end": v(-117.47, -7.77) * mm});
            skSolve(sketch);
        }
        {
            var Q0;
            Q0 = qSketchRegion(id + "F15", true);
            var Q1;
            {var subQ0=sQuery(id+"F2.wireOp",EDGE,"E2024");var subQ1=sQuery(id+"F2.wireOp",EDGE,"E2023");Q1=makeQuery(id+"F12.boolean.opBoolean","MERGE",FACE,{"derivedFrom":[makeQuery(id+"F10.boolean.opBoolean","MERGE",FACE,{"derivedFrom":[makeQuery(id+"F9.boolean.opBoolean","MERGE",FACE,{"derivedFrom":[makeQuery(id+"F3.opExtrude","CAP_FACE",FACE,{"disambiguationData":[OSD([sQuery(id+"F2.wireOp",EDGE,"E1307"),sQuery(id+"F2.wireOp",EDGE,"E1308"),sQuery(id+"F2.wireOp",EDGE,"E1309"),sQuery(id+"F2.wireOp",EDGE,"E1310"),sQuery(id+"F2.wireOp",EDGE,"E1311"),sQuery(id+"F2.wireOp",EDGE,"E1312"),sQuery(id+"F2.wireOp",EDGE,"E1313"),sQuery(id+"F2.wireOp",EDGE,"E1314"),sQuery(id+"F2.wireOp",EDGE,"E1315"),sQuery(id+"F2.wireOp",EDGE,"E1316"),sQuery(id+"F2.wireOp",EDGE,"E1317"),sQuery(id+"F2.wireOp",EDGE,"E1318"),sQuery(id+"F2.wireOp",EDGE,"E1319"),sQuery(id+"F2.wireOp",EDGE,"E1320"),sQuery(id+"F2.wireOp",EDGE,"E1321"),sQuery(id+"F2.wireOp",EDGE,"E1322"),sQuery(id+"F2.wireOp",EDGE,"E1323"),sQuery(id+"F2.wireOp",EDGE,"E1324"),sQuery(id+"F2.wireOp",EDGE,"E1325"),sQuery(id+"F2.wireOp",EDGE,"E1326"),sQuery(id+"F2.wireOp",EDGE,"E1327"),sQuery(id+"F2.wireOp",EDGE,"E1328"),sQuery(id+"F2.wireOp",EDGE,"E1329"),sQuery(id+"F2.wireOp",EDGE,"E1330"),sQuery(id+"F2.wireOp",EDGE,"E1331"),sQuery(id+"F2.wireOp",EDGE,"E1332"),sQuery(id+"F2.wireOp",EDGE,"E1333"),sQuery(id+"F2.wireOp",EDGE,"E1334"),sQuery(id+"F2.wireOp",EDGE,"E1335"),sQuery(id+"F2.wireOp",EDGE,"E1336"),sQuery(id+"F2.wireOp",EDGE,"E1337"),sQuery(id+"F2.wireOp",EDGE,"E1338"),sQuery(id+"F2.wireOp",EDGE,"E1339"),sQuery(id+"F2.wireOp",EDGE,"E1340"),sQuery(id+"F2.wireOp",EDGE,"E1341"),sQuery(id+"F2.wireOp",EDGE,"E1342"),sQuery(id+"F2.wireOp",EDGE,"E1343"),sQuery(id+"F2.wireOp",EDGE,"E1344"),sQuery(id+"F2.wireOp",EDGE,"E1345"),sQuery(id+"F2.wireOp",EDGE,"E1346"),sQuery(id+"F2.wireOp",EDGE,"E1347"),sQuery(id+"F2.wireOp",EDGE,"E1348"),sQuery(id+"F2.wireOp",EDGE,"E1349"),sQuery(id+"F2.wireOp",EDGE,"E1350"),sQuery(id+"F2.wireOp",EDGE,"E1351"),sQuery(id+"F2.wireOp",EDGE,"E1352"),sQuery(id+"F2.wireOp",EDGE,"E1353"),sQuery(id+"F2.wireOp",EDGE,"E1354"),sQuery(id+"F2.wireOp",EDGE,"E1355"),sQuery(id+"F2.wireOp",EDGE,"E1356"),sQuery(id+"F2.wireOp",EDGE,"E1357"),sQuery(id+"F2.wireOp",EDGE,"E1358"),sQuery(id+"F2.wireOp",EDGE,"E1359"),sQuery(id+"F2.wireOp",EDGE,"E1360"),sQuery(id+"F2.wireOp",EDGE,"E1361"),sQuery(id+"F2.wireOp",EDGE,"E1362"),sQuery(id+"F2.wireOp",EDGE,"E1363"),sQuery(id+"F2.wireOp",EDGE,"E1364"),sQuery(id+"F2.wireOp",EDGE,"E1365"),sQuery(id+"F2.wireOp",EDGE,"E1366"),sQuery(id+"F2.wireOp",EDGE,"E1367"),sQuery(id+"F2.wireOp",EDGE,"E1368"),sQuery(id+"F2.wireOp",EDGE,"E1369"),sQuery(id+"F2.wireOp",EDGE,"E1370"),sQuery(id+"F2.wireOp",EDGE,"E1371"),sQuery(id+"F2.wireOp",EDGE,"E1372"),sQuery(id+"F2.wireOp",EDGE,"E1373"),sQuery(id+"F2.wireOp",EDGE,"E1374"),sQuery(id+"F2.wireOp",EDGE,"E1375"),sQuery(id+"F2.wireOp",EDGE,"E1376"),sQuery(id+"F2.wireOp",EDGE,"E1377"),sQuery(id+"F2.wireOp",EDGE,"E1378"),sQuery(id+"F2.wireOp",EDGE,"E1379"),sQuery(id+"F2.wireOp",EDGE,"E1380"),sQuery(id+"F2.wireOp",EDGE,"E1381"),sQuery(id+"F2.wireOp",EDGE,"E1382"),sQuery(id+"F2.wireOp",EDGE,"E1383"),sQuery(id+"F2.wireOp",EDGE,"E1384"),sQuery(id+"F2.wireOp",EDGE,"E1385"),sQuery(id+"F2.wireOp",EDGE,"E1386"),sQuery(id+"F2.wireOp",EDGE,"E1387"),sQuery(id+"F2.wireOp",EDGE,"E1388"),sQuery(id+"F2.wireOp",EDGE,"E1389"),sQuery(id+"F2.wireOp",EDGE,"E1390"),sQuery(id+"F2.wireOp",EDGE,"E1391"),sQuery(id+"F2.wireOp",EDGE,"E1392"),sQuery(id+"F2.wireOp",EDGE,"E1393"),sQuery(id+"F2.wireOp",EDGE,"E1394"),sQuery(id+"F2.wireOp",EDGE,"E1395"),sQuery(id+"F2.wireOp",EDGE,"E1396"),sQuery(id+"F2.wireOp",EDGE,"E1397"),sQuery(id+"F2.wireOp",EDGE,"E1398"),sQuery(id+"F2.wireOp",EDGE,"E1399"),sQuery(id+"F2.wireOp",EDGE,"E1400"),sQuery(id+"F2.wireOp",EDGE,"E1401"),sQuery(id+"F2.wireOp",EDGE,"E1402"),sQuery(id+"F2.wireOp",EDGE,"E1403"),sQuery(id+"F2.wireOp",EDGE,"E1404"),sQuery(id+"F2.wireOp",EDGE,"E1405"),sQuery(id+"F2.wireOp",EDGE,"E1406"),sQuery(id+"F2.wireOp",EDGE,"E1407"),sQuery(id+"F2.wireOp",EDGE,"E1408"),sQuery(id+"F2.wireOp",EDGE,"E1409"),sQuery(id+"F2.wireOp",EDGE,"E1410"),sQuery(id+"F2.wireOp",EDGE,"E1411"),sQuery(id+"F2.wireOp",EDGE,"E1412"),sQuery(id+"F2.wireOp",EDGE,"E1413"),sQuery(id+"F2.wireOp",EDGE,"E1414"),sQuery(id+"F2.wireOp",EDGE,"E1415"),sQuery(id+"F2.wireOp",EDGE,"E1416"),sQuery(id+"F2.wireOp",EDGE,"E1417"),sQuery(id+"F2.wireOp",EDGE,"E1418"),sQuery(id+"F2.wireOp",EDGE,"E1419"),sQuery(id+"F2.wireOp",EDGE,"E1420"),sQuery(id+"F2.wireOp",EDGE,"E1421"),sQuery(id+"F2.wireOp",EDGE,"E1422"),sQuery(id+"F2.wireOp",EDGE,"E1423"),sQuery(id+"F2.wireOp",EDGE,"E1424"),sQuery(id+"F2.wireOp",EDGE,"E1425"),sQuery(id+"F2.wireOp",EDGE,"E1426"),sQuery(id+"F2.wireOp",EDGE,"E1427"),sQuery(id+"F2.wireOp",EDGE,"E1428"),sQuery(id+"F2.wireOp",EDGE,"E1429"),sQuery(id+"F2.wireOp",EDGE,"E1430"),sQuery(id+"F2.wireOp",EDGE,"E1431"),sQuery(id+"F2.wireOp",EDGE,"E1432"),sQuery(id+"F2.wireOp",EDGE,"E1433"),sQuery(id+"F2.wireOp",EDGE,"E1434"),sQuery(id+"F2.wireOp",EDGE,"E1435"),sQuery(id+"F2.wireOp",EDGE,"E1436"),sQuery(id+"F2.wireOp",EDGE,"E1437"),sQuery(id+"F2.wireOp",EDGE,"E1438"),sQuery(id+"F2.wireOp",EDGE,"E1439"),sQuery(id+"F2.wireOp",EDGE,"E1440"),sQuery(id+"F2.wireOp",EDGE,"E1441"),sQuery(id+"F2.wireOp",EDGE,"E1442"),sQuery(id+"F2.wireOp",EDGE,"E1443"),sQuery(id+"F2.wireOp",EDGE,"E1444"),sQuery(id+"F2.wireOp",EDGE,"E1445"),sQuery(id+"F2.wireOp",EDGE,"E1446"),sQuery(id+"F2.wireOp",EDGE,"E1447"),sQuery(id+"F2.wireOp",EDGE,"E1448"),sQuery(id+"F2.wireOp",EDGE,"E1449"),sQuery(id+"F2.wireOp",EDGE,"E1450"),sQuery(id+"F2.wireOp",EDGE,"E1451"),sQuery(id+"F2.wireOp",EDGE,"E1452"),sQuery(id+"F2.wireOp",EDGE,"E1453"),sQuery(id+"F2.wireOp",EDGE,"E1454"),sQuery(id+"F2.wireOp",EDGE,"E1455"),sQuery(id+"F2.wireOp",EDGE,"E1456"),sQuery(id+"F2.wireOp",EDGE,"E1457"),sQuery(id+"F2.wireOp",EDGE,"E1458"),sQuery(id+"F2.wireOp",EDGE,"E1459"),sQuery(id+"F2.wireOp",EDGE,"E1742"),sQuery(id+"F2.wireOp",EDGE,"E1743"),sQuery(id+"F2.wireOp",EDGE,"E1744"),sQuery(id+"F2.wireOp",EDGE,"E1745"),sQuery(id+"F2.wireOp",EDGE,"E1746"),sQuery(id+"F2.wireOp",EDGE,"E1747"),sQuery(id+"F2.wireOp",EDGE,"E1748"),sQuery(id+"F2.wireOp",EDGE,"E1749"),sQuery(id+"F2.wireOp",EDGE,"E1750"),sQuery(id+"F2.wireOp",EDGE,"E1751"),sQuery(id+"F2.wireOp",EDGE,"E1752"),sQuery(id+"F2.wireOp",EDGE,"E1753"),sQuery(id+"F2.wireOp",EDGE,"E1754"),sQuery(id+"F2.wireOp",EDGE,"E1755"),sQuery(id+"F2.wireOp",EDGE,"E1756"),sQuery(id+"F2.wireOp",EDGE,"E1757"),sQuery(id+"F2.wireOp",EDGE,"E1758"),sQuery(id+"F2.wireOp",EDGE,"E1759"),sQuery(id+"F2.wireOp",EDGE,"E1760"),sQuery(id+"F2.wireOp",EDGE,"E1761"),sQuery(id+"F2.wireOp",EDGE,"E1762"),sQuery(id+"F2.wireOp",EDGE,"E1763"),sQuery(id+"F2.wireOp",EDGE,"E1764"),sQuery(id+"F2.wireOp",EDGE,"E1765"),sQuery(id+"F2.wireOp",EDGE,"E1766"),sQuery(id+"F2.wireOp",EDGE,"E1767"),sQuery(id+"F2.wireOp",EDGE,"E1768"),sQuery(id+"F2.wireOp",EDGE,"E1769"),sQuery(id+"F2.wireOp",EDGE,"E1770"),sQuery(id+"F2.wireOp",EDGE,"E1771"),sQuery(id+"F2.wireOp",EDGE,"E1772"),sQuery(id+"F2.wireOp",EDGE,"E1773"),sQuery(id+"F2.wireOp",EDGE,"E1774"),sQuery(id+"F2.wireOp",EDGE,"E1775"),sQuery(id+"F2.wireOp",EDGE,"E1776"),sQuery(id+"F2.wireOp",EDGE,"E1777"),sQuery(id+"F2.wireOp",EDGE,"E1778"),sQuery(id+"F2.wireOp",EDGE,"E1779"),sQuery(id+"F2.wireOp",EDGE,"E1780"),sQuery(id+"F2.wireOp",EDGE,"E1781"),sQuery(id+"F2.wireOp",EDGE,"E1782"),sQuery(id+"F2.wireOp",EDGE,"E1783"),sQuery(id+"F2.wireOp",EDGE,"E1784"),sQuery(id+"F2.wireOp",EDGE,"E1785"),sQuery(id+"F2.wireOp",EDGE,"E1786"),sQuery(id+"F2.wireOp",EDGE,"E1787"),sQuery(id+"F2.wireOp",EDGE,"E1788"),sQuery(id+"F2.wireOp",EDGE,"E1789"),sQuery(id+"F2.wireOp",EDGE,"E1790"),sQuery(id+"F2.wireOp",EDGE,"E1791"),sQuery(id+"F2.wireOp",EDGE,"E1792"),sQuery(id+"F2.wireOp",EDGE,"E1793"),sQuery(id+"F2.wireOp",EDGE,"E1794"),sQuery(id+"F2.wireOp",EDGE,"E1795"),sQuery(id+"F2.wireOp",EDGE,"E1796"),sQuery(id+"F2.wireOp",EDGE,"E1797"),sQuery(id+"F2.wireOp",EDGE,"E1798"),sQuery(id+"F2.wireOp",EDGE,"E1799"),sQuery(id+"F2.wireOp",EDGE,"E1800"),sQuery(id+"F2.wireOp",EDGE,"E1801"),sQuery(id+"F2.wireOp",EDGE,"E1802"),sQuery(id+"F2.wireOp",EDGE,"E1803"),sQuery(id+"F2.wireOp",EDGE,"E1804"),sQuery(id+"F2.wireOp",EDGE,"E1805"),sQuery(id+"F2.wireOp",EDGE,"E1806"),sQuery(id+"F2.wireOp",EDGE,"E1807"),sQuery(id+"F2.wireOp",EDGE,"E1808"),sQuery(id+"F2.wireOp",EDGE,"E1809"),sQuery(id+"F2.wireOp",EDGE,"E1810"),sQuery(id+"F2.wireOp",EDGE,"E1811"),sQuery(id+"F2.wireOp",EDGE,"E1812"),sQuery(id+"F2.wireOp",EDGE,"E1813"),sQuery(id+"F2.wireOp",EDGE,"E1814"),sQuery(id+"F2.wireOp",EDGE,"E1815"),sQuery(id+"F2.wireOp",EDGE,"E1816"),sQuery(id+"F2.wireOp",EDGE,"E1817"),sQuery(id+"F2.wireOp",EDGE,"E1818"),sQuery(id+"F2.wireOp",EDGE,"E1819"),sQuery(id+"F2.wireOp",EDGE,"E1820"),sQuery(id+"F2.wireOp",EDGE,"E1821"),sQuery(id+"F2.wireOp",EDGE,"E1822"),sQuery(id+"F2.wireOp",EDGE,"E1823"),sQuery(id+"F2.wireOp",EDGE,"E1824"),sQuery(id+"F2.wireOp",EDGE,"E1825"),sQuery(id+"F2.wireOp",EDGE,"E1826"),sQuery(id+"F2.wireOp",EDGE,"E1827"),sQuery(id+"F2.wireOp",EDGE,"E1828"),sQuery(id+"F2.wireOp",EDGE,"E1829"),sQuery(id+"F2.wireOp",EDGE,"E1830"),sQuery(id+"F2.wireOp",EDGE,"E1831"),sQuery(id+"F2.wireOp",EDGE,"E1832"),sQuery(id+"F2.wireOp",EDGE,"E1833"),sQuery(id+"F2.wireOp",EDGE,"E1834"),sQuery(id+"F2.wireOp",EDGE,"E1835"),sQuery(id+"F2.wireOp",EDGE,"E1836"),sQuery(id+"F2.wireOp",EDGE,"E1837"),sQuery(id+"F2.wireOp",EDGE,"E1838"),sQuery(id+"F2.wireOp",EDGE,"E1839"),sQuery(id+"F2.wireOp",EDGE,"E1840"),sQuery(id+"F2.wireOp",EDGE,"E1841"),sQuery(id+"F2.wireOp",EDGE,"E1842"),sQuery(id+"F2.wireOp",EDGE,"E1843"),sQuery(id+"F2.wireOp",EDGE,"E1844"),sQuery(id+"F2.wireOp",EDGE,"E1845"),sQuery(id+"F2.wireOp",EDGE,"E1846"),sQuery(id+"F2.wireOp",EDGE,"E1847"),sQuery(id+"F2.wireOp",EDGE,"E1848"),sQuery(id+"F2.wireOp",EDGE,"E1849"),sQuery(id+"F2.wireOp",EDGE,"E1850"),sQuery(id+"F2.wireOp",EDGE,"E1851"),sQuery(id+"F2.wireOp",EDGE,"E1852"),sQuery(id+"F2.wireOp",EDGE,"E1853"),sQuery(id+"F2.wireOp",EDGE,"E1854"),sQuery(id+"F2.wireOp",EDGE,"E1855"),sQuery(id+"F2.wireOp",EDGE,"E1856"),sQuery(id+"F2.wireOp",EDGE,"E1857"),sQuery(id+"F2.wireOp",EDGE,"E1858"),sQuery(id+"F2.wireOp",EDGE,"E1859"),sQuery(id+"F2.wireOp",EDGE,"E1860"),sQuery(id+"F2.wireOp",EDGE,"E1861"),sQuery(id+"F2.wireOp",EDGE,"E1862"),sQuery(id+"F2.wireOp",EDGE,"E1863"),sQuery(id+"F2.wireOp",EDGE,"E1864"),sQuery(id+"F2.wireOp",EDGE,"E1865"),sQuery(id+"F2.wireOp",EDGE,"E1866"),sQuery(id+"F2.wireOp",EDGE,"E1867"),sQuery(id+"F2.wireOp",EDGE,"E1868"),sQuery(id+"F2.wireOp",EDGE,"E1869"),sQuery(id+"F2.wireOp",EDGE,"E1870"),sQuery(id+"F2.wireOp",EDGE,"E1871"),sQuery(id+"F2.wireOp",EDGE,"E1872"),sQuery(id+"F2.wireOp",EDGE,"E1873"),sQuery(id+"F2.wireOp",EDGE,"E1874"),sQuery(id+"F2.wireOp",EDGE,"E1875"),sQuery(id+"F2.wireOp",EDGE,"E1876"),sQuery(id+"F2.wireOp",EDGE,"E1877"),sQuery(id+"F2.wireOp",EDGE,"E1878"),sQuery(id+"F2.wireOp",EDGE,"E1879"),sQuery(id+"F2.wireOp",EDGE,"E1880"),sQuery(id+"F2.wireOp",EDGE,"E1881"),sQuery(id+"F2.wireOp",EDGE,"E1882"),sQuery(id+"F2.wireOp",EDGE,"E1883"),sQuery(id+"F2.wireOp",EDGE,"E1884"),sQuery(id+"F2.wireOp",EDGE,"E1885"),sQuery(id+"F2.wireOp",EDGE,"E1886"),sQuery(id+"F2.wireOp",EDGE,"E1887"),sQuery(id+"F2.wireOp",EDGE,"E1888"),sQuery(id+"F2.wireOp",EDGE,"E1889"),sQuery(id+"F2.wireOp",EDGE,"E1890"),sQuery(id+"F2.wireOp",EDGE,"E1891"),sQuery(id+"F2.wireOp",EDGE,"E1892"),sQuery(id+"F2.wireOp",EDGE,"E1893"),sQuery(id+"F2.wireOp",EDGE,"E1894"),sQuery(id+"F2.wireOp",EDGE,"E1895"),sQuery(id+"F2.wireOp",EDGE,"E1896"),sQuery(id+"F2.wireOp",EDGE,"E1897"),sQuery(id+"F2.wireOp",EDGE,"E1898"),sQuery(id+"F2.wireOp",EDGE,"E1899"),sQuery(id+"F2.wireOp",EDGE,"E1900"),sQuery(id+"F2.wireOp",EDGE,"E1901"),sQuery(id+"F2.wireOp",EDGE,"E1902"),sQuery(id+"F2.wireOp",EDGE,"E1903"),sQuery(id+"F2.wireOp",EDGE,"E1904"),sQuery(id+"F2.wireOp",EDGE,"E1905"),sQuery(id+"F2.wireOp",EDGE,"E1906"),sQuery(id+"F2.wireOp",EDGE,"E1907"),sQuery(id+"F2.wireOp",EDGE,"E1908"),sQuery(id+"F2.wireOp",EDGE,"E1909"),sQuery(id+"F2.wireOp",EDGE,"E1910"),sQuery(id+"F2.wireOp",EDGE,"E1911"),sQuery(id+"F2.wireOp",EDGE,"E1912"),sQuery(id+"F2.wireOp",EDGE,"E1913"),sQuery(id+"F2.wireOp",EDGE,"E1914"),sQuery(id+"F2.wireOp",EDGE,"E1915"),sQuery(id+"F2.wireOp",EDGE,"E1916"),sQuery(id+"F2.wireOp",EDGE,"E1917"),sQuery(id+"F2.wireOp",EDGE,"E1918"),sQuery(id+"F2.wireOp",EDGE,"E1919"),sQuery(id+"F2.wireOp",EDGE,"E1920"),sQuery(id+"F2.wireOp",EDGE,"E1921"),sQuery(id+"F2.wireOp",EDGE,"E1922"),sQuery(id+"F2.wireOp",EDGE,"E1923"),sQuery(id+"F2.wireOp",EDGE,"E1924"),sQuery(id+"F2.wireOp",EDGE,"E1925"),sQuery(id+"F2.wireOp",EDGE,"E1926"),sQuery(id+"F2.wireOp",EDGE,"E1927"),sQuery(id+"F2.wireOp",EDGE,"E1928"),sQuery(id+"F2.wireOp",EDGE,"E1929"),sQuery(id+"F2.wireOp",EDGE,"E1930"),sQuery(id+"F2.wireOp",EDGE,"E1931"),sQuery(id+"F2.wireOp",EDGE,"E1932"),sQuery(id+"F2.wireOp",EDGE,"E1933"),sQuery(id+"F2.wireOp",EDGE,"E1934"),sQuery(id+"F2.wireOp",EDGE,"E1935"),sQuery(id+"F2.wireOp",EDGE,"E1936"),sQuery(id+"F2.wireOp",EDGE,"E1937"),sQuery(id+"F2.wireOp",EDGE,"E1938"),sQuery(id+"F2.wireOp",EDGE,"E1939"),sQuery(id+"F2.wireOp",EDGE,"E1940"),sQuery(id+"F2.wireOp",EDGE,"E1941"),sQuery(id+"F2.wireOp",EDGE,"E1942"),sQuery(id+"F2.wireOp",EDGE,"E1943"),sQuery(id+"F2.wireOp",EDGE,"E1944"),sQuery(id+"F2.wireOp",EDGE,"E1945"),sQuery(id+"F2.wireOp",EDGE,"E1946"),sQuery(id+"F2.wireOp",EDGE,"E1947"),sQuery(id+"F2.wireOp",EDGE,"E1948"),sQuery(id+"F2.wireOp",EDGE,"E1949"),sQuery(id+"F2.wireOp",EDGE,"E1950"),sQuery(id+"F2.wireOp",EDGE,"E1951"),sQuery(id+"F2.wireOp",EDGE,"E1952"),sQuery(id+"F2.wireOp",EDGE,"E1953"),sQuery(id+"F2.wireOp",EDGE,"E1954"),sQuery(id+"F2.wireOp",EDGE,"E1955"),sQuery(id+"F2.wireOp",EDGE,"E1956"),sQuery(id+"F2.wireOp",EDGE,"E1957"),sQuery(id+"F2.wireOp",EDGE,"E1958"),sQuery(id+"F2.wireOp",EDGE,"E1959"),sQuery(id+"F2.wireOp",EDGE,"E1960"),sQuery(id+"F2.wireOp",EDGE,"E1961"),sQuery(id+"F2.wireOp",EDGE,"E1962"),sQuery(id+"F2.wireOp",EDGE,"E1963"),sQuery(id+"F2.wireOp",EDGE,"E1964"),sQuery(id+"F2.wireOp",EDGE,"E1965"),sQuery(id+"F2.wireOp",EDGE,"E1966"),sQuery(id+"F2.wireOp",EDGE,"E1967"),sQuery(id+"F2.wireOp",EDGE,"E1968"),sQuery(id+"F2.wireOp",EDGE,"E1969"),sQuery(id+"F2.wireOp",EDGE,"E1970"),sQuery(id+"F2.wireOp",EDGE,"E1971"),sQuery(id+"F2.wireOp",EDGE,"E1972"),sQuery(id+"F2.wireOp",EDGE,"E1973"),sQuery(id+"F2.wireOp",EDGE,"E1974"),sQuery(id+"F2.wireOp",EDGE,"E1975"),sQuery(id+"F2.wireOp",EDGE,"E1976"),sQuery(id+"F2.wireOp",EDGE,"E1977"),sQuery(id+"F2.wireOp",EDGE,"E1978"),sQuery(id+"F2.wireOp",EDGE,"E1979"),sQuery(id+"F2.wireOp",EDGE,"E1980"),sQuery(id+"F2.wireOp",EDGE,"E1981"),sQuery(id+"F2.wireOp",EDGE,"E1982"),sQuery(id+"F2.wireOp",EDGE,"E1983"),sQuery(id+"F2.wireOp",EDGE,"E1984"),sQuery(id+"F2.wireOp",EDGE,"E1985"),sQuery(id+"F2.wireOp",EDGE,"E1986"),sQuery(id+"F2.wireOp",EDGE,"E1987"),sQuery(id+"F2.wireOp",EDGE,"E1988"),sQuery(id+"F2.wireOp",EDGE,"E1989"),sQuery(id+"F2.wireOp",EDGE,"E1990"),sQuery(id+"F2.wireOp",EDGE,"E1991"),sQuery(id+"F2.wireOp",EDGE,"E1992"),sQuery(id+"F2.wireOp",EDGE,"E1993"),sQuery(id+"F2.wireOp",EDGE,"E1994"),sQuery(id+"F2.wireOp",EDGE,"E1995"),sQuery(id+"F2.wireOp",EDGE,"E1996"),sQuery(id+"F2.wireOp",EDGE,"E1997"),sQuery(id+"F2.wireOp",EDGE,"E1998"),sQuery(id+"F2.wireOp",EDGE,"E1999"),sQuery(id+"F2.wireOp",EDGE,"E2000"),sQuery(id+"F2.wireOp",EDGE,"E2001"),sQuery(id+"F2.wireOp",EDGE,"E2002"),sQuery(id+"F2.wireOp",EDGE,"E2003"),sQuery(id+"F2.wireOp",EDGE,"E2004"),sQuery(id+"F2.wireOp",EDGE,"E2005"),sQuery(id+"F2.wireOp",EDGE,"E2006"),sQuery(id+"F2.wireOp",EDGE,"E2007"),sQuery(id+"F2.wireOp",EDGE,"E2008"),sQuery(id+"F2.wireOp",EDGE,"E2009"),sQuery(id+"F2.wireOp",EDGE,"E2010"),sQuery(id+"F2.wireOp",EDGE,"E2011"),sQuery(id+"F2.wireOp",EDGE,"E2012"),sQuery(id+"F2.wireOp",EDGE,"E2013"),sQuery(id+"F2.wireOp",EDGE,"E2014"),sQuery(id+"F2.wireOp",EDGE,"E2015"),sQuery(id+"F2.wireOp",EDGE,"E2016"),sQuery(id+"F2.wireOp",EDGE,"E2017"),sQuery(id+"F2.wireOp",EDGE,"E2018"),sQuery(id+"F2.wireOp",EDGE,"E2019"),sQuery(id+"F2.wireOp",EDGE,"E2020"),sQuery(id+"F2.wireOp",EDGE,"E2021"),sQuery(id+"F2.wireOp",EDGE,"E2022"),subQ0,sQuery(id+"F2.wireOp",EDGE,"E2025"),sQuery(id+"F2.wireOp",EDGE,"E2026")])],"isStart":false}),makeQuery(id+"F3.opExtrude","CAP_FACE",FACE,{"disambiguationData":[OSD([sQuery(id+"F2.wireOp",EDGE,"E1146"),sQuery(id+"F2.wireOp",EDGE,"E1147"),sQuery(id+"F2.wireOp",EDGE,"E1148"),sQuery(id+"F2.wireOp",EDGE,"E1149"),sQuery(id+"F2.wireOp",EDGE,"E1150"),sQuery(id+"F2.wireOp",EDGE,"E1151"),sQuery(id+"F2.wireOp",EDGE,"E1152"),sQuery(id+"F2.wireOp",EDGE,"E1153"),sQuery(id+"F2.wireOp",EDGE,"E1154"),sQuery(id+"F2.wireOp",EDGE,"E1155"),sQuery(id+"F2.wireOp",EDGE,"E1156"),sQuery(id+"F2.wireOp",EDGE,"E1157"),sQuery(id+"F2.wireOp",EDGE,"E1158"),sQuery(id+"F2.wireOp",EDGE,"E1159"),sQuery(id+"F2.wireOp",EDGE,"E1160"),sQuery(id+"F2.wireOp",EDGE,"E1161"),sQuery(id+"F2.wireOp",EDGE,"E1162"),sQuery(id+"F2.wireOp",EDGE,"E1163"),sQuery(id+"F2.wireOp",EDGE,"E1164"),sQuery(id+"F2.wireOp",EDGE,"E1165"),sQuery(id+"F2.wireOp",EDGE,"E1166"),sQuery(id+"F2.wireOp",EDGE,"E1167"),sQuery(id+"F2.wireOp",EDGE,"E1168"),sQuery(id+"F2.wireOp",EDGE,"E1169"),sQuery(id+"F2.wireOp",EDGE,"E1170"),sQuery(id+"F2.wireOp",EDGE,"E1171"),sQuery(id+"F2.wireOp",EDGE,"E1172"),sQuery(id+"F2.wireOp",EDGE,"E1173"),sQuery(id+"F2.wireOp",EDGE,"E1174"),sQuery(id+"F2.wireOp",EDGE,"E1175"),sQuery(id+"F2.wireOp",EDGE,"E1176"),sQuery(id+"F2.wireOp",EDGE,"E1177"),sQuery(id+"F2.wireOp",EDGE,"E1178"),sQuery(id+"F2.wireOp",EDGE,"E1179"),sQuery(id+"F2.wireOp",EDGE,"E1180"),sQuery(id+"F2.wireOp",EDGE,"E1181"),sQuery(id+"F2.wireOp",EDGE,"E1182"),sQuery(id+"F2.wireOp",EDGE,"E1183"),sQuery(id+"F2.wireOp",EDGE,"E1184"),sQuery(id+"F2.wireOp",EDGE,"E1185"),sQuery(id+"F2.wireOp",EDGE,"E1186"),sQuery(id+"F2.wireOp",EDGE,"E1187"),sQuery(id+"F2.wireOp",EDGE,"E1188"),sQuery(id+"F2.wireOp",EDGE,"E1189"),sQuery(id+"F2.wireOp",EDGE,"E1190"),sQuery(id+"F2.wireOp",EDGE,"E1191"),sQuery(id+"F2.wireOp",EDGE,"E1192"),sQuery(id+"F2.wireOp",EDGE,"E1193"),sQuery(id+"F2.wireOp",EDGE,"E1194"),sQuery(id+"F2.wireOp",EDGE,"E1195"),sQuery(id+"F2.wireOp",EDGE,"E1196"),sQuery(id+"F2.wireOp",EDGE,"E1197"),sQuery(id+"F2.wireOp",EDGE,"E1198"),sQuery(id+"F2.wireOp",EDGE,"E1199"),sQuery(id+"F2.wireOp",EDGE,"E1200"),sQuery(id+"F2.wireOp",EDGE,"E1201"),sQuery(id+"F2.wireOp",EDGE,"E1202"),sQuery(id+"F2.wireOp",EDGE,"E1203"),sQuery(id+"F2.wireOp",EDGE,"E1204"),sQuery(id+"F2.wireOp",EDGE,"E1205"),sQuery(id+"F2.wireOp",EDGE,"E1206"),sQuery(id+"F2.wireOp",EDGE,"E1207"),sQuery(id+"F2.wireOp",EDGE,"E1208"),sQuery(id+"F2.wireOp",EDGE,"E1209"),sQuery(id+"F2.wireOp",EDGE,"E1210"),sQuery(id+"F2.wireOp",EDGE,"E1211"),sQuery(id+"F2.wireOp",EDGE,"E1212"),sQuery(id+"F2.wireOp",EDGE,"E1213"),sQuery(id+"F2.wireOp",EDGE,"E1214"),sQuery(id+"F2.wireOp",EDGE,"E1215"),sQuery(id+"F2.wireOp",EDGE,"E1216"),sQuery(id+"F2.wireOp",EDGE,"E1217"),sQuery(id+"F2.wireOp",EDGE,"E1218"),sQuery(id+"F2.wireOp",EDGE,"E1219"),sQuery(id+"F2.wireOp",EDGE,"E1220"),sQuery(id+"F2.wireOp",EDGE,"E1221"),sQuery(id+"F2.wireOp",EDGE,"E1222"),sQuery(id+"F2.wireOp",EDGE,"E1223"),sQuery(id+"F2.wireOp",EDGE,"E1224"),sQuery(id+"F2.wireOp",EDGE,"E1225"),sQuery(id+"F2.wireOp",EDGE,"E1226"),sQuery(id+"F2.wireOp",EDGE,"E1227"),sQuery(id+"F2.wireOp",EDGE,"E1228"),sQuery(id+"F2.wireOp",EDGE,"E1229"),sQuery(id+"F2.wireOp",EDGE,"E1230"),sQuery(id+"F2.wireOp",EDGE,"E1231"),sQuery(id+"F2.wireOp",EDGE,"E1232"),sQuery(id+"F2.wireOp",EDGE,"E1233"),sQuery(id+"F2.wireOp",EDGE,"E1234"),sQuery(id+"F2.wireOp",EDGE,"E1235"),sQuery(id+"F2.wireOp",EDGE,"E1236"),sQuery(id+"F2.wireOp",EDGE,"E1237"),sQuery(id+"F2.wireOp",EDGE,"E1238"),sQuery(id+"F2.wireOp",EDGE,"E1239"),sQuery(id+"F2.wireOp",EDGE,"E1240"),sQuery(id+"F2.wireOp",EDGE,"E1241"),sQuery(id+"F2.wireOp",EDGE,"E1242"),sQuery(id+"F2.wireOp",EDGE,"E1243"),sQuery(id+"F2.wireOp",EDGE,"E1244"),sQuery(id+"F2.wireOp",EDGE,"E1245"),sQuery(id+"F2.wireOp",EDGE,"E1246"),sQuery(id+"F2.wireOp",EDGE,"E1247"),sQuery(id+"F2.wireOp",EDGE,"E1248"),sQuery(id+"F2.wireOp",EDGE,"E1249"),sQuery(id+"F2.wireOp",EDGE,"E1250"),sQuery(id+"F2.wireOp",EDGE,"E1251"),sQuery(id+"F2.wireOp",EDGE,"E1252"),sQuery(id+"F2.wireOp",EDGE,"E1253"),sQuery(id+"F2.wireOp",EDGE,"E1254"),sQuery(id+"F2.wireOp",EDGE,"E1255"),sQuery(id+"F2.wireOp",EDGE,"E1256"),sQuery(id+"F2.wireOp",EDGE,"E1257"),sQuery(id+"F2.wireOp",EDGE,"E1258"),sQuery(id+"F2.wireOp",EDGE,"E1259"),sQuery(id+"F2.wireOp",EDGE,"E1260"),sQuery(id+"F2.wireOp",EDGE,"E1261"),sQuery(id+"F2.wireOp",EDGE,"E1262"),sQuery(id+"F2.wireOp",EDGE,"E1263"),sQuery(id+"F2.wireOp",EDGE,"E1264"),sQuery(id+"F2.wireOp",EDGE,"E1265"),sQuery(id+"F2.wireOp",EDGE,"E1266"),sQuery(id+"F2.wireOp",EDGE,"E1267"),sQuery(id+"F2.wireOp",EDGE,"E1268"),sQuery(id+"F2.wireOp",EDGE,"E1269"),sQuery(id+"F2.wireOp",EDGE,"E1270"),sQuery(id+"F2.wireOp",EDGE,"E1271"),sQuery(id+"F2.wireOp",EDGE,"E1272"),sQuery(id+"F2.wireOp",EDGE,"E1273"),sQuery(id+"F2.wireOp",EDGE,"E1274"),sQuery(id+"F2.wireOp",EDGE,"E1275"),sQuery(id+"F2.wireOp",EDGE,"E1276"),sQuery(id+"F2.wireOp",EDGE,"E1277"),sQuery(id+"F2.wireOp",EDGE,"E1278"),sQuery(id+"F2.wireOp",EDGE,"E1279"),sQuery(id+"F2.wireOp",EDGE,"E1280"),sQuery(id+"F2.wireOp",EDGE,"E1281"),sQuery(id+"F2.wireOp",EDGE,"E1282"),sQuery(id+"F2.wireOp",EDGE,"E1283"),sQuery(id+"F2.wireOp",EDGE,"E1284"),sQuery(id+"F2.wireOp",EDGE,"E1285"),sQuery(id+"F2.wireOp",EDGE,"E1286"),sQuery(id+"F2.wireOp",EDGE,"E1287"),sQuery(id+"F2.wireOp",EDGE,"E1288"),sQuery(id+"F2.wireOp",EDGE,"E1289"),sQuery(id+"F2.wireOp",EDGE,"E1290"),sQuery(id+"F2.wireOp",EDGE,"E1291"),sQuery(id+"F2.wireOp",EDGE,"E1292"),sQuery(id+"F2.wireOp",EDGE,"E1293"),sQuery(id+"F2.wireOp",EDGE,"E1294"),sQuery(id+"F2.wireOp",EDGE,"E1295"),sQuery(id+"F2.wireOp",EDGE,"E1296"),sQuery(id+"F2.wireOp",EDGE,"E1297"),sQuery(id+"F2.wireOp",EDGE,"E1298"),sQuery(id+"F2.wireOp",EDGE,"E1299"),sQuery(id+"F2.wireOp",EDGE,"E1300"),sQuery(id+"F2.wireOp",EDGE,"E1301"),sQuery(id+"F2.wireOp",EDGE,"E1302"),sQuery(id+"F2.wireOp",EDGE,"E1303"),sQuery(id+"F2.wireOp",EDGE,"E1304"),sQuery(id+"F2.wireOp",EDGE,"E1305"),sQuery(id+"F2.wireOp",EDGE,"E1306"),sQuery(id+"F2.wireOp",EDGE,"E1460"),sQuery(id+"F2.wireOp",EDGE,"E1461"),sQuery(id+"F2.wireOp",EDGE,"E1462"),sQuery(id+"F2.wireOp",EDGE,"E1463"),sQuery(id+"F2.wireOp",EDGE,"E1464"),sQuery(id+"F2.wireOp",EDGE,"E1465"),sQuery(id+"F2.wireOp",EDGE,"E1466"),sQuery(id+"F2.wireOp",EDGE,"E1467"),sQuery(id+"F2.wireOp",EDGE,"E1468"),sQuery(id+"F2.wireOp",EDGE,"E1469"),sQuery(id+"F2.wireOp",EDGE,"E1470"),sQuery(id+"F2.wireOp",EDGE,"E1471"),sQuery(id+"F2.wireOp",EDGE,"E1472"),sQuery(id+"F2.wireOp",EDGE,"E1473"),sQuery(id+"F2.wireOp",EDGE,"E1474"),sQuery(id+"F2.wireOp",EDGE,"E1475"),sQuery(id+"F2.wireOp",EDGE,"E1476"),sQuery(id+"F2.wireOp",EDGE,"E1477"),sQuery(id+"F2.wireOp",EDGE,"E1478"),sQuery(id+"F2.wireOp",EDGE,"E1479"),sQuery(id+"F2.wireOp",EDGE,"E1480"),sQuery(id+"F2.wireOp",EDGE,"E1481"),sQuery(id+"F2.wireOp",EDGE,"E1482"),sQuery(id+"F2.wireOp",EDGE,"E1483"),sQuery(id+"F2.wireOp",EDGE,"E1484"),sQuery(id+"F2.wireOp",EDGE,"E1485"),sQuery(id+"F2.wireOp",EDGE,"E1486"),sQuery(id+"F2.wireOp",EDGE,"E1487"),sQuery(id+"F2.wireOp",EDGE,"E1488"),sQuery(id+"F2.wireOp",EDGE,"E1489"),sQuery(id+"F2.wireOp",EDGE,"E1490"),sQuery(id+"F2.wireOp",EDGE,"E1491"),sQuery(id+"F2.wireOp",EDGE,"E1492"),sQuery(id+"F2.wireOp",EDGE,"E1493"),sQuery(id+"F2.wireOp",EDGE,"E1494"),sQuery(id+"F2.wireOp",EDGE,"E1495"),sQuery(id+"F2.wireOp",EDGE,"E1496"),sQuery(id+"F2.wireOp",EDGE,"E1497"),sQuery(id+"F2.wireOp",EDGE,"E1498"),sQuery(id+"F2.wireOp",EDGE,"E1499"),sQuery(id+"F2.wireOp",EDGE,"E1500"),sQuery(id+"F2.wireOp",EDGE,"E1501"),sQuery(id+"F2.wireOp",EDGE,"E1502"),sQuery(id+"F2.wireOp",EDGE,"E1503"),sQuery(id+"F2.wireOp",EDGE,"E1504"),sQuery(id+"F2.wireOp",EDGE,"E1505"),sQuery(id+"F2.wireOp",EDGE,"E1506"),sQuery(id+"F2.wireOp",EDGE,"E1507"),sQuery(id+"F2.wireOp",EDGE,"E1508"),sQuery(id+"F2.wireOp",EDGE,"E1509"),sQuery(id+"F2.wireOp",EDGE,"E1510"),sQuery(id+"F2.wireOp",EDGE,"E1511"),sQuery(id+"F2.wireOp",EDGE,"E1512"),sQuery(id+"F2.wireOp",EDGE,"E1513"),sQuery(id+"F2.wireOp",EDGE,"E1514"),sQuery(id+"F2.wireOp",EDGE,"E1515"),sQuery(id+"F2.wireOp",EDGE,"E1516"),sQuery(id+"F2.wireOp",EDGE,"E1517"),sQuery(id+"F2.wireOp",EDGE,"E1518"),sQuery(id+"F2.wireOp",EDGE,"E1519"),sQuery(id+"F2.wireOp",EDGE,"E1520"),sQuery(id+"F2.wireOp",EDGE,"E1521"),sQuery(id+"F2.wireOp",EDGE,"E1522"),sQuery(id+"F2.wireOp",EDGE,"E1523"),sQuery(id+"F2.wireOp",EDGE,"E1524"),sQuery(id+"F2.wireOp",EDGE,"E1525"),sQuery(id+"F2.wireOp",EDGE,"E1526"),sQuery(id+"F2.wireOp",EDGE,"E1527"),sQuery(id+"F2.wireOp",EDGE,"E1528"),sQuery(id+"F2.wireOp",EDGE,"E1529"),sQuery(id+"F2.wireOp",EDGE,"E1530"),sQuery(id+"F2.wireOp",EDGE,"E1531"),sQuery(id+"F2.wireOp",EDGE,"E1532"),sQuery(id+"F2.wireOp",EDGE,"E1533"),sQuery(id+"F2.wireOp",EDGE,"E1534"),sQuery(id+"F2.wireOp",EDGE,"E1535"),sQuery(id+"F2.wireOp",EDGE,"E1536"),sQuery(id+"F2.wireOp",EDGE,"E1537"),sQuery(id+"F2.wireOp",EDGE,"E1538"),sQuery(id+"F2.wireOp",EDGE,"E1539"),sQuery(id+"F2.wireOp",EDGE,"E1540"),sQuery(id+"F2.wireOp",EDGE,"E1541"),sQuery(id+"F2.wireOp",EDGE,"E1542"),sQuery(id+"F2.wireOp",EDGE,"E1543"),sQuery(id+"F2.wireOp",EDGE,"E1544"),sQuery(id+"F2.wireOp",EDGE,"E1545"),sQuery(id+"F2.wireOp",EDGE,"E1546"),sQuery(id+"F2.wireOp",EDGE,"E1547"),sQuery(id+"F2.wireOp",EDGE,"E1548"),sQuery(id+"F2.wireOp",EDGE,"E1549"),sQuery(id+"F2.wireOp",EDGE,"E1550"),sQuery(id+"F2.wireOp",EDGE,"E1551"),sQuery(id+"F2.wireOp",EDGE,"E1552"),sQuery(id+"F2.wireOp",EDGE,"E1553"),sQuery(id+"F2.wireOp",EDGE,"E1554"),sQuery(id+"F2.wireOp",EDGE,"E1555"),sQuery(id+"F2.wireOp",EDGE,"E1556"),sQuery(id+"F2.wireOp",EDGE,"E1557"),sQuery(id+"F2.wireOp",EDGE,"E1558"),sQuery(id+"F2.wireOp",EDGE,"E1559"),sQuery(id+"F2.wireOp",EDGE,"E1560"),sQuery(id+"F2.wireOp",EDGE,"E1561"),sQuery(id+"F2.wireOp",EDGE,"E1562"),sQuery(id+"F2.wireOp",EDGE,"E1563"),sQuery(id+"F2.wireOp",EDGE,"E1564"),sQuery(id+"F2.wireOp",EDGE,"E1565"),sQuery(id+"F2.wireOp",EDGE,"E1566"),sQuery(id+"F2.wireOp",EDGE,"E1567"),sQuery(id+"F2.wireOp",EDGE,"E1568"),sQuery(id+"F2.wireOp",EDGE,"E1569"),sQuery(id+"F2.wireOp",EDGE,"E1570"),sQuery(id+"F2.wireOp",EDGE,"E1571"),sQuery(id+"F2.wireOp",EDGE,"E1572"),sQuery(id+"F2.wireOp",EDGE,"E1573"),sQuery(id+"F2.wireOp",EDGE,"E1574"),sQuery(id+"F2.wireOp",EDGE,"E1575"),sQuery(id+"F2.wireOp",EDGE,"E1576"),sQuery(id+"F2.wireOp",EDGE,"E1577"),sQuery(id+"F2.wireOp",EDGE,"E1578"),sQuery(id+"F2.wireOp",EDGE,"E1579"),sQuery(id+"F2.wireOp",EDGE,"E1580"),sQuery(id+"F2.wireOp",EDGE,"E1581"),sQuery(id+"F2.wireOp",EDGE,"E1582"),sQuery(id+"F2.wireOp",EDGE,"E1583"),sQuery(id+"F2.wireOp",EDGE,"E1584"),sQuery(id+"F2.wireOp",EDGE,"E1585"),sQuery(id+"F2.wireOp",EDGE,"E1586"),sQuery(id+"F2.wireOp",EDGE,"E1587"),sQuery(id+"F2.wireOp",EDGE,"E1588"),sQuery(id+"F2.wireOp",EDGE,"E1589"),sQuery(id+"F2.wireOp",EDGE,"E1590"),sQuery(id+"F2.wireOp",EDGE,"E1591"),sQuery(id+"F2.wireOp",EDGE,"E1592"),sQuery(id+"F2.wireOp",EDGE,"E1593"),sQuery(id+"F2.wireOp",EDGE,"E1594"),sQuery(id+"F2.wireOp",EDGE,"E1595"),sQuery(id+"F2.wireOp",EDGE,"E1596"),sQuery(id+"F2.wireOp",EDGE,"E1597"),sQuery(id+"F2.wireOp",EDGE,"E1598"),sQuery(id+"F2.wireOp",EDGE,"E1599"),sQuery(id+"F2.wireOp",EDGE,"E1600"),sQuery(id+"F2.wireOp",EDGE,"E1601"),sQuery(id+"F2.wireOp",EDGE,"E1602"),sQuery(id+"F2.wireOp",EDGE,"E1603"),sQuery(id+"F2.wireOp",EDGE,"E1604"),sQuery(id+"F2.wireOp",EDGE,"E1605"),sQuery(id+"F2.wireOp",EDGE,"E1606"),sQuery(id+"F2.wireOp",EDGE,"E1607"),sQuery(id+"F2.wireOp",EDGE,"E1608"),sQuery(id+"F2.wireOp",EDGE,"E1609"),sQuery(id+"F2.wireOp",EDGE,"E1610"),sQuery(id+"F2.wireOp",EDGE,"E1611"),sQuery(id+"F2.wireOp",EDGE,"E1612"),sQuery(id+"F2.wireOp",EDGE,"E1613"),sQuery(id+"F2.wireOp",EDGE,"E1614"),sQuery(id+"F2.wireOp",EDGE,"E1615"),sQuery(id+"F2.wireOp",EDGE,"E1616"),sQuery(id+"F2.wireOp",EDGE,"E1617"),sQuery(id+"F2.wireOp",EDGE,"E1618"),sQuery(id+"F2.wireOp",EDGE,"E1619"),sQuery(id+"F2.wireOp",EDGE,"E1620"),sQuery(id+"F2.wireOp",EDGE,"E1621"),sQuery(id+"F2.wireOp",EDGE,"E1622"),sQuery(id+"F2.wireOp",EDGE,"E1623"),sQuery(id+"F2.wireOp",EDGE,"E1624"),sQuery(id+"F2.wireOp",EDGE,"E1625"),sQuery(id+"F2.wireOp",EDGE,"E1626"),sQuery(id+"F2.wireOp",EDGE,"E1627"),sQuery(id+"F2.wireOp",EDGE,"E1628"),sQuery(id+"F2.wireOp",EDGE,"E1629"),sQuery(id+"F2.wireOp",EDGE,"E1630"),sQuery(id+"F2.wireOp",EDGE,"E1631"),sQuery(id+"F2.wireOp",EDGE,"E1632"),sQuery(id+"F2.wireOp",EDGE,"E1633"),sQuery(id+"F2.wireOp",EDGE,"E1634"),sQuery(id+"F2.wireOp",EDGE,"E1635"),sQuery(id+"F2.wireOp",EDGE,"E1636"),sQuery(id+"F2.wireOp",EDGE,"E1637"),sQuery(id+"F2.wireOp",EDGE,"E1638"),sQuery(id+"F2.wireOp",EDGE,"E1639"),sQuery(id+"F2.wireOp",EDGE,"E1640"),sQuery(id+"F2.wireOp",EDGE,"E1641"),sQuery(id+"F2.wireOp",EDGE,"E1642"),sQuery(id+"F2.wireOp",EDGE,"E1643"),sQuery(id+"F2.wireOp",EDGE,"E1644"),sQuery(id+"F2.wireOp",EDGE,"E1645"),sQuery(id+"F2.wireOp",EDGE,"E1646"),sQuery(id+"F2.wireOp",EDGE,"E1647"),sQuery(id+"F2.wireOp",EDGE,"E1648"),sQuery(id+"F2.wireOp",EDGE,"E1649"),sQuery(id+"F2.wireOp",EDGE,"E1650"),sQuery(id+"F2.wireOp",EDGE,"E1651"),sQuery(id+"F2.wireOp",EDGE,"E1652"),sQuery(id+"F2.wireOp",EDGE,"E1653"),sQuery(id+"F2.wireOp",EDGE,"E1654"),sQuery(id+"F2.wireOp",EDGE,"E1655"),sQuery(id+"F2.wireOp",EDGE,"E1656"),sQuery(id+"F2.wireOp",EDGE,"E1657"),sQuery(id+"F2.wireOp",EDGE,"E1658"),sQuery(id+"F2.wireOp",EDGE,"E1659"),sQuery(id+"F2.wireOp",EDGE,"E1660"),sQuery(id+"F2.wireOp",EDGE,"E1661"),sQuery(id+"F2.wireOp",EDGE,"E1662"),sQuery(id+"F2.wireOp",EDGE,"E1663"),sQuery(id+"F2.wireOp",EDGE,"E1664"),sQuery(id+"F2.wireOp",EDGE,"E1665"),sQuery(id+"F2.wireOp",EDGE,"E1666"),sQuery(id+"F2.wireOp",EDGE,"E1667"),sQuery(id+"F2.wireOp",EDGE,"E1668"),sQuery(id+"F2.wireOp",EDGE,"E1669"),sQuery(id+"F2.wireOp",EDGE,"E1670"),sQuery(id+"F2.wireOp",EDGE,"E1671"),sQuery(id+"F2.wireOp",EDGE,"E1672"),sQuery(id+"F2.wireOp",EDGE,"E1673"),sQuery(id+"F2.wireOp",EDGE,"E1674"),sQuery(id+"F2.wireOp",EDGE,"E1675"),sQuery(id+"F2.wireOp",EDGE,"E1676"),sQuery(id+"F2.wireOp",EDGE,"E1677"),sQuery(id+"F2.wireOp",EDGE,"E1678"),sQuery(id+"F2.wireOp",EDGE,"E1679"),sQuery(id+"F2.wireOp",EDGE,"E1680"),sQuery(id+"F2.wireOp",EDGE,"E1681"),sQuery(id+"F2.wireOp",EDGE,"E1682"),sQuery(id+"F2.wireOp",EDGE,"E1683"),sQuery(id+"F2.wireOp",EDGE,"E1684"),sQuery(id+"F2.wireOp",EDGE,"E1685"),sQuery(id+"F2.wireOp",EDGE,"E1686"),sQuery(id+"F2.wireOp",EDGE,"E1687"),sQuery(id+"F2.wireOp",EDGE,"E1688"),sQuery(id+"F2.wireOp",EDGE,"E1689"),sQuery(id+"F2.wireOp",EDGE,"E1690"),sQuery(id+"F2.wireOp",EDGE,"E1691"),sQuery(id+"F2.wireOp",EDGE,"E1692"),sQuery(id+"F2.wireOp",EDGE,"E1693"),sQuery(id+"F2.wireOp",EDGE,"E1694"),sQuery(id+"F2.wireOp",EDGE,"E1695"),sQuery(id+"F2.wireOp",EDGE,"E1696"),sQuery(id+"F2.wireOp",EDGE,"E1697"),sQuery(id+"F2.wireOp",EDGE,"E1698"),sQuery(id+"F2.wireOp",EDGE,"E1699"),sQuery(id+"F2.wireOp",EDGE,"E1700"),sQuery(id+"F2.wireOp",EDGE,"E1701"),sQuery(id+"F2.wireOp",EDGE,"E1702"),sQuery(id+"F2.wireOp",EDGE,"E1703"),sQuery(id+"F2.wireOp",EDGE,"E1704"),sQuery(id+"F2.wireOp",EDGE,"E1705"),sQuery(id+"F2.wireOp",EDGE,"E1706"),sQuery(id+"F2.wireOp",EDGE,"E1707"),sQuery(id+"F2.wireOp",EDGE,"E1708"),sQuery(id+"F2.wireOp",EDGE,"E1709"),sQuery(id+"F2.wireOp",EDGE,"E1710"),sQuery(id+"F2.wireOp",EDGE,"E1711"),sQuery(id+"F2.wireOp",EDGE,"E1712"),sQuery(id+"F2.wireOp",EDGE,"E1713"),sQuery(id+"F2.wireOp",EDGE,"E1714"),sQuery(id+"F2.wireOp",EDGE,"E1715"),sQuery(id+"F2.wireOp",EDGE,"E1716"),sQuery(id+"F2.wireOp",EDGE,"E1717"),sQuery(id+"F2.wireOp",EDGE,"E1718"),sQuery(id+"F2.wireOp",EDGE,"E1719"),sQuery(id+"F2.wireOp",EDGE,"E1720"),sQuery(id+"F2.wireOp",EDGE,"E1721"),sQuery(id+"F2.wireOp",EDGE,"E1722"),sQuery(id+"F2.wireOp",EDGE,"E1723"),sQuery(id+"F2.wireOp",EDGE,"E1724"),sQuery(id+"F2.wireOp",EDGE,"E1725"),sQuery(id+"F2.wireOp",EDGE,"E1726"),sQuery(id+"F2.wireOp",EDGE,"E1727"),sQuery(id+"F2.wireOp",EDGE,"E1728"),sQuery(id+"F2.wireOp",EDGE,"E1729"),sQuery(id+"F2.wireOp",EDGE,"E1730"),sQuery(id+"F2.wireOp",EDGE,"E1731"),sQuery(id+"F2.wireOp",EDGE,"E1732"),sQuery(id+"F2.wireOp",EDGE,"E1733"),sQuery(id+"F2.wireOp",EDGE,"E1734"),sQuery(id+"F2.wireOp",EDGE,"E1735"),sQuery(id+"F2.wireOp",EDGE,"E1736"),sQuery(id+"F2.wireOp",EDGE,"E1737"),sQuery(id+"F2.wireOp",EDGE,"E1738"),sQuery(id+"F2.wireOp",EDGE,"E1739"),sQuery(id+"F2.wireOp",EDGE,"E1740"),sQuery(id+"F2.wireOp",EDGE,"E1741"),subQ1])],"isStart":false}),makeQuery(id+"F9.opExtrude","CAP_FACE",FACE,{"disambiguationData":[OSD([sQuery(id+"F8.wireOp",EDGE,"E2031.0"),sQuery(id+"F8.wireOp",EDGE,"E2032.0"),sQuery(id+"F8.wireOp",EDGE,"E2033.0"),sQuery(id+"F8.wireOp",EDGE,"E2034.0"),sQuery(id+"F8.wireOp",EDGE,"E2035.0"),sQuery(id+"F8.wireOp",EDGE,"E2036")])],"isStart":false})]}),makeQuery(id+"F10.opSweep","SWEPT_FACE",FACE,{"disambiguationData":[OSD([sQuery(id+"F0.wireOp",EDGE,"E254"),subQ1])]})]}),makeQuery(id+"F12.opSweep","SWEPT_FACE",FACE,{"disambiguationData":[OSD([subQ0,sQuery(id+"F11.wireOp",EDGE,"E2037.0")])]})]});}
            extrude(context, id + "F16", {"entities" : qUnion([Q0]), "operationType" : NewBodyOperationType.ADD, "endBound" : BoundingType.UP_TO_SURFACE, "depth" : 25 * mm, "endBoundEntityFace" : qUnion([Q1]), "offsetDistance" : 25 * mm});
        }
        {
            var Q0;
            Q0=makeQuery(id+"F1.opExtrude","SWEPT_BODY",BODY,{"disambiguationData":[OSD([sQuery(id+"F0.wireOp",EDGE,"E0"),sQuery(id+"F0.wireOp",EDGE,"E1"),sQuery(id+"F0.wireOp",EDGE,"E2"),sQuery(id+"F0.wireOp",EDGE,"E3"),sQuery(id+"F0.wireOp",EDGE,"E4"),sQuery(id+"F0.wireOp",EDGE,"E5"),sQuery(id+"F0.wireOp",EDGE,"E6"),sQuery(id+"F0.wireOp",EDGE,"E7"),sQuery(id+"F0.wireOp",EDGE,"E8"),sQuery(id+"F0.wireOp",EDGE,"E9"),sQuery(id+"F0.wireOp",EDGE,"E10"),sQuery(id+"F0.wireOp",EDGE,"E11"),sQuery(id+"F0.wireOp",EDGE,"E12"),sQuery(id+"F0.wireOp",EDGE,"E13"),sQuery(id+"F0.wireOp",EDGE,"E14"),sQuery(id+"F0.wireOp",EDGE,"E15"),sQuery(id+"F0.wireOp",EDGE,"E16"),sQuery(id+"F0.wireOp",EDGE,"E17"),sQuery(id+"F0.wireOp",EDGE,"E18"),sQuery(id+"F0.wireOp",EDGE,"E19"),sQuery(id+"F0.wireOp",EDGE,"E20"),sQuery(id+"F0.wireOp",EDGE,"E21"),sQuery(id+"F0.wireOp",EDGE,"E22"),sQuery(id+"F0.wireOp",EDGE,"E23"),sQuery(id+"F0.wireOp",EDGE,"E24"),sQuery(id+"F0.wireOp",EDGE,"E25"),sQuery(id+"F0.wireOp",EDGE,"E26"),sQuery(id+"F0.wireOp",EDGE,"E27"),sQuery(id+"F0.wireOp",EDGE,"E28"),sQuery(id+"F0.wireOp",EDGE,"E29"),sQuery(id+"F0.wireOp",EDGE,"E30"),sQuery(id+"F0.wireOp",EDGE,"E31"),sQuery(id+"F0.wireOp",EDGE,"E32"),sQuery(id+"F0.wireOp",EDGE,"E33"),sQuery(id+"F0.wireOp",EDGE,"E34"),sQuery(id+"F0.wireOp",EDGE,"E35"),sQuery(id+"F0.wireOp",EDGE,"E36"),sQuery(id+"F0.wireOp",EDGE,"E37"),sQuery(id+"F0.wireOp",EDGE,"E38"),sQuery(id+"F0.wireOp",EDGE,"E39"),sQuery(id+"F0.wireOp",EDGE,"E40"),sQuery(id+"F0.wireOp",EDGE,"E41"),sQuery(id+"F0.wireOp",EDGE,"E42"),sQuery(id+"F0.wireOp",EDGE,"E43"),sQuery(id+"F0.wireOp",EDGE,"E44"),sQuery(id+"F0.wireOp",EDGE,"E45"),sQuery(id+"F0.wireOp",EDGE,"E46"),sQuery(id+"F0.wireOp",EDGE,"E47"),sQuery(id+"F0.wireOp",EDGE,"E48"),sQuery(id+"F0.wireOp",EDGE,"E49"),sQuery(id+"F0.wireOp",EDGE,"E50"),sQuery(id+"F0.wireOp",EDGE,"E51"),sQuery(id+"F0.wireOp",EDGE,"E52"),sQuery(id+"F0.wireOp",EDGE,"E53"),sQuery(id+"F0.wireOp",EDGE,"E54"),sQuery(id+"F0.wireOp",EDGE,"E55"),sQuery(id+"F0.wireOp",EDGE,"E56"),sQuery(id+"F0.wireOp",EDGE,"E57"),sQuery(id+"F0.wireOp",EDGE,"E58"),sQuery(id+"F0.wireOp",EDGE,"E59"),sQuery(id+"F0.wireOp",EDGE,"E60"),sQuery(id+"F0.wireOp",EDGE,"E61"),sQuery(id+"F0.wireOp",EDGE,"E62"),sQuery(id+"F0.wireOp",EDGE,"E63"),sQuery(id+"F0.wireOp",EDGE,"E64"),sQuery(id+"F0.wireOp",EDGE,"E65"),sQuery(id+"F0.wireOp",EDGE,"E66"),sQuery(id+"F0.wireOp",EDGE,"E67"),sQuery(id+"F0.wireOp",EDGE,"E68"),sQuery(id+"F0.wireOp",EDGE,"E69"),sQuery(id+"F0.wireOp",EDGE,"E70"),sQuery(id+"F0.wireOp",EDGE,"E71"),sQuery(id+"F0.wireOp",EDGE,"E72"),sQuery(id+"F0.wireOp",EDGE,"E73"),sQuery(id+"F0.wireOp",EDGE,"E74"),sQuery(id+"F0.wireOp",EDGE,"E75"),sQuery(id+"F0.wireOp",EDGE,"E76"),sQuery(id+"F0.wireOp",EDGE,"E77"),sQuery(id+"F0.wireOp",EDGE,"E78"),sQuery(id+"F0.wireOp",EDGE,"E79"),sQuery(id+"F0.wireOp",EDGE,"E80"),sQuery(id+"F0.wireOp",EDGE,"E81"),sQuery(id+"F0.wireOp",EDGE,"E82"),sQuery(id+"F0.wireOp",EDGE,"E83"),sQuery(id+"F0.wireOp",EDGE,"E84"),sQuery(id+"F0.wireOp",EDGE,"E85"),sQuery(id+"F0.wireOp",EDGE,"E86"),sQuery(id+"F0.wireOp",EDGE,"E87"),sQuery(id+"F0.wireOp",EDGE,"E88"),sQuery(id+"F0.wireOp",EDGE,"E89"),sQuery(id+"F0.wireOp",EDGE,"E90"),sQuery(id+"F0.wireOp",EDGE,"E91"),sQuery(id+"F0.wireOp",EDGE,"E92"),sQuery(id+"F0.wireOp",EDGE,"E93"),sQuery(id+"F0.wireOp",EDGE,"E94"),sQuery(id+"F0.wireOp",EDGE,"E95"),sQuery(id+"F0.wireOp",EDGE,"E96"),sQuery(id+"F0.wireOp",EDGE,"E97"),sQuery(id+"F0.wireOp",EDGE,"E98"),sQuery(id+"F0.wireOp",EDGE,"E99"),sQuery(id+"F0.wireOp",EDGE,"E100"),sQuery(id+"F0.wireOp",EDGE,"E101"),sQuery(id+"F0.wireOp",EDGE,"E102"),sQuery(id+"F0.wireOp",EDGE,"E103"),sQuery(id+"F0.wireOp",EDGE,"E104"),sQuery(id+"F0.wireOp",EDGE,"E105"),sQuery(id+"F0.wireOp",EDGE,"E106"),sQuery(id+"F0.wireOp",EDGE,"E107"),sQuery(id+"F0.wireOp",EDGE,"E108"),sQuery(id+"F0.wireOp",EDGE,"E109"),sQuery(id+"F0.wireOp",EDGE,"E110"),sQuery(id+"F0.wireOp",EDGE,"E111"),sQuery(id+"F0.wireOp",EDGE,"E112"),sQuery(id+"F0.wireOp",EDGE,"E113"),sQuery(id+"F0.wireOp",EDGE,"E114"),sQuery(id+"F0.wireOp",EDGE,"E115"),sQuery(id+"F0.wireOp",EDGE,"E116"),sQuery(id+"F0.wireOp",EDGE,"E117"),sQuery(id+"F0.wireOp",EDGE,"E118"),sQuery(id+"F0.wireOp",EDGE,"E119"),sQuery(id+"F0.wireOp",EDGE,"E120"),sQuery(id+"F0.wireOp",EDGE,"E121"),sQuery(id+"F0.wireOp",EDGE,"E122"),sQuery(id+"F0.wireOp",EDGE,"E123"),sQuery(id+"F0.wireOp",EDGE,"E124"),sQuery(id+"F0.wireOp",EDGE,"E125"),sQuery(id+"F0.wireOp",EDGE,"E126"),sQuery(id+"F0.wireOp",EDGE,"E127"),sQuery(id+"F0.wireOp",EDGE,"E128"),sQuery(id+"F0.wireOp",EDGE,"E129"),sQuery(id+"F0.wireOp",EDGE,"E130"),sQuery(id+"F0.wireOp",EDGE,"E131"),sQuery(id+"F0.wireOp",EDGE,"E132"),sQuery(id+"F0.wireOp",EDGE,"E133"),sQuery(id+"F0.wireOp",EDGE,"E134"),sQuery(id+"F0.wireOp",EDGE,"E135"),sQuery(id+"F0.wireOp",EDGE,"E136"),sQuery(id+"F0.wireOp",EDGE,"E137"),sQuery(id+"F0.wireOp",EDGE,"E138"),sQuery(id+"F0.wireOp",EDGE,"E139"),sQuery(id+"F0.wireOp",EDGE,"E140"),sQuery(id+"F0.wireOp",EDGE,"E141"),sQuery(id+"F0.wireOp",EDGE,"E142"),sQuery(id+"F0.wireOp",EDGE,"E143"),sQuery(id+"F0.wireOp",EDGE,"E144"),sQuery(id+"F0.wireOp",EDGE,"E145"),sQuery(id+"F0.wireOp",EDGE,"E146"),sQuery(id+"F0.wireOp",EDGE,"E147"),sQuery(id+"F0.wireOp",EDGE,"E148"),sQuery(id+"F0.wireOp",EDGE,"E149"),sQuery(id+"F0.wireOp",EDGE,"E150"),sQuery(id+"F0.wireOp",EDGE,"E151"),sQuery(id+"F0.wireOp",EDGE,"E152"),sQuery(id+"F0.wireOp",EDGE,"E153"),sQuery(id+"F0.wireOp",EDGE,"E154"),sQuery(id+"F0.wireOp",EDGE,"E155"),sQuery(id+"F0.wireOp",EDGE,"E156"),sQuery(id+"F0.wireOp",EDGE,"E157"),sQuery(id+"F0.wireOp",EDGE,"E158"),sQuery(id+"F0.wireOp",EDGE,"E159"),sQuery(id+"F0.wireOp",EDGE,"E160"),sQuery(id+"F0.wireOp",EDGE,"E161"),sQuery(id+"F0.wireOp",EDGE,"E162"),sQuery(id+"F0.wireOp",EDGE,"E163"),sQuery(id+"F0.wireOp",EDGE,"E164"),sQuery(id+"F0.wireOp",EDGE,"E165"),sQuery(id+"F0.wireOp",EDGE,"E166"),sQuery(id+"F0.wireOp",EDGE,"E167"),sQuery(id+"F0.wireOp",EDGE,"E168"),sQuery(id+"F0.wireOp",EDGE,"E169"),sQuery(id+"F0.wireOp",EDGE,"E170"),sQuery(id+"F0.wireOp",EDGE,"E171"),sQuery(id+"F0.wireOp",EDGE,"E172"),sQuery(id+"F0.wireOp",EDGE,"E173"),sQuery(id+"F0.wireOp",EDGE,"E174"),sQuery(id+"F0.wireOp",EDGE,"E175"),sQuery(id+"F0.wireOp",EDGE,"E176"),sQuery(id+"F0.wireOp",EDGE,"E177"),sQuery(id+"F0.wireOp",EDGE,"E178"),sQuery(id+"F0.wireOp",EDGE,"E179"),sQuery(id+"F0.wireOp",EDGE,"E180"),sQuery(id+"F0.wireOp",EDGE,"E181"),sQuery(id+"F0.wireOp",EDGE,"E182"),sQuery(id+"F0.wireOp",EDGE,"E183"),sQuery(id+"F0.wireOp",EDGE,"E184"),sQuery(id+"F0.wireOp",EDGE,"E185"),sQuery(id+"F0.wireOp",EDGE,"E186"),sQuery(id+"F0.wireOp",EDGE,"E187"),sQuery(id+"F0.wireOp",EDGE,"E188"),sQuery(id+"F0.wireOp",EDGE,"E189"),sQuery(id+"F0.wireOp",EDGE,"E190"),sQuery(id+"F0.wireOp",EDGE,"E191"),sQuery(id+"F0.wireOp",EDGE,"E192"),sQuery(id+"F0.wireOp",EDGE,"E193"),sQuery(id+"F0.wireOp",EDGE,"E194"),sQuery(id+"F0.wireOp",EDGE,"E195"),sQuery(id+"F0.wireOp",EDGE,"E196"),sQuery(id+"F0.wireOp",EDGE,"E197"),sQuery(id+"F0.wireOp",EDGE,"E198"),sQuery(id+"F0.wireOp",EDGE,"E199"),sQuery(id+"F0.wireOp",EDGE,"E200"),sQuery(id+"F0.wireOp",EDGE,"E201"),sQuery(id+"F0.wireOp",EDGE,"E202"),sQuery(id+"F0.wireOp",EDGE,"E203"),sQuery(id+"F0.wireOp",EDGE,"E204"),sQuery(id+"F0.wireOp",EDGE,"E205"),sQuery(id+"F0.wireOp",EDGE,"E206"),sQuery(id+"F0.wireOp",EDGE,"E207"),sQuery(id+"F0.wireOp",EDGE,"E208"),sQuery(id+"F0.wireOp",EDGE,"E209"),sQuery(id+"F0.wireOp",EDGE,"E210"),sQuery(id+"F0.wireOp",EDGE,"E211"),sQuery(id+"F0.wireOp",EDGE,"E212"),sQuery(id+"F0.wireOp",EDGE,"E213"),sQuery(id+"F0.wireOp",EDGE,"E214"),sQuery(id+"F0.wireOp",EDGE,"E215"),sQuery(id+"F0.wireOp",EDGE,"E216"),sQuery(id+"F0.wireOp",EDGE,"E217"),sQuery(id+"F0.wireOp",EDGE,"E218"),sQuery(id+"F0.wireOp",EDGE,"E219"),sQuery(id+"F0.wireOp",EDGE,"E220"),sQuery(id+"F0.wireOp",EDGE,"E221"),sQuery(id+"F0.wireOp",EDGE,"E222"),sQuery(id+"F0.wireOp",EDGE,"E223"),sQuery(id+"F0.wireOp",EDGE,"E224"),sQuery(id+"F0.wireOp",EDGE,"E225"),sQuery(id+"F0.wireOp",EDGE,"E226"),sQuery(id+"F0.wireOp",EDGE,"E227"),sQuery(id+"F0.wireOp",EDGE,"E228"),sQuery(id+"F0.wireOp",EDGE,"E229"),sQuery(id+"F0.wireOp",EDGE,"E230"),sQuery(id+"F0.wireOp",EDGE,"E231"),sQuery(id+"F0.wireOp",EDGE,"E232"),sQuery(id+"F0.wireOp",EDGE,"E233"),sQuery(id+"F0.wireOp",EDGE,"E234"),sQuery(id+"F0.wireOp",EDGE,"E235"),sQuery(id+"F0.wireOp",EDGE,"E236"),sQuery(id+"F0.wireOp",EDGE,"E237"),sQuery(id+"F0.wireOp",EDGE,"E238"),sQuery(id+"F0.wireOp",EDGE,"E239"),sQuery(id+"F0.wireOp",EDGE,"E240"),sQuery(id+"F0.wireOp",EDGE,"E241"),sQuery(id+"F0.wireOp",EDGE,"E242"),sQuery(id+"F0.wireOp",EDGE,"E243"),sQuery(id+"F0.wireOp",EDGE,"E244"),sQuery(id+"F0.wireOp",EDGE,"E245"),sQuery(id+"F0.wireOp",EDGE,"E246"),sQuery(id+"F0.wireOp",EDGE,"E247"),sQuery(id+"F0.wireOp",EDGE,"E248"),sQuery(id+"F0.wireOp",EDGE,"E249"),sQuery(id+"F0.wireOp",EDGE,"E250"),sQuery(id+"F0.wireOp",EDGE,"E251"),sQuery(id+"F0.wireOp",EDGE,"E252"),sQuery(id+"F0.wireOp",EDGE,"E253"),sQuery(id+"F0.wireOp",EDGE,"E254"),sQuery(id+"F0.wireOp",EDGE,"E255"),sQuery(id+"F0.wireOp",EDGE,"E256"),sQuery(id+"F0.wireOp",EDGE,"E257"),sQuery(id+"F0.wireOp",EDGE,"E258"),sQuery(id+"F0.wireOp",EDGE,"E259"),sQuery(id+"F0.wireOp",EDGE,"E260"),sQuery(id+"F0.wireOp",EDGE,"E261"),sQuery(id+"F0.wireOp",EDGE,"E262"),sQuery(id+"F0.wireOp",EDGE,"E263"),sQuery(id+"F0.wireOp",EDGE,"E264"),sQuery(id+"F0.wireOp",EDGE,"E265"),sQuery(id+"F0.wireOp",EDGE,"E266"),sQuery(id+"F0.wireOp",EDGE,"E267"),sQuery(id+"F0.wireOp",EDGE,"E268"),sQuery(id+"F0.wireOp",EDGE,"E269"),sQuery(id+"F0.wireOp",EDGE,"E270"),sQuery(id+"F0.wireOp",EDGE,"E271"),sQuery(id+"F0.wireOp",EDGE,"E272"),sQuery(id+"F0.wireOp",EDGE,"E273"),sQuery(id+"F0.wireOp",EDGE,"E274"),sQuery(id+"F0.wireOp",EDGE,"E275"),sQuery(id+"F0.wireOp",EDGE,"E276"),sQuery(id+"F0.wireOp",EDGE,"E277"),sQuery(id+"F0.wireOp",EDGE,"E278"),sQuery(id+"F0.wireOp",EDGE,"E279"),sQuery(id+"F0.wireOp",EDGE,"E280"),sQuery(id+"F0.wireOp",EDGE,"E281"),sQuery(id+"F0.wireOp",EDGE,"E282"),sQuery(id+"F0.wireOp",EDGE,"E283"),sQuery(id+"F0.wireOp",EDGE,"E284"),sQuery(id+"F0.wireOp",EDGE,"E285"),sQuery(id+"F0.wireOp",EDGE,"E286"),sQuery(id+"F0.wireOp",EDGE,"E287"),sQuery(id+"F0.wireOp",EDGE,"E288"),sQuery(id+"F0.wireOp",EDGE,"E289"),sQuery(id+"F0.wireOp",EDGE,"E290"),sQuery(id+"F0.wireOp",EDGE,"E291"),sQuery(id+"F0.wireOp",EDGE,"E292"),sQuery(id+"F0.wireOp",EDGE,"E293"),sQuery(id+"F0.wireOp",EDGE,"E294"),sQuery(id+"F0.wireOp",EDGE,"E295"),sQuery(id+"F0.wireOp",EDGE,"E296"),sQuery(id+"F0.wireOp",EDGE,"E297"),sQuery(id+"F0.wireOp",EDGE,"E298"),sQuery(id+"F0.wireOp",EDGE,"E299"),sQuery(id+"F0.wireOp",EDGE,"E300"),sQuery(id+"F0.wireOp",EDGE,"E301"),sQuery(id+"F0.wireOp",EDGE,"E302"),sQuery(id+"F0.wireOp",EDGE,"E303"),sQuery(id+"F0.wireOp",EDGE,"E304"),sQuery(id+"F0.wireOp",EDGE,"E305"),sQuery(id+"F0.wireOp",EDGE,"E306"),sQuery(id+"F0.wireOp",EDGE,"E307"),sQuery(id+"F0.wireOp",EDGE,"E308"),sQuery(id+"F0.wireOp",EDGE,"E309"),sQuery(id+"F0.wireOp",EDGE,"E310"),sQuery(id+"F0.wireOp",EDGE,"E311"),sQuery(id+"F0.wireOp",EDGE,"E312"),sQuery(id+"F0.wireOp",EDGE,"E313"),sQuery(id+"F0.wireOp",EDGE,"E314"),sQuery(id+"F0.wireOp",EDGE,"E315"),sQuery(id+"F0.wireOp",EDGE,"E316"),sQuery(id+"F0.wireOp",EDGE,"E317"),sQuery(id+"F0.wireOp",EDGE,"E318"),sQuery(id+"F0.wireOp",EDGE,"E319"),sQuery(id+"F0.wireOp",EDGE,"E320"),sQuery(id+"F0.wireOp",EDGE,"E321"),sQuery(id+"F0.wireOp",EDGE,"E322"),sQuery(id+"F0.wireOp",EDGE,"E323"),sQuery(id+"F0.wireOp",EDGE,"E324"),sQuery(id+"F0.wireOp",EDGE,"E325"),sQuery(id+"F0.wireOp",EDGE,"E326"),sQuery(id+"F0.wireOp",EDGE,"E327"),sQuery(id+"F0.wireOp",EDGE,"E328"),sQuery(id+"F0.wireOp",EDGE,"E329"),sQuery(id+"F0.wireOp",EDGE,"E330"),sQuery(id+"F0.wireOp",EDGE,"E331"),sQuery(id+"F0.wireOp",EDGE,"E332"),sQuery(id+"F0.wireOp",EDGE,"E333"),sQuery(id+"F0.wireOp",EDGE,"E334"),sQuery(id+"F0.wireOp",EDGE,"E335"),sQuery(id+"F0.wireOp",EDGE,"E336"),sQuery(id+"F0.wireOp",EDGE,"E337"),sQuery(id+"F0.wireOp",EDGE,"E338"),sQuery(id+"F0.wireOp",EDGE,"E339"),sQuery(id+"F0.wireOp",EDGE,"E340"),sQuery(id+"F0.wireOp",EDGE,"E341"),sQuery(id+"F0.wireOp",EDGE,"E342"),sQuery(id+"F0.wireOp",EDGE,"E343"),sQuery(id+"F0.wireOp",EDGE,"E344"),sQuery(id+"F0.wireOp",EDGE,"E345"),sQuery(id+"F0.wireOp",EDGE,"E346"),sQuery(id+"F0.wireOp",EDGE,"E347"),sQuery(id+"F0.wireOp",EDGE,"E348"),sQuery(id+"F0.wireOp",EDGE,"E349"),sQuery(id+"F0.wireOp",EDGE,"E350"),sQuery(id+"F0.wireOp",EDGE,"E351"),sQuery(id+"F0.wireOp",EDGE,"E352"),sQuery(id+"F0.wireOp",EDGE,"E353"),sQuery(id+"F0.wireOp",EDGE,"E354"),sQuery(id+"F0.wireOp",EDGE,"E355"),sQuery(id+"F0.wireOp",EDGE,"E356"),sQuery(id+"F0.wireOp",EDGE,"E357"),sQuery(id+"F0.wireOp",EDGE,"E358"),sQuery(id+"F0.wireOp",EDGE,"E359"),sQuery(id+"F0.wireOp",EDGE,"E360"),sQuery(id+"F0.wireOp",EDGE,"E361"),sQuery(id+"F0.wireOp",EDGE,"E362"),sQuery(id+"F0.wireOp",EDGE,"E363"),sQuery(id+"F0.wireOp",EDGE,"E364"),sQuery(id+"F0.wireOp",EDGE,"E365"),sQuery(id+"F0.wireOp",EDGE,"E366"),sQuery(id+"F0.wireOp",EDGE,"E367"),sQuery(id+"F0.wireOp",EDGE,"E368"),sQuery(id+"F0.wireOp",EDGE,"E369"),sQuery(id+"F0.wireOp",EDGE,"E370"),sQuery(id+"F0.wireOp",EDGE,"E371"),sQuery(id+"F0.wireOp",EDGE,"E372"),sQuery(id+"F0.wireOp",EDGE,"E373"),sQuery(id+"F0.wireOp",EDGE,"E374"),sQuery(id+"F0.wireOp",EDGE,"E375"),sQuery(id+"F0.wireOp",EDGE,"E376"),sQuery(id+"F0.wireOp",EDGE,"E377"),sQuery(id+"F0.wireOp",EDGE,"E378"),sQuery(id+"F0.wireOp",EDGE,"E379"),sQuery(id+"F0.wireOp",EDGE,"E380"),sQuery(id+"F0.wireOp",EDGE,"E381"),sQuery(id+"F0.wireOp",EDGE,"E382"),sQuery(id+"F0.wireOp",EDGE,"E383"),sQuery(id+"F0.wireOp",EDGE,"E384"),sQuery(id+"F0.wireOp",EDGE,"E385"),sQuery(id+"F0.wireOp",EDGE,"E386"),sQuery(id+"F0.wireOp",EDGE,"E387"),sQuery(id+"F0.wireOp",EDGE,"E388"),sQuery(id+"F0.wireOp",EDGE,"E389"),sQuery(id+"F0.wireOp",EDGE,"E390"),sQuery(id+"F0.wireOp",EDGE,"E391"),sQuery(id+"F0.wireOp",EDGE,"E392"),sQuery(id+"F0.wireOp",EDGE,"E393"),sQuery(id+"F0.wireOp",EDGE,"E394"),sQuery(id+"F0.wireOp",EDGE,"E395"),sQuery(id+"F0.wireOp",EDGE,"E396"),sQuery(id+"F0.wireOp",EDGE,"E397"),sQuery(id+"F0.wireOp",EDGE,"E398"),sQuery(id+"F0.wireOp",EDGE,"E399"),sQuery(id+"F0.wireOp",EDGE,"E400"),sQuery(id+"F0.wireOp",EDGE,"E401"),sQuery(id+"F0.wireOp",EDGE,"E402"),sQuery(id+"F0.wireOp",EDGE,"E403"),sQuery(id+"F0.wireOp",EDGE,"E404"),sQuery(id+"F0.wireOp",EDGE,"E405"),sQuery(id+"F0.wireOp",EDGE,"E406"),sQuery(id+"F0.wireOp",EDGE,"E407"),sQuery(id+"F0.wireOp",EDGE,"E408"),sQuery(id+"F0.wireOp",EDGE,"E409"),sQuery(id+"F0.wireOp",EDGE,"E410"),sQuery(id+"F0.wireOp",EDGE,"E411"),sQuery(id+"F0.wireOp",EDGE,"E412"),sQuery(id+"F0.wireOp",EDGE,"E413"),sQuery(id+"F0.wireOp",EDGE,"E414"),sQuery(id+"F0.wireOp",EDGE,"E415"),sQuery(id+"F0.wireOp",EDGE,"E416"),sQuery(id+"F0.wireOp",EDGE,"E417"),sQuery(id+"F0.wireOp",EDGE,"E418"),sQuery(id+"F0.wireOp",EDGE,"E419"),sQuery(id+"F0.wireOp",EDGE,"E420"),sQuery(id+"F0.wireOp",EDGE,"E421"),sQuery(id+"F0.wireOp",EDGE,"E422"),sQuery(id+"F0.wireOp",EDGE,"E423"),sQuery(id+"F0.wireOp",EDGE,"E424"),sQuery(id+"F0.wireOp",EDGE,"E425"),sQuery(id+"F0.wireOp",EDGE,"E426"),sQuery(id+"F0.wireOp",EDGE,"E427"),sQuery(id+"F0.wireOp",EDGE,"E428"),sQuery(id+"F0.wireOp",EDGE,"E429"),sQuery(id+"F0.wireOp",EDGE,"E430"),sQuery(id+"F0.wireOp",EDGE,"E431"),sQuery(id+"F0.wireOp",EDGE,"E432"),sQuery(id+"F0.wireOp",EDGE,"E433"),sQuery(id+"F0.wireOp",EDGE,"E434"),sQuery(id+"F0.wireOp",EDGE,"E435"),sQuery(id+"F0.wireOp",EDGE,"E436"),sQuery(id+"F0.wireOp",EDGE,"E437"),sQuery(id+"F0.wireOp",EDGE,"E438"),sQuery(id+"F0.wireOp",EDGE,"E439"),sQuery(id+"F0.wireOp",EDGE,"E440"),sQuery(id+"F0.wireOp",EDGE,"E441"),sQuery(id+"F0.wireOp",EDGE,"E442"),sQuery(id+"F0.wireOp",EDGE,"E443"),sQuery(id+"F0.wireOp",EDGE,"E444"),sQuery(id+"F0.wireOp",EDGE,"E445"),sQuery(id+"F0.wireOp",EDGE,"E446"),sQuery(id+"F0.wireOp",EDGE,"E447"),sQuery(id+"F0.wireOp",EDGE,"E448"),sQuery(id+"F0.wireOp",EDGE,"E449"),sQuery(id+"F0.wireOp",EDGE,"E450"),sQuery(id+"F0.wireOp",EDGE,"E451"),sQuery(id+"F0.wireOp",EDGE,"E452"),sQuery(id+"F0.wireOp",EDGE,"E453"),sQuery(id+"F0.wireOp",EDGE,"E454"),sQuery(id+"F0.wireOp",EDGE,"E455"),sQuery(id+"F0.wireOp",EDGE,"E456"),sQuery(id+"F0.wireOp",EDGE,"E457"),sQuery(id+"F0.wireOp",EDGE,"E458"),sQuery(id+"F0.wireOp",EDGE,"E459"),sQuery(id+"F0.wireOp",EDGE,"E460"),sQuery(id+"F0.wireOp",EDGE,"E461"),sQuery(id+"F0.wireOp",EDGE,"E462"),sQuery(id+"F0.wireOp",EDGE,"E463"),sQuery(id+"F0.wireOp",EDGE,"E464"),sQuery(id+"F0.wireOp",EDGE,"E465"),sQuery(id+"F0.wireOp",EDGE,"E466"),sQuery(id+"F0.wireOp",EDGE,"E467"),sQuery(id+"F0.wireOp",EDGE,"E468"),sQuery(id+"F0.wireOp",EDGE,"E469"),sQuery(id+"F0.wireOp",EDGE,"E470"),sQuery(id+"F0.wireOp",EDGE,"E471"),sQuery(id+"F0.wireOp",EDGE,"E472"),sQuery(id+"F0.wireOp",EDGE,"E473"),sQuery(id+"F0.wireOp",EDGE,"E474"),sQuery(id+"F0.wireOp",EDGE,"E475"),sQuery(id+"F0.wireOp",EDGE,"E476"),sQuery(id+"F0.wireOp",EDGE,"E477"),sQuery(id+"F0.wireOp",EDGE,"E478"),sQuery(id+"F0.wireOp",EDGE,"E479"),sQuery(id+"F0.wireOp",EDGE,"E480"),sQuery(id+"F0.wireOp",EDGE,"E481"),sQuery(id+"F0.wireOp",EDGE,"E482"),sQuery(id+"F0.wireOp",EDGE,"E483"),sQuery(id+"F0.wireOp",EDGE,"E484"),sQuery(id+"F0.wireOp",EDGE,"E485"),sQuery(id+"F0.wireOp",EDGE,"E486"),sQuery(id+"F0.wireOp",EDGE,"E487"),sQuery(id+"F0.wireOp",EDGE,"E488"),sQuery(id+"F0.wireOp",EDGE,"E489"),sQuery(id+"F0.wireOp",EDGE,"E490"),sQuery(id+"F0.wireOp",EDGE,"E491"),sQuery(id+"F0.wireOp",EDGE,"E492"),sQuery(id+"F0.wireOp",EDGE,"E493"),sQuery(id+"F0.wireOp",EDGE,"E494"),sQuery(id+"F0.wireOp",EDGE,"E495"),sQuery(id+"F0.wireOp",EDGE,"E496"),sQuery(id+"F0.wireOp",EDGE,"E497"),sQuery(id+"F0.wireOp",EDGE,"E498"),sQuery(id+"F0.wireOp",EDGE,"E499"),sQuery(id+"F0.wireOp",EDGE,"E500"),sQuery(id+"F0.wireOp",EDGE,"E501"),sQuery(id+"F0.wireOp",EDGE,"E502"),sQuery(id+"F0.wireOp",EDGE,"E503"),sQuery(id+"F0.wireOp",EDGE,"E504"),sQuery(id+"F0.wireOp",EDGE,"E505"),sQuery(id+"F0.wireOp",EDGE,"E506"),sQuery(id+"F0.wireOp",EDGE,"E507"),sQuery(id+"F0.wireOp",EDGE,"E508"),sQuery(id+"F0.wireOp",EDGE,"E509"),sQuery(id+"F0.wireOp",EDGE,"E510"),sQuery(id+"F0.wireOp",EDGE,"E511"),sQuery(id+"F0.wireOp",EDGE,"E512"),sQuery(id+"F0.wireOp",EDGE,"E513"),sQuery(id+"F0.wireOp",EDGE,"E514"),sQuery(id+"F0.wireOp",EDGE,"E515"),sQuery(id+"F0.wireOp",EDGE,"E516"),sQuery(id+"F0.wireOp",EDGE,"E517"),sQuery(id+"F0.wireOp",EDGE,"E518"),sQuery(id+"F0.wireOp",EDGE,"E519"),sQuery(id+"F0.wireOp",EDGE,"E520"),sQuery(id+"F0.wireOp",EDGE,"E521"),sQuery(id+"F0.wireOp",EDGE,"E522"),sQuery(id+"F0.wireOp",EDGE,"E523"),sQuery(id+"F0.wireOp",EDGE,"E524"),sQuery(id+"F0.wireOp",EDGE,"E525"),sQuery(id+"F0.wireOp",EDGE,"E526"),sQuery(id+"F0.wireOp",EDGE,"E527"),sQuery(id+"F0.wireOp",EDGE,"E528"),sQuery(id+"F0.wireOp",EDGE,"E529"),sQuery(id+"F0.wireOp",EDGE,"E530"),sQuery(id+"F0.wireOp",EDGE,"E531"),sQuery(id+"F0.wireOp",EDGE,"E532"),sQuery(id+"F0.wireOp",EDGE,"E533"),sQuery(id+"F0.wireOp",EDGE,"E534"),sQuery(id+"F0.wireOp",EDGE,"E535"),sQuery(id+"F0.wireOp",EDGE,"E536"),sQuery(id+"F0.wireOp",EDGE,"E537"),sQuery(id+"F0.wireOp",EDGE,"E538"),sQuery(id+"F0.wireOp",EDGE,"E539"),sQuery(id+"F0.wireOp",EDGE,"E540"),sQuery(id+"F0.wireOp",EDGE,"E541"),sQuery(id+"F0.wireOp",EDGE,"E542"),sQuery(id+"F0.wireOp",EDGE,"E543"),sQuery(id+"F0.wireOp",EDGE,"E544"),sQuery(id+"F0.wireOp",EDGE,"E545"),sQuery(id+"F0.wireOp",EDGE,"E546"),sQuery(id+"F0.wireOp",EDGE,"E547"),sQuery(id+"F0.wireOp",EDGE,"E548"),sQuery(id+"F0.wireOp",EDGE,"E549"),sQuery(id+"F0.wireOp",EDGE,"E550"),sQuery(id+"F0.wireOp",EDGE,"E551"),sQuery(id+"F0.wireOp",EDGE,"E552"),sQuery(id+"F0.wireOp",EDGE,"E553"),sQuery(id+"F0.wireOp",EDGE,"E554"),sQuery(id+"F0.wireOp",EDGE,"E555"),sQuery(id+"F0.wireOp",EDGE,"E556"),sQuery(id+"F0.wireOp",EDGE,"E557"),sQuery(id+"F0.wireOp",EDGE,"E558"),sQuery(id+"F0.wireOp",EDGE,"E559"),sQuery(id+"F0.wireOp",EDGE,"E560"),sQuery(id+"F0.wireOp",EDGE,"E561"),sQuery(id+"F0.wireOp",EDGE,"E562"),sQuery(id+"F0.wireOp",EDGE,"E563"),sQuery(id+"F0.wireOp",EDGE,"E564"),sQuery(id+"F0.wireOp",EDGE,"E565"),sQuery(id+"F0.wireOp",EDGE,"E566"),sQuery(id+"F0.wireOp",EDGE,"E567"),sQuery(id+"F0.wireOp",EDGE,"E568"),sQuery(id+"F0.wireOp",EDGE,"E569"),sQuery(id+"F0.wireOp",EDGE,"E570"),sQuery(id+"F0.wireOp",EDGE,"E571"),sQuery(id+"F0.wireOp",EDGE,"E572"),sQuery(id+"F0.wireOp",EDGE,"E573"),sQuery(id+"F0.wireOp",EDGE,"E574"),sQuery(id+"F0.wireOp",EDGE,"E575"),sQuery(id+"F0.wireOp",EDGE,"E576"),sQuery(id+"F0.wireOp",EDGE,"E577"),sQuery(id+"F0.wireOp",EDGE,"E1140"),sQuery(id+"F0.wireOp",EDGE,"E1143")])]});
            var Q1;
            Q1=qCreatedBy(makeId("Origin.pointOp"),VERTEX);
            transform(context, id + "F17", {"entities" : qUnion([Q0]), "transformType" : TransformType.SCALE_UNIFORMLY, "scale" : 1, "scalePoint" : qUnion([Q1]), "makeCopy" : false});
        }
        {
            var Q0;
            {var subQ0=sQuery(id+"F0.wireOp",EDGE,"E341");var subQ1=sQuery(id+"F0.wireOp",EDGE,"E340");var subQ4=sQuery(id+"F0.wireOp",EDGE,"E1143");var subQ5=sQuery(id+"F0.wireOp",EDGE,"E1140");var subQ6=sQuery(id+"F0.wireOp",EDGE,"E577");var subQ7=sQuery(id+"F0.wireOp",EDGE,"E576");var subQ8=sQuery(id+"F0.wireOp",EDGE,"E575");var subQ9=sQuery(id+"F0.wireOp",EDGE,"E574");var subQ10=sQuery(id+"F0.wireOp",EDGE,"E573");var subQ11=sQuery(id+"F0.wireOp",EDGE,"E572");var subQ12=sQuery(id+"F0.wireOp",EDGE,"E571");var subQ13=sQuery(id+"F0.wireOp",EDGE,"E570");var subQ14=sQuery(id+"F0.wireOp",EDGE,"E569");var subQ15=sQuery(id+"F0.wireOp",EDGE,"E568");var subQ16=sQuery(id+"F0.wireOp",EDGE,"E567");var subQ17=sQuery(id+"F0.wireOp",EDGE,"E566");var subQ18=sQuery(id+"F0.wireOp",EDGE,"E565");var subQ19=sQuery(id+"F0.wireOp",EDGE,"E564");var subQ20=sQuery(id+"F0.wireOp",EDGE,"E563");var subQ21=sQuery(id+"F0.wireOp",EDGE,"E562");var subQ22=sQuery(id+"F0.wireOp",EDGE,"E561");var subQ23=sQuery(id+"F0.wireOp",EDGE,"E560");var subQ24=sQuery(id+"F0.wireOp",EDGE,"E559");var subQ25=sQuery(id+"F0.wireOp",EDGE,"E558");var subQ26=sQuery(id+"F0.wireOp",EDGE,"E557");var subQ27=sQuery(id+"F0.wireOp",EDGE,"E556");var subQ28=sQuery(id+"F0.wireOp",EDGE,"E555");var subQ29=sQuery(id+"F0.wireOp",EDGE,"E554");var subQ30=sQuery(id+"F0.wireOp",EDGE,"E553");var subQ31=sQuery(id+"F0.wireOp",EDGE,"E552");var subQ32=sQuery(id+"F0.wireOp",EDGE,"E551");var subQ33=sQuery(id+"F0.wireOp",EDGE,"E550");var subQ34=sQuery(id+"F0.wireOp",EDGE,"E549");var subQ35=sQuery(id+"F0.wireOp",EDGE,"E548");var subQ36=sQuery(id+"F0.wireOp",EDGE,"E547");var subQ37=sQuery(id+"F0.wireOp",EDGE,"E546");var subQ38=sQuery(id+"F0.wireOp",EDGE,"E545");var subQ39=sQuery(id+"F0.wireOp",EDGE,"E544");var subQ40=sQuery(id+"F0.wireOp",EDGE,"E543");var subQ41=sQuery(id+"F0.wireOp",EDGE,"E542");var subQ42=sQuery(id+"F0.wireOp",EDGE,"E541");var subQ43=sQuery(id+"F0.wireOp",EDGE,"E540");var subQ44=sQuery(id+"F0.wireOp",EDGE,"E539");var subQ45=sQuery(id+"F0.wireOp",EDGE,"E538");var subQ46=sQuery(id+"F0.wireOp",EDGE,"E537");var subQ47=sQuery(id+"F0.wireOp",EDGE,"E536");var subQ48=sQuery(id+"F0.wireOp",EDGE,"E535");var subQ49=sQuery(id+"F0.wireOp",EDGE,"E534");var subQ50=sQuery(id+"F0.wireOp",EDGE,"E533");var subQ51=sQuery(id+"F0.wireOp",EDGE,"E532");var subQ52=sQuery(id+"F0.wireOp",EDGE,"E531");var subQ53=sQuery(id+"F0.wireOp",EDGE,"E530");var subQ54=sQuery(id+"F0.wireOp",EDGE,"E529");var subQ55=sQuery(id+"F0.wireOp",EDGE,"E528");var subQ56=sQuery(id+"F0.wireOp",EDGE,"E527");var subQ57=sQuery(id+"F0.wireOp",EDGE,"E526");var subQ58=sQuery(id+"F0.wireOp",EDGE,"E525");var subQ59=sQuery(id+"F0.wireOp",EDGE,"E524");var subQ60=sQuery(id+"F0.wireOp",EDGE,"E523");var subQ61=sQuery(id+"F0.wireOp",EDGE,"E522");var subQ62=sQuery(id+"F0.wireOp",EDGE,"E521");var subQ63=sQuery(id+"F0.wireOp",EDGE,"E520");var subQ64=sQuery(id+"F0.wireOp",EDGE,"E519");var subQ65=sQuery(id+"F0.wireOp",EDGE,"E518");var subQ66=sQuery(id+"F0.wireOp",EDGE,"E517");var subQ67=sQuery(id+"F0.wireOp",EDGE,"E516");var subQ68=sQuery(id+"F0.wireOp",EDGE,"E515");var subQ69=sQuery(id+"F0.wireOp",EDGE,"E514");var subQ70=sQuery(id+"F0.wireOp",EDGE,"E513");var subQ71=sQuery(id+"F0.wireOp",EDGE,"E512");var subQ72=sQuery(id+"F0.wireOp",EDGE,"E511");var subQ73=sQuery(id+"F0.wireOp",EDGE,"E510");var subQ74=sQuery(id+"F0.wireOp",EDGE,"E509");var subQ75=sQuery(id+"F0.wireOp",EDGE,"E508");var subQ76=sQuery(id+"F0.wireOp",EDGE,"E507");var subQ77=sQuery(id+"F0.wireOp",EDGE,"E506");var subQ78=sQuery(id+"F0.wireOp",EDGE,"E505");var subQ79=sQuery(id+"F0.wireOp",EDGE,"E504");var subQ80=sQuery(id+"F0.wireOp",EDGE,"E503");var subQ81=sQuery(id+"F0.wireOp",EDGE,"E502");var subQ82=sQuery(id+"F0.wireOp",EDGE,"E501");var subQ83=sQuery(id+"F0.wireOp",EDGE,"E500");var subQ84=sQuery(id+"F0.wireOp",EDGE,"E499");var subQ85=sQuery(id+"F0.wireOp",EDGE,"E498");var subQ86=sQuery(id+"F0.wireOp",EDGE,"E497");var subQ87=sQuery(id+"F0.wireOp",EDGE,"E496");var subQ88=sQuery(id+"F0.wireOp",EDGE,"E495");var subQ89=sQuery(id+"F0.wireOp",EDGE,"E494");var subQ90=sQuery(id+"F0.wireOp",EDGE,"E493");var subQ91=sQuery(id+"F0.wireOp",EDGE,"E492");var subQ92=sQuery(id+"F0.wireOp",EDGE,"E491");var subQ93=sQuery(id+"F0.wireOp",EDGE,"E490");var subQ94=sQuery(id+"F0.wireOp",EDGE,"E489");var subQ95=sQuery(id+"F0.wireOp",EDGE,"E488");var subQ96=sQuery(id+"F0.wireOp",EDGE,"E487");var subQ97=sQuery(id+"F0.wireOp",EDGE,"E486");var subQ98=sQuery(id+"F0.wireOp",EDGE,"E485");var subQ99=sQuery(id+"F0.wireOp",EDGE,"E484");var subQ100=sQuery(id+"F0.wireOp",EDGE,"E483");var subQ101=sQuery(id+"F0.wireOp",EDGE,"E482");var subQ102=sQuery(id+"F0.wireOp",EDGE,"E481");var subQ103=sQuery(id+"F0.wireOp",EDGE,"E480");var subQ104=sQuery(id+"F0.wireOp",EDGE,"E479");var subQ105=sQuery(id+"F0.wireOp",EDGE,"E478");var subQ106=sQuery(id+"F0.wireOp",EDGE,"E477");var subQ107=sQuery(id+"F0.wireOp",EDGE,"E476");var subQ108=sQuery(id+"F0.wireOp",EDGE,"E475");var subQ109=sQuery(id+"F0.wireOp",EDGE,"E474");var subQ110=sQuery(id+"F0.wireOp",EDGE,"E473");var subQ111=sQuery(id+"F0.wireOp",EDGE,"E472");var subQ112=sQuery(id+"F0.wireOp",EDGE,"E471");var subQ113=sQuery(id+"F0.wireOp",EDGE,"E470");var subQ114=sQuery(id+"F0.wireOp",EDGE,"E469");var subQ115=sQuery(id+"F0.wireOp",EDGE,"E468");var subQ116=sQuery(id+"F0.wireOp",EDGE,"E467");var subQ117=sQuery(id+"F0.wireOp",EDGE,"E466");var subQ118=sQuery(id+"F0.wireOp",EDGE,"E465");var subQ119=sQuery(id+"F0.wireOp",EDGE,"E464");var subQ120=sQuery(id+"F0.wireOp",EDGE,"E463");var subQ121=sQuery(id+"F0.wireOp",EDGE,"E462");var subQ122=sQuery(id+"F0.wireOp",EDGE,"E461");var subQ123=sQuery(id+"F0.wireOp",EDGE,"E460");var subQ124=sQuery(id+"F0.wireOp",EDGE,"E459");var subQ125=sQuery(id+"F0.wireOp",EDGE,"E458");var subQ126=sQuery(id+"F0.wireOp",EDGE,"E457");var subQ127=sQuery(id+"F0.wireOp",EDGE,"E456");var subQ128=sQuery(id+"F0.wireOp",EDGE,"E455");var subQ129=sQuery(id+"F0.wireOp",EDGE,"E454");var subQ130=sQuery(id+"F0.wireOp",EDGE,"E453");var subQ131=sQuery(id+"F0.wireOp",EDGE,"E452");var subQ132=sQuery(id+"F0.wireOp",EDGE,"E451");var subQ133=sQuery(id+"F0.wireOp",EDGE,"E450");var subQ134=sQuery(id+"F0.wireOp",EDGE,"E449");var subQ135=sQuery(id+"F0.wireOp",EDGE,"E448");var subQ136=sQuery(id+"F0.wireOp",EDGE,"E447");var subQ137=sQuery(id+"F0.wireOp",EDGE,"E446");var subQ138=sQuery(id+"F0.wireOp",EDGE,"E445");var subQ139=sQuery(id+"F0.wireOp",EDGE,"E444");var subQ140=sQuery(id+"F0.wireOp",EDGE,"E443");var subQ141=sQuery(id+"F0.wireOp",EDGE,"E442");var subQ142=sQuery(id+"F0.wireOp",EDGE,"E441");var subQ143=sQuery(id+"F0.wireOp",EDGE,"E440");var subQ144=sQuery(id+"F0.wireOp",EDGE,"E439");var subQ145=sQuery(id+"F0.wireOp",EDGE,"E438");var subQ146=sQuery(id+"F0.wireOp",EDGE,"E437");var subQ147=sQuery(id+"F0.wireOp",EDGE,"E436");var subQ148=sQuery(id+"F0.wireOp",EDGE,"E435");var subQ149=sQuery(id+"F0.wireOp",EDGE,"E434");var subQ150=sQuery(id+"F0.wireOp",EDGE,"E433");var subQ151=sQuery(id+"F0.wireOp",EDGE,"E432");var subQ152=sQuery(id+"F0.wireOp",EDGE,"E431");var subQ153=sQuery(id+"F0.wireOp",EDGE,"E430");var subQ154=sQuery(id+"F0.wireOp",EDGE,"E429");var subQ155=sQuery(id+"F0.wireOp",EDGE,"E428");var subQ156=sQuery(id+"F0.wireOp",EDGE,"E427");var subQ157=sQuery(id+"F0.wireOp",EDGE,"E426");var subQ158=sQuery(id+"F0.wireOp",EDGE,"E425");var subQ159=sQuery(id+"F0.wireOp",EDGE,"E424");var subQ160=sQuery(id+"F0.wireOp",EDGE,"E423");var subQ161=sQuery(id+"F0.wireOp",EDGE,"E422");var subQ162=sQuery(id+"F0.wireOp",EDGE,"E421");var subQ163=sQuery(id+"F0.wireOp",EDGE,"E420");var subQ164=sQuery(id+"F0.wireOp",EDGE,"E419");var subQ165=sQuery(id+"F0.wireOp",EDGE,"E418");var subQ166=sQuery(id+"F0.wireOp",EDGE,"E417");var subQ167=sQuery(id+"F0.wireOp",EDGE,"E416");var subQ168=sQuery(id+"F0.wireOp",EDGE,"E415");var subQ169=sQuery(id+"F0.wireOp",EDGE,"E414");var subQ170=sQuery(id+"F0.wireOp",EDGE,"E413");var subQ171=sQuery(id+"F0.wireOp",EDGE,"E412");var subQ172=sQuery(id+"F0.wireOp",EDGE,"E411");var subQ173=sQuery(id+"F0.wireOp",EDGE,"E410");var subQ174=sQuery(id+"F0.wireOp",EDGE,"E409");var subQ175=sQuery(id+"F0.wireOp",EDGE,"E408");var subQ176=sQuery(id+"F0.wireOp",EDGE,"E407");var subQ177=sQuery(id+"F0.wireOp",EDGE,"E406");var subQ178=sQuery(id+"F0.wireOp",EDGE,"E405");var subQ179=sQuery(id+"F0.wireOp",EDGE,"E404");var subQ180=sQuery(id+"F0.wireOp",EDGE,"E403");var subQ181=sQuery(id+"F0.wireOp",EDGE,"E402");var subQ182=sQuery(id+"F0.wireOp",EDGE,"E401");var subQ183=sQuery(id+"F0.wireOp",EDGE,"E400");var subQ184=sQuery(id+"F0.wireOp",EDGE,"E399");var subQ185=sQuery(id+"F0.wireOp",EDGE,"E398");var subQ186=sQuery(id+"F0.wireOp",EDGE,"E397");var subQ187=sQuery(id+"F0.wireOp",EDGE,"E396");var subQ188=sQuery(id+"F0.wireOp",EDGE,"E395");var subQ189=sQuery(id+"F0.wireOp",EDGE,"E394");var subQ190=sQuery(id+"F0.wireOp",EDGE,"E393");var subQ191=sQuery(id+"F0.wireOp",EDGE,"E392");var subQ192=sQuery(id+"F0.wireOp",EDGE,"E391");var subQ193=sQuery(id+"F0.wireOp",EDGE,"E390");var subQ194=sQuery(id+"F0.wireOp",EDGE,"E389");var subQ195=sQuery(id+"F0.wireOp",EDGE,"E388");var subQ196=sQuery(id+"F0.wireOp",EDGE,"E387");var subQ197=sQuery(id+"F0.wireOp",EDGE,"E386");var subQ198=sQuery(id+"F0.wireOp",EDGE,"E385");var subQ199=sQuery(id+"F0.wireOp",EDGE,"E384");var subQ200=sQuery(id+"F0.wireOp",EDGE,"E383");var subQ201=sQuery(id+"F0.wireOp",EDGE,"E382");var subQ202=sQuery(id+"F0.wireOp",EDGE,"E381");var subQ203=sQuery(id+"F0.wireOp",EDGE,"E380");var subQ204=sQuery(id+"F0.wireOp",EDGE,"E379");var subQ205=sQuery(id+"F0.wireOp",EDGE,"E378");var subQ206=sQuery(id+"F0.wireOp",EDGE,"E377");var subQ207=sQuery(id+"F0.wireOp",EDGE,"E376");var subQ208=sQuery(id+"F0.wireOp",EDGE,"E375");var subQ209=sQuery(id+"F0.wireOp",EDGE,"E374");var subQ210=sQuery(id+"F0.wireOp",EDGE,"E373");var subQ211=sQuery(id+"F0.wireOp",EDGE,"E372");var subQ212=sQuery(id+"F0.wireOp",EDGE,"E371");var subQ213=sQuery(id+"F0.wireOp",EDGE,"E370");var subQ214=sQuery(id+"F0.wireOp",EDGE,"E369");var subQ215=sQuery(id+"F0.wireOp",EDGE,"E368");var subQ216=sQuery(id+"F0.wireOp",EDGE,"E367");var subQ217=sQuery(id+"F0.wireOp",EDGE,"E366");var subQ218=sQuery(id+"F0.wireOp",EDGE,"E365");var subQ219=sQuery(id+"F0.wireOp",EDGE,"E364");var subQ220=sQuery(id+"F0.wireOp",EDGE,"E363");var subQ221=sQuery(id+"F0.wireOp",EDGE,"E362");var subQ222=sQuery(id+"F0.wireOp",EDGE,"E361");var subQ223=sQuery(id+"F0.wireOp",EDGE,"E360");var subQ224=sQuery(id+"F0.wireOp",EDGE,"E359");var subQ225=sQuery(id+"F0.wireOp",EDGE,"E358");var subQ226=sQuery(id+"F0.wireOp",EDGE,"E357");var subQ227=sQuery(id+"F0.wireOp",EDGE,"E356");var subQ228=sQuery(id+"F0.wireOp",EDGE,"E355");var subQ229=sQuery(id+"F0.wireOp",EDGE,"E354");var subQ230=sQuery(id+"F0.wireOp",EDGE,"E353");var subQ231=sQuery(id+"F0.wireOp",EDGE,"E352");var subQ232=sQuery(id+"F0.wireOp",EDGE,"E351");var subQ233=sQuery(id+"F0.wireOp",EDGE,"E350");var subQ234=sQuery(id+"F0.wireOp",EDGE,"E349");var subQ235=sQuery(id+"F0.wireOp",EDGE,"E348");var subQ236=sQuery(id+"F0.wireOp",EDGE,"E347");var subQ237=sQuery(id+"F0.wireOp",EDGE,"E346");var subQ238=sQuery(id+"F0.wireOp",EDGE,"E345");var subQ239=sQuery(id+"F0.wireOp",EDGE,"E344");var subQ240=sQuery(id+"F0.wireOp",EDGE,"E343");var subQ241=sQuery(id+"F0.wireOp",EDGE,"E342");var subQ242=sQuery(id+"F0.wireOp",EDGE,"E339");var subQ243=sQuery(id+"F0.wireOp",EDGE,"E338");var subQ244=sQuery(id+"F0.wireOp",EDGE,"E337");var subQ245=sQuery(id+"F0.wireOp",EDGE,"E336");var subQ246=sQuery(id+"F0.wireOp",EDGE,"E335");var subQ247=sQuery(id+"F0.wireOp",EDGE,"E334");var subQ248=sQuery(id+"F0.wireOp",EDGE,"E333");var subQ249=sQuery(id+"F0.wireOp",EDGE,"E332");var subQ250=sQuery(id+"F0.wireOp",EDGE,"E331");var subQ251=sQuery(id+"F0.wireOp",EDGE,"E330");var subQ252=sQuery(id+"F0.wireOp",EDGE,"E329");var subQ253=sQuery(id+"F0.wireOp",EDGE,"E328");var subQ254=sQuery(id+"F0.wireOp",EDGE,"E327");var subQ255=sQuery(id+"F0.wireOp",EDGE,"E326");var subQ256=sQuery(id+"F0.wireOp",EDGE,"E325");var subQ257=sQuery(id+"F0.wireOp",EDGE,"E324");var subQ258=sQuery(id+"F0.wireOp",EDGE,"E323");var subQ259=sQuery(id+"F0.wireOp",EDGE,"E322");var subQ260=sQuery(id+"F0.wireOp",EDGE,"E321");var subQ261=sQuery(id+"F0.wireOp",EDGE,"E320");var subQ262=sQuery(id+"F0.wireOp",EDGE,"E319");var subQ263=sQuery(id+"F0.wireOp",EDGE,"E318");var subQ264=sQuery(id+"F0.wireOp",EDGE,"E317");var subQ265=sQuery(id+"F0.wireOp",EDGE,"E316");var subQ266=sQuery(id+"F0.wireOp",EDGE,"E315");var subQ267=sQuery(id+"F0.wireOp",EDGE,"E314");var subQ268=sQuery(id+"F0.wireOp",EDGE,"E313");var subQ269=sQuery(id+"F0.wireOp",EDGE,"E312");var subQ270=sQuery(id+"F0.wireOp",EDGE,"E311");var subQ271=sQuery(id+"F0.wireOp",EDGE,"E310");var subQ272=sQuery(id+"F0.wireOp",EDGE,"E309");var subQ273=sQuery(id+"F0.wireOp",EDGE,"E308");var subQ274=sQuery(id+"F0.wireOp",EDGE,"E307");var subQ275=sQuery(id+"F0.wireOp",EDGE,"E306");var subQ276=sQuery(id+"F0.wireOp",EDGE,"E305");var subQ277=sQuery(id+"F0.wireOp",EDGE,"E304");var subQ278=sQuery(id+"F0.wireOp",EDGE,"E303");var subQ279=sQuery(id+"F0.wireOp",EDGE,"E302");var subQ280=sQuery(id+"F0.wireOp",EDGE,"E301");var subQ281=sQuery(id+"F0.wireOp",EDGE,"E300");var subQ282=sQuery(id+"F0.wireOp",EDGE,"E299");var subQ283=sQuery(id+"F0.wireOp",EDGE,"E298");var subQ284=sQuery(id+"F0.wireOp",EDGE,"E297");var subQ285=sQuery(id+"F0.wireOp",EDGE,"E296");var subQ286=sQuery(id+"F0.wireOp",EDGE,"E295");var subQ287=sQuery(id+"F0.wireOp",EDGE,"E294");var subQ288=sQuery(id+"F0.wireOp",EDGE,"E293");var subQ289=sQuery(id+"F0.wireOp",EDGE,"E292");var subQ290=sQuery(id+"F0.wireOp",EDGE,"E291");var subQ291=sQuery(id+"F0.wireOp",EDGE,"E290");var subQ292=sQuery(id+"F0.wireOp",EDGE,"E289");var subQ293=sQuery(id+"F0.wireOp",EDGE,"E288");var subQ294=sQuery(id+"F0.wireOp",EDGE,"E287");var subQ295=sQuery(id+"F0.wireOp",EDGE,"E286");var subQ296=sQuery(id+"F0.wireOp",EDGE,"E285");var subQ297=sQuery(id+"F0.wireOp",EDGE,"E284");var subQ298=sQuery(id+"F0.wireOp",EDGE,"E283");var subQ299=sQuery(id+"F0.wireOp",EDGE,"E282");var subQ300=sQuery(id+"F0.wireOp",EDGE,"E281");var subQ301=sQuery(id+"F0.wireOp",EDGE,"E280");var subQ302=sQuery(id+"F0.wireOp",EDGE,"E279");var subQ303=sQuery(id+"F0.wireOp",EDGE,"E278");var subQ304=sQuery(id+"F0.wireOp",EDGE,"E277");var subQ305=sQuery(id+"F0.wireOp",EDGE,"E276");var subQ306=sQuery(id+"F0.wireOp",EDGE,"E275");var subQ307=sQuery(id+"F0.wireOp",EDGE,"E274");var subQ308=sQuery(id+"F0.wireOp",EDGE,"E273");var subQ309=sQuery(id+"F0.wireOp",EDGE,"E272");var subQ310=sQuery(id+"F0.wireOp",EDGE,"E271");var subQ311=sQuery(id+"F0.wireOp",EDGE,"E270");var subQ312=sQuery(id+"F0.wireOp",EDGE,"E269");var subQ313=sQuery(id+"F0.wireOp",EDGE,"E268");var subQ314=sQuery(id+"F0.wireOp",EDGE,"E267");var subQ315=sQuery(id+"F0.wireOp",EDGE,"E266");var subQ316=sQuery(id+"F0.wireOp",EDGE,"E265");var subQ317=sQuery(id+"F0.wireOp",EDGE,"E264");var subQ318=sQuery(id+"F0.wireOp",EDGE,"E263");var subQ319=sQuery(id+"F0.wireOp",EDGE,"E262");var subQ320=sQuery(id+"F0.wireOp",EDGE,"E261");var subQ321=sQuery(id+"F0.wireOp",EDGE,"E260");var subQ322=sQuery(id+"F0.wireOp",EDGE,"E259");var subQ323=sQuery(id+"F0.wireOp",EDGE,"E258");var subQ324=sQuery(id+"F0.wireOp",EDGE,"E257");var subQ325=sQuery(id+"F0.wireOp",EDGE,"E256");var subQ326=sQuery(id+"F0.wireOp",EDGE,"E255");var subQ327=sQuery(id+"F0.wireOp",EDGE,"E254");var subQ328=sQuery(id+"F0.wireOp",EDGE,"E253");var subQ329=sQuery(id+"F0.wireOp",EDGE,"E252");var subQ330=sQuery(id+"F0.wireOp",EDGE,"E251");var subQ331=sQuery(id+"F0.wireOp",EDGE,"E250");var subQ332=sQuery(id+"F0.wireOp",EDGE,"E249");var subQ333=sQuery(id+"F0.wireOp",EDGE,"E248");var subQ334=sQuery(id+"F0.wireOp",EDGE,"E247");var subQ335=sQuery(id+"F0.wireOp",EDGE,"E246");var subQ336=sQuery(id+"F0.wireOp",EDGE,"E245");var subQ337=sQuery(id+"F0.wireOp",EDGE,"E244");var subQ338=sQuery(id+"F0.wireOp",EDGE,"E243");var subQ339=sQuery(id+"F0.wireOp",EDGE,"E242");var subQ340=sQuery(id+"F0.wireOp",EDGE,"E241");var subQ341=sQuery(id+"F0.wireOp",EDGE,"E240");var subQ342=sQuery(id+"F0.wireOp",EDGE,"E239");var subQ343=sQuery(id+"F0.wireOp",EDGE,"E238");var subQ344=sQuery(id+"F0.wireOp",EDGE,"E237");var subQ345=sQuery(id+"F0.wireOp",EDGE,"E236");var subQ346=sQuery(id+"F0.wireOp",EDGE,"E235");var subQ347=sQuery(id+"F0.wireOp",EDGE,"E234");var subQ348=sQuery(id+"F0.wireOp",EDGE,"E233");var subQ349=sQuery(id+"F0.wireOp",EDGE,"E232");var subQ350=sQuery(id+"F0.wireOp",EDGE,"E231");var subQ351=sQuery(id+"F0.wireOp",EDGE,"E230");var subQ352=sQuery(id+"F0.wireOp",EDGE,"E229");var subQ353=sQuery(id+"F0.wireOp",EDGE,"E228");var subQ354=sQuery(id+"F0.wireOp",EDGE,"E227");var subQ355=sQuery(id+"F0.wireOp",EDGE,"E226");var subQ356=sQuery(id+"F0.wireOp",EDGE,"E225");var subQ357=sQuery(id+"F0.wireOp",EDGE,"E224");var subQ358=sQuery(id+"F0.wireOp",EDGE,"E223");var subQ359=sQuery(id+"F0.wireOp",EDGE,"E222");var subQ360=sQuery(id+"F0.wireOp",EDGE,"E221");var subQ361=sQuery(id+"F0.wireOp",EDGE,"E220");var subQ362=sQuery(id+"F0.wireOp",EDGE,"E219");var subQ363=sQuery(id+"F0.wireOp",EDGE,"E218");var subQ364=sQuery(id+"F0.wireOp",EDGE,"E217");var subQ365=sQuery(id+"F0.wireOp",EDGE,"E216");var subQ366=sQuery(id+"F0.wireOp",EDGE,"E215");var subQ367=sQuery(id+"F0.wireOp",EDGE,"E214");var subQ368=sQuery(id+"F0.wireOp",EDGE,"E213");var subQ369=sQuery(id+"F0.wireOp",EDGE,"E212");var subQ370=sQuery(id+"F0.wireOp",EDGE,"E211");var subQ371=sQuery(id+"F0.wireOp",EDGE,"E210");var subQ372=sQuery(id+"F0.wireOp",EDGE,"E209");var subQ373=sQuery(id+"F0.wireOp",EDGE,"E208");var subQ374=sQuery(id+"F0.wireOp",EDGE,"E207");var subQ375=sQuery(id+"F0.wireOp",EDGE,"E206");var subQ376=sQuery(id+"F0.wireOp",EDGE,"E205");var subQ377=sQuery(id+"F0.wireOp",EDGE,"E204");var subQ378=sQuery(id+"F0.wireOp",EDGE,"E203");var subQ379=sQuery(id+"F0.wireOp",EDGE,"E202");var subQ380=sQuery(id+"F0.wireOp",EDGE,"E201");var subQ381=sQuery(id+"F0.wireOp",EDGE,"E200");var subQ382=sQuery(id+"F0.wireOp",EDGE,"E199");var subQ383=sQuery(id+"F0.wireOp",EDGE,"E198");var subQ384=sQuery(id+"F0.wireOp",EDGE,"E197");var subQ385=sQuery(id+"F0.wireOp",EDGE,"E196");var subQ386=sQuery(id+"F0.wireOp",EDGE,"E195");var subQ387=sQuery(id+"F0.wireOp",EDGE,"E194");var subQ388=sQuery(id+"F0.wireOp",EDGE,"E193");var subQ389=sQuery(id+"F0.wireOp",EDGE,"E192");var subQ390=sQuery(id+"F0.wireOp",EDGE,"E191");var subQ391=sQuery(id+"F0.wireOp",EDGE,"E190");var subQ392=sQuery(id+"F0.wireOp",EDGE,"E189");var subQ393=sQuery(id+"F0.wireOp",EDGE,"E188");var subQ394=sQuery(id+"F0.wireOp",EDGE,"E187");var subQ395=sQuery(id+"F0.wireOp",EDGE,"E186");var subQ396=sQuery(id+"F0.wireOp",EDGE,"E185");var subQ397=sQuery(id+"F0.wireOp",EDGE,"E184");var subQ398=sQuery(id+"F0.wireOp",EDGE,"E183");var subQ399=sQuery(id+"F0.wireOp",EDGE,"E182");var subQ400=sQuery(id+"F0.wireOp",EDGE,"E181");var subQ401=sQuery(id+"F0.wireOp",EDGE,"E180");var subQ402=sQuery(id+"F0.wireOp",EDGE,"E179");var subQ403=sQuery(id+"F0.wireOp",EDGE,"E178");var subQ404=sQuery(id+"F0.wireOp",EDGE,"E177");var subQ405=sQuery(id+"F0.wireOp",EDGE,"E176");var subQ406=sQuery(id+"F0.wireOp",EDGE,"E175");var subQ407=sQuery(id+"F0.wireOp",EDGE,"E174");var subQ408=sQuery(id+"F0.wireOp",EDGE,"E173");var subQ409=sQuery(id+"F0.wireOp",EDGE,"E172");var subQ410=sQuery(id+"F0.wireOp",EDGE,"E171");var subQ411=sQuery(id+"F0.wireOp",EDGE,"E170");var subQ412=sQuery(id+"F0.wireOp",EDGE,"E169");var subQ413=sQuery(id+"F0.wireOp",EDGE,"E168");var subQ414=sQuery(id+"F0.wireOp",EDGE,"E167");var subQ415=sQuery(id+"F0.wireOp",EDGE,"E166");var subQ416=sQuery(id+"F0.wireOp",EDGE,"E165");var subQ417=sQuery(id+"F0.wireOp",EDGE,"E164");var subQ418=sQuery(id+"F0.wireOp",EDGE,"E163");var subQ419=sQuery(id+"F0.wireOp",EDGE,"E162");var subQ420=sQuery(id+"F0.wireOp",EDGE,"E161");var subQ421=sQuery(id+"F0.wireOp",EDGE,"E160");var subQ422=sQuery(id+"F0.wireOp",EDGE,"E159");var subQ423=sQuery(id+"F0.wireOp",EDGE,"E158");var subQ424=sQuery(id+"F0.wireOp",EDGE,"E157");var subQ425=sQuery(id+"F0.wireOp",EDGE,"E156");var subQ426=sQuery(id+"F0.wireOp",EDGE,"E155");var subQ427=sQuery(id+"F0.wireOp",EDGE,"E154");var subQ428=sQuery(id+"F0.wireOp",EDGE,"E153");var subQ429=sQuery(id+"F0.wireOp",EDGE,"E152");var subQ430=sQuery(id+"F0.wireOp",EDGE,"E151");var subQ431=sQuery(id+"F0.wireOp",EDGE,"E150");var subQ432=sQuery(id+"F0.wireOp",EDGE,"E149");var subQ433=sQuery(id+"F0.wireOp",EDGE,"E148");var subQ434=sQuery(id+"F0.wireOp",EDGE,"E147");var subQ435=sQuery(id+"F0.wireOp",EDGE,"E146");var subQ436=sQuery(id+"F0.wireOp",EDGE,"E145");var subQ437=sQuery(id+"F0.wireOp",EDGE,"E144");var subQ438=sQuery(id+"F0.wireOp",EDGE,"E143");var subQ439=sQuery(id+"F0.wireOp",EDGE,"E142");var subQ440=sQuery(id+"F0.wireOp",EDGE,"E141");var subQ441=sQuery(id+"F0.wireOp",EDGE,"E140");var subQ442=sQuery(id+"F0.wireOp",EDGE,"E139");var subQ443=sQuery(id+"F0.wireOp",EDGE,"E138");var subQ444=sQuery(id+"F0.wireOp",EDGE,"E137");var subQ445=sQuery(id+"F0.wireOp",EDGE,"E136");var subQ446=sQuery(id+"F0.wireOp",EDGE,"E135");var subQ447=sQuery(id+"F0.wireOp",EDGE,"E134");var subQ448=sQuery(id+"F0.wireOp",EDGE,"E133");var subQ449=sQuery(id+"F0.wireOp",EDGE,"E132");var subQ450=sQuery(id+"F0.wireOp",EDGE,"E131");var subQ451=sQuery(id+"F0.wireOp",EDGE,"E130");var subQ452=sQuery(id+"F0.wireOp",EDGE,"E129");var subQ453=sQuery(id+"F0.wireOp",EDGE,"E128");var subQ454=sQuery(id+"F0.wireOp",EDGE,"E127");var subQ455=sQuery(id+"F0.wireOp",EDGE,"E126");var subQ456=sQuery(id+"F0.wireOp",EDGE,"E125");var subQ457=sQuery(id+"F0.wireOp",EDGE,"E124");var subQ458=sQuery(id+"F0.wireOp",EDGE,"E123");var subQ459=sQuery(id+"F0.wireOp",EDGE,"E122");var subQ460=sQuery(id+"F0.wireOp",EDGE,"E121");var subQ461=sQuery(id+"F0.wireOp",EDGE,"E120");var subQ462=sQuery(id+"F0.wireOp",EDGE,"E119");var subQ463=sQuery(id+"F0.wireOp",EDGE,"E118");var subQ464=sQuery(id+"F0.wireOp",EDGE,"E117");var subQ465=sQuery(id+"F0.wireOp",EDGE,"E116");var subQ466=sQuery(id+"F0.wireOp",EDGE,"E115");var subQ467=sQuery(id+"F0.wireOp",EDGE,"E114");var subQ468=sQuery(id+"F0.wireOp",EDGE,"E113");var subQ469=sQuery(id+"F0.wireOp",EDGE,"E112");var subQ470=sQuery(id+"F0.wireOp",EDGE,"E111");var subQ471=sQuery(id+"F0.wireOp",EDGE,"E110");var subQ472=sQuery(id+"F0.wireOp",EDGE,"E109");var subQ473=sQuery(id+"F0.wireOp",EDGE,"E108");var subQ474=sQuery(id+"F0.wireOp",EDGE,"E107");var subQ475=sQuery(id+"F0.wireOp",EDGE,"E106");var subQ476=sQuery(id+"F0.wireOp",EDGE,"E105");var subQ477=sQuery(id+"F0.wireOp",EDGE,"E104");var subQ478=sQuery(id+"F0.wireOp",EDGE,"E103");var subQ479=sQuery(id+"F0.wireOp",EDGE,"E102");var subQ480=sQuery(id+"F0.wireOp",EDGE,"E101");var subQ481=sQuery(id+"F0.wireOp",EDGE,"E100");var subQ482=sQuery(id+"F0.wireOp",EDGE,"E99");var subQ483=sQuery(id+"F0.wireOp",EDGE,"E98");var subQ484=sQuery(id+"F0.wireOp",EDGE,"E97");var subQ485=sQuery(id+"F0.wireOp",EDGE,"E96");var subQ486=sQuery(id+"F0.wireOp",EDGE,"E95");var subQ487=sQuery(id+"F0.wireOp",EDGE,"E94");var subQ488=sQuery(id+"F0.wireOp",EDGE,"E93");var subQ489=sQuery(id+"F0.wireOp",EDGE,"E92");var subQ490=sQuery(id+"F0.wireOp",EDGE,"E91");var subQ491=sQuery(id+"F0.wireOp",EDGE,"E90");var subQ492=sQuery(id+"F0.wireOp",EDGE,"E89");var subQ493=sQuery(id+"F0.wireOp",EDGE,"E88");var subQ494=sQuery(id+"F0.wireOp",EDGE,"E87");var subQ495=sQuery(id+"F0.wireOp",EDGE,"E86");var subQ496=sQuery(id+"F0.wireOp",EDGE,"E85");var subQ497=sQuery(id+"F0.wireOp",EDGE,"E84");var subQ498=sQuery(id+"F0.wireOp",EDGE,"E83");var subQ499=sQuery(id+"F0.wireOp",EDGE,"E82");var subQ500=sQuery(id+"F0.wireOp",EDGE,"E81");var subQ501=sQuery(id+"F0.wireOp",EDGE,"E80");var subQ502=sQuery(id+"F0.wireOp",EDGE,"E79");var subQ503=sQuery(id+"F0.wireOp",EDGE,"E78");var subQ504=sQuery(id+"F0.wireOp",EDGE,"E77");var subQ505=sQuery(id+"F0.wireOp",EDGE,"E76");var subQ506=sQuery(id+"F0.wireOp",EDGE,"E75");var subQ507=sQuery(id+"F0.wireOp",EDGE,"E74");var subQ508=sQuery(id+"F0.wireOp",EDGE,"E73");var subQ509=sQuery(id+"F0.wireOp",EDGE,"E72");var subQ510=sQuery(id+"F0.wireOp",EDGE,"E71");var subQ511=sQuery(id+"F0.wireOp",EDGE,"E70");var subQ512=sQuery(id+"F0.wireOp",EDGE,"E69");var subQ513=sQuery(id+"F0.wireOp",EDGE,"E68");var subQ514=sQuery(id+"F0.wireOp",EDGE,"E67");var subQ515=sQuery(id+"F0.wireOp",EDGE,"E66");var subQ516=sQuery(id+"F0.wireOp",EDGE,"E65");var subQ517=sQuery(id+"F0.wireOp",EDGE,"E64");var subQ518=sQuery(id+"F0.wireOp",EDGE,"E63");var subQ519=sQuery(id+"F0.wireOp",EDGE,"E62");var subQ520=sQuery(id+"F0.wireOp",EDGE,"E61");var subQ521=sQuery(id+"F0.wireOp",EDGE,"E60");var subQ522=sQuery(id+"F0.wireOp",EDGE,"E59");var subQ523=sQuery(id+"F0.wireOp",EDGE,"E58");var subQ524=sQuery(id+"F0.wireOp",EDGE,"E57");var subQ525=sQuery(id+"F0.wireOp",EDGE,"E56");var subQ526=sQuery(id+"F0.wireOp",EDGE,"E55");var subQ527=sQuery(id+"F0.wireOp",EDGE,"E54");var subQ528=sQuery(id+"F0.wireOp",EDGE,"E53");var subQ529=sQuery(id+"F0.wireOp",EDGE,"E52");var subQ530=sQuery(id+"F0.wireOp",EDGE,"E51");var subQ531=sQuery(id+"F0.wireOp",EDGE,"E50");var subQ532=sQuery(id+"F0.wireOp",EDGE,"E49");var subQ533=sQuery(id+"F0.wireOp",EDGE,"E48");var subQ534=sQuery(id+"F0.wireOp",EDGE,"E47");var subQ535=sQuery(id+"F0.wireOp",EDGE,"E46");var subQ536=sQuery(id+"F0.wireOp",EDGE,"E45");var subQ537=sQuery(id+"F0.wireOp",EDGE,"E44");var subQ538=sQuery(id+"F0.wireOp",EDGE,"E43");var subQ539=sQuery(id+"F0.wireOp",EDGE,"E42");var subQ540=sQuery(id+"F0.wireOp",EDGE,"E41");var subQ541=sQuery(id+"F0.wireOp",EDGE,"E40");var subQ542=sQuery(id+"F0.wireOp",EDGE,"E39");var subQ543=sQuery(id+"F0.wireOp",EDGE,"E38");var subQ544=sQuery(id+"F0.wireOp",EDGE,"E37");var subQ545=sQuery(id+"F0.wireOp",EDGE,"E36");var subQ546=sQuery(id+"F0.wireOp",EDGE,"E35");var subQ547=sQuery(id+"F0.wireOp",EDGE,"E34");var subQ548=sQuery(id+"F0.wireOp",EDGE,"E33");var subQ549=sQuery(id+"F0.wireOp",EDGE,"E32");var subQ550=sQuery(id+"F0.wireOp",EDGE,"E31");var subQ551=sQuery(id+"F0.wireOp",EDGE,"E30");var subQ552=sQuery(id+"F0.wireOp",EDGE,"E29");var subQ553=sQuery(id+"F0.wireOp",EDGE,"E28");var subQ554=sQuery(id+"F0.wireOp",EDGE,"E27");var subQ555=sQuery(id+"F0.wireOp",EDGE,"E26");var subQ556=sQuery(id+"F0.wireOp",EDGE,"E25");var subQ557=sQuery(id+"F0.wireOp",EDGE,"E24");var subQ558=sQuery(id+"F0.wireOp",EDGE,"E23");var subQ559=sQuery(id+"F0.wireOp",EDGE,"E22");var subQ560=sQuery(id+"F0.wireOp",EDGE,"E21");var subQ561=sQuery(id+"F0.wireOp",EDGE,"E20");var subQ562=sQuery(id+"F0.wireOp",EDGE,"E19");var subQ563=sQuery(id+"F0.wireOp",EDGE,"E18");var subQ564=sQuery(id+"F0.wireOp",EDGE,"E17");var subQ565=sQuery(id+"F0.wireOp",EDGE,"E16");var subQ566=sQuery(id+"F0.wireOp",EDGE,"E15");var subQ567=sQuery(id+"F0.wireOp",EDGE,"E14");var subQ568=sQuery(id+"F0.wireOp",EDGE,"E13");var subQ569=sQuery(id+"F0.wireOp",EDGE,"E12");var subQ570=sQuery(id+"F0.wireOp",EDGE,"E11");var subQ571=sQuery(id+"F0.wireOp",EDGE,"E10");var subQ572=sQuery(id+"F0.wireOp",EDGE,"E9");var subQ573=sQuery(id+"F0.wireOp",EDGE,"E8");var subQ574=sQuery(id+"F0.wireOp",EDGE,"E7");var subQ575=sQuery(id+"F0.wireOp",EDGE,"E6");var subQ576=sQuery(id+"F0.wireOp",EDGE,"E5");var subQ577=sQuery(id+"F0.wireOp",EDGE,"E4");var subQ578=sQuery(id+"F0.wireOp",EDGE,"E3");var subQ579=sQuery(id+"F0.wireOp",EDGE,"E2");var subQ580=sQuery(id+"F0.wireOp",EDGE,"E1");var subQ581=sQuery(id+"F0.wireOp",EDGE,"E0");Q0=makeQuery(id+"F10.boolean.opBoolean","SPLIT",FACE,{"disambiguationData":[TD([makeQuery(id+"F1.opExtrude","SWEPT_FACE",FACE,{"disambiguationData":[OSD([subQ1])]})])],"derivedFrom":makeQuery(id+"F1.opExtrude","CAP_FACE",FACE,{"disambiguationData":[OSD([subQ581,subQ580,subQ579,subQ578,subQ577,subQ576,subQ575,subQ574,subQ573,subQ572,subQ571,subQ570,subQ569,subQ568,subQ567,subQ566,subQ565,subQ564,subQ563,subQ562,subQ561,subQ560,subQ559,subQ558,subQ557,subQ556,subQ555,subQ554,subQ553,subQ552,subQ551,subQ550,subQ549,subQ548,subQ547,subQ546,subQ545,subQ544,subQ543,subQ542,subQ541,subQ540,subQ539,subQ538,subQ537,subQ536,subQ535,subQ534,subQ533,subQ532,subQ531,subQ530,subQ529,subQ528,subQ527,subQ526,subQ525,subQ524,subQ523,subQ522,subQ521,subQ520,subQ519,subQ518,subQ517,subQ516,subQ515,subQ514,subQ513,subQ512,subQ511,subQ510,subQ509,subQ508,subQ507,subQ506,subQ505,subQ504,subQ503,subQ502,subQ501,subQ500,subQ499,subQ498,subQ497,subQ496,subQ495,subQ494,subQ493,subQ492,subQ491,subQ490,subQ489,subQ488,subQ487,subQ486,subQ485,subQ484,subQ483,subQ482,subQ481,subQ480,subQ479,subQ478,subQ477,subQ476,subQ475,subQ474,subQ473,subQ472,subQ471,subQ470,subQ469,subQ468,subQ467,subQ466,subQ465,subQ464,subQ463,subQ462,subQ461,subQ460,subQ459,subQ458,subQ457,subQ456,subQ455,subQ454,subQ453,subQ452,subQ451,subQ450,subQ449,subQ448,subQ447,subQ446,subQ445,subQ444,subQ443,subQ442,subQ441,subQ440,subQ439,subQ438,subQ437,subQ436,subQ435,subQ434,subQ433,subQ432,subQ431,subQ430,subQ429,subQ428,subQ427,subQ426,subQ425,subQ424,subQ423,subQ422,subQ421,subQ420,subQ419,subQ418,subQ417,subQ416,subQ415,subQ414,subQ413,subQ412,subQ411,subQ410,subQ409,subQ408,subQ407,subQ406,subQ405,subQ404,subQ403,subQ402,subQ401,subQ400,subQ399,subQ398,subQ397,subQ396,subQ395,subQ394,subQ393,subQ392,subQ391,subQ390,subQ389,subQ388,subQ387,subQ386,subQ385,subQ384,subQ383,subQ382,subQ381,subQ380,subQ379,subQ378,subQ377,subQ376,subQ375,subQ374,subQ373,subQ372,subQ371,subQ370,subQ369,subQ368,subQ367,subQ366,subQ365,subQ364,subQ363,subQ362,subQ361,subQ360,subQ359,subQ358,subQ357,subQ356,subQ355,subQ354,subQ353,subQ352,subQ351,subQ350,subQ349,subQ348,subQ347,subQ346,subQ345,subQ344,subQ343,subQ342,subQ341,subQ340,subQ339,subQ338,subQ337,subQ336,subQ335,subQ334,subQ333,subQ332,subQ331,subQ330,subQ329,subQ328,subQ327,subQ326,subQ325,subQ324,subQ323,subQ322,subQ321,subQ320,subQ319,subQ318,subQ317,subQ316,subQ315,subQ314,subQ313,subQ312,subQ311,subQ310,subQ309,subQ308,subQ307,subQ306,subQ305,subQ304,subQ303,subQ302,subQ301,subQ300,subQ299,subQ298,subQ297,subQ296,subQ295,subQ294,subQ293,subQ292,subQ291,subQ290,subQ289,subQ288,subQ287,subQ286,subQ285,subQ284,subQ283,subQ282,subQ281,subQ280,subQ279,subQ278,subQ277,subQ276,subQ275,subQ274,subQ273,subQ272,subQ271,subQ270,subQ269,subQ268,subQ267,subQ266,subQ265,subQ264,subQ263,subQ262,subQ261,subQ260,subQ259,subQ258,subQ257,subQ256,subQ255,subQ254,subQ253,subQ252,subQ251,subQ250,subQ249,subQ248,subQ247,subQ246,subQ245,subQ244,subQ243,subQ242,subQ1,subQ0,subQ241,subQ240,subQ239,subQ238,subQ237,subQ236,subQ235,subQ234,subQ233,subQ232,subQ231,subQ230,subQ229,subQ228,subQ227,subQ226,subQ225,subQ224,subQ223,subQ222,subQ221,subQ220,subQ219,subQ218,subQ217,subQ216,subQ215,subQ214,subQ213,subQ212,subQ211,subQ210,subQ209,subQ208,subQ207,subQ206,subQ205,subQ204,subQ203,subQ202,subQ201,subQ200,subQ199,subQ198,subQ197,subQ196,subQ195,subQ194,subQ193,subQ192,subQ191,subQ190,subQ189,subQ188,subQ187,subQ186,subQ185,subQ184,subQ183,subQ182,subQ181,subQ180,subQ179,subQ178,subQ177,subQ176,subQ175,subQ174,subQ173,subQ172,subQ171,subQ170,subQ169,subQ168,subQ167,subQ166,subQ165,subQ164,subQ163,subQ162,subQ161,subQ160,subQ159,subQ158,subQ157,subQ156,subQ155,subQ154,subQ153,subQ152,subQ151,subQ150,subQ149,subQ148,subQ147,subQ146,subQ145,subQ144,subQ143,subQ142,subQ141,subQ140,subQ139,subQ138,subQ137,subQ136,subQ135,subQ134,subQ133,subQ132,subQ131,subQ130,subQ129,subQ128,subQ127,subQ126,subQ125,subQ124,subQ123,subQ122,subQ121,subQ120,subQ119,subQ118,subQ117,subQ116,subQ115,subQ114,subQ113,subQ112,subQ111,subQ110,subQ109,subQ108,subQ107,subQ106,subQ105,subQ104,subQ103,subQ102,subQ101,subQ100,subQ99,subQ98,subQ97,subQ96,subQ95,subQ94,subQ93,subQ92,subQ91,subQ90,subQ89,subQ88,subQ87,subQ86,subQ85,subQ84,subQ83,subQ82,subQ81,subQ80,subQ79,subQ78,subQ77,subQ76,subQ75,subQ74,subQ73,subQ72,subQ71,subQ70,subQ69,subQ68,subQ67,subQ66,subQ65,subQ64,subQ63,subQ62,subQ61,subQ60,subQ59,subQ58,subQ57,subQ56,subQ55,subQ54,subQ53,subQ52,subQ51,subQ50,subQ49,subQ48,subQ47,subQ46,subQ45,subQ44,subQ43,subQ42,subQ41,subQ40,subQ39,subQ38,subQ37,subQ36,subQ35,subQ34,subQ33,subQ32,subQ31,subQ30,subQ29,subQ28,subQ27,subQ26,subQ25,subQ24,subQ23,subQ22,subQ21,subQ20,subQ19,subQ18,subQ17,subQ16,subQ15,subQ14,subQ13,subQ12,subQ11,subQ10,subQ9,subQ8,subQ7,subQ6,subQ5,subQ4])],"isStart":false})});}
            var sketch = newSketch(context, id + "F18", { "sketchPlane" : qUnion([Q0])});
            skCircle(sketch, "E2048.0", {"center": v(-38.1, 0.27) * mm, "radius": 6 * mm});
            skSolve(sketch);
        }
        {
            var Q0;
            Q0 = qSketchRegion(id + "F18", true);
            var Q1;
            Q1=makeQuery(id+"F1.opExtrude","CAP_FACE",FACE,{"disambiguationData":[OSD([sQuery(id+"F0.wireOp",EDGE,"E0"),sQuery(id+"F0.wireOp",EDGE,"E1"),sQuery(id+"F0.wireOp",EDGE,"E2"),sQuery(id+"F0.wireOp",EDGE,"E3"),sQuery(id+"F0.wireOp",EDGE,"E4"),sQuery(id+"F0.wireOp",EDGE,"E5"),sQuery(id+"F0.wireOp",EDGE,"E6"),sQuery(id+"F0.wireOp",EDGE,"E7"),sQuery(id+"F0.wireOp",EDGE,"E8"),sQuery(id+"F0.wireOp",EDGE,"E9"),sQuery(id+"F0.wireOp",EDGE,"E10"),sQuery(id+"F0.wireOp",EDGE,"E11"),sQuery(id+"F0.wireOp",EDGE,"E12"),sQuery(id+"F0.wireOp",EDGE,"E13"),sQuery(id+"F0.wireOp",EDGE,"E14"),sQuery(id+"F0.wireOp",EDGE,"E15"),sQuery(id+"F0.wireOp",EDGE,"E16"),sQuery(id+"F0.wireOp",EDGE,"E17"),sQuery(id+"F0.wireOp",EDGE,"E18"),sQuery(id+"F0.wireOp",EDGE,"E19"),sQuery(id+"F0.wireOp",EDGE,"E20"),sQuery(id+"F0.wireOp",EDGE,"E21"),sQuery(id+"F0.wireOp",EDGE,"E22"),sQuery(id+"F0.wireOp",EDGE,"E23"),sQuery(id+"F0.wireOp",EDGE,"E24"),sQuery(id+"F0.wireOp",EDGE,"E25"),sQuery(id+"F0.wireOp",EDGE,"E26"),sQuery(id+"F0.wireOp",EDGE,"E27"),sQuery(id+"F0.wireOp",EDGE,"E28"),sQuery(id+"F0.wireOp",EDGE,"E29"),sQuery(id+"F0.wireOp",EDGE,"E30"),sQuery(id+"F0.wireOp",EDGE,"E31"),sQuery(id+"F0.wireOp",EDGE,"E32"),sQuery(id+"F0.wireOp",EDGE,"E33"),sQuery(id+"F0.wireOp",EDGE,"E34"),sQuery(id+"F0.wireOp",EDGE,"E35"),sQuery(id+"F0.wireOp",EDGE,"E36"),sQuery(id+"F0.wireOp",EDGE,"E37"),sQuery(id+"F0.wireOp",EDGE,"E38"),sQuery(id+"F0.wireOp",EDGE,"E39"),sQuery(id+"F0.wireOp",EDGE,"E40"),sQuery(id+"F0.wireOp",EDGE,"E41"),sQuery(id+"F0.wireOp",EDGE,"E42"),sQuery(id+"F0.wireOp",EDGE,"E43"),sQuery(id+"F0.wireOp",EDGE,"E44"),sQuery(id+"F0.wireOp",EDGE,"E45"),sQuery(id+"F0.wireOp",EDGE,"E46"),sQuery(id+"F0.wireOp",EDGE,"E47"),sQuery(id+"F0.wireOp",EDGE,"E48"),sQuery(id+"F0.wireOp",EDGE,"E49"),sQuery(id+"F0.wireOp",EDGE,"E50"),sQuery(id+"F0.wireOp",EDGE,"E51"),sQuery(id+"F0.wireOp",EDGE,"E52"),sQuery(id+"F0.wireOp",EDGE,"E53"),sQuery(id+"F0.wireOp",EDGE,"E54"),sQuery(id+"F0.wireOp",EDGE,"E55"),sQuery(id+"F0.wireOp",EDGE,"E56"),sQuery(id+"F0.wireOp",EDGE,"E57"),sQuery(id+"F0.wireOp",EDGE,"E58"),sQuery(id+"F0.wireOp",EDGE,"E59"),sQuery(id+"F0.wireOp",EDGE,"E60"),sQuery(id+"F0.wireOp",EDGE,"E61"),sQuery(id+"F0.wireOp",EDGE,"E62"),sQuery(id+"F0.wireOp",EDGE,"E63"),sQuery(id+"F0.wireOp",EDGE,"E64"),sQuery(id+"F0.wireOp",EDGE,"E65"),sQuery(id+"F0.wireOp",EDGE,"E66"),sQuery(id+"F0.wireOp",EDGE,"E67"),sQuery(id+"F0.wireOp",EDGE,"E68"),sQuery(id+"F0.wireOp",EDGE,"E69"),sQuery(id+"F0.wireOp",EDGE,"E70"),sQuery(id+"F0.wireOp",EDGE,"E71"),sQuery(id+"F0.wireOp",EDGE,"E72"),sQuery(id+"F0.wireOp",EDGE,"E73"),sQuery(id+"F0.wireOp",EDGE,"E74"),sQuery(id+"F0.wireOp",EDGE,"E75"),sQuery(id+"F0.wireOp",EDGE,"E76"),sQuery(id+"F0.wireOp",EDGE,"E77"),sQuery(id+"F0.wireOp",EDGE,"E78"),sQuery(id+"F0.wireOp",EDGE,"E79"),sQuery(id+"F0.wireOp",EDGE,"E80"),sQuery(id+"F0.wireOp",EDGE,"E81"),sQuery(id+"F0.wireOp",EDGE,"E82"),sQuery(id+"F0.wireOp",EDGE,"E83"),sQuery(id+"F0.wireOp",EDGE,"E84"),sQuery(id+"F0.wireOp",EDGE,"E85"),sQuery(id+"F0.wireOp",EDGE,"E86"),sQuery(id+"F0.wireOp",EDGE,"E87"),sQuery(id+"F0.wireOp",EDGE,"E88"),sQuery(id+"F0.wireOp",EDGE,"E89"),sQuery(id+"F0.wireOp",EDGE,"E90"),sQuery(id+"F0.wireOp",EDGE,"E91"),sQuery(id+"F0.wireOp",EDGE,"E92"),sQuery(id+"F0.wireOp",EDGE,"E93"),sQuery(id+"F0.wireOp",EDGE,"E94"),sQuery(id+"F0.wireOp",EDGE,"E95"),sQuery(id+"F0.wireOp",EDGE,"E96"),sQuery(id+"F0.wireOp",EDGE,"E97"),sQuery(id+"F0.wireOp",EDGE,"E98"),sQuery(id+"F0.wireOp",EDGE,"E99"),sQuery(id+"F0.wireOp",EDGE,"E100"),sQuery(id+"F0.wireOp",EDGE,"E101"),sQuery(id+"F0.wireOp",EDGE,"E102"),sQuery(id+"F0.wireOp",EDGE,"E103"),sQuery(id+"F0.wireOp",EDGE,"E104"),sQuery(id+"F0.wireOp",EDGE,"E105"),sQuery(id+"F0.wireOp",EDGE,"E106"),sQuery(id+"F0.wireOp",EDGE,"E107"),sQuery(id+"F0.wireOp",EDGE,"E108"),sQuery(id+"F0.wireOp",EDGE,"E109"),sQuery(id+"F0.wireOp",EDGE,"E110"),sQuery(id+"F0.wireOp",EDGE,"E111"),sQuery(id+"F0.wireOp",EDGE,"E112"),sQuery(id+"F0.wireOp",EDGE,"E113"),sQuery(id+"F0.wireOp",EDGE,"E114"),sQuery(id+"F0.wireOp",EDGE,"E115"),sQuery(id+"F0.wireOp",EDGE,"E116"),sQuery(id+"F0.wireOp",EDGE,"E117"),sQuery(id+"F0.wireOp",EDGE,"E118"),sQuery(id+"F0.wireOp",EDGE,"E119"),sQuery(id+"F0.wireOp",EDGE,"E120"),sQuery(id+"F0.wireOp",EDGE,"E121"),sQuery(id+"F0.wireOp",EDGE,"E122"),sQuery(id+"F0.wireOp",EDGE,"E123"),sQuery(id+"F0.wireOp",EDGE,"E124"),sQuery(id+"F0.wireOp",EDGE,"E125"),sQuery(id+"F0.wireOp",EDGE,"E126"),sQuery(id+"F0.wireOp",EDGE,"E127"),sQuery(id+"F0.wireOp",EDGE,"E128"),sQuery(id+"F0.wireOp",EDGE,"E129"),sQuery(id+"F0.wireOp",EDGE,"E130"),sQuery(id+"F0.wireOp",EDGE,"E131"),sQuery(id+"F0.wireOp",EDGE,"E132"),sQuery(id+"F0.wireOp",EDGE,"E133"),sQuery(id+"F0.wireOp",EDGE,"E134"),sQuery(id+"F0.wireOp",EDGE,"E135"),sQuery(id+"F0.wireOp",EDGE,"E136"),sQuery(id+"F0.wireOp",EDGE,"E137"),sQuery(id+"F0.wireOp",EDGE,"E138"),sQuery(id+"F0.wireOp",EDGE,"E139"),sQuery(id+"F0.wireOp",EDGE,"E140"),sQuery(id+"F0.wireOp",EDGE,"E141"),sQuery(id+"F0.wireOp",EDGE,"E142"),sQuery(id+"F0.wireOp",EDGE,"E143"),sQuery(id+"F0.wireOp",EDGE,"E144"),sQuery(id+"F0.wireOp",EDGE,"E145"),sQuery(id+"F0.wireOp",EDGE,"E146"),sQuery(id+"F0.wireOp",EDGE,"E147"),sQuery(id+"F0.wireOp",EDGE,"E148"),sQuery(id+"F0.wireOp",EDGE,"E149"),sQuery(id+"F0.wireOp",EDGE,"E150"),sQuery(id+"F0.wireOp",EDGE,"E151"),sQuery(id+"F0.wireOp",EDGE,"E152"),sQuery(id+"F0.wireOp",EDGE,"E153"),sQuery(id+"F0.wireOp",EDGE,"E154"),sQuery(id+"F0.wireOp",EDGE,"E155"),sQuery(id+"F0.wireOp",EDGE,"E156"),sQuery(id+"F0.wireOp",EDGE,"E157"),sQuery(id+"F0.wireOp",EDGE,"E158"),sQuery(id+"F0.wireOp",EDGE,"E159"),sQuery(id+"F0.wireOp",EDGE,"E160"),sQuery(id+"F0.wireOp",EDGE,"E161"),sQuery(id+"F0.wireOp",EDGE,"E162"),sQuery(id+"F0.wireOp",EDGE,"E163"),sQuery(id+"F0.wireOp",EDGE,"E164"),sQuery(id+"F0.wireOp",EDGE,"E165"),sQuery(id+"F0.wireOp",EDGE,"E166"),sQuery(id+"F0.wireOp",EDGE,"E167"),sQuery(id+"F0.wireOp",EDGE,"E168"),sQuery(id+"F0.wireOp",EDGE,"E169"),sQuery(id+"F0.wireOp",EDGE,"E170"),sQuery(id+"F0.wireOp",EDGE,"E171"),sQuery(id+"F0.wireOp",EDGE,"E172"),sQuery(id+"F0.wireOp",EDGE,"E173"),sQuery(id+"F0.wireOp",EDGE,"E174"),sQuery(id+"F0.wireOp",EDGE,"E175"),sQuery(id+"F0.wireOp",EDGE,"E176"),sQuery(id+"F0.wireOp",EDGE,"E177"),sQuery(id+"F0.wireOp",EDGE,"E178"),sQuery(id+"F0.wireOp",EDGE,"E179"),sQuery(id+"F0.wireOp",EDGE,"E180"),sQuery(id+"F0.wireOp",EDGE,"E181"),sQuery(id+"F0.wireOp",EDGE,"E182"),sQuery(id+"F0.wireOp",EDGE,"E183"),sQuery(id+"F0.wireOp",EDGE,"E184"),sQuery(id+"F0.wireOp",EDGE,"E185"),sQuery(id+"F0.wireOp",EDGE,"E186"),sQuery(id+"F0.wireOp",EDGE,"E187"),sQuery(id+"F0.wireOp",EDGE,"E188"),sQuery(id+"F0.wireOp",EDGE,"E189"),sQuery(id+"F0.wireOp",EDGE,"E190"),sQuery(id+"F0.wireOp",EDGE,"E191"),sQuery(id+"F0.wireOp",EDGE,"E192"),sQuery(id+"F0.wireOp",EDGE,"E193"),sQuery(id+"F0.wireOp",EDGE,"E194"),sQuery(id+"F0.wireOp",EDGE,"E195"),sQuery(id+"F0.wireOp",EDGE,"E196"),sQuery(id+"F0.wireOp",EDGE,"E197"),sQuery(id+"F0.wireOp",EDGE,"E198"),sQuery(id+"F0.wireOp",EDGE,"E199"),sQuery(id+"F0.wireOp",EDGE,"E200"),sQuery(id+"F0.wireOp",EDGE,"E201"),sQuery(id+"F0.wireOp",EDGE,"E202"),sQuery(id+"F0.wireOp",EDGE,"E203"),sQuery(id+"F0.wireOp",EDGE,"E204"),sQuery(id+"F0.wireOp",EDGE,"E205"),sQuery(id+"F0.wireOp",EDGE,"E206"),sQuery(id+"F0.wireOp",EDGE,"E207"),sQuery(id+"F0.wireOp",EDGE,"E208"),sQuery(id+"F0.wireOp",EDGE,"E209"),sQuery(id+"F0.wireOp",EDGE,"E210"),sQuery(id+"F0.wireOp",EDGE,"E211"),sQuery(id+"F0.wireOp",EDGE,"E212"),sQuery(id+"F0.wireOp",EDGE,"E213"),sQuery(id+"F0.wireOp",EDGE,"E214"),sQuery(id+"F0.wireOp",EDGE,"E215"),sQuery(id+"F0.wireOp",EDGE,"E216"),sQuery(id+"F0.wireOp",EDGE,"E217"),sQuery(id+"F0.wireOp",EDGE,"E218"),sQuery(id+"F0.wireOp",EDGE,"E219"),sQuery(id+"F0.wireOp",EDGE,"E220"),sQuery(id+"F0.wireOp",EDGE,"E221"),sQuery(id+"F0.wireOp",EDGE,"E222"),sQuery(id+"F0.wireOp",EDGE,"E223"),sQuery(id+"F0.wireOp",EDGE,"E224"),sQuery(id+"F0.wireOp",EDGE,"E225"),sQuery(id+"F0.wireOp",EDGE,"E226"),sQuery(id+"F0.wireOp",EDGE,"E227"),sQuery(id+"F0.wireOp",EDGE,"E228"),sQuery(id+"F0.wireOp",EDGE,"E229"),sQuery(id+"F0.wireOp",EDGE,"E230"),sQuery(id+"F0.wireOp",EDGE,"E231"),sQuery(id+"F0.wireOp",EDGE,"E232"),sQuery(id+"F0.wireOp",EDGE,"E233"),sQuery(id+"F0.wireOp",EDGE,"E234"),sQuery(id+"F0.wireOp",EDGE,"E235"),sQuery(id+"F0.wireOp",EDGE,"E236"),sQuery(id+"F0.wireOp",EDGE,"E237"),sQuery(id+"F0.wireOp",EDGE,"E238"),sQuery(id+"F0.wireOp",EDGE,"E239"),sQuery(id+"F0.wireOp",EDGE,"E240"),sQuery(id+"F0.wireOp",EDGE,"E241"),sQuery(id+"F0.wireOp",EDGE,"E242"),sQuery(id+"F0.wireOp",EDGE,"E243"),sQuery(id+"F0.wireOp",EDGE,"E244"),sQuery(id+"F0.wireOp",EDGE,"E245"),sQuery(id+"F0.wireOp",EDGE,"E246"),sQuery(id+"F0.wireOp",EDGE,"E247"),sQuery(id+"F0.wireOp",EDGE,"E248"),sQuery(id+"F0.wireOp",EDGE,"E249"),sQuery(id+"F0.wireOp",EDGE,"E250"),sQuery(id+"F0.wireOp",EDGE,"E251"),sQuery(id+"F0.wireOp",EDGE,"E252"),sQuery(id+"F0.wireOp",EDGE,"E253"),sQuery(id+"F0.wireOp",EDGE,"E254"),sQuery(id+"F0.wireOp",EDGE,"E255"),sQuery(id+"F0.wireOp",EDGE,"E256"),sQuery(id+"F0.wireOp",EDGE,"E257"),sQuery(id+"F0.wireOp",EDGE,"E258"),sQuery(id+"F0.wireOp",EDGE,"E259"),sQuery(id+"F0.wireOp",EDGE,"E260"),sQuery(id+"F0.wireOp",EDGE,"E261"),sQuery(id+"F0.wireOp",EDGE,"E262"),sQuery(id+"F0.wireOp",EDGE,"E263"),sQuery(id+"F0.wireOp",EDGE,"E264"),sQuery(id+"F0.wireOp",EDGE,"E265"),sQuery(id+"F0.wireOp",EDGE,"E266"),sQuery(id+"F0.wireOp",EDGE,"E267"),sQuery(id+"F0.wireOp",EDGE,"E268"),sQuery(id+"F0.wireOp",EDGE,"E269"),sQuery(id+"F0.wireOp",EDGE,"E270"),sQuery(id+"F0.wireOp",EDGE,"E271"),sQuery(id+"F0.wireOp",EDGE,"E272"),sQuery(id+"F0.wireOp",EDGE,"E273"),sQuery(id+"F0.wireOp",EDGE,"E274"),sQuery(id+"F0.wireOp",EDGE,"E275"),sQuery(id+"F0.wireOp",EDGE,"E276"),sQuery(id+"F0.wireOp",EDGE,"E277"),sQuery(id+"F0.wireOp",EDGE,"E278"),sQuery(id+"F0.wireOp",EDGE,"E279"),sQuery(id+"F0.wireOp",EDGE,"E280"),sQuery(id+"F0.wireOp",EDGE,"E281"),sQuery(id+"F0.wireOp",EDGE,"E282"),sQuery(id+"F0.wireOp",EDGE,"E283"),sQuery(id+"F0.wireOp",EDGE,"E284"),sQuery(id+"F0.wireOp",EDGE,"E285"),sQuery(id+"F0.wireOp",EDGE,"E286"),sQuery(id+"F0.wireOp",EDGE,"E287"),sQuery(id+"F0.wireOp",EDGE,"E288"),sQuery(id+"F0.wireOp",EDGE,"E289"),sQuery(id+"F0.wireOp",EDGE,"E290"),sQuery(id+"F0.wireOp",EDGE,"E291"),sQuery(id+"F0.wireOp",EDGE,"E292"),sQuery(id+"F0.wireOp",EDGE,"E293"),sQuery(id+"F0.wireOp",EDGE,"E294"),sQuery(id+"F0.wireOp",EDGE,"E295"),sQuery(id+"F0.wireOp",EDGE,"E296"),sQuery(id+"F0.wireOp",EDGE,"E297"),sQuery(id+"F0.wireOp",EDGE,"E298"),sQuery(id+"F0.wireOp",EDGE,"E299"),sQuery(id+"F0.wireOp",EDGE,"E300"),sQuery(id+"F0.wireOp",EDGE,"E301"),sQuery(id+"F0.wireOp",EDGE,"E302"),sQuery(id+"F0.wireOp",EDGE,"E303"),sQuery(id+"F0.wireOp",EDGE,"E304"),sQuery(id+"F0.wireOp",EDGE,"E305"),sQuery(id+"F0.wireOp",EDGE,"E306"),sQuery(id+"F0.wireOp",EDGE,"E307"),sQuery(id+"F0.wireOp",EDGE,"E308"),sQuery(id+"F0.wireOp",EDGE,"E309"),sQuery(id+"F0.wireOp",EDGE,"E310"),sQuery(id+"F0.wireOp",EDGE,"E311"),sQuery(id+"F0.wireOp",EDGE,"E312"),sQuery(id+"F0.wireOp",EDGE,"E313"),sQuery(id+"F0.wireOp",EDGE,"E314"),sQuery(id+"F0.wireOp",EDGE,"E315"),sQuery(id+"F0.wireOp",EDGE,"E316"),sQuery(id+"F0.wireOp",EDGE,"E317"),sQuery(id+"F0.wireOp",EDGE,"E318"),sQuery(id+"F0.wireOp",EDGE,"E319"),sQuery(id+"F0.wireOp",EDGE,"E320"),sQuery(id+"F0.wireOp",EDGE,"E321"),sQuery(id+"F0.wireOp",EDGE,"E322"),sQuery(id+"F0.wireOp",EDGE,"E323"),sQuery(id+"F0.wireOp",EDGE,"E324"),sQuery(id+"F0.wireOp",EDGE,"E325"),sQuery(id+"F0.wireOp",EDGE,"E326"),sQuery(id+"F0.wireOp",EDGE,"E327"),sQuery(id+"F0.wireOp",EDGE,"E328"),sQuery(id+"F0.wireOp",EDGE,"E329"),sQuery(id+"F0.wireOp",EDGE,"E330"),sQuery(id+"F0.wireOp",EDGE,"E331"),sQuery(id+"F0.wireOp",EDGE,"E332"),sQuery(id+"F0.wireOp",EDGE,"E333"),sQuery(id+"F0.wireOp",EDGE,"E334"),sQuery(id+"F0.wireOp",EDGE,"E335"),sQuery(id+"F0.wireOp",EDGE,"E336"),sQuery(id+"F0.wireOp",EDGE,"E337"),sQuery(id+"F0.wireOp",EDGE,"E338"),sQuery(id+"F0.wireOp",EDGE,"E339"),sQuery(id+"F0.wireOp",EDGE,"E340"),sQuery(id+"F0.wireOp",EDGE,"E341"),sQuery(id+"F0.wireOp",EDGE,"E342"),sQuery(id+"F0.wireOp",EDGE,"E343"),sQuery(id+"F0.wireOp",EDGE,"E344"),sQuery(id+"F0.wireOp",EDGE,"E345"),sQuery(id+"F0.wireOp",EDGE,"E346"),sQuery(id+"F0.wireOp",EDGE,"E347"),sQuery(id+"F0.wireOp",EDGE,"E348"),sQuery(id+"F0.wireOp",EDGE,"E349"),sQuery(id+"F0.wireOp",EDGE,"E350"),sQuery(id+"F0.wireOp",EDGE,"E351"),sQuery(id+"F0.wireOp",EDGE,"E352"),sQuery(id+"F0.wireOp",EDGE,"E353"),sQuery(id+"F0.wireOp",EDGE,"E354"),sQuery(id+"F0.wireOp",EDGE,"E355"),sQuery(id+"F0.wireOp",EDGE,"E356"),sQuery(id+"F0.wireOp",EDGE,"E357"),sQuery(id+"F0.wireOp",EDGE,"E358"),sQuery(id+"F0.wireOp",EDGE,"E359"),sQuery(id+"F0.wireOp",EDGE,"E360"),sQuery(id+"F0.wireOp",EDGE,"E361"),sQuery(id+"F0.wireOp",EDGE,"E362"),sQuery(id+"F0.wireOp",EDGE,"E363"),sQuery(id+"F0.wireOp",EDGE,"E364"),sQuery(id+"F0.wireOp",EDGE,"E365"),sQuery(id+"F0.wireOp",EDGE,"E366"),sQuery(id+"F0.wireOp",EDGE,"E367"),sQuery(id+"F0.wireOp",EDGE,"E368"),sQuery(id+"F0.wireOp",EDGE,"E369"),sQuery(id+"F0.wireOp",EDGE,"E370"),sQuery(id+"F0.wireOp",EDGE,"E371"),sQuery(id+"F0.wireOp",EDGE,"E372"),sQuery(id+"F0.wireOp",EDGE,"E373"),sQuery(id+"F0.wireOp",EDGE,"E374"),sQuery(id+"F0.wireOp",EDGE,"E375"),sQuery(id+"F0.wireOp",EDGE,"E376"),sQuery(id+"F0.wireOp",EDGE,"E377"),sQuery(id+"F0.wireOp",EDGE,"E378"),sQuery(id+"F0.wireOp",EDGE,"E379"),sQuery(id+"F0.wireOp",EDGE,"E380"),sQuery(id+"F0.wireOp",EDGE,"E381"),sQuery(id+"F0.wireOp",EDGE,"E382"),sQuery(id+"F0.wireOp",EDGE,"E383"),sQuery(id+"F0.wireOp",EDGE,"E384"),sQuery(id+"F0.wireOp",EDGE,"E385"),sQuery(id+"F0.wireOp",EDGE,"E386"),sQuery(id+"F0.wireOp",EDGE,"E387"),sQuery(id+"F0.wireOp",EDGE,"E388"),sQuery(id+"F0.wireOp",EDGE,"E389"),sQuery(id+"F0.wireOp",EDGE,"E390"),sQuery(id+"F0.wireOp",EDGE,"E391"),sQuery(id+"F0.wireOp",EDGE,"E392"),sQuery(id+"F0.wireOp",EDGE,"E393"),sQuery(id+"F0.wireOp",EDGE,"E394"),sQuery(id+"F0.wireOp",EDGE,"E395"),sQuery(id+"F0.wireOp",EDGE,"E396"),sQuery(id+"F0.wireOp",EDGE,"E397"),sQuery(id+"F0.wireOp",EDGE,"E398"),sQuery(id+"F0.wireOp",EDGE,"E399"),sQuery(id+"F0.wireOp",EDGE,"E400"),sQuery(id+"F0.wireOp",EDGE,"E401"),sQuery(id+"F0.wireOp",EDGE,"E402"),sQuery(id+"F0.wireOp",EDGE,"E403"),sQuery(id+"F0.wireOp",EDGE,"E404"),sQuery(id+"F0.wireOp",EDGE,"E405"),sQuery(id+"F0.wireOp",EDGE,"E406"),sQuery(id+"F0.wireOp",EDGE,"E407"),sQuery(id+"F0.wireOp",EDGE,"E408"),sQuery(id+"F0.wireOp",EDGE,"E409"),sQuery(id+"F0.wireOp",EDGE,"E410"),sQuery(id+"F0.wireOp",EDGE,"E411"),sQuery(id+"F0.wireOp",EDGE,"E412"),sQuery(id+"F0.wireOp",EDGE,"E413"),sQuery(id+"F0.wireOp",EDGE,"E414"),sQuery(id+"F0.wireOp",EDGE,"E415"),sQuery(id+"F0.wireOp",EDGE,"E416"),sQuery(id+"F0.wireOp",EDGE,"E417"),sQuery(id+"F0.wireOp",EDGE,"E418"),sQuery(id+"F0.wireOp",EDGE,"E419"),sQuery(id+"F0.wireOp",EDGE,"E420"),sQuery(id+"F0.wireOp",EDGE,"E421"),sQuery(id+"F0.wireOp",EDGE,"E422"),sQuery(id+"F0.wireOp",EDGE,"E423"),sQuery(id+"F0.wireOp",EDGE,"E424"),sQuery(id+"F0.wireOp",EDGE,"E425"),sQuery(id+"F0.wireOp",EDGE,"E426"),sQuery(id+"F0.wireOp",EDGE,"E427"),sQuery(id+"F0.wireOp",EDGE,"E428"),sQuery(id+"F0.wireOp",EDGE,"E429"),sQuery(id+"F0.wireOp",EDGE,"E430"),sQuery(id+"F0.wireOp",EDGE,"E431"),sQuery(id+"F0.wireOp",EDGE,"E432"),sQuery(id+"F0.wireOp",EDGE,"E433"),sQuery(id+"F0.wireOp",EDGE,"E434"),sQuery(id+"F0.wireOp",EDGE,"E435"),sQuery(id+"F0.wireOp",EDGE,"E436"),sQuery(id+"F0.wireOp",EDGE,"E437"),sQuery(id+"F0.wireOp",EDGE,"E438"),sQuery(id+"F0.wireOp",EDGE,"E439"),sQuery(id+"F0.wireOp",EDGE,"E440"),sQuery(id+"F0.wireOp",EDGE,"E441"),sQuery(id+"F0.wireOp",EDGE,"E442"),sQuery(id+"F0.wireOp",EDGE,"E443"),sQuery(id+"F0.wireOp",EDGE,"E444"),sQuery(id+"F0.wireOp",EDGE,"E445"),sQuery(id+"F0.wireOp",EDGE,"E446"),sQuery(id+"F0.wireOp",EDGE,"E447"),sQuery(id+"F0.wireOp",EDGE,"E448"),sQuery(id+"F0.wireOp",EDGE,"E449"),sQuery(id+"F0.wireOp",EDGE,"E450"),sQuery(id+"F0.wireOp",EDGE,"E451"),sQuery(id+"F0.wireOp",EDGE,"E452"),sQuery(id+"F0.wireOp",EDGE,"E453"),sQuery(id+"F0.wireOp",EDGE,"E454"),sQuery(id+"F0.wireOp",EDGE,"E455"),sQuery(id+"F0.wireOp",EDGE,"E456"),sQuery(id+"F0.wireOp",EDGE,"E457"),sQuery(id+"F0.wireOp",EDGE,"E458"),sQuery(id+"F0.wireOp",EDGE,"E459"),sQuery(id+"F0.wireOp",EDGE,"E460"),sQuery(id+"F0.wireOp",EDGE,"E461"),sQuery(id+"F0.wireOp",EDGE,"E462"),sQuery(id+"F0.wireOp",EDGE,"E463"),sQuery(id+"F0.wireOp",EDGE,"E464"),sQuery(id+"F0.wireOp",EDGE,"E465"),sQuery(id+"F0.wireOp",EDGE,"E466"),sQuery(id+"F0.wireOp",EDGE,"E467"),sQuery(id+"F0.wireOp",EDGE,"E468"),sQuery(id+"F0.wireOp",EDGE,"E469"),sQuery(id+"F0.wireOp",EDGE,"E470"),sQuery(id+"F0.wireOp",EDGE,"E471"),sQuery(id+"F0.wireOp",EDGE,"E472"),sQuery(id+"F0.wireOp",EDGE,"E473"),sQuery(id+"F0.wireOp",EDGE,"E474"),sQuery(id+"F0.wireOp",EDGE,"E475"),sQuery(id+"F0.wireOp",EDGE,"E476"),sQuery(id+"F0.wireOp",EDGE,"E477"),sQuery(id+"F0.wireOp",EDGE,"E478"),sQuery(id+"F0.wireOp",EDGE,"E479"),sQuery(id+"F0.wireOp",EDGE,"E480"),sQuery(id+"F0.wireOp",EDGE,"E481"),sQuery(id+"F0.wireOp",EDGE,"E482"),sQuery(id+"F0.wireOp",EDGE,"E483"),sQuery(id+"F0.wireOp",EDGE,"E484"),sQuery(id+"F0.wireOp",EDGE,"E485"),sQuery(id+"F0.wireOp",EDGE,"E486"),sQuery(id+"F0.wireOp",EDGE,"E487"),sQuery(id+"F0.wireOp",EDGE,"E488"),sQuery(id+"F0.wireOp",EDGE,"E489"),sQuery(id+"F0.wireOp",EDGE,"E490"),sQuery(id+"F0.wireOp",EDGE,"E491"),sQuery(id+"F0.wireOp",EDGE,"E492"),sQuery(id+"F0.wireOp",EDGE,"E493"),sQuery(id+"F0.wireOp",EDGE,"E494"),sQuery(id+"F0.wireOp",EDGE,"E495"),sQuery(id+"F0.wireOp",EDGE,"E496"),sQuery(id+"F0.wireOp",EDGE,"E497"),sQuery(id+"F0.wireOp",EDGE,"E498"),sQuery(id+"F0.wireOp",EDGE,"E499"),sQuery(id+"F0.wireOp",EDGE,"E500"),sQuery(id+"F0.wireOp",EDGE,"E501"),sQuery(id+"F0.wireOp",EDGE,"E502"),sQuery(id+"F0.wireOp",EDGE,"E503"),sQuery(id+"F0.wireOp",EDGE,"E504"),sQuery(id+"F0.wireOp",EDGE,"E505"),sQuery(id+"F0.wireOp",EDGE,"E506"),sQuery(id+"F0.wireOp",EDGE,"E507"),sQuery(id+"F0.wireOp",EDGE,"E508"),sQuery(id+"F0.wireOp",EDGE,"E509"),sQuery(id+"F0.wireOp",EDGE,"E510"),sQuery(id+"F0.wireOp",EDGE,"E511"),sQuery(id+"F0.wireOp",EDGE,"E512"),sQuery(id+"F0.wireOp",EDGE,"E513"),sQuery(id+"F0.wireOp",EDGE,"E514"),sQuery(id+"F0.wireOp",EDGE,"E515"),sQuery(id+"F0.wireOp",EDGE,"E516"),sQuery(id+"F0.wireOp",EDGE,"E517"),sQuery(id+"F0.wireOp",EDGE,"E518"),sQuery(id+"F0.wireOp",EDGE,"E519"),sQuery(id+"F0.wireOp",EDGE,"E520"),sQuery(id+"F0.wireOp",EDGE,"E521"),sQuery(id+"F0.wireOp",EDGE,"E522"),sQuery(id+"F0.wireOp",EDGE,"E523"),sQuery(id+"F0.wireOp",EDGE,"E524"),sQuery(id+"F0.wireOp",EDGE,"E525"),sQuery(id+"F0.wireOp",EDGE,"E526"),sQuery(id+"F0.wireOp",EDGE,"E527"),sQuery(id+"F0.wireOp",EDGE,"E528"),sQuery(id+"F0.wireOp",EDGE,"E529"),sQuery(id+"F0.wireOp",EDGE,"E530"),sQuery(id+"F0.wireOp",EDGE,"E531"),sQuery(id+"F0.wireOp",EDGE,"E532"),sQuery(id+"F0.wireOp",EDGE,"E533"),sQuery(id+"F0.wireOp",EDGE,"E534"),sQuery(id+"F0.wireOp",EDGE,"E535"),sQuery(id+"F0.wireOp",EDGE,"E536"),sQuery(id+"F0.wireOp",EDGE,"E537"),sQuery(id+"F0.wireOp",EDGE,"E538"),sQuery(id+"F0.wireOp",EDGE,"E539"),sQuery(id+"F0.wireOp",EDGE,"E540"),sQuery(id+"F0.wireOp",EDGE,"E541"),sQuery(id+"F0.wireOp",EDGE,"E542"),sQuery(id+"F0.wireOp",EDGE,"E543"),sQuery(id+"F0.wireOp",EDGE,"E544"),sQuery(id+"F0.wireOp",EDGE,"E545"),sQuery(id+"F0.wireOp",EDGE,"E546"),sQuery(id+"F0.wireOp",EDGE,"E547"),sQuery(id+"F0.wireOp",EDGE,"E548"),sQuery(id+"F0.wireOp",EDGE,"E549"),sQuery(id+"F0.wireOp",EDGE,"E550"),sQuery(id+"F0.wireOp",EDGE,"E551"),sQuery(id+"F0.wireOp",EDGE,"E552"),sQuery(id+"F0.wireOp",EDGE,"E553"),sQuery(id+"F0.wireOp",EDGE,"E554"),sQuery(id+"F0.wireOp",EDGE,"E555"),sQuery(id+"F0.wireOp",EDGE,"E556"),sQuery(id+"F0.wireOp",EDGE,"E557"),sQuery(id+"F0.wireOp",EDGE,"E558"),sQuery(id+"F0.wireOp",EDGE,"E559"),sQuery(id+"F0.wireOp",EDGE,"E560"),sQuery(id+"F0.wireOp",EDGE,"E561"),sQuery(id+"F0.wireOp",EDGE,"E562"),sQuery(id+"F0.wireOp",EDGE,"E563"),sQuery(id+"F0.wireOp",EDGE,"E564"),sQuery(id+"F0.wireOp",EDGE,"E565"),sQuery(id+"F0.wireOp",EDGE,"E566"),sQuery(id+"F0.wireOp",EDGE,"E567"),sQuery(id+"F0.wireOp",EDGE,"E568"),sQuery(id+"F0.wireOp",EDGE,"E569"),sQuery(id+"F0.wireOp",EDGE,"E570"),sQuery(id+"F0.wireOp",EDGE,"E571"),sQuery(id+"F0.wireOp",EDGE,"E572"),sQuery(id+"F0.wireOp",EDGE,"E573"),sQuery(id+"F0.wireOp",EDGE,"E574"),sQuery(id+"F0.wireOp",EDGE,"E575"),sQuery(id+"F0.wireOp",EDGE,"E576"),sQuery(id+"F0.wireOp",EDGE,"E577"),sQuery(id+"F0.wireOp",EDGE,"E1140"),sQuery(id+"F0.wireOp",EDGE,"E1143")])],"isStart":true});
            extrude(context, id + "F19", {"entities" : qUnion([Q0]), "operationType" : NewBodyOperationType.ADD, "endBound" : BoundingType.UP_TO_SURFACE, "oppositeDirection" : true, "depth" : 25 * mm, "endBoundEntityFace" : qUnion([Q1]), "offsetDistance" : 25 * mm});
        }
        {
            var Q0;
            {var subQ0=sQuery(id+"F0.wireOp",EDGE,"E341");var subQ1=sQuery(id+"F0.wireOp",EDGE,"E340");var subQ4=sQuery(id+"F0.wireOp",EDGE,"E1143");var subQ5=sQuery(id+"F0.wireOp",EDGE,"E1140");var subQ6=sQuery(id+"F0.wireOp",EDGE,"E577");var subQ7=sQuery(id+"F0.wireOp",EDGE,"E576");var subQ8=sQuery(id+"F0.wireOp",EDGE,"E575");var subQ9=sQuery(id+"F0.wireOp",EDGE,"E574");var subQ10=sQuery(id+"F0.wireOp",EDGE,"E573");var subQ11=sQuery(id+"F0.wireOp",EDGE,"E572");var subQ12=sQuery(id+"F0.wireOp",EDGE,"E571");var subQ13=sQuery(id+"F0.wireOp",EDGE,"E570");var subQ14=sQuery(id+"F0.wireOp",EDGE,"E569");var subQ15=sQuery(id+"F0.wireOp",EDGE,"E568");var subQ16=sQuery(id+"F0.wireOp",EDGE,"E567");var subQ17=sQuery(id+"F0.wireOp",EDGE,"E566");var subQ18=sQuery(id+"F0.wireOp",EDGE,"E565");var subQ19=sQuery(id+"F0.wireOp",EDGE,"E564");var subQ20=sQuery(id+"F0.wireOp",EDGE,"E563");var subQ21=sQuery(id+"F0.wireOp",EDGE,"E562");var subQ22=sQuery(id+"F0.wireOp",EDGE,"E561");var subQ23=sQuery(id+"F0.wireOp",EDGE,"E560");var subQ24=sQuery(id+"F0.wireOp",EDGE,"E559");var subQ25=sQuery(id+"F0.wireOp",EDGE,"E558");var subQ26=sQuery(id+"F0.wireOp",EDGE,"E557");var subQ27=sQuery(id+"F0.wireOp",EDGE,"E556");var subQ28=sQuery(id+"F0.wireOp",EDGE,"E555");var subQ29=sQuery(id+"F0.wireOp",EDGE,"E554");var subQ30=sQuery(id+"F0.wireOp",EDGE,"E553");var subQ31=sQuery(id+"F0.wireOp",EDGE,"E552");var subQ32=sQuery(id+"F0.wireOp",EDGE,"E551");var subQ33=sQuery(id+"F0.wireOp",EDGE,"E550");var subQ34=sQuery(id+"F0.wireOp",EDGE,"E549");var subQ35=sQuery(id+"F0.wireOp",EDGE,"E548");var subQ36=sQuery(id+"F0.wireOp",EDGE,"E547");var subQ37=sQuery(id+"F0.wireOp",EDGE,"E546");var subQ38=sQuery(id+"F0.wireOp",EDGE,"E545");var subQ39=sQuery(id+"F0.wireOp",EDGE,"E544");var subQ40=sQuery(id+"F0.wireOp",EDGE,"E543");var subQ41=sQuery(id+"F0.wireOp",EDGE,"E542");var subQ42=sQuery(id+"F0.wireOp",EDGE,"E541");var subQ43=sQuery(id+"F0.wireOp",EDGE,"E540");var subQ44=sQuery(id+"F0.wireOp",EDGE,"E539");var subQ45=sQuery(id+"F0.wireOp",EDGE,"E538");var subQ46=sQuery(id+"F0.wireOp",EDGE,"E537");var subQ47=sQuery(id+"F0.wireOp",EDGE,"E536");var subQ48=sQuery(id+"F0.wireOp",EDGE,"E535");var subQ49=sQuery(id+"F0.wireOp",EDGE,"E534");var subQ50=sQuery(id+"F0.wireOp",EDGE,"E533");var subQ51=sQuery(id+"F0.wireOp",EDGE,"E532");var subQ52=sQuery(id+"F0.wireOp",EDGE,"E531");var subQ53=sQuery(id+"F0.wireOp",EDGE,"E530");var subQ54=sQuery(id+"F0.wireOp",EDGE,"E529");var subQ55=sQuery(id+"F0.wireOp",EDGE,"E528");var subQ56=sQuery(id+"F0.wireOp",EDGE,"E527");var subQ57=sQuery(id+"F0.wireOp",EDGE,"E526");var subQ58=sQuery(id+"F0.wireOp",EDGE,"E525");var subQ59=sQuery(id+"F0.wireOp",EDGE,"E524");var subQ60=sQuery(id+"F0.wireOp",EDGE,"E523");var subQ61=sQuery(id+"F0.wireOp",EDGE,"E522");var subQ62=sQuery(id+"F0.wireOp",EDGE,"E521");var subQ63=sQuery(id+"F0.wireOp",EDGE,"E520");var subQ64=sQuery(id+"F0.wireOp",EDGE,"E519");var subQ65=sQuery(id+"F0.wireOp",EDGE,"E518");var subQ66=sQuery(id+"F0.wireOp",EDGE,"E517");var subQ67=sQuery(id+"F0.wireOp",EDGE,"E516");var subQ68=sQuery(id+"F0.wireOp",EDGE,"E515");var subQ69=sQuery(id+"F0.wireOp",EDGE,"E514");var subQ70=sQuery(id+"F0.wireOp",EDGE,"E513");var subQ71=sQuery(id+"F0.wireOp",EDGE,"E512");var subQ72=sQuery(id+"F0.wireOp",EDGE,"E511");var subQ73=sQuery(id+"F0.wireOp",EDGE,"E510");var subQ74=sQuery(id+"F0.wireOp",EDGE,"E509");var subQ75=sQuery(id+"F0.wireOp",EDGE,"E508");var subQ76=sQuery(id+"F0.wireOp",EDGE,"E507");var subQ77=sQuery(id+"F0.wireOp",EDGE,"E506");var subQ78=sQuery(id+"F0.wireOp",EDGE,"E505");var subQ79=sQuery(id+"F0.wireOp",EDGE,"E504");var subQ80=sQuery(id+"F0.wireOp",EDGE,"E503");var subQ81=sQuery(id+"F0.wireOp",EDGE,"E502");var subQ82=sQuery(id+"F0.wireOp",EDGE,"E501");var subQ83=sQuery(id+"F0.wireOp",EDGE,"E500");var subQ84=sQuery(id+"F0.wireOp",EDGE,"E499");var subQ85=sQuery(id+"F0.wireOp",EDGE,"E498");var subQ86=sQuery(id+"F0.wireOp",EDGE,"E497");var subQ87=sQuery(id+"F0.wireOp",EDGE,"E496");var subQ88=sQuery(id+"F0.wireOp",EDGE,"E495");var subQ89=sQuery(id+"F0.wireOp",EDGE,"E494");var subQ90=sQuery(id+"F0.wireOp",EDGE,"E493");var subQ91=sQuery(id+"F0.wireOp",EDGE,"E492");var subQ92=sQuery(id+"F0.wireOp",EDGE,"E491");var subQ93=sQuery(id+"F0.wireOp",EDGE,"E490");var subQ94=sQuery(id+"F0.wireOp",EDGE,"E489");var subQ95=sQuery(id+"F0.wireOp",EDGE,"E488");var subQ96=sQuery(id+"F0.wireOp",EDGE,"E487");var subQ97=sQuery(id+"F0.wireOp",EDGE,"E486");var subQ98=sQuery(id+"F0.wireOp",EDGE,"E485");var subQ99=sQuery(id+"F0.wireOp",EDGE,"E484");var subQ100=sQuery(id+"F0.wireOp",EDGE,"E483");var subQ101=sQuery(id+"F0.wireOp",EDGE,"E482");var subQ102=sQuery(id+"F0.wireOp",EDGE,"E481");var subQ103=sQuery(id+"F0.wireOp",EDGE,"E480");var subQ104=sQuery(id+"F0.wireOp",EDGE,"E479");var subQ105=sQuery(id+"F0.wireOp",EDGE,"E478");var subQ106=sQuery(id+"F0.wireOp",EDGE,"E477");var subQ107=sQuery(id+"F0.wireOp",EDGE,"E476");var subQ108=sQuery(id+"F0.wireOp",EDGE,"E475");var subQ109=sQuery(id+"F0.wireOp",EDGE,"E474");var subQ110=sQuery(id+"F0.wireOp",EDGE,"E473");var subQ111=sQuery(id+"F0.wireOp",EDGE,"E472");var subQ112=sQuery(id+"F0.wireOp",EDGE,"E471");var subQ113=sQuery(id+"F0.wireOp",EDGE,"E470");var subQ114=sQuery(id+"F0.wireOp",EDGE,"E469");var subQ115=sQuery(id+"F0.wireOp",EDGE,"E468");var subQ116=sQuery(id+"F0.wireOp",EDGE,"E467");var subQ117=sQuery(id+"F0.wireOp",EDGE,"E466");var subQ118=sQuery(id+"F0.wireOp",EDGE,"E465");var subQ119=sQuery(id+"F0.wireOp",EDGE,"E464");var subQ120=sQuery(id+"F0.wireOp",EDGE,"E463");var subQ121=sQuery(id+"F0.wireOp",EDGE,"E462");var subQ122=sQuery(id+"F0.wireOp",EDGE,"E461");var subQ123=sQuery(id+"F0.wireOp",EDGE,"E460");var subQ124=sQuery(id+"F0.wireOp",EDGE,"E459");var subQ125=sQuery(id+"F0.wireOp",EDGE,"E458");var subQ126=sQuery(id+"F0.wireOp",EDGE,"E457");var subQ127=sQuery(id+"F0.wireOp",EDGE,"E456");var subQ128=sQuery(id+"F0.wireOp",EDGE,"E455");var subQ129=sQuery(id+"F0.wireOp",EDGE,"E454");var subQ130=sQuery(id+"F0.wireOp",EDGE,"E453");var subQ131=sQuery(id+"F0.wireOp",EDGE,"E452");var subQ132=sQuery(id+"F0.wireOp",EDGE,"E451");var subQ133=sQuery(id+"F0.wireOp",EDGE,"E450");var subQ134=sQuery(id+"F0.wireOp",EDGE,"E449");var subQ135=sQuery(id+"F0.wireOp",EDGE,"E448");var subQ136=sQuery(id+"F0.wireOp",EDGE,"E447");var subQ137=sQuery(id+"F0.wireOp",EDGE,"E446");var subQ138=sQuery(id+"F0.wireOp",EDGE,"E445");var subQ139=sQuery(id+"F0.wireOp",EDGE,"E444");var subQ140=sQuery(id+"F0.wireOp",EDGE,"E443");var subQ141=sQuery(id+"F0.wireOp",EDGE,"E442");var subQ142=sQuery(id+"F0.wireOp",EDGE,"E441");var subQ143=sQuery(id+"F0.wireOp",EDGE,"E440");var subQ144=sQuery(id+"F0.wireOp",EDGE,"E439");var subQ145=sQuery(id+"F0.wireOp",EDGE,"E438");var subQ146=sQuery(id+"F0.wireOp",EDGE,"E437");var subQ147=sQuery(id+"F0.wireOp",EDGE,"E436");var subQ148=sQuery(id+"F0.wireOp",EDGE,"E435");var subQ149=sQuery(id+"F0.wireOp",EDGE,"E434");var subQ150=sQuery(id+"F0.wireOp",EDGE,"E433");var subQ151=sQuery(id+"F0.wireOp",EDGE,"E432");var subQ152=sQuery(id+"F0.wireOp",EDGE,"E431");var subQ153=sQuery(id+"F0.wireOp",EDGE,"E430");var subQ154=sQuery(id+"F0.wireOp",EDGE,"E429");var subQ155=sQuery(id+"F0.wireOp",EDGE,"E428");var subQ156=sQuery(id+"F0.wireOp",EDGE,"E427");var subQ157=sQuery(id+"F0.wireOp",EDGE,"E426");var subQ158=sQuery(id+"F0.wireOp",EDGE,"E425");var subQ159=sQuery(id+"F0.wireOp",EDGE,"E424");var subQ160=sQuery(id+"F0.wireOp",EDGE,"E423");var subQ161=sQuery(id+"F0.wireOp",EDGE,"E422");var subQ162=sQuery(id+"F0.wireOp",EDGE,"E421");var subQ163=sQuery(id+"F0.wireOp",EDGE,"E420");var subQ164=sQuery(id+"F0.wireOp",EDGE,"E419");var subQ165=sQuery(id+"F0.wireOp",EDGE,"E418");var subQ166=sQuery(id+"F0.wireOp",EDGE,"E417");var subQ167=sQuery(id+"F0.wireOp",EDGE,"E416");var subQ168=sQuery(id+"F0.wireOp",EDGE,"E415");var subQ169=sQuery(id+"F0.wireOp",EDGE,"E414");var subQ170=sQuery(id+"F0.wireOp",EDGE,"E413");var subQ171=sQuery(id+"F0.wireOp",EDGE,"E412");var subQ172=sQuery(id+"F0.wireOp",EDGE,"E411");var subQ173=sQuery(id+"F0.wireOp",EDGE,"E410");var subQ174=sQuery(id+"F0.wireOp",EDGE,"E409");var subQ175=sQuery(id+"F0.wireOp",EDGE,"E408");var subQ176=sQuery(id+"F0.wireOp",EDGE,"E407");var subQ177=sQuery(id+"F0.wireOp",EDGE,"E406");var subQ178=sQuery(id+"F0.wireOp",EDGE,"E405");var subQ179=sQuery(id+"F0.wireOp",EDGE,"E404");var subQ180=sQuery(id+"F0.wireOp",EDGE,"E403");var subQ181=sQuery(id+"F0.wireOp",EDGE,"E402");var subQ182=sQuery(id+"F0.wireOp",EDGE,"E401");var subQ183=sQuery(id+"F0.wireOp",EDGE,"E400");var subQ184=sQuery(id+"F0.wireOp",EDGE,"E399");var subQ185=sQuery(id+"F0.wireOp",EDGE,"E398");var subQ186=sQuery(id+"F0.wireOp",EDGE,"E397");var subQ187=sQuery(id+"F0.wireOp",EDGE,"E396");var subQ188=sQuery(id+"F0.wireOp",EDGE,"E395");var subQ189=sQuery(id+"F0.wireOp",EDGE,"E394");var subQ190=sQuery(id+"F0.wireOp",EDGE,"E393");var subQ191=sQuery(id+"F0.wireOp",EDGE,"E392");var subQ192=sQuery(id+"F0.wireOp",EDGE,"E391");var subQ193=sQuery(id+"F0.wireOp",EDGE,"E390");var subQ194=sQuery(id+"F0.wireOp",EDGE,"E389");var subQ195=sQuery(id+"F0.wireOp",EDGE,"E388");var subQ196=sQuery(id+"F0.wireOp",EDGE,"E387");var subQ197=sQuery(id+"F0.wireOp",EDGE,"E386");var subQ198=sQuery(id+"F0.wireOp",EDGE,"E385");var subQ199=sQuery(id+"F0.wireOp",EDGE,"E384");var subQ200=sQuery(id+"F0.wireOp",EDGE,"E383");var subQ201=sQuery(id+"F0.wireOp",EDGE,"E382");var subQ202=sQuery(id+"F0.wireOp",EDGE,"E381");var subQ203=sQuery(id+"F0.wireOp",EDGE,"E380");var subQ204=sQuery(id+"F0.wireOp",EDGE,"E379");var subQ205=sQuery(id+"F0.wireOp",EDGE,"E378");var subQ206=sQuery(id+"F0.wireOp",EDGE,"E377");var subQ207=sQuery(id+"F0.wireOp",EDGE,"E376");var subQ208=sQuery(id+"F0.wireOp",EDGE,"E375");var subQ209=sQuery(id+"F0.wireOp",EDGE,"E374");var subQ210=sQuery(id+"F0.wireOp",EDGE,"E373");var subQ211=sQuery(id+"F0.wireOp",EDGE,"E372");var subQ212=sQuery(id+"F0.wireOp",EDGE,"E371");var subQ213=sQuery(id+"F0.wireOp",EDGE,"E370");var subQ214=sQuery(id+"F0.wireOp",EDGE,"E369");var subQ215=sQuery(id+"F0.wireOp",EDGE,"E368");var subQ216=sQuery(id+"F0.wireOp",EDGE,"E367");var subQ217=sQuery(id+"F0.wireOp",EDGE,"E366");var subQ218=sQuery(id+"F0.wireOp",EDGE,"E365");var subQ219=sQuery(id+"F0.wireOp",EDGE,"E364");var subQ220=sQuery(id+"F0.wireOp",EDGE,"E363");var subQ221=sQuery(id+"F0.wireOp",EDGE,"E362");var subQ222=sQuery(id+"F0.wireOp",EDGE,"E361");var subQ223=sQuery(id+"F0.wireOp",EDGE,"E360");var subQ224=sQuery(id+"F0.wireOp",EDGE,"E359");var subQ225=sQuery(id+"F0.wireOp",EDGE,"E358");var subQ226=sQuery(id+"F0.wireOp",EDGE,"E357");var subQ227=sQuery(id+"F0.wireOp",EDGE,"E356");var subQ228=sQuery(id+"F0.wireOp",EDGE,"E355");var subQ229=sQuery(id+"F0.wireOp",EDGE,"E354");var subQ230=sQuery(id+"F0.wireOp",EDGE,"E353");var subQ231=sQuery(id+"F0.wireOp",EDGE,"E352");var subQ232=sQuery(id+"F0.wireOp",EDGE,"E351");var subQ233=sQuery(id+"F0.wireOp",EDGE,"E350");var subQ234=sQuery(id+"F0.wireOp",EDGE,"E349");var subQ235=sQuery(id+"F0.wireOp",EDGE,"E348");var subQ236=sQuery(id+"F0.wireOp",EDGE,"E347");var subQ237=sQuery(id+"F0.wireOp",EDGE,"E346");var subQ238=sQuery(id+"F0.wireOp",EDGE,"E345");var subQ239=sQuery(id+"F0.wireOp",EDGE,"E344");var subQ240=sQuery(id+"F0.wireOp",EDGE,"E343");var subQ241=sQuery(id+"F0.wireOp",EDGE,"E342");var subQ242=sQuery(id+"F0.wireOp",EDGE,"E339");var subQ243=sQuery(id+"F0.wireOp",EDGE,"E338");var subQ244=sQuery(id+"F0.wireOp",EDGE,"E337");var subQ245=sQuery(id+"F0.wireOp",EDGE,"E336");var subQ246=sQuery(id+"F0.wireOp",EDGE,"E335");var subQ247=sQuery(id+"F0.wireOp",EDGE,"E334");var subQ248=sQuery(id+"F0.wireOp",EDGE,"E333");var subQ249=sQuery(id+"F0.wireOp",EDGE,"E332");var subQ250=sQuery(id+"F0.wireOp",EDGE,"E331");var subQ251=sQuery(id+"F0.wireOp",EDGE,"E330");var subQ252=sQuery(id+"F0.wireOp",EDGE,"E329");var subQ253=sQuery(id+"F0.wireOp",EDGE,"E328");var subQ254=sQuery(id+"F0.wireOp",EDGE,"E327");var subQ255=sQuery(id+"F0.wireOp",EDGE,"E326");var subQ256=sQuery(id+"F0.wireOp",EDGE,"E325");var subQ257=sQuery(id+"F0.wireOp",EDGE,"E324");var subQ258=sQuery(id+"F0.wireOp",EDGE,"E323");var subQ259=sQuery(id+"F0.wireOp",EDGE,"E322");var subQ260=sQuery(id+"F0.wireOp",EDGE,"E321");var subQ261=sQuery(id+"F0.wireOp",EDGE,"E320");var subQ262=sQuery(id+"F0.wireOp",EDGE,"E319");var subQ263=sQuery(id+"F0.wireOp",EDGE,"E318");var subQ264=sQuery(id+"F0.wireOp",EDGE,"E317");var subQ265=sQuery(id+"F0.wireOp",EDGE,"E316");var subQ266=sQuery(id+"F0.wireOp",EDGE,"E315");var subQ267=sQuery(id+"F0.wireOp",EDGE,"E314");var subQ268=sQuery(id+"F0.wireOp",EDGE,"E313");var subQ269=sQuery(id+"F0.wireOp",EDGE,"E312");var subQ270=sQuery(id+"F0.wireOp",EDGE,"E311");var subQ271=sQuery(id+"F0.wireOp",EDGE,"E310");var subQ272=sQuery(id+"F0.wireOp",EDGE,"E309");var subQ273=sQuery(id+"F0.wireOp",EDGE,"E308");var subQ274=sQuery(id+"F0.wireOp",EDGE,"E307");var subQ275=sQuery(id+"F0.wireOp",EDGE,"E306");var subQ276=sQuery(id+"F0.wireOp",EDGE,"E305");var subQ277=sQuery(id+"F0.wireOp",EDGE,"E304");var subQ278=sQuery(id+"F0.wireOp",EDGE,"E303");var subQ279=sQuery(id+"F0.wireOp",EDGE,"E302");var subQ280=sQuery(id+"F0.wireOp",EDGE,"E301");var subQ281=sQuery(id+"F0.wireOp",EDGE,"E300");var subQ282=sQuery(id+"F0.wireOp",EDGE,"E299");var subQ283=sQuery(id+"F0.wireOp",EDGE,"E298");var subQ284=sQuery(id+"F0.wireOp",EDGE,"E297");var subQ285=sQuery(id+"F0.wireOp",EDGE,"E296");var subQ286=sQuery(id+"F0.wireOp",EDGE,"E295");var subQ287=sQuery(id+"F0.wireOp",EDGE,"E294");var subQ288=sQuery(id+"F0.wireOp",EDGE,"E293");var subQ289=sQuery(id+"F0.wireOp",EDGE,"E292");var subQ290=sQuery(id+"F0.wireOp",EDGE,"E291");var subQ291=sQuery(id+"F0.wireOp",EDGE,"E290");var subQ292=sQuery(id+"F0.wireOp",EDGE,"E289");var subQ293=sQuery(id+"F0.wireOp",EDGE,"E288");var subQ294=sQuery(id+"F0.wireOp",EDGE,"E287");var subQ295=sQuery(id+"F0.wireOp",EDGE,"E286");var subQ296=sQuery(id+"F0.wireOp",EDGE,"E285");var subQ297=sQuery(id+"F0.wireOp",EDGE,"E284");var subQ298=sQuery(id+"F0.wireOp",EDGE,"E283");var subQ299=sQuery(id+"F0.wireOp",EDGE,"E282");var subQ300=sQuery(id+"F0.wireOp",EDGE,"E281");var subQ301=sQuery(id+"F0.wireOp",EDGE,"E280");var subQ302=sQuery(id+"F0.wireOp",EDGE,"E279");var subQ303=sQuery(id+"F0.wireOp",EDGE,"E278");var subQ304=sQuery(id+"F0.wireOp",EDGE,"E277");var subQ305=sQuery(id+"F0.wireOp",EDGE,"E276");var subQ306=sQuery(id+"F0.wireOp",EDGE,"E275");var subQ307=sQuery(id+"F0.wireOp",EDGE,"E274");var subQ308=sQuery(id+"F0.wireOp",EDGE,"E273");var subQ309=sQuery(id+"F0.wireOp",EDGE,"E272");var subQ310=sQuery(id+"F0.wireOp",EDGE,"E271");var subQ311=sQuery(id+"F0.wireOp",EDGE,"E270");var subQ312=sQuery(id+"F0.wireOp",EDGE,"E269");var subQ313=sQuery(id+"F0.wireOp",EDGE,"E268");var subQ314=sQuery(id+"F0.wireOp",EDGE,"E267");var subQ315=sQuery(id+"F0.wireOp",EDGE,"E266");var subQ316=sQuery(id+"F0.wireOp",EDGE,"E265");var subQ317=sQuery(id+"F0.wireOp",EDGE,"E264");var subQ318=sQuery(id+"F0.wireOp",EDGE,"E263");var subQ319=sQuery(id+"F0.wireOp",EDGE,"E262");var subQ320=sQuery(id+"F0.wireOp",EDGE,"E261");var subQ321=sQuery(id+"F0.wireOp",EDGE,"E260");var subQ322=sQuery(id+"F0.wireOp",EDGE,"E259");var subQ323=sQuery(id+"F0.wireOp",EDGE,"E258");var subQ324=sQuery(id+"F0.wireOp",EDGE,"E257");var subQ325=sQuery(id+"F0.wireOp",EDGE,"E256");var subQ326=sQuery(id+"F0.wireOp",EDGE,"E255");var subQ327=sQuery(id+"F0.wireOp",EDGE,"E254");var subQ328=sQuery(id+"F0.wireOp",EDGE,"E253");var subQ329=sQuery(id+"F0.wireOp",EDGE,"E252");var subQ330=sQuery(id+"F0.wireOp",EDGE,"E251");var subQ331=sQuery(id+"F0.wireOp",EDGE,"E250");var subQ332=sQuery(id+"F0.wireOp",EDGE,"E249");var subQ333=sQuery(id+"F0.wireOp",EDGE,"E248");var subQ334=sQuery(id+"F0.wireOp",EDGE,"E247");var subQ335=sQuery(id+"F0.wireOp",EDGE,"E246");var subQ336=sQuery(id+"F0.wireOp",EDGE,"E245");var subQ337=sQuery(id+"F0.wireOp",EDGE,"E244");var subQ338=sQuery(id+"F0.wireOp",EDGE,"E243");var subQ339=sQuery(id+"F0.wireOp",EDGE,"E242");var subQ340=sQuery(id+"F0.wireOp",EDGE,"E241");var subQ341=sQuery(id+"F0.wireOp",EDGE,"E240");var subQ342=sQuery(id+"F0.wireOp",EDGE,"E239");var subQ343=sQuery(id+"F0.wireOp",EDGE,"E238");var subQ344=sQuery(id+"F0.wireOp",EDGE,"E237");var subQ345=sQuery(id+"F0.wireOp",EDGE,"E236");var subQ346=sQuery(id+"F0.wireOp",EDGE,"E235");var subQ347=sQuery(id+"F0.wireOp",EDGE,"E234");var subQ348=sQuery(id+"F0.wireOp",EDGE,"E233");var subQ349=sQuery(id+"F0.wireOp",EDGE,"E232");var subQ350=sQuery(id+"F0.wireOp",EDGE,"E231");var subQ351=sQuery(id+"F0.wireOp",EDGE,"E230");var subQ352=sQuery(id+"F0.wireOp",EDGE,"E229");var subQ353=sQuery(id+"F0.wireOp",EDGE,"E228");var subQ354=sQuery(id+"F0.wireOp",EDGE,"E227");var subQ355=sQuery(id+"F0.wireOp",EDGE,"E226");var subQ356=sQuery(id+"F0.wireOp",EDGE,"E225");var subQ357=sQuery(id+"F0.wireOp",EDGE,"E224");var subQ358=sQuery(id+"F0.wireOp",EDGE,"E223");var subQ359=sQuery(id+"F0.wireOp",EDGE,"E222");var subQ360=sQuery(id+"F0.wireOp",EDGE,"E221");var subQ361=sQuery(id+"F0.wireOp",EDGE,"E220");var subQ362=sQuery(id+"F0.wireOp",EDGE,"E219");var subQ363=sQuery(id+"F0.wireOp",EDGE,"E218");var subQ364=sQuery(id+"F0.wireOp",EDGE,"E217");var subQ365=sQuery(id+"F0.wireOp",EDGE,"E216");var subQ366=sQuery(id+"F0.wireOp",EDGE,"E215");var subQ367=sQuery(id+"F0.wireOp",EDGE,"E214");var subQ368=sQuery(id+"F0.wireOp",EDGE,"E213");var subQ369=sQuery(id+"F0.wireOp",EDGE,"E212");var subQ370=sQuery(id+"F0.wireOp",EDGE,"E211");var subQ371=sQuery(id+"F0.wireOp",EDGE,"E210");var subQ372=sQuery(id+"F0.wireOp",EDGE,"E209");var subQ373=sQuery(id+"F0.wireOp",EDGE,"E208");var subQ374=sQuery(id+"F0.wireOp",EDGE,"E207");var subQ375=sQuery(id+"F0.wireOp",EDGE,"E206");var subQ376=sQuery(id+"F0.wireOp",EDGE,"E205");var subQ377=sQuery(id+"F0.wireOp",EDGE,"E204");var subQ378=sQuery(id+"F0.wireOp",EDGE,"E203");var subQ379=sQuery(id+"F0.wireOp",EDGE,"E202");var subQ380=sQuery(id+"F0.wireOp",EDGE,"E201");var subQ381=sQuery(id+"F0.wireOp",EDGE,"E200");var subQ382=sQuery(id+"F0.wireOp",EDGE,"E199");var subQ383=sQuery(id+"F0.wireOp",EDGE,"E198");var subQ384=sQuery(id+"F0.wireOp",EDGE,"E197");var subQ385=sQuery(id+"F0.wireOp",EDGE,"E196");var subQ386=sQuery(id+"F0.wireOp",EDGE,"E195");var subQ387=sQuery(id+"F0.wireOp",EDGE,"E194");var subQ388=sQuery(id+"F0.wireOp",EDGE,"E193");var subQ389=sQuery(id+"F0.wireOp",EDGE,"E192");var subQ390=sQuery(id+"F0.wireOp",EDGE,"E191");var subQ391=sQuery(id+"F0.wireOp",EDGE,"E190");var subQ392=sQuery(id+"F0.wireOp",EDGE,"E189");var subQ393=sQuery(id+"F0.wireOp",EDGE,"E188");var subQ394=sQuery(id+"F0.wireOp",EDGE,"E187");var subQ395=sQuery(id+"F0.wireOp",EDGE,"E186");var subQ396=sQuery(id+"F0.wireOp",EDGE,"E185");var subQ397=sQuery(id+"F0.wireOp",EDGE,"E184");var subQ398=sQuery(id+"F0.wireOp",EDGE,"E183");var subQ399=sQuery(id+"F0.wireOp",EDGE,"E182");var subQ400=sQuery(id+"F0.wireOp",EDGE,"E181");var subQ401=sQuery(id+"F0.wireOp",EDGE,"E180");var subQ402=sQuery(id+"F0.wireOp",EDGE,"E179");var subQ403=sQuery(id+"F0.wireOp",EDGE,"E178");var subQ404=sQuery(id+"F0.wireOp",EDGE,"E177");var subQ405=sQuery(id+"F0.wireOp",EDGE,"E176");var subQ406=sQuery(id+"F0.wireOp",EDGE,"E175");var subQ407=sQuery(id+"F0.wireOp",EDGE,"E174");var subQ408=sQuery(id+"F0.wireOp",EDGE,"E173");var subQ409=sQuery(id+"F0.wireOp",EDGE,"E172");var subQ410=sQuery(id+"F0.wireOp",EDGE,"E171");var subQ411=sQuery(id+"F0.wireOp",EDGE,"E170");var subQ412=sQuery(id+"F0.wireOp",EDGE,"E169");var subQ413=sQuery(id+"F0.wireOp",EDGE,"E168");var subQ414=sQuery(id+"F0.wireOp",EDGE,"E167");var subQ415=sQuery(id+"F0.wireOp",EDGE,"E166");var subQ416=sQuery(id+"F0.wireOp",EDGE,"E165");var subQ417=sQuery(id+"F0.wireOp",EDGE,"E164");var subQ418=sQuery(id+"F0.wireOp",EDGE,"E163");var subQ419=sQuery(id+"F0.wireOp",EDGE,"E162");var subQ420=sQuery(id+"F0.wireOp",EDGE,"E161");var subQ421=sQuery(id+"F0.wireOp",EDGE,"E160");var subQ422=sQuery(id+"F0.wireOp",EDGE,"E159");var subQ423=sQuery(id+"F0.wireOp",EDGE,"E158");var subQ424=sQuery(id+"F0.wireOp",EDGE,"E157");var subQ425=sQuery(id+"F0.wireOp",EDGE,"E156");var subQ426=sQuery(id+"F0.wireOp",EDGE,"E155");var subQ427=sQuery(id+"F0.wireOp",EDGE,"E154");var subQ428=sQuery(id+"F0.wireOp",EDGE,"E153");var subQ429=sQuery(id+"F0.wireOp",EDGE,"E152");var subQ430=sQuery(id+"F0.wireOp",EDGE,"E151");var subQ431=sQuery(id+"F0.wireOp",EDGE,"E150");var subQ432=sQuery(id+"F0.wireOp",EDGE,"E149");var subQ433=sQuery(id+"F0.wireOp",EDGE,"E148");var subQ434=sQuery(id+"F0.wireOp",EDGE,"E147");var subQ435=sQuery(id+"F0.wireOp",EDGE,"E146");var subQ436=sQuery(id+"F0.wireOp",EDGE,"E145");var subQ437=sQuery(id+"F0.wireOp",EDGE,"E144");var subQ438=sQuery(id+"F0.wireOp",EDGE,"E143");var subQ439=sQuery(id+"F0.wireOp",EDGE,"E142");var subQ440=sQuery(id+"F0.wireOp",EDGE,"E141");var subQ441=sQuery(id+"F0.wireOp",EDGE,"E140");var subQ442=sQuery(id+"F0.wireOp",EDGE,"E139");var subQ443=sQuery(id+"F0.wireOp",EDGE,"E138");var subQ444=sQuery(id+"F0.wireOp",EDGE,"E137");var subQ445=sQuery(id+"F0.wireOp",EDGE,"E136");var subQ446=sQuery(id+"F0.wireOp",EDGE,"E135");var subQ447=sQuery(id+"F0.wireOp",EDGE,"E134");var subQ448=sQuery(id+"F0.wireOp",EDGE,"E133");var subQ449=sQuery(id+"F0.wireOp",EDGE,"E132");var subQ450=sQuery(id+"F0.wireOp",EDGE,"E131");var subQ451=sQuery(id+"F0.wireOp",EDGE,"E130");var subQ452=sQuery(id+"F0.wireOp",EDGE,"E129");var subQ453=sQuery(id+"F0.wireOp",EDGE,"E128");var subQ454=sQuery(id+"F0.wireOp",EDGE,"E127");var subQ455=sQuery(id+"F0.wireOp",EDGE,"E126");var subQ456=sQuery(id+"F0.wireOp",EDGE,"E125");var subQ457=sQuery(id+"F0.wireOp",EDGE,"E124");var subQ458=sQuery(id+"F0.wireOp",EDGE,"E123");var subQ459=sQuery(id+"F0.wireOp",EDGE,"E122");var subQ460=sQuery(id+"F0.wireOp",EDGE,"E121");var subQ461=sQuery(id+"F0.wireOp",EDGE,"E120");var subQ462=sQuery(id+"F0.wireOp",EDGE,"E119");var subQ463=sQuery(id+"F0.wireOp",EDGE,"E118");var subQ464=sQuery(id+"F0.wireOp",EDGE,"E117");var subQ465=sQuery(id+"F0.wireOp",EDGE,"E116");var subQ466=sQuery(id+"F0.wireOp",EDGE,"E115");var subQ467=sQuery(id+"F0.wireOp",EDGE,"E114");var subQ468=sQuery(id+"F0.wireOp",EDGE,"E113");var subQ469=sQuery(id+"F0.wireOp",EDGE,"E112");var subQ470=sQuery(id+"F0.wireOp",EDGE,"E111");var subQ471=sQuery(id+"F0.wireOp",EDGE,"E110");var subQ472=sQuery(id+"F0.wireOp",EDGE,"E109");var subQ473=sQuery(id+"F0.wireOp",EDGE,"E108");var subQ474=sQuery(id+"F0.wireOp",EDGE,"E107");var subQ475=sQuery(id+"F0.wireOp",EDGE,"E106");var subQ476=sQuery(id+"F0.wireOp",EDGE,"E105");var subQ477=sQuery(id+"F0.wireOp",EDGE,"E104");var subQ478=sQuery(id+"F0.wireOp",EDGE,"E103");var subQ479=sQuery(id+"F0.wireOp",EDGE,"E102");var subQ480=sQuery(id+"F0.wireOp",EDGE,"E101");var subQ481=sQuery(id+"F0.wireOp",EDGE,"E100");var subQ482=sQuery(id+"F0.wireOp",EDGE,"E99");var subQ483=sQuery(id+"F0.wireOp",EDGE,"E98");var subQ484=sQuery(id+"F0.wireOp",EDGE,"E97");var subQ485=sQuery(id+"F0.wireOp",EDGE,"E96");var subQ486=sQuery(id+"F0.wireOp",EDGE,"E95");var subQ487=sQuery(id+"F0.wireOp",EDGE,"E94");var subQ488=sQuery(id+"F0.wireOp",EDGE,"E93");var subQ489=sQuery(id+"F0.wireOp",EDGE,"E92");var subQ490=sQuery(id+"F0.wireOp",EDGE,"E91");var subQ491=sQuery(id+"F0.wireOp",EDGE,"E90");var subQ492=sQuery(id+"F0.wireOp",EDGE,"E89");var subQ493=sQuery(id+"F0.wireOp",EDGE,"E88");var subQ494=sQuery(id+"F0.wireOp",EDGE,"E87");var subQ495=sQuery(id+"F0.wireOp",EDGE,"E86");var subQ496=sQuery(id+"F0.wireOp",EDGE,"E85");var subQ497=sQuery(id+"F0.wireOp",EDGE,"E84");var subQ498=sQuery(id+"F0.wireOp",EDGE,"E83");var subQ499=sQuery(id+"F0.wireOp",EDGE,"E82");var subQ500=sQuery(id+"F0.wireOp",EDGE,"E81");var subQ501=sQuery(id+"F0.wireOp",EDGE,"E80");var subQ502=sQuery(id+"F0.wireOp",EDGE,"E79");var subQ503=sQuery(id+"F0.wireOp",EDGE,"E78");var subQ504=sQuery(id+"F0.wireOp",EDGE,"E77");var subQ505=sQuery(id+"F0.wireOp",EDGE,"E76");var subQ506=sQuery(id+"F0.wireOp",EDGE,"E75");var subQ507=sQuery(id+"F0.wireOp",EDGE,"E74");var subQ508=sQuery(id+"F0.wireOp",EDGE,"E73");var subQ509=sQuery(id+"F0.wireOp",EDGE,"E72");var subQ510=sQuery(id+"F0.wireOp",EDGE,"E71");var subQ511=sQuery(id+"F0.wireOp",EDGE,"E70");var subQ512=sQuery(id+"F0.wireOp",EDGE,"E69");var subQ513=sQuery(id+"F0.wireOp",EDGE,"E68");var subQ514=sQuery(id+"F0.wireOp",EDGE,"E67");var subQ515=sQuery(id+"F0.wireOp",EDGE,"E66");var subQ516=sQuery(id+"F0.wireOp",EDGE,"E65");var subQ517=sQuery(id+"F0.wireOp",EDGE,"E64");var subQ518=sQuery(id+"F0.wireOp",EDGE,"E63");var subQ519=sQuery(id+"F0.wireOp",EDGE,"E62");var subQ520=sQuery(id+"F0.wireOp",EDGE,"E61");var subQ521=sQuery(id+"F0.wireOp",EDGE,"E60");var subQ522=sQuery(id+"F0.wireOp",EDGE,"E59");var subQ523=sQuery(id+"F0.wireOp",EDGE,"E58");var subQ524=sQuery(id+"F0.wireOp",EDGE,"E57");var subQ525=sQuery(id+"F0.wireOp",EDGE,"E56");var subQ526=sQuery(id+"F0.wireOp",EDGE,"E55");var subQ527=sQuery(id+"F0.wireOp",EDGE,"E54");var subQ528=sQuery(id+"F0.wireOp",EDGE,"E53");var subQ529=sQuery(id+"F0.wireOp",EDGE,"E52");var subQ530=sQuery(id+"F0.wireOp",EDGE,"E51");var subQ531=sQuery(id+"F0.wireOp",EDGE,"E50");var subQ532=sQuery(id+"F0.wireOp",EDGE,"E49");var subQ533=sQuery(id+"F0.wireOp",EDGE,"E48");var subQ534=sQuery(id+"F0.wireOp",EDGE,"E47");var subQ535=sQuery(id+"F0.wireOp",EDGE,"E46");var subQ536=sQuery(id+"F0.wireOp",EDGE,"E45");var subQ537=sQuery(id+"F0.wireOp",EDGE,"E44");var subQ538=sQuery(id+"F0.wireOp",EDGE,"E43");var subQ539=sQuery(id+"F0.wireOp",EDGE,"E42");var subQ540=sQuery(id+"F0.wireOp",EDGE,"E41");var subQ541=sQuery(id+"F0.wireOp",EDGE,"E40");var subQ542=sQuery(id+"F0.wireOp",EDGE,"E39");var subQ543=sQuery(id+"F0.wireOp",EDGE,"E38");var subQ544=sQuery(id+"F0.wireOp",EDGE,"E37");var subQ545=sQuery(id+"F0.wireOp",EDGE,"E36");var subQ546=sQuery(id+"F0.wireOp",EDGE,"E35");var subQ547=sQuery(id+"F0.wireOp",EDGE,"E34");var subQ548=sQuery(id+"F0.wireOp",EDGE,"E33");var subQ549=sQuery(id+"F0.wireOp",EDGE,"E32");var subQ550=sQuery(id+"F0.wireOp",EDGE,"E31");var subQ551=sQuery(id+"F0.wireOp",EDGE,"E30");var subQ552=sQuery(id+"F0.wireOp",EDGE,"E29");var subQ553=sQuery(id+"F0.wireOp",EDGE,"E28");var subQ554=sQuery(id+"F0.wireOp",EDGE,"E27");var subQ555=sQuery(id+"F0.wireOp",EDGE,"E26");var subQ556=sQuery(id+"F0.wireOp",EDGE,"E25");var subQ557=sQuery(id+"F0.wireOp",EDGE,"E24");var subQ558=sQuery(id+"F0.wireOp",EDGE,"E23");var subQ559=sQuery(id+"F0.wireOp",EDGE,"E22");var subQ560=sQuery(id+"F0.wireOp",EDGE,"E21");var subQ561=sQuery(id+"F0.wireOp",EDGE,"E20");var subQ562=sQuery(id+"F0.wireOp",EDGE,"E19");var subQ563=sQuery(id+"F0.wireOp",EDGE,"E18");var subQ564=sQuery(id+"F0.wireOp",EDGE,"E17");var subQ565=sQuery(id+"F0.wireOp",EDGE,"E16");var subQ566=sQuery(id+"F0.wireOp",EDGE,"E15");var subQ567=sQuery(id+"F0.wireOp",EDGE,"E14");var subQ568=sQuery(id+"F0.wireOp",EDGE,"E13");var subQ569=sQuery(id+"F0.wireOp",EDGE,"E12");var subQ570=sQuery(id+"F0.wireOp",EDGE,"E11");var subQ571=sQuery(id+"F0.wireOp",EDGE,"E10");var subQ572=sQuery(id+"F0.wireOp",EDGE,"E9");var subQ573=sQuery(id+"F0.wireOp",EDGE,"E8");var subQ574=sQuery(id+"F0.wireOp",EDGE,"E7");var subQ575=sQuery(id+"F0.wireOp",EDGE,"E6");var subQ576=sQuery(id+"F0.wireOp",EDGE,"E5");var subQ577=sQuery(id+"F0.wireOp",EDGE,"E4");var subQ578=sQuery(id+"F0.wireOp",EDGE,"E3");var subQ579=sQuery(id+"F0.wireOp",EDGE,"E2");var subQ580=sQuery(id+"F0.wireOp",EDGE,"E1");var subQ581=sQuery(id+"F0.wireOp",EDGE,"E0");Q0=makeQuery(id+"F19.boolean.opBoolean","MERGE",FACE,{"derivedFrom":[makeQuery(id+"F10.boolean.opBoolean","SPLIT",FACE,{"disambiguationData":[TD([makeQuery(id+"F1.opExtrude","SWEPT_FACE",FACE,{"disambiguationData":[OSD([subQ1])]})])],"derivedFrom":makeQuery(id+"F1.opExtrude","CAP_FACE",FACE,{"disambiguationData":[OSD([subQ581,subQ580,subQ579,subQ578,subQ577,subQ576,subQ575,subQ574,subQ573,subQ572,subQ571,subQ570,subQ569,subQ568,subQ567,subQ566,subQ565,subQ564,subQ563,subQ562,subQ561,subQ560,subQ559,subQ558,subQ557,subQ556,subQ555,subQ554,subQ553,subQ552,subQ551,subQ550,subQ549,subQ548,subQ547,subQ546,subQ545,subQ544,subQ543,subQ542,subQ541,subQ540,subQ539,subQ538,subQ537,subQ536,subQ535,subQ534,subQ533,subQ532,subQ531,subQ530,subQ529,subQ528,subQ527,subQ526,subQ525,subQ524,subQ523,subQ522,subQ521,subQ520,subQ519,subQ518,subQ517,subQ516,subQ515,subQ514,subQ513,subQ512,subQ511,subQ510,subQ509,subQ508,subQ507,subQ506,subQ505,subQ504,subQ503,subQ502,subQ501,subQ500,subQ499,subQ498,subQ497,subQ496,subQ495,subQ494,subQ493,subQ492,subQ491,subQ490,subQ489,subQ488,subQ487,subQ486,subQ485,subQ484,subQ483,subQ482,subQ481,subQ480,subQ479,subQ478,subQ477,subQ476,subQ475,subQ474,subQ473,subQ472,subQ471,subQ470,subQ469,subQ468,subQ467,subQ466,subQ465,subQ464,subQ463,subQ462,subQ461,subQ460,subQ459,subQ458,subQ457,subQ456,subQ455,subQ454,subQ453,subQ452,subQ451,subQ450,subQ449,subQ448,subQ447,subQ446,subQ445,subQ444,subQ443,subQ442,subQ441,subQ440,subQ439,subQ438,subQ437,subQ436,subQ435,subQ434,subQ433,subQ432,subQ431,subQ430,subQ429,subQ428,subQ427,subQ426,subQ425,subQ424,subQ423,subQ422,subQ421,subQ420,subQ419,subQ418,subQ417,subQ416,subQ415,subQ414,subQ413,subQ412,subQ411,subQ410,subQ409,subQ408,subQ407,subQ406,subQ405,subQ404,subQ403,subQ402,subQ401,subQ400,subQ399,subQ398,subQ397,subQ396,subQ395,subQ394,subQ393,subQ392,subQ391,subQ390,subQ389,subQ388,subQ387,subQ386,subQ385,subQ384,subQ383,subQ382,subQ381,subQ380,subQ379,subQ378,subQ377,subQ376,subQ375,subQ374,subQ373,subQ372,subQ371,subQ370,subQ369,subQ368,subQ367,subQ366,subQ365,subQ364,subQ363,subQ362,subQ361,subQ360,subQ359,subQ358,subQ357,subQ356,subQ355,subQ354,subQ353,subQ352,subQ351,subQ350,subQ349,subQ348,subQ347,subQ346,subQ345,subQ344,subQ343,subQ342,subQ341,subQ340,subQ339,subQ338,subQ337,subQ336,subQ335,subQ334,subQ333,subQ332,subQ331,subQ330,subQ329,subQ328,subQ327,subQ326,subQ325,subQ324,subQ323,subQ322,subQ321,subQ320,subQ319,subQ318,subQ317,subQ316,subQ315,subQ314,subQ313,subQ312,subQ311,subQ310,subQ309,subQ308,subQ307,subQ306,subQ305,subQ304,subQ303,subQ302,subQ301,subQ300,subQ299,subQ298,subQ297,subQ296,subQ295,subQ294,subQ293,subQ292,subQ291,subQ290,subQ289,subQ288,subQ287,subQ286,subQ285,subQ284,subQ283,subQ282,subQ281,subQ280,subQ279,subQ278,subQ277,subQ276,subQ275,subQ274,subQ273,subQ272,subQ271,subQ270,subQ269,subQ268,subQ267,subQ266,subQ265,subQ264,subQ263,subQ262,subQ261,subQ260,subQ259,subQ258,subQ257,subQ256,subQ255,subQ254,subQ253,subQ252,subQ251,subQ250,subQ249,subQ248,subQ247,subQ246,subQ245,subQ244,subQ243,subQ242,subQ1,subQ0,subQ241,subQ240,subQ239,subQ238,subQ237,subQ236,subQ235,subQ234,subQ233,subQ232,subQ231,subQ230,subQ229,subQ228,subQ227,subQ226,subQ225,subQ224,subQ223,subQ222,subQ221,subQ220,subQ219,subQ218,subQ217,subQ216,subQ215,subQ214,subQ213,subQ212,subQ211,subQ210,subQ209,subQ208,subQ207,subQ206,subQ205,subQ204,subQ203,subQ202,subQ201,subQ200,subQ199,subQ198,subQ197,subQ196,subQ195,subQ194,subQ193,subQ192,subQ191,subQ190,subQ189,subQ188,subQ187,subQ186,subQ185,subQ184,subQ183,subQ182,subQ181,subQ180,subQ179,subQ178,subQ177,subQ176,subQ175,subQ174,subQ173,subQ172,subQ171,subQ170,subQ169,subQ168,subQ167,subQ166,subQ165,subQ164,subQ163,subQ162,subQ161,subQ160,subQ159,subQ158,subQ157,subQ156,subQ155,subQ154,subQ153,subQ152,subQ151,subQ150,subQ149,subQ148,subQ147,subQ146,subQ145,subQ144,subQ143,subQ142,subQ141,subQ140,subQ139,subQ138,subQ137,subQ136,subQ135,subQ134,subQ133,subQ132,subQ131,subQ130,subQ129,subQ128,subQ127,subQ126,subQ125,subQ124,subQ123,subQ122,subQ121,subQ120,subQ119,subQ118,subQ117,subQ116,subQ115,subQ114,subQ113,subQ112,subQ111,subQ110,subQ109,subQ108,subQ107,subQ106,subQ105,subQ104,subQ103,subQ102,subQ101,subQ100,subQ99,subQ98,subQ97,subQ96,subQ95,subQ94,subQ93,subQ92,subQ91,subQ90,subQ89,subQ88,subQ87,subQ86,subQ85,subQ84,subQ83,subQ82,subQ81,subQ80,subQ79,subQ78,subQ77,subQ76,subQ75,subQ74,subQ73,subQ72,subQ71,subQ70,subQ69,subQ68,subQ67,subQ66,subQ65,subQ64,subQ63,subQ62,subQ61,subQ60,subQ59,subQ58,subQ57,subQ56,subQ55,subQ54,subQ53,subQ52,subQ51,subQ50,subQ49,subQ48,subQ47,subQ46,subQ45,subQ44,subQ43,subQ42,subQ41,subQ40,subQ39,subQ38,subQ37,subQ36,subQ35,subQ34,subQ33,subQ32,subQ31,subQ30,subQ29,subQ28,subQ27,subQ26,subQ25,subQ24,subQ23,subQ22,subQ21,subQ20,subQ19,subQ18,subQ17,subQ16,subQ15,subQ14,subQ13,subQ12,subQ11,subQ10,subQ9,subQ8,subQ7,subQ6,subQ5,subQ4])],"isStart":false})}),makeQuery(id+"F19.opExtrude","CAP_FACE",FACE,{"disambiguationData":[OSD([sQuery(id+"F18.wireOp",EDGE,"E2048.0")])],"isStart":true})]});}
            var sketch = newSketch(context, id + "F20", { "sketchPlane" : qUnion([Q0])});
            skCircle(sketch, "E2049", {"center": v(-91.22, 0) * mm, "radius": 4 * mm});
            skSolve(sketch);
        }
        {
            var Q0;
            Q0 = qSketchRegion(id + "F20", true);
            extrude(context, id + "F21", {"entities" : qUnion([Q0]), "operationType" : NewBodyOperationType.REMOVE, "endBound" : BoundingType.THROUGH_ALL, "oppositeDirection" : true, "depth" : 25 * mm, "offsetDistance" : 25 * mm});
        }
    });
